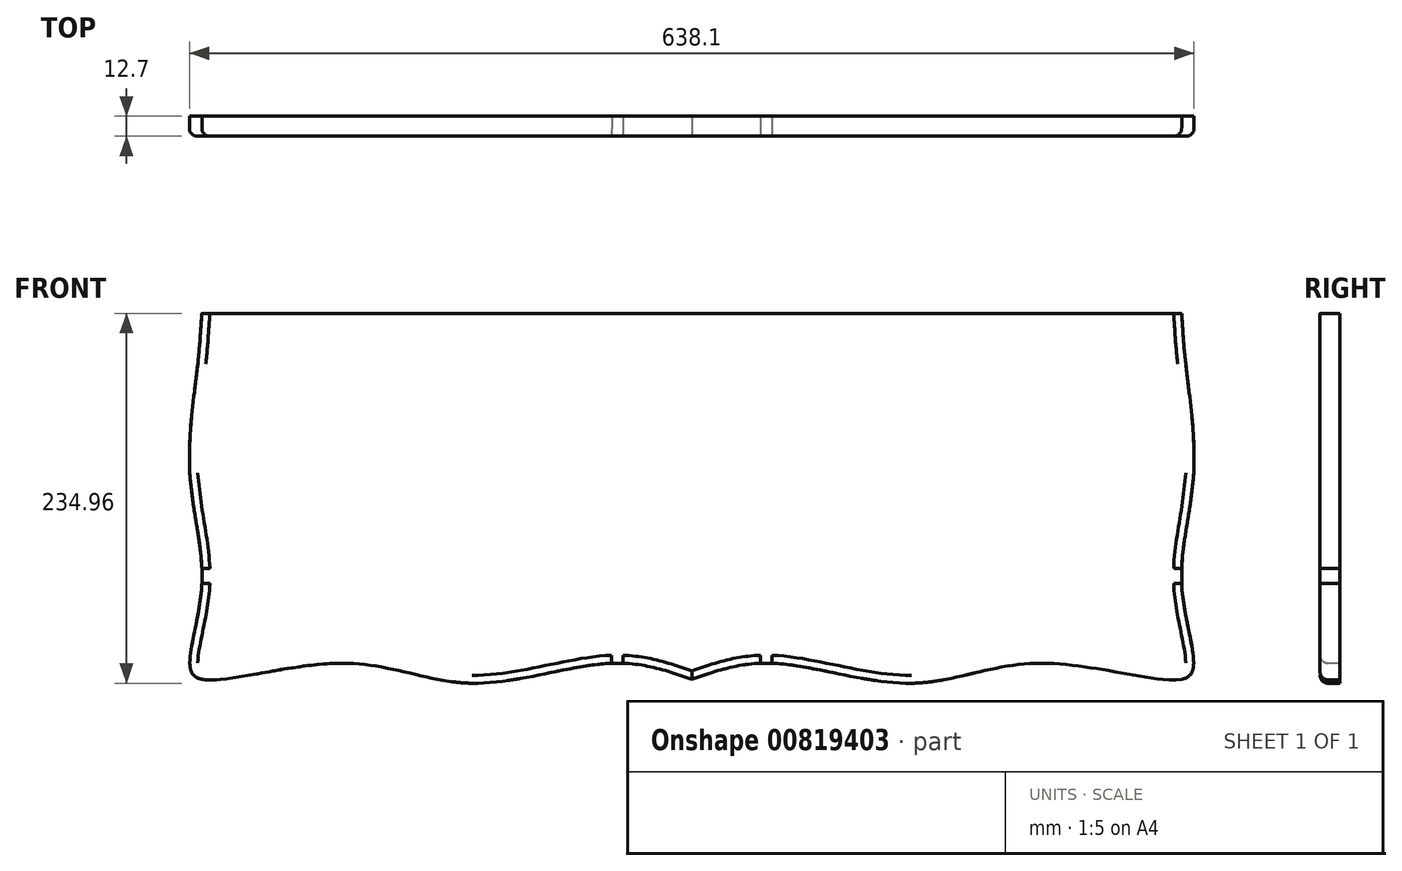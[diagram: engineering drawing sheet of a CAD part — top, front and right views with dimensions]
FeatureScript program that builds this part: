
annotation { "Feature Type Name" : "Feature", "Feature Type Description" : "" }
export const myFeature = defineFeature(function(context is Context, id is Id, definition is map)
    precondition{}
    {
        {
            var Q0;
            Q0=qCreatedBy(makeId("Front.planeOp"),FACE);
            var sketch = newSketch(context, id + "F0", { "sketchPlane" : qUnion([Q0])});
            skLineSegment(sketch, "E0.bottom", {"start": v(-290.57, 108.48) * mm, "end": v(331.73, 108.48) * mm});
            skLineSegment(sketch, "E0.top", {"start": v(-290.57, -113.77) * mm, "end": v(331.73, -113.77) * mm});
            skLineSegment(sketch, "E0.left", {"start": v(-290.57, 108.48) * mm, "end": v(-290.57, -113.77) * mm});
            skLineSegment(sketch, "E0.right", {"start": v(331.73, 108.48) * mm, "end": v(331.73, -113.77) * mm});
            skPoint(sketch, "E1", {"position": v(20.58, 108.48) * mm});
            skSolve(sketch);
        }
        {
            var Q0;
            Q0=makeQuery(id+"F0.imprint","IMPRINT",FACE,{"disambiguationData":[TD([[makeQuery(id+"F0.imprint","IMPRINT",EDGE,{"derivedFrom":sQuery(id+"F0.wireOp",EDGE,"E0.bottom")}),-1.0]])]});
            extrude(context, id + "F1", {"entities" : qUnion([Q0]), "depth" : 12.7 * mm, "offsetDistance" : 25.4 * mm});
        }
        {
            var Q0;
            Q0=makeQuery(id+"F1.opExtrude","CAP_FACE",FACE,{"disambiguationData":[OSD([sQuery(id+"F0.wireOp",EDGE,"E0.bottom"),sQuery(id+"F0.wireOp",EDGE,"E0.top"),sQuery(id+"F0.wireOp",EDGE,"E0.left"),sQuery(id+"F0.wireOp",EDGE,"E0.right")])],"isStart":false});
            var sketch = newSketch(context, id + "F2", { "sketchPlane" : qUnion([Q0])});
            skText(sketch, "E2", { "text": "Swimming", "fontName": "OpenSans-Bold.ttf"});
            skPoint(sketch, "E3", {"position": v(20.58, 108.48) * mm});
            const initialGuessF2  = {"E2": [-0.19905, 0.00392, 1, 0, 0.06017]};
            skSetInitialGuess(sketch, initialGuessF2);
            skSolve(sketch);
        }
        {
            var Q0;
            Q0=makeQuery(id+"F2.imprint","IMPRINT",FACE,{"disambiguationData":[TD([[makeQuery(id+"F2.imprint","IMPRINT",EDGE,{"derivedFrom":sQuery(id+"F2.wireOp",EDGE,"E2.sketch_text.stroke-0")}),1.0]])]});
            var sketch = newSketch(context, id + "F3", { "sketchPlane" : qUnion([Q0])});
            skText(sketch, "E4", { "text": " < silhouette >", "fontName": "OpenSans-Bold.ttf"});
            skPoint(sketch, "E5", {"position": v(20.58, -113.77) * mm});
            const initialGuessF3  = {"E4": [-0.15546, -0.06206, 1, 0, 0.03604]};
            skSetInitialGuess(sketch, initialGuessF3);
            skSolve(sketch);
        }
        {
            var Q0;
            {var subQ0=sQuery(id+"F0.wireOp",EDGE,"E0.right");var subQ1=sQuery(id+"F0.wireOp",EDGE,"E0.bottom");var subQ2=sQuery(id+"F0.wireOp",EDGE,"E0.left");var subQ3=sQuery(id+"F0.wireOp",EDGE,"E0.top");Q0=makeQuery(id+"FjgwLtvUwF4HY63_1.boolean.opBoolean","SPLIT",FACE,{"disambiguationData":[TD([makeQuery(id+"F1.opExtrude","SWEPT_FACE",FACE,{"disambiguationData":[OSD([subQ1])]})])],"derivedFrom":makeQuery(id+"F1.opExtrude","CAP_FACE",FACE,{"disambiguationData":[OSD([subQ1,subQ3,subQ2,subQ0])],"isStart":false})});}
            var sketch = newSketch(context, id + "F4", { "sketchPlane" : qUnion([Q0])});
            skPoint(sketch, "E6", {"position": v(-290.57, -62.97) * mm});
            skPoint(sketch, "E7", {"position": v(-290.57, 6.88) * mm});
            skPoint(sketch, "E8", {"position": v(-290.57, 76.73) * mm});
            skLineSegment(sketch, "E9", {"start": v(-290.57, 76.73) * mm, "end": v(-293.1, 76.73) * mm});
            skLineSegment(sketch, "E10", {"start": v(-290.57, 6.88) * mm, "end": v(-298.19, 6.88) * mm});
            skLineSegment(sketch, "E11", {"start": v(-290.57, -113.77) * mm, "end": v(-298.19, -113.77) * mm});
            skLineSegment(sketch, "E12", {"start": v(-290.57, -113.77) * mm, "end": v(-290.57, -123.93) * mm});
            skPoint(sketch, "E13", {"position": v(-201.67, -113.77) * mm});
            skPoint(sketch, "E14", {"position": v(20.58, -113.77) * mm});
            skPoint(sketch, "E15", {"position": v(-30.22, -113.77) * mm});
            skPoint(sketch, "E16", {"position": v(-119.12, -113.77) * mm});
            skPoint(sketch, "E17", {"position": v(71.38, -113.77) * mm});
            skPoint(sketch, "E18", {"position": v(160.28, -113.77) * mm});
            skPoint(sketch, "E19", {"position": v(242.83, -113.77) * mm});
            skPoint(sketch, "E20", {"position": v(331.73, -62.97) * mm});
            skPoint(sketch, "E21", {"position": v(331.73, 6.88) * mm});
            skPoint(sketch, "E22", {"position": v(331.73, 76.73) * mm});
            skLineSegment(sketch, "E23", {"start": v(331.73, 76.73) * mm, "end": v(334.27, 76.73) * mm});
            skLineSegment(sketch, "E24", {"start": v(331.73, 6.88) * mm, "end": v(339.35, 6.88) * mm});
            skLineSegment(sketch, "E25", {"start": v(331.73, -113.77) * mm, "end": v(339.35, -113.77) * mm});
            skLineSegment(sketch, "E26", {"start": v(331.73, -113.77) * mm, "end": v(331.73, -123.93) * mm});
            skLineSegment(sketch, "E27", {"start": v(-119.12, -113.77) * mm, "end": v(-119.12, -126.47) * mm});
            skLineSegment(sketch, "E28", {"start": v(20.58, -113.77) * mm, "end": v(20.58, -123.93) * mm});
            skLineSegment(sketch, "E29", {"start": v(160.28, -113.77) * mm, "end": v(160.28, -126.47) * mm});
            skFitSpline(sketch, "E30", {"points": [v(-290.57, 108.48) * mm, v(-293.1, 76.73) * mm, v(-298.19, 6.88) * mm, v(-290.57, -62.97) * mm, v(-298.19, -113.77) * mm, v(-290.57, -123.93) * mm, v(-201.67, -113.77) * mm, v(-119.12, -126.47) * mm, v(-30.22, -113.77) * mm, v(20.58, -123.93) * mm], "startDerivative": vector(-26.2, -341.82) * mm, "endDerivative": vector(438.15, -148.5) * mm});
            skFitSpline(sketch, "E31", {"points": [v(331.73, 108.48) * mm, v(334.27, 76.73) * mm, v(339.35, 6.88) * mm, v(331.73, -62.97) * mm, v(339.35, -113.77) * mm, v(331.73, -123.93) * mm, v(242.83, -113.77) * mm, v(160.28, -126.47) * mm, v(71.38, -113.77) * mm, v(20.58, -123.93) * mm], "startDerivative": vector(26.2, -341.82) * mm, "endDerivative": vector(-438.15, -148.5) * mm});
            skSolve(sketch);
        }
        {
            var Q0;
            {var subQ0=sQuery(id+"F4.wireOp",EDGE,"E28");Q0=makeQuery(id+"F4.imprint","IMPRINT",FACE,{"disambiguationData":[TD([[makeQuery(id+"F4.imprint","IMPRINT",EDGE,{"derivedFrom":subQ0}),-1.0]])]});}
            var Q1;
            {var subQ0=sQuery(id+"F4.wireOp",EDGE,"E28");Q1=makeQuery(id+"F4.imprint","IMPRINT",FACE,{"disambiguationData":[TD([[makeQuery(id+"F4.imprint","IMPRINT",EDGE,{"derivedFrom":subQ0}),1.0]])]});}
            var Q2;
            {var subQ0=sQuery(id+"F4.wireOp",EDGE,"E27");Q2=makeQuery(id+"F4.imprint","IMPRINT",FACE,{"disambiguationData":[TD([[makeQuery(id+"F4.imprint","IMPRINT",EDGE,{"derivedFrom":subQ0}),1.0]])]});}
            var Q3;
            {var subQ0=sQuery(id+"F4.wireOp",EDGE,"E27");Q3=makeQuery(id+"F4.imprint","IMPRINT",FACE,{"disambiguationData":[TD([[makeQuery(id+"F4.imprint","IMPRINT",EDGE,{"derivedFrom":subQ0}),-1.0]])]});}
            var Q4;
            {var subQ0=sQuery(id+"F4.wireOp",EDGE,"E12");Q4=makeQuery(id+"F4.imprint","IMPRINT",FACE,{"disambiguationData":[TD([[makeQuery(id+"F4.imprint","IMPRINT",EDGE,{"derivedFrom":subQ0}),1.0]])]});}
            var Q5;
            {var subQ0=sQuery(id+"F4.wireOp",EDGE,"E11");Q5=makeQuery(id+"F4.imprint","IMPRINT",FACE,{"disambiguationData":[TD([[makeQuery(id+"F4.imprint","IMPRINT",EDGE,{"derivedFrom":subQ0}),1.0]])]});}
            var Q6;
            {var subQ0=sQuery(id+"F4.wireOp",EDGE,"E11");Q6=makeQuery(id+"F4.imprint","IMPRINT",FACE,{"disambiguationData":[TD([[makeQuery(id+"F4.imprint","IMPRINT",EDGE,{"derivedFrom":subQ0}),-1.0]])]});}
            var Q7;
            {var subQ0=sQuery(id+"F4.wireOp",EDGE,"E10");Q7=makeQuery(id+"F4.imprint","IMPRINT",FACE,{"disambiguationData":[TD([[makeQuery(id+"F4.imprint","IMPRINT",EDGE,{"derivedFrom":subQ0}),1.0]])]});}
            var Q8;
            {var subQ0=sQuery(id+"F4.wireOp",EDGE,"E9");Q8=makeQuery(id+"F4.imprint","IMPRINT",FACE,{"disambiguationData":[TD([[makeQuery(id+"F4.imprint","IMPRINT",EDGE,{"derivedFrom":subQ0}),1.0]])]});}
            var Q9;
            {var subQ0=makeQuery(id+"F1.opExtrude","CAP_EDGE",EDGE,{"disambiguationData":[OSD([sQuery(id+"F0.wireOp",EDGE,"E0.bottom")])],"isStart":false});Q9=makeQuery(id+"F4.imprint","IMPRINT",FACE,{"disambiguationData":[TD([[makeQuery(id+"F4.imprint","IMPRINT",EDGE,{"derivedFrom":subQ0}),-1.0]])]});}
            var Q10;
            {var subQ0=sQuery(id+"F4.wireOp",EDGE,"E29");Q10=makeQuery(id+"F4.imprint","IMPRINT",FACE,{"disambiguationData":[TD([[makeQuery(id+"F4.imprint","IMPRINT",EDGE,{"derivedFrom":subQ0}),-1.0]])]});}
            var Q11;
            {var subQ0=sQuery(id+"F4.wireOp",EDGE,"E29");Q11=makeQuery(id+"F4.imprint","IMPRINT",FACE,{"disambiguationData":[TD([[makeQuery(id+"F4.imprint","IMPRINT",EDGE,{"derivedFrom":subQ0}),1.0]])]});}
            var Q12;
            {var subQ0=sQuery(id+"F4.wireOp",EDGE,"E26");Q12=makeQuery(id+"F4.imprint","IMPRINT",FACE,{"disambiguationData":[TD([[makeQuery(id+"F4.imprint","IMPRINT",EDGE,{"derivedFrom":subQ0}),-1.0]])]});}
            var Q13;
            {var subQ0=sQuery(id+"F4.wireOp",EDGE,"E25");Q13=makeQuery(id+"F4.imprint","IMPRINT",FACE,{"disambiguationData":[TD([[makeQuery(id+"F4.imprint","IMPRINT",EDGE,{"derivedFrom":subQ0}),-1.0]])]});}
            var Q14;
            {var subQ0=sQuery(id+"F4.wireOp",EDGE,"E25");Q14=makeQuery(id+"F4.imprint","IMPRINT",FACE,{"disambiguationData":[TD([[makeQuery(id+"F4.imprint","IMPRINT",EDGE,{"derivedFrom":subQ0}),1.0]])]});}
            var Q15;
            {var subQ0=sQuery(id+"F4.wireOp",EDGE,"E24");Q15=makeQuery(id+"F4.imprint","IMPRINT",FACE,{"disambiguationData":[TD([[makeQuery(id+"F4.imprint","IMPRINT",EDGE,{"derivedFrom":subQ0}),-1.0]])]});}
            var Q16;
            {var subQ0=sQuery(id+"F4.wireOp",EDGE,"E23");Q16=makeQuery(id+"F4.imprint","IMPRINT",FACE,{"disambiguationData":[TD([[makeQuery(id+"F4.imprint","IMPRINT",EDGE,{"derivedFrom":subQ0}),-1.0]])]});}
            var Q17;
            {var subQ0=sQuery(id+"F4.wireOp",EDGE,"E23");Q17=makeQuery(id+"F4.imprint","IMPRINT",FACE,{"disambiguationData":[TD([[makeQuery(id+"F4.imprint","IMPRINT",EDGE,{"derivedFrom":subQ0}),1.0]])]});}
            var Q18;
            {var subQ0=sQuery(id+"F4.wireOp",EDGE,"E9");Q18=makeQuery(id+"F4.imprint","IMPRINT",FACE,{"disambiguationData":[TD([[makeQuery(id+"F4.imprint","IMPRINT",EDGE,{"derivedFrom":subQ0}),-1.0]])]});}
            extrude(context, id + "F5", {"entities" : qUnion([Q0, Q1, Q2, Q3, Q4, Q5, Q6, Q7, Q8, Q9, Q10, Q11, Q12, Q13, Q14, Q15, Q16, Q17, Q18]), "operationType" : NewBodyOperationType.ADD, "depth" : -12.7 * mm, "offsetDistance" : 25.4 * mm});
        }
        {
            var Q0;
            {var subQ0=sQuery(id+"F4.wireOp",EDGE,"8007402e-1a4e-4a06-85a5-2af08e553504");var subQ1=sQuery(id+"F0.wireOp",EDGE,"E0.left");var subQ2=sQuery(id+"F0.wireOp",EDGE,"E0.top");var subQ3=sQuery(id+"F0.wireOp",EDGE,"E0.bottom");Q0=makeQuery(id+"F5.boolean.opBoolean","SPLIT",EDGE,{"disambiguationData":[TD([makeQuery(id+"F1.opExtrude","CAP_FACE",FACE,{"disambiguationData":[OSD([subQ3,subQ2,subQ1,sQuery(id+"F0.wireOp",EDGE,"E0.right")])],"isStart":false}),makeQuery(id+"F1.opExtrude","SWEPT_FACE",FACE,{"disambiguationData":[OSD([subQ2])]}),makeQuery(id+"F1.opExtrude","SWEPT_FACE",FACE,{"disambiguationData":[OSD([subQ1])]}),makeQuery(id+"F5.opExtrude","SWEPT_FACE",FACE,{"disambiguationData":[OSD([subQ0])]}),makeQuery(id+"F5.opExtrude","CAP_FACE",FACE,{"disambiguationData":[OSD([subQ3,sQuery(id+"F2.wireOp",EDGE,"E2.sketch_text.stroke-0"),sQuery(id+"F2.wireOp",EDGE,"E2.sketch_text.stroke-1"),sQuery(id+"F2.wireOp",EDGE,"E2.sketch_text.stroke-2"),sQuery(id+"F2.wireOp",EDGE,"E2.sketch_text.stroke-3"),sQuery(id+"F2.wireOp",EDGE,"E2.sketch_text.stroke-4"),sQuery(id+"F2.wireOp",EDGE,"E2.sketch_text.stroke-5"),sQuery(id+"F2.wireOp",EDGE,"E2.sketch_text.stroke-6"),sQuery(id+"F2.wireOp",EDGE,"E2.sketch_text.stroke-7"),sQuery(id+"F2.wireOp",EDGE,"E2.sketch_text.stroke-8"),sQuery(id+"F2.wireOp",EDGE,"E2.sketch_text.stroke-9"),sQuery(id+"F2.wireOp",EDGE,"E2.sketch_text.stroke-10"),sQuery(id+"F2.wireOp",EDGE,"E2.sketch_text.stroke-11"),sQuery(id+"F2.wireOp",EDGE,"E2.sketch_text.stroke-12"),sQuery(id+"F2.wireOp",EDGE,"E2.sketch_text.stroke-13"),sQuery(id+"F2.wireOp",EDGE,"E2.sketch_text.stroke-14"),sQuery(id+"F2.wireOp",EDGE,"E2.sketch_text.stroke-15"),sQuery(id+"F2.wireOp",EDGE,"E2.sketch_text.stroke-16"),sQuery(id+"F2.wireOp",EDGE,"E2.sketch_text.stroke-17"),sQuery(id+"F2.wireOp",EDGE,"E2.sketch_text.stroke-18"),sQuery(id+"F2.wireOp",EDGE,"E2.sketch_text.stroke-19"),sQuery(id+"F2.wireOp",EDGE,"E2.sketch_text.stroke-20"),sQuery(id+"F2.wireOp",EDGE,"E2.sketch_text.stroke-21"),sQuery(id+"F2.wireOp",EDGE,"E2.sketch_text.stroke-22"),sQuery(id+"F2.wireOp",EDGE,"E2.sketch_text.stroke-23"),sQuery(id+"F2.wireOp",EDGE,"E2.sketch_text.stroke-24"),sQuery(id+"F2.wireOp",EDGE,"E2.sketch_text.stroke-25"),sQuery(id+"F2.wireOp",EDGE,"E2.sketch_text.stroke-26"),sQuery(id+"F2.wireOp",EDGE,"E2.sketch_text.stroke-27"),sQuery(id+"F2.wireOp",EDGE,"E2.sketch_text.stroke-28"),sQuery(id+"F2.wireOp",EDGE,"E2.sketch_text.stroke-29"),sQuery(id+"F2.wireOp",EDGE,"E2.sketch_text.stroke-30"),sQuery(id+"F2.wireOp",EDGE,"E2.sketch_text.stroke-31"),sQuery(id+"F2.wireOp",EDGE,"E2.sketch_text.stroke-32"),sQuery(id+"F2.wireOp",EDGE,"E2.sketch_text.stroke-33"),sQuery(id+"F2.wireOp",EDGE,"E2.sketch_text.stroke-34"),sQuery(id+"F2.wireOp",EDGE,"E2.sketch_text.stroke-35"),sQuery(id+"F2.wireOp",EDGE,"E2.sketch_text.stroke-36"),sQuery(id+"F2.wireOp",EDGE,"E2.sketch_text.stroke-37"),sQuery(id+"F2.wireOp",EDGE,"E2.sketch_text.stroke-38"),sQuery(id+"F2.wireOp",EDGE,"E2.sketch_text.stroke-39"),sQuery(id+"F2.wireOp",EDGE,"E2.sketch_text.stroke-40"),sQuery(id+"F2.wireOp",EDGE,"E2.sketch_text.stroke-41"),sQuery(id+"F2.wireOp",EDGE,"E2.sketch_text.stroke-42"),sQuery(id+"F2.wireOp",EDGE,"E2.sketch_text.stroke-43"),sQuery(id+"F2.wireOp",EDGE,"E2.sketch_text.stroke-44"),sQuery(id+"F2.wireOp",EDGE,"E2.sketch_text.stroke-45"),sQuery(id+"F2.wireOp",EDGE,"E2.sketch_text.stroke-46"),sQuery(id+"F2.wireOp",EDGE,"E2.sketch_text.stroke-47"),sQuery(id+"F2.wireOp",EDGE,"E2.sketch_text.stroke-48"),sQuery(id+"F2.wireOp",EDGE,"E2.sketch_text.stroke-49"),sQuery(id+"F2.wireOp",EDGE,"E2.sketch_text.stroke-50"),sQuery(id+"F2.wireOp",EDGE,"E2.sketch_text.stroke-51"),sQuery(id+"F2.wireOp",EDGE,"E2.sketch_text.stroke-52"),sQuery(id+"F2.wireOp",EDGE,"E2.sketch_text.stroke-53"),sQuery(id+"F2.wireOp",EDGE,"E2.sketch_text.stroke-54"),sQuery(id+"F2.wireOp",EDGE,"E2.sketch_text.stroke-55"),sQuery(id+"F2.wireOp",EDGE,"E2.sketch_text.stroke-56"),sQuery(id+"F2.wireOp",EDGE,"E2.sketch_text.stroke-57"),sQuery(id+"F2.wireOp",EDGE,"E2.sketch_text.stroke-58"),sQuery(id+"F2.wireOp",EDGE,"E2.sketch_text.stroke-59"),sQuery(id+"F2.wireOp",EDGE,"E2.sketch_text.stroke-60"),sQuery(id+"F2.wireOp",EDGE,"E2.sketch_text.stroke-61"),sQuery(id+"F2.wireOp",EDGE,"E2.sketch_text.stroke-62"),sQuery(id+"F2.wireOp",EDGE,"E2.sketch_text.stroke-63"),sQuery(id+"F2.wireOp",EDGE,"E2.sketch_text.stroke-64"),sQuery(id+"F2.wireOp",EDGE,"E2.sketch_text.stroke-65"),sQuery(id+"F2.wireOp",EDGE,"E2.sketch_text.stroke-66"),sQuery(id+"F2.wireOp",EDGE,"E2.sketch_text.stroke-67"),sQuery(id+"F2.wireOp",EDGE,"E2.sketch_text.stroke-68"),sQuery(id+"F2.wireOp",EDGE,"E2.sketch_text.stroke-69"),sQuery(id+"F2.wireOp",EDGE,"E2.sketch_text.stroke-70"),sQuery(id+"F2.wireOp",EDGE,"E2.sketch_text.stroke-71"),sQuery(id+"F2.wireOp",EDGE,"E2.sketch_text.stroke-72"),sQuery(id+"F2.wireOp",EDGE,"E2.sketch_text.stroke-73"),sQuery(id+"F2.wireOp",EDGE,"E2.sketch_text.stroke-74"),sQuery(id+"F2.wireOp",EDGE,"E2.sketch_text.stroke-75"),sQuery(id+"F2.wireOp",EDGE,"E2.sketch_text.stroke-76"),sQuery(id+"F2.wireOp",EDGE,"E2.sketch_text.stroke-77"),sQuery(id+"F2.wireOp",EDGE,"E2.sketch_text.stroke-78"),sQuery(id+"F2.wireOp",EDGE,"E2.sketch_text.stroke-79"),sQuery(id+"F2.wireOp",EDGE,"E2.sketch_text.stroke-80"),sQuery(id+"F2.wireOp",EDGE,"E2.sketch_text.stroke-81"),sQuery(id+"F2.wireOp",EDGE,"E2.sketch_text.stroke-82"),sQuery(id+"F2.wireOp",EDGE,"E2.sketch_text.stroke-83"),sQuery(id+"F2.wireOp",EDGE,"E2.sketch_text.stroke-84"),sQuery(id+"F2.wireOp",EDGE,"E2.sketch_text.stroke-85"),sQuery(id+"F2.wireOp",EDGE,"E2.sketch_text.stroke-86"),sQuery(id+"F2.wireOp",EDGE,"E2.sketch_text.stroke-87"),sQuery(id+"F2.wireOp",EDGE,"E2.sketch_text.stroke-88"),sQuery(id+"F2.wireOp",EDGE,"E2.sketch_text.stroke-89"),sQuery(id+"F2.wireOp",EDGE,"E2.sketch_text.stroke-90"),sQuery(id+"F2.wireOp",EDGE,"E2.sketch_text.stroke-91"),sQuery(id+"F2.wireOp",EDGE,"E2.sketch_text.stroke-92"),sQuery(id+"F2.wireOp",EDGE,"E2.sketch_text.stroke-93"),sQuery(id+"F2.wireOp",EDGE,"E2.sketch_text.stroke-94"),sQuery(id+"F2.wireOp",EDGE,"E2.sketch_text.stroke-95"),sQuery(id+"F2.wireOp",EDGE,"E2.sketch_text.stroke-96"),sQuery(id+"F2.wireOp",EDGE,"E2.sketch_text.stroke-97"),sQuery(id+"F2.wireOp",EDGE,"E2.sketch_text.stroke-98"),sQuery(id+"F2.wireOp",EDGE,"E2.sketch_text.stroke-99"),sQuery(id+"F2.wireOp",EDGE,"E2.sketch_text.stroke-100"),sQuery(id+"F2.wireOp",EDGE,"E2.sketch_text.stroke-101"),sQuery(id+"F2.wireOp",EDGE,"E2.sketch_text.stroke-102"),sQuery(id+"F2.wireOp",EDGE,"E2.sketch_text.stroke-103"),sQuery(id+"F2.wireOp",EDGE,"E2.sketch_text.stroke-104"),sQuery(id+"F2.wireOp",EDGE,"E2.sketch_text.stroke-105"),sQuery(id+"F2.wireOp",EDGE,"E2.sketch_text.stroke-106"),sQuery(id+"F2.wireOp",EDGE,"E2.sketch_text.stroke-107"),sQuery(id+"F2.wireOp",EDGE,"E2.sketch_text.stroke-108"),sQuery(id+"F2.wireOp",EDGE,"E2.sketch_text.stroke-109"),sQuery(id+"F2.wireOp",EDGE,"E2.sketch_text.stroke-110"),sQuery(id+"F2.wireOp",EDGE,"E2.sketch_text.stroke-111"),sQuery(id+"F2.wireOp",EDGE,"E2.sketch_text.stroke-112"),sQuery(id+"F2.wireOp",EDGE,"E2.sketch_text.stroke-113"),sQuery(id+"F2.wireOp",EDGE,"E2.sketch_text.stroke-114"),sQuery(id+"F2.wireOp",EDGE,"E2.sketch_text.stroke-115"),sQuery(id+"F2.wireOp",EDGE,"E2.sketch_text.stroke-116"),sQuery(id+"F2.wireOp",EDGE,"E2.sketch_text.stroke-117"),sQuery(id+"F2.wireOp",EDGE,"E2.sketch_text.stroke-118"),sQuery(id+"F2.wireOp",EDGE,"E2.sketch_text.stroke-119"),sQuery(id+"F2.wireOp",EDGE,"E2.sketch_text.stroke-120"),sQuery(id+"F2.wireOp",EDGE,"E2.sketch_text.stroke-121"),sQuery(id+"F2.wireOp",EDGE,"E2.sketch_text.stroke-122"),sQuery(id+"F2.wireOp",EDGE,"E2.sketch_text.stroke-123"),sQuery(id+"F2.wireOp",EDGE,"E2.sketch_text.stroke-124"),sQuery(id+"F2.wireOp",EDGE,"E2.sketch_text.stroke-125"),sQuery(id+"F2.wireOp",EDGE,"E2.sketch_text.stroke-126"),sQuery(id+"F2.wireOp",EDGE,"E2.sketch_text.stroke-127"),sQuery(id+"F2.wireOp",EDGE,"E2.sketch_text.stroke-128"),sQuery(id+"F2.wireOp",EDGE,"E2.sketch_text.stroke-129"),sQuery(id+"F2.wireOp",EDGE,"E2.sketch_text.stroke-130"),sQuery(id+"F2.wireOp",EDGE,"E2.sketch_text.stroke-131"),sQuery(id+"F2.wireOp",EDGE,"E2.sketch_text.stroke-132"),sQuery(id+"F2.wireOp",EDGE,"E2.sketch_text.stroke-133"),sQuery(id+"F2.wireOp",EDGE,"E2.sketch_text.stroke-134"),sQuery(id+"F2.wireOp",EDGE,"E2.sketch_text.stroke-135"),sQuery(id+"F2.wireOp",EDGE,"E2.sketch_text.stroke-136"),sQuery(id+"F2.wireOp",EDGE,"E2.sketch_text.stroke-137"),sQuery(id+"F2.wireOp",EDGE,"E2.sketch_text.stroke-138"),sQuery(id+"F2.wireOp",EDGE,"E2.sketch_text.stroke-139"),sQuery(id+"F2.wireOp",EDGE,"E2.sketch_text.stroke-140"),sQuery(id+"F2.wireOp",EDGE,"E2.sketch_text.stroke-141"),sQuery(id+"F2.wireOp",EDGE,"E2.sketch_text.stroke-142"),sQuery(id+"F2.wireOp",EDGE,"E2.sketch_text.stroke-143"),sQuery(id+"F2.wireOp",EDGE,"E2.sketch_text.stroke-144"),sQuery(id+"F2.wireOp",EDGE,"E2.sketch_text.stroke-145"),sQuery(id+"F2.wireOp",EDGE,"E2.sketch_text.stroke-146"),sQuery(id+"F2.wireOp",EDGE,"E2.sketch_text.stroke-147"),sQuery(id+"F2.wireOp",EDGE,"E2.sketch_text.stroke-148"),sQuery(id+"F2.wireOp",EDGE,"E2.sketch_text.stroke-149"),sQuery(id+"F2.wireOp",EDGE,"E2.sketch_text.stroke-150"),sQuery(id+"F2.wireOp",EDGE,"E2.sketch_text.stroke-151"),sQuery(id+"F2.wireOp",EDGE,"E2.sketch_text.stroke-152"),sQuery(id+"F2.wireOp",EDGE,"E2.sketch_text.stroke-153"),sQuery(id+"F2.wireOp",EDGE,"E2.sketch_text.stroke-154"),sQuery(id+"F2.wireOp",EDGE,"E2.sketch_text.stroke-155"),sQuery(id+"F2.wireOp",EDGE,"E2.sketch_text.stroke-156"),sQuery(id+"F2.wireOp",EDGE,"E2.sketch_text.stroke-157"),sQuery(id+"F2.wireOp",EDGE,"E2.sketch_text.stroke-158"),sQuery(id+"F2.wireOp",EDGE,"E2.sketch_text.stroke-159"),sQuery(id+"F2.wireOp",EDGE,"E2.sketch_text.stroke-160"),sQuery(id+"F2.wireOp",EDGE,"E2.sketch_text.stroke-161"),sQuery(id+"F2.wireOp",EDGE,"E2.sketch_text.stroke-162"),sQuery(id+"F2.wireOp",EDGE,"E2.sketch_text.stroke-163"),sQuery(id+"F2.wireOp",EDGE,"E2.sketch_text.stroke-164"),sQuery(id+"F2.wireOp",EDGE,"E2.sketch_text.stroke-165"),sQuery(id+"F2.wireOp",EDGE,"E2.sketch_text.stroke-166"),sQuery(id+"F2.wireOp",EDGE,"E2.sketch_text.stroke-167"),sQuery(id+"F2.wireOp",EDGE,"E2.sketch_text.stroke-168"),sQuery(id+"F2.wireOp",EDGE,"E2.sketch_text.stroke-169"),sQuery(id+"F2.wireOp",EDGE,"E2.sketch_text.stroke-170"),sQuery(id+"F2.wireOp",EDGE,"E2.sketch_text.stroke-171"),sQuery(id+"F2.wireOp",EDGE,"E2.sketch_text.stroke-172"),sQuery(id+"F2.wireOp",EDGE,"E2.sketch_text.stroke-173"),sQuery(id+"F3.wireOp",EDGE,"E4.sketch_text.stroke-0"),sQuery(id+"F3.wireOp",EDGE,"E4.sketch_text.stroke-1"),sQuery(id+"F3.wireOp",EDGE,"E4.sketch_text.stroke-2"),sQuery(id+"F3.wireOp",EDGE,"E4.sketch_text.stroke-3"),sQuery(id+"F3.wireOp",EDGE,"E4.sketch_text.stroke-4"),sQuery(id+"F3.wireOp",EDGE,"E4.sketch_text.stroke-5"),sQuery(id+"F3.wireOp",EDGE,"E4.sketch_text.stroke-6"),sQuery(id+"F3.wireOp",EDGE,"E4.sketch_text.stroke-7"),sQuery(id+"F3.wireOp",EDGE,"E4.sketch_text.stroke-8"),sQuery(id+"F3.wireOp",EDGE,"E4.sketch_text.stroke-9"),sQuery(id+"F3.wireOp",EDGE,"E4.sketch_text.stroke-10"),sQuery(id+"F3.wireOp",EDGE,"E4.sketch_text.stroke-11"),sQuery(id+"F3.wireOp",EDGE,"E4.sketch_text.stroke-12"),sQuery(id+"F3.wireOp",EDGE,"E4.sketch_text.stroke-13"),sQuery(id+"F3.wireOp",EDGE,"E4.sketch_text.stroke-14"),sQuery(id+"F3.wireOp",EDGE,"E4.sketch_text.stroke-15"),sQuery(id+"F3.wireOp",EDGE,"E4.sketch_text.stroke-16"),sQuery(id+"F3.wireOp",EDGE,"E4.sketch_text.stroke-17"),sQuery(id+"F3.wireOp",EDGE,"E4.sketch_text.stroke-18"),sQuery(id+"F3.wireOp",EDGE,"E4.sketch_text.stroke-19"),sQuery(id+"F3.wireOp",EDGE,"E4.sketch_text.stroke-20"),sQuery(id+"F3.wireOp",EDGE,"E4.sketch_text.stroke-21"),sQuery(id+"F3.wireOp",EDGE,"E4.sketch_text.stroke-22"),sQuery(id+"F3.wireOp",EDGE,"E4.sketch_text.stroke-23"),sQuery(id+"F3.wireOp",EDGE,"E4.sketch_text.stroke-24"),sQuery(id+"F3.wireOp",EDGE,"E4.sketch_text.stroke-25"),sQuery(id+"F3.wireOp",EDGE,"E4.sketch_text.stroke-26"),sQuery(id+"F3.wireOp",EDGE,"E4.sketch_text.stroke-27"),sQuery(id+"F3.wireOp",EDGE,"E4.sketch_text.stroke-28"),sQuery(id+"F3.wireOp",EDGE,"E4.sketch_text.stroke-29"),sQuery(id+"F3.wireOp",EDGE,"E4.sketch_text.stroke-30"),sQuery(id+"F3.wireOp",EDGE,"E4.sketch_text.stroke-31"),sQuery(id+"F3.wireOp",EDGE,"E4.sketch_text.stroke-32"),sQuery(id+"F3.wireOp",EDGE,"E4.sketch_text.stroke-33"),sQuery(id+"F3.wireOp",EDGE,"E4.sketch_text.stroke-34"),sQuery(id+"F3.wireOp",EDGE,"E4.sketch_text.stroke-35"),sQuery(id+"F3.wireOp",EDGE,"E4.sketch_text.stroke-36"),sQuery(id+"F3.wireOp",EDGE,"E4.sketch_text.stroke-37"),sQuery(id+"F3.wireOp",EDGE,"E4.sketch_text.stroke-38"),sQuery(id+"F3.wireOp",EDGE,"E4.sketch_text.stroke-39"),sQuery(id+"F3.wireOp",EDGE,"E4.sketch_text.stroke-40"),sQuery(id+"F3.wireOp",EDGE,"E4.sketch_text.stroke-41"),sQuery(id+"F3.wireOp",EDGE,"E4.sketch_text.stroke-42"),sQuery(id+"F3.wireOp",EDGE,"E4.sketch_text.stroke-43"),sQuery(id+"F3.wireOp",EDGE,"E4.sketch_text.stroke-44"),sQuery(id+"F3.wireOp",EDGE,"E4.sketch_text.stroke-45"),sQuery(id+"F3.wireOp",EDGE,"E4.sketch_text.stroke-46"),sQuery(id+"F3.wireOp",EDGE,"E4.sketch_text.stroke-47"),sQuery(id+"F3.wireOp",EDGE,"E4.sketch_text.stroke-48"),sQuery(id+"F3.wireOp",EDGE,"E4.sketch_text.stroke-49"),sQuery(id+"F3.wireOp",EDGE,"E4.sketch_text.stroke-50"),sQuery(id+"F3.wireOp",EDGE,"E4.sketch_text.stroke-51"),sQuery(id+"F3.wireOp",EDGE,"E4.sketch_text.stroke-52"),sQuery(id+"F3.wireOp",EDGE,"E4.sketch_text.stroke-53"),sQuery(id+"F3.wireOp",EDGE,"E4.sketch_text.stroke-54"),sQuery(id+"F3.wireOp",EDGE,"E4.sketch_text.stroke-55"),sQuery(id+"F3.wireOp",EDGE,"E4.sketch_text.stroke-56"),sQuery(id+"F3.wireOp",EDGE,"E4.sketch_text.stroke-57"),sQuery(id+"F3.wireOp",EDGE,"E4.sketch_text.stroke-58"),sQuery(id+"F3.wireOp",EDGE,"E4.sketch_text.stroke-59"),sQuery(id+"F3.wireOp",EDGE,"E4.sketch_text.stroke-60"),sQuery(id+"F3.wireOp",EDGE,"E4.sketch_text.stroke-61"),sQuery(id+"F3.wireOp",EDGE,"E4.sketch_text.stroke-62"),sQuery(id+"F3.wireOp",EDGE,"E4.sketch_text.stroke-71"),sQuery(id+"F3.wireOp",EDGE,"E4.sketch_text.stroke-72"),sQuery(id+"F3.wireOp",EDGE,"E4.sketch_text.stroke-73"),sQuery(id+"F3.wireOp",EDGE,"E4.sketch_text.stroke-74"),sQuery(id+"F3.wireOp",EDGE,"E4.sketch_text.stroke-75"),sQuery(id+"F3.wireOp",EDGE,"E4.sketch_text.stroke-76"),sQuery(id+"F3.wireOp",EDGE,"E4.sketch_text.stroke-77"),sQuery(id+"F3.wireOp",EDGE,"E4.sketch_text.stroke-78"),sQuery(id+"F3.wireOp",EDGE,"E4.sketch_text.stroke-79"),sQuery(id+"F3.wireOp",EDGE,"E4.sketch_text.stroke-80"),sQuery(id+"F3.wireOp",EDGE,"E4.sketch_text.stroke-81"),sQuery(id+"F3.wireOp",EDGE,"E4.sketch_text.stroke-82"),sQuery(id+"F3.wireOp",EDGE,"E4.sketch_text.stroke-83"),sQuery(id+"F3.wireOp",EDGE,"E4.sketch_text.stroke-84"),sQuery(id+"F3.wireOp",EDGE,"E4.sketch_text.stroke-85"),sQuery(id+"F3.wireOp",EDGE,"E4.sketch_text.stroke-86"),sQuery(id+"F3.wireOp",EDGE,"E4.sketch_text.stroke-87"),sQuery(id+"F3.wireOp",EDGE,"E4.sketch_text.stroke-88"),sQuery(id+"F3.wireOp",EDGE,"E4.sketch_text.stroke-89"),sQuery(id+"F3.wireOp",EDGE,"E4.sketch_text.stroke-90"),sQuery(id+"F3.wireOp",EDGE,"E4.sketch_text.stroke-91"),sQuery(id+"F3.wireOp",EDGE,"E4.sketch_text.stroke-92"),sQuery(id+"F3.wireOp",EDGE,"E4.sketch_text.stroke-93"),sQuery(id+"F3.wireOp",EDGE,"E4.sketch_text.stroke-94"),sQuery(id+"F3.wireOp",EDGE,"E4.sketch_text.stroke-95"),sQuery(id+"F3.wireOp",EDGE,"E4.sketch_text.stroke-96"),sQuery(id+"F3.wireOp",EDGE,"E4.sketch_text.stroke-97"),sQuery(id+"F3.wireOp",EDGE,"E4.sketch_text.stroke-103"),sQuery(id+"F3.wireOp",EDGE,"E4.sketch_text.stroke-104"),sQuery(id+"F3.wireOp",EDGE,"E4.sketch_text.stroke-105"),sQuery(id+"F3.wireOp",EDGE,"E4.sketch_text.stroke-106"),sQuery(id+"F3.wireOp",EDGE,"E4.sketch_text.stroke-107"),sQuery(id+"F3.wireOp",EDGE,"E4.sketch_text.stroke-108"),sQuery(id+"F3.wireOp",EDGE,"E4.sketch_text.stroke-109"),sQuery(id+"F3.wireOp",EDGE,"E4.sketch_text.stroke-110"),sQuery(id+"F3.wireOp",EDGE,"E4.sketch_text.stroke-111"),sQuery(id+"F3.wireOp",EDGE,"E4.sketch_text.stroke-112"),sQuery(id+"F3.wireOp",EDGE,"E4.sketch_text.stroke-113"),sQuery(id+"F3.wireOp",EDGE,"E4.sketch_text.stroke-114"),sQuery(id+"F3.wireOp",EDGE,"E4.sketch_text.stroke-115"),sQuery(id+"F3.wireOp",EDGE,"E4.sketch_text.stroke-116"),sQuery(id+"F3.wireOp",EDGE,"E4.sketch_text.stroke-117"),sQuery(id+"F3.wireOp",EDGE,"E4.sketch_text.stroke-118"),sQuery(id+"F3.wireOp",EDGE,"E4.sketch_text.stroke-119"),sQuery(id+"F3.wireOp",EDGE,"E4.sketch_text.stroke-120"),sQuery(id+"F3.wireOp",EDGE,"E4.sketch_text.stroke-121"),sQuery(id+"F3.wireOp",EDGE,"E4.sketch_text.stroke-122"),sQuery(id+"F3.wireOp",EDGE,"E4.sketch_text.stroke-123"),sQuery(id+"F3.wireOp",EDGE,"E4.sketch_text.stroke-124"),sQuery(id+"F3.wireOp",EDGE,"E4.sketch_text.stroke-125"),sQuery(id+"F3.wireOp",EDGE,"E4.sketch_text.stroke-126"),sQuery(id+"F3.wireOp",EDGE,"E4.sketch_text.stroke-127"),sQuery(id+"F3.wireOp",EDGE,"E4.sketch_text.stroke-128"),sQuery(id+"F3.wireOp",EDGE,"E4.sketch_text.stroke-129"),sQuery(id+"F3.wireOp",EDGE,"E4.sketch_text.stroke-130"),sQuery(id+"F3.wireOp",EDGE,"E4.sketch_text.stroke-131"),sQuery(id+"F3.wireOp",EDGE,"E4.sketch_text.stroke-132"),sQuery(id+"F3.wireOp",EDGE,"E4.sketch_text.stroke-133"),sQuery(id+"F3.wireOp",EDGE,"E4.sketch_text.stroke-134"),sQuery(id+"F3.wireOp",EDGE,"E4.sketch_text.stroke-135"),sQuery(id+"F3.wireOp",EDGE,"E4.sketch_text.stroke-136"),sQuery(id+"F3.wireOp",EDGE,"E4.sketch_text.stroke-137"),sQuery(id+"F3.wireOp",EDGE,"E4.sketch_text.stroke-138"),sQuery(id+"F3.wireOp",EDGE,"E4.sketch_text.stroke-139"),sQuery(id+"F3.wireOp",EDGE,"E4.sketch_text.stroke-140"),sQuery(id+"F3.wireOp",EDGE,"E4.sketch_text.stroke-141"),sQuery(id+"F3.wireOp",EDGE,"E4.sketch_text.stroke-142"),sQuery(id+"F3.wireOp",EDGE,"E4.sketch_text.stroke-143"),sQuery(id+"F3.wireOp",EDGE,"E4.sketch_text.stroke-144"),sQuery(id+"F3.wireOp",EDGE,"E4.sketch_text.stroke-145"),sQuery(id+"F3.wireOp",EDGE,"E4.sketch_text.stroke-146"),sQuery(id+"F3.wireOp",EDGE,"E4.sketch_text.stroke-147"),sQuery(id+"F3.wireOp",EDGE,"E4.sketch_text.stroke-148"),sQuery(id+"F3.wireOp",EDGE,"E4.sketch_text.stroke-149"),sQuery(id+"F3.wireOp",EDGE,"E4.sketch_text.stroke-150"),sQuery(id+"F3.wireOp",EDGE,"E4.sketch_text.stroke-151"),sQuery(id+"F3.wireOp",EDGE,"E4.sketch_text.stroke-152"),sQuery(id+"F3.wireOp",EDGE,"E4.sketch_text.stroke-153"),sQuery(id+"F3.wireOp",EDGE,"E4.sketch_text.stroke-159"),sQuery(id+"F3.wireOp",EDGE,"E4.sketch_text.stroke-160"),sQuery(id+"F3.wireOp",EDGE,"E4.sketch_text.stroke-161"),sQuery(id+"F3.wireOp",EDGE,"E4.sketch_text.stroke-162"),sQuery(id+"F3.wireOp",EDGE,"E4.sketch_text.stroke-163"),sQuery(id+"F3.wireOp",EDGE,"E4.sketch_text.stroke-164"),sQuery(id+"F3.wireOp",EDGE,"E4.sketch_text.stroke-165"),sQuery(id+"F3.wireOp",EDGE,"E4.sketch_text.stroke-166"),sQuery(id+"F3.wireOp",EDGE,"E4.sketch_text.stroke-167"),sQuery(id+"F3.wireOp",EDGE,"E4.sketch_text.stroke-168"),sQuery(id+"F3.wireOp",EDGE,"E4.sketch_text.stroke-169"),sQuery(id+"F3.wireOp",EDGE,"E4.sketch_text.stroke-170"),sQuery(id+"F3.wireOp",EDGE,"E4.sketch_text.stroke-171"),sQuery(id+"F3.wireOp",EDGE,"E4.sketch_text.stroke-172"),sQuery(id+"F3.wireOp",EDGE,"E4.sketch_text.stroke-173"),sQuery(id+"F3.wireOp",EDGE,"E4.sketch_text.stroke-174"),sQuery(id+"F3.wireOp",EDGE,"E4.sketch_text.stroke-175"),sQuery(id+"F3.wireOp",EDGE,"E4.sketch_text.stroke-176"),sQuery(id+"F3.wireOp",EDGE,"E4.sketch_text.stroke-177"),sQuery(id+"F3.wireOp",EDGE,"E4.sketch_text.stroke-178"),sQuery(id+"F3.wireOp",EDGE,"E4.sketch_text.stroke-179"),sQuery(id+"F3.wireOp",EDGE,"E4.sketch_text.stroke-180"),subQ0,sQuery(id+"F4.wireOp",EDGE,"6ee83ff3-586e-4dbe-aaea-af71240543bd")])],"isStart":true})])],"derivedFrom":makeQuery(id+"F5.opExtrude","CAP_EDGE",EDGE,{"disambiguationData":[OSD([subQ0])],"isStart":true})});}
            var Q1;
            Q1=makeQuery(id+"F1.opExtrude","CAP_EDGE",EDGE,{"disambiguationData":[OSD([sQuery(id+"F0.wireOp",EDGE,"E0.left")])],"isStart":false});
            var Q2;
            {var subQ0=sQuery(id+"F0.wireOp",EDGE,"E0.top");var subQ1=sQuery(id+"F0.wireOp",EDGE,"E0.bottom");var subQ2=sQuery(id+"F4.wireOp",EDGE,"8007402e-1a4e-4a06-85a5-2af08e553504");Q2=makeQuery(id+"F5.boolean.opBoolean","SPLIT",EDGE,{"disambiguationData":[TD([makeQuery(id+"F1.opExtrude","CAP_FACE",FACE,{"disambiguationData":[OSD([subQ1,subQ0,sQuery(id+"F0.wireOp",EDGE,"E0.left"),sQuery(id+"F0.wireOp",EDGE,"E0.right")])],"isStart":false}),makeQuery(id+"F1.opExtrude","SWEPT_FACE",FACE,{"disambiguationData":[OSD([subQ0])]}),makeQuery(id+"F5.opExtrude","SWEPT_FACE",FACE,{"disambiguationData":[OSD([subQ2])]}),makeQuery(id+"F5.opExtrude","CAP_FACE",FACE,{"disambiguationData":[OSD([subQ1,sQuery(id+"F2.wireOp",EDGE,"E2.sketch_text.stroke-0"),sQuery(id+"F2.wireOp",EDGE,"E2.sketch_text.stroke-1"),sQuery(id+"F2.wireOp",EDGE,"E2.sketch_text.stroke-2"),sQuery(id+"F2.wireOp",EDGE,"E2.sketch_text.stroke-3"),sQuery(id+"F2.wireOp",EDGE,"E2.sketch_text.stroke-4"),sQuery(id+"F2.wireOp",EDGE,"E2.sketch_text.stroke-5"),sQuery(id+"F2.wireOp",EDGE,"E2.sketch_text.stroke-6"),sQuery(id+"F2.wireOp",EDGE,"E2.sketch_text.stroke-7"),sQuery(id+"F2.wireOp",EDGE,"E2.sketch_text.stroke-8"),sQuery(id+"F2.wireOp",EDGE,"E2.sketch_text.stroke-9"),sQuery(id+"F2.wireOp",EDGE,"E2.sketch_text.stroke-10"),sQuery(id+"F2.wireOp",EDGE,"E2.sketch_text.stroke-11"),sQuery(id+"F2.wireOp",EDGE,"E2.sketch_text.stroke-12"),sQuery(id+"F2.wireOp",EDGE,"E2.sketch_text.stroke-13"),sQuery(id+"F2.wireOp",EDGE,"E2.sketch_text.stroke-14"),sQuery(id+"F2.wireOp",EDGE,"E2.sketch_text.stroke-15"),sQuery(id+"F2.wireOp",EDGE,"E2.sketch_text.stroke-16"),sQuery(id+"F2.wireOp",EDGE,"E2.sketch_text.stroke-17"),sQuery(id+"F2.wireOp",EDGE,"E2.sketch_text.stroke-18"),sQuery(id+"F2.wireOp",EDGE,"E2.sketch_text.stroke-19"),sQuery(id+"F2.wireOp",EDGE,"E2.sketch_text.stroke-20"),sQuery(id+"F2.wireOp",EDGE,"E2.sketch_text.stroke-21"),sQuery(id+"F2.wireOp",EDGE,"E2.sketch_text.stroke-22"),sQuery(id+"F2.wireOp",EDGE,"E2.sketch_text.stroke-23"),sQuery(id+"F2.wireOp",EDGE,"E2.sketch_text.stroke-24"),sQuery(id+"F2.wireOp",EDGE,"E2.sketch_text.stroke-25"),sQuery(id+"F2.wireOp",EDGE,"E2.sketch_text.stroke-26"),sQuery(id+"F2.wireOp",EDGE,"E2.sketch_text.stroke-27"),sQuery(id+"F2.wireOp",EDGE,"E2.sketch_text.stroke-28"),sQuery(id+"F2.wireOp",EDGE,"E2.sketch_text.stroke-29"),sQuery(id+"F2.wireOp",EDGE,"E2.sketch_text.stroke-30"),sQuery(id+"F2.wireOp",EDGE,"E2.sketch_text.stroke-31"),sQuery(id+"F2.wireOp",EDGE,"E2.sketch_text.stroke-32"),sQuery(id+"F2.wireOp",EDGE,"E2.sketch_text.stroke-33"),sQuery(id+"F2.wireOp",EDGE,"E2.sketch_text.stroke-34"),sQuery(id+"F2.wireOp",EDGE,"E2.sketch_text.stroke-35"),sQuery(id+"F2.wireOp",EDGE,"E2.sketch_text.stroke-36"),sQuery(id+"F2.wireOp",EDGE,"E2.sketch_text.stroke-37"),sQuery(id+"F2.wireOp",EDGE,"E2.sketch_text.stroke-38"),sQuery(id+"F2.wireOp",EDGE,"E2.sketch_text.stroke-39"),sQuery(id+"F2.wireOp",EDGE,"E2.sketch_text.stroke-40"),sQuery(id+"F2.wireOp",EDGE,"E2.sketch_text.stroke-41"),sQuery(id+"F2.wireOp",EDGE,"E2.sketch_text.stroke-42"),sQuery(id+"F2.wireOp",EDGE,"E2.sketch_text.stroke-43"),sQuery(id+"F2.wireOp",EDGE,"E2.sketch_text.stroke-44"),sQuery(id+"F2.wireOp",EDGE,"E2.sketch_text.stroke-45"),sQuery(id+"F2.wireOp",EDGE,"E2.sketch_text.stroke-46"),sQuery(id+"F2.wireOp",EDGE,"E2.sketch_text.stroke-47"),sQuery(id+"F2.wireOp",EDGE,"E2.sketch_text.stroke-48"),sQuery(id+"F2.wireOp",EDGE,"E2.sketch_text.stroke-49"),sQuery(id+"F2.wireOp",EDGE,"E2.sketch_text.stroke-50"),sQuery(id+"F2.wireOp",EDGE,"E2.sketch_text.stroke-51"),sQuery(id+"F2.wireOp",EDGE,"E2.sketch_text.stroke-52"),sQuery(id+"F2.wireOp",EDGE,"E2.sketch_text.stroke-53"),sQuery(id+"F2.wireOp",EDGE,"E2.sketch_text.stroke-54"),sQuery(id+"F2.wireOp",EDGE,"E2.sketch_text.stroke-55"),sQuery(id+"F2.wireOp",EDGE,"E2.sketch_text.stroke-56"),sQuery(id+"F2.wireOp",EDGE,"E2.sketch_text.stroke-57"),sQuery(id+"F2.wireOp",EDGE,"E2.sketch_text.stroke-58"),sQuery(id+"F2.wireOp",EDGE,"E2.sketch_text.stroke-59"),sQuery(id+"F2.wireOp",EDGE,"E2.sketch_text.stroke-60"),sQuery(id+"F2.wireOp",EDGE,"E2.sketch_text.stroke-61"),sQuery(id+"F2.wireOp",EDGE,"E2.sketch_text.stroke-62"),sQuery(id+"F2.wireOp",EDGE,"E2.sketch_text.stroke-63"),sQuery(id+"F2.wireOp",EDGE,"E2.sketch_text.stroke-64"),sQuery(id+"F2.wireOp",EDGE,"E2.sketch_text.stroke-65"),sQuery(id+"F2.wireOp",EDGE,"E2.sketch_text.stroke-66"),sQuery(id+"F2.wireOp",EDGE,"E2.sketch_text.stroke-67"),sQuery(id+"F2.wireOp",EDGE,"E2.sketch_text.stroke-68"),sQuery(id+"F2.wireOp",EDGE,"E2.sketch_text.stroke-69"),sQuery(id+"F2.wireOp",EDGE,"E2.sketch_text.stroke-70"),sQuery(id+"F2.wireOp",EDGE,"E2.sketch_text.stroke-71"),sQuery(id+"F2.wireOp",EDGE,"E2.sketch_text.stroke-72"),sQuery(id+"F2.wireOp",EDGE,"E2.sketch_text.stroke-73"),sQuery(id+"F2.wireOp",EDGE,"E2.sketch_text.stroke-74"),sQuery(id+"F2.wireOp",EDGE,"E2.sketch_text.stroke-75"),sQuery(id+"F2.wireOp",EDGE,"E2.sketch_text.stroke-76"),sQuery(id+"F2.wireOp",EDGE,"E2.sketch_text.stroke-77"),sQuery(id+"F2.wireOp",EDGE,"E2.sketch_text.stroke-78"),sQuery(id+"F2.wireOp",EDGE,"E2.sketch_text.stroke-79"),sQuery(id+"F2.wireOp",EDGE,"E2.sketch_text.stroke-80"),sQuery(id+"F2.wireOp",EDGE,"E2.sketch_text.stroke-81"),sQuery(id+"F2.wireOp",EDGE,"E2.sketch_text.stroke-82"),sQuery(id+"F2.wireOp",EDGE,"E2.sketch_text.stroke-83"),sQuery(id+"F2.wireOp",EDGE,"E2.sketch_text.stroke-84"),sQuery(id+"F2.wireOp",EDGE,"E2.sketch_text.stroke-85"),sQuery(id+"F2.wireOp",EDGE,"E2.sketch_text.stroke-86"),sQuery(id+"F2.wireOp",EDGE,"E2.sketch_text.stroke-87"),sQuery(id+"F2.wireOp",EDGE,"E2.sketch_text.stroke-88"),sQuery(id+"F2.wireOp",EDGE,"E2.sketch_text.stroke-89"),sQuery(id+"F2.wireOp",EDGE,"E2.sketch_text.stroke-90"),sQuery(id+"F2.wireOp",EDGE,"E2.sketch_text.stroke-91"),sQuery(id+"F2.wireOp",EDGE,"E2.sketch_text.stroke-92"),sQuery(id+"F2.wireOp",EDGE,"E2.sketch_text.stroke-93"),sQuery(id+"F2.wireOp",EDGE,"E2.sketch_text.stroke-94"),sQuery(id+"F2.wireOp",EDGE,"E2.sketch_text.stroke-95"),sQuery(id+"F2.wireOp",EDGE,"E2.sketch_text.stroke-96"),sQuery(id+"F2.wireOp",EDGE,"E2.sketch_text.stroke-97"),sQuery(id+"F2.wireOp",EDGE,"E2.sketch_text.stroke-98"),sQuery(id+"F2.wireOp",EDGE,"E2.sketch_text.stroke-99"),sQuery(id+"F2.wireOp",EDGE,"E2.sketch_text.stroke-100"),sQuery(id+"F2.wireOp",EDGE,"E2.sketch_text.stroke-101"),sQuery(id+"F2.wireOp",EDGE,"E2.sketch_text.stroke-102"),sQuery(id+"F2.wireOp",EDGE,"E2.sketch_text.stroke-103"),sQuery(id+"F2.wireOp",EDGE,"E2.sketch_text.stroke-104"),sQuery(id+"F2.wireOp",EDGE,"E2.sketch_text.stroke-105"),sQuery(id+"F2.wireOp",EDGE,"E2.sketch_text.stroke-106"),sQuery(id+"F2.wireOp",EDGE,"E2.sketch_text.stroke-107"),sQuery(id+"F2.wireOp",EDGE,"E2.sketch_text.stroke-108"),sQuery(id+"F2.wireOp",EDGE,"E2.sketch_text.stroke-109"),sQuery(id+"F2.wireOp",EDGE,"E2.sketch_text.stroke-110"),sQuery(id+"F2.wireOp",EDGE,"E2.sketch_text.stroke-111"),sQuery(id+"F2.wireOp",EDGE,"E2.sketch_text.stroke-112"),sQuery(id+"F2.wireOp",EDGE,"E2.sketch_text.stroke-113"),sQuery(id+"F2.wireOp",EDGE,"E2.sketch_text.stroke-114"),sQuery(id+"F2.wireOp",EDGE,"E2.sketch_text.stroke-115"),sQuery(id+"F2.wireOp",EDGE,"E2.sketch_text.stroke-116"),sQuery(id+"F2.wireOp",EDGE,"E2.sketch_text.stroke-117"),sQuery(id+"F2.wireOp",EDGE,"E2.sketch_text.stroke-118"),sQuery(id+"F2.wireOp",EDGE,"E2.sketch_text.stroke-119"),sQuery(id+"F2.wireOp",EDGE,"E2.sketch_text.stroke-120"),sQuery(id+"F2.wireOp",EDGE,"E2.sketch_text.stroke-121"),sQuery(id+"F2.wireOp",EDGE,"E2.sketch_text.stroke-122"),sQuery(id+"F2.wireOp",EDGE,"E2.sketch_text.stroke-123"),sQuery(id+"F2.wireOp",EDGE,"E2.sketch_text.stroke-124"),sQuery(id+"F2.wireOp",EDGE,"E2.sketch_text.stroke-125"),sQuery(id+"F2.wireOp",EDGE,"E2.sketch_text.stroke-126"),sQuery(id+"F2.wireOp",EDGE,"E2.sketch_text.stroke-127"),sQuery(id+"F2.wireOp",EDGE,"E2.sketch_text.stroke-128"),sQuery(id+"F2.wireOp",EDGE,"E2.sketch_text.stroke-129"),sQuery(id+"F2.wireOp",EDGE,"E2.sketch_text.stroke-130"),sQuery(id+"F2.wireOp",EDGE,"E2.sketch_text.stroke-131"),sQuery(id+"F2.wireOp",EDGE,"E2.sketch_text.stroke-132"),sQuery(id+"F2.wireOp",EDGE,"E2.sketch_text.stroke-133"),sQuery(id+"F2.wireOp",EDGE,"E2.sketch_text.stroke-134"),sQuery(id+"F2.wireOp",EDGE,"E2.sketch_text.stroke-135"),sQuery(id+"F2.wireOp",EDGE,"E2.sketch_text.stroke-136"),sQuery(id+"F2.wireOp",EDGE,"E2.sketch_text.stroke-137"),sQuery(id+"F2.wireOp",EDGE,"E2.sketch_text.stroke-138"),sQuery(id+"F2.wireOp",EDGE,"E2.sketch_text.stroke-139"),sQuery(id+"F2.wireOp",EDGE,"E2.sketch_text.stroke-140"),sQuery(id+"F2.wireOp",EDGE,"E2.sketch_text.stroke-141"),sQuery(id+"F2.wireOp",EDGE,"E2.sketch_text.stroke-142"),sQuery(id+"F2.wireOp",EDGE,"E2.sketch_text.stroke-143"),sQuery(id+"F2.wireOp",EDGE,"E2.sketch_text.stroke-144"),sQuery(id+"F2.wireOp",EDGE,"E2.sketch_text.stroke-145"),sQuery(id+"F2.wireOp",EDGE,"E2.sketch_text.stroke-146"),sQuery(id+"F2.wireOp",EDGE,"E2.sketch_text.stroke-147"),sQuery(id+"F2.wireOp",EDGE,"E2.sketch_text.stroke-148"),sQuery(id+"F2.wireOp",EDGE,"E2.sketch_text.stroke-149"),sQuery(id+"F2.wireOp",EDGE,"E2.sketch_text.stroke-150"),sQuery(id+"F2.wireOp",EDGE,"E2.sketch_text.stroke-151"),sQuery(id+"F2.wireOp",EDGE,"E2.sketch_text.stroke-152"),sQuery(id+"F2.wireOp",EDGE,"E2.sketch_text.stroke-153"),sQuery(id+"F2.wireOp",EDGE,"E2.sketch_text.stroke-154"),sQuery(id+"F2.wireOp",EDGE,"E2.sketch_text.stroke-155"),sQuery(id+"F2.wireOp",EDGE,"E2.sketch_text.stroke-156"),sQuery(id+"F2.wireOp",EDGE,"E2.sketch_text.stroke-157"),sQuery(id+"F2.wireOp",EDGE,"E2.sketch_text.stroke-158"),sQuery(id+"F2.wireOp",EDGE,"E2.sketch_text.stroke-159"),sQuery(id+"F2.wireOp",EDGE,"E2.sketch_text.stroke-160"),sQuery(id+"F2.wireOp",EDGE,"E2.sketch_text.stroke-161"),sQuery(id+"F2.wireOp",EDGE,"E2.sketch_text.stroke-162"),sQuery(id+"F2.wireOp",EDGE,"E2.sketch_text.stroke-163"),sQuery(id+"F2.wireOp",EDGE,"E2.sketch_text.stroke-164"),sQuery(id+"F2.wireOp",EDGE,"E2.sketch_text.stroke-165"),sQuery(id+"F2.wireOp",EDGE,"E2.sketch_text.stroke-166"),sQuery(id+"F2.wireOp",EDGE,"E2.sketch_text.stroke-167"),sQuery(id+"F2.wireOp",EDGE,"E2.sketch_text.stroke-168"),sQuery(id+"F2.wireOp",EDGE,"E2.sketch_text.stroke-169"),sQuery(id+"F2.wireOp",EDGE,"E2.sketch_text.stroke-170"),sQuery(id+"F2.wireOp",EDGE,"E2.sketch_text.stroke-171"),sQuery(id+"F2.wireOp",EDGE,"E2.sketch_text.stroke-172"),sQuery(id+"F2.wireOp",EDGE,"E2.sketch_text.stroke-173"),sQuery(id+"F3.wireOp",EDGE,"E4.sketch_text.stroke-0"),sQuery(id+"F3.wireOp",EDGE,"E4.sketch_text.stroke-1"),sQuery(id+"F3.wireOp",EDGE,"E4.sketch_text.stroke-2"),sQuery(id+"F3.wireOp",EDGE,"E4.sketch_text.stroke-3"),sQuery(id+"F3.wireOp",EDGE,"E4.sketch_text.stroke-4"),sQuery(id+"F3.wireOp",EDGE,"E4.sketch_text.stroke-5"),sQuery(id+"F3.wireOp",EDGE,"E4.sketch_text.stroke-6"),sQuery(id+"F3.wireOp",EDGE,"E4.sketch_text.stroke-7"),sQuery(id+"F3.wireOp",EDGE,"E4.sketch_text.stroke-8"),sQuery(id+"F3.wireOp",EDGE,"E4.sketch_text.stroke-9"),sQuery(id+"F3.wireOp",EDGE,"E4.sketch_text.stroke-10"),sQuery(id+"F3.wireOp",EDGE,"E4.sketch_text.stroke-11"),sQuery(id+"F3.wireOp",EDGE,"E4.sketch_text.stroke-12"),sQuery(id+"F3.wireOp",EDGE,"E4.sketch_text.stroke-13"),sQuery(id+"F3.wireOp",EDGE,"E4.sketch_text.stroke-14"),sQuery(id+"F3.wireOp",EDGE,"E4.sketch_text.stroke-15"),sQuery(id+"F3.wireOp",EDGE,"E4.sketch_text.stroke-16"),sQuery(id+"F3.wireOp",EDGE,"E4.sketch_text.stroke-17"),sQuery(id+"F3.wireOp",EDGE,"E4.sketch_text.stroke-18"),sQuery(id+"F3.wireOp",EDGE,"E4.sketch_text.stroke-19"),sQuery(id+"F3.wireOp",EDGE,"E4.sketch_text.stroke-20"),sQuery(id+"F3.wireOp",EDGE,"E4.sketch_text.stroke-21"),sQuery(id+"F3.wireOp",EDGE,"E4.sketch_text.stroke-22"),sQuery(id+"F3.wireOp",EDGE,"E4.sketch_text.stroke-23"),sQuery(id+"F3.wireOp",EDGE,"E4.sketch_text.stroke-24"),sQuery(id+"F3.wireOp",EDGE,"E4.sketch_text.stroke-25"),sQuery(id+"F3.wireOp",EDGE,"E4.sketch_text.stroke-26"),sQuery(id+"F3.wireOp",EDGE,"E4.sketch_text.stroke-27"),sQuery(id+"F3.wireOp",EDGE,"E4.sketch_text.stroke-28"),sQuery(id+"F3.wireOp",EDGE,"E4.sketch_text.stroke-29"),sQuery(id+"F3.wireOp",EDGE,"E4.sketch_text.stroke-30"),sQuery(id+"F3.wireOp",EDGE,"E4.sketch_text.stroke-31"),sQuery(id+"F3.wireOp",EDGE,"E4.sketch_text.stroke-32"),sQuery(id+"F3.wireOp",EDGE,"E4.sketch_text.stroke-33"),sQuery(id+"F3.wireOp",EDGE,"E4.sketch_text.stroke-34"),sQuery(id+"F3.wireOp",EDGE,"E4.sketch_text.stroke-35"),sQuery(id+"F3.wireOp",EDGE,"E4.sketch_text.stroke-36"),sQuery(id+"F3.wireOp",EDGE,"E4.sketch_text.stroke-37"),sQuery(id+"F3.wireOp",EDGE,"E4.sketch_text.stroke-38"),sQuery(id+"F3.wireOp",EDGE,"E4.sketch_text.stroke-39"),sQuery(id+"F3.wireOp",EDGE,"E4.sketch_text.stroke-40"),sQuery(id+"F3.wireOp",EDGE,"E4.sketch_text.stroke-41"),sQuery(id+"F3.wireOp",EDGE,"E4.sketch_text.stroke-42"),sQuery(id+"F3.wireOp",EDGE,"E4.sketch_text.stroke-43"),sQuery(id+"F3.wireOp",EDGE,"E4.sketch_text.stroke-44"),sQuery(id+"F3.wireOp",EDGE,"E4.sketch_text.stroke-45"),sQuery(id+"F3.wireOp",EDGE,"E4.sketch_text.stroke-46"),sQuery(id+"F3.wireOp",EDGE,"E4.sketch_text.stroke-47"),sQuery(id+"F3.wireOp",EDGE,"E4.sketch_text.stroke-48"),sQuery(id+"F3.wireOp",EDGE,"E4.sketch_text.stroke-49"),sQuery(id+"F3.wireOp",EDGE,"E4.sketch_text.stroke-50"),sQuery(id+"F3.wireOp",EDGE,"E4.sketch_text.stroke-51"),sQuery(id+"F3.wireOp",EDGE,"E4.sketch_text.stroke-52"),sQuery(id+"F3.wireOp",EDGE,"E4.sketch_text.stroke-53"),sQuery(id+"F3.wireOp",EDGE,"E4.sketch_text.stroke-54"),sQuery(id+"F3.wireOp",EDGE,"E4.sketch_text.stroke-55"),sQuery(id+"F3.wireOp",EDGE,"E4.sketch_text.stroke-56"),sQuery(id+"F3.wireOp",EDGE,"E4.sketch_text.stroke-57"),sQuery(id+"F3.wireOp",EDGE,"E4.sketch_text.stroke-58"),sQuery(id+"F3.wireOp",EDGE,"E4.sketch_text.stroke-59"),sQuery(id+"F3.wireOp",EDGE,"E4.sketch_text.stroke-60"),sQuery(id+"F3.wireOp",EDGE,"E4.sketch_text.stroke-61"),sQuery(id+"F3.wireOp",EDGE,"E4.sketch_text.stroke-62"),sQuery(id+"F3.wireOp",EDGE,"E4.sketch_text.stroke-71"),sQuery(id+"F3.wireOp",EDGE,"E4.sketch_text.stroke-72"),sQuery(id+"F3.wireOp",EDGE,"E4.sketch_text.stroke-73"),sQuery(id+"F3.wireOp",EDGE,"E4.sketch_text.stroke-74"),sQuery(id+"F3.wireOp",EDGE,"E4.sketch_text.stroke-75"),sQuery(id+"F3.wireOp",EDGE,"E4.sketch_text.stroke-76"),sQuery(id+"F3.wireOp",EDGE,"E4.sketch_text.stroke-77"),sQuery(id+"F3.wireOp",EDGE,"E4.sketch_text.stroke-78"),sQuery(id+"F3.wireOp",EDGE,"E4.sketch_text.stroke-79"),sQuery(id+"F3.wireOp",EDGE,"E4.sketch_text.stroke-80"),sQuery(id+"F3.wireOp",EDGE,"E4.sketch_text.stroke-81"),sQuery(id+"F3.wireOp",EDGE,"E4.sketch_text.stroke-82"),sQuery(id+"F3.wireOp",EDGE,"E4.sketch_text.stroke-83"),sQuery(id+"F3.wireOp",EDGE,"E4.sketch_text.stroke-84"),sQuery(id+"F3.wireOp",EDGE,"E4.sketch_text.stroke-85"),sQuery(id+"F3.wireOp",EDGE,"E4.sketch_text.stroke-86"),sQuery(id+"F3.wireOp",EDGE,"E4.sketch_text.stroke-87"),sQuery(id+"F3.wireOp",EDGE,"E4.sketch_text.stroke-88"),sQuery(id+"F3.wireOp",EDGE,"E4.sketch_text.stroke-89"),sQuery(id+"F3.wireOp",EDGE,"E4.sketch_text.stroke-90"),sQuery(id+"F3.wireOp",EDGE,"E4.sketch_text.stroke-91"),sQuery(id+"F3.wireOp",EDGE,"E4.sketch_text.stroke-92"),sQuery(id+"F3.wireOp",EDGE,"E4.sketch_text.stroke-93"),sQuery(id+"F3.wireOp",EDGE,"E4.sketch_text.stroke-94"),sQuery(id+"F3.wireOp",EDGE,"E4.sketch_text.stroke-95"),sQuery(id+"F3.wireOp",EDGE,"E4.sketch_text.stroke-96"),sQuery(id+"F3.wireOp",EDGE,"E4.sketch_text.stroke-97"),sQuery(id+"F3.wireOp",EDGE,"E4.sketch_text.stroke-103"),sQuery(id+"F3.wireOp",EDGE,"E4.sketch_text.stroke-104"),sQuery(id+"F3.wireOp",EDGE,"E4.sketch_text.stroke-105"),sQuery(id+"F3.wireOp",EDGE,"E4.sketch_text.stroke-106"),sQuery(id+"F3.wireOp",EDGE,"E4.sketch_text.stroke-107"),sQuery(id+"F3.wireOp",EDGE,"E4.sketch_text.stroke-108"),sQuery(id+"F3.wireOp",EDGE,"E4.sketch_text.stroke-109"),sQuery(id+"F3.wireOp",EDGE,"E4.sketch_text.stroke-110"),sQuery(id+"F3.wireOp",EDGE,"E4.sketch_text.stroke-111"),sQuery(id+"F3.wireOp",EDGE,"E4.sketch_text.stroke-112"),sQuery(id+"F3.wireOp",EDGE,"E4.sketch_text.stroke-113"),sQuery(id+"F3.wireOp",EDGE,"E4.sketch_text.stroke-114"),sQuery(id+"F3.wireOp",EDGE,"E4.sketch_text.stroke-115"),sQuery(id+"F3.wireOp",EDGE,"E4.sketch_text.stroke-116"),sQuery(id+"F3.wireOp",EDGE,"E4.sketch_text.stroke-117"),sQuery(id+"F3.wireOp",EDGE,"E4.sketch_text.stroke-118"),sQuery(id+"F3.wireOp",EDGE,"E4.sketch_text.stroke-119"),sQuery(id+"F3.wireOp",EDGE,"E4.sketch_text.stroke-120"),sQuery(id+"F3.wireOp",EDGE,"E4.sketch_text.stroke-121"),sQuery(id+"F3.wireOp",EDGE,"E4.sketch_text.stroke-122"),sQuery(id+"F3.wireOp",EDGE,"E4.sketch_text.stroke-123"),sQuery(id+"F3.wireOp",EDGE,"E4.sketch_text.stroke-124"),sQuery(id+"F3.wireOp",EDGE,"E4.sketch_text.stroke-125"),sQuery(id+"F3.wireOp",EDGE,"E4.sketch_text.stroke-126"),sQuery(id+"F3.wireOp",EDGE,"E4.sketch_text.stroke-127"),sQuery(id+"F3.wireOp",EDGE,"E4.sketch_text.stroke-128"),sQuery(id+"F3.wireOp",EDGE,"E4.sketch_text.stroke-129"),sQuery(id+"F3.wireOp",EDGE,"E4.sketch_text.stroke-130"),sQuery(id+"F3.wireOp",EDGE,"E4.sketch_text.stroke-131"),sQuery(id+"F3.wireOp",EDGE,"E4.sketch_text.stroke-132"),sQuery(id+"F3.wireOp",EDGE,"E4.sketch_text.stroke-133"),sQuery(id+"F3.wireOp",EDGE,"E4.sketch_text.stroke-134"),sQuery(id+"F3.wireOp",EDGE,"E4.sketch_text.stroke-135"),sQuery(id+"F3.wireOp",EDGE,"E4.sketch_text.stroke-136"),sQuery(id+"F3.wireOp",EDGE,"E4.sketch_text.stroke-137"),sQuery(id+"F3.wireOp",EDGE,"E4.sketch_text.stroke-138"),sQuery(id+"F3.wireOp",EDGE,"E4.sketch_text.stroke-139"),sQuery(id+"F3.wireOp",EDGE,"E4.sketch_text.stroke-140"),sQuery(id+"F3.wireOp",EDGE,"E4.sketch_text.stroke-141"),sQuery(id+"F3.wireOp",EDGE,"E4.sketch_text.stroke-142"),sQuery(id+"F3.wireOp",EDGE,"E4.sketch_text.stroke-143"),sQuery(id+"F3.wireOp",EDGE,"E4.sketch_text.stroke-144"),sQuery(id+"F3.wireOp",EDGE,"E4.sketch_text.stroke-145"),sQuery(id+"F3.wireOp",EDGE,"E4.sketch_text.stroke-146"),sQuery(id+"F3.wireOp",EDGE,"E4.sketch_text.stroke-147"),sQuery(id+"F3.wireOp",EDGE,"E4.sketch_text.stroke-148"),sQuery(id+"F3.wireOp",EDGE,"E4.sketch_text.stroke-149"),sQuery(id+"F3.wireOp",EDGE,"E4.sketch_text.stroke-150"),sQuery(id+"F3.wireOp",EDGE,"E4.sketch_text.stroke-151"),sQuery(id+"F3.wireOp",EDGE,"E4.sketch_text.stroke-152"),sQuery(id+"F3.wireOp",EDGE,"E4.sketch_text.stroke-153"),sQuery(id+"F3.wireOp",EDGE,"E4.sketch_text.stroke-159"),sQuery(id+"F3.wireOp",EDGE,"E4.sketch_text.stroke-160"),sQuery(id+"F3.wireOp",EDGE,"E4.sketch_text.stroke-161"),sQuery(id+"F3.wireOp",EDGE,"E4.sketch_text.stroke-162"),sQuery(id+"F3.wireOp",EDGE,"E4.sketch_text.stroke-163"),sQuery(id+"F3.wireOp",EDGE,"E4.sketch_text.stroke-164"),sQuery(id+"F3.wireOp",EDGE,"E4.sketch_text.stroke-165"),sQuery(id+"F3.wireOp",EDGE,"E4.sketch_text.stroke-166"),sQuery(id+"F3.wireOp",EDGE,"E4.sketch_text.stroke-167"),sQuery(id+"F3.wireOp",EDGE,"E4.sketch_text.stroke-168"),sQuery(id+"F3.wireOp",EDGE,"E4.sketch_text.stroke-169"),sQuery(id+"F3.wireOp",EDGE,"E4.sketch_text.stroke-170"),sQuery(id+"F3.wireOp",EDGE,"E4.sketch_text.stroke-171"),sQuery(id+"F3.wireOp",EDGE,"E4.sketch_text.stroke-172"),sQuery(id+"F3.wireOp",EDGE,"E4.sketch_text.stroke-173"),sQuery(id+"F3.wireOp",EDGE,"E4.sketch_text.stroke-174"),sQuery(id+"F3.wireOp",EDGE,"E4.sketch_text.stroke-175"),sQuery(id+"F3.wireOp",EDGE,"E4.sketch_text.stroke-176"),sQuery(id+"F3.wireOp",EDGE,"E4.sketch_text.stroke-177"),sQuery(id+"F3.wireOp",EDGE,"E4.sketch_text.stroke-178"),sQuery(id+"F3.wireOp",EDGE,"E4.sketch_text.stroke-179"),sQuery(id+"F3.wireOp",EDGE,"E4.sketch_text.stroke-180"),subQ2,sQuery(id+"F4.wireOp",EDGE,"6ee83ff3-586e-4dbe-aaea-af71240543bd")])],"isStart":true})])],"derivedFrom":makeQuery(id+"F5.opExtrude","CAP_EDGE",EDGE,{"disambiguationData":[OSD([subQ2])],"isStart":true})});}
            var Q3;
            {var subQ0=sQuery(id+"F4.wireOp",EDGE,"8007402e-1a4e-4a06-85a5-2af08e553504");var subQ1=sQuery(id+"F0.wireOp",EDGE,"E0.top");var subQ2=sQuery(id+"F4.wireOp",EDGE,"6ee83ff3-586e-4dbe-aaea-af71240543bd");var subQ3=sQuery(id+"F0.wireOp",EDGE,"E0.bottom");Q3=makeQuery(id+"F5.boolean.opBoolean","SPLIT",EDGE,{"disambiguationData":[TD([makeQuery(id+"F1.opExtrude","CAP_FACE",FACE,{"disambiguationData":[OSD([subQ3,subQ1,sQuery(id+"F0.wireOp",EDGE,"E0.left"),sQuery(id+"F0.wireOp",EDGE,"E0.right")])],"isStart":false}),makeQuery(id+"F1.opExtrude","SWEPT_FACE",FACE,{"disambiguationData":[OSD([subQ1])]}),makeQuery(id+"F5.opExtrude","SWEPT_FACE",FACE,{"disambiguationData":[OSD([subQ0])]}),makeQuery(id+"F5.opExtrude","CAP_FACE",FACE,{"disambiguationData":[OSD([subQ3,sQuery(id+"F2.wireOp",EDGE,"E2.sketch_text.stroke-0"),sQuery(id+"F2.wireOp",EDGE,"E2.sketch_text.stroke-1"),sQuery(id+"F2.wireOp",EDGE,"E2.sketch_text.stroke-2"),sQuery(id+"F2.wireOp",EDGE,"E2.sketch_text.stroke-3"),sQuery(id+"F2.wireOp",EDGE,"E2.sketch_text.stroke-4"),sQuery(id+"F2.wireOp",EDGE,"E2.sketch_text.stroke-5"),sQuery(id+"F2.wireOp",EDGE,"E2.sketch_text.stroke-6"),sQuery(id+"F2.wireOp",EDGE,"E2.sketch_text.stroke-7"),sQuery(id+"F2.wireOp",EDGE,"E2.sketch_text.stroke-8"),sQuery(id+"F2.wireOp",EDGE,"E2.sketch_text.stroke-9"),sQuery(id+"F2.wireOp",EDGE,"E2.sketch_text.stroke-10"),sQuery(id+"F2.wireOp",EDGE,"E2.sketch_text.stroke-11"),sQuery(id+"F2.wireOp",EDGE,"E2.sketch_text.stroke-12"),sQuery(id+"F2.wireOp",EDGE,"E2.sketch_text.stroke-13"),sQuery(id+"F2.wireOp",EDGE,"E2.sketch_text.stroke-14"),sQuery(id+"F2.wireOp",EDGE,"E2.sketch_text.stroke-15"),sQuery(id+"F2.wireOp",EDGE,"E2.sketch_text.stroke-16"),sQuery(id+"F2.wireOp",EDGE,"E2.sketch_text.stroke-17"),sQuery(id+"F2.wireOp",EDGE,"E2.sketch_text.stroke-18"),sQuery(id+"F2.wireOp",EDGE,"E2.sketch_text.stroke-19"),sQuery(id+"F2.wireOp",EDGE,"E2.sketch_text.stroke-20"),sQuery(id+"F2.wireOp",EDGE,"E2.sketch_text.stroke-21"),sQuery(id+"F2.wireOp",EDGE,"E2.sketch_text.stroke-22"),sQuery(id+"F2.wireOp",EDGE,"E2.sketch_text.stroke-23"),sQuery(id+"F2.wireOp",EDGE,"E2.sketch_text.stroke-24"),sQuery(id+"F2.wireOp",EDGE,"E2.sketch_text.stroke-25"),sQuery(id+"F2.wireOp",EDGE,"E2.sketch_text.stroke-26"),sQuery(id+"F2.wireOp",EDGE,"E2.sketch_text.stroke-27"),sQuery(id+"F2.wireOp",EDGE,"E2.sketch_text.stroke-28"),sQuery(id+"F2.wireOp",EDGE,"E2.sketch_text.stroke-29"),sQuery(id+"F2.wireOp",EDGE,"E2.sketch_text.stroke-30"),sQuery(id+"F2.wireOp",EDGE,"E2.sketch_text.stroke-31"),sQuery(id+"F2.wireOp",EDGE,"E2.sketch_text.stroke-32"),sQuery(id+"F2.wireOp",EDGE,"E2.sketch_text.stroke-33"),sQuery(id+"F2.wireOp",EDGE,"E2.sketch_text.stroke-34"),sQuery(id+"F2.wireOp",EDGE,"E2.sketch_text.stroke-35"),sQuery(id+"F2.wireOp",EDGE,"E2.sketch_text.stroke-36"),sQuery(id+"F2.wireOp",EDGE,"E2.sketch_text.stroke-37"),sQuery(id+"F2.wireOp",EDGE,"E2.sketch_text.stroke-38"),sQuery(id+"F2.wireOp",EDGE,"E2.sketch_text.stroke-39"),sQuery(id+"F2.wireOp",EDGE,"E2.sketch_text.stroke-40"),sQuery(id+"F2.wireOp",EDGE,"E2.sketch_text.stroke-41"),sQuery(id+"F2.wireOp",EDGE,"E2.sketch_text.stroke-42"),sQuery(id+"F2.wireOp",EDGE,"E2.sketch_text.stroke-43"),sQuery(id+"F2.wireOp",EDGE,"E2.sketch_text.stroke-44"),sQuery(id+"F2.wireOp",EDGE,"E2.sketch_text.stroke-45"),sQuery(id+"F2.wireOp",EDGE,"E2.sketch_text.stroke-46"),sQuery(id+"F2.wireOp",EDGE,"E2.sketch_text.stroke-47"),sQuery(id+"F2.wireOp",EDGE,"E2.sketch_text.stroke-48"),sQuery(id+"F2.wireOp",EDGE,"E2.sketch_text.stroke-49"),sQuery(id+"F2.wireOp",EDGE,"E2.sketch_text.stroke-50"),sQuery(id+"F2.wireOp",EDGE,"E2.sketch_text.stroke-51"),sQuery(id+"F2.wireOp",EDGE,"E2.sketch_text.stroke-52"),sQuery(id+"F2.wireOp",EDGE,"E2.sketch_text.stroke-53"),sQuery(id+"F2.wireOp",EDGE,"E2.sketch_text.stroke-54"),sQuery(id+"F2.wireOp",EDGE,"E2.sketch_text.stroke-55"),sQuery(id+"F2.wireOp",EDGE,"E2.sketch_text.stroke-56"),sQuery(id+"F2.wireOp",EDGE,"E2.sketch_text.stroke-57"),sQuery(id+"F2.wireOp",EDGE,"E2.sketch_text.stroke-58"),sQuery(id+"F2.wireOp",EDGE,"E2.sketch_text.stroke-59"),sQuery(id+"F2.wireOp",EDGE,"E2.sketch_text.stroke-60"),sQuery(id+"F2.wireOp",EDGE,"E2.sketch_text.stroke-61"),sQuery(id+"F2.wireOp",EDGE,"E2.sketch_text.stroke-62"),sQuery(id+"F2.wireOp",EDGE,"E2.sketch_text.stroke-63"),sQuery(id+"F2.wireOp",EDGE,"E2.sketch_text.stroke-64"),sQuery(id+"F2.wireOp",EDGE,"E2.sketch_text.stroke-65"),sQuery(id+"F2.wireOp",EDGE,"E2.sketch_text.stroke-66"),sQuery(id+"F2.wireOp",EDGE,"E2.sketch_text.stroke-67"),sQuery(id+"F2.wireOp",EDGE,"E2.sketch_text.stroke-68"),sQuery(id+"F2.wireOp",EDGE,"E2.sketch_text.stroke-69"),sQuery(id+"F2.wireOp",EDGE,"E2.sketch_text.stroke-70"),sQuery(id+"F2.wireOp",EDGE,"E2.sketch_text.stroke-71"),sQuery(id+"F2.wireOp",EDGE,"E2.sketch_text.stroke-72"),sQuery(id+"F2.wireOp",EDGE,"E2.sketch_text.stroke-73"),sQuery(id+"F2.wireOp",EDGE,"E2.sketch_text.stroke-74"),sQuery(id+"F2.wireOp",EDGE,"E2.sketch_text.stroke-75"),sQuery(id+"F2.wireOp",EDGE,"E2.sketch_text.stroke-76"),sQuery(id+"F2.wireOp",EDGE,"E2.sketch_text.stroke-77"),sQuery(id+"F2.wireOp",EDGE,"E2.sketch_text.stroke-78"),sQuery(id+"F2.wireOp",EDGE,"E2.sketch_text.stroke-79"),sQuery(id+"F2.wireOp",EDGE,"E2.sketch_text.stroke-80"),sQuery(id+"F2.wireOp",EDGE,"E2.sketch_text.stroke-81"),sQuery(id+"F2.wireOp",EDGE,"E2.sketch_text.stroke-82"),sQuery(id+"F2.wireOp",EDGE,"E2.sketch_text.stroke-83"),sQuery(id+"F2.wireOp",EDGE,"E2.sketch_text.stroke-84"),sQuery(id+"F2.wireOp",EDGE,"E2.sketch_text.stroke-85"),sQuery(id+"F2.wireOp",EDGE,"E2.sketch_text.stroke-86"),sQuery(id+"F2.wireOp",EDGE,"E2.sketch_text.stroke-87"),sQuery(id+"F2.wireOp",EDGE,"E2.sketch_text.stroke-88"),sQuery(id+"F2.wireOp",EDGE,"E2.sketch_text.stroke-89"),sQuery(id+"F2.wireOp",EDGE,"E2.sketch_text.stroke-90"),sQuery(id+"F2.wireOp",EDGE,"E2.sketch_text.stroke-91"),sQuery(id+"F2.wireOp",EDGE,"E2.sketch_text.stroke-92"),sQuery(id+"F2.wireOp",EDGE,"E2.sketch_text.stroke-93"),sQuery(id+"F2.wireOp",EDGE,"E2.sketch_text.stroke-94"),sQuery(id+"F2.wireOp",EDGE,"E2.sketch_text.stroke-95"),sQuery(id+"F2.wireOp",EDGE,"E2.sketch_text.stroke-96"),sQuery(id+"F2.wireOp",EDGE,"E2.sketch_text.stroke-97"),sQuery(id+"F2.wireOp",EDGE,"E2.sketch_text.stroke-98"),sQuery(id+"F2.wireOp",EDGE,"E2.sketch_text.stroke-99"),sQuery(id+"F2.wireOp",EDGE,"E2.sketch_text.stroke-100"),sQuery(id+"F2.wireOp",EDGE,"E2.sketch_text.stroke-101"),sQuery(id+"F2.wireOp",EDGE,"E2.sketch_text.stroke-102"),sQuery(id+"F2.wireOp",EDGE,"E2.sketch_text.stroke-103"),sQuery(id+"F2.wireOp",EDGE,"E2.sketch_text.stroke-104"),sQuery(id+"F2.wireOp",EDGE,"E2.sketch_text.stroke-105"),sQuery(id+"F2.wireOp",EDGE,"E2.sketch_text.stroke-106"),sQuery(id+"F2.wireOp",EDGE,"E2.sketch_text.stroke-107"),sQuery(id+"F2.wireOp",EDGE,"E2.sketch_text.stroke-108"),sQuery(id+"F2.wireOp",EDGE,"E2.sketch_text.stroke-109"),sQuery(id+"F2.wireOp",EDGE,"E2.sketch_text.stroke-110"),sQuery(id+"F2.wireOp",EDGE,"E2.sketch_text.stroke-111"),sQuery(id+"F2.wireOp",EDGE,"E2.sketch_text.stroke-112"),sQuery(id+"F2.wireOp",EDGE,"E2.sketch_text.stroke-113"),sQuery(id+"F2.wireOp",EDGE,"E2.sketch_text.stroke-114"),sQuery(id+"F2.wireOp",EDGE,"E2.sketch_text.stroke-115"),sQuery(id+"F2.wireOp",EDGE,"E2.sketch_text.stroke-116"),sQuery(id+"F2.wireOp",EDGE,"E2.sketch_text.stroke-117"),sQuery(id+"F2.wireOp",EDGE,"E2.sketch_text.stroke-118"),sQuery(id+"F2.wireOp",EDGE,"E2.sketch_text.stroke-119"),sQuery(id+"F2.wireOp",EDGE,"E2.sketch_text.stroke-120"),sQuery(id+"F2.wireOp",EDGE,"E2.sketch_text.stroke-121"),sQuery(id+"F2.wireOp",EDGE,"E2.sketch_text.stroke-122"),sQuery(id+"F2.wireOp",EDGE,"E2.sketch_text.stroke-123"),sQuery(id+"F2.wireOp",EDGE,"E2.sketch_text.stroke-124"),sQuery(id+"F2.wireOp",EDGE,"E2.sketch_text.stroke-125"),sQuery(id+"F2.wireOp",EDGE,"E2.sketch_text.stroke-126"),sQuery(id+"F2.wireOp",EDGE,"E2.sketch_text.stroke-127"),sQuery(id+"F2.wireOp",EDGE,"E2.sketch_text.stroke-128"),sQuery(id+"F2.wireOp",EDGE,"E2.sketch_text.stroke-129"),sQuery(id+"F2.wireOp",EDGE,"E2.sketch_text.stroke-130"),sQuery(id+"F2.wireOp",EDGE,"E2.sketch_text.stroke-131"),sQuery(id+"F2.wireOp",EDGE,"E2.sketch_text.stroke-132"),sQuery(id+"F2.wireOp",EDGE,"E2.sketch_text.stroke-133"),sQuery(id+"F2.wireOp",EDGE,"E2.sketch_text.stroke-134"),sQuery(id+"F2.wireOp",EDGE,"E2.sketch_text.stroke-135"),sQuery(id+"F2.wireOp",EDGE,"E2.sketch_text.stroke-136"),sQuery(id+"F2.wireOp",EDGE,"E2.sketch_text.stroke-137"),sQuery(id+"F2.wireOp",EDGE,"E2.sketch_text.stroke-138"),sQuery(id+"F2.wireOp",EDGE,"E2.sketch_text.stroke-139"),sQuery(id+"F2.wireOp",EDGE,"E2.sketch_text.stroke-140"),sQuery(id+"F2.wireOp",EDGE,"E2.sketch_text.stroke-141"),sQuery(id+"F2.wireOp",EDGE,"E2.sketch_text.stroke-142"),sQuery(id+"F2.wireOp",EDGE,"E2.sketch_text.stroke-143"),sQuery(id+"F2.wireOp",EDGE,"E2.sketch_text.stroke-144"),sQuery(id+"F2.wireOp",EDGE,"E2.sketch_text.stroke-145"),sQuery(id+"F2.wireOp",EDGE,"E2.sketch_text.stroke-146"),sQuery(id+"F2.wireOp",EDGE,"E2.sketch_text.stroke-147"),sQuery(id+"F2.wireOp",EDGE,"E2.sketch_text.stroke-148"),sQuery(id+"F2.wireOp",EDGE,"E2.sketch_text.stroke-149"),sQuery(id+"F2.wireOp",EDGE,"E2.sketch_text.stroke-150"),sQuery(id+"F2.wireOp",EDGE,"E2.sketch_text.stroke-151"),sQuery(id+"F2.wireOp",EDGE,"E2.sketch_text.stroke-152"),sQuery(id+"F2.wireOp",EDGE,"E2.sketch_text.stroke-153"),sQuery(id+"F2.wireOp",EDGE,"E2.sketch_text.stroke-154"),sQuery(id+"F2.wireOp",EDGE,"E2.sketch_text.stroke-155"),sQuery(id+"F2.wireOp",EDGE,"E2.sketch_text.stroke-156"),sQuery(id+"F2.wireOp",EDGE,"E2.sketch_text.stroke-157"),sQuery(id+"F2.wireOp",EDGE,"E2.sketch_text.stroke-158"),sQuery(id+"F2.wireOp",EDGE,"E2.sketch_text.stroke-159"),sQuery(id+"F2.wireOp",EDGE,"E2.sketch_text.stroke-160"),sQuery(id+"F2.wireOp",EDGE,"E2.sketch_text.stroke-161"),sQuery(id+"F2.wireOp",EDGE,"E2.sketch_text.stroke-162"),sQuery(id+"F2.wireOp",EDGE,"E2.sketch_text.stroke-163"),sQuery(id+"F2.wireOp",EDGE,"E2.sketch_text.stroke-164"),sQuery(id+"F2.wireOp",EDGE,"E2.sketch_text.stroke-165"),sQuery(id+"F2.wireOp",EDGE,"E2.sketch_text.stroke-166"),sQuery(id+"F2.wireOp",EDGE,"E2.sketch_text.stroke-167"),sQuery(id+"F2.wireOp",EDGE,"E2.sketch_text.stroke-168"),sQuery(id+"F2.wireOp",EDGE,"E2.sketch_text.stroke-169"),sQuery(id+"F2.wireOp",EDGE,"E2.sketch_text.stroke-170"),sQuery(id+"F2.wireOp",EDGE,"E2.sketch_text.stroke-171"),sQuery(id+"F2.wireOp",EDGE,"E2.sketch_text.stroke-172"),sQuery(id+"F2.wireOp",EDGE,"E2.sketch_text.stroke-173"),sQuery(id+"F3.wireOp",EDGE,"E4.sketch_text.stroke-0"),sQuery(id+"F3.wireOp",EDGE,"E4.sketch_text.stroke-1"),sQuery(id+"F3.wireOp",EDGE,"E4.sketch_text.stroke-2"),sQuery(id+"F3.wireOp",EDGE,"E4.sketch_text.stroke-3"),sQuery(id+"F3.wireOp",EDGE,"E4.sketch_text.stroke-4"),sQuery(id+"F3.wireOp",EDGE,"E4.sketch_text.stroke-5"),sQuery(id+"F3.wireOp",EDGE,"E4.sketch_text.stroke-6"),sQuery(id+"F3.wireOp",EDGE,"E4.sketch_text.stroke-7"),sQuery(id+"F3.wireOp",EDGE,"E4.sketch_text.stroke-8"),sQuery(id+"F3.wireOp",EDGE,"E4.sketch_text.stroke-9"),sQuery(id+"F3.wireOp",EDGE,"E4.sketch_text.stroke-10"),sQuery(id+"F3.wireOp",EDGE,"E4.sketch_text.stroke-11"),sQuery(id+"F3.wireOp",EDGE,"E4.sketch_text.stroke-12"),sQuery(id+"F3.wireOp",EDGE,"E4.sketch_text.stroke-13"),sQuery(id+"F3.wireOp",EDGE,"E4.sketch_text.stroke-14"),sQuery(id+"F3.wireOp",EDGE,"E4.sketch_text.stroke-15"),sQuery(id+"F3.wireOp",EDGE,"E4.sketch_text.stroke-16"),sQuery(id+"F3.wireOp",EDGE,"E4.sketch_text.stroke-17"),sQuery(id+"F3.wireOp",EDGE,"E4.sketch_text.stroke-18"),sQuery(id+"F3.wireOp",EDGE,"E4.sketch_text.stroke-19"),sQuery(id+"F3.wireOp",EDGE,"E4.sketch_text.stroke-20"),sQuery(id+"F3.wireOp",EDGE,"E4.sketch_text.stroke-21"),sQuery(id+"F3.wireOp",EDGE,"E4.sketch_text.stroke-22"),sQuery(id+"F3.wireOp",EDGE,"E4.sketch_text.stroke-23"),sQuery(id+"F3.wireOp",EDGE,"E4.sketch_text.stroke-24"),sQuery(id+"F3.wireOp",EDGE,"E4.sketch_text.stroke-25"),sQuery(id+"F3.wireOp",EDGE,"E4.sketch_text.stroke-26"),sQuery(id+"F3.wireOp",EDGE,"E4.sketch_text.stroke-27"),sQuery(id+"F3.wireOp",EDGE,"E4.sketch_text.stroke-28"),sQuery(id+"F3.wireOp",EDGE,"E4.sketch_text.stroke-29"),sQuery(id+"F3.wireOp",EDGE,"E4.sketch_text.stroke-30"),sQuery(id+"F3.wireOp",EDGE,"E4.sketch_text.stroke-31"),sQuery(id+"F3.wireOp",EDGE,"E4.sketch_text.stroke-32"),sQuery(id+"F3.wireOp",EDGE,"E4.sketch_text.stroke-33"),sQuery(id+"F3.wireOp",EDGE,"E4.sketch_text.stroke-34"),sQuery(id+"F3.wireOp",EDGE,"E4.sketch_text.stroke-35"),sQuery(id+"F3.wireOp",EDGE,"E4.sketch_text.stroke-36"),sQuery(id+"F3.wireOp",EDGE,"E4.sketch_text.stroke-37"),sQuery(id+"F3.wireOp",EDGE,"E4.sketch_text.stroke-38"),sQuery(id+"F3.wireOp",EDGE,"E4.sketch_text.stroke-39"),sQuery(id+"F3.wireOp",EDGE,"E4.sketch_text.stroke-40"),sQuery(id+"F3.wireOp",EDGE,"E4.sketch_text.stroke-41"),sQuery(id+"F3.wireOp",EDGE,"E4.sketch_text.stroke-42"),sQuery(id+"F3.wireOp",EDGE,"E4.sketch_text.stroke-43"),sQuery(id+"F3.wireOp",EDGE,"E4.sketch_text.stroke-44"),sQuery(id+"F3.wireOp",EDGE,"E4.sketch_text.stroke-45"),sQuery(id+"F3.wireOp",EDGE,"E4.sketch_text.stroke-46"),sQuery(id+"F3.wireOp",EDGE,"E4.sketch_text.stroke-47"),sQuery(id+"F3.wireOp",EDGE,"E4.sketch_text.stroke-48"),sQuery(id+"F3.wireOp",EDGE,"E4.sketch_text.stroke-49"),sQuery(id+"F3.wireOp",EDGE,"E4.sketch_text.stroke-50"),sQuery(id+"F3.wireOp",EDGE,"E4.sketch_text.stroke-51"),sQuery(id+"F3.wireOp",EDGE,"E4.sketch_text.stroke-52"),sQuery(id+"F3.wireOp",EDGE,"E4.sketch_text.stroke-53"),sQuery(id+"F3.wireOp",EDGE,"E4.sketch_text.stroke-54"),sQuery(id+"F3.wireOp",EDGE,"E4.sketch_text.stroke-55"),sQuery(id+"F3.wireOp",EDGE,"E4.sketch_text.stroke-56"),sQuery(id+"F3.wireOp",EDGE,"E4.sketch_text.stroke-57"),sQuery(id+"F3.wireOp",EDGE,"E4.sketch_text.stroke-58"),sQuery(id+"F3.wireOp",EDGE,"E4.sketch_text.stroke-59"),sQuery(id+"F3.wireOp",EDGE,"E4.sketch_text.stroke-60"),sQuery(id+"F3.wireOp",EDGE,"E4.sketch_text.stroke-61"),sQuery(id+"F3.wireOp",EDGE,"E4.sketch_text.stroke-62"),sQuery(id+"F3.wireOp",EDGE,"E4.sketch_text.stroke-71"),sQuery(id+"F3.wireOp",EDGE,"E4.sketch_text.stroke-72"),sQuery(id+"F3.wireOp",EDGE,"E4.sketch_text.stroke-73"),sQuery(id+"F3.wireOp",EDGE,"E4.sketch_text.stroke-74"),sQuery(id+"F3.wireOp",EDGE,"E4.sketch_text.stroke-75"),sQuery(id+"F3.wireOp",EDGE,"E4.sketch_text.stroke-76"),sQuery(id+"F3.wireOp",EDGE,"E4.sketch_text.stroke-77"),sQuery(id+"F3.wireOp",EDGE,"E4.sketch_text.stroke-78"),sQuery(id+"F3.wireOp",EDGE,"E4.sketch_text.stroke-79"),sQuery(id+"F3.wireOp",EDGE,"E4.sketch_text.stroke-80"),sQuery(id+"F3.wireOp",EDGE,"E4.sketch_text.stroke-81"),sQuery(id+"F3.wireOp",EDGE,"E4.sketch_text.stroke-82"),sQuery(id+"F3.wireOp",EDGE,"E4.sketch_text.stroke-83"),sQuery(id+"F3.wireOp",EDGE,"E4.sketch_text.stroke-84"),sQuery(id+"F3.wireOp",EDGE,"E4.sketch_text.stroke-85"),sQuery(id+"F3.wireOp",EDGE,"E4.sketch_text.stroke-86"),sQuery(id+"F3.wireOp",EDGE,"E4.sketch_text.stroke-87"),sQuery(id+"F3.wireOp",EDGE,"E4.sketch_text.stroke-88"),sQuery(id+"F3.wireOp",EDGE,"E4.sketch_text.stroke-89"),sQuery(id+"F3.wireOp",EDGE,"E4.sketch_text.stroke-90"),sQuery(id+"F3.wireOp",EDGE,"E4.sketch_text.stroke-91"),sQuery(id+"F3.wireOp",EDGE,"E4.sketch_text.stroke-92"),sQuery(id+"F3.wireOp",EDGE,"E4.sketch_text.stroke-93"),sQuery(id+"F3.wireOp",EDGE,"E4.sketch_text.stroke-94"),sQuery(id+"F3.wireOp",EDGE,"E4.sketch_text.stroke-95"),sQuery(id+"F3.wireOp",EDGE,"E4.sketch_text.stroke-96"),sQuery(id+"F3.wireOp",EDGE,"E4.sketch_text.stroke-97"),sQuery(id+"F3.wireOp",EDGE,"E4.sketch_text.stroke-103"),sQuery(id+"F3.wireOp",EDGE,"E4.sketch_text.stroke-104"),sQuery(id+"F3.wireOp",EDGE,"E4.sketch_text.stroke-105"),sQuery(id+"F3.wireOp",EDGE,"E4.sketch_text.stroke-106"),sQuery(id+"F3.wireOp",EDGE,"E4.sketch_text.stroke-107"),sQuery(id+"F3.wireOp",EDGE,"E4.sketch_text.stroke-108"),sQuery(id+"F3.wireOp",EDGE,"E4.sketch_text.stroke-109"),sQuery(id+"F3.wireOp",EDGE,"E4.sketch_text.stroke-110"),sQuery(id+"F3.wireOp",EDGE,"E4.sketch_text.stroke-111"),sQuery(id+"F3.wireOp",EDGE,"E4.sketch_text.stroke-112"),sQuery(id+"F3.wireOp",EDGE,"E4.sketch_text.stroke-113"),sQuery(id+"F3.wireOp",EDGE,"E4.sketch_text.stroke-114"),sQuery(id+"F3.wireOp",EDGE,"E4.sketch_text.stroke-115"),sQuery(id+"F3.wireOp",EDGE,"E4.sketch_text.stroke-116"),sQuery(id+"F3.wireOp",EDGE,"E4.sketch_text.stroke-117"),sQuery(id+"F3.wireOp",EDGE,"E4.sketch_text.stroke-118"),sQuery(id+"F3.wireOp",EDGE,"E4.sketch_text.stroke-119"),sQuery(id+"F3.wireOp",EDGE,"E4.sketch_text.stroke-120"),sQuery(id+"F3.wireOp",EDGE,"E4.sketch_text.stroke-121"),sQuery(id+"F3.wireOp",EDGE,"E4.sketch_text.stroke-122"),sQuery(id+"F3.wireOp",EDGE,"E4.sketch_text.stroke-123"),sQuery(id+"F3.wireOp",EDGE,"E4.sketch_text.stroke-124"),sQuery(id+"F3.wireOp",EDGE,"E4.sketch_text.stroke-125"),sQuery(id+"F3.wireOp",EDGE,"E4.sketch_text.stroke-126"),sQuery(id+"F3.wireOp",EDGE,"E4.sketch_text.stroke-127"),sQuery(id+"F3.wireOp",EDGE,"E4.sketch_text.stroke-128"),sQuery(id+"F3.wireOp",EDGE,"E4.sketch_text.stroke-129"),sQuery(id+"F3.wireOp",EDGE,"E4.sketch_text.stroke-130"),sQuery(id+"F3.wireOp",EDGE,"E4.sketch_text.stroke-131"),sQuery(id+"F3.wireOp",EDGE,"E4.sketch_text.stroke-132"),sQuery(id+"F3.wireOp",EDGE,"E4.sketch_text.stroke-133"),sQuery(id+"F3.wireOp",EDGE,"E4.sketch_text.stroke-134"),sQuery(id+"F3.wireOp",EDGE,"E4.sketch_text.stroke-135"),sQuery(id+"F3.wireOp",EDGE,"E4.sketch_text.stroke-136"),sQuery(id+"F3.wireOp",EDGE,"E4.sketch_text.stroke-137"),sQuery(id+"F3.wireOp",EDGE,"E4.sketch_text.stroke-138"),sQuery(id+"F3.wireOp",EDGE,"E4.sketch_text.stroke-139"),sQuery(id+"F3.wireOp",EDGE,"E4.sketch_text.stroke-140"),sQuery(id+"F3.wireOp",EDGE,"E4.sketch_text.stroke-141"),sQuery(id+"F3.wireOp",EDGE,"E4.sketch_text.stroke-142"),sQuery(id+"F3.wireOp",EDGE,"E4.sketch_text.stroke-143"),sQuery(id+"F3.wireOp",EDGE,"E4.sketch_text.stroke-144"),sQuery(id+"F3.wireOp",EDGE,"E4.sketch_text.stroke-145"),sQuery(id+"F3.wireOp",EDGE,"E4.sketch_text.stroke-146"),sQuery(id+"F3.wireOp",EDGE,"E4.sketch_text.stroke-147"),sQuery(id+"F3.wireOp",EDGE,"E4.sketch_text.stroke-148"),sQuery(id+"F3.wireOp",EDGE,"E4.sketch_text.stroke-149"),sQuery(id+"F3.wireOp",EDGE,"E4.sketch_text.stroke-150"),sQuery(id+"F3.wireOp",EDGE,"E4.sketch_text.stroke-151"),sQuery(id+"F3.wireOp",EDGE,"E4.sketch_text.stroke-152"),sQuery(id+"F3.wireOp",EDGE,"E4.sketch_text.stroke-153"),sQuery(id+"F3.wireOp",EDGE,"E4.sketch_text.stroke-159"),sQuery(id+"F3.wireOp",EDGE,"E4.sketch_text.stroke-160"),sQuery(id+"F3.wireOp",EDGE,"E4.sketch_text.stroke-161"),sQuery(id+"F3.wireOp",EDGE,"E4.sketch_text.stroke-162"),sQuery(id+"F3.wireOp",EDGE,"E4.sketch_text.stroke-163"),sQuery(id+"F3.wireOp",EDGE,"E4.sketch_text.stroke-164"),sQuery(id+"F3.wireOp",EDGE,"E4.sketch_text.stroke-165"),sQuery(id+"F3.wireOp",EDGE,"E4.sketch_text.stroke-166"),sQuery(id+"F3.wireOp",EDGE,"E4.sketch_text.stroke-167"),sQuery(id+"F3.wireOp",EDGE,"E4.sketch_text.stroke-168"),sQuery(id+"F3.wireOp",EDGE,"E4.sketch_text.stroke-169"),sQuery(id+"F3.wireOp",EDGE,"E4.sketch_text.stroke-170"),sQuery(id+"F3.wireOp",EDGE,"E4.sketch_text.stroke-171"),sQuery(id+"F3.wireOp",EDGE,"E4.sketch_text.stroke-172"),sQuery(id+"F3.wireOp",EDGE,"E4.sketch_text.stroke-173"),sQuery(id+"F3.wireOp",EDGE,"E4.sketch_text.stroke-174"),sQuery(id+"F3.wireOp",EDGE,"E4.sketch_text.stroke-175"),sQuery(id+"F3.wireOp",EDGE,"E4.sketch_text.stroke-176"),sQuery(id+"F3.wireOp",EDGE,"E4.sketch_text.stroke-177"),sQuery(id+"F3.wireOp",EDGE,"E4.sketch_text.stroke-178"),sQuery(id+"F3.wireOp",EDGE,"E4.sketch_text.stroke-179"),sQuery(id+"F3.wireOp",EDGE,"E4.sketch_text.stroke-180"),subQ0,subQ2])],"isStart":true}),makeQuery(id+"F5.opExtrude","SWEPT_FACE",FACE,{"disambiguationData":[OSD([subQ2])]})])],"derivedFrom":makeQuery(id+"F5.opExtrude","CAP_EDGE",EDGE,{"disambiguationData":[OSD([subQ0])],"isStart":true})});}
            var Q4;
            {var subQ0=sQuery(id+"F0.wireOp",EDGE,"E0.top");var subQ1=sQuery(id+"F0.wireOp",EDGE,"E0.bottom");var subQ2=sQuery(id+"F4.wireOp",EDGE,"8007402e-1a4e-4a06-85a5-2af08e553504");Q4=makeQuery(id+"F5.boolean.opBoolean","SPLIT",EDGE,{"disambiguationData":[TD([makeQuery(id+"F1.opExtrude","CAP_FACE",FACE,{"disambiguationData":[OSD([subQ1,subQ0,sQuery(id+"F0.wireOp",EDGE,"E0.left"),sQuery(id+"F0.wireOp",EDGE,"E0.right")])],"isStart":false}),makeQuery(id+"F1.opExtrude","SWEPT_FACE",FACE,{"disambiguationData":[OSD([subQ0])]}),makeQuery(id+"F5.opExtrude","SWEPT_FACE",FACE,{"disambiguationData":[OSD([subQ2])]}),makeQuery(id+"F5.opExtrude","CAP_FACE",FACE,{"disambiguationData":[OSD([subQ1,sQuery(id+"F2.wireOp",EDGE,"E2.sketch_text.stroke-0"),sQuery(id+"F2.wireOp",EDGE,"E2.sketch_text.stroke-1"),sQuery(id+"F2.wireOp",EDGE,"E2.sketch_text.stroke-2"),sQuery(id+"F2.wireOp",EDGE,"E2.sketch_text.stroke-3"),sQuery(id+"F2.wireOp",EDGE,"E2.sketch_text.stroke-4"),sQuery(id+"F2.wireOp",EDGE,"E2.sketch_text.stroke-5"),sQuery(id+"F2.wireOp",EDGE,"E2.sketch_text.stroke-6"),sQuery(id+"F2.wireOp",EDGE,"E2.sketch_text.stroke-7"),sQuery(id+"F2.wireOp",EDGE,"E2.sketch_text.stroke-8"),sQuery(id+"F2.wireOp",EDGE,"E2.sketch_text.stroke-9"),sQuery(id+"F2.wireOp",EDGE,"E2.sketch_text.stroke-10"),sQuery(id+"F2.wireOp",EDGE,"E2.sketch_text.stroke-11"),sQuery(id+"F2.wireOp",EDGE,"E2.sketch_text.stroke-12"),sQuery(id+"F2.wireOp",EDGE,"E2.sketch_text.stroke-13"),sQuery(id+"F2.wireOp",EDGE,"E2.sketch_text.stroke-14"),sQuery(id+"F2.wireOp",EDGE,"E2.sketch_text.stroke-15"),sQuery(id+"F2.wireOp",EDGE,"E2.sketch_text.stroke-16"),sQuery(id+"F2.wireOp",EDGE,"E2.sketch_text.stroke-17"),sQuery(id+"F2.wireOp",EDGE,"E2.sketch_text.stroke-18"),sQuery(id+"F2.wireOp",EDGE,"E2.sketch_text.stroke-19"),sQuery(id+"F2.wireOp",EDGE,"E2.sketch_text.stroke-20"),sQuery(id+"F2.wireOp",EDGE,"E2.sketch_text.stroke-21"),sQuery(id+"F2.wireOp",EDGE,"E2.sketch_text.stroke-22"),sQuery(id+"F2.wireOp",EDGE,"E2.sketch_text.stroke-23"),sQuery(id+"F2.wireOp",EDGE,"E2.sketch_text.stroke-24"),sQuery(id+"F2.wireOp",EDGE,"E2.sketch_text.stroke-25"),sQuery(id+"F2.wireOp",EDGE,"E2.sketch_text.stroke-26"),sQuery(id+"F2.wireOp",EDGE,"E2.sketch_text.stroke-27"),sQuery(id+"F2.wireOp",EDGE,"E2.sketch_text.stroke-28"),sQuery(id+"F2.wireOp",EDGE,"E2.sketch_text.stroke-29"),sQuery(id+"F2.wireOp",EDGE,"E2.sketch_text.stroke-30"),sQuery(id+"F2.wireOp",EDGE,"E2.sketch_text.stroke-31"),sQuery(id+"F2.wireOp",EDGE,"E2.sketch_text.stroke-32"),sQuery(id+"F2.wireOp",EDGE,"E2.sketch_text.stroke-33"),sQuery(id+"F2.wireOp",EDGE,"E2.sketch_text.stroke-34"),sQuery(id+"F2.wireOp",EDGE,"E2.sketch_text.stroke-35"),sQuery(id+"F2.wireOp",EDGE,"E2.sketch_text.stroke-36"),sQuery(id+"F2.wireOp",EDGE,"E2.sketch_text.stroke-37"),sQuery(id+"F2.wireOp",EDGE,"E2.sketch_text.stroke-38"),sQuery(id+"F2.wireOp",EDGE,"E2.sketch_text.stroke-39"),sQuery(id+"F2.wireOp",EDGE,"E2.sketch_text.stroke-40"),sQuery(id+"F2.wireOp",EDGE,"E2.sketch_text.stroke-41"),sQuery(id+"F2.wireOp",EDGE,"E2.sketch_text.stroke-42"),sQuery(id+"F2.wireOp",EDGE,"E2.sketch_text.stroke-43"),sQuery(id+"F2.wireOp",EDGE,"E2.sketch_text.stroke-44"),sQuery(id+"F2.wireOp",EDGE,"E2.sketch_text.stroke-45"),sQuery(id+"F2.wireOp",EDGE,"E2.sketch_text.stroke-46"),sQuery(id+"F2.wireOp",EDGE,"E2.sketch_text.stroke-47"),sQuery(id+"F2.wireOp",EDGE,"E2.sketch_text.stroke-48"),sQuery(id+"F2.wireOp",EDGE,"E2.sketch_text.stroke-49"),sQuery(id+"F2.wireOp",EDGE,"E2.sketch_text.stroke-50"),sQuery(id+"F2.wireOp",EDGE,"E2.sketch_text.stroke-51"),sQuery(id+"F2.wireOp",EDGE,"E2.sketch_text.stroke-52"),sQuery(id+"F2.wireOp",EDGE,"E2.sketch_text.stroke-53"),sQuery(id+"F2.wireOp",EDGE,"E2.sketch_text.stroke-54"),sQuery(id+"F2.wireOp",EDGE,"E2.sketch_text.stroke-55"),sQuery(id+"F2.wireOp",EDGE,"E2.sketch_text.stroke-56"),sQuery(id+"F2.wireOp",EDGE,"E2.sketch_text.stroke-57"),sQuery(id+"F2.wireOp",EDGE,"E2.sketch_text.stroke-58"),sQuery(id+"F2.wireOp",EDGE,"E2.sketch_text.stroke-59"),sQuery(id+"F2.wireOp",EDGE,"E2.sketch_text.stroke-60"),sQuery(id+"F2.wireOp",EDGE,"E2.sketch_text.stroke-61"),sQuery(id+"F2.wireOp",EDGE,"E2.sketch_text.stroke-62"),sQuery(id+"F2.wireOp",EDGE,"E2.sketch_text.stroke-63"),sQuery(id+"F2.wireOp",EDGE,"E2.sketch_text.stroke-64"),sQuery(id+"F2.wireOp",EDGE,"E2.sketch_text.stroke-65"),sQuery(id+"F2.wireOp",EDGE,"E2.sketch_text.stroke-66"),sQuery(id+"F2.wireOp",EDGE,"E2.sketch_text.stroke-67"),sQuery(id+"F2.wireOp",EDGE,"E2.sketch_text.stroke-68"),sQuery(id+"F2.wireOp",EDGE,"E2.sketch_text.stroke-69"),sQuery(id+"F2.wireOp",EDGE,"E2.sketch_text.stroke-70"),sQuery(id+"F2.wireOp",EDGE,"E2.sketch_text.stroke-71"),sQuery(id+"F2.wireOp",EDGE,"E2.sketch_text.stroke-72"),sQuery(id+"F2.wireOp",EDGE,"E2.sketch_text.stroke-73"),sQuery(id+"F2.wireOp",EDGE,"E2.sketch_text.stroke-74"),sQuery(id+"F2.wireOp",EDGE,"E2.sketch_text.stroke-75"),sQuery(id+"F2.wireOp",EDGE,"E2.sketch_text.stroke-76"),sQuery(id+"F2.wireOp",EDGE,"E2.sketch_text.stroke-77"),sQuery(id+"F2.wireOp",EDGE,"E2.sketch_text.stroke-78"),sQuery(id+"F2.wireOp",EDGE,"E2.sketch_text.stroke-79"),sQuery(id+"F2.wireOp",EDGE,"E2.sketch_text.stroke-80"),sQuery(id+"F2.wireOp",EDGE,"E2.sketch_text.stroke-81"),sQuery(id+"F2.wireOp",EDGE,"E2.sketch_text.stroke-82"),sQuery(id+"F2.wireOp",EDGE,"E2.sketch_text.stroke-83"),sQuery(id+"F2.wireOp",EDGE,"E2.sketch_text.stroke-84"),sQuery(id+"F2.wireOp",EDGE,"E2.sketch_text.stroke-85"),sQuery(id+"F2.wireOp",EDGE,"E2.sketch_text.stroke-86"),sQuery(id+"F2.wireOp",EDGE,"E2.sketch_text.stroke-87"),sQuery(id+"F2.wireOp",EDGE,"E2.sketch_text.stroke-88"),sQuery(id+"F2.wireOp",EDGE,"E2.sketch_text.stroke-89"),sQuery(id+"F2.wireOp",EDGE,"E2.sketch_text.stroke-90"),sQuery(id+"F2.wireOp",EDGE,"E2.sketch_text.stroke-91"),sQuery(id+"F2.wireOp",EDGE,"E2.sketch_text.stroke-92"),sQuery(id+"F2.wireOp",EDGE,"E2.sketch_text.stroke-93"),sQuery(id+"F2.wireOp",EDGE,"E2.sketch_text.stroke-94"),sQuery(id+"F2.wireOp",EDGE,"E2.sketch_text.stroke-95"),sQuery(id+"F2.wireOp",EDGE,"E2.sketch_text.stroke-96"),sQuery(id+"F2.wireOp",EDGE,"E2.sketch_text.stroke-97"),sQuery(id+"F2.wireOp",EDGE,"E2.sketch_text.stroke-98"),sQuery(id+"F2.wireOp",EDGE,"E2.sketch_text.stroke-99"),sQuery(id+"F2.wireOp",EDGE,"E2.sketch_text.stroke-100"),sQuery(id+"F2.wireOp",EDGE,"E2.sketch_text.stroke-101"),sQuery(id+"F2.wireOp",EDGE,"E2.sketch_text.stroke-102"),sQuery(id+"F2.wireOp",EDGE,"E2.sketch_text.stroke-103"),sQuery(id+"F2.wireOp",EDGE,"E2.sketch_text.stroke-104"),sQuery(id+"F2.wireOp",EDGE,"E2.sketch_text.stroke-105"),sQuery(id+"F2.wireOp",EDGE,"E2.sketch_text.stroke-106"),sQuery(id+"F2.wireOp",EDGE,"E2.sketch_text.stroke-107"),sQuery(id+"F2.wireOp",EDGE,"E2.sketch_text.stroke-108"),sQuery(id+"F2.wireOp",EDGE,"E2.sketch_text.stroke-109"),sQuery(id+"F2.wireOp",EDGE,"E2.sketch_text.stroke-110"),sQuery(id+"F2.wireOp",EDGE,"E2.sketch_text.stroke-111"),sQuery(id+"F2.wireOp",EDGE,"E2.sketch_text.stroke-112"),sQuery(id+"F2.wireOp",EDGE,"E2.sketch_text.stroke-113"),sQuery(id+"F2.wireOp",EDGE,"E2.sketch_text.stroke-114"),sQuery(id+"F2.wireOp",EDGE,"E2.sketch_text.stroke-115"),sQuery(id+"F2.wireOp",EDGE,"E2.sketch_text.stroke-116"),sQuery(id+"F2.wireOp",EDGE,"E2.sketch_text.stroke-117"),sQuery(id+"F2.wireOp",EDGE,"E2.sketch_text.stroke-118"),sQuery(id+"F2.wireOp",EDGE,"E2.sketch_text.stroke-119"),sQuery(id+"F2.wireOp",EDGE,"E2.sketch_text.stroke-120"),sQuery(id+"F2.wireOp",EDGE,"E2.sketch_text.stroke-121"),sQuery(id+"F2.wireOp",EDGE,"E2.sketch_text.stroke-122"),sQuery(id+"F2.wireOp",EDGE,"E2.sketch_text.stroke-123"),sQuery(id+"F2.wireOp",EDGE,"E2.sketch_text.stroke-124"),sQuery(id+"F2.wireOp",EDGE,"E2.sketch_text.stroke-125"),sQuery(id+"F2.wireOp",EDGE,"E2.sketch_text.stroke-126"),sQuery(id+"F2.wireOp",EDGE,"E2.sketch_text.stroke-127"),sQuery(id+"F2.wireOp",EDGE,"E2.sketch_text.stroke-128"),sQuery(id+"F2.wireOp",EDGE,"E2.sketch_text.stroke-129"),sQuery(id+"F2.wireOp",EDGE,"E2.sketch_text.stroke-130"),sQuery(id+"F2.wireOp",EDGE,"E2.sketch_text.stroke-131"),sQuery(id+"F2.wireOp",EDGE,"E2.sketch_text.stroke-132"),sQuery(id+"F2.wireOp",EDGE,"E2.sketch_text.stroke-133"),sQuery(id+"F2.wireOp",EDGE,"E2.sketch_text.stroke-134"),sQuery(id+"F2.wireOp",EDGE,"E2.sketch_text.stroke-135"),sQuery(id+"F2.wireOp",EDGE,"E2.sketch_text.stroke-136"),sQuery(id+"F2.wireOp",EDGE,"E2.sketch_text.stroke-137"),sQuery(id+"F2.wireOp",EDGE,"E2.sketch_text.stroke-138"),sQuery(id+"F2.wireOp",EDGE,"E2.sketch_text.stroke-139"),sQuery(id+"F2.wireOp",EDGE,"E2.sketch_text.stroke-140"),sQuery(id+"F2.wireOp",EDGE,"E2.sketch_text.stroke-141"),sQuery(id+"F2.wireOp",EDGE,"E2.sketch_text.stroke-142"),sQuery(id+"F2.wireOp",EDGE,"E2.sketch_text.stroke-143"),sQuery(id+"F2.wireOp",EDGE,"E2.sketch_text.stroke-144"),sQuery(id+"F2.wireOp",EDGE,"E2.sketch_text.stroke-145"),sQuery(id+"F2.wireOp",EDGE,"E2.sketch_text.stroke-146"),sQuery(id+"F2.wireOp",EDGE,"E2.sketch_text.stroke-147"),sQuery(id+"F2.wireOp",EDGE,"E2.sketch_text.stroke-148"),sQuery(id+"F2.wireOp",EDGE,"E2.sketch_text.stroke-149"),sQuery(id+"F2.wireOp",EDGE,"E2.sketch_text.stroke-150"),sQuery(id+"F2.wireOp",EDGE,"E2.sketch_text.stroke-151"),sQuery(id+"F2.wireOp",EDGE,"E2.sketch_text.stroke-152"),sQuery(id+"F2.wireOp",EDGE,"E2.sketch_text.stroke-153"),sQuery(id+"F2.wireOp",EDGE,"E2.sketch_text.stroke-154"),sQuery(id+"F2.wireOp",EDGE,"E2.sketch_text.stroke-155"),sQuery(id+"F2.wireOp",EDGE,"E2.sketch_text.stroke-156"),sQuery(id+"F2.wireOp",EDGE,"E2.sketch_text.stroke-157"),sQuery(id+"F2.wireOp",EDGE,"E2.sketch_text.stroke-158"),sQuery(id+"F2.wireOp",EDGE,"E2.sketch_text.stroke-159"),sQuery(id+"F2.wireOp",EDGE,"E2.sketch_text.stroke-160"),sQuery(id+"F2.wireOp",EDGE,"E2.sketch_text.stroke-161"),sQuery(id+"F2.wireOp",EDGE,"E2.sketch_text.stroke-162"),sQuery(id+"F2.wireOp",EDGE,"E2.sketch_text.stroke-163"),sQuery(id+"F2.wireOp",EDGE,"E2.sketch_text.stroke-164"),sQuery(id+"F2.wireOp",EDGE,"E2.sketch_text.stroke-165"),sQuery(id+"F2.wireOp",EDGE,"E2.sketch_text.stroke-166"),sQuery(id+"F2.wireOp",EDGE,"E2.sketch_text.stroke-167"),sQuery(id+"F2.wireOp",EDGE,"E2.sketch_text.stroke-168"),sQuery(id+"F2.wireOp",EDGE,"E2.sketch_text.stroke-169"),sQuery(id+"F2.wireOp",EDGE,"E2.sketch_text.stroke-170"),sQuery(id+"F2.wireOp",EDGE,"E2.sketch_text.stroke-171"),sQuery(id+"F2.wireOp",EDGE,"E2.sketch_text.stroke-172"),sQuery(id+"F2.wireOp",EDGE,"E2.sketch_text.stroke-173"),sQuery(id+"F3.wireOp",EDGE,"E4.sketch_text.stroke-0"),sQuery(id+"F3.wireOp",EDGE,"E4.sketch_text.stroke-1"),sQuery(id+"F3.wireOp",EDGE,"E4.sketch_text.stroke-2"),sQuery(id+"F3.wireOp",EDGE,"E4.sketch_text.stroke-3"),sQuery(id+"F3.wireOp",EDGE,"E4.sketch_text.stroke-4"),sQuery(id+"F3.wireOp",EDGE,"E4.sketch_text.stroke-5"),sQuery(id+"F3.wireOp",EDGE,"E4.sketch_text.stroke-6"),sQuery(id+"F3.wireOp",EDGE,"E4.sketch_text.stroke-7"),sQuery(id+"F3.wireOp",EDGE,"E4.sketch_text.stroke-8"),sQuery(id+"F3.wireOp",EDGE,"E4.sketch_text.stroke-9"),sQuery(id+"F3.wireOp",EDGE,"E4.sketch_text.stroke-10"),sQuery(id+"F3.wireOp",EDGE,"E4.sketch_text.stroke-11"),sQuery(id+"F3.wireOp",EDGE,"E4.sketch_text.stroke-12"),sQuery(id+"F3.wireOp",EDGE,"E4.sketch_text.stroke-13"),sQuery(id+"F3.wireOp",EDGE,"E4.sketch_text.stroke-14"),sQuery(id+"F3.wireOp",EDGE,"E4.sketch_text.stroke-15"),sQuery(id+"F3.wireOp",EDGE,"E4.sketch_text.stroke-16"),sQuery(id+"F3.wireOp",EDGE,"E4.sketch_text.stroke-17"),sQuery(id+"F3.wireOp",EDGE,"E4.sketch_text.stroke-18"),sQuery(id+"F3.wireOp",EDGE,"E4.sketch_text.stroke-19"),sQuery(id+"F3.wireOp",EDGE,"E4.sketch_text.stroke-20"),sQuery(id+"F3.wireOp",EDGE,"E4.sketch_text.stroke-21"),sQuery(id+"F3.wireOp",EDGE,"E4.sketch_text.stroke-22"),sQuery(id+"F3.wireOp",EDGE,"E4.sketch_text.stroke-23"),sQuery(id+"F3.wireOp",EDGE,"E4.sketch_text.stroke-24"),sQuery(id+"F3.wireOp",EDGE,"E4.sketch_text.stroke-25"),sQuery(id+"F3.wireOp",EDGE,"E4.sketch_text.stroke-26"),sQuery(id+"F3.wireOp",EDGE,"E4.sketch_text.stroke-27"),sQuery(id+"F3.wireOp",EDGE,"E4.sketch_text.stroke-28"),sQuery(id+"F3.wireOp",EDGE,"E4.sketch_text.stroke-29"),sQuery(id+"F3.wireOp",EDGE,"E4.sketch_text.stroke-30"),sQuery(id+"F3.wireOp",EDGE,"E4.sketch_text.stroke-31"),sQuery(id+"F3.wireOp",EDGE,"E4.sketch_text.stroke-32"),sQuery(id+"F3.wireOp",EDGE,"E4.sketch_text.stroke-33"),sQuery(id+"F3.wireOp",EDGE,"E4.sketch_text.stroke-34"),sQuery(id+"F3.wireOp",EDGE,"E4.sketch_text.stroke-35"),sQuery(id+"F3.wireOp",EDGE,"E4.sketch_text.stroke-36"),sQuery(id+"F3.wireOp",EDGE,"E4.sketch_text.stroke-37"),sQuery(id+"F3.wireOp",EDGE,"E4.sketch_text.stroke-38"),sQuery(id+"F3.wireOp",EDGE,"E4.sketch_text.stroke-39"),sQuery(id+"F3.wireOp",EDGE,"E4.sketch_text.stroke-40"),sQuery(id+"F3.wireOp",EDGE,"E4.sketch_text.stroke-41"),sQuery(id+"F3.wireOp",EDGE,"E4.sketch_text.stroke-42"),sQuery(id+"F3.wireOp",EDGE,"E4.sketch_text.stroke-43"),sQuery(id+"F3.wireOp",EDGE,"E4.sketch_text.stroke-44"),sQuery(id+"F3.wireOp",EDGE,"E4.sketch_text.stroke-45"),sQuery(id+"F3.wireOp",EDGE,"E4.sketch_text.stroke-46"),sQuery(id+"F3.wireOp",EDGE,"E4.sketch_text.stroke-47"),sQuery(id+"F3.wireOp",EDGE,"E4.sketch_text.stroke-48"),sQuery(id+"F3.wireOp",EDGE,"E4.sketch_text.stroke-49"),sQuery(id+"F3.wireOp",EDGE,"E4.sketch_text.stroke-50"),sQuery(id+"F3.wireOp",EDGE,"E4.sketch_text.stroke-51"),sQuery(id+"F3.wireOp",EDGE,"E4.sketch_text.stroke-52"),sQuery(id+"F3.wireOp",EDGE,"E4.sketch_text.stroke-53"),sQuery(id+"F3.wireOp",EDGE,"E4.sketch_text.stroke-54"),sQuery(id+"F3.wireOp",EDGE,"E4.sketch_text.stroke-55"),sQuery(id+"F3.wireOp",EDGE,"E4.sketch_text.stroke-56"),sQuery(id+"F3.wireOp",EDGE,"E4.sketch_text.stroke-57"),sQuery(id+"F3.wireOp",EDGE,"E4.sketch_text.stroke-58"),sQuery(id+"F3.wireOp",EDGE,"E4.sketch_text.stroke-59"),sQuery(id+"F3.wireOp",EDGE,"E4.sketch_text.stroke-60"),sQuery(id+"F3.wireOp",EDGE,"E4.sketch_text.stroke-61"),sQuery(id+"F3.wireOp",EDGE,"E4.sketch_text.stroke-62"),sQuery(id+"F3.wireOp",EDGE,"E4.sketch_text.stroke-71"),sQuery(id+"F3.wireOp",EDGE,"E4.sketch_text.stroke-72"),sQuery(id+"F3.wireOp",EDGE,"E4.sketch_text.stroke-73"),sQuery(id+"F3.wireOp",EDGE,"E4.sketch_text.stroke-74"),sQuery(id+"F3.wireOp",EDGE,"E4.sketch_text.stroke-75"),sQuery(id+"F3.wireOp",EDGE,"E4.sketch_text.stroke-76"),sQuery(id+"F3.wireOp",EDGE,"E4.sketch_text.stroke-77"),sQuery(id+"F3.wireOp",EDGE,"E4.sketch_text.stroke-78"),sQuery(id+"F3.wireOp",EDGE,"E4.sketch_text.stroke-79"),sQuery(id+"F3.wireOp",EDGE,"E4.sketch_text.stroke-80"),sQuery(id+"F3.wireOp",EDGE,"E4.sketch_text.stroke-81"),sQuery(id+"F3.wireOp",EDGE,"E4.sketch_text.stroke-82"),sQuery(id+"F3.wireOp",EDGE,"E4.sketch_text.stroke-83"),sQuery(id+"F3.wireOp",EDGE,"E4.sketch_text.stroke-84"),sQuery(id+"F3.wireOp",EDGE,"E4.sketch_text.stroke-85"),sQuery(id+"F3.wireOp",EDGE,"E4.sketch_text.stroke-86"),sQuery(id+"F3.wireOp",EDGE,"E4.sketch_text.stroke-87"),sQuery(id+"F3.wireOp",EDGE,"E4.sketch_text.stroke-88"),sQuery(id+"F3.wireOp",EDGE,"E4.sketch_text.stroke-89"),sQuery(id+"F3.wireOp",EDGE,"E4.sketch_text.stroke-90"),sQuery(id+"F3.wireOp",EDGE,"E4.sketch_text.stroke-91"),sQuery(id+"F3.wireOp",EDGE,"E4.sketch_text.stroke-92"),sQuery(id+"F3.wireOp",EDGE,"E4.sketch_text.stroke-93"),sQuery(id+"F3.wireOp",EDGE,"E4.sketch_text.stroke-94"),sQuery(id+"F3.wireOp",EDGE,"E4.sketch_text.stroke-95"),sQuery(id+"F3.wireOp",EDGE,"E4.sketch_text.stroke-96"),sQuery(id+"F3.wireOp",EDGE,"E4.sketch_text.stroke-97"),sQuery(id+"F3.wireOp",EDGE,"E4.sketch_text.stroke-103"),sQuery(id+"F3.wireOp",EDGE,"E4.sketch_text.stroke-104"),sQuery(id+"F3.wireOp",EDGE,"E4.sketch_text.stroke-105"),sQuery(id+"F3.wireOp",EDGE,"E4.sketch_text.stroke-106"),sQuery(id+"F3.wireOp",EDGE,"E4.sketch_text.stroke-107"),sQuery(id+"F3.wireOp",EDGE,"E4.sketch_text.stroke-108"),sQuery(id+"F3.wireOp",EDGE,"E4.sketch_text.stroke-109"),sQuery(id+"F3.wireOp",EDGE,"E4.sketch_text.stroke-110"),sQuery(id+"F3.wireOp",EDGE,"E4.sketch_text.stroke-111"),sQuery(id+"F3.wireOp",EDGE,"E4.sketch_text.stroke-112"),sQuery(id+"F3.wireOp",EDGE,"E4.sketch_text.stroke-113"),sQuery(id+"F3.wireOp",EDGE,"E4.sketch_text.stroke-114"),sQuery(id+"F3.wireOp",EDGE,"E4.sketch_text.stroke-115"),sQuery(id+"F3.wireOp",EDGE,"E4.sketch_text.stroke-116"),sQuery(id+"F3.wireOp",EDGE,"E4.sketch_text.stroke-117"),sQuery(id+"F3.wireOp",EDGE,"E4.sketch_text.stroke-118"),sQuery(id+"F3.wireOp",EDGE,"E4.sketch_text.stroke-119"),sQuery(id+"F3.wireOp",EDGE,"E4.sketch_text.stroke-120"),sQuery(id+"F3.wireOp",EDGE,"E4.sketch_text.stroke-121"),sQuery(id+"F3.wireOp",EDGE,"E4.sketch_text.stroke-122"),sQuery(id+"F3.wireOp",EDGE,"E4.sketch_text.stroke-123"),sQuery(id+"F3.wireOp",EDGE,"E4.sketch_text.stroke-124"),sQuery(id+"F3.wireOp",EDGE,"E4.sketch_text.stroke-125"),sQuery(id+"F3.wireOp",EDGE,"E4.sketch_text.stroke-126"),sQuery(id+"F3.wireOp",EDGE,"E4.sketch_text.stroke-127"),sQuery(id+"F3.wireOp",EDGE,"E4.sketch_text.stroke-128"),sQuery(id+"F3.wireOp",EDGE,"E4.sketch_text.stroke-129"),sQuery(id+"F3.wireOp",EDGE,"E4.sketch_text.stroke-130"),sQuery(id+"F3.wireOp",EDGE,"E4.sketch_text.stroke-131"),sQuery(id+"F3.wireOp",EDGE,"E4.sketch_text.stroke-132"),sQuery(id+"F3.wireOp",EDGE,"E4.sketch_text.stroke-133"),sQuery(id+"F3.wireOp",EDGE,"E4.sketch_text.stroke-134"),sQuery(id+"F3.wireOp",EDGE,"E4.sketch_text.stroke-135"),sQuery(id+"F3.wireOp",EDGE,"E4.sketch_text.stroke-136"),sQuery(id+"F3.wireOp",EDGE,"E4.sketch_text.stroke-137"),sQuery(id+"F3.wireOp",EDGE,"E4.sketch_text.stroke-138"),sQuery(id+"F3.wireOp",EDGE,"E4.sketch_text.stroke-139"),sQuery(id+"F3.wireOp",EDGE,"E4.sketch_text.stroke-140"),sQuery(id+"F3.wireOp",EDGE,"E4.sketch_text.stroke-141"),sQuery(id+"F3.wireOp",EDGE,"E4.sketch_text.stroke-142"),sQuery(id+"F3.wireOp",EDGE,"E4.sketch_text.stroke-143"),sQuery(id+"F3.wireOp",EDGE,"E4.sketch_text.stroke-144"),sQuery(id+"F3.wireOp",EDGE,"E4.sketch_text.stroke-145"),sQuery(id+"F3.wireOp",EDGE,"E4.sketch_text.stroke-146"),sQuery(id+"F3.wireOp",EDGE,"E4.sketch_text.stroke-147"),sQuery(id+"F3.wireOp",EDGE,"E4.sketch_text.stroke-148"),sQuery(id+"F3.wireOp",EDGE,"E4.sketch_text.stroke-149"),sQuery(id+"F3.wireOp",EDGE,"E4.sketch_text.stroke-150"),sQuery(id+"F3.wireOp",EDGE,"E4.sketch_text.stroke-151"),sQuery(id+"F3.wireOp",EDGE,"E4.sketch_text.stroke-152"),sQuery(id+"F3.wireOp",EDGE,"E4.sketch_text.stroke-153"),sQuery(id+"F3.wireOp",EDGE,"E4.sketch_text.stroke-159"),sQuery(id+"F3.wireOp",EDGE,"E4.sketch_text.stroke-160"),sQuery(id+"F3.wireOp",EDGE,"E4.sketch_text.stroke-161"),sQuery(id+"F3.wireOp",EDGE,"E4.sketch_text.stroke-162"),sQuery(id+"F3.wireOp",EDGE,"E4.sketch_text.stroke-163"),sQuery(id+"F3.wireOp",EDGE,"E4.sketch_text.stroke-164"),sQuery(id+"F3.wireOp",EDGE,"E4.sketch_text.stroke-165"),sQuery(id+"F3.wireOp",EDGE,"E4.sketch_text.stroke-166"),sQuery(id+"F3.wireOp",EDGE,"E4.sketch_text.stroke-167"),sQuery(id+"F3.wireOp",EDGE,"E4.sketch_text.stroke-168"),sQuery(id+"F3.wireOp",EDGE,"E4.sketch_text.stroke-169"),sQuery(id+"F3.wireOp",EDGE,"E4.sketch_text.stroke-170"),sQuery(id+"F3.wireOp",EDGE,"E4.sketch_text.stroke-171"),sQuery(id+"F3.wireOp",EDGE,"E4.sketch_text.stroke-172"),sQuery(id+"F3.wireOp",EDGE,"E4.sketch_text.stroke-173"),sQuery(id+"F3.wireOp",EDGE,"E4.sketch_text.stroke-174"),sQuery(id+"F3.wireOp",EDGE,"E4.sketch_text.stroke-175"),sQuery(id+"F3.wireOp",EDGE,"E4.sketch_text.stroke-176"),sQuery(id+"F3.wireOp",EDGE,"E4.sketch_text.stroke-177"),sQuery(id+"F3.wireOp",EDGE,"E4.sketch_text.stroke-178"),sQuery(id+"F3.wireOp",EDGE,"E4.sketch_text.stroke-179"),sQuery(id+"F3.wireOp",EDGE,"E4.sketch_text.stroke-180"),subQ2,sQuery(id+"F4.wireOp",EDGE,"6ee83ff3-586e-4dbe-aaea-af71240543bd")])],"isStart":true})]),OD(1.0)],"derivedFrom":makeQuery(id+"F1.opExtrude","CAP_EDGE",EDGE,{"disambiguationData":[OSD([subQ0])],"isStart":false})});}
            var Q5;
            {var subQ0=sQuery(id+"F0.wireOp",EDGE,"E0.top");var subQ1=sQuery(id+"F0.wireOp",EDGE,"E0.bottom");var subQ2=sQuery(id+"F4.wireOp",EDGE,"8007402e-1a4e-4a06-85a5-2af08e553504");Q5=makeQuery(id+"F5.boolean.opBoolean","SPLIT",EDGE,{"disambiguationData":[TD([makeQuery(id+"F1.opExtrude","CAP_FACE",FACE,{"disambiguationData":[OSD([subQ1,subQ0,sQuery(id+"F0.wireOp",EDGE,"E0.left"),sQuery(id+"F0.wireOp",EDGE,"E0.right")])],"isStart":false}),makeQuery(id+"F1.opExtrude","SWEPT_FACE",FACE,{"disambiguationData":[OSD([subQ0])]}),makeQuery(id+"F5.opExtrude","SWEPT_FACE",FACE,{"disambiguationData":[OSD([subQ2])]}),makeQuery(id+"F5.opExtrude","CAP_FACE",FACE,{"disambiguationData":[OSD([subQ1,sQuery(id+"F2.wireOp",EDGE,"E2.sketch_text.stroke-0"),sQuery(id+"F2.wireOp",EDGE,"E2.sketch_text.stroke-1"),sQuery(id+"F2.wireOp",EDGE,"E2.sketch_text.stroke-2"),sQuery(id+"F2.wireOp",EDGE,"E2.sketch_text.stroke-3"),sQuery(id+"F2.wireOp",EDGE,"E2.sketch_text.stroke-4"),sQuery(id+"F2.wireOp",EDGE,"E2.sketch_text.stroke-5"),sQuery(id+"F2.wireOp",EDGE,"E2.sketch_text.stroke-6"),sQuery(id+"F2.wireOp",EDGE,"E2.sketch_text.stroke-7"),sQuery(id+"F2.wireOp",EDGE,"E2.sketch_text.stroke-8"),sQuery(id+"F2.wireOp",EDGE,"E2.sketch_text.stroke-9"),sQuery(id+"F2.wireOp",EDGE,"E2.sketch_text.stroke-10"),sQuery(id+"F2.wireOp",EDGE,"E2.sketch_text.stroke-11"),sQuery(id+"F2.wireOp",EDGE,"E2.sketch_text.stroke-12"),sQuery(id+"F2.wireOp",EDGE,"E2.sketch_text.stroke-13"),sQuery(id+"F2.wireOp",EDGE,"E2.sketch_text.stroke-14"),sQuery(id+"F2.wireOp",EDGE,"E2.sketch_text.stroke-15"),sQuery(id+"F2.wireOp",EDGE,"E2.sketch_text.stroke-16"),sQuery(id+"F2.wireOp",EDGE,"E2.sketch_text.stroke-17"),sQuery(id+"F2.wireOp",EDGE,"E2.sketch_text.stroke-18"),sQuery(id+"F2.wireOp",EDGE,"E2.sketch_text.stroke-19"),sQuery(id+"F2.wireOp",EDGE,"E2.sketch_text.stroke-20"),sQuery(id+"F2.wireOp",EDGE,"E2.sketch_text.stroke-21"),sQuery(id+"F2.wireOp",EDGE,"E2.sketch_text.stroke-22"),sQuery(id+"F2.wireOp",EDGE,"E2.sketch_text.stroke-23"),sQuery(id+"F2.wireOp",EDGE,"E2.sketch_text.stroke-24"),sQuery(id+"F2.wireOp",EDGE,"E2.sketch_text.stroke-25"),sQuery(id+"F2.wireOp",EDGE,"E2.sketch_text.stroke-26"),sQuery(id+"F2.wireOp",EDGE,"E2.sketch_text.stroke-27"),sQuery(id+"F2.wireOp",EDGE,"E2.sketch_text.stroke-28"),sQuery(id+"F2.wireOp",EDGE,"E2.sketch_text.stroke-29"),sQuery(id+"F2.wireOp",EDGE,"E2.sketch_text.stroke-30"),sQuery(id+"F2.wireOp",EDGE,"E2.sketch_text.stroke-31"),sQuery(id+"F2.wireOp",EDGE,"E2.sketch_text.stroke-32"),sQuery(id+"F2.wireOp",EDGE,"E2.sketch_text.stroke-33"),sQuery(id+"F2.wireOp",EDGE,"E2.sketch_text.stroke-34"),sQuery(id+"F2.wireOp",EDGE,"E2.sketch_text.stroke-35"),sQuery(id+"F2.wireOp",EDGE,"E2.sketch_text.stroke-36"),sQuery(id+"F2.wireOp",EDGE,"E2.sketch_text.stroke-37"),sQuery(id+"F2.wireOp",EDGE,"E2.sketch_text.stroke-38"),sQuery(id+"F2.wireOp",EDGE,"E2.sketch_text.stroke-39"),sQuery(id+"F2.wireOp",EDGE,"E2.sketch_text.stroke-40"),sQuery(id+"F2.wireOp",EDGE,"E2.sketch_text.stroke-41"),sQuery(id+"F2.wireOp",EDGE,"E2.sketch_text.stroke-42"),sQuery(id+"F2.wireOp",EDGE,"E2.sketch_text.stroke-43"),sQuery(id+"F2.wireOp",EDGE,"E2.sketch_text.stroke-44"),sQuery(id+"F2.wireOp",EDGE,"E2.sketch_text.stroke-45"),sQuery(id+"F2.wireOp",EDGE,"E2.sketch_text.stroke-46"),sQuery(id+"F2.wireOp",EDGE,"E2.sketch_text.stroke-47"),sQuery(id+"F2.wireOp",EDGE,"E2.sketch_text.stroke-48"),sQuery(id+"F2.wireOp",EDGE,"E2.sketch_text.stroke-49"),sQuery(id+"F2.wireOp",EDGE,"E2.sketch_text.stroke-50"),sQuery(id+"F2.wireOp",EDGE,"E2.sketch_text.stroke-51"),sQuery(id+"F2.wireOp",EDGE,"E2.sketch_text.stroke-52"),sQuery(id+"F2.wireOp",EDGE,"E2.sketch_text.stroke-53"),sQuery(id+"F2.wireOp",EDGE,"E2.sketch_text.stroke-54"),sQuery(id+"F2.wireOp",EDGE,"E2.sketch_text.stroke-55"),sQuery(id+"F2.wireOp",EDGE,"E2.sketch_text.stroke-56"),sQuery(id+"F2.wireOp",EDGE,"E2.sketch_text.stroke-57"),sQuery(id+"F2.wireOp",EDGE,"E2.sketch_text.stroke-58"),sQuery(id+"F2.wireOp",EDGE,"E2.sketch_text.stroke-59"),sQuery(id+"F2.wireOp",EDGE,"E2.sketch_text.stroke-60"),sQuery(id+"F2.wireOp",EDGE,"E2.sketch_text.stroke-61"),sQuery(id+"F2.wireOp",EDGE,"E2.sketch_text.stroke-62"),sQuery(id+"F2.wireOp",EDGE,"E2.sketch_text.stroke-63"),sQuery(id+"F2.wireOp",EDGE,"E2.sketch_text.stroke-64"),sQuery(id+"F2.wireOp",EDGE,"E2.sketch_text.stroke-65"),sQuery(id+"F2.wireOp",EDGE,"E2.sketch_text.stroke-66"),sQuery(id+"F2.wireOp",EDGE,"E2.sketch_text.stroke-67"),sQuery(id+"F2.wireOp",EDGE,"E2.sketch_text.stroke-68"),sQuery(id+"F2.wireOp",EDGE,"E2.sketch_text.stroke-69"),sQuery(id+"F2.wireOp",EDGE,"E2.sketch_text.stroke-70"),sQuery(id+"F2.wireOp",EDGE,"E2.sketch_text.stroke-71"),sQuery(id+"F2.wireOp",EDGE,"E2.sketch_text.stroke-72"),sQuery(id+"F2.wireOp",EDGE,"E2.sketch_text.stroke-73"),sQuery(id+"F2.wireOp",EDGE,"E2.sketch_text.stroke-74"),sQuery(id+"F2.wireOp",EDGE,"E2.sketch_text.stroke-75"),sQuery(id+"F2.wireOp",EDGE,"E2.sketch_text.stroke-76"),sQuery(id+"F2.wireOp",EDGE,"E2.sketch_text.stroke-77"),sQuery(id+"F2.wireOp",EDGE,"E2.sketch_text.stroke-78"),sQuery(id+"F2.wireOp",EDGE,"E2.sketch_text.stroke-79"),sQuery(id+"F2.wireOp",EDGE,"E2.sketch_text.stroke-80"),sQuery(id+"F2.wireOp",EDGE,"E2.sketch_text.stroke-81"),sQuery(id+"F2.wireOp",EDGE,"E2.sketch_text.stroke-82"),sQuery(id+"F2.wireOp",EDGE,"E2.sketch_text.stroke-83"),sQuery(id+"F2.wireOp",EDGE,"E2.sketch_text.stroke-84"),sQuery(id+"F2.wireOp",EDGE,"E2.sketch_text.stroke-85"),sQuery(id+"F2.wireOp",EDGE,"E2.sketch_text.stroke-86"),sQuery(id+"F2.wireOp",EDGE,"E2.sketch_text.stroke-87"),sQuery(id+"F2.wireOp",EDGE,"E2.sketch_text.stroke-88"),sQuery(id+"F2.wireOp",EDGE,"E2.sketch_text.stroke-89"),sQuery(id+"F2.wireOp",EDGE,"E2.sketch_text.stroke-90"),sQuery(id+"F2.wireOp",EDGE,"E2.sketch_text.stroke-91"),sQuery(id+"F2.wireOp",EDGE,"E2.sketch_text.stroke-92"),sQuery(id+"F2.wireOp",EDGE,"E2.sketch_text.stroke-93"),sQuery(id+"F2.wireOp",EDGE,"E2.sketch_text.stroke-94"),sQuery(id+"F2.wireOp",EDGE,"E2.sketch_text.stroke-95"),sQuery(id+"F2.wireOp",EDGE,"E2.sketch_text.stroke-96"),sQuery(id+"F2.wireOp",EDGE,"E2.sketch_text.stroke-97"),sQuery(id+"F2.wireOp",EDGE,"E2.sketch_text.stroke-98"),sQuery(id+"F2.wireOp",EDGE,"E2.sketch_text.stroke-99"),sQuery(id+"F2.wireOp",EDGE,"E2.sketch_text.stroke-100"),sQuery(id+"F2.wireOp",EDGE,"E2.sketch_text.stroke-101"),sQuery(id+"F2.wireOp",EDGE,"E2.sketch_text.stroke-102"),sQuery(id+"F2.wireOp",EDGE,"E2.sketch_text.stroke-103"),sQuery(id+"F2.wireOp",EDGE,"E2.sketch_text.stroke-104"),sQuery(id+"F2.wireOp",EDGE,"E2.sketch_text.stroke-105"),sQuery(id+"F2.wireOp",EDGE,"E2.sketch_text.stroke-106"),sQuery(id+"F2.wireOp",EDGE,"E2.sketch_text.stroke-107"),sQuery(id+"F2.wireOp",EDGE,"E2.sketch_text.stroke-108"),sQuery(id+"F2.wireOp",EDGE,"E2.sketch_text.stroke-109"),sQuery(id+"F2.wireOp",EDGE,"E2.sketch_text.stroke-110"),sQuery(id+"F2.wireOp",EDGE,"E2.sketch_text.stroke-111"),sQuery(id+"F2.wireOp",EDGE,"E2.sketch_text.stroke-112"),sQuery(id+"F2.wireOp",EDGE,"E2.sketch_text.stroke-113"),sQuery(id+"F2.wireOp",EDGE,"E2.sketch_text.stroke-114"),sQuery(id+"F2.wireOp",EDGE,"E2.sketch_text.stroke-115"),sQuery(id+"F2.wireOp",EDGE,"E2.sketch_text.stroke-116"),sQuery(id+"F2.wireOp",EDGE,"E2.sketch_text.stroke-117"),sQuery(id+"F2.wireOp",EDGE,"E2.sketch_text.stroke-118"),sQuery(id+"F2.wireOp",EDGE,"E2.sketch_text.stroke-119"),sQuery(id+"F2.wireOp",EDGE,"E2.sketch_text.stroke-120"),sQuery(id+"F2.wireOp",EDGE,"E2.sketch_text.stroke-121"),sQuery(id+"F2.wireOp",EDGE,"E2.sketch_text.stroke-122"),sQuery(id+"F2.wireOp",EDGE,"E2.sketch_text.stroke-123"),sQuery(id+"F2.wireOp",EDGE,"E2.sketch_text.stroke-124"),sQuery(id+"F2.wireOp",EDGE,"E2.sketch_text.stroke-125"),sQuery(id+"F2.wireOp",EDGE,"E2.sketch_text.stroke-126"),sQuery(id+"F2.wireOp",EDGE,"E2.sketch_text.stroke-127"),sQuery(id+"F2.wireOp",EDGE,"E2.sketch_text.stroke-128"),sQuery(id+"F2.wireOp",EDGE,"E2.sketch_text.stroke-129"),sQuery(id+"F2.wireOp",EDGE,"E2.sketch_text.stroke-130"),sQuery(id+"F2.wireOp",EDGE,"E2.sketch_text.stroke-131"),sQuery(id+"F2.wireOp",EDGE,"E2.sketch_text.stroke-132"),sQuery(id+"F2.wireOp",EDGE,"E2.sketch_text.stroke-133"),sQuery(id+"F2.wireOp",EDGE,"E2.sketch_text.stroke-134"),sQuery(id+"F2.wireOp",EDGE,"E2.sketch_text.stroke-135"),sQuery(id+"F2.wireOp",EDGE,"E2.sketch_text.stroke-136"),sQuery(id+"F2.wireOp",EDGE,"E2.sketch_text.stroke-137"),sQuery(id+"F2.wireOp",EDGE,"E2.sketch_text.stroke-138"),sQuery(id+"F2.wireOp",EDGE,"E2.sketch_text.stroke-139"),sQuery(id+"F2.wireOp",EDGE,"E2.sketch_text.stroke-140"),sQuery(id+"F2.wireOp",EDGE,"E2.sketch_text.stroke-141"),sQuery(id+"F2.wireOp",EDGE,"E2.sketch_text.stroke-142"),sQuery(id+"F2.wireOp",EDGE,"E2.sketch_text.stroke-143"),sQuery(id+"F2.wireOp",EDGE,"E2.sketch_text.stroke-144"),sQuery(id+"F2.wireOp",EDGE,"E2.sketch_text.stroke-145"),sQuery(id+"F2.wireOp",EDGE,"E2.sketch_text.stroke-146"),sQuery(id+"F2.wireOp",EDGE,"E2.sketch_text.stroke-147"),sQuery(id+"F2.wireOp",EDGE,"E2.sketch_text.stroke-148"),sQuery(id+"F2.wireOp",EDGE,"E2.sketch_text.stroke-149"),sQuery(id+"F2.wireOp",EDGE,"E2.sketch_text.stroke-150"),sQuery(id+"F2.wireOp",EDGE,"E2.sketch_text.stroke-151"),sQuery(id+"F2.wireOp",EDGE,"E2.sketch_text.stroke-152"),sQuery(id+"F2.wireOp",EDGE,"E2.sketch_text.stroke-153"),sQuery(id+"F2.wireOp",EDGE,"E2.sketch_text.stroke-154"),sQuery(id+"F2.wireOp",EDGE,"E2.sketch_text.stroke-155"),sQuery(id+"F2.wireOp",EDGE,"E2.sketch_text.stroke-156"),sQuery(id+"F2.wireOp",EDGE,"E2.sketch_text.stroke-157"),sQuery(id+"F2.wireOp",EDGE,"E2.sketch_text.stroke-158"),sQuery(id+"F2.wireOp",EDGE,"E2.sketch_text.stroke-159"),sQuery(id+"F2.wireOp",EDGE,"E2.sketch_text.stroke-160"),sQuery(id+"F2.wireOp",EDGE,"E2.sketch_text.stroke-161"),sQuery(id+"F2.wireOp",EDGE,"E2.sketch_text.stroke-162"),sQuery(id+"F2.wireOp",EDGE,"E2.sketch_text.stroke-163"),sQuery(id+"F2.wireOp",EDGE,"E2.sketch_text.stroke-164"),sQuery(id+"F2.wireOp",EDGE,"E2.sketch_text.stroke-165"),sQuery(id+"F2.wireOp",EDGE,"E2.sketch_text.stroke-166"),sQuery(id+"F2.wireOp",EDGE,"E2.sketch_text.stroke-167"),sQuery(id+"F2.wireOp",EDGE,"E2.sketch_text.stroke-168"),sQuery(id+"F2.wireOp",EDGE,"E2.sketch_text.stroke-169"),sQuery(id+"F2.wireOp",EDGE,"E2.sketch_text.stroke-170"),sQuery(id+"F2.wireOp",EDGE,"E2.sketch_text.stroke-171"),sQuery(id+"F2.wireOp",EDGE,"E2.sketch_text.stroke-172"),sQuery(id+"F2.wireOp",EDGE,"E2.sketch_text.stroke-173"),sQuery(id+"F3.wireOp",EDGE,"E4.sketch_text.stroke-0"),sQuery(id+"F3.wireOp",EDGE,"E4.sketch_text.stroke-1"),sQuery(id+"F3.wireOp",EDGE,"E4.sketch_text.stroke-2"),sQuery(id+"F3.wireOp",EDGE,"E4.sketch_text.stroke-3"),sQuery(id+"F3.wireOp",EDGE,"E4.sketch_text.stroke-4"),sQuery(id+"F3.wireOp",EDGE,"E4.sketch_text.stroke-5"),sQuery(id+"F3.wireOp",EDGE,"E4.sketch_text.stroke-6"),sQuery(id+"F3.wireOp",EDGE,"E4.sketch_text.stroke-7"),sQuery(id+"F3.wireOp",EDGE,"E4.sketch_text.stroke-8"),sQuery(id+"F3.wireOp",EDGE,"E4.sketch_text.stroke-9"),sQuery(id+"F3.wireOp",EDGE,"E4.sketch_text.stroke-10"),sQuery(id+"F3.wireOp",EDGE,"E4.sketch_text.stroke-11"),sQuery(id+"F3.wireOp",EDGE,"E4.sketch_text.stroke-12"),sQuery(id+"F3.wireOp",EDGE,"E4.sketch_text.stroke-13"),sQuery(id+"F3.wireOp",EDGE,"E4.sketch_text.stroke-14"),sQuery(id+"F3.wireOp",EDGE,"E4.sketch_text.stroke-15"),sQuery(id+"F3.wireOp",EDGE,"E4.sketch_text.stroke-16"),sQuery(id+"F3.wireOp",EDGE,"E4.sketch_text.stroke-17"),sQuery(id+"F3.wireOp",EDGE,"E4.sketch_text.stroke-18"),sQuery(id+"F3.wireOp",EDGE,"E4.sketch_text.stroke-19"),sQuery(id+"F3.wireOp",EDGE,"E4.sketch_text.stroke-20"),sQuery(id+"F3.wireOp",EDGE,"E4.sketch_text.stroke-21"),sQuery(id+"F3.wireOp",EDGE,"E4.sketch_text.stroke-22"),sQuery(id+"F3.wireOp",EDGE,"E4.sketch_text.stroke-23"),sQuery(id+"F3.wireOp",EDGE,"E4.sketch_text.stroke-24"),sQuery(id+"F3.wireOp",EDGE,"E4.sketch_text.stroke-25"),sQuery(id+"F3.wireOp",EDGE,"E4.sketch_text.stroke-26"),sQuery(id+"F3.wireOp",EDGE,"E4.sketch_text.stroke-27"),sQuery(id+"F3.wireOp",EDGE,"E4.sketch_text.stroke-28"),sQuery(id+"F3.wireOp",EDGE,"E4.sketch_text.stroke-29"),sQuery(id+"F3.wireOp",EDGE,"E4.sketch_text.stroke-30"),sQuery(id+"F3.wireOp",EDGE,"E4.sketch_text.stroke-31"),sQuery(id+"F3.wireOp",EDGE,"E4.sketch_text.stroke-32"),sQuery(id+"F3.wireOp",EDGE,"E4.sketch_text.stroke-33"),sQuery(id+"F3.wireOp",EDGE,"E4.sketch_text.stroke-34"),sQuery(id+"F3.wireOp",EDGE,"E4.sketch_text.stroke-35"),sQuery(id+"F3.wireOp",EDGE,"E4.sketch_text.stroke-36"),sQuery(id+"F3.wireOp",EDGE,"E4.sketch_text.stroke-37"),sQuery(id+"F3.wireOp",EDGE,"E4.sketch_text.stroke-38"),sQuery(id+"F3.wireOp",EDGE,"E4.sketch_text.stroke-39"),sQuery(id+"F3.wireOp",EDGE,"E4.sketch_text.stroke-40"),sQuery(id+"F3.wireOp",EDGE,"E4.sketch_text.stroke-41"),sQuery(id+"F3.wireOp",EDGE,"E4.sketch_text.stroke-42"),sQuery(id+"F3.wireOp",EDGE,"E4.sketch_text.stroke-43"),sQuery(id+"F3.wireOp",EDGE,"E4.sketch_text.stroke-44"),sQuery(id+"F3.wireOp",EDGE,"E4.sketch_text.stroke-45"),sQuery(id+"F3.wireOp",EDGE,"E4.sketch_text.stroke-46"),sQuery(id+"F3.wireOp",EDGE,"E4.sketch_text.stroke-47"),sQuery(id+"F3.wireOp",EDGE,"E4.sketch_text.stroke-48"),sQuery(id+"F3.wireOp",EDGE,"E4.sketch_text.stroke-49"),sQuery(id+"F3.wireOp",EDGE,"E4.sketch_text.stroke-50"),sQuery(id+"F3.wireOp",EDGE,"E4.sketch_text.stroke-51"),sQuery(id+"F3.wireOp",EDGE,"E4.sketch_text.stroke-52"),sQuery(id+"F3.wireOp",EDGE,"E4.sketch_text.stroke-53"),sQuery(id+"F3.wireOp",EDGE,"E4.sketch_text.stroke-54"),sQuery(id+"F3.wireOp",EDGE,"E4.sketch_text.stroke-55"),sQuery(id+"F3.wireOp",EDGE,"E4.sketch_text.stroke-56"),sQuery(id+"F3.wireOp",EDGE,"E4.sketch_text.stroke-57"),sQuery(id+"F3.wireOp",EDGE,"E4.sketch_text.stroke-58"),sQuery(id+"F3.wireOp",EDGE,"E4.sketch_text.stroke-59"),sQuery(id+"F3.wireOp",EDGE,"E4.sketch_text.stroke-60"),sQuery(id+"F3.wireOp",EDGE,"E4.sketch_text.stroke-61"),sQuery(id+"F3.wireOp",EDGE,"E4.sketch_text.stroke-62"),sQuery(id+"F3.wireOp",EDGE,"E4.sketch_text.stroke-71"),sQuery(id+"F3.wireOp",EDGE,"E4.sketch_text.stroke-72"),sQuery(id+"F3.wireOp",EDGE,"E4.sketch_text.stroke-73"),sQuery(id+"F3.wireOp",EDGE,"E4.sketch_text.stroke-74"),sQuery(id+"F3.wireOp",EDGE,"E4.sketch_text.stroke-75"),sQuery(id+"F3.wireOp",EDGE,"E4.sketch_text.stroke-76"),sQuery(id+"F3.wireOp",EDGE,"E4.sketch_text.stroke-77"),sQuery(id+"F3.wireOp",EDGE,"E4.sketch_text.stroke-78"),sQuery(id+"F3.wireOp",EDGE,"E4.sketch_text.stroke-79"),sQuery(id+"F3.wireOp",EDGE,"E4.sketch_text.stroke-80"),sQuery(id+"F3.wireOp",EDGE,"E4.sketch_text.stroke-81"),sQuery(id+"F3.wireOp",EDGE,"E4.sketch_text.stroke-82"),sQuery(id+"F3.wireOp",EDGE,"E4.sketch_text.stroke-83"),sQuery(id+"F3.wireOp",EDGE,"E4.sketch_text.stroke-84"),sQuery(id+"F3.wireOp",EDGE,"E4.sketch_text.stroke-85"),sQuery(id+"F3.wireOp",EDGE,"E4.sketch_text.stroke-86"),sQuery(id+"F3.wireOp",EDGE,"E4.sketch_text.stroke-87"),sQuery(id+"F3.wireOp",EDGE,"E4.sketch_text.stroke-88"),sQuery(id+"F3.wireOp",EDGE,"E4.sketch_text.stroke-89"),sQuery(id+"F3.wireOp",EDGE,"E4.sketch_text.stroke-90"),sQuery(id+"F3.wireOp",EDGE,"E4.sketch_text.stroke-91"),sQuery(id+"F3.wireOp",EDGE,"E4.sketch_text.stroke-92"),sQuery(id+"F3.wireOp",EDGE,"E4.sketch_text.stroke-93"),sQuery(id+"F3.wireOp",EDGE,"E4.sketch_text.stroke-94"),sQuery(id+"F3.wireOp",EDGE,"E4.sketch_text.stroke-95"),sQuery(id+"F3.wireOp",EDGE,"E4.sketch_text.stroke-96"),sQuery(id+"F3.wireOp",EDGE,"E4.sketch_text.stroke-97"),sQuery(id+"F3.wireOp",EDGE,"E4.sketch_text.stroke-103"),sQuery(id+"F3.wireOp",EDGE,"E4.sketch_text.stroke-104"),sQuery(id+"F3.wireOp",EDGE,"E4.sketch_text.stroke-105"),sQuery(id+"F3.wireOp",EDGE,"E4.sketch_text.stroke-106"),sQuery(id+"F3.wireOp",EDGE,"E4.sketch_text.stroke-107"),sQuery(id+"F3.wireOp",EDGE,"E4.sketch_text.stroke-108"),sQuery(id+"F3.wireOp",EDGE,"E4.sketch_text.stroke-109"),sQuery(id+"F3.wireOp",EDGE,"E4.sketch_text.stroke-110"),sQuery(id+"F3.wireOp",EDGE,"E4.sketch_text.stroke-111"),sQuery(id+"F3.wireOp",EDGE,"E4.sketch_text.stroke-112"),sQuery(id+"F3.wireOp",EDGE,"E4.sketch_text.stroke-113"),sQuery(id+"F3.wireOp",EDGE,"E4.sketch_text.stroke-114"),sQuery(id+"F3.wireOp",EDGE,"E4.sketch_text.stroke-115"),sQuery(id+"F3.wireOp",EDGE,"E4.sketch_text.stroke-116"),sQuery(id+"F3.wireOp",EDGE,"E4.sketch_text.stroke-117"),sQuery(id+"F3.wireOp",EDGE,"E4.sketch_text.stroke-118"),sQuery(id+"F3.wireOp",EDGE,"E4.sketch_text.stroke-119"),sQuery(id+"F3.wireOp",EDGE,"E4.sketch_text.stroke-120"),sQuery(id+"F3.wireOp",EDGE,"E4.sketch_text.stroke-121"),sQuery(id+"F3.wireOp",EDGE,"E4.sketch_text.stroke-122"),sQuery(id+"F3.wireOp",EDGE,"E4.sketch_text.stroke-123"),sQuery(id+"F3.wireOp",EDGE,"E4.sketch_text.stroke-124"),sQuery(id+"F3.wireOp",EDGE,"E4.sketch_text.stroke-125"),sQuery(id+"F3.wireOp",EDGE,"E4.sketch_text.stroke-126"),sQuery(id+"F3.wireOp",EDGE,"E4.sketch_text.stroke-127"),sQuery(id+"F3.wireOp",EDGE,"E4.sketch_text.stroke-128"),sQuery(id+"F3.wireOp",EDGE,"E4.sketch_text.stroke-129"),sQuery(id+"F3.wireOp",EDGE,"E4.sketch_text.stroke-130"),sQuery(id+"F3.wireOp",EDGE,"E4.sketch_text.stroke-131"),sQuery(id+"F3.wireOp",EDGE,"E4.sketch_text.stroke-132"),sQuery(id+"F3.wireOp",EDGE,"E4.sketch_text.stroke-133"),sQuery(id+"F3.wireOp",EDGE,"E4.sketch_text.stroke-134"),sQuery(id+"F3.wireOp",EDGE,"E4.sketch_text.stroke-135"),sQuery(id+"F3.wireOp",EDGE,"E4.sketch_text.stroke-136"),sQuery(id+"F3.wireOp",EDGE,"E4.sketch_text.stroke-137"),sQuery(id+"F3.wireOp",EDGE,"E4.sketch_text.stroke-138"),sQuery(id+"F3.wireOp",EDGE,"E4.sketch_text.stroke-139"),sQuery(id+"F3.wireOp",EDGE,"E4.sketch_text.stroke-140"),sQuery(id+"F3.wireOp",EDGE,"E4.sketch_text.stroke-141"),sQuery(id+"F3.wireOp",EDGE,"E4.sketch_text.stroke-142"),sQuery(id+"F3.wireOp",EDGE,"E4.sketch_text.stroke-143"),sQuery(id+"F3.wireOp",EDGE,"E4.sketch_text.stroke-144"),sQuery(id+"F3.wireOp",EDGE,"E4.sketch_text.stroke-145"),sQuery(id+"F3.wireOp",EDGE,"E4.sketch_text.stroke-146"),sQuery(id+"F3.wireOp",EDGE,"E4.sketch_text.stroke-147"),sQuery(id+"F3.wireOp",EDGE,"E4.sketch_text.stroke-148"),sQuery(id+"F3.wireOp",EDGE,"E4.sketch_text.stroke-149"),sQuery(id+"F3.wireOp",EDGE,"E4.sketch_text.stroke-150"),sQuery(id+"F3.wireOp",EDGE,"E4.sketch_text.stroke-151"),sQuery(id+"F3.wireOp",EDGE,"E4.sketch_text.stroke-152"),sQuery(id+"F3.wireOp",EDGE,"E4.sketch_text.stroke-153"),sQuery(id+"F3.wireOp",EDGE,"E4.sketch_text.stroke-159"),sQuery(id+"F3.wireOp",EDGE,"E4.sketch_text.stroke-160"),sQuery(id+"F3.wireOp",EDGE,"E4.sketch_text.stroke-161"),sQuery(id+"F3.wireOp",EDGE,"E4.sketch_text.stroke-162"),sQuery(id+"F3.wireOp",EDGE,"E4.sketch_text.stroke-163"),sQuery(id+"F3.wireOp",EDGE,"E4.sketch_text.stroke-164"),sQuery(id+"F3.wireOp",EDGE,"E4.sketch_text.stroke-165"),sQuery(id+"F3.wireOp",EDGE,"E4.sketch_text.stroke-166"),sQuery(id+"F3.wireOp",EDGE,"E4.sketch_text.stroke-167"),sQuery(id+"F3.wireOp",EDGE,"E4.sketch_text.stroke-168"),sQuery(id+"F3.wireOp",EDGE,"E4.sketch_text.stroke-169"),sQuery(id+"F3.wireOp",EDGE,"E4.sketch_text.stroke-170"),sQuery(id+"F3.wireOp",EDGE,"E4.sketch_text.stroke-171"),sQuery(id+"F3.wireOp",EDGE,"E4.sketch_text.stroke-172"),sQuery(id+"F3.wireOp",EDGE,"E4.sketch_text.stroke-173"),sQuery(id+"F3.wireOp",EDGE,"E4.sketch_text.stroke-174"),sQuery(id+"F3.wireOp",EDGE,"E4.sketch_text.stroke-175"),sQuery(id+"F3.wireOp",EDGE,"E4.sketch_text.stroke-176"),sQuery(id+"F3.wireOp",EDGE,"E4.sketch_text.stroke-177"),sQuery(id+"F3.wireOp",EDGE,"E4.sketch_text.stroke-178"),sQuery(id+"F3.wireOp",EDGE,"E4.sketch_text.stroke-179"),sQuery(id+"F3.wireOp",EDGE,"E4.sketch_text.stroke-180"),subQ2,sQuery(id+"F4.wireOp",EDGE,"6ee83ff3-586e-4dbe-aaea-af71240543bd")])],"isStart":true})]),OD(0.0)],"derivedFrom":makeQuery(id+"F1.opExtrude","CAP_EDGE",EDGE,{"disambiguationData":[OSD([subQ0])],"isStart":false})});}
            var Q6;
            {var subQ0=sQuery(id+"F4.wireOp",EDGE,"6ee83ff3-586e-4dbe-aaea-af71240543bd");var subQ1=sQuery(id+"F0.wireOp",EDGE,"E0.bottom");var subQ2=sQuery(id+"F0.wireOp",EDGE,"E0.right");Q6=makeQuery(id+"F5.boolean.opBoolean","SPLIT",EDGE,{"disambiguationData":[TD([makeQuery(id+"F1.opExtrude","SWEPT_FACE",FACE,{"disambiguationData":[OSD([subQ1])]}),makeQuery(id+"F1.opExtrude","CAP_FACE",FACE,{"disambiguationData":[OSD([subQ1,sQuery(id+"F0.wireOp",EDGE,"E0.top"),sQuery(id+"F0.wireOp",EDGE,"E0.left"),subQ2])],"isStart":false}),makeQuery(id+"F1.opExtrude","SWEPT_FACE",FACE,{"disambiguationData":[OSD([subQ2])]}),makeQuery(id+"F5.opExtrude","CAP_FACE",FACE,{"disambiguationData":[OSD([subQ1,sQuery(id+"F2.wireOp",EDGE,"E2.sketch_text.stroke-0"),sQuery(id+"F2.wireOp",EDGE,"E2.sketch_text.stroke-1"),sQuery(id+"F2.wireOp",EDGE,"E2.sketch_text.stroke-2"),sQuery(id+"F2.wireOp",EDGE,"E2.sketch_text.stroke-3"),sQuery(id+"F2.wireOp",EDGE,"E2.sketch_text.stroke-4"),sQuery(id+"F2.wireOp",EDGE,"E2.sketch_text.stroke-5"),sQuery(id+"F2.wireOp",EDGE,"E2.sketch_text.stroke-6"),sQuery(id+"F2.wireOp",EDGE,"E2.sketch_text.stroke-7"),sQuery(id+"F2.wireOp",EDGE,"E2.sketch_text.stroke-8"),sQuery(id+"F2.wireOp",EDGE,"E2.sketch_text.stroke-9"),sQuery(id+"F2.wireOp",EDGE,"E2.sketch_text.stroke-10"),sQuery(id+"F2.wireOp",EDGE,"E2.sketch_text.stroke-11"),sQuery(id+"F2.wireOp",EDGE,"E2.sketch_text.stroke-12"),sQuery(id+"F2.wireOp",EDGE,"E2.sketch_text.stroke-13"),sQuery(id+"F2.wireOp",EDGE,"E2.sketch_text.stroke-14"),sQuery(id+"F2.wireOp",EDGE,"E2.sketch_text.stroke-15"),sQuery(id+"F2.wireOp",EDGE,"E2.sketch_text.stroke-16"),sQuery(id+"F2.wireOp",EDGE,"E2.sketch_text.stroke-17"),sQuery(id+"F2.wireOp",EDGE,"E2.sketch_text.stroke-18"),sQuery(id+"F2.wireOp",EDGE,"E2.sketch_text.stroke-19"),sQuery(id+"F2.wireOp",EDGE,"E2.sketch_text.stroke-20"),sQuery(id+"F2.wireOp",EDGE,"E2.sketch_text.stroke-21"),sQuery(id+"F2.wireOp",EDGE,"E2.sketch_text.stroke-22"),sQuery(id+"F2.wireOp",EDGE,"E2.sketch_text.stroke-23"),sQuery(id+"F2.wireOp",EDGE,"E2.sketch_text.stroke-24"),sQuery(id+"F2.wireOp",EDGE,"E2.sketch_text.stroke-25"),sQuery(id+"F2.wireOp",EDGE,"E2.sketch_text.stroke-26"),sQuery(id+"F2.wireOp",EDGE,"E2.sketch_text.stroke-27"),sQuery(id+"F2.wireOp",EDGE,"E2.sketch_text.stroke-28"),sQuery(id+"F2.wireOp",EDGE,"E2.sketch_text.stroke-29"),sQuery(id+"F2.wireOp",EDGE,"E2.sketch_text.stroke-30"),sQuery(id+"F2.wireOp",EDGE,"E2.sketch_text.stroke-31"),sQuery(id+"F2.wireOp",EDGE,"E2.sketch_text.stroke-32"),sQuery(id+"F2.wireOp",EDGE,"E2.sketch_text.stroke-33"),sQuery(id+"F2.wireOp",EDGE,"E2.sketch_text.stroke-34"),sQuery(id+"F2.wireOp",EDGE,"E2.sketch_text.stroke-35"),sQuery(id+"F2.wireOp",EDGE,"E2.sketch_text.stroke-36"),sQuery(id+"F2.wireOp",EDGE,"E2.sketch_text.stroke-37"),sQuery(id+"F2.wireOp",EDGE,"E2.sketch_text.stroke-38"),sQuery(id+"F2.wireOp",EDGE,"E2.sketch_text.stroke-39"),sQuery(id+"F2.wireOp",EDGE,"E2.sketch_text.stroke-40"),sQuery(id+"F2.wireOp",EDGE,"E2.sketch_text.stroke-41"),sQuery(id+"F2.wireOp",EDGE,"E2.sketch_text.stroke-42"),sQuery(id+"F2.wireOp",EDGE,"E2.sketch_text.stroke-43"),sQuery(id+"F2.wireOp",EDGE,"E2.sketch_text.stroke-44"),sQuery(id+"F2.wireOp",EDGE,"E2.sketch_text.stroke-45"),sQuery(id+"F2.wireOp",EDGE,"E2.sketch_text.stroke-46"),sQuery(id+"F2.wireOp",EDGE,"E2.sketch_text.stroke-47"),sQuery(id+"F2.wireOp",EDGE,"E2.sketch_text.stroke-48"),sQuery(id+"F2.wireOp",EDGE,"E2.sketch_text.stroke-49"),sQuery(id+"F2.wireOp",EDGE,"E2.sketch_text.stroke-50"),sQuery(id+"F2.wireOp",EDGE,"E2.sketch_text.stroke-51"),sQuery(id+"F2.wireOp",EDGE,"E2.sketch_text.stroke-52"),sQuery(id+"F2.wireOp",EDGE,"E2.sketch_text.stroke-53"),sQuery(id+"F2.wireOp",EDGE,"E2.sketch_text.stroke-54"),sQuery(id+"F2.wireOp",EDGE,"E2.sketch_text.stroke-55"),sQuery(id+"F2.wireOp",EDGE,"E2.sketch_text.stroke-56"),sQuery(id+"F2.wireOp",EDGE,"E2.sketch_text.stroke-57"),sQuery(id+"F2.wireOp",EDGE,"E2.sketch_text.stroke-58"),sQuery(id+"F2.wireOp",EDGE,"E2.sketch_text.stroke-59"),sQuery(id+"F2.wireOp",EDGE,"E2.sketch_text.stroke-60"),sQuery(id+"F2.wireOp",EDGE,"E2.sketch_text.stroke-61"),sQuery(id+"F2.wireOp",EDGE,"E2.sketch_text.stroke-62"),sQuery(id+"F2.wireOp",EDGE,"E2.sketch_text.stroke-63"),sQuery(id+"F2.wireOp",EDGE,"E2.sketch_text.stroke-64"),sQuery(id+"F2.wireOp",EDGE,"E2.sketch_text.stroke-65"),sQuery(id+"F2.wireOp",EDGE,"E2.sketch_text.stroke-66"),sQuery(id+"F2.wireOp",EDGE,"E2.sketch_text.stroke-67"),sQuery(id+"F2.wireOp",EDGE,"E2.sketch_text.stroke-68"),sQuery(id+"F2.wireOp",EDGE,"E2.sketch_text.stroke-69"),sQuery(id+"F2.wireOp",EDGE,"E2.sketch_text.stroke-70"),sQuery(id+"F2.wireOp",EDGE,"E2.sketch_text.stroke-71"),sQuery(id+"F2.wireOp",EDGE,"E2.sketch_text.stroke-72"),sQuery(id+"F2.wireOp",EDGE,"E2.sketch_text.stroke-73"),sQuery(id+"F2.wireOp",EDGE,"E2.sketch_text.stroke-74"),sQuery(id+"F2.wireOp",EDGE,"E2.sketch_text.stroke-75"),sQuery(id+"F2.wireOp",EDGE,"E2.sketch_text.stroke-76"),sQuery(id+"F2.wireOp",EDGE,"E2.sketch_text.stroke-77"),sQuery(id+"F2.wireOp",EDGE,"E2.sketch_text.stroke-78"),sQuery(id+"F2.wireOp",EDGE,"E2.sketch_text.stroke-79"),sQuery(id+"F2.wireOp",EDGE,"E2.sketch_text.stroke-80"),sQuery(id+"F2.wireOp",EDGE,"E2.sketch_text.stroke-81"),sQuery(id+"F2.wireOp",EDGE,"E2.sketch_text.stroke-82"),sQuery(id+"F2.wireOp",EDGE,"E2.sketch_text.stroke-83"),sQuery(id+"F2.wireOp",EDGE,"E2.sketch_text.stroke-84"),sQuery(id+"F2.wireOp",EDGE,"E2.sketch_text.stroke-85"),sQuery(id+"F2.wireOp",EDGE,"E2.sketch_text.stroke-86"),sQuery(id+"F2.wireOp",EDGE,"E2.sketch_text.stroke-87"),sQuery(id+"F2.wireOp",EDGE,"E2.sketch_text.stroke-88"),sQuery(id+"F2.wireOp",EDGE,"E2.sketch_text.stroke-89"),sQuery(id+"F2.wireOp",EDGE,"E2.sketch_text.stroke-90"),sQuery(id+"F2.wireOp",EDGE,"E2.sketch_text.stroke-91"),sQuery(id+"F2.wireOp",EDGE,"E2.sketch_text.stroke-92"),sQuery(id+"F2.wireOp",EDGE,"E2.sketch_text.stroke-93"),sQuery(id+"F2.wireOp",EDGE,"E2.sketch_text.stroke-94"),sQuery(id+"F2.wireOp",EDGE,"E2.sketch_text.stroke-95"),sQuery(id+"F2.wireOp",EDGE,"E2.sketch_text.stroke-96"),sQuery(id+"F2.wireOp",EDGE,"E2.sketch_text.stroke-97"),sQuery(id+"F2.wireOp",EDGE,"E2.sketch_text.stroke-98"),sQuery(id+"F2.wireOp",EDGE,"E2.sketch_text.stroke-99"),sQuery(id+"F2.wireOp",EDGE,"E2.sketch_text.stroke-100"),sQuery(id+"F2.wireOp",EDGE,"E2.sketch_text.stroke-101"),sQuery(id+"F2.wireOp",EDGE,"E2.sketch_text.stroke-102"),sQuery(id+"F2.wireOp",EDGE,"E2.sketch_text.stroke-103"),sQuery(id+"F2.wireOp",EDGE,"E2.sketch_text.stroke-104"),sQuery(id+"F2.wireOp",EDGE,"E2.sketch_text.stroke-105"),sQuery(id+"F2.wireOp",EDGE,"E2.sketch_text.stroke-106"),sQuery(id+"F2.wireOp",EDGE,"E2.sketch_text.stroke-107"),sQuery(id+"F2.wireOp",EDGE,"E2.sketch_text.stroke-108"),sQuery(id+"F2.wireOp",EDGE,"E2.sketch_text.stroke-109"),sQuery(id+"F2.wireOp",EDGE,"E2.sketch_text.stroke-110"),sQuery(id+"F2.wireOp",EDGE,"E2.sketch_text.stroke-111"),sQuery(id+"F2.wireOp",EDGE,"E2.sketch_text.stroke-112"),sQuery(id+"F2.wireOp",EDGE,"E2.sketch_text.stroke-113"),sQuery(id+"F2.wireOp",EDGE,"E2.sketch_text.stroke-114"),sQuery(id+"F2.wireOp",EDGE,"E2.sketch_text.stroke-115"),sQuery(id+"F2.wireOp",EDGE,"E2.sketch_text.stroke-116"),sQuery(id+"F2.wireOp",EDGE,"E2.sketch_text.stroke-117"),sQuery(id+"F2.wireOp",EDGE,"E2.sketch_text.stroke-118"),sQuery(id+"F2.wireOp",EDGE,"E2.sketch_text.stroke-119"),sQuery(id+"F2.wireOp",EDGE,"E2.sketch_text.stroke-120"),sQuery(id+"F2.wireOp",EDGE,"E2.sketch_text.stroke-121"),sQuery(id+"F2.wireOp",EDGE,"E2.sketch_text.stroke-122"),sQuery(id+"F2.wireOp",EDGE,"E2.sketch_text.stroke-123"),sQuery(id+"F2.wireOp",EDGE,"E2.sketch_text.stroke-124"),sQuery(id+"F2.wireOp",EDGE,"E2.sketch_text.stroke-125"),sQuery(id+"F2.wireOp",EDGE,"E2.sketch_text.stroke-126"),sQuery(id+"F2.wireOp",EDGE,"E2.sketch_text.stroke-127"),sQuery(id+"F2.wireOp",EDGE,"E2.sketch_text.stroke-128"),sQuery(id+"F2.wireOp",EDGE,"E2.sketch_text.stroke-129"),sQuery(id+"F2.wireOp",EDGE,"E2.sketch_text.stroke-130"),sQuery(id+"F2.wireOp",EDGE,"E2.sketch_text.stroke-131"),sQuery(id+"F2.wireOp",EDGE,"E2.sketch_text.stroke-132"),sQuery(id+"F2.wireOp",EDGE,"E2.sketch_text.stroke-133"),sQuery(id+"F2.wireOp",EDGE,"E2.sketch_text.stroke-134"),sQuery(id+"F2.wireOp",EDGE,"E2.sketch_text.stroke-135"),sQuery(id+"F2.wireOp",EDGE,"E2.sketch_text.stroke-136"),sQuery(id+"F2.wireOp",EDGE,"E2.sketch_text.stroke-137"),sQuery(id+"F2.wireOp",EDGE,"E2.sketch_text.stroke-138"),sQuery(id+"F2.wireOp",EDGE,"E2.sketch_text.stroke-139"),sQuery(id+"F2.wireOp",EDGE,"E2.sketch_text.stroke-140"),sQuery(id+"F2.wireOp",EDGE,"E2.sketch_text.stroke-141"),sQuery(id+"F2.wireOp",EDGE,"E2.sketch_text.stroke-142"),sQuery(id+"F2.wireOp",EDGE,"E2.sketch_text.stroke-143"),sQuery(id+"F2.wireOp",EDGE,"E2.sketch_text.stroke-144"),sQuery(id+"F2.wireOp",EDGE,"E2.sketch_text.stroke-145"),sQuery(id+"F2.wireOp",EDGE,"E2.sketch_text.stroke-146"),sQuery(id+"F2.wireOp",EDGE,"E2.sketch_text.stroke-147"),sQuery(id+"F2.wireOp",EDGE,"E2.sketch_text.stroke-148"),sQuery(id+"F2.wireOp",EDGE,"E2.sketch_text.stroke-149"),sQuery(id+"F2.wireOp",EDGE,"E2.sketch_text.stroke-150"),sQuery(id+"F2.wireOp",EDGE,"E2.sketch_text.stroke-151"),sQuery(id+"F2.wireOp",EDGE,"E2.sketch_text.stroke-152"),sQuery(id+"F2.wireOp",EDGE,"E2.sketch_text.stroke-153"),sQuery(id+"F2.wireOp",EDGE,"E2.sketch_text.stroke-154"),sQuery(id+"F2.wireOp",EDGE,"E2.sketch_text.stroke-155"),sQuery(id+"F2.wireOp",EDGE,"E2.sketch_text.stroke-156"),sQuery(id+"F2.wireOp",EDGE,"E2.sketch_text.stroke-157"),sQuery(id+"F2.wireOp",EDGE,"E2.sketch_text.stroke-158"),sQuery(id+"F2.wireOp",EDGE,"E2.sketch_text.stroke-159"),sQuery(id+"F2.wireOp",EDGE,"E2.sketch_text.stroke-160"),sQuery(id+"F2.wireOp",EDGE,"E2.sketch_text.stroke-161"),sQuery(id+"F2.wireOp",EDGE,"E2.sketch_text.stroke-162"),sQuery(id+"F2.wireOp",EDGE,"E2.sketch_text.stroke-163"),sQuery(id+"F2.wireOp",EDGE,"E2.sketch_text.stroke-164"),sQuery(id+"F2.wireOp",EDGE,"E2.sketch_text.stroke-165"),sQuery(id+"F2.wireOp",EDGE,"E2.sketch_text.stroke-166"),sQuery(id+"F2.wireOp",EDGE,"E2.sketch_text.stroke-167"),sQuery(id+"F2.wireOp",EDGE,"E2.sketch_text.stroke-168"),sQuery(id+"F2.wireOp",EDGE,"E2.sketch_text.stroke-169"),sQuery(id+"F2.wireOp",EDGE,"E2.sketch_text.stroke-170"),sQuery(id+"F2.wireOp",EDGE,"E2.sketch_text.stroke-171"),sQuery(id+"F2.wireOp",EDGE,"E2.sketch_text.stroke-172"),sQuery(id+"F2.wireOp",EDGE,"E2.sketch_text.stroke-173"),sQuery(id+"F3.wireOp",EDGE,"E4.sketch_text.stroke-0"),sQuery(id+"F3.wireOp",EDGE,"E4.sketch_text.stroke-1"),sQuery(id+"F3.wireOp",EDGE,"E4.sketch_text.stroke-2"),sQuery(id+"F3.wireOp",EDGE,"E4.sketch_text.stroke-3"),sQuery(id+"F3.wireOp",EDGE,"E4.sketch_text.stroke-4"),sQuery(id+"F3.wireOp",EDGE,"E4.sketch_text.stroke-5"),sQuery(id+"F3.wireOp",EDGE,"E4.sketch_text.stroke-6"),sQuery(id+"F3.wireOp",EDGE,"E4.sketch_text.stroke-7"),sQuery(id+"F3.wireOp",EDGE,"E4.sketch_text.stroke-8"),sQuery(id+"F3.wireOp",EDGE,"E4.sketch_text.stroke-9"),sQuery(id+"F3.wireOp",EDGE,"E4.sketch_text.stroke-10"),sQuery(id+"F3.wireOp",EDGE,"E4.sketch_text.stroke-11"),sQuery(id+"F3.wireOp",EDGE,"E4.sketch_text.stroke-12"),sQuery(id+"F3.wireOp",EDGE,"E4.sketch_text.stroke-13"),sQuery(id+"F3.wireOp",EDGE,"E4.sketch_text.stroke-14"),sQuery(id+"F3.wireOp",EDGE,"E4.sketch_text.stroke-15"),sQuery(id+"F3.wireOp",EDGE,"E4.sketch_text.stroke-16"),sQuery(id+"F3.wireOp",EDGE,"E4.sketch_text.stroke-17"),sQuery(id+"F3.wireOp",EDGE,"E4.sketch_text.stroke-18"),sQuery(id+"F3.wireOp",EDGE,"E4.sketch_text.stroke-19"),sQuery(id+"F3.wireOp",EDGE,"E4.sketch_text.stroke-20"),sQuery(id+"F3.wireOp",EDGE,"E4.sketch_text.stroke-21"),sQuery(id+"F3.wireOp",EDGE,"E4.sketch_text.stroke-22"),sQuery(id+"F3.wireOp",EDGE,"E4.sketch_text.stroke-23"),sQuery(id+"F3.wireOp",EDGE,"E4.sketch_text.stroke-24"),sQuery(id+"F3.wireOp",EDGE,"E4.sketch_text.stroke-25"),sQuery(id+"F3.wireOp",EDGE,"E4.sketch_text.stroke-26"),sQuery(id+"F3.wireOp",EDGE,"E4.sketch_text.stroke-27"),sQuery(id+"F3.wireOp",EDGE,"E4.sketch_text.stroke-28"),sQuery(id+"F3.wireOp",EDGE,"E4.sketch_text.stroke-29"),sQuery(id+"F3.wireOp",EDGE,"E4.sketch_text.stroke-30"),sQuery(id+"F3.wireOp",EDGE,"E4.sketch_text.stroke-31"),sQuery(id+"F3.wireOp",EDGE,"E4.sketch_text.stroke-32"),sQuery(id+"F3.wireOp",EDGE,"E4.sketch_text.stroke-33"),sQuery(id+"F3.wireOp",EDGE,"E4.sketch_text.stroke-34"),sQuery(id+"F3.wireOp",EDGE,"E4.sketch_text.stroke-35"),sQuery(id+"F3.wireOp",EDGE,"E4.sketch_text.stroke-36"),sQuery(id+"F3.wireOp",EDGE,"E4.sketch_text.stroke-37"),sQuery(id+"F3.wireOp",EDGE,"E4.sketch_text.stroke-38"),sQuery(id+"F3.wireOp",EDGE,"E4.sketch_text.stroke-39"),sQuery(id+"F3.wireOp",EDGE,"E4.sketch_text.stroke-40"),sQuery(id+"F3.wireOp",EDGE,"E4.sketch_text.stroke-41"),sQuery(id+"F3.wireOp",EDGE,"E4.sketch_text.stroke-42"),sQuery(id+"F3.wireOp",EDGE,"E4.sketch_text.stroke-43"),sQuery(id+"F3.wireOp",EDGE,"E4.sketch_text.stroke-44"),sQuery(id+"F3.wireOp",EDGE,"E4.sketch_text.stroke-45"),sQuery(id+"F3.wireOp",EDGE,"E4.sketch_text.stroke-46"),sQuery(id+"F3.wireOp",EDGE,"E4.sketch_text.stroke-47"),sQuery(id+"F3.wireOp",EDGE,"E4.sketch_text.stroke-48"),sQuery(id+"F3.wireOp",EDGE,"E4.sketch_text.stroke-49"),sQuery(id+"F3.wireOp",EDGE,"E4.sketch_text.stroke-50"),sQuery(id+"F3.wireOp",EDGE,"E4.sketch_text.stroke-51"),sQuery(id+"F3.wireOp",EDGE,"E4.sketch_text.stroke-52"),sQuery(id+"F3.wireOp",EDGE,"E4.sketch_text.stroke-53"),sQuery(id+"F3.wireOp",EDGE,"E4.sketch_text.stroke-54"),sQuery(id+"F3.wireOp",EDGE,"E4.sketch_text.stroke-55"),sQuery(id+"F3.wireOp",EDGE,"E4.sketch_text.stroke-56"),sQuery(id+"F3.wireOp",EDGE,"E4.sketch_text.stroke-57"),sQuery(id+"F3.wireOp",EDGE,"E4.sketch_text.stroke-58"),sQuery(id+"F3.wireOp",EDGE,"E4.sketch_text.stroke-59"),sQuery(id+"F3.wireOp",EDGE,"E4.sketch_text.stroke-60"),sQuery(id+"F3.wireOp",EDGE,"E4.sketch_text.stroke-61"),sQuery(id+"F3.wireOp",EDGE,"E4.sketch_text.stroke-62"),sQuery(id+"F3.wireOp",EDGE,"E4.sketch_text.stroke-71"),sQuery(id+"F3.wireOp",EDGE,"E4.sketch_text.stroke-72"),sQuery(id+"F3.wireOp",EDGE,"E4.sketch_text.stroke-73"),sQuery(id+"F3.wireOp",EDGE,"E4.sketch_text.stroke-74"),sQuery(id+"F3.wireOp",EDGE,"E4.sketch_text.stroke-75"),sQuery(id+"F3.wireOp",EDGE,"E4.sketch_text.stroke-76"),sQuery(id+"F3.wireOp",EDGE,"E4.sketch_text.stroke-77"),sQuery(id+"F3.wireOp",EDGE,"E4.sketch_text.stroke-78"),sQuery(id+"F3.wireOp",EDGE,"E4.sketch_text.stroke-79"),sQuery(id+"F3.wireOp",EDGE,"E4.sketch_text.stroke-80"),sQuery(id+"F3.wireOp",EDGE,"E4.sketch_text.stroke-81"),sQuery(id+"F3.wireOp",EDGE,"E4.sketch_text.stroke-82"),sQuery(id+"F3.wireOp",EDGE,"E4.sketch_text.stroke-83"),sQuery(id+"F3.wireOp",EDGE,"E4.sketch_text.stroke-84"),sQuery(id+"F3.wireOp",EDGE,"E4.sketch_text.stroke-85"),sQuery(id+"F3.wireOp",EDGE,"E4.sketch_text.stroke-86"),sQuery(id+"F3.wireOp",EDGE,"E4.sketch_text.stroke-87"),sQuery(id+"F3.wireOp",EDGE,"E4.sketch_text.stroke-88"),sQuery(id+"F3.wireOp",EDGE,"E4.sketch_text.stroke-89"),sQuery(id+"F3.wireOp",EDGE,"E4.sketch_text.stroke-90"),sQuery(id+"F3.wireOp",EDGE,"E4.sketch_text.stroke-91"),sQuery(id+"F3.wireOp",EDGE,"E4.sketch_text.stroke-92"),sQuery(id+"F3.wireOp",EDGE,"E4.sketch_text.stroke-93"),sQuery(id+"F3.wireOp",EDGE,"E4.sketch_text.stroke-94"),sQuery(id+"F3.wireOp",EDGE,"E4.sketch_text.stroke-95"),sQuery(id+"F3.wireOp",EDGE,"E4.sketch_text.stroke-96"),sQuery(id+"F3.wireOp",EDGE,"E4.sketch_text.stroke-97"),sQuery(id+"F3.wireOp",EDGE,"E4.sketch_text.stroke-103"),sQuery(id+"F3.wireOp",EDGE,"E4.sketch_text.stroke-104"),sQuery(id+"F3.wireOp",EDGE,"E4.sketch_text.stroke-105"),sQuery(id+"F3.wireOp",EDGE,"E4.sketch_text.stroke-106"),sQuery(id+"F3.wireOp",EDGE,"E4.sketch_text.stroke-107"),sQuery(id+"F3.wireOp",EDGE,"E4.sketch_text.stroke-108"),sQuery(id+"F3.wireOp",EDGE,"E4.sketch_text.stroke-109"),sQuery(id+"F3.wireOp",EDGE,"E4.sketch_text.stroke-110"),sQuery(id+"F3.wireOp",EDGE,"E4.sketch_text.stroke-111"),sQuery(id+"F3.wireOp",EDGE,"E4.sketch_text.stroke-112"),sQuery(id+"F3.wireOp",EDGE,"E4.sketch_text.stroke-113"),sQuery(id+"F3.wireOp",EDGE,"E4.sketch_text.stroke-114"),sQuery(id+"F3.wireOp",EDGE,"E4.sketch_text.stroke-115"),sQuery(id+"F3.wireOp",EDGE,"E4.sketch_text.stroke-116"),sQuery(id+"F3.wireOp",EDGE,"E4.sketch_text.stroke-117"),sQuery(id+"F3.wireOp",EDGE,"E4.sketch_text.stroke-118"),sQuery(id+"F3.wireOp",EDGE,"E4.sketch_text.stroke-119"),sQuery(id+"F3.wireOp",EDGE,"E4.sketch_text.stroke-120"),sQuery(id+"F3.wireOp",EDGE,"E4.sketch_text.stroke-121"),sQuery(id+"F3.wireOp",EDGE,"E4.sketch_text.stroke-122"),sQuery(id+"F3.wireOp",EDGE,"E4.sketch_text.stroke-123"),sQuery(id+"F3.wireOp",EDGE,"E4.sketch_text.stroke-124"),sQuery(id+"F3.wireOp",EDGE,"E4.sketch_text.stroke-125"),sQuery(id+"F3.wireOp",EDGE,"E4.sketch_text.stroke-126"),sQuery(id+"F3.wireOp",EDGE,"E4.sketch_text.stroke-127"),sQuery(id+"F3.wireOp",EDGE,"E4.sketch_text.stroke-128"),sQuery(id+"F3.wireOp",EDGE,"E4.sketch_text.stroke-129"),sQuery(id+"F3.wireOp",EDGE,"E4.sketch_text.stroke-130"),sQuery(id+"F3.wireOp",EDGE,"E4.sketch_text.stroke-131"),sQuery(id+"F3.wireOp",EDGE,"E4.sketch_text.stroke-132"),sQuery(id+"F3.wireOp",EDGE,"E4.sketch_text.stroke-133"),sQuery(id+"F3.wireOp",EDGE,"E4.sketch_text.stroke-134"),sQuery(id+"F3.wireOp",EDGE,"E4.sketch_text.stroke-135"),sQuery(id+"F3.wireOp",EDGE,"E4.sketch_text.stroke-136"),sQuery(id+"F3.wireOp",EDGE,"E4.sketch_text.stroke-137"),sQuery(id+"F3.wireOp",EDGE,"E4.sketch_text.stroke-138"),sQuery(id+"F3.wireOp",EDGE,"E4.sketch_text.stroke-139"),sQuery(id+"F3.wireOp",EDGE,"E4.sketch_text.stroke-140"),sQuery(id+"F3.wireOp",EDGE,"E4.sketch_text.stroke-141"),sQuery(id+"F3.wireOp",EDGE,"E4.sketch_text.stroke-142"),sQuery(id+"F3.wireOp",EDGE,"E4.sketch_text.stroke-143"),sQuery(id+"F3.wireOp",EDGE,"E4.sketch_text.stroke-144"),sQuery(id+"F3.wireOp",EDGE,"E4.sketch_text.stroke-145"),sQuery(id+"F3.wireOp",EDGE,"E4.sketch_text.stroke-146"),sQuery(id+"F3.wireOp",EDGE,"E4.sketch_text.stroke-147"),sQuery(id+"F3.wireOp",EDGE,"E4.sketch_text.stroke-148"),sQuery(id+"F3.wireOp",EDGE,"E4.sketch_text.stroke-149"),sQuery(id+"F3.wireOp",EDGE,"E4.sketch_text.stroke-150"),sQuery(id+"F3.wireOp",EDGE,"E4.sketch_text.stroke-151"),sQuery(id+"F3.wireOp",EDGE,"E4.sketch_text.stroke-152"),sQuery(id+"F3.wireOp",EDGE,"E4.sketch_text.stroke-153"),sQuery(id+"F3.wireOp",EDGE,"E4.sketch_text.stroke-159"),sQuery(id+"F3.wireOp",EDGE,"E4.sketch_text.stroke-160"),sQuery(id+"F3.wireOp",EDGE,"E4.sketch_text.stroke-161"),sQuery(id+"F3.wireOp",EDGE,"E4.sketch_text.stroke-162"),sQuery(id+"F3.wireOp",EDGE,"E4.sketch_text.stroke-163"),sQuery(id+"F3.wireOp",EDGE,"E4.sketch_text.stroke-164"),sQuery(id+"F3.wireOp",EDGE,"E4.sketch_text.stroke-165"),sQuery(id+"F3.wireOp",EDGE,"E4.sketch_text.stroke-166"),sQuery(id+"F3.wireOp",EDGE,"E4.sketch_text.stroke-167"),sQuery(id+"F3.wireOp",EDGE,"E4.sketch_text.stroke-168"),sQuery(id+"F3.wireOp",EDGE,"E4.sketch_text.stroke-169"),sQuery(id+"F3.wireOp",EDGE,"E4.sketch_text.stroke-170"),sQuery(id+"F3.wireOp",EDGE,"E4.sketch_text.stroke-171"),sQuery(id+"F3.wireOp",EDGE,"E4.sketch_text.stroke-172"),sQuery(id+"F3.wireOp",EDGE,"E4.sketch_text.stroke-173"),sQuery(id+"F3.wireOp",EDGE,"E4.sketch_text.stroke-174"),sQuery(id+"F3.wireOp",EDGE,"E4.sketch_text.stroke-175"),sQuery(id+"F3.wireOp",EDGE,"E4.sketch_text.stroke-176"),sQuery(id+"F3.wireOp",EDGE,"E4.sketch_text.stroke-177"),sQuery(id+"F3.wireOp",EDGE,"E4.sketch_text.stroke-178"),sQuery(id+"F3.wireOp",EDGE,"E4.sketch_text.stroke-179"),sQuery(id+"F3.wireOp",EDGE,"E4.sketch_text.stroke-180"),sQuery(id+"F4.wireOp",EDGE,"8007402e-1a4e-4a06-85a5-2af08e553504"),subQ0])],"isStart":true}),makeQuery(id+"F5.opExtrude","SWEPT_FACE",FACE,{"disambiguationData":[OSD([subQ0])]})])],"derivedFrom":makeQuery(id+"F5.opExtrude","CAP_EDGE",EDGE,{"disambiguationData":[OSD([subQ0])],"isStart":true})});}
            var Q7;
            {var subQ0=sQuery(id+"F0.wireOp",EDGE,"E0.right");var subQ1=sQuery(id+"F0.wireOp",EDGE,"E0.top");var subQ2=sQuery(id+"F4.wireOp",EDGE,"6ee83ff3-586e-4dbe-aaea-af71240543bd");var subQ3=sQuery(id+"F0.wireOp",EDGE,"E0.bottom");Q7=makeQuery(id+"F5.boolean.opBoolean","SPLIT",EDGE,{"disambiguationData":[TD([makeQuery(id+"F1.opExtrude","CAP_FACE",FACE,{"disambiguationData":[OSD([subQ3,subQ1,sQuery(id+"F0.wireOp",EDGE,"E0.left"),subQ0])],"isStart":false}),makeQuery(id+"F1.opExtrude","SWEPT_FACE",FACE,{"disambiguationData":[OSD([subQ1])]}),makeQuery(id+"F1.opExtrude","SWEPT_FACE",FACE,{"disambiguationData":[OSD([subQ0])]}),makeQuery(id+"F5.opExtrude","CAP_FACE",FACE,{"disambiguationData":[OSD([subQ3,sQuery(id+"F2.wireOp",EDGE,"E2.sketch_text.stroke-0"),sQuery(id+"F2.wireOp",EDGE,"E2.sketch_text.stroke-1"),sQuery(id+"F2.wireOp",EDGE,"E2.sketch_text.stroke-2"),sQuery(id+"F2.wireOp",EDGE,"E2.sketch_text.stroke-3"),sQuery(id+"F2.wireOp",EDGE,"E2.sketch_text.stroke-4"),sQuery(id+"F2.wireOp",EDGE,"E2.sketch_text.stroke-5"),sQuery(id+"F2.wireOp",EDGE,"E2.sketch_text.stroke-6"),sQuery(id+"F2.wireOp",EDGE,"E2.sketch_text.stroke-7"),sQuery(id+"F2.wireOp",EDGE,"E2.sketch_text.stroke-8"),sQuery(id+"F2.wireOp",EDGE,"E2.sketch_text.stroke-9"),sQuery(id+"F2.wireOp",EDGE,"E2.sketch_text.stroke-10"),sQuery(id+"F2.wireOp",EDGE,"E2.sketch_text.stroke-11"),sQuery(id+"F2.wireOp",EDGE,"E2.sketch_text.stroke-12"),sQuery(id+"F2.wireOp",EDGE,"E2.sketch_text.stroke-13"),sQuery(id+"F2.wireOp",EDGE,"E2.sketch_text.stroke-14"),sQuery(id+"F2.wireOp",EDGE,"E2.sketch_text.stroke-15"),sQuery(id+"F2.wireOp",EDGE,"E2.sketch_text.stroke-16"),sQuery(id+"F2.wireOp",EDGE,"E2.sketch_text.stroke-17"),sQuery(id+"F2.wireOp",EDGE,"E2.sketch_text.stroke-18"),sQuery(id+"F2.wireOp",EDGE,"E2.sketch_text.stroke-19"),sQuery(id+"F2.wireOp",EDGE,"E2.sketch_text.stroke-20"),sQuery(id+"F2.wireOp",EDGE,"E2.sketch_text.stroke-21"),sQuery(id+"F2.wireOp",EDGE,"E2.sketch_text.stroke-22"),sQuery(id+"F2.wireOp",EDGE,"E2.sketch_text.stroke-23"),sQuery(id+"F2.wireOp",EDGE,"E2.sketch_text.stroke-24"),sQuery(id+"F2.wireOp",EDGE,"E2.sketch_text.stroke-25"),sQuery(id+"F2.wireOp",EDGE,"E2.sketch_text.stroke-26"),sQuery(id+"F2.wireOp",EDGE,"E2.sketch_text.stroke-27"),sQuery(id+"F2.wireOp",EDGE,"E2.sketch_text.stroke-28"),sQuery(id+"F2.wireOp",EDGE,"E2.sketch_text.stroke-29"),sQuery(id+"F2.wireOp",EDGE,"E2.sketch_text.stroke-30"),sQuery(id+"F2.wireOp",EDGE,"E2.sketch_text.stroke-31"),sQuery(id+"F2.wireOp",EDGE,"E2.sketch_text.stroke-32"),sQuery(id+"F2.wireOp",EDGE,"E2.sketch_text.stroke-33"),sQuery(id+"F2.wireOp",EDGE,"E2.sketch_text.stroke-34"),sQuery(id+"F2.wireOp",EDGE,"E2.sketch_text.stroke-35"),sQuery(id+"F2.wireOp",EDGE,"E2.sketch_text.stroke-36"),sQuery(id+"F2.wireOp",EDGE,"E2.sketch_text.stroke-37"),sQuery(id+"F2.wireOp",EDGE,"E2.sketch_text.stroke-38"),sQuery(id+"F2.wireOp",EDGE,"E2.sketch_text.stroke-39"),sQuery(id+"F2.wireOp",EDGE,"E2.sketch_text.stroke-40"),sQuery(id+"F2.wireOp",EDGE,"E2.sketch_text.stroke-41"),sQuery(id+"F2.wireOp",EDGE,"E2.sketch_text.stroke-42"),sQuery(id+"F2.wireOp",EDGE,"E2.sketch_text.stroke-43"),sQuery(id+"F2.wireOp",EDGE,"E2.sketch_text.stroke-44"),sQuery(id+"F2.wireOp",EDGE,"E2.sketch_text.stroke-45"),sQuery(id+"F2.wireOp",EDGE,"E2.sketch_text.stroke-46"),sQuery(id+"F2.wireOp",EDGE,"E2.sketch_text.stroke-47"),sQuery(id+"F2.wireOp",EDGE,"E2.sketch_text.stroke-48"),sQuery(id+"F2.wireOp",EDGE,"E2.sketch_text.stroke-49"),sQuery(id+"F2.wireOp",EDGE,"E2.sketch_text.stroke-50"),sQuery(id+"F2.wireOp",EDGE,"E2.sketch_text.stroke-51"),sQuery(id+"F2.wireOp",EDGE,"E2.sketch_text.stroke-52"),sQuery(id+"F2.wireOp",EDGE,"E2.sketch_text.stroke-53"),sQuery(id+"F2.wireOp",EDGE,"E2.sketch_text.stroke-54"),sQuery(id+"F2.wireOp",EDGE,"E2.sketch_text.stroke-55"),sQuery(id+"F2.wireOp",EDGE,"E2.sketch_text.stroke-56"),sQuery(id+"F2.wireOp",EDGE,"E2.sketch_text.stroke-57"),sQuery(id+"F2.wireOp",EDGE,"E2.sketch_text.stroke-58"),sQuery(id+"F2.wireOp",EDGE,"E2.sketch_text.stroke-59"),sQuery(id+"F2.wireOp",EDGE,"E2.sketch_text.stroke-60"),sQuery(id+"F2.wireOp",EDGE,"E2.sketch_text.stroke-61"),sQuery(id+"F2.wireOp",EDGE,"E2.sketch_text.stroke-62"),sQuery(id+"F2.wireOp",EDGE,"E2.sketch_text.stroke-63"),sQuery(id+"F2.wireOp",EDGE,"E2.sketch_text.stroke-64"),sQuery(id+"F2.wireOp",EDGE,"E2.sketch_text.stroke-65"),sQuery(id+"F2.wireOp",EDGE,"E2.sketch_text.stroke-66"),sQuery(id+"F2.wireOp",EDGE,"E2.sketch_text.stroke-67"),sQuery(id+"F2.wireOp",EDGE,"E2.sketch_text.stroke-68"),sQuery(id+"F2.wireOp",EDGE,"E2.sketch_text.stroke-69"),sQuery(id+"F2.wireOp",EDGE,"E2.sketch_text.stroke-70"),sQuery(id+"F2.wireOp",EDGE,"E2.sketch_text.stroke-71"),sQuery(id+"F2.wireOp",EDGE,"E2.sketch_text.stroke-72"),sQuery(id+"F2.wireOp",EDGE,"E2.sketch_text.stroke-73"),sQuery(id+"F2.wireOp",EDGE,"E2.sketch_text.stroke-74"),sQuery(id+"F2.wireOp",EDGE,"E2.sketch_text.stroke-75"),sQuery(id+"F2.wireOp",EDGE,"E2.sketch_text.stroke-76"),sQuery(id+"F2.wireOp",EDGE,"E2.sketch_text.stroke-77"),sQuery(id+"F2.wireOp",EDGE,"E2.sketch_text.stroke-78"),sQuery(id+"F2.wireOp",EDGE,"E2.sketch_text.stroke-79"),sQuery(id+"F2.wireOp",EDGE,"E2.sketch_text.stroke-80"),sQuery(id+"F2.wireOp",EDGE,"E2.sketch_text.stroke-81"),sQuery(id+"F2.wireOp",EDGE,"E2.sketch_text.stroke-82"),sQuery(id+"F2.wireOp",EDGE,"E2.sketch_text.stroke-83"),sQuery(id+"F2.wireOp",EDGE,"E2.sketch_text.stroke-84"),sQuery(id+"F2.wireOp",EDGE,"E2.sketch_text.stroke-85"),sQuery(id+"F2.wireOp",EDGE,"E2.sketch_text.stroke-86"),sQuery(id+"F2.wireOp",EDGE,"E2.sketch_text.stroke-87"),sQuery(id+"F2.wireOp",EDGE,"E2.sketch_text.stroke-88"),sQuery(id+"F2.wireOp",EDGE,"E2.sketch_text.stroke-89"),sQuery(id+"F2.wireOp",EDGE,"E2.sketch_text.stroke-90"),sQuery(id+"F2.wireOp",EDGE,"E2.sketch_text.stroke-91"),sQuery(id+"F2.wireOp",EDGE,"E2.sketch_text.stroke-92"),sQuery(id+"F2.wireOp",EDGE,"E2.sketch_text.stroke-93"),sQuery(id+"F2.wireOp",EDGE,"E2.sketch_text.stroke-94"),sQuery(id+"F2.wireOp",EDGE,"E2.sketch_text.stroke-95"),sQuery(id+"F2.wireOp",EDGE,"E2.sketch_text.stroke-96"),sQuery(id+"F2.wireOp",EDGE,"E2.sketch_text.stroke-97"),sQuery(id+"F2.wireOp",EDGE,"E2.sketch_text.stroke-98"),sQuery(id+"F2.wireOp",EDGE,"E2.sketch_text.stroke-99"),sQuery(id+"F2.wireOp",EDGE,"E2.sketch_text.stroke-100"),sQuery(id+"F2.wireOp",EDGE,"E2.sketch_text.stroke-101"),sQuery(id+"F2.wireOp",EDGE,"E2.sketch_text.stroke-102"),sQuery(id+"F2.wireOp",EDGE,"E2.sketch_text.stroke-103"),sQuery(id+"F2.wireOp",EDGE,"E2.sketch_text.stroke-104"),sQuery(id+"F2.wireOp",EDGE,"E2.sketch_text.stroke-105"),sQuery(id+"F2.wireOp",EDGE,"E2.sketch_text.stroke-106"),sQuery(id+"F2.wireOp",EDGE,"E2.sketch_text.stroke-107"),sQuery(id+"F2.wireOp",EDGE,"E2.sketch_text.stroke-108"),sQuery(id+"F2.wireOp",EDGE,"E2.sketch_text.stroke-109"),sQuery(id+"F2.wireOp",EDGE,"E2.sketch_text.stroke-110"),sQuery(id+"F2.wireOp",EDGE,"E2.sketch_text.stroke-111"),sQuery(id+"F2.wireOp",EDGE,"E2.sketch_text.stroke-112"),sQuery(id+"F2.wireOp",EDGE,"E2.sketch_text.stroke-113"),sQuery(id+"F2.wireOp",EDGE,"E2.sketch_text.stroke-114"),sQuery(id+"F2.wireOp",EDGE,"E2.sketch_text.stroke-115"),sQuery(id+"F2.wireOp",EDGE,"E2.sketch_text.stroke-116"),sQuery(id+"F2.wireOp",EDGE,"E2.sketch_text.stroke-117"),sQuery(id+"F2.wireOp",EDGE,"E2.sketch_text.stroke-118"),sQuery(id+"F2.wireOp",EDGE,"E2.sketch_text.stroke-119"),sQuery(id+"F2.wireOp",EDGE,"E2.sketch_text.stroke-120"),sQuery(id+"F2.wireOp",EDGE,"E2.sketch_text.stroke-121"),sQuery(id+"F2.wireOp",EDGE,"E2.sketch_text.stroke-122"),sQuery(id+"F2.wireOp",EDGE,"E2.sketch_text.stroke-123"),sQuery(id+"F2.wireOp",EDGE,"E2.sketch_text.stroke-124"),sQuery(id+"F2.wireOp",EDGE,"E2.sketch_text.stroke-125"),sQuery(id+"F2.wireOp",EDGE,"E2.sketch_text.stroke-126"),sQuery(id+"F2.wireOp",EDGE,"E2.sketch_text.stroke-127"),sQuery(id+"F2.wireOp",EDGE,"E2.sketch_text.stroke-128"),sQuery(id+"F2.wireOp",EDGE,"E2.sketch_text.stroke-129"),sQuery(id+"F2.wireOp",EDGE,"E2.sketch_text.stroke-130"),sQuery(id+"F2.wireOp",EDGE,"E2.sketch_text.stroke-131"),sQuery(id+"F2.wireOp",EDGE,"E2.sketch_text.stroke-132"),sQuery(id+"F2.wireOp",EDGE,"E2.sketch_text.stroke-133"),sQuery(id+"F2.wireOp",EDGE,"E2.sketch_text.stroke-134"),sQuery(id+"F2.wireOp",EDGE,"E2.sketch_text.stroke-135"),sQuery(id+"F2.wireOp",EDGE,"E2.sketch_text.stroke-136"),sQuery(id+"F2.wireOp",EDGE,"E2.sketch_text.stroke-137"),sQuery(id+"F2.wireOp",EDGE,"E2.sketch_text.stroke-138"),sQuery(id+"F2.wireOp",EDGE,"E2.sketch_text.stroke-139"),sQuery(id+"F2.wireOp",EDGE,"E2.sketch_text.stroke-140"),sQuery(id+"F2.wireOp",EDGE,"E2.sketch_text.stroke-141"),sQuery(id+"F2.wireOp",EDGE,"E2.sketch_text.stroke-142"),sQuery(id+"F2.wireOp",EDGE,"E2.sketch_text.stroke-143"),sQuery(id+"F2.wireOp",EDGE,"E2.sketch_text.stroke-144"),sQuery(id+"F2.wireOp",EDGE,"E2.sketch_text.stroke-145"),sQuery(id+"F2.wireOp",EDGE,"E2.sketch_text.stroke-146"),sQuery(id+"F2.wireOp",EDGE,"E2.sketch_text.stroke-147"),sQuery(id+"F2.wireOp",EDGE,"E2.sketch_text.stroke-148"),sQuery(id+"F2.wireOp",EDGE,"E2.sketch_text.stroke-149"),sQuery(id+"F2.wireOp",EDGE,"E2.sketch_text.stroke-150"),sQuery(id+"F2.wireOp",EDGE,"E2.sketch_text.stroke-151"),sQuery(id+"F2.wireOp",EDGE,"E2.sketch_text.stroke-152"),sQuery(id+"F2.wireOp",EDGE,"E2.sketch_text.stroke-153"),sQuery(id+"F2.wireOp",EDGE,"E2.sketch_text.stroke-154"),sQuery(id+"F2.wireOp",EDGE,"E2.sketch_text.stroke-155"),sQuery(id+"F2.wireOp",EDGE,"E2.sketch_text.stroke-156"),sQuery(id+"F2.wireOp",EDGE,"E2.sketch_text.stroke-157"),sQuery(id+"F2.wireOp",EDGE,"E2.sketch_text.stroke-158"),sQuery(id+"F2.wireOp",EDGE,"E2.sketch_text.stroke-159"),sQuery(id+"F2.wireOp",EDGE,"E2.sketch_text.stroke-160"),sQuery(id+"F2.wireOp",EDGE,"E2.sketch_text.stroke-161"),sQuery(id+"F2.wireOp",EDGE,"E2.sketch_text.stroke-162"),sQuery(id+"F2.wireOp",EDGE,"E2.sketch_text.stroke-163"),sQuery(id+"F2.wireOp",EDGE,"E2.sketch_text.stroke-164"),sQuery(id+"F2.wireOp",EDGE,"E2.sketch_text.stroke-165"),sQuery(id+"F2.wireOp",EDGE,"E2.sketch_text.stroke-166"),sQuery(id+"F2.wireOp",EDGE,"E2.sketch_text.stroke-167"),sQuery(id+"F2.wireOp",EDGE,"E2.sketch_text.stroke-168"),sQuery(id+"F2.wireOp",EDGE,"E2.sketch_text.stroke-169"),sQuery(id+"F2.wireOp",EDGE,"E2.sketch_text.stroke-170"),sQuery(id+"F2.wireOp",EDGE,"E2.sketch_text.stroke-171"),sQuery(id+"F2.wireOp",EDGE,"E2.sketch_text.stroke-172"),sQuery(id+"F2.wireOp",EDGE,"E2.sketch_text.stroke-173"),sQuery(id+"F3.wireOp",EDGE,"E4.sketch_text.stroke-0"),sQuery(id+"F3.wireOp",EDGE,"E4.sketch_text.stroke-1"),sQuery(id+"F3.wireOp",EDGE,"E4.sketch_text.stroke-2"),sQuery(id+"F3.wireOp",EDGE,"E4.sketch_text.stroke-3"),sQuery(id+"F3.wireOp",EDGE,"E4.sketch_text.stroke-4"),sQuery(id+"F3.wireOp",EDGE,"E4.sketch_text.stroke-5"),sQuery(id+"F3.wireOp",EDGE,"E4.sketch_text.stroke-6"),sQuery(id+"F3.wireOp",EDGE,"E4.sketch_text.stroke-7"),sQuery(id+"F3.wireOp",EDGE,"E4.sketch_text.stroke-8"),sQuery(id+"F3.wireOp",EDGE,"E4.sketch_text.stroke-9"),sQuery(id+"F3.wireOp",EDGE,"E4.sketch_text.stroke-10"),sQuery(id+"F3.wireOp",EDGE,"E4.sketch_text.stroke-11"),sQuery(id+"F3.wireOp",EDGE,"E4.sketch_text.stroke-12"),sQuery(id+"F3.wireOp",EDGE,"E4.sketch_text.stroke-13"),sQuery(id+"F3.wireOp",EDGE,"E4.sketch_text.stroke-14"),sQuery(id+"F3.wireOp",EDGE,"E4.sketch_text.stroke-15"),sQuery(id+"F3.wireOp",EDGE,"E4.sketch_text.stroke-16"),sQuery(id+"F3.wireOp",EDGE,"E4.sketch_text.stroke-17"),sQuery(id+"F3.wireOp",EDGE,"E4.sketch_text.stroke-18"),sQuery(id+"F3.wireOp",EDGE,"E4.sketch_text.stroke-19"),sQuery(id+"F3.wireOp",EDGE,"E4.sketch_text.stroke-20"),sQuery(id+"F3.wireOp",EDGE,"E4.sketch_text.stroke-21"),sQuery(id+"F3.wireOp",EDGE,"E4.sketch_text.stroke-22"),sQuery(id+"F3.wireOp",EDGE,"E4.sketch_text.stroke-23"),sQuery(id+"F3.wireOp",EDGE,"E4.sketch_text.stroke-24"),sQuery(id+"F3.wireOp",EDGE,"E4.sketch_text.stroke-25"),sQuery(id+"F3.wireOp",EDGE,"E4.sketch_text.stroke-26"),sQuery(id+"F3.wireOp",EDGE,"E4.sketch_text.stroke-27"),sQuery(id+"F3.wireOp",EDGE,"E4.sketch_text.stroke-28"),sQuery(id+"F3.wireOp",EDGE,"E4.sketch_text.stroke-29"),sQuery(id+"F3.wireOp",EDGE,"E4.sketch_text.stroke-30"),sQuery(id+"F3.wireOp",EDGE,"E4.sketch_text.stroke-31"),sQuery(id+"F3.wireOp",EDGE,"E4.sketch_text.stroke-32"),sQuery(id+"F3.wireOp",EDGE,"E4.sketch_text.stroke-33"),sQuery(id+"F3.wireOp",EDGE,"E4.sketch_text.stroke-34"),sQuery(id+"F3.wireOp",EDGE,"E4.sketch_text.stroke-35"),sQuery(id+"F3.wireOp",EDGE,"E4.sketch_text.stroke-36"),sQuery(id+"F3.wireOp",EDGE,"E4.sketch_text.stroke-37"),sQuery(id+"F3.wireOp",EDGE,"E4.sketch_text.stroke-38"),sQuery(id+"F3.wireOp",EDGE,"E4.sketch_text.stroke-39"),sQuery(id+"F3.wireOp",EDGE,"E4.sketch_text.stroke-40"),sQuery(id+"F3.wireOp",EDGE,"E4.sketch_text.stroke-41"),sQuery(id+"F3.wireOp",EDGE,"E4.sketch_text.stroke-42"),sQuery(id+"F3.wireOp",EDGE,"E4.sketch_text.stroke-43"),sQuery(id+"F3.wireOp",EDGE,"E4.sketch_text.stroke-44"),sQuery(id+"F3.wireOp",EDGE,"E4.sketch_text.stroke-45"),sQuery(id+"F3.wireOp",EDGE,"E4.sketch_text.stroke-46"),sQuery(id+"F3.wireOp",EDGE,"E4.sketch_text.stroke-47"),sQuery(id+"F3.wireOp",EDGE,"E4.sketch_text.stroke-48"),sQuery(id+"F3.wireOp",EDGE,"E4.sketch_text.stroke-49"),sQuery(id+"F3.wireOp",EDGE,"E4.sketch_text.stroke-50"),sQuery(id+"F3.wireOp",EDGE,"E4.sketch_text.stroke-51"),sQuery(id+"F3.wireOp",EDGE,"E4.sketch_text.stroke-52"),sQuery(id+"F3.wireOp",EDGE,"E4.sketch_text.stroke-53"),sQuery(id+"F3.wireOp",EDGE,"E4.sketch_text.stroke-54"),sQuery(id+"F3.wireOp",EDGE,"E4.sketch_text.stroke-55"),sQuery(id+"F3.wireOp",EDGE,"E4.sketch_text.stroke-56"),sQuery(id+"F3.wireOp",EDGE,"E4.sketch_text.stroke-57"),sQuery(id+"F3.wireOp",EDGE,"E4.sketch_text.stroke-58"),sQuery(id+"F3.wireOp",EDGE,"E4.sketch_text.stroke-59"),sQuery(id+"F3.wireOp",EDGE,"E4.sketch_text.stroke-60"),sQuery(id+"F3.wireOp",EDGE,"E4.sketch_text.stroke-61"),sQuery(id+"F3.wireOp",EDGE,"E4.sketch_text.stroke-62"),sQuery(id+"F3.wireOp",EDGE,"E4.sketch_text.stroke-71"),sQuery(id+"F3.wireOp",EDGE,"E4.sketch_text.stroke-72"),sQuery(id+"F3.wireOp",EDGE,"E4.sketch_text.stroke-73"),sQuery(id+"F3.wireOp",EDGE,"E4.sketch_text.stroke-74"),sQuery(id+"F3.wireOp",EDGE,"E4.sketch_text.stroke-75"),sQuery(id+"F3.wireOp",EDGE,"E4.sketch_text.stroke-76"),sQuery(id+"F3.wireOp",EDGE,"E4.sketch_text.stroke-77"),sQuery(id+"F3.wireOp",EDGE,"E4.sketch_text.stroke-78"),sQuery(id+"F3.wireOp",EDGE,"E4.sketch_text.stroke-79"),sQuery(id+"F3.wireOp",EDGE,"E4.sketch_text.stroke-80"),sQuery(id+"F3.wireOp",EDGE,"E4.sketch_text.stroke-81"),sQuery(id+"F3.wireOp",EDGE,"E4.sketch_text.stroke-82"),sQuery(id+"F3.wireOp",EDGE,"E4.sketch_text.stroke-83"),sQuery(id+"F3.wireOp",EDGE,"E4.sketch_text.stroke-84"),sQuery(id+"F3.wireOp",EDGE,"E4.sketch_text.stroke-85"),sQuery(id+"F3.wireOp",EDGE,"E4.sketch_text.stroke-86"),sQuery(id+"F3.wireOp",EDGE,"E4.sketch_text.stroke-87"),sQuery(id+"F3.wireOp",EDGE,"E4.sketch_text.stroke-88"),sQuery(id+"F3.wireOp",EDGE,"E4.sketch_text.stroke-89"),sQuery(id+"F3.wireOp",EDGE,"E4.sketch_text.stroke-90"),sQuery(id+"F3.wireOp",EDGE,"E4.sketch_text.stroke-91"),sQuery(id+"F3.wireOp",EDGE,"E4.sketch_text.stroke-92"),sQuery(id+"F3.wireOp",EDGE,"E4.sketch_text.stroke-93"),sQuery(id+"F3.wireOp",EDGE,"E4.sketch_text.stroke-94"),sQuery(id+"F3.wireOp",EDGE,"E4.sketch_text.stroke-95"),sQuery(id+"F3.wireOp",EDGE,"E4.sketch_text.stroke-96"),sQuery(id+"F3.wireOp",EDGE,"E4.sketch_text.stroke-97"),sQuery(id+"F3.wireOp",EDGE,"E4.sketch_text.stroke-103"),sQuery(id+"F3.wireOp",EDGE,"E4.sketch_text.stroke-104"),sQuery(id+"F3.wireOp",EDGE,"E4.sketch_text.stroke-105"),sQuery(id+"F3.wireOp",EDGE,"E4.sketch_text.stroke-106"),sQuery(id+"F3.wireOp",EDGE,"E4.sketch_text.stroke-107"),sQuery(id+"F3.wireOp",EDGE,"E4.sketch_text.stroke-108"),sQuery(id+"F3.wireOp",EDGE,"E4.sketch_text.stroke-109"),sQuery(id+"F3.wireOp",EDGE,"E4.sketch_text.stroke-110"),sQuery(id+"F3.wireOp",EDGE,"E4.sketch_text.stroke-111"),sQuery(id+"F3.wireOp",EDGE,"E4.sketch_text.stroke-112"),sQuery(id+"F3.wireOp",EDGE,"E4.sketch_text.stroke-113"),sQuery(id+"F3.wireOp",EDGE,"E4.sketch_text.stroke-114"),sQuery(id+"F3.wireOp",EDGE,"E4.sketch_text.stroke-115"),sQuery(id+"F3.wireOp",EDGE,"E4.sketch_text.stroke-116"),sQuery(id+"F3.wireOp",EDGE,"E4.sketch_text.stroke-117"),sQuery(id+"F3.wireOp",EDGE,"E4.sketch_text.stroke-118"),sQuery(id+"F3.wireOp",EDGE,"E4.sketch_text.stroke-119"),sQuery(id+"F3.wireOp",EDGE,"E4.sketch_text.stroke-120"),sQuery(id+"F3.wireOp",EDGE,"E4.sketch_text.stroke-121"),sQuery(id+"F3.wireOp",EDGE,"E4.sketch_text.stroke-122"),sQuery(id+"F3.wireOp",EDGE,"E4.sketch_text.stroke-123"),sQuery(id+"F3.wireOp",EDGE,"E4.sketch_text.stroke-124"),sQuery(id+"F3.wireOp",EDGE,"E4.sketch_text.stroke-125"),sQuery(id+"F3.wireOp",EDGE,"E4.sketch_text.stroke-126"),sQuery(id+"F3.wireOp",EDGE,"E4.sketch_text.stroke-127"),sQuery(id+"F3.wireOp",EDGE,"E4.sketch_text.stroke-128"),sQuery(id+"F3.wireOp",EDGE,"E4.sketch_text.stroke-129"),sQuery(id+"F3.wireOp",EDGE,"E4.sketch_text.stroke-130"),sQuery(id+"F3.wireOp",EDGE,"E4.sketch_text.stroke-131"),sQuery(id+"F3.wireOp",EDGE,"E4.sketch_text.stroke-132"),sQuery(id+"F3.wireOp",EDGE,"E4.sketch_text.stroke-133"),sQuery(id+"F3.wireOp",EDGE,"E4.sketch_text.stroke-134"),sQuery(id+"F3.wireOp",EDGE,"E4.sketch_text.stroke-135"),sQuery(id+"F3.wireOp",EDGE,"E4.sketch_text.stroke-136"),sQuery(id+"F3.wireOp",EDGE,"E4.sketch_text.stroke-137"),sQuery(id+"F3.wireOp",EDGE,"E4.sketch_text.stroke-138"),sQuery(id+"F3.wireOp",EDGE,"E4.sketch_text.stroke-139"),sQuery(id+"F3.wireOp",EDGE,"E4.sketch_text.stroke-140"),sQuery(id+"F3.wireOp",EDGE,"E4.sketch_text.stroke-141"),sQuery(id+"F3.wireOp",EDGE,"E4.sketch_text.stroke-142"),sQuery(id+"F3.wireOp",EDGE,"E4.sketch_text.stroke-143"),sQuery(id+"F3.wireOp",EDGE,"E4.sketch_text.stroke-144"),sQuery(id+"F3.wireOp",EDGE,"E4.sketch_text.stroke-145"),sQuery(id+"F3.wireOp",EDGE,"E4.sketch_text.stroke-146"),sQuery(id+"F3.wireOp",EDGE,"E4.sketch_text.stroke-147"),sQuery(id+"F3.wireOp",EDGE,"E4.sketch_text.stroke-148"),sQuery(id+"F3.wireOp",EDGE,"E4.sketch_text.stroke-149"),sQuery(id+"F3.wireOp",EDGE,"E4.sketch_text.stroke-150"),sQuery(id+"F3.wireOp",EDGE,"E4.sketch_text.stroke-151"),sQuery(id+"F3.wireOp",EDGE,"E4.sketch_text.stroke-152"),sQuery(id+"F3.wireOp",EDGE,"E4.sketch_text.stroke-153"),sQuery(id+"F3.wireOp",EDGE,"E4.sketch_text.stroke-159"),sQuery(id+"F3.wireOp",EDGE,"E4.sketch_text.stroke-160"),sQuery(id+"F3.wireOp",EDGE,"E4.sketch_text.stroke-161"),sQuery(id+"F3.wireOp",EDGE,"E4.sketch_text.stroke-162"),sQuery(id+"F3.wireOp",EDGE,"E4.sketch_text.stroke-163"),sQuery(id+"F3.wireOp",EDGE,"E4.sketch_text.stroke-164"),sQuery(id+"F3.wireOp",EDGE,"E4.sketch_text.stroke-165"),sQuery(id+"F3.wireOp",EDGE,"E4.sketch_text.stroke-166"),sQuery(id+"F3.wireOp",EDGE,"E4.sketch_text.stroke-167"),sQuery(id+"F3.wireOp",EDGE,"E4.sketch_text.stroke-168"),sQuery(id+"F3.wireOp",EDGE,"E4.sketch_text.stroke-169"),sQuery(id+"F3.wireOp",EDGE,"E4.sketch_text.stroke-170"),sQuery(id+"F3.wireOp",EDGE,"E4.sketch_text.stroke-171"),sQuery(id+"F3.wireOp",EDGE,"E4.sketch_text.stroke-172"),sQuery(id+"F3.wireOp",EDGE,"E4.sketch_text.stroke-173"),sQuery(id+"F3.wireOp",EDGE,"E4.sketch_text.stroke-174"),sQuery(id+"F3.wireOp",EDGE,"E4.sketch_text.stroke-175"),sQuery(id+"F3.wireOp",EDGE,"E4.sketch_text.stroke-176"),sQuery(id+"F3.wireOp",EDGE,"E4.sketch_text.stroke-177"),sQuery(id+"F3.wireOp",EDGE,"E4.sketch_text.stroke-178"),sQuery(id+"F3.wireOp",EDGE,"E4.sketch_text.stroke-179"),sQuery(id+"F3.wireOp",EDGE,"E4.sketch_text.stroke-180"),sQuery(id+"F4.wireOp",EDGE,"8007402e-1a4e-4a06-85a5-2af08e553504"),subQ2])],"isStart":true}),makeQuery(id+"F5.opExtrude","SWEPT_FACE",FACE,{"disambiguationData":[OSD([subQ2])]})])],"derivedFrom":makeQuery(id+"F5.opExtrude","CAP_EDGE",EDGE,{"disambiguationData":[OSD([subQ2])],"isStart":true})});}
            var Q8;
            Q8=makeQuery(id+"F1.opExtrude","CAP_EDGE",EDGE,{"disambiguationData":[OSD([sQuery(id+"F0.wireOp",EDGE,"E0.right")])],"isStart":false});
            var Q9;
            {var subQ0=sQuery(id+"F0.wireOp",EDGE,"E0.top");var subQ1=sQuery(id+"F0.wireOp",EDGE,"E0.bottom");var subQ2=sQuery(id+"F4.wireOp",EDGE,"6ee83ff3-586e-4dbe-aaea-af71240543bd");Q9=makeQuery(id+"F5.boolean.opBoolean","SPLIT",EDGE,{"disambiguationData":[TD([makeQuery(id+"F1.opExtrude","CAP_FACE",FACE,{"disambiguationData":[OSD([subQ1,subQ0,sQuery(id+"F0.wireOp",EDGE,"E0.left"),sQuery(id+"F0.wireOp",EDGE,"E0.right")])],"isStart":false}),makeQuery(id+"F1.opExtrude","SWEPT_FACE",FACE,{"disambiguationData":[OSD([subQ0])]}),makeQuery(id+"F5.opExtrude","CAP_FACE",FACE,{"disambiguationData":[OSD([subQ1,sQuery(id+"F2.wireOp",EDGE,"E2.sketch_text.stroke-0"),sQuery(id+"F2.wireOp",EDGE,"E2.sketch_text.stroke-1"),sQuery(id+"F2.wireOp",EDGE,"E2.sketch_text.stroke-2"),sQuery(id+"F2.wireOp",EDGE,"E2.sketch_text.stroke-3"),sQuery(id+"F2.wireOp",EDGE,"E2.sketch_text.stroke-4"),sQuery(id+"F2.wireOp",EDGE,"E2.sketch_text.stroke-5"),sQuery(id+"F2.wireOp",EDGE,"E2.sketch_text.stroke-6"),sQuery(id+"F2.wireOp",EDGE,"E2.sketch_text.stroke-7"),sQuery(id+"F2.wireOp",EDGE,"E2.sketch_text.stroke-8"),sQuery(id+"F2.wireOp",EDGE,"E2.sketch_text.stroke-9"),sQuery(id+"F2.wireOp",EDGE,"E2.sketch_text.stroke-10"),sQuery(id+"F2.wireOp",EDGE,"E2.sketch_text.stroke-11"),sQuery(id+"F2.wireOp",EDGE,"E2.sketch_text.stroke-12"),sQuery(id+"F2.wireOp",EDGE,"E2.sketch_text.stroke-13"),sQuery(id+"F2.wireOp",EDGE,"E2.sketch_text.stroke-14"),sQuery(id+"F2.wireOp",EDGE,"E2.sketch_text.stroke-15"),sQuery(id+"F2.wireOp",EDGE,"E2.sketch_text.stroke-16"),sQuery(id+"F2.wireOp",EDGE,"E2.sketch_text.stroke-17"),sQuery(id+"F2.wireOp",EDGE,"E2.sketch_text.stroke-18"),sQuery(id+"F2.wireOp",EDGE,"E2.sketch_text.stroke-19"),sQuery(id+"F2.wireOp",EDGE,"E2.sketch_text.stroke-20"),sQuery(id+"F2.wireOp",EDGE,"E2.sketch_text.stroke-21"),sQuery(id+"F2.wireOp",EDGE,"E2.sketch_text.stroke-22"),sQuery(id+"F2.wireOp",EDGE,"E2.sketch_text.stroke-23"),sQuery(id+"F2.wireOp",EDGE,"E2.sketch_text.stroke-24"),sQuery(id+"F2.wireOp",EDGE,"E2.sketch_text.stroke-25"),sQuery(id+"F2.wireOp",EDGE,"E2.sketch_text.stroke-26"),sQuery(id+"F2.wireOp",EDGE,"E2.sketch_text.stroke-27"),sQuery(id+"F2.wireOp",EDGE,"E2.sketch_text.stroke-28"),sQuery(id+"F2.wireOp",EDGE,"E2.sketch_text.stroke-29"),sQuery(id+"F2.wireOp",EDGE,"E2.sketch_text.stroke-30"),sQuery(id+"F2.wireOp",EDGE,"E2.sketch_text.stroke-31"),sQuery(id+"F2.wireOp",EDGE,"E2.sketch_text.stroke-32"),sQuery(id+"F2.wireOp",EDGE,"E2.sketch_text.stroke-33"),sQuery(id+"F2.wireOp",EDGE,"E2.sketch_text.stroke-34"),sQuery(id+"F2.wireOp",EDGE,"E2.sketch_text.stroke-35"),sQuery(id+"F2.wireOp",EDGE,"E2.sketch_text.stroke-36"),sQuery(id+"F2.wireOp",EDGE,"E2.sketch_text.stroke-37"),sQuery(id+"F2.wireOp",EDGE,"E2.sketch_text.stroke-38"),sQuery(id+"F2.wireOp",EDGE,"E2.sketch_text.stroke-39"),sQuery(id+"F2.wireOp",EDGE,"E2.sketch_text.stroke-40"),sQuery(id+"F2.wireOp",EDGE,"E2.sketch_text.stroke-41"),sQuery(id+"F2.wireOp",EDGE,"E2.sketch_text.stroke-42"),sQuery(id+"F2.wireOp",EDGE,"E2.sketch_text.stroke-43"),sQuery(id+"F2.wireOp",EDGE,"E2.sketch_text.stroke-44"),sQuery(id+"F2.wireOp",EDGE,"E2.sketch_text.stroke-45"),sQuery(id+"F2.wireOp",EDGE,"E2.sketch_text.stroke-46"),sQuery(id+"F2.wireOp",EDGE,"E2.sketch_text.stroke-47"),sQuery(id+"F2.wireOp",EDGE,"E2.sketch_text.stroke-48"),sQuery(id+"F2.wireOp",EDGE,"E2.sketch_text.stroke-49"),sQuery(id+"F2.wireOp",EDGE,"E2.sketch_text.stroke-50"),sQuery(id+"F2.wireOp",EDGE,"E2.sketch_text.stroke-51"),sQuery(id+"F2.wireOp",EDGE,"E2.sketch_text.stroke-52"),sQuery(id+"F2.wireOp",EDGE,"E2.sketch_text.stroke-53"),sQuery(id+"F2.wireOp",EDGE,"E2.sketch_text.stroke-54"),sQuery(id+"F2.wireOp",EDGE,"E2.sketch_text.stroke-55"),sQuery(id+"F2.wireOp",EDGE,"E2.sketch_text.stroke-56"),sQuery(id+"F2.wireOp",EDGE,"E2.sketch_text.stroke-57"),sQuery(id+"F2.wireOp",EDGE,"E2.sketch_text.stroke-58"),sQuery(id+"F2.wireOp",EDGE,"E2.sketch_text.stroke-59"),sQuery(id+"F2.wireOp",EDGE,"E2.sketch_text.stroke-60"),sQuery(id+"F2.wireOp",EDGE,"E2.sketch_text.stroke-61"),sQuery(id+"F2.wireOp",EDGE,"E2.sketch_text.stroke-62"),sQuery(id+"F2.wireOp",EDGE,"E2.sketch_text.stroke-63"),sQuery(id+"F2.wireOp",EDGE,"E2.sketch_text.stroke-64"),sQuery(id+"F2.wireOp",EDGE,"E2.sketch_text.stroke-65"),sQuery(id+"F2.wireOp",EDGE,"E2.sketch_text.stroke-66"),sQuery(id+"F2.wireOp",EDGE,"E2.sketch_text.stroke-67"),sQuery(id+"F2.wireOp",EDGE,"E2.sketch_text.stroke-68"),sQuery(id+"F2.wireOp",EDGE,"E2.sketch_text.stroke-69"),sQuery(id+"F2.wireOp",EDGE,"E2.sketch_text.stroke-70"),sQuery(id+"F2.wireOp",EDGE,"E2.sketch_text.stroke-71"),sQuery(id+"F2.wireOp",EDGE,"E2.sketch_text.stroke-72"),sQuery(id+"F2.wireOp",EDGE,"E2.sketch_text.stroke-73"),sQuery(id+"F2.wireOp",EDGE,"E2.sketch_text.stroke-74"),sQuery(id+"F2.wireOp",EDGE,"E2.sketch_text.stroke-75"),sQuery(id+"F2.wireOp",EDGE,"E2.sketch_text.stroke-76"),sQuery(id+"F2.wireOp",EDGE,"E2.sketch_text.stroke-77"),sQuery(id+"F2.wireOp",EDGE,"E2.sketch_text.stroke-78"),sQuery(id+"F2.wireOp",EDGE,"E2.sketch_text.stroke-79"),sQuery(id+"F2.wireOp",EDGE,"E2.sketch_text.stroke-80"),sQuery(id+"F2.wireOp",EDGE,"E2.sketch_text.stroke-81"),sQuery(id+"F2.wireOp",EDGE,"E2.sketch_text.stroke-82"),sQuery(id+"F2.wireOp",EDGE,"E2.sketch_text.stroke-83"),sQuery(id+"F2.wireOp",EDGE,"E2.sketch_text.stroke-84"),sQuery(id+"F2.wireOp",EDGE,"E2.sketch_text.stroke-85"),sQuery(id+"F2.wireOp",EDGE,"E2.sketch_text.stroke-86"),sQuery(id+"F2.wireOp",EDGE,"E2.sketch_text.stroke-87"),sQuery(id+"F2.wireOp",EDGE,"E2.sketch_text.stroke-88"),sQuery(id+"F2.wireOp",EDGE,"E2.sketch_text.stroke-89"),sQuery(id+"F2.wireOp",EDGE,"E2.sketch_text.stroke-90"),sQuery(id+"F2.wireOp",EDGE,"E2.sketch_text.stroke-91"),sQuery(id+"F2.wireOp",EDGE,"E2.sketch_text.stroke-92"),sQuery(id+"F2.wireOp",EDGE,"E2.sketch_text.stroke-93"),sQuery(id+"F2.wireOp",EDGE,"E2.sketch_text.stroke-94"),sQuery(id+"F2.wireOp",EDGE,"E2.sketch_text.stroke-95"),sQuery(id+"F2.wireOp",EDGE,"E2.sketch_text.stroke-96"),sQuery(id+"F2.wireOp",EDGE,"E2.sketch_text.stroke-97"),sQuery(id+"F2.wireOp",EDGE,"E2.sketch_text.stroke-98"),sQuery(id+"F2.wireOp",EDGE,"E2.sketch_text.stroke-99"),sQuery(id+"F2.wireOp",EDGE,"E2.sketch_text.stroke-100"),sQuery(id+"F2.wireOp",EDGE,"E2.sketch_text.stroke-101"),sQuery(id+"F2.wireOp",EDGE,"E2.sketch_text.stroke-102"),sQuery(id+"F2.wireOp",EDGE,"E2.sketch_text.stroke-103"),sQuery(id+"F2.wireOp",EDGE,"E2.sketch_text.stroke-104"),sQuery(id+"F2.wireOp",EDGE,"E2.sketch_text.stroke-105"),sQuery(id+"F2.wireOp",EDGE,"E2.sketch_text.stroke-106"),sQuery(id+"F2.wireOp",EDGE,"E2.sketch_text.stroke-107"),sQuery(id+"F2.wireOp",EDGE,"E2.sketch_text.stroke-108"),sQuery(id+"F2.wireOp",EDGE,"E2.sketch_text.stroke-109"),sQuery(id+"F2.wireOp",EDGE,"E2.sketch_text.stroke-110"),sQuery(id+"F2.wireOp",EDGE,"E2.sketch_text.stroke-111"),sQuery(id+"F2.wireOp",EDGE,"E2.sketch_text.stroke-112"),sQuery(id+"F2.wireOp",EDGE,"E2.sketch_text.stroke-113"),sQuery(id+"F2.wireOp",EDGE,"E2.sketch_text.stroke-114"),sQuery(id+"F2.wireOp",EDGE,"E2.sketch_text.stroke-115"),sQuery(id+"F2.wireOp",EDGE,"E2.sketch_text.stroke-116"),sQuery(id+"F2.wireOp",EDGE,"E2.sketch_text.stroke-117"),sQuery(id+"F2.wireOp",EDGE,"E2.sketch_text.stroke-118"),sQuery(id+"F2.wireOp",EDGE,"E2.sketch_text.stroke-119"),sQuery(id+"F2.wireOp",EDGE,"E2.sketch_text.stroke-120"),sQuery(id+"F2.wireOp",EDGE,"E2.sketch_text.stroke-121"),sQuery(id+"F2.wireOp",EDGE,"E2.sketch_text.stroke-122"),sQuery(id+"F2.wireOp",EDGE,"E2.sketch_text.stroke-123"),sQuery(id+"F2.wireOp",EDGE,"E2.sketch_text.stroke-124"),sQuery(id+"F2.wireOp",EDGE,"E2.sketch_text.stroke-125"),sQuery(id+"F2.wireOp",EDGE,"E2.sketch_text.stroke-126"),sQuery(id+"F2.wireOp",EDGE,"E2.sketch_text.stroke-127"),sQuery(id+"F2.wireOp",EDGE,"E2.sketch_text.stroke-128"),sQuery(id+"F2.wireOp",EDGE,"E2.sketch_text.stroke-129"),sQuery(id+"F2.wireOp",EDGE,"E2.sketch_text.stroke-130"),sQuery(id+"F2.wireOp",EDGE,"E2.sketch_text.stroke-131"),sQuery(id+"F2.wireOp",EDGE,"E2.sketch_text.stroke-132"),sQuery(id+"F2.wireOp",EDGE,"E2.sketch_text.stroke-133"),sQuery(id+"F2.wireOp",EDGE,"E2.sketch_text.stroke-134"),sQuery(id+"F2.wireOp",EDGE,"E2.sketch_text.stroke-135"),sQuery(id+"F2.wireOp",EDGE,"E2.sketch_text.stroke-136"),sQuery(id+"F2.wireOp",EDGE,"E2.sketch_text.stroke-137"),sQuery(id+"F2.wireOp",EDGE,"E2.sketch_text.stroke-138"),sQuery(id+"F2.wireOp",EDGE,"E2.sketch_text.stroke-139"),sQuery(id+"F2.wireOp",EDGE,"E2.sketch_text.stroke-140"),sQuery(id+"F2.wireOp",EDGE,"E2.sketch_text.stroke-141"),sQuery(id+"F2.wireOp",EDGE,"E2.sketch_text.stroke-142"),sQuery(id+"F2.wireOp",EDGE,"E2.sketch_text.stroke-143"),sQuery(id+"F2.wireOp",EDGE,"E2.sketch_text.stroke-144"),sQuery(id+"F2.wireOp",EDGE,"E2.sketch_text.stroke-145"),sQuery(id+"F2.wireOp",EDGE,"E2.sketch_text.stroke-146"),sQuery(id+"F2.wireOp",EDGE,"E2.sketch_text.stroke-147"),sQuery(id+"F2.wireOp",EDGE,"E2.sketch_text.stroke-148"),sQuery(id+"F2.wireOp",EDGE,"E2.sketch_text.stroke-149"),sQuery(id+"F2.wireOp",EDGE,"E2.sketch_text.stroke-150"),sQuery(id+"F2.wireOp",EDGE,"E2.sketch_text.stroke-151"),sQuery(id+"F2.wireOp",EDGE,"E2.sketch_text.stroke-152"),sQuery(id+"F2.wireOp",EDGE,"E2.sketch_text.stroke-153"),sQuery(id+"F2.wireOp",EDGE,"E2.sketch_text.stroke-154"),sQuery(id+"F2.wireOp",EDGE,"E2.sketch_text.stroke-155"),sQuery(id+"F2.wireOp",EDGE,"E2.sketch_text.stroke-156"),sQuery(id+"F2.wireOp",EDGE,"E2.sketch_text.stroke-157"),sQuery(id+"F2.wireOp",EDGE,"E2.sketch_text.stroke-158"),sQuery(id+"F2.wireOp",EDGE,"E2.sketch_text.stroke-159"),sQuery(id+"F2.wireOp",EDGE,"E2.sketch_text.stroke-160"),sQuery(id+"F2.wireOp",EDGE,"E2.sketch_text.stroke-161"),sQuery(id+"F2.wireOp",EDGE,"E2.sketch_text.stroke-162"),sQuery(id+"F2.wireOp",EDGE,"E2.sketch_text.stroke-163"),sQuery(id+"F2.wireOp",EDGE,"E2.sketch_text.stroke-164"),sQuery(id+"F2.wireOp",EDGE,"E2.sketch_text.stroke-165"),sQuery(id+"F2.wireOp",EDGE,"E2.sketch_text.stroke-166"),sQuery(id+"F2.wireOp",EDGE,"E2.sketch_text.stroke-167"),sQuery(id+"F2.wireOp",EDGE,"E2.sketch_text.stroke-168"),sQuery(id+"F2.wireOp",EDGE,"E2.sketch_text.stroke-169"),sQuery(id+"F2.wireOp",EDGE,"E2.sketch_text.stroke-170"),sQuery(id+"F2.wireOp",EDGE,"E2.sketch_text.stroke-171"),sQuery(id+"F2.wireOp",EDGE,"E2.sketch_text.stroke-172"),sQuery(id+"F2.wireOp",EDGE,"E2.sketch_text.stroke-173"),sQuery(id+"F3.wireOp",EDGE,"E4.sketch_text.stroke-0"),sQuery(id+"F3.wireOp",EDGE,"E4.sketch_text.stroke-1"),sQuery(id+"F3.wireOp",EDGE,"E4.sketch_text.stroke-2"),sQuery(id+"F3.wireOp",EDGE,"E4.sketch_text.stroke-3"),sQuery(id+"F3.wireOp",EDGE,"E4.sketch_text.stroke-4"),sQuery(id+"F3.wireOp",EDGE,"E4.sketch_text.stroke-5"),sQuery(id+"F3.wireOp",EDGE,"E4.sketch_text.stroke-6"),sQuery(id+"F3.wireOp",EDGE,"E4.sketch_text.stroke-7"),sQuery(id+"F3.wireOp",EDGE,"E4.sketch_text.stroke-8"),sQuery(id+"F3.wireOp",EDGE,"E4.sketch_text.stroke-9"),sQuery(id+"F3.wireOp",EDGE,"E4.sketch_text.stroke-10"),sQuery(id+"F3.wireOp",EDGE,"E4.sketch_text.stroke-11"),sQuery(id+"F3.wireOp",EDGE,"E4.sketch_text.stroke-12"),sQuery(id+"F3.wireOp",EDGE,"E4.sketch_text.stroke-13"),sQuery(id+"F3.wireOp",EDGE,"E4.sketch_text.stroke-14"),sQuery(id+"F3.wireOp",EDGE,"E4.sketch_text.stroke-15"),sQuery(id+"F3.wireOp",EDGE,"E4.sketch_text.stroke-16"),sQuery(id+"F3.wireOp",EDGE,"E4.sketch_text.stroke-17"),sQuery(id+"F3.wireOp",EDGE,"E4.sketch_text.stroke-18"),sQuery(id+"F3.wireOp",EDGE,"E4.sketch_text.stroke-19"),sQuery(id+"F3.wireOp",EDGE,"E4.sketch_text.stroke-20"),sQuery(id+"F3.wireOp",EDGE,"E4.sketch_text.stroke-21"),sQuery(id+"F3.wireOp",EDGE,"E4.sketch_text.stroke-22"),sQuery(id+"F3.wireOp",EDGE,"E4.sketch_text.stroke-23"),sQuery(id+"F3.wireOp",EDGE,"E4.sketch_text.stroke-24"),sQuery(id+"F3.wireOp",EDGE,"E4.sketch_text.stroke-25"),sQuery(id+"F3.wireOp",EDGE,"E4.sketch_text.stroke-26"),sQuery(id+"F3.wireOp",EDGE,"E4.sketch_text.stroke-27"),sQuery(id+"F3.wireOp",EDGE,"E4.sketch_text.stroke-28"),sQuery(id+"F3.wireOp",EDGE,"E4.sketch_text.stroke-29"),sQuery(id+"F3.wireOp",EDGE,"E4.sketch_text.stroke-30"),sQuery(id+"F3.wireOp",EDGE,"E4.sketch_text.stroke-31"),sQuery(id+"F3.wireOp",EDGE,"E4.sketch_text.stroke-32"),sQuery(id+"F3.wireOp",EDGE,"E4.sketch_text.stroke-33"),sQuery(id+"F3.wireOp",EDGE,"E4.sketch_text.stroke-34"),sQuery(id+"F3.wireOp",EDGE,"E4.sketch_text.stroke-35"),sQuery(id+"F3.wireOp",EDGE,"E4.sketch_text.stroke-36"),sQuery(id+"F3.wireOp",EDGE,"E4.sketch_text.stroke-37"),sQuery(id+"F3.wireOp",EDGE,"E4.sketch_text.stroke-38"),sQuery(id+"F3.wireOp",EDGE,"E4.sketch_text.stroke-39"),sQuery(id+"F3.wireOp",EDGE,"E4.sketch_text.stroke-40"),sQuery(id+"F3.wireOp",EDGE,"E4.sketch_text.stroke-41"),sQuery(id+"F3.wireOp",EDGE,"E4.sketch_text.stroke-42"),sQuery(id+"F3.wireOp",EDGE,"E4.sketch_text.stroke-43"),sQuery(id+"F3.wireOp",EDGE,"E4.sketch_text.stroke-44"),sQuery(id+"F3.wireOp",EDGE,"E4.sketch_text.stroke-45"),sQuery(id+"F3.wireOp",EDGE,"E4.sketch_text.stroke-46"),sQuery(id+"F3.wireOp",EDGE,"E4.sketch_text.stroke-47"),sQuery(id+"F3.wireOp",EDGE,"E4.sketch_text.stroke-48"),sQuery(id+"F3.wireOp",EDGE,"E4.sketch_text.stroke-49"),sQuery(id+"F3.wireOp",EDGE,"E4.sketch_text.stroke-50"),sQuery(id+"F3.wireOp",EDGE,"E4.sketch_text.stroke-51"),sQuery(id+"F3.wireOp",EDGE,"E4.sketch_text.stroke-52"),sQuery(id+"F3.wireOp",EDGE,"E4.sketch_text.stroke-53"),sQuery(id+"F3.wireOp",EDGE,"E4.sketch_text.stroke-54"),sQuery(id+"F3.wireOp",EDGE,"E4.sketch_text.stroke-55"),sQuery(id+"F3.wireOp",EDGE,"E4.sketch_text.stroke-56"),sQuery(id+"F3.wireOp",EDGE,"E4.sketch_text.stroke-57"),sQuery(id+"F3.wireOp",EDGE,"E4.sketch_text.stroke-58"),sQuery(id+"F3.wireOp",EDGE,"E4.sketch_text.stroke-59"),sQuery(id+"F3.wireOp",EDGE,"E4.sketch_text.stroke-60"),sQuery(id+"F3.wireOp",EDGE,"E4.sketch_text.stroke-61"),sQuery(id+"F3.wireOp",EDGE,"E4.sketch_text.stroke-62"),sQuery(id+"F3.wireOp",EDGE,"E4.sketch_text.stroke-71"),sQuery(id+"F3.wireOp",EDGE,"E4.sketch_text.stroke-72"),sQuery(id+"F3.wireOp",EDGE,"E4.sketch_text.stroke-73"),sQuery(id+"F3.wireOp",EDGE,"E4.sketch_text.stroke-74"),sQuery(id+"F3.wireOp",EDGE,"E4.sketch_text.stroke-75"),sQuery(id+"F3.wireOp",EDGE,"E4.sketch_text.stroke-76"),sQuery(id+"F3.wireOp",EDGE,"E4.sketch_text.stroke-77"),sQuery(id+"F3.wireOp",EDGE,"E4.sketch_text.stroke-78"),sQuery(id+"F3.wireOp",EDGE,"E4.sketch_text.stroke-79"),sQuery(id+"F3.wireOp",EDGE,"E4.sketch_text.stroke-80"),sQuery(id+"F3.wireOp",EDGE,"E4.sketch_text.stroke-81"),sQuery(id+"F3.wireOp",EDGE,"E4.sketch_text.stroke-82"),sQuery(id+"F3.wireOp",EDGE,"E4.sketch_text.stroke-83"),sQuery(id+"F3.wireOp",EDGE,"E4.sketch_text.stroke-84"),sQuery(id+"F3.wireOp",EDGE,"E4.sketch_text.stroke-85"),sQuery(id+"F3.wireOp",EDGE,"E4.sketch_text.stroke-86"),sQuery(id+"F3.wireOp",EDGE,"E4.sketch_text.stroke-87"),sQuery(id+"F3.wireOp",EDGE,"E4.sketch_text.stroke-88"),sQuery(id+"F3.wireOp",EDGE,"E4.sketch_text.stroke-89"),sQuery(id+"F3.wireOp",EDGE,"E4.sketch_text.stroke-90"),sQuery(id+"F3.wireOp",EDGE,"E4.sketch_text.stroke-91"),sQuery(id+"F3.wireOp",EDGE,"E4.sketch_text.stroke-92"),sQuery(id+"F3.wireOp",EDGE,"E4.sketch_text.stroke-93"),sQuery(id+"F3.wireOp",EDGE,"E4.sketch_text.stroke-94"),sQuery(id+"F3.wireOp",EDGE,"E4.sketch_text.stroke-95"),sQuery(id+"F3.wireOp",EDGE,"E4.sketch_text.stroke-96"),sQuery(id+"F3.wireOp",EDGE,"E4.sketch_text.stroke-97"),sQuery(id+"F3.wireOp",EDGE,"E4.sketch_text.stroke-103"),sQuery(id+"F3.wireOp",EDGE,"E4.sketch_text.stroke-104"),sQuery(id+"F3.wireOp",EDGE,"E4.sketch_text.stroke-105"),sQuery(id+"F3.wireOp",EDGE,"E4.sketch_text.stroke-106"),sQuery(id+"F3.wireOp",EDGE,"E4.sketch_text.stroke-107"),sQuery(id+"F3.wireOp",EDGE,"E4.sketch_text.stroke-108"),sQuery(id+"F3.wireOp",EDGE,"E4.sketch_text.stroke-109"),sQuery(id+"F3.wireOp",EDGE,"E4.sketch_text.stroke-110"),sQuery(id+"F3.wireOp",EDGE,"E4.sketch_text.stroke-111"),sQuery(id+"F3.wireOp",EDGE,"E4.sketch_text.stroke-112"),sQuery(id+"F3.wireOp",EDGE,"E4.sketch_text.stroke-113"),sQuery(id+"F3.wireOp",EDGE,"E4.sketch_text.stroke-114"),sQuery(id+"F3.wireOp",EDGE,"E4.sketch_text.stroke-115"),sQuery(id+"F3.wireOp",EDGE,"E4.sketch_text.stroke-116"),sQuery(id+"F3.wireOp",EDGE,"E4.sketch_text.stroke-117"),sQuery(id+"F3.wireOp",EDGE,"E4.sketch_text.stroke-118"),sQuery(id+"F3.wireOp",EDGE,"E4.sketch_text.stroke-119"),sQuery(id+"F3.wireOp",EDGE,"E4.sketch_text.stroke-120"),sQuery(id+"F3.wireOp",EDGE,"E4.sketch_text.stroke-121"),sQuery(id+"F3.wireOp",EDGE,"E4.sketch_text.stroke-122"),sQuery(id+"F3.wireOp",EDGE,"E4.sketch_text.stroke-123"),sQuery(id+"F3.wireOp",EDGE,"E4.sketch_text.stroke-124"),sQuery(id+"F3.wireOp",EDGE,"E4.sketch_text.stroke-125"),sQuery(id+"F3.wireOp",EDGE,"E4.sketch_text.stroke-126"),sQuery(id+"F3.wireOp",EDGE,"E4.sketch_text.stroke-127"),sQuery(id+"F3.wireOp",EDGE,"E4.sketch_text.stroke-128"),sQuery(id+"F3.wireOp",EDGE,"E4.sketch_text.stroke-129"),sQuery(id+"F3.wireOp",EDGE,"E4.sketch_text.stroke-130"),sQuery(id+"F3.wireOp",EDGE,"E4.sketch_text.stroke-131"),sQuery(id+"F3.wireOp",EDGE,"E4.sketch_text.stroke-132"),sQuery(id+"F3.wireOp",EDGE,"E4.sketch_text.stroke-133"),sQuery(id+"F3.wireOp",EDGE,"E4.sketch_text.stroke-134"),sQuery(id+"F3.wireOp",EDGE,"E4.sketch_text.stroke-135"),sQuery(id+"F3.wireOp",EDGE,"E4.sketch_text.stroke-136"),sQuery(id+"F3.wireOp",EDGE,"E4.sketch_text.stroke-137"),sQuery(id+"F3.wireOp",EDGE,"E4.sketch_text.stroke-138"),sQuery(id+"F3.wireOp",EDGE,"E4.sketch_text.stroke-139"),sQuery(id+"F3.wireOp",EDGE,"E4.sketch_text.stroke-140"),sQuery(id+"F3.wireOp",EDGE,"E4.sketch_text.stroke-141"),sQuery(id+"F3.wireOp",EDGE,"E4.sketch_text.stroke-142"),sQuery(id+"F3.wireOp",EDGE,"E4.sketch_text.stroke-143"),sQuery(id+"F3.wireOp",EDGE,"E4.sketch_text.stroke-144"),sQuery(id+"F3.wireOp",EDGE,"E4.sketch_text.stroke-145"),sQuery(id+"F3.wireOp",EDGE,"E4.sketch_text.stroke-146"),sQuery(id+"F3.wireOp",EDGE,"E4.sketch_text.stroke-147"),sQuery(id+"F3.wireOp",EDGE,"E4.sketch_text.stroke-148"),sQuery(id+"F3.wireOp",EDGE,"E4.sketch_text.stroke-149"),sQuery(id+"F3.wireOp",EDGE,"E4.sketch_text.stroke-150"),sQuery(id+"F3.wireOp",EDGE,"E4.sketch_text.stroke-151"),sQuery(id+"F3.wireOp",EDGE,"E4.sketch_text.stroke-152"),sQuery(id+"F3.wireOp",EDGE,"E4.sketch_text.stroke-153"),sQuery(id+"F3.wireOp",EDGE,"E4.sketch_text.stroke-159"),sQuery(id+"F3.wireOp",EDGE,"E4.sketch_text.stroke-160"),sQuery(id+"F3.wireOp",EDGE,"E4.sketch_text.stroke-161"),sQuery(id+"F3.wireOp",EDGE,"E4.sketch_text.stroke-162"),sQuery(id+"F3.wireOp",EDGE,"E4.sketch_text.stroke-163"),sQuery(id+"F3.wireOp",EDGE,"E4.sketch_text.stroke-164"),sQuery(id+"F3.wireOp",EDGE,"E4.sketch_text.stroke-165"),sQuery(id+"F3.wireOp",EDGE,"E4.sketch_text.stroke-166"),sQuery(id+"F3.wireOp",EDGE,"E4.sketch_text.stroke-167"),sQuery(id+"F3.wireOp",EDGE,"E4.sketch_text.stroke-168"),sQuery(id+"F3.wireOp",EDGE,"E4.sketch_text.stroke-169"),sQuery(id+"F3.wireOp",EDGE,"E4.sketch_text.stroke-170"),sQuery(id+"F3.wireOp",EDGE,"E4.sketch_text.stroke-171"),sQuery(id+"F3.wireOp",EDGE,"E4.sketch_text.stroke-172"),sQuery(id+"F3.wireOp",EDGE,"E4.sketch_text.stroke-173"),sQuery(id+"F3.wireOp",EDGE,"E4.sketch_text.stroke-174"),sQuery(id+"F3.wireOp",EDGE,"E4.sketch_text.stroke-175"),sQuery(id+"F3.wireOp",EDGE,"E4.sketch_text.stroke-176"),sQuery(id+"F3.wireOp",EDGE,"E4.sketch_text.stroke-177"),sQuery(id+"F3.wireOp",EDGE,"E4.sketch_text.stroke-178"),sQuery(id+"F3.wireOp",EDGE,"E4.sketch_text.stroke-179"),sQuery(id+"F3.wireOp",EDGE,"E4.sketch_text.stroke-180"),sQuery(id+"F4.wireOp",EDGE,"8007402e-1a4e-4a06-85a5-2af08e553504"),subQ2])],"isStart":true}),makeQuery(id+"F5.opExtrude","SWEPT_FACE",FACE,{"disambiguationData":[OSD([subQ2])]})])],"derivedFrom":makeQuery(id+"F5.opExtrude","CAP_EDGE",EDGE,{"disambiguationData":[OSD([subQ2])],"isStart":true})});}
            var Q10;
            {var subQ0=sQuery(id+"F4.wireOp",EDGE,"8007402e-1a4e-4a06-85a5-2af08e553504");var subQ1=sQuery(id+"F0.wireOp",EDGE,"E0.top");var subQ2=sQuery(id+"F4.wireOp",EDGE,"6ee83ff3-586e-4dbe-aaea-af71240543bd");var subQ3=sQuery(id+"F0.wireOp",EDGE,"E0.bottom");Q10=makeQuery(id+"F5.boolean.opBoolean","SPLIT",EDGE,{"disambiguationData":[TD([makeQuery(id+"F1.opExtrude","CAP_FACE",FACE,{"disambiguationData":[OSD([subQ3,subQ1,sQuery(id+"F0.wireOp",EDGE,"E0.left"),sQuery(id+"F0.wireOp",EDGE,"E0.right")])],"isStart":false}),makeQuery(id+"F1.opExtrude","SWEPT_FACE",FACE,{"disambiguationData":[OSD([subQ1])]}),makeQuery(id+"F5.opExtrude","SWEPT_FACE",FACE,{"disambiguationData":[OSD([subQ0])]}),makeQuery(id+"F5.opExtrude","CAP_FACE",FACE,{"disambiguationData":[OSD([subQ3,sQuery(id+"F2.wireOp",EDGE,"E2.sketch_text.stroke-0"),sQuery(id+"F2.wireOp",EDGE,"E2.sketch_text.stroke-1"),sQuery(id+"F2.wireOp",EDGE,"E2.sketch_text.stroke-2"),sQuery(id+"F2.wireOp",EDGE,"E2.sketch_text.stroke-3"),sQuery(id+"F2.wireOp",EDGE,"E2.sketch_text.stroke-4"),sQuery(id+"F2.wireOp",EDGE,"E2.sketch_text.stroke-5"),sQuery(id+"F2.wireOp",EDGE,"E2.sketch_text.stroke-6"),sQuery(id+"F2.wireOp",EDGE,"E2.sketch_text.stroke-7"),sQuery(id+"F2.wireOp",EDGE,"E2.sketch_text.stroke-8"),sQuery(id+"F2.wireOp",EDGE,"E2.sketch_text.stroke-9"),sQuery(id+"F2.wireOp",EDGE,"E2.sketch_text.stroke-10"),sQuery(id+"F2.wireOp",EDGE,"E2.sketch_text.stroke-11"),sQuery(id+"F2.wireOp",EDGE,"E2.sketch_text.stroke-12"),sQuery(id+"F2.wireOp",EDGE,"E2.sketch_text.stroke-13"),sQuery(id+"F2.wireOp",EDGE,"E2.sketch_text.stroke-14"),sQuery(id+"F2.wireOp",EDGE,"E2.sketch_text.stroke-15"),sQuery(id+"F2.wireOp",EDGE,"E2.sketch_text.stroke-16"),sQuery(id+"F2.wireOp",EDGE,"E2.sketch_text.stroke-17"),sQuery(id+"F2.wireOp",EDGE,"E2.sketch_text.stroke-18"),sQuery(id+"F2.wireOp",EDGE,"E2.sketch_text.stroke-19"),sQuery(id+"F2.wireOp",EDGE,"E2.sketch_text.stroke-20"),sQuery(id+"F2.wireOp",EDGE,"E2.sketch_text.stroke-21"),sQuery(id+"F2.wireOp",EDGE,"E2.sketch_text.stroke-22"),sQuery(id+"F2.wireOp",EDGE,"E2.sketch_text.stroke-23"),sQuery(id+"F2.wireOp",EDGE,"E2.sketch_text.stroke-24"),sQuery(id+"F2.wireOp",EDGE,"E2.sketch_text.stroke-25"),sQuery(id+"F2.wireOp",EDGE,"E2.sketch_text.stroke-26"),sQuery(id+"F2.wireOp",EDGE,"E2.sketch_text.stroke-27"),sQuery(id+"F2.wireOp",EDGE,"E2.sketch_text.stroke-28"),sQuery(id+"F2.wireOp",EDGE,"E2.sketch_text.stroke-29"),sQuery(id+"F2.wireOp",EDGE,"E2.sketch_text.stroke-30"),sQuery(id+"F2.wireOp",EDGE,"E2.sketch_text.stroke-31"),sQuery(id+"F2.wireOp",EDGE,"E2.sketch_text.stroke-32"),sQuery(id+"F2.wireOp",EDGE,"E2.sketch_text.stroke-33"),sQuery(id+"F2.wireOp",EDGE,"E2.sketch_text.stroke-34"),sQuery(id+"F2.wireOp",EDGE,"E2.sketch_text.stroke-35"),sQuery(id+"F2.wireOp",EDGE,"E2.sketch_text.stroke-36"),sQuery(id+"F2.wireOp",EDGE,"E2.sketch_text.stroke-37"),sQuery(id+"F2.wireOp",EDGE,"E2.sketch_text.stroke-38"),sQuery(id+"F2.wireOp",EDGE,"E2.sketch_text.stroke-39"),sQuery(id+"F2.wireOp",EDGE,"E2.sketch_text.stroke-40"),sQuery(id+"F2.wireOp",EDGE,"E2.sketch_text.stroke-41"),sQuery(id+"F2.wireOp",EDGE,"E2.sketch_text.stroke-42"),sQuery(id+"F2.wireOp",EDGE,"E2.sketch_text.stroke-43"),sQuery(id+"F2.wireOp",EDGE,"E2.sketch_text.stroke-44"),sQuery(id+"F2.wireOp",EDGE,"E2.sketch_text.stroke-45"),sQuery(id+"F2.wireOp",EDGE,"E2.sketch_text.stroke-46"),sQuery(id+"F2.wireOp",EDGE,"E2.sketch_text.stroke-47"),sQuery(id+"F2.wireOp",EDGE,"E2.sketch_text.stroke-48"),sQuery(id+"F2.wireOp",EDGE,"E2.sketch_text.stroke-49"),sQuery(id+"F2.wireOp",EDGE,"E2.sketch_text.stroke-50"),sQuery(id+"F2.wireOp",EDGE,"E2.sketch_text.stroke-51"),sQuery(id+"F2.wireOp",EDGE,"E2.sketch_text.stroke-52"),sQuery(id+"F2.wireOp",EDGE,"E2.sketch_text.stroke-53"),sQuery(id+"F2.wireOp",EDGE,"E2.sketch_text.stroke-54"),sQuery(id+"F2.wireOp",EDGE,"E2.sketch_text.stroke-55"),sQuery(id+"F2.wireOp",EDGE,"E2.sketch_text.stroke-56"),sQuery(id+"F2.wireOp",EDGE,"E2.sketch_text.stroke-57"),sQuery(id+"F2.wireOp",EDGE,"E2.sketch_text.stroke-58"),sQuery(id+"F2.wireOp",EDGE,"E2.sketch_text.stroke-59"),sQuery(id+"F2.wireOp",EDGE,"E2.sketch_text.stroke-60"),sQuery(id+"F2.wireOp",EDGE,"E2.sketch_text.stroke-61"),sQuery(id+"F2.wireOp",EDGE,"E2.sketch_text.stroke-62"),sQuery(id+"F2.wireOp",EDGE,"E2.sketch_text.stroke-63"),sQuery(id+"F2.wireOp",EDGE,"E2.sketch_text.stroke-64"),sQuery(id+"F2.wireOp",EDGE,"E2.sketch_text.stroke-65"),sQuery(id+"F2.wireOp",EDGE,"E2.sketch_text.stroke-66"),sQuery(id+"F2.wireOp",EDGE,"E2.sketch_text.stroke-67"),sQuery(id+"F2.wireOp",EDGE,"E2.sketch_text.stroke-68"),sQuery(id+"F2.wireOp",EDGE,"E2.sketch_text.stroke-69"),sQuery(id+"F2.wireOp",EDGE,"E2.sketch_text.stroke-70"),sQuery(id+"F2.wireOp",EDGE,"E2.sketch_text.stroke-71"),sQuery(id+"F2.wireOp",EDGE,"E2.sketch_text.stroke-72"),sQuery(id+"F2.wireOp",EDGE,"E2.sketch_text.stroke-73"),sQuery(id+"F2.wireOp",EDGE,"E2.sketch_text.stroke-74"),sQuery(id+"F2.wireOp",EDGE,"E2.sketch_text.stroke-75"),sQuery(id+"F2.wireOp",EDGE,"E2.sketch_text.stroke-76"),sQuery(id+"F2.wireOp",EDGE,"E2.sketch_text.stroke-77"),sQuery(id+"F2.wireOp",EDGE,"E2.sketch_text.stroke-78"),sQuery(id+"F2.wireOp",EDGE,"E2.sketch_text.stroke-79"),sQuery(id+"F2.wireOp",EDGE,"E2.sketch_text.stroke-80"),sQuery(id+"F2.wireOp",EDGE,"E2.sketch_text.stroke-81"),sQuery(id+"F2.wireOp",EDGE,"E2.sketch_text.stroke-82"),sQuery(id+"F2.wireOp",EDGE,"E2.sketch_text.stroke-83"),sQuery(id+"F2.wireOp",EDGE,"E2.sketch_text.stroke-84"),sQuery(id+"F2.wireOp",EDGE,"E2.sketch_text.stroke-85"),sQuery(id+"F2.wireOp",EDGE,"E2.sketch_text.stroke-86"),sQuery(id+"F2.wireOp",EDGE,"E2.sketch_text.stroke-87"),sQuery(id+"F2.wireOp",EDGE,"E2.sketch_text.stroke-88"),sQuery(id+"F2.wireOp",EDGE,"E2.sketch_text.stroke-89"),sQuery(id+"F2.wireOp",EDGE,"E2.sketch_text.stroke-90"),sQuery(id+"F2.wireOp",EDGE,"E2.sketch_text.stroke-91"),sQuery(id+"F2.wireOp",EDGE,"E2.sketch_text.stroke-92"),sQuery(id+"F2.wireOp",EDGE,"E2.sketch_text.stroke-93"),sQuery(id+"F2.wireOp",EDGE,"E2.sketch_text.stroke-94"),sQuery(id+"F2.wireOp",EDGE,"E2.sketch_text.stroke-95"),sQuery(id+"F2.wireOp",EDGE,"E2.sketch_text.stroke-96"),sQuery(id+"F2.wireOp",EDGE,"E2.sketch_text.stroke-97"),sQuery(id+"F2.wireOp",EDGE,"E2.sketch_text.stroke-98"),sQuery(id+"F2.wireOp",EDGE,"E2.sketch_text.stroke-99"),sQuery(id+"F2.wireOp",EDGE,"E2.sketch_text.stroke-100"),sQuery(id+"F2.wireOp",EDGE,"E2.sketch_text.stroke-101"),sQuery(id+"F2.wireOp",EDGE,"E2.sketch_text.stroke-102"),sQuery(id+"F2.wireOp",EDGE,"E2.sketch_text.stroke-103"),sQuery(id+"F2.wireOp",EDGE,"E2.sketch_text.stroke-104"),sQuery(id+"F2.wireOp",EDGE,"E2.sketch_text.stroke-105"),sQuery(id+"F2.wireOp",EDGE,"E2.sketch_text.stroke-106"),sQuery(id+"F2.wireOp",EDGE,"E2.sketch_text.stroke-107"),sQuery(id+"F2.wireOp",EDGE,"E2.sketch_text.stroke-108"),sQuery(id+"F2.wireOp",EDGE,"E2.sketch_text.stroke-109"),sQuery(id+"F2.wireOp",EDGE,"E2.sketch_text.stroke-110"),sQuery(id+"F2.wireOp",EDGE,"E2.sketch_text.stroke-111"),sQuery(id+"F2.wireOp",EDGE,"E2.sketch_text.stroke-112"),sQuery(id+"F2.wireOp",EDGE,"E2.sketch_text.stroke-113"),sQuery(id+"F2.wireOp",EDGE,"E2.sketch_text.stroke-114"),sQuery(id+"F2.wireOp",EDGE,"E2.sketch_text.stroke-115"),sQuery(id+"F2.wireOp",EDGE,"E2.sketch_text.stroke-116"),sQuery(id+"F2.wireOp",EDGE,"E2.sketch_text.stroke-117"),sQuery(id+"F2.wireOp",EDGE,"E2.sketch_text.stroke-118"),sQuery(id+"F2.wireOp",EDGE,"E2.sketch_text.stroke-119"),sQuery(id+"F2.wireOp",EDGE,"E2.sketch_text.stroke-120"),sQuery(id+"F2.wireOp",EDGE,"E2.sketch_text.stroke-121"),sQuery(id+"F2.wireOp",EDGE,"E2.sketch_text.stroke-122"),sQuery(id+"F2.wireOp",EDGE,"E2.sketch_text.stroke-123"),sQuery(id+"F2.wireOp",EDGE,"E2.sketch_text.stroke-124"),sQuery(id+"F2.wireOp",EDGE,"E2.sketch_text.stroke-125"),sQuery(id+"F2.wireOp",EDGE,"E2.sketch_text.stroke-126"),sQuery(id+"F2.wireOp",EDGE,"E2.sketch_text.stroke-127"),sQuery(id+"F2.wireOp",EDGE,"E2.sketch_text.stroke-128"),sQuery(id+"F2.wireOp",EDGE,"E2.sketch_text.stroke-129"),sQuery(id+"F2.wireOp",EDGE,"E2.sketch_text.stroke-130"),sQuery(id+"F2.wireOp",EDGE,"E2.sketch_text.stroke-131"),sQuery(id+"F2.wireOp",EDGE,"E2.sketch_text.stroke-132"),sQuery(id+"F2.wireOp",EDGE,"E2.sketch_text.stroke-133"),sQuery(id+"F2.wireOp",EDGE,"E2.sketch_text.stroke-134"),sQuery(id+"F2.wireOp",EDGE,"E2.sketch_text.stroke-135"),sQuery(id+"F2.wireOp",EDGE,"E2.sketch_text.stroke-136"),sQuery(id+"F2.wireOp",EDGE,"E2.sketch_text.stroke-137"),sQuery(id+"F2.wireOp",EDGE,"E2.sketch_text.stroke-138"),sQuery(id+"F2.wireOp",EDGE,"E2.sketch_text.stroke-139"),sQuery(id+"F2.wireOp",EDGE,"E2.sketch_text.stroke-140"),sQuery(id+"F2.wireOp",EDGE,"E2.sketch_text.stroke-141"),sQuery(id+"F2.wireOp",EDGE,"E2.sketch_text.stroke-142"),sQuery(id+"F2.wireOp",EDGE,"E2.sketch_text.stroke-143"),sQuery(id+"F2.wireOp",EDGE,"E2.sketch_text.stroke-144"),sQuery(id+"F2.wireOp",EDGE,"E2.sketch_text.stroke-145"),sQuery(id+"F2.wireOp",EDGE,"E2.sketch_text.stroke-146"),sQuery(id+"F2.wireOp",EDGE,"E2.sketch_text.stroke-147"),sQuery(id+"F2.wireOp",EDGE,"E2.sketch_text.stroke-148"),sQuery(id+"F2.wireOp",EDGE,"E2.sketch_text.stroke-149"),sQuery(id+"F2.wireOp",EDGE,"E2.sketch_text.stroke-150"),sQuery(id+"F2.wireOp",EDGE,"E2.sketch_text.stroke-151"),sQuery(id+"F2.wireOp",EDGE,"E2.sketch_text.stroke-152"),sQuery(id+"F2.wireOp",EDGE,"E2.sketch_text.stroke-153"),sQuery(id+"F2.wireOp",EDGE,"E2.sketch_text.stroke-154"),sQuery(id+"F2.wireOp",EDGE,"E2.sketch_text.stroke-155"),sQuery(id+"F2.wireOp",EDGE,"E2.sketch_text.stroke-156"),sQuery(id+"F2.wireOp",EDGE,"E2.sketch_text.stroke-157"),sQuery(id+"F2.wireOp",EDGE,"E2.sketch_text.stroke-158"),sQuery(id+"F2.wireOp",EDGE,"E2.sketch_text.stroke-159"),sQuery(id+"F2.wireOp",EDGE,"E2.sketch_text.stroke-160"),sQuery(id+"F2.wireOp",EDGE,"E2.sketch_text.stroke-161"),sQuery(id+"F2.wireOp",EDGE,"E2.sketch_text.stroke-162"),sQuery(id+"F2.wireOp",EDGE,"E2.sketch_text.stroke-163"),sQuery(id+"F2.wireOp",EDGE,"E2.sketch_text.stroke-164"),sQuery(id+"F2.wireOp",EDGE,"E2.sketch_text.stroke-165"),sQuery(id+"F2.wireOp",EDGE,"E2.sketch_text.stroke-166"),sQuery(id+"F2.wireOp",EDGE,"E2.sketch_text.stroke-167"),sQuery(id+"F2.wireOp",EDGE,"E2.sketch_text.stroke-168"),sQuery(id+"F2.wireOp",EDGE,"E2.sketch_text.stroke-169"),sQuery(id+"F2.wireOp",EDGE,"E2.sketch_text.stroke-170"),sQuery(id+"F2.wireOp",EDGE,"E2.sketch_text.stroke-171"),sQuery(id+"F2.wireOp",EDGE,"E2.sketch_text.stroke-172"),sQuery(id+"F2.wireOp",EDGE,"E2.sketch_text.stroke-173"),sQuery(id+"F3.wireOp",EDGE,"E4.sketch_text.stroke-0"),sQuery(id+"F3.wireOp",EDGE,"E4.sketch_text.stroke-1"),sQuery(id+"F3.wireOp",EDGE,"E4.sketch_text.stroke-2"),sQuery(id+"F3.wireOp",EDGE,"E4.sketch_text.stroke-3"),sQuery(id+"F3.wireOp",EDGE,"E4.sketch_text.stroke-4"),sQuery(id+"F3.wireOp",EDGE,"E4.sketch_text.stroke-5"),sQuery(id+"F3.wireOp",EDGE,"E4.sketch_text.stroke-6"),sQuery(id+"F3.wireOp",EDGE,"E4.sketch_text.stroke-7"),sQuery(id+"F3.wireOp",EDGE,"E4.sketch_text.stroke-8"),sQuery(id+"F3.wireOp",EDGE,"E4.sketch_text.stroke-9"),sQuery(id+"F3.wireOp",EDGE,"E4.sketch_text.stroke-10"),sQuery(id+"F3.wireOp",EDGE,"E4.sketch_text.stroke-11"),sQuery(id+"F3.wireOp",EDGE,"E4.sketch_text.stroke-12"),sQuery(id+"F3.wireOp",EDGE,"E4.sketch_text.stroke-13"),sQuery(id+"F3.wireOp",EDGE,"E4.sketch_text.stroke-14"),sQuery(id+"F3.wireOp",EDGE,"E4.sketch_text.stroke-15"),sQuery(id+"F3.wireOp",EDGE,"E4.sketch_text.stroke-16"),sQuery(id+"F3.wireOp",EDGE,"E4.sketch_text.stroke-17"),sQuery(id+"F3.wireOp",EDGE,"E4.sketch_text.stroke-18"),sQuery(id+"F3.wireOp",EDGE,"E4.sketch_text.stroke-19"),sQuery(id+"F3.wireOp",EDGE,"E4.sketch_text.stroke-20"),sQuery(id+"F3.wireOp",EDGE,"E4.sketch_text.stroke-21"),sQuery(id+"F3.wireOp",EDGE,"E4.sketch_text.stroke-22"),sQuery(id+"F3.wireOp",EDGE,"E4.sketch_text.stroke-23"),sQuery(id+"F3.wireOp",EDGE,"E4.sketch_text.stroke-24"),sQuery(id+"F3.wireOp",EDGE,"E4.sketch_text.stroke-25"),sQuery(id+"F3.wireOp",EDGE,"E4.sketch_text.stroke-26"),sQuery(id+"F3.wireOp",EDGE,"E4.sketch_text.stroke-27"),sQuery(id+"F3.wireOp",EDGE,"E4.sketch_text.stroke-28"),sQuery(id+"F3.wireOp",EDGE,"E4.sketch_text.stroke-29"),sQuery(id+"F3.wireOp",EDGE,"E4.sketch_text.stroke-30"),sQuery(id+"F3.wireOp",EDGE,"E4.sketch_text.stroke-31"),sQuery(id+"F3.wireOp",EDGE,"E4.sketch_text.stroke-32"),sQuery(id+"F3.wireOp",EDGE,"E4.sketch_text.stroke-33"),sQuery(id+"F3.wireOp",EDGE,"E4.sketch_text.stroke-34"),sQuery(id+"F3.wireOp",EDGE,"E4.sketch_text.stroke-35"),sQuery(id+"F3.wireOp",EDGE,"E4.sketch_text.stroke-36"),sQuery(id+"F3.wireOp",EDGE,"E4.sketch_text.stroke-37"),sQuery(id+"F3.wireOp",EDGE,"E4.sketch_text.stroke-38"),sQuery(id+"F3.wireOp",EDGE,"E4.sketch_text.stroke-39"),sQuery(id+"F3.wireOp",EDGE,"E4.sketch_text.stroke-40"),sQuery(id+"F3.wireOp",EDGE,"E4.sketch_text.stroke-41"),sQuery(id+"F3.wireOp",EDGE,"E4.sketch_text.stroke-42"),sQuery(id+"F3.wireOp",EDGE,"E4.sketch_text.stroke-43"),sQuery(id+"F3.wireOp",EDGE,"E4.sketch_text.stroke-44"),sQuery(id+"F3.wireOp",EDGE,"E4.sketch_text.stroke-45"),sQuery(id+"F3.wireOp",EDGE,"E4.sketch_text.stroke-46"),sQuery(id+"F3.wireOp",EDGE,"E4.sketch_text.stroke-47"),sQuery(id+"F3.wireOp",EDGE,"E4.sketch_text.stroke-48"),sQuery(id+"F3.wireOp",EDGE,"E4.sketch_text.stroke-49"),sQuery(id+"F3.wireOp",EDGE,"E4.sketch_text.stroke-50"),sQuery(id+"F3.wireOp",EDGE,"E4.sketch_text.stroke-51"),sQuery(id+"F3.wireOp",EDGE,"E4.sketch_text.stroke-52"),sQuery(id+"F3.wireOp",EDGE,"E4.sketch_text.stroke-53"),sQuery(id+"F3.wireOp",EDGE,"E4.sketch_text.stroke-54"),sQuery(id+"F3.wireOp",EDGE,"E4.sketch_text.stroke-55"),sQuery(id+"F3.wireOp",EDGE,"E4.sketch_text.stroke-56"),sQuery(id+"F3.wireOp",EDGE,"E4.sketch_text.stroke-57"),sQuery(id+"F3.wireOp",EDGE,"E4.sketch_text.stroke-58"),sQuery(id+"F3.wireOp",EDGE,"E4.sketch_text.stroke-59"),sQuery(id+"F3.wireOp",EDGE,"E4.sketch_text.stroke-60"),sQuery(id+"F3.wireOp",EDGE,"E4.sketch_text.stroke-61"),sQuery(id+"F3.wireOp",EDGE,"E4.sketch_text.stroke-62"),sQuery(id+"F3.wireOp",EDGE,"E4.sketch_text.stroke-71"),sQuery(id+"F3.wireOp",EDGE,"E4.sketch_text.stroke-72"),sQuery(id+"F3.wireOp",EDGE,"E4.sketch_text.stroke-73"),sQuery(id+"F3.wireOp",EDGE,"E4.sketch_text.stroke-74"),sQuery(id+"F3.wireOp",EDGE,"E4.sketch_text.stroke-75"),sQuery(id+"F3.wireOp",EDGE,"E4.sketch_text.stroke-76"),sQuery(id+"F3.wireOp",EDGE,"E4.sketch_text.stroke-77"),sQuery(id+"F3.wireOp",EDGE,"E4.sketch_text.stroke-78"),sQuery(id+"F3.wireOp",EDGE,"E4.sketch_text.stroke-79"),sQuery(id+"F3.wireOp",EDGE,"E4.sketch_text.stroke-80"),sQuery(id+"F3.wireOp",EDGE,"E4.sketch_text.stroke-81"),sQuery(id+"F3.wireOp",EDGE,"E4.sketch_text.stroke-82"),sQuery(id+"F3.wireOp",EDGE,"E4.sketch_text.stroke-83"),sQuery(id+"F3.wireOp",EDGE,"E4.sketch_text.stroke-84"),sQuery(id+"F3.wireOp",EDGE,"E4.sketch_text.stroke-85"),sQuery(id+"F3.wireOp",EDGE,"E4.sketch_text.stroke-86"),sQuery(id+"F3.wireOp",EDGE,"E4.sketch_text.stroke-87"),sQuery(id+"F3.wireOp",EDGE,"E4.sketch_text.stroke-88"),sQuery(id+"F3.wireOp",EDGE,"E4.sketch_text.stroke-89"),sQuery(id+"F3.wireOp",EDGE,"E4.sketch_text.stroke-90"),sQuery(id+"F3.wireOp",EDGE,"E4.sketch_text.stroke-91"),sQuery(id+"F3.wireOp",EDGE,"E4.sketch_text.stroke-92"),sQuery(id+"F3.wireOp",EDGE,"E4.sketch_text.stroke-93"),sQuery(id+"F3.wireOp",EDGE,"E4.sketch_text.stroke-94"),sQuery(id+"F3.wireOp",EDGE,"E4.sketch_text.stroke-95"),sQuery(id+"F3.wireOp",EDGE,"E4.sketch_text.stroke-96"),sQuery(id+"F3.wireOp",EDGE,"E4.sketch_text.stroke-97"),sQuery(id+"F3.wireOp",EDGE,"E4.sketch_text.stroke-103"),sQuery(id+"F3.wireOp",EDGE,"E4.sketch_text.stroke-104"),sQuery(id+"F3.wireOp",EDGE,"E4.sketch_text.stroke-105"),sQuery(id+"F3.wireOp",EDGE,"E4.sketch_text.stroke-106"),sQuery(id+"F3.wireOp",EDGE,"E4.sketch_text.stroke-107"),sQuery(id+"F3.wireOp",EDGE,"E4.sketch_text.stroke-108"),sQuery(id+"F3.wireOp",EDGE,"E4.sketch_text.stroke-109"),sQuery(id+"F3.wireOp",EDGE,"E4.sketch_text.stroke-110"),sQuery(id+"F3.wireOp",EDGE,"E4.sketch_text.stroke-111"),sQuery(id+"F3.wireOp",EDGE,"E4.sketch_text.stroke-112"),sQuery(id+"F3.wireOp",EDGE,"E4.sketch_text.stroke-113"),sQuery(id+"F3.wireOp",EDGE,"E4.sketch_text.stroke-114"),sQuery(id+"F3.wireOp",EDGE,"E4.sketch_text.stroke-115"),sQuery(id+"F3.wireOp",EDGE,"E4.sketch_text.stroke-116"),sQuery(id+"F3.wireOp",EDGE,"E4.sketch_text.stroke-117"),sQuery(id+"F3.wireOp",EDGE,"E4.sketch_text.stroke-118"),sQuery(id+"F3.wireOp",EDGE,"E4.sketch_text.stroke-119"),sQuery(id+"F3.wireOp",EDGE,"E4.sketch_text.stroke-120"),sQuery(id+"F3.wireOp",EDGE,"E4.sketch_text.stroke-121"),sQuery(id+"F3.wireOp",EDGE,"E4.sketch_text.stroke-122"),sQuery(id+"F3.wireOp",EDGE,"E4.sketch_text.stroke-123"),sQuery(id+"F3.wireOp",EDGE,"E4.sketch_text.stroke-124"),sQuery(id+"F3.wireOp",EDGE,"E4.sketch_text.stroke-125"),sQuery(id+"F3.wireOp",EDGE,"E4.sketch_text.stroke-126"),sQuery(id+"F3.wireOp",EDGE,"E4.sketch_text.stroke-127"),sQuery(id+"F3.wireOp",EDGE,"E4.sketch_text.stroke-128"),sQuery(id+"F3.wireOp",EDGE,"E4.sketch_text.stroke-129"),sQuery(id+"F3.wireOp",EDGE,"E4.sketch_text.stroke-130"),sQuery(id+"F3.wireOp",EDGE,"E4.sketch_text.stroke-131"),sQuery(id+"F3.wireOp",EDGE,"E4.sketch_text.stroke-132"),sQuery(id+"F3.wireOp",EDGE,"E4.sketch_text.stroke-133"),sQuery(id+"F3.wireOp",EDGE,"E4.sketch_text.stroke-134"),sQuery(id+"F3.wireOp",EDGE,"E4.sketch_text.stroke-135"),sQuery(id+"F3.wireOp",EDGE,"E4.sketch_text.stroke-136"),sQuery(id+"F3.wireOp",EDGE,"E4.sketch_text.stroke-137"),sQuery(id+"F3.wireOp",EDGE,"E4.sketch_text.stroke-138"),sQuery(id+"F3.wireOp",EDGE,"E4.sketch_text.stroke-139"),sQuery(id+"F3.wireOp",EDGE,"E4.sketch_text.stroke-140"),sQuery(id+"F3.wireOp",EDGE,"E4.sketch_text.stroke-141"),sQuery(id+"F3.wireOp",EDGE,"E4.sketch_text.stroke-142"),sQuery(id+"F3.wireOp",EDGE,"E4.sketch_text.stroke-143"),sQuery(id+"F3.wireOp",EDGE,"E4.sketch_text.stroke-144"),sQuery(id+"F3.wireOp",EDGE,"E4.sketch_text.stroke-145"),sQuery(id+"F3.wireOp",EDGE,"E4.sketch_text.stroke-146"),sQuery(id+"F3.wireOp",EDGE,"E4.sketch_text.stroke-147"),sQuery(id+"F3.wireOp",EDGE,"E4.sketch_text.stroke-148"),sQuery(id+"F3.wireOp",EDGE,"E4.sketch_text.stroke-149"),sQuery(id+"F3.wireOp",EDGE,"E4.sketch_text.stroke-150"),sQuery(id+"F3.wireOp",EDGE,"E4.sketch_text.stroke-151"),sQuery(id+"F3.wireOp",EDGE,"E4.sketch_text.stroke-152"),sQuery(id+"F3.wireOp",EDGE,"E4.sketch_text.stroke-153"),sQuery(id+"F3.wireOp",EDGE,"E4.sketch_text.stroke-159"),sQuery(id+"F3.wireOp",EDGE,"E4.sketch_text.stroke-160"),sQuery(id+"F3.wireOp",EDGE,"E4.sketch_text.stroke-161"),sQuery(id+"F3.wireOp",EDGE,"E4.sketch_text.stroke-162"),sQuery(id+"F3.wireOp",EDGE,"E4.sketch_text.stroke-163"),sQuery(id+"F3.wireOp",EDGE,"E4.sketch_text.stroke-164"),sQuery(id+"F3.wireOp",EDGE,"E4.sketch_text.stroke-165"),sQuery(id+"F3.wireOp",EDGE,"E4.sketch_text.stroke-166"),sQuery(id+"F3.wireOp",EDGE,"E4.sketch_text.stroke-167"),sQuery(id+"F3.wireOp",EDGE,"E4.sketch_text.stroke-168"),sQuery(id+"F3.wireOp",EDGE,"E4.sketch_text.stroke-169"),sQuery(id+"F3.wireOp",EDGE,"E4.sketch_text.stroke-170"),sQuery(id+"F3.wireOp",EDGE,"E4.sketch_text.stroke-171"),sQuery(id+"F3.wireOp",EDGE,"E4.sketch_text.stroke-172"),sQuery(id+"F3.wireOp",EDGE,"E4.sketch_text.stroke-173"),sQuery(id+"F3.wireOp",EDGE,"E4.sketch_text.stroke-174"),sQuery(id+"F3.wireOp",EDGE,"E4.sketch_text.stroke-175"),sQuery(id+"F3.wireOp",EDGE,"E4.sketch_text.stroke-176"),sQuery(id+"F3.wireOp",EDGE,"E4.sketch_text.stroke-177"),sQuery(id+"F3.wireOp",EDGE,"E4.sketch_text.stroke-178"),sQuery(id+"F3.wireOp",EDGE,"E4.sketch_text.stroke-179"),sQuery(id+"F3.wireOp",EDGE,"E4.sketch_text.stroke-180"),subQ0,subQ2])],"isStart":true}),makeQuery(id+"F5.opExtrude","SWEPT_FACE",FACE,{"disambiguationData":[OSD([subQ2])]})])],"derivedFrom":makeQuery(id+"F5.opExtrude","CAP_EDGE",EDGE,{"disambiguationData":[OSD([subQ2])],"isStart":true})});}
            var Q11;
            {var subQ0=sQuery(id+"F0.wireOp",EDGE,"E0.top");var subQ1=sQuery(id+"F0.wireOp",EDGE,"E0.bottom");var subQ2=sQuery(id+"F4.wireOp",EDGE,"6ee83ff3-586e-4dbe-aaea-af71240543bd");Q11=makeQuery(id+"F5.boolean.opBoolean","SPLIT",EDGE,{"disambiguationData":[TD([makeQuery(id+"F1.opExtrude","CAP_FACE",FACE,{"disambiguationData":[OSD([subQ1,subQ0,sQuery(id+"F0.wireOp",EDGE,"E0.left"),sQuery(id+"F0.wireOp",EDGE,"E0.right")])],"isStart":false}),makeQuery(id+"F1.opExtrude","SWEPT_FACE",FACE,{"disambiguationData":[OSD([subQ0])]}),makeQuery(id+"F5.opExtrude","CAP_FACE",FACE,{"disambiguationData":[OSD([subQ1,sQuery(id+"F2.wireOp",EDGE,"E2.sketch_text.stroke-0"),sQuery(id+"F2.wireOp",EDGE,"E2.sketch_text.stroke-1"),sQuery(id+"F2.wireOp",EDGE,"E2.sketch_text.stroke-2"),sQuery(id+"F2.wireOp",EDGE,"E2.sketch_text.stroke-3"),sQuery(id+"F2.wireOp",EDGE,"E2.sketch_text.stroke-4"),sQuery(id+"F2.wireOp",EDGE,"E2.sketch_text.stroke-5"),sQuery(id+"F2.wireOp",EDGE,"E2.sketch_text.stroke-6"),sQuery(id+"F2.wireOp",EDGE,"E2.sketch_text.stroke-7"),sQuery(id+"F2.wireOp",EDGE,"E2.sketch_text.stroke-8"),sQuery(id+"F2.wireOp",EDGE,"E2.sketch_text.stroke-9"),sQuery(id+"F2.wireOp",EDGE,"E2.sketch_text.stroke-10"),sQuery(id+"F2.wireOp",EDGE,"E2.sketch_text.stroke-11"),sQuery(id+"F2.wireOp",EDGE,"E2.sketch_text.stroke-12"),sQuery(id+"F2.wireOp",EDGE,"E2.sketch_text.stroke-13"),sQuery(id+"F2.wireOp",EDGE,"E2.sketch_text.stroke-14"),sQuery(id+"F2.wireOp",EDGE,"E2.sketch_text.stroke-15"),sQuery(id+"F2.wireOp",EDGE,"E2.sketch_text.stroke-16"),sQuery(id+"F2.wireOp",EDGE,"E2.sketch_text.stroke-17"),sQuery(id+"F2.wireOp",EDGE,"E2.sketch_text.stroke-18"),sQuery(id+"F2.wireOp",EDGE,"E2.sketch_text.stroke-19"),sQuery(id+"F2.wireOp",EDGE,"E2.sketch_text.stroke-20"),sQuery(id+"F2.wireOp",EDGE,"E2.sketch_text.stroke-21"),sQuery(id+"F2.wireOp",EDGE,"E2.sketch_text.stroke-22"),sQuery(id+"F2.wireOp",EDGE,"E2.sketch_text.stroke-23"),sQuery(id+"F2.wireOp",EDGE,"E2.sketch_text.stroke-24"),sQuery(id+"F2.wireOp",EDGE,"E2.sketch_text.stroke-25"),sQuery(id+"F2.wireOp",EDGE,"E2.sketch_text.stroke-26"),sQuery(id+"F2.wireOp",EDGE,"E2.sketch_text.stroke-27"),sQuery(id+"F2.wireOp",EDGE,"E2.sketch_text.stroke-28"),sQuery(id+"F2.wireOp",EDGE,"E2.sketch_text.stroke-29"),sQuery(id+"F2.wireOp",EDGE,"E2.sketch_text.stroke-30"),sQuery(id+"F2.wireOp",EDGE,"E2.sketch_text.stroke-31"),sQuery(id+"F2.wireOp",EDGE,"E2.sketch_text.stroke-32"),sQuery(id+"F2.wireOp",EDGE,"E2.sketch_text.stroke-33"),sQuery(id+"F2.wireOp",EDGE,"E2.sketch_text.stroke-34"),sQuery(id+"F2.wireOp",EDGE,"E2.sketch_text.stroke-35"),sQuery(id+"F2.wireOp",EDGE,"E2.sketch_text.stroke-36"),sQuery(id+"F2.wireOp",EDGE,"E2.sketch_text.stroke-37"),sQuery(id+"F2.wireOp",EDGE,"E2.sketch_text.stroke-38"),sQuery(id+"F2.wireOp",EDGE,"E2.sketch_text.stroke-39"),sQuery(id+"F2.wireOp",EDGE,"E2.sketch_text.stroke-40"),sQuery(id+"F2.wireOp",EDGE,"E2.sketch_text.stroke-41"),sQuery(id+"F2.wireOp",EDGE,"E2.sketch_text.stroke-42"),sQuery(id+"F2.wireOp",EDGE,"E2.sketch_text.stroke-43"),sQuery(id+"F2.wireOp",EDGE,"E2.sketch_text.stroke-44"),sQuery(id+"F2.wireOp",EDGE,"E2.sketch_text.stroke-45"),sQuery(id+"F2.wireOp",EDGE,"E2.sketch_text.stroke-46"),sQuery(id+"F2.wireOp",EDGE,"E2.sketch_text.stroke-47"),sQuery(id+"F2.wireOp",EDGE,"E2.sketch_text.stroke-48"),sQuery(id+"F2.wireOp",EDGE,"E2.sketch_text.stroke-49"),sQuery(id+"F2.wireOp",EDGE,"E2.sketch_text.stroke-50"),sQuery(id+"F2.wireOp",EDGE,"E2.sketch_text.stroke-51"),sQuery(id+"F2.wireOp",EDGE,"E2.sketch_text.stroke-52"),sQuery(id+"F2.wireOp",EDGE,"E2.sketch_text.stroke-53"),sQuery(id+"F2.wireOp",EDGE,"E2.sketch_text.stroke-54"),sQuery(id+"F2.wireOp",EDGE,"E2.sketch_text.stroke-55"),sQuery(id+"F2.wireOp",EDGE,"E2.sketch_text.stroke-56"),sQuery(id+"F2.wireOp",EDGE,"E2.sketch_text.stroke-57"),sQuery(id+"F2.wireOp",EDGE,"E2.sketch_text.stroke-58"),sQuery(id+"F2.wireOp",EDGE,"E2.sketch_text.stroke-59"),sQuery(id+"F2.wireOp",EDGE,"E2.sketch_text.stroke-60"),sQuery(id+"F2.wireOp",EDGE,"E2.sketch_text.stroke-61"),sQuery(id+"F2.wireOp",EDGE,"E2.sketch_text.stroke-62"),sQuery(id+"F2.wireOp",EDGE,"E2.sketch_text.stroke-63"),sQuery(id+"F2.wireOp",EDGE,"E2.sketch_text.stroke-64"),sQuery(id+"F2.wireOp",EDGE,"E2.sketch_text.stroke-65"),sQuery(id+"F2.wireOp",EDGE,"E2.sketch_text.stroke-66"),sQuery(id+"F2.wireOp",EDGE,"E2.sketch_text.stroke-67"),sQuery(id+"F2.wireOp",EDGE,"E2.sketch_text.stroke-68"),sQuery(id+"F2.wireOp",EDGE,"E2.sketch_text.stroke-69"),sQuery(id+"F2.wireOp",EDGE,"E2.sketch_text.stroke-70"),sQuery(id+"F2.wireOp",EDGE,"E2.sketch_text.stroke-71"),sQuery(id+"F2.wireOp",EDGE,"E2.sketch_text.stroke-72"),sQuery(id+"F2.wireOp",EDGE,"E2.sketch_text.stroke-73"),sQuery(id+"F2.wireOp",EDGE,"E2.sketch_text.stroke-74"),sQuery(id+"F2.wireOp",EDGE,"E2.sketch_text.stroke-75"),sQuery(id+"F2.wireOp",EDGE,"E2.sketch_text.stroke-76"),sQuery(id+"F2.wireOp",EDGE,"E2.sketch_text.stroke-77"),sQuery(id+"F2.wireOp",EDGE,"E2.sketch_text.stroke-78"),sQuery(id+"F2.wireOp",EDGE,"E2.sketch_text.stroke-79"),sQuery(id+"F2.wireOp",EDGE,"E2.sketch_text.stroke-80"),sQuery(id+"F2.wireOp",EDGE,"E2.sketch_text.stroke-81"),sQuery(id+"F2.wireOp",EDGE,"E2.sketch_text.stroke-82"),sQuery(id+"F2.wireOp",EDGE,"E2.sketch_text.stroke-83"),sQuery(id+"F2.wireOp",EDGE,"E2.sketch_text.stroke-84"),sQuery(id+"F2.wireOp",EDGE,"E2.sketch_text.stroke-85"),sQuery(id+"F2.wireOp",EDGE,"E2.sketch_text.stroke-86"),sQuery(id+"F2.wireOp",EDGE,"E2.sketch_text.stroke-87"),sQuery(id+"F2.wireOp",EDGE,"E2.sketch_text.stroke-88"),sQuery(id+"F2.wireOp",EDGE,"E2.sketch_text.stroke-89"),sQuery(id+"F2.wireOp",EDGE,"E2.sketch_text.stroke-90"),sQuery(id+"F2.wireOp",EDGE,"E2.sketch_text.stroke-91"),sQuery(id+"F2.wireOp",EDGE,"E2.sketch_text.stroke-92"),sQuery(id+"F2.wireOp",EDGE,"E2.sketch_text.stroke-93"),sQuery(id+"F2.wireOp",EDGE,"E2.sketch_text.stroke-94"),sQuery(id+"F2.wireOp",EDGE,"E2.sketch_text.stroke-95"),sQuery(id+"F2.wireOp",EDGE,"E2.sketch_text.stroke-96"),sQuery(id+"F2.wireOp",EDGE,"E2.sketch_text.stroke-97"),sQuery(id+"F2.wireOp",EDGE,"E2.sketch_text.stroke-98"),sQuery(id+"F2.wireOp",EDGE,"E2.sketch_text.stroke-99"),sQuery(id+"F2.wireOp",EDGE,"E2.sketch_text.stroke-100"),sQuery(id+"F2.wireOp",EDGE,"E2.sketch_text.stroke-101"),sQuery(id+"F2.wireOp",EDGE,"E2.sketch_text.stroke-102"),sQuery(id+"F2.wireOp",EDGE,"E2.sketch_text.stroke-103"),sQuery(id+"F2.wireOp",EDGE,"E2.sketch_text.stroke-104"),sQuery(id+"F2.wireOp",EDGE,"E2.sketch_text.stroke-105"),sQuery(id+"F2.wireOp",EDGE,"E2.sketch_text.stroke-106"),sQuery(id+"F2.wireOp",EDGE,"E2.sketch_text.stroke-107"),sQuery(id+"F2.wireOp",EDGE,"E2.sketch_text.stroke-108"),sQuery(id+"F2.wireOp",EDGE,"E2.sketch_text.stroke-109"),sQuery(id+"F2.wireOp",EDGE,"E2.sketch_text.stroke-110"),sQuery(id+"F2.wireOp",EDGE,"E2.sketch_text.stroke-111"),sQuery(id+"F2.wireOp",EDGE,"E2.sketch_text.stroke-112"),sQuery(id+"F2.wireOp",EDGE,"E2.sketch_text.stroke-113"),sQuery(id+"F2.wireOp",EDGE,"E2.sketch_text.stroke-114"),sQuery(id+"F2.wireOp",EDGE,"E2.sketch_text.stroke-115"),sQuery(id+"F2.wireOp",EDGE,"E2.sketch_text.stroke-116"),sQuery(id+"F2.wireOp",EDGE,"E2.sketch_text.stroke-117"),sQuery(id+"F2.wireOp",EDGE,"E2.sketch_text.stroke-118"),sQuery(id+"F2.wireOp",EDGE,"E2.sketch_text.stroke-119"),sQuery(id+"F2.wireOp",EDGE,"E2.sketch_text.stroke-120"),sQuery(id+"F2.wireOp",EDGE,"E2.sketch_text.stroke-121"),sQuery(id+"F2.wireOp",EDGE,"E2.sketch_text.stroke-122"),sQuery(id+"F2.wireOp",EDGE,"E2.sketch_text.stroke-123"),sQuery(id+"F2.wireOp",EDGE,"E2.sketch_text.stroke-124"),sQuery(id+"F2.wireOp",EDGE,"E2.sketch_text.stroke-125"),sQuery(id+"F2.wireOp",EDGE,"E2.sketch_text.stroke-126"),sQuery(id+"F2.wireOp",EDGE,"E2.sketch_text.stroke-127"),sQuery(id+"F2.wireOp",EDGE,"E2.sketch_text.stroke-128"),sQuery(id+"F2.wireOp",EDGE,"E2.sketch_text.stroke-129"),sQuery(id+"F2.wireOp",EDGE,"E2.sketch_text.stroke-130"),sQuery(id+"F2.wireOp",EDGE,"E2.sketch_text.stroke-131"),sQuery(id+"F2.wireOp",EDGE,"E2.sketch_text.stroke-132"),sQuery(id+"F2.wireOp",EDGE,"E2.sketch_text.stroke-133"),sQuery(id+"F2.wireOp",EDGE,"E2.sketch_text.stroke-134"),sQuery(id+"F2.wireOp",EDGE,"E2.sketch_text.stroke-135"),sQuery(id+"F2.wireOp",EDGE,"E2.sketch_text.stroke-136"),sQuery(id+"F2.wireOp",EDGE,"E2.sketch_text.stroke-137"),sQuery(id+"F2.wireOp",EDGE,"E2.sketch_text.stroke-138"),sQuery(id+"F2.wireOp",EDGE,"E2.sketch_text.stroke-139"),sQuery(id+"F2.wireOp",EDGE,"E2.sketch_text.stroke-140"),sQuery(id+"F2.wireOp",EDGE,"E2.sketch_text.stroke-141"),sQuery(id+"F2.wireOp",EDGE,"E2.sketch_text.stroke-142"),sQuery(id+"F2.wireOp",EDGE,"E2.sketch_text.stroke-143"),sQuery(id+"F2.wireOp",EDGE,"E2.sketch_text.stroke-144"),sQuery(id+"F2.wireOp",EDGE,"E2.sketch_text.stroke-145"),sQuery(id+"F2.wireOp",EDGE,"E2.sketch_text.stroke-146"),sQuery(id+"F2.wireOp",EDGE,"E2.sketch_text.stroke-147"),sQuery(id+"F2.wireOp",EDGE,"E2.sketch_text.stroke-148"),sQuery(id+"F2.wireOp",EDGE,"E2.sketch_text.stroke-149"),sQuery(id+"F2.wireOp",EDGE,"E2.sketch_text.stroke-150"),sQuery(id+"F2.wireOp",EDGE,"E2.sketch_text.stroke-151"),sQuery(id+"F2.wireOp",EDGE,"E2.sketch_text.stroke-152"),sQuery(id+"F2.wireOp",EDGE,"E2.sketch_text.stroke-153"),sQuery(id+"F2.wireOp",EDGE,"E2.sketch_text.stroke-154"),sQuery(id+"F2.wireOp",EDGE,"E2.sketch_text.stroke-155"),sQuery(id+"F2.wireOp",EDGE,"E2.sketch_text.stroke-156"),sQuery(id+"F2.wireOp",EDGE,"E2.sketch_text.stroke-157"),sQuery(id+"F2.wireOp",EDGE,"E2.sketch_text.stroke-158"),sQuery(id+"F2.wireOp",EDGE,"E2.sketch_text.stroke-159"),sQuery(id+"F2.wireOp",EDGE,"E2.sketch_text.stroke-160"),sQuery(id+"F2.wireOp",EDGE,"E2.sketch_text.stroke-161"),sQuery(id+"F2.wireOp",EDGE,"E2.sketch_text.stroke-162"),sQuery(id+"F2.wireOp",EDGE,"E2.sketch_text.stroke-163"),sQuery(id+"F2.wireOp",EDGE,"E2.sketch_text.stroke-164"),sQuery(id+"F2.wireOp",EDGE,"E2.sketch_text.stroke-165"),sQuery(id+"F2.wireOp",EDGE,"E2.sketch_text.stroke-166"),sQuery(id+"F2.wireOp",EDGE,"E2.sketch_text.stroke-167"),sQuery(id+"F2.wireOp",EDGE,"E2.sketch_text.stroke-168"),sQuery(id+"F2.wireOp",EDGE,"E2.sketch_text.stroke-169"),sQuery(id+"F2.wireOp",EDGE,"E2.sketch_text.stroke-170"),sQuery(id+"F2.wireOp",EDGE,"E2.sketch_text.stroke-171"),sQuery(id+"F2.wireOp",EDGE,"E2.sketch_text.stroke-172"),sQuery(id+"F2.wireOp",EDGE,"E2.sketch_text.stroke-173"),sQuery(id+"F3.wireOp",EDGE,"E4.sketch_text.stroke-0"),sQuery(id+"F3.wireOp",EDGE,"E4.sketch_text.stroke-1"),sQuery(id+"F3.wireOp",EDGE,"E4.sketch_text.stroke-2"),sQuery(id+"F3.wireOp",EDGE,"E4.sketch_text.stroke-3"),sQuery(id+"F3.wireOp",EDGE,"E4.sketch_text.stroke-4"),sQuery(id+"F3.wireOp",EDGE,"E4.sketch_text.stroke-5"),sQuery(id+"F3.wireOp",EDGE,"E4.sketch_text.stroke-6"),sQuery(id+"F3.wireOp",EDGE,"E4.sketch_text.stroke-7"),sQuery(id+"F3.wireOp",EDGE,"E4.sketch_text.stroke-8"),sQuery(id+"F3.wireOp",EDGE,"E4.sketch_text.stroke-9"),sQuery(id+"F3.wireOp",EDGE,"E4.sketch_text.stroke-10"),sQuery(id+"F3.wireOp",EDGE,"E4.sketch_text.stroke-11"),sQuery(id+"F3.wireOp",EDGE,"E4.sketch_text.stroke-12"),sQuery(id+"F3.wireOp",EDGE,"E4.sketch_text.stroke-13"),sQuery(id+"F3.wireOp",EDGE,"E4.sketch_text.stroke-14"),sQuery(id+"F3.wireOp",EDGE,"E4.sketch_text.stroke-15"),sQuery(id+"F3.wireOp",EDGE,"E4.sketch_text.stroke-16"),sQuery(id+"F3.wireOp",EDGE,"E4.sketch_text.stroke-17"),sQuery(id+"F3.wireOp",EDGE,"E4.sketch_text.stroke-18"),sQuery(id+"F3.wireOp",EDGE,"E4.sketch_text.stroke-19"),sQuery(id+"F3.wireOp",EDGE,"E4.sketch_text.stroke-20"),sQuery(id+"F3.wireOp",EDGE,"E4.sketch_text.stroke-21"),sQuery(id+"F3.wireOp",EDGE,"E4.sketch_text.stroke-22"),sQuery(id+"F3.wireOp",EDGE,"E4.sketch_text.stroke-23"),sQuery(id+"F3.wireOp",EDGE,"E4.sketch_text.stroke-24"),sQuery(id+"F3.wireOp",EDGE,"E4.sketch_text.stroke-25"),sQuery(id+"F3.wireOp",EDGE,"E4.sketch_text.stroke-26"),sQuery(id+"F3.wireOp",EDGE,"E4.sketch_text.stroke-27"),sQuery(id+"F3.wireOp",EDGE,"E4.sketch_text.stroke-28"),sQuery(id+"F3.wireOp",EDGE,"E4.sketch_text.stroke-29"),sQuery(id+"F3.wireOp",EDGE,"E4.sketch_text.stroke-30"),sQuery(id+"F3.wireOp",EDGE,"E4.sketch_text.stroke-31"),sQuery(id+"F3.wireOp",EDGE,"E4.sketch_text.stroke-32"),sQuery(id+"F3.wireOp",EDGE,"E4.sketch_text.stroke-33"),sQuery(id+"F3.wireOp",EDGE,"E4.sketch_text.stroke-34"),sQuery(id+"F3.wireOp",EDGE,"E4.sketch_text.stroke-35"),sQuery(id+"F3.wireOp",EDGE,"E4.sketch_text.stroke-36"),sQuery(id+"F3.wireOp",EDGE,"E4.sketch_text.stroke-37"),sQuery(id+"F3.wireOp",EDGE,"E4.sketch_text.stroke-38"),sQuery(id+"F3.wireOp",EDGE,"E4.sketch_text.stroke-39"),sQuery(id+"F3.wireOp",EDGE,"E4.sketch_text.stroke-40"),sQuery(id+"F3.wireOp",EDGE,"E4.sketch_text.stroke-41"),sQuery(id+"F3.wireOp",EDGE,"E4.sketch_text.stroke-42"),sQuery(id+"F3.wireOp",EDGE,"E4.sketch_text.stroke-43"),sQuery(id+"F3.wireOp",EDGE,"E4.sketch_text.stroke-44"),sQuery(id+"F3.wireOp",EDGE,"E4.sketch_text.stroke-45"),sQuery(id+"F3.wireOp",EDGE,"E4.sketch_text.stroke-46"),sQuery(id+"F3.wireOp",EDGE,"E4.sketch_text.stroke-47"),sQuery(id+"F3.wireOp",EDGE,"E4.sketch_text.stroke-48"),sQuery(id+"F3.wireOp",EDGE,"E4.sketch_text.stroke-49"),sQuery(id+"F3.wireOp",EDGE,"E4.sketch_text.stroke-50"),sQuery(id+"F3.wireOp",EDGE,"E4.sketch_text.stroke-51"),sQuery(id+"F3.wireOp",EDGE,"E4.sketch_text.stroke-52"),sQuery(id+"F3.wireOp",EDGE,"E4.sketch_text.stroke-53"),sQuery(id+"F3.wireOp",EDGE,"E4.sketch_text.stroke-54"),sQuery(id+"F3.wireOp",EDGE,"E4.sketch_text.stroke-55"),sQuery(id+"F3.wireOp",EDGE,"E4.sketch_text.stroke-56"),sQuery(id+"F3.wireOp",EDGE,"E4.sketch_text.stroke-57"),sQuery(id+"F3.wireOp",EDGE,"E4.sketch_text.stroke-58"),sQuery(id+"F3.wireOp",EDGE,"E4.sketch_text.stroke-59"),sQuery(id+"F3.wireOp",EDGE,"E4.sketch_text.stroke-60"),sQuery(id+"F3.wireOp",EDGE,"E4.sketch_text.stroke-61"),sQuery(id+"F3.wireOp",EDGE,"E4.sketch_text.stroke-62"),sQuery(id+"F3.wireOp",EDGE,"E4.sketch_text.stroke-71"),sQuery(id+"F3.wireOp",EDGE,"E4.sketch_text.stroke-72"),sQuery(id+"F3.wireOp",EDGE,"E4.sketch_text.stroke-73"),sQuery(id+"F3.wireOp",EDGE,"E4.sketch_text.stroke-74"),sQuery(id+"F3.wireOp",EDGE,"E4.sketch_text.stroke-75"),sQuery(id+"F3.wireOp",EDGE,"E4.sketch_text.stroke-76"),sQuery(id+"F3.wireOp",EDGE,"E4.sketch_text.stroke-77"),sQuery(id+"F3.wireOp",EDGE,"E4.sketch_text.stroke-78"),sQuery(id+"F3.wireOp",EDGE,"E4.sketch_text.stroke-79"),sQuery(id+"F3.wireOp",EDGE,"E4.sketch_text.stroke-80"),sQuery(id+"F3.wireOp",EDGE,"E4.sketch_text.stroke-81"),sQuery(id+"F3.wireOp",EDGE,"E4.sketch_text.stroke-82"),sQuery(id+"F3.wireOp",EDGE,"E4.sketch_text.stroke-83"),sQuery(id+"F3.wireOp",EDGE,"E4.sketch_text.stroke-84"),sQuery(id+"F3.wireOp",EDGE,"E4.sketch_text.stroke-85"),sQuery(id+"F3.wireOp",EDGE,"E4.sketch_text.stroke-86"),sQuery(id+"F3.wireOp",EDGE,"E4.sketch_text.stroke-87"),sQuery(id+"F3.wireOp",EDGE,"E4.sketch_text.stroke-88"),sQuery(id+"F3.wireOp",EDGE,"E4.sketch_text.stroke-89"),sQuery(id+"F3.wireOp",EDGE,"E4.sketch_text.stroke-90"),sQuery(id+"F3.wireOp",EDGE,"E4.sketch_text.stroke-91"),sQuery(id+"F3.wireOp",EDGE,"E4.sketch_text.stroke-92"),sQuery(id+"F3.wireOp",EDGE,"E4.sketch_text.stroke-93"),sQuery(id+"F3.wireOp",EDGE,"E4.sketch_text.stroke-94"),sQuery(id+"F3.wireOp",EDGE,"E4.sketch_text.stroke-95"),sQuery(id+"F3.wireOp",EDGE,"E4.sketch_text.stroke-96"),sQuery(id+"F3.wireOp",EDGE,"E4.sketch_text.stroke-97"),sQuery(id+"F3.wireOp",EDGE,"E4.sketch_text.stroke-103"),sQuery(id+"F3.wireOp",EDGE,"E4.sketch_text.stroke-104"),sQuery(id+"F3.wireOp",EDGE,"E4.sketch_text.stroke-105"),sQuery(id+"F3.wireOp",EDGE,"E4.sketch_text.stroke-106"),sQuery(id+"F3.wireOp",EDGE,"E4.sketch_text.stroke-107"),sQuery(id+"F3.wireOp",EDGE,"E4.sketch_text.stroke-108"),sQuery(id+"F3.wireOp",EDGE,"E4.sketch_text.stroke-109"),sQuery(id+"F3.wireOp",EDGE,"E4.sketch_text.stroke-110"),sQuery(id+"F3.wireOp",EDGE,"E4.sketch_text.stroke-111"),sQuery(id+"F3.wireOp",EDGE,"E4.sketch_text.stroke-112"),sQuery(id+"F3.wireOp",EDGE,"E4.sketch_text.stroke-113"),sQuery(id+"F3.wireOp",EDGE,"E4.sketch_text.stroke-114"),sQuery(id+"F3.wireOp",EDGE,"E4.sketch_text.stroke-115"),sQuery(id+"F3.wireOp",EDGE,"E4.sketch_text.stroke-116"),sQuery(id+"F3.wireOp",EDGE,"E4.sketch_text.stroke-117"),sQuery(id+"F3.wireOp",EDGE,"E4.sketch_text.stroke-118"),sQuery(id+"F3.wireOp",EDGE,"E4.sketch_text.stroke-119"),sQuery(id+"F3.wireOp",EDGE,"E4.sketch_text.stroke-120"),sQuery(id+"F3.wireOp",EDGE,"E4.sketch_text.stroke-121"),sQuery(id+"F3.wireOp",EDGE,"E4.sketch_text.stroke-122"),sQuery(id+"F3.wireOp",EDGE,"E4.sketch_text.stroke-123"),sQuery(id+"F3.wireOp",EDGE,"E4.sketch_text.stroke-124"),sQuery(id+"F3.wireOp",EDGE,"E4.sketch_text.stroke-125"),sQuery(id+"F3.wireOp",EDGE,"E4.sketch_text.stroke-126"),sQuery(id+"F3.wireOp",EDGE,"E4.sketch_text.stroke-127"),sQuery(id+"F3.wireOp",EDGE,"E4.sketch_text.stroke-128"),sQuery(id+"F3.wireOp",EDGE,"E4.sketch_text.stroke-129"),sQuery(id+"F3.wireOp",EDGE,"E4.sketch_text.stroke-130"),sQuery(id+"F3.wireOp",EDGE,"E4.sketch_text.stroke-131"),sQuery(id+"F3.wireOp",EDGE,"E4.sketch_text.stroke-132"),sQuery(id+"F3.wireOp",EDGE,"E4.sketch_text.stroke-133"),sQuery(id+"F3.wireOp",EDGE,"E4.sketch_text.stroke-134"),sQuery(id+"F3.wireOp",EDGE,"E4.sketch_text.stroke-135"),sQuery(id+"F3.wireOp",EDGE,"E4.sketch_text.stroke-136"),sQuery(id+"F3.wireOp",EDGE,"E4.sketch_text.stroke-137"),sQuery(id+"F3.wireOp",EDGE,"E4.sketch_text.stroke-138"),sQuery(id+"F3.wireOp",EDGE,"E4.sketch_text.stroke-139"),sQuery(id+"F3.wireOp",EDGE,"E4.sketch_text.stroke-140"),sQuery(id+"F3.wireOp",EDGE,"E4.sketch_text.stroke-141"),sQuery(id+"F3.wireOp",EDGE,"E4.sketch_text.stroke-142"),sQuery(id+"F3.wireOp",EDGE,"E4.sketch_text.stroke-143"),sQuery(id+"F3.wireOp",EDGE,"E4.sketch_text.stroke-144"),sQuery(id+"F3.wireOp",EDGE,"E4.sketch_text.stroke-145"),sQuery(id+"F3.wireOp",EDGE,"E4.sketch_text.stroke-146"),sQuery(id+"F3.wireOp",EDGE,"E4.sketch_text.stroke-147"),sQuery(id+"F3.wireOp",EDGE,"E4.sketch_text.stroke-148"),sQuery(id+"F3.wireOp",EDGE,"E4.sketch_text.stroke-149"),sQuery(id+"F3.wireOp",EDGE,"E4.sketch_text.stroke-150"),sQuery(id+"F3.wireOp",EDGE,"E4.sketch_text.stroke-151"),sQuery(id+"F3.wireOp",EDGE,"E4.sketch_text.stroke-152"),sQuery(id+"F3.wireOp",EDGE,"E4.sketch_text.stroke-153"),sQuery(id+"F3.wireOp",EDGE,"E4.sketch_text.stroke-159"),sQuery(id+"F3.wireOp",EDGE,"E4.sketch_text.stroke-160"),sQuery(id+"F3.wireOp",EDGE,"E4.sketch_text.stroke-161"),sQuery(id+"F3.wireOp",EDGE,"E4.sketch_text.stroke-162"),sQuery(id+"F3.wireOp",EDGE,"E4.sketch_text.stroke-163"),sQuery(id+"F3.wireOp",EDGE,"E4.sketch_text.stroke-164"),sQuery(id+"F3.wireOp",EDGE,"E4.sketch_text.stroke-165"),sQuery(id+"F3.wireOp",EDGE,"E4.sketch_text.stroke-166"),sQuery(id+"F3.wireOp",EDGE,"E4.sketch_text.stroke-167"),sQuery(id+"F3.wireOp",EDGE,"E4.sketch_text.stroke-168"),sQuery(id+"F3.wireOp",EDGE,"E4.sketch_text.stroke-169"),sQuery(id+"F3.wireOp",EDGE,"E4.sketch_text.stroke-170"),sQuery(id+"F3.wireOp",EDGE,"E4.sketch_text.stroke-171"),sQuery(id+"F3.wireOp",EDGE,"E4.sketch_text.stroke-172"),sQuery(id+"F3.wireOp",EDGE,"E4.sketch_text.stroke-173"),sQuery(id+"F3.wireOp",EDGE,"E4.sketch_text.stroke-174"),sQuery(id+"F3.wireOp",EDGE,"E4.sketch_text.stroke-175"),sQuery(id+"F3.wireOp",EDGE,"E4.sketch_text.stroke-176"),sQuery(id+"F3.wireOp",EDGE,"E4.sketch_text.stroke-177"),sQuery(id+"F3.wireOp",EDGE,"E4.sketch_text.stroke-178"),sQuery(id+"F3.wireOp",EDGE,"E4.sketch_text.stroke-179"),sQuery(id+"F3.wireOp",EDGE,"E4.sketch_text.stroke-180"),sQuery(id+"F4.wireOp",EDGE,"8007402e-1a4e-4a06-85a5-2af08e553504"),subQ2])],"isStart":true}),makeQuery(id+"F5.opExtrude","SWEPT_FACE",FACE,{"disambiguationData":[OSD([subQ2])]})]),OD(0.0)],"derivedFrom":makeQuery(id+"F1.opExtrude","CAP_EDGE",EDGE,{"disambiguationData":[OSD([subQ0])],"isStart":false})});}
            var Q12;
            {var subQ0=sQuery(id+"F0.wireOp",EDGE,"E0.top");var subQ1=sQuery(id+"F0.wireOp",EDGE,"E0.bottom");var subQ2=sQuery(id+"F4.wireOp",EDGE,"6ee83ff3-586e-4dbe-aaea-af71240543bd");Q12=makeQuery(id+"F5.boolean.opBoolean","SPLIT",EDGE,{"disambiguationData":[TD([makeQuery(id+"F1.opExtrude","CAP_FACE",FACE,{"disambiguationData":[OSD([subQ1,subQ0,sQuery(id+"F0.wireOp",EDGE,"E0.left"),sQuery(id+"F0.wireOp",EDGE,"E0.right")])],"isStart":false}),makeQuery(id+"F1.opExtrude","SWEPT_FACE",FACE,{"disambiguationData":[OSD([subQ0])]}),makeQuery(id+"F5.opExtrude","CAP_FACE",FACE,{"disambiguationData":[OSD([subQ1,sQuery(id+"F2.wireOp",EDGE,"E2.sketch_text.stroke-0"),sQuery(id+"F2.wireOp",EDGE,"E2.sketch_text.stroke-1"),sQuery(id+"F2.wireOp",EDGE,"E2.sketch_text.stroke-2"),sQuery(id+"F2.wireOp",EDGE,"E2.sketch_text.stroke-3"),sQuery(id+"F2.wireOp",EDGE,"E2.sketch_text.stroke-4"),sQuery(id+"F2.wireOp",EDGE,"E2.sketch_text.stroke-5"),sQuery(id+"F2.wireOp",EDGE,"E2.sketch_text.stroke-6"),sQuery(id+"F2.wireOp",EDGE,"E2.sketch_text.stroke-7"),sQuery(id+"F2.wireOp",EDGE,"E2.sketch_text.stroke-8"),sQuery(id+"F2.wireOp",EDGE,"E2.sketch_text.stroke-9"),sQuery(id+"F2.wireOp",EDGE,"E2.sketch_text.stroke-10"),sQuery(id+"F2.wireOp",EDGE,"E2.sketch_text.stroke-11"),sQuery(id+"F2.wireOp",EDGE,"E2.sketch_text.stroke-12"),sQuery(id+"F2.wireOp",EDGE,"E2.sketch_text.stroke-13"),sQuery(id+"F2.wireOp",EDGE,"E2.sketch_text.stroke-14"),sQuery(id+"F2.wireOp",EDGE,"E2.sketch_text.stroke-15"),sQuery(id+"F2.wireOp",EDGE,"E2.sketch_text.stroke-16"),sQuery(id+"F2.wireOp",EDGE,"E2.sketch_text.stroke-17"),sQuery(id+"F2.wireOp",EDGE,"E2.sketch_text.stroke-18"),sQuery(id+"F2.wireOp",EDGE,"E2.sketch_text.stroke-19"),sQuery(id+"F2.wireOp",EDGE,"E2.sketch_text.stroke-20"),sQuery(id+"F2.wireOp",EDGE,"E2.sketch_text.stroke-21"),sQuery(id+"F2.wireOp",EDGE,"E2.sketch_text.stroke-22"),sQuery(id+"F2.wireOp",EDGE,"E2.sketch_text.stroke-23"),sQuery(id+"F2.wireOp",EDGE,"E2.sketch_text.stroke-24"),sQuery(id+"F2.wireOp",EDGE,"E2.sketch_text.stroke-25"),sQuery(id+"F2.wireOp",EDGE,"E2.sketch_text.stroke-26"),sQuery(id+"F2.wireOp",EDGE,"E2.sketch_text.stroke-27"),sQuery(id+"F2.wireOp",EDGE,"E2.sketch_text.stroke-28"),sQuery(id+"F2.wireOp",EDGE,"E2.sketch_text.stroke-29"),sQuery(id+"F2.wireOp",EDGE,"E2.sketch_text.stroke-30"),sQuery(id+"F2.wireOp",EDGE,"E2.sketch_text.stroke-31"),sQuery(id+"F2.wireOp",EDGE,"E2.sketch_text.stroke-32"),sQuery(id+"F2.wireOp",EDGE,"E2.sketch_text.stroke-33"),sQuery(id+"F2.wireOp",EDGE,"E2.sketch_text.stroke-34"),sQuery(id+"F2.wireOp",EDGE,"E2.sketch_text.stroke-35"),sQuery(id+"F2.wireOp",EDGE,"E2.sketch_text.stroke-36"),sQuery(id+"F2.wireOp",EDGE,"E2.sketch_text.stroke-37"),sQuery(id+"F2.wireOp",EDGE,"E2.sketch_text.stroke-38"),sQuery(id+"F2.wireOp",EDGE,"E2.sketch_text.stroke-39"),sQuery(id+"F2.wireOp",EDGE,"E2.sketch_text.stroke-40"),sQuery(id+"F2.wireOp",EDGE,"E2.sketch_text.stroke-41"),sQuery(id+"F2.wireOp",EDGE,"E2.sketch_text.stroke-42"),sQuery(id+"F2.wireOp",EDGE,"E2.sketch_text.stroke-43"),sQuery(id+"F2.wireOp",EDGE,"E2.sketch_text.stroke-44"),sQuery(id+"F2.wireOp",EDGE,"E2.sketch_text.stroke-45"),sQuery(id+"F2.wireOp",EDGE,"E2.sketch_text.stroke-46"),sQuery(id+"F2.wireOp",EDGE,"E2.sketch_text.stroke-47"),sQuery(id+"F2.wireOp",EDGE,"E2.sketch_text.stroke-48"),sQuery(id+"F2.wireOp",EDGE,"E2.sketch_text.stroke-49"),sQuery(id+"F2.wireOp",EDGE,"E2.sketch_text.stroke-50"),sQuery(id+"F2.wireOp",EDGE,"E2.sketch_text.stroke-51"),sQuery(id+"F2.wireOp",EDGE,"E2.sketch_text.stroke-52"),sQuery(id+"F2.wireOp",EDGE,"E2.sketch_text.stroke-53"),sQuery(id+"F2.wireOp",EDGE,"E2.sketch_text.stroke-54"),sQuery(id+"F2.wireOp",EDGE,"E2.sketch_text.stroke-55"),sQuery(id+"F2.wireOp",EDGE,"E2.sketch_text.stroke-56"),sQuery(id+"F2.wireOp",EDGE,"E2.sketch_text.stroke-57"),sQuery(id+"F2.wireOp",EDGE,"E2.sketch_text.stroke-58"),sQuery(id+"F2.wireOp",EDGE,"E2.sketch_text.stroke-59"),sQuery(id+"F2.wireOp",EDGE,"E2.sketch_text.stroke-60"),sQuery(id+"F2.wireOp",EDGE,"E2.sketch_text.stroke-61"),sQuery(id+"F2.wireOp",EDGE,"E2.sketch_text.stroke-62"),sQuery(id+"F2.wireOp",EDGE,"E2.sketch_text.stroke-63"),sQuery(id+"F2.wireOp",EDGE,"E2.sketch_text.stroke-64"),sQuery(id+"F2.wireOp",EDGE,"E2.sketch_text.stroke-65"),sQuery(id+"F2.wireOp",EDGE,"E2.sketch_text.stroke-66"),sQuery(id+"F2.wireOp",EDGE,"E2.sketch_text.stroke-67"),sQuery(id+"F2.wireOp",EDGE,"E2.sketch_text.stroke-68"),sQuery(id+"F2.wireOp",EDGE,"E2.sketch_text.stroke-69"),sQuery(id+"F2.wireOp",EDGE,"E2.sketch_text.stroke-70"),sQuery(id+"F2.wireOp",EDGE,"E2.sketch_text.stroke-71"),sQuery(id+"F2.wireOp",EDGE,"E2.sketch_text.stroke-72"),sQuery(id+"F2.wireOp",EDGE,"E2.sketch_text.stroke-73"),sQuery(id+"F2.wireOp",EDGE,"E2.sketch_text.stroke-74"),sQuery(id+"F2.wireOp",EDGE,"E2.sketch_text.stroke-75"),sQuery(id+"F2.wireOp",EDGE,"E2.sketch_text.stroke-76"),sQuery(id+"F2.wireOp",EDGE,"E2.sketch_text.stroke-77"),sQuery(id+"F2.wireOp",EDGE,"E2.sketch_text.stroke-78"),sQuery(id+"F2.wireOp",EDGE,"E2.sketch_text.stroke-79"),sQuery(id+"F2.wireOp",EDGE,"E2.sketch_text.stroke-80"),sQuery(id+"F2.wireOp",EDGE,"E2.sketch_text.stroke-81"),sQuery(id+"F2.wireOp",EDGE,"E2.sketch_text.stroke-82"),sQuery(id+"F2.wireOp",EDGE,"E2.sketch_text.stroke-83"),sQuery(id+"F2.wireOp",EDGE,"E2.sketch_text.stroke-84"),sQuery(id+"F2.wireOp",EDGE,"E2.sketch_text.stroke-85"),sQuery(id+"F2.wireOp",EDGE,"E2.sketch_text.stroke-86"),sQuery(id+"F2.wireOp",EDGE,"E2.sketch_text.stroke-87"),sQuery(id+"F2.wireOp",EDGE,"E2.sketch_text.stroke-88"),sQuery(id+"F2.wireOp",EDGE,"E2.sketch_text.stroke-89"),sQuery(id+"F2.wireOp",EDGE,"E2.sketch_text.stroke-90"),sQuery(id+"F2.wireOp",EDGE,"E2.sketch_text.stroke-91"),sQuery(id+"F2.wireOp",EDGE,"E2.sketch_text.stroke-92"),sQuery(id+"F2.wireOp",EDGE,"E2.sketch_text.stroke-93"),sQuery(id+"F2.wireOp",EDGE,"E2.sketch_text.stroke-94"),sQuery(id+"F2.wireOp",EDGE,"E2.sketch_text.stroke-95"),sQuery(id+"F2.wireOp",EDGE,"E2.sketch_text.stroke-96"),sQuery(id+"F2.wireOp",EDGE,"E2.sketch_text.stroke-97"),sQuery(id+"F2.wireOp",EDGE,"E2.sketch_text.stroke-98"),sQuery(id+"F2.wireOp",EDGE,"E2.sketch_text.stroke-99"),sQuery(id+"F2.wireOp",EDGE,"E2.sketch_text.stroke-100"),sQuery(id+"F2.wireOp",EDGE,"E2.sketch_text.stroke-101"),sQuery(id+"F2.wireOp",EDGE,"E2.sketch_text.stroke-102"),sQuery(id+"F2.wireOp",EDGE,"E2.sketch_text.stroke-103"),sQuery(id+"F2.wireOp",EDGE,"E2.sketch_text.stroke-104"),sQuery(id+"F2.wireOp",EDGE,"E2.sketch_text.stroke-105"),sQuery(id+"F2.wireOp",EDGE,"E2.sketch_text.stroke-106"),sQuery(id+"F2.wireOp",EDGE,"E2.sketch_text.stroke-107"),sQuery(id+"F2.wireOp",EDGE,"E2.sketch_text.stroke-108"),sQuery(id+"F2.wireOp",EDGE,"E2.sketch_text.stroke-109"),sQuery(id+"F2.wireOp",EDGE,"E2.sketch_text.stroke-110"),sQuery(id+"F2.wireOp",EDGE,"E2.sketch_text.stroke-111"),sQuery(id+"F2.wireOp",EDGE,"E2.sketch_text.stroke-112"),sQuery(id+"F2.wireOp",EDGE,"E2.sketch_text.stroke-113"),sQuery(id+"F2.wireOp",EDGE,"E2.sketch_text.stroke-114"),sQuery(id+"F2.wireOp",EDGE,"E2.sketch_text.stroke-115"),sQuery(id+"F2.wireOp",EDGE,"E2.sketch_text.stroke-116"),sQuery(id+"F2.wireOp",EDGE,"E2.sketch_text.stroke-117"),sQuery(id+"F2.wireOp",EDGE,"E2.sketch_text.stroke-118"),sQuery(id+"F2.wireOp",EDGE,"E2.sketch_text.stroke-119"),sQuery(id+"F2.wireOp",EDGE,"E2.sketch_text.stroke-120"),sQuery(id+"F2.wireOp",EDGE,"E2.sketch_text.stroke-121"),sQuery(id+"F2.wireOp",EDGE,"E2.sketch_text.stroke-122"),sQuery(id+"F2.wireOp",EDGE,"E2.sketch_text.stroke-123"),sQuery(id+"F2.wireOp",EDGE,"E2.sketch_text.stroke-124"),sQuery(id+"F2.wireOp",EDGE,"E2.sketch_text.stroke-125"),sQuery(id+"F2.wireOp",EDGE,"E2.sketch_text.stroke-126"),sQuery(id+"F2.wireOp",EDGE,"E2.sketch_text.stroke-127"),sQuery(id+"F2.wireOp",EDGE,"E2.sketch_text.stroke-128"),sQuery(id+"F2.wireOp",EDGE,"E2.sketch_text.stroke-129"),sQuery(id+"F2.wireOp",EDGE,"E2.sketch_text.stroke-130"),sQuery(id+"F2.wireOp",EDGE,"E2.sketch_text.stroke-131"),sQuery(id+"F2.wireOp",EDGE,"E2.sketch_text.stroke-132"),sQuery(id+"F2.wireOp",EDGE,"E2.sketch_text.stroke-133"),sQuery(id+"F2.wireOp",EDGE,"E2.sketch_text.stroke-134"),sQuery(id+"F2.wireOp",EDGE,"E2.sketch_text.stroke-135"),sQuery(id+"F2.wireOp",EDGE,"E2.sketch_text.stroke-136"),sQuery(id+"F2.wireOp",EDGE,"E2.sketch_text.stroke-137"),sQuery(id+"F2.wireOp",EDGE,"E2.sketch_text.stroke-138"),sQuery(id+"F2.wireOp",EDGE,"E2.sketch_text.stroke-139"),sQuery(id+"F2.wireOp",EDGE,"E2.sketch_text.stroke-140"),sQuery(id+"F2.wireOp",EDGE,"E2.sketch_text.stroke-141"),sQuery(id+"F2.wireOp",EDGE,"E2.sketch_text.stroke-142"),sQuery(id+"F2.wireOp",EDGE,"E2.sketch_text.stroke-143"),sQuery(id+"F2.wireOp",EDGE,"E2.sketch_text.stroke-144"),sQuery(id+"F2.wireOp",EDGE,"E2.sketch_text.stroke-145"),sQuery(id+"F2.wireOp",EDGE,"E2.sketch_text.stroke-146"),sQuery(id+"F2.wireOp",EDGE,"E2.sketch_text.stroke-147"),sQuery(id+"F2.wireOp",EDGE,"E2.sketch_text.stroke-148"),sQuery(id+"F2.wireOp",EDGE,"E2.sketch_text.stroke-149"),sQuery(id+"F2.wireOp",EDGE,"E2.sketch_text.stroke-150"),sQuery(id+"F2.wireOp",EDGE,"E2.sketch_text.stroke-151"),sQuery(id+"F2.wireOp",EDGE,"E2.sketch_text.stroke-152"),sQuery(id+"F2.wireOp",EDGE,"E2.sketch_text.stroke-153"),sQuery(id+"F2.wireOp",EDGE,"E2.sketch_text.stroke-154"),sQuery(id+"F2.wireOp",EDGE,"E2.sketch_text.stroke-155"),sQuery(id+"F2.wireOp",EDGE,"E2.sketch_text.stroke-156"),sQuery(id+"F2.wireOp",EDGE,"E2.sketch_text.stroke-157"),sQuery(id+"F2.wireOp",EDGE,"E2.sketch_text.stroke-158"),sQuery(id+"F2.wireOp",EDGE,"E2.sketch_text.stroke-159"),sQuery(id+"F2.wireOp",EDGE,"E2.sketch_text.stroke-160"),sQuery(id+"F2.wireOp",EDGE,"E2.sketch_text.stroke-161"),sQuery(id+"F2.wireOp",EDGE,"E2.sketch_text.stroke-162"),sQuery(id+"F2.wireOp",EDGE,"E2.sketch_text.stroke-163"),sQuery(id+"F2.wireOp",EDGE,"E2.sketch_text.stroke-164"),sQuery(id+"F2.wireOp",EDGE,"E2.sketch_text.stroke-165"),sQuery(id+"F2.wireOp",EDGE,"E2.sketch_text.stroke-166"),sQuery(id+"F2.wireOp",EDGE,"E2.sketch_text.stroke-167"),sQuery(id+"F2.wireOp",EDGE,"E2.sketch_text.stroke-168"),sQuery(id+"F2.wireOp",EDGE,"E2.sketch_text.stroke-169"),sQuery(id+"F2.wireOp",EDGE,"E2.sketch_text.stroke-170"),sQuery(id+"F2.wireOp",EDGE,"E2.sketch_text.stroke-171"),sQuery(id+"F2.wireOp",EDGE,"E2.sketch_text.stroke-172"),sQuery(id+"F2.wireOp",EDGE,"E2.sketch_text.stroke-173"),sQuery(id+"F3.wireOp",EDGE,"E4.sketch_text.stroke-0"),sQuery(id+"F3.wireOp",EDGE,"E4.sketch_text.stroke-1"),sQuery(id+"F3.wireOp",EDGE,"E4.sketch_text.stroke-2"),sQuery(id+"F3.wireOp",EDGE,"E4.sketch_text.stroke-3"),sQuery(id+"F3.wireOp",EDGE,"E4.sketch_text.stroke-4"),sQuery(id+"F3.wireOp",EDGE,"E4.sketch_text.stroke-5"),sQuery(id+"F3.wireOp",EDGE,"E4.sketch_text.stroke-6"),sQuery(id+"F3.wireOp",EDGE,"E4.sketch_text.stroke-7"),sQuery(id+"F3.wireOp",EDGE,"E4.sketch_text.stroke-8"),sQuery(id+"F3.wireOp",EDGE,"E4.sketch_text.stroke-9"),sQuery(id+"F3.wireOp",EDGE,"E4.sketch_text.stroke-10"),sQuery(id+"F3.wireOp",EDGE,"E4.sketch_text.stroke-11"),sQuery(id+"F3.wireOp",EDGE,"E4.sketch_text.stroke-12"),sQuery(id+"F3.wireOp",EDGE,"E4.sketch_text.stroke-13"),sQuery(id+"F3.wireOp",EDGE,"E4.sketch_text.stroke-14"),sQuery(id+"F3.wireOp",EDGE,"E4.sketch_text.stroke-15"),sQuery(id+"F3.wireOp",EDGE,"E4.sketch_text.stroke-16"),sQuery(id+"F3.wireOp",EDGE,"E4.sketch_text.stroke-17"),sQuery(id+"F3.wireOp",EDGE,"E4.sketch_text.stroke-18"),sQuery(id+"F3.wireOp",EDGE,"E4.sketch_text.stroke-19"),sQuery(id+"F3.wireOp",EDGE,"E4.sketch_text.stroke-20"),sQuery(id+"F3.wireOp",EDGE,"E4.sketch_text.stroke-21"),sQuery(id+"F3.wireOp",EDGE,"E4.sketch_text.stroke-22"),sQuery(id+"F3.wireOp",EDGE,"E4.sketch_text.stroke-23"),sQuery(id+"F3.wireOp",EDGE,"E4.sketch_text.stroke-24"),sQuery(id+"F3.wireOp",EDGE,"E4.sketch_text.stroke-25"),sQuery(id+"F3.wireOp",EDGE,"E4.sketch_text.stroke-26"),sQuery(id+"F3.wireOp",EDGE,"E4.sketch_text.stroke-27"),sQuery(id+"F3.wireOp",EDGE,"E4.sketch_text.stroke-28"),sQuery(id+"F3.wireOp",EDGE,"E4.sketch_text.stroke-29"),sQuery(id+"F3.wireOp",EDGE,"E4.sketch_text.stroke-30"),sQuery(id+"F3.wireOp",EDGE,"E4.sketch_text.stroke-31"),sQuery(id+"F3.wireOp",EDGE,"E4.sketch_text.stroke-32"),sQuery(id+"F3.wireOp",EDGE,"E4.sketch_text.stroke-33"),sQuery(id+"F3.wireOp",EDGE,"E4.sketch_text.stroke-34"),sQuery(id+"F3.wireOp",EDGE,"E4.sketch_text.stroke-35"),sQuery(id+"F3.wireOp",EDGE,"E4.sketch_text.stroke-36"),sQuery(id+"F3.wireOp",EDGE,"E4.sketch_text.stroke-37"),sQuery(id+"F3.wireOp",EDGE,"E4.sketch_text.stroke-38"),sQuery(id+"F3.wireOp",EDGE,"E4.sketch_text.stroke-39"),sQuery(id+"F3.wireOp",EDGE,"E4.sketch_text.stroke-40"),sQuery(id+"F3.wireOp",EDGE,"E4.sketch_text.stroke-41"),sQuery(id+"F3.wireOp",EDGE,"E4.sketch_text.stroke-42"),sQuery(id+"F3.wireOp",EDGE,"E4.sketch_text.stroke-43"),sQuery(id+"F3.wireOp",EDGE,"E4.sketch_text.stroke-44"),sQuery(id+"F3.wireOp",EDGE,"E4.sketch_text.stroke-45"),sQuery(id+"F3.wireOp",EDGE,"E4.sketch_text.stroke-46"),sQuery(id+"F3.wireOp",EDGE,"E4.sketch_text.stroke-47"),sQuery(id+"F3.wireOp",EDGE,"E4.sketch_text.stroke-48"),sQuery(id+"F3.wireOp",EDGE,"E4.sketch_text.stroke-49"),sQuery(id+"F3.wireOp",EDGE,"E4.sketch_text.stroke-50"),sQuery(id+"F3.wireOp",EDGE,"E4.sketch_text.stroke-51"),sQuery(id+"F3.wireOp",EDGE,"E4.sketch_text.stroke-52"),sQuery(id+"F3.wireOp",EDGE,"E4.sketch_text.stroke-53"),sQuery(id+"F3.wireOp",EDGE,"E4.sketch_text.stroke-54"),sQuery(id+"F3.wireOp",EDGE,"E4.sketch_text.stroke-55"),sQuery(id+"F3.wireOp",EDGE,"E4.sketch_text.stroke-56"),sQuery(id+"F3.wireOp",EDGE,"E4.sketch_text.stroke-57"),sQuery(id+"F3.wireOp",EDGE,"E4.sketch_text.stroke-58"),sQuery(id+"F3.wireOp",EDGE,"E4.sketch_text.stroke-59"),sQuery(id+"F3.wireOp",EDGE,"E4.sketch_text.stroke-60"),sQuery(id+"F3.wireOp",EDGE,"E4.sketch_text.stroke-61"),sQuery(id+"F3.wireOp",EDGE,"E4.sketch_text.stroke-62"),sQuery(id+"F3.wireOp",EDGE,"E4.sketch_text.stroke-71"),sQuery(id+"F3.wireOp",EDGE,"E4.sketch_text.stroke-72"),sQuery(id+"F3.wireOp",EDGE,"E4.sketch_text.stroke-73"),sQuery(id+"F3.wireOp",EDGE,"E4.sketch_text.stroke-74"),sQuery(id+"F3.wireOp",EDGE,"E4.sketch_text.stroke-75"),sQuery(id+"F3.wireOp",EDGE,"E4.sketch_text.stroke-76"),sQuery(id+"F3.wireOp",EDGE,"E4.sketch_text.stroke-77"),sQuery(id+"F3.wireOp",EDGE,"E4.sketch_text.stroke-78"),sQuery(id+"F3.wireOp",EDGE,"E4.sketch_text.stroke-79"),sQuery(id+"F3.wireOp",EDGE,"E4.sketch_text.stroke-80"),sQuery(id+"F3.wireOp",EDGE,"E4.sketch_text.stroke-81"),sQuery(id+"F3.wireOp",EDGE,"E4.sketch_text.stroke-82"),sQuery(id+"F3.wireOp",EDGE,"E4.sketch_text.stroke-83"),sQuery(id+"F3.wireOp",EDGE,"E4.sketch_text.stroke-84"),sQuery(id+"F3.wireOp",EDGE,"E4.sketch_text.stroke-85"),sQuery(id+"F3.wireOp",EDGE,"E4.sketch_text.stroke-86"),sQuery(id+"F3.wireOp",EDGE,"E4.sketch_text.stroke-87"),sQuery(id+"F3.wireOp",EDGE,"E4.sketch_text.stroke-88"),sQuery(id+"F3.wireOp",EDGE,"E4.sketch_text.stroke-89"),sQuery(id+"F3.wireOp",EDGE,"E4.sketch_text.stroke-90"),sQuery(id+"F3.wireOp",EDGE,"E4.sketch_text.stroke-91"),sQuery(id+"F3.wireOp",EDGE,"E4.sketch_text.stroke-92"),sQuery(id+"F3.wireOp",EDGE,"E4.sketch_text.stroke-93"),sQuery(id+"F3.wireOp",EDGE,"E4.sketch_text.stroke-94"),sQuery(id+"F3.wireOp",EDGE,"E4.sketch_text.stroke-95"),sQuery(id+"F3.wireOp",EDGE,"E4.sketch_text.stroke-96"),sQuery(id+"F3.wireOp",EDGE,"E4.sketch_text.stroke-97"),sQuery(id+"F3.wireOp",EDGE,"E4.sketch_text.stroke-103"),sQuery(id+"F3.wireOp",EDGE,"E4.sketch_text.stroke-104"),sQuery(id+"F3.wireOp",EDGE,"E4.sketch_text.stroke-105"),sQuery(id+"F3.wireOp",EDGE,"E4.sketch_text.stroke-106"),sQuery(id+"F3.wireOp",EDGE,"E4.sketch_text.stroke-107"),sQuery(id+"F3.wireOp",EDGE,"E4.sketch_text.stroke-108"),sQuery(id+"F3.wireOp",EDGE,"E4.sketch_text.stroke-109"),sQuery(id+"F3.wireOp",EDGE,"E4.sketch_text.stroke-110"),sQuery(id+"F3.wireOp",EDGE,"E4.sketch_text.stroke-111"),sQuery(id+"F3.wireOp",EDGE,"E4.sketch_text.stroke-112"),sQuery(id+"F3.wireOp",EDGE,"E4.sketch_text.stroke-113"),sQuery(id+"F3.wireOp",EDGE,"E4.sketch_text.stroke-114"),sQuery(id+"F3.wireOp",EDGE,"E4.sketch_text.stroke-115"),sQuery(id+"F3.wireOp",EDGE,"E4.sketch_text.stroke-116"),sQuery(id+"F3.wireOp",EDGE,"E4.sketch_text.stroke-117"),sQuery(id+"F3.wireOp",EDGE,"E4.sketch_text.stroke-118"),sQuery(id+"F3.wireOp",EDGE,"E4.sketch_text.stroke-119"),sQuery(id+"F3.wireOp",EDGE,"E4.sketch_text.stroke-120"),sQuery(id+"F3.wireOp",EDGE,"E4.sketch_text.stroke-121"),sQuery(id+"F3.wireOp",EDGE,"E4.sketch_text.stroke-122"),sQuery(id+"F3.wireOp",EDGE,"E4.sketch_text.stroke-123"),sQuery(id+"F3.wireOp",EDGE,"E4.sketch_text.stroke-124"),sQuery(id+"F3.wireOp",EDGE,"E4.sketch_text.stroke-125"),sQuery(id+"F3.wireOp",EDGE,"E4.sketch_text.stroke-126"),sQuery(id+"F3.wireOp",EDGE,"E4.sketch_text.stroke-127"),sQuery(id+"F3.wireOp",EDGE,"E4.sketch_text.stroke-128"),sQuery(id+"F3.wireOp",EDGE,"E4.sketch_text.stroke-129"),sQuery(id+"F3.wireOp",EDGE,"E4.sketch_text.stroke-130"),sQuery(id+"F3.wireOp",EDGE,"E4.sketch_text.stroke-131"),sQuery(id+"F3.wireOp",EDGE,"E4.sketch_text.stroke-132"),sQuery(id+"F3.wireOp",EDGE,"E4.sketch_text.stroke-133"),sQuery(id+"F3.wireOp",EDGE,"E4.sketch_text.stroke-134"),sQuery(id+"F3.wireOp",EDGE,"E4.sketch_text.stroke-135"),sQuery(id+"F3.wireOp",EDGE,"E4.sketch_text.stroke-136"),sQuery(id+"F3.wireOp",EDGE,"E4.sketch_text.stroke-137"),sQuery(id+"F3.wireOp",EDGE,"E4.sketch_text.stroke-138"),sQuery(id+"F3.wireOp",EDGE,"E4.sketch_text.stroke-139"),sQuery(id+"F3.wireOp",EDGE,"E4.sketch_text.stroke-140"),sQuery(id+"F3.wireOp",EDGE,"E4.sketch_text.stroke-141"),sQuery(id+"F3.wireOp",EDGE,"E4.sketch_text.stroke-142"),sQuery(id+"F3.wireOp",EDGE,"E4.sketch_text.stroke-143"),sQuery(id+"F3.wireOp",EDGE,"E4.sketch_text.stroke-144"),sQuery(id+"F3.wireOp",EDGE,"E4.sketch_text.stroke-145"),sQuery(id+"F3.wireOp",EDGE,"E4.sketch_text.stroke-146"),sQuery(id+"F3.wireOp",EDGE,"E4.sketch_text.stroke-147"),sQuery(id+"F3.wireOp",EDGE,"E4.sketch_text.stroke-148"),sQuery(id+"F3.wireOp",EDGE,"E4.sketch_text.stroke-149"),sQuery(id+"F3.wireOp",EDGE,"E4.sketch_text.stroke-150"),sQuery(id+"F3.wireOp",EDGE,"E4.sketch_text.stroke-151"),sQuery(id+"F3.wireOp",EDGE,"E4.sketch_text.stroke-152"),sQuery(id+"F3.wireOp",EDGE,"E4.sketch_text.stroke-153"),sQuery(id+"F3.wireOp",EDGE,"E4.sketch_text.stroke-159"),sQuery(id+"F3.wireOp",EDGE,"E4.sketch_text.stroke-160"),sQuery(id+"F3.wireOp",EDGE,"E4.sketch_text.stroke-161"),sQuery(id+"F3.wireOp",EDGE,"E4.sketch_text.stroke-162"),sQuery(id+"F3.wireOp",EDGE,"E4.sketch_text.stroke-163"),sQuery(id+"F3.wireOp",EDGE,"E4.sketch_text.stroke-164"),sQuery(id+"F3.wireOp",EDGE,"E4.sketch_text.stroke-165"),sQuery(id+"F3.wireOp",EDGE,"E4.sketch_text.stroke-166"),sQuery(id+"F3.wireOp",EDGE,"E4.sketch_text.stroke-167"),sQuery(id+"F3.wireOp",EDGE,"E4.sketch_text.stroke-168"),sQuery(id+"F3.wireOp",EDGE,"E4.sketch_text.stroke-169"),sQuery(id+"F3.wireOp",EDGE,"E4.sketch_text.stroke-170"),sQuery(id+"F3.wireOp",EDGE,"E4.sketch_text.stroke-171"),sQuery(id+"F3.wireOp",EDGE,"E4.sketch_text.stroke-172"),sQuery(id+"F3.wireOp",EDGE,"E4.sketch_text.stroke-173"),sQuery(id+"F3.wireOp",EDGE,"E4.sketch_text.stroke-174"),sQuery(id+"F3.wireOp",EDGE,"E4.sketch_text.stroke-175"),sQuery(id+"F3.wireOp",EDGE,"E4.sketch_text.stroke-176"),sQuery(id+"F3.wireOp",EDGE,"E4.sketch_text.stroke-177"),sQuery(id+"F3.wireOp",EDGE,"E4.sketch_text.stroke-178"),sQuery(id+"F3.wireOp",EDGE,"E4.sketch_text.stroke-179"),sQuery(id+"F3.wireOp",EDGE,"E4.sketch_text.stroke-180"),sQuery(id+"F4.wireOp",EDGE,"8007402e-1a4e-4a06-85a5-2af08e553504"),subQ2])],"isStart":true}),makeQuery(id+"F5.opExtrude","SWEPT_FACE",FACE,{"disambiguationData":[OSD([subQ2])]})]),OD(1.0)],"derivedFrom":makeQuery(id+"F1.opExtrude","CAP_EDGE",EDGE,{"disambiguationData":[OSD([subQ0])],"isStart":false})});}
            var Q13;
            {var subQ0=sQuery(id+"F0.wireOp",EDGE,"E0.top");var subQ1=sQuery(id+"F0.wireOp",EDGE,"E0.bottom");var subQ2=sQuery(id+"F4.wireOp",EDGE,"727ac2c1-f511-4829-95a7-a443ef16a4cd");Q13=makeQuery(id+"F5.boolean.opBoolean","SPLIT",EDGE,{"disambiguationData":[TD([makeQuery(id+"F1.opExtrude","CAP_FACE",FACE,{"disambiguationData":[OSD([subQ1,subQ0,sQuery(id+"F0.wireOp",EDGE,"E0.left"),sQuery(id+"F0.wireOp",EDGE,"E0.right")])],"isStart":false}),makeQuery(id+"F1.opExtrude","SWEPT_FACE",FACE,{"disambiguationData":[OSD([subQ0])]}),makeQuery(id+"F5.opExtrude","CAP_FACE",FACE,{"disambiguationData":[OSD([subQ1,sQuery(id+"F2.wireOp",EDGE,"E2.sketch_text.stroke-0"),sQuery(id+"F2.wireOp",EDGE,"E2.sketch_text.stroke-1"),sQuery(id+"F2.wireOp",EDGE,"E2.sketch_text.stroke-2"),sQuery(id+"F2.wireOp",EDGE,"E2.sketch_text.stroke-3"),sQuery(id+"F2.wireOp",EDGE,"E2.sketch_text.stroke-4"),sQuery(id+"F2.wireOp",EDGE,"E2.sketch_text.stroke-5"),sQuery(id+"F2.wireOp",EDGE,"E2.sketch_text.stroke-6"),sQuery(id+"F2.wireOp",EDGE,"E2.sketch_text.stroke-7"),sQuery(id+"F2.wireOp",EDGE,"E2.sketch_text.stroke-8"),sQuery(id+"F2.wireOp",EDGE,"E2.sketch_text.stroke-9"),sQuery(id+"F2.wireOp",EDGE,"E2.sketch_text.stroke-10"),sQuery(id+"F2.wireOp",EDGE,"E2.sketch_text.stroke-11"),sQuery(id+"F2.wireOp",EDGE,"E2.sketch_text.stroke-12"),sQuery(id+"F2.wireOp",EDGE,"E2.sketch_text.stroke-13"),sQuery(id+"F2.wireOp",EDGE,"E2.sketch_text.stroke-14"),sQuery(id+"F2.wireOp",EDGE,"E2.sketch_text.stroke-15"),sQuery(id+"F2.wireOp",EDGE,"E2.sketch_text.stroke-16"),sQuery(id+"F2.wireOp",EDGE,"E2.sketch_text.stroke-17"),sQuery(id+"F2.wireOp",EDGE,"E2.sketch_text.stroke-18"),sQuery(id+"F2.wireOp",EDGE,"E2.sketch_text.stroke-19"),sQuery(id+"F2.wireOp",EDGE,"E2.sketch_text.stroke-20"),sQuery(id+"F2.wireOp",EDGE,"E2.sketch_text.stroke-21"),sQuery(id+"F2.wireOp",EDGE,"E2.sketch_text.stroke-22"),sQuery(id+"F2.wireOp",EDGE,"E2.sketch_text.stroke-23"),sQuery(id+"F2.wireOp",EDGE,"E2.sketch_text.stroke-24"),sQuery(id+"F2.wireOp",EDGE,"E2.sketch_text.stroke-25"),sQuery(id+"F2.wireOp",EDGE,"E2.sketch_text.stroke-26"),sQuery(id+"F2.wireOp",EDGE,"E2.sketch_text.stroke-27"),sQuery(id+"F2.wireOp",EDGE,"E2.sketch_text.stroke-28"),sQuery(id+"F2.wireOp",EDGE,"E2.sketch_text.stroke-29"),sQuery(id+"F2.wireOp",EDGE,"E2.sketch_text.stroke-30"),sQuery(id+"F2.wireOp",EDGE,"E2.sketch_text.stroke-31"),sQuery(id+"F2.wireOp",EDGE,"E2.sketch_text.stroke-32"),sQuery(id+"F2.wireOp",EDGE,"E2.sketch_text.stroke-33"),sQuery(id+"F2.wireOp",EDGE,"E2.sketch_text.stroke-34"),sQuery(id+"F2.wireOp",EDGE,"E2.sketch_text.stroke-35"),sQuery(id+"F2.wireOp",EDGE,"E2.sketch_text.stroke-36"),sQuery(id+"F2.wireOp",EDGE,"E2.sketch_text.stroke-37"),sQuery(id+"F2.wireOp",EDGE,"E2.sketch_text.stroke-38"),sQuery(id+"F2.wireOp",EDGE,"E2.sketch_text.stroke-39"),sQuery(id+"F2.wireOp",EDGE,"E2.sketch_text.stroke-40"),sQuery(id+"F2.wireOp",EDGE,"E2.sketch_text.stroke-41"),sQuery(id+"F2.wireOp",EDGE,"E2.sketch_text.stroke-42"),sQuery(id+"F2.wireOp",EDGE,"E2.sketch_text.stroke-43"),sQuery(id+"F2.wireOp",EDGE,"E2.sketch_text.stroke-44"),sQuery(id+"F2.wireOp",EDGE,"E2.sketch_text.stroke-45"),sQuery(id+"F2.wireOp",EDGE,"E2.sketch_text.stroke-46"),sQuery(id+"F2.wireOp",EDGE,"E2.sketch_text.stroke-47"),sQuery(id+"F2.wireOp",EDGE,"E2.sketch_text.stroke-48"),sQuery(id+"F2.wireOp",EDGE,"E2.sketch_text.stroke-49"),sQuery(id+"F2.wireOp",EDGE,"E2.sketch_text.stroke-50"),sQuery(id+"F2.wireOp",EDGE,"E2.sketch_text.stroke-51"),sQuery(id+"F2.wireOp",EDGE,"E2.sketch_text.stroke-52"),sQuery(id+"F2.wireOp",EDGE,"E2.sketch_text.stroke-53"),sQuery(id+"F2.wireOp",EDGE,"E2.sketch_text.stroke-54"),sQuery(id+"F2.wireOp",EDGE,"E2.sketch_text.stroke-55"),sQuery(id+"F2.wireOp",EDGE,"E2.sketch_text.stroke-56"),sQuery(id+"F2.wireOp",EDGE,"E2.sketch_text.stroke-57"),sQuery(id+"F2.wireOp",EDGE,"E2.sketch_text.stroke-58"),sQuery(id+"F2.wireOp",EDGE,"E2.sketch_text.stroke-59"),sQuery(id+"F2.wireOp",EDGE,"E2.sketch_text.stroke-60"),sQuery(id+"F2.wireOp",EDGE,"E2.sketch_text.stroke-61"),sQuery(id+"F2.wireOp",EDGE,"E2.sketch_text.stroke-62"),sQuery(id+"F2.wireOp",EDGE,"E2.sketch_text.stroke-63"),sQuery(id+"F2.wireOp",EDGE,"E2.sketch_text.stroke-64"),sQuery(id+"F2.wireOp",EDGE,"E2.sketch_text.stroke-65"),sQuery(id+"F2.wireOp",EDGE,"E2.sketch_text.stroke-66"),sQuery(id+"F2.wireOp",EDGE,"E2.sketch_text.stroke-67"),sQuery(id+"F2.wireOp",EDGE,"E2.sketch_text.stroke-68"),sQuery(id+"F2.wireOp",EDGE,"E2.sketch_text.stroke-69"),sQuery(id+"F2.wireOp",EDGE,"E2.sketch_text.stroke-70"),sQuery(id+"F2.wireOp",EDGE,"E2.sketch_text.stroke-71"),sQuery(id+"F2.wireOp",EDGE,"E2.sketch_text.stroke-72"),sQuery(id+"F2.wireOp",EDGE,"E2.sketch_text.stroke-73"),sQuery(id+"F2.wireOp",EDGE,"E2.sketch_text.stroke-74"),sQuery(id+"F2.wireOp",EDGE,"E2.sketch_text.stroke-75"),sQuery(id+"F2.wireOp",EDGE,"E2.sketch_text.stroke-76"),sQuery(id+"F2.wireOp",EDGE,"E2.sketch_text.stroke-77"),sQuery(id+"F2.wireOp",EDGE,"E2.sketch_text.stroke-78"),sQuery(id+"F2.wireOp",EDGE,"E2.sketch_text.stroke-79"),sQuery(id+"F2.wireOp",EDGE,"E2.sketch_text.stroke-80"),sQuery(id+"F2.wireOp",EDGE,"E2.sketch_text.stroke-81"),sQuery(id+"F2.wireOp",EDGE,"E2.sketch_text.stroke-82"),sQuery(id+"F2.wireOp",EDGE,"E2.sketch_text.stroke-83"),sQuery(id+"F2.wireOp",EDGE,"E2.sketch_text.stroke-84"),sQuery(id+"F2.wireOp",EDGE,"E2.sketch_text.stroke-85"),sQuery(id+"F2.wireOp",EDGE,"E2.sketch_text.stroke-86"),sQuery(id+"F2.wireOp",EDGE,"E2.sketch_text.stroke-87"),sQuery(id+"F2.wireOp",EDGE,"E2.sketch_text.stroke-88"),sQuery(id+"F2.wireOp",EDGE,"E2.sketch_text.stroke-89"),sQuery(id+"F2.wireOp",EDGE,"E2.sketch_text.stroke-90"),sQuery(id+"F2.wireOp",EDGE,"E2.sketch_text.stroke-91"),sQuery(id+"F2.wireOp",EDGE,"E2.sketch_text.stroke-92"),sQuery(id+"F2.wireOp",EDGE,"E2.sketch_text.stroke-93"),sQuery(id+"F2.wireOp",EDGE,"E2.sketch_text.stroke-94"),sQuery(id+"F2.wireOp",EDGE,"E2.sketch_text.stroke-95"),sQuery(id+"F2.wireOp",EDGE,"E2.sketch_text.stroke-96"),sQuery(id+"F2.wireOp",EDGE,"E2.sketch_text.stroke-97"),sQuery(id+"F2.wireOp",EDGE,"E2.sketch_text.stroke-98"),sQuery(id+"F2.wireOp",EDGE,"E2.sketch_text.stroke-99"),sQuery(id+"F2.wireOp",EDGE,"E2.sketch_text.stroke-100"),sQuery(id+"F2.wireOp",EDGE,"E2.sketch_text.stroke-101"),sQuery(id+"F2.wireOp",EDGE,"E2.sketch_text.stroke-102"),sQuery(id+"F2.wireOp",EDGE,"E2.sketch_text.stroke-103"),sQuery(id+"F2.wireOp",EDGE,"E2.sketch_text.stroke-104"),sQuery(id+"F2.wireOp",EDGE,"E2.sketch_text.stroke-105"),sQuery(id+"F2.wireOp",EDGE,"E2.sketch_text.stroke-106"),sQuery(id+"F2.wireOp",EDGE,"E2.sketch_text.stroke-107"),sQuery(id+"F2.wireOp",EDGE,"E2.sketch_text.stroke-108"),sQuery(id+"F2.wireOp",EDGE,"E2.sketch_text.stroke-109"),sQuery(id+"F2.wireOp",EDGE,"E2.sketch_text.stroke-110"),sQuery(id+"F2.wireOp",EDGE,"E2.sketch_text.stroke-111"),sQuery(id+"F2.wireOp",EDGE,"E2.sketch_text.stroke-112"),sQuery(id+"F2.wireOp",EDGE,"E2.sketch_text.stroke-113"),sQuery(id+"F2.wireOp",EDGE,"E2.sketch_text.stroke-114"),sQuery(id+"F2.wireOp",EDGE,"E2.sketch_text.stroke-115"),sQuery(id+"F2.wireOp",EDGE,"E2.sketch_text.stroke-116"),sQuery(id+"F2.wireOp",EDGE,"E2.sketch_text.stroke-117"),sQuery(id+"F2.wireOp",EDGE,"E2.sketch_text.stroke-118"),sQuery(id+"F2.wireOp",EDGE,"E2.sketch_text.stroke-119"),sQuery(id+"F2.wireOp",EDGE,"E2.sketch_text.stroke-120"),sQuery(id+"F2.wireOp",EDGE,"E2.sketch_text.stroke-121"),sQuery(id+"F2.wireOp",EDGE,"E2.sketch_text.stroke-122"),sQuery(id+"F2.wireOp",EDGE,"E2.sketch_text.stroke-123"),sQuery(id+"F2.wireOp",EDGE,"E2.sketch_text.stroke-124"),sQuery(id+"F2.wireOp",EDGE,"E2.sketch_text.stroke-125"),sQuery(id+"F2.wireOp",EDGE,"E2.sketch_text.stroke-126"),sQuery(id+"F2.wireOp",EDGE,"E2.sketch_text.stroke-127"),sQuery(id+"F2.wireOp",EDGE,"E2.sketch_text.stroke-128"),sQuery(id+"F2.wireOp",EDGE,"E2.sketch_text.stroke-129"),sQuery(id+"F2.wireOp",EDGE,"E2.sketch_text.stroke-130"),sQuery(id+"F2.wireOp",EDGE,"E2.sketch_text.stroke-131"),sQuery(id+"F2.wireOp",EDGE,"E2.sketch_text.stroke-132"),sQuery(id+"F2.wireOp",EDGE,"E2.sketch_text.stroke-133"),sQuery(id+"F2.wireOp",EDGE,"E2.sketch_text.stroke-134"),sQuery(id+"F2.wireOp",EDGE,"E2.sketch_text.stroke-135"),sQuery(id+"F2.wireOp",EDGE,"E2.sketch_text.stroke-136"),sQuery(id+"F2.wireOp",EDGE,"E2.sketch_text.stroke-137"),sQuery(id+"F2.wireOp",EDGE,"E2.sketch_text.stroke-138"),sQuery(id+"F2.wireOp",EDGE,"E2.sketch_text.stroke-139"),sQuery(id+"F2.wireOp",EDGE,"E2.sketch_text.stroke-140"),sQuery(id+"F2.wireOp",EDGE,"E2.sketch_text.stroke-141"),sQuery(id+"F2.wireOp",EDGE,"E2.sketch_text.stroke-142"),sQuery(id+"F2.wireOp",EDGE,"E2.sketch_text.stroke-143"),sQuery(id+"F2.wireOp",EDGE,"E2.sketch_text.stroke-144"),sQuery(id+"F2.wireOp",EDGE,"E2.sketch_text.stroke-145"),sQuery(id+"F2.wireOp",EDGE,"E2.sketch_text.stroke-146"),sQuery(id+"F2.wireOp",EDGE,"E2.sketch_text.stroke-147"),sQuery(id+"F2.wireOp",EDGE,"E2.sketch_text.stroke-148"),sQuery(id+"F2.wireOp",EDGE,"E2.sketch_text.stroke-149"),sQuery(id+"F2.wireOp",EDGE,"E2.sketch_text.stroke-150"),sQuery(id+"F2.wireOp",EDGE,"E2.sketch_text.stroke-151"),sQuery(id+"F2.wireOp",EDGE,"E2.sketch_text.stroke-152"),sQuery(id+"F2.wireOp",EDGE,"E2.sketch_text.stroke-153"),sQuery(id+"F2.wireOp",EDGE,"E2.sketch_text.stroke-154"),sQuery(id+"F2.wireOp",EDGE,"E2.sketch_text.stroke-155"),sQuery(id+"F2.wireOp",EDGE,"E2.sketch_text.stroke-156"),sQuery(id+"F2.wireOp",EDGE,"E2.sketch_text.stroke-157"),sQuery(id+"F2.wireOp",EDGE,"E2.sketch_text.stroke-158"),sQuery(id+"F2.wireOp",EDGE,"E2.sketch_text.stroke-159"),sQuery(id+"F2.wireOp",EDGE,"E2.sketch_text.stroke-160"),sQuery(id+"F2.wireOp",EDGE,"E2.sketch_text.stroke-161"),sQuery(id+"F2.wireOp",EDGE,"E2.sketch_text.stroke-162"),sQuery(id+"F2.wireOp",EDGE,"E2.sketch_text.stroke-163"),sQuery(id+"F2.wireOp",EDGE,"E2.sketch_text.stroke-164"),sQuery(id+"F2.wireOp",EDGE,"E2.sketch_text.stroke-165"),sQuery(id+"F2.wireOp",EDGE,"E2.sketch_text.stroke-166"),sQuery(id+"F2.wireOp",EDGE,"E2.sketch_text.stroke-167"),sQuery(id+"F2.wireOp",EDGE,"E2.sketch_text.stroke-168"),sQuery(id+"F2.wireOp",EDGE,"E2.sketch_text.stroke-169"),sQuery(id+"F2.wireOp",EDGE,"E2.sketch_text.stroke-170"),sQuery(id+"F2.wireOp",EDGE,"E2.sketch_text.stroke-171"),sQuery(id+"F2.wireOp",EDGE,"E2.sketch_text.stroke-172"),sQuery(id+"F2.wireOp",EDGE,"E2.sketch_text.stroke-173"),sQuery(id+"F3.wireOp",EDGE,"E4.sketch_text.stroke-0"),sQuery(id+"F3.wireOp",EDGE,"E4.sketch_text.stroke-1"),sQuery(id+"F3.wireOp",EDGE,"E4.sketch_text.stroke-2"),sQuery(id+"F3.wireOp",EDGE,"E4.sketch_text.stroke-3"),sQuery(id+"F3.wireOp",EDGE,"E4.sketch_text.stroke-4"),sQuery(id+"F3.wireOp",EDGE,"E4.sketch_text.stroke-5"),sQuery(id+"F3.wireOp",EDGE,"E4.sketch_text.stroke-6"),sQuery(id+"F3.wireOp",EDGE,"E4.sketch_text.stroke-7"),sQuery(id+"F3.wireOp",EDGE,"E4.sketch_text.stroke-8"),sQuery(id+"F3.wireOp",EDGE,"E4.sketch_text.stroke-9"),sQuery(id+"F3.wireOp",EDGE,"E4.sketch_text.stroke-10"),sQuery(id+"F3.wireOp",EDGE,"E4.sketch_text.stroke-11"),sQuery(id+"F3.wireOp",EDGE,"E4.sketch_text.stroke-12"),sQuery(id+"F3.wireOp",EDGE,"E4.sketch_text.stroke-13"),sQuery(id+"F3.wireOp",EDGE,"E4.sketch_text.stroke-14"),sQuery(id+"F3.wireOp",EDGE,"E4.sketch_text.stroke-15"),sQuery(id+"F3.wireOp",EDGE,"E4.sketch_text.stroke-16"),sQuery(id+"F3.wireOp",EDGE,"E4.sketch_text.stroke-17"),sQuery(id+"F3.wireOp",EDGE,"E4.sketch_text.stroke-18"),sQuery(id+"F3.wireOp",EDGE,"E4.sketch_text.stroke-19"),sQuery(id+"F3.wireOp",EDGE,"E4.sketch_text.stroke-20"),sQuery(id+"F3.wireOp",EDGE,"E4.sketch_text.stroke-21"),sQuery(id+"F3.wireOp",EDGE,"E4.sketch_text.stroke-22"),sQuery(id+"F3.wireOp",EDGE,"E4.sketch_text.stroke-23"),sQuery(id+"F3.wireOp",EDGE,"E4.sketch_text.stroke-24"),sQuery(id+"F3.wireOp",EDGE,"E4.sketch_text.stroke-25"),sQuery(id+"F3.wireOp",EDGE,"E4.sketch_text.stroke-26"),sQuery(id+"F3.wireOp",EDGE,"E4.sketch_text.stroke-27"),sQuery(id+"F3.wireOp",EDGE,"E4.sketch_text.stroke-28"),sQuery(id+"F3.wireOp",EDGE,"E4.sketch_text.stroke-29"),sQuery(id+"F3.wireOp",EDGE,"E4.sketch_text.stroke-30"),sQuery(id+"F3.wireOp",EDGE,"E4.sketch_text.stroke-31"),sQuery(id+"F3.wireOp",EDGE,"E4.sketch_text.stroke-32"),sQuery(id+"F3.wireOp",EDGE,"E4.sketch_text.stroke-33"),sQuery(id+"F3.wireOp",EDGE,"E4.sketch_text.stroke-34"),sQuery(id+"F3.wireOp",EDGE,"E4.sketch_text.stroke-35"),sQuery(id+"F3.wireOp",EDGE,"E4.sketch_text.stroke-36"),sQuery(id+"F3.wireOp",EDGE,"E4.sketch_text.stroke-37"),sQuery(id+"F3.wireOp",EDGE,"E4.sketch_text.stroke-38"),sQuery(id+"F3.wireOp",EDGE,"E4.sketch_text.stroke-39"),sQuery(id+"F3.wireOp",EDGE,"E4.sketch_text.stroke-40"),sQuery(id+"F3.wireOp",EDGE,"E4.sketch_text.stroke-41"),sQuery(id+"F3.wireOp",EDGE,"E4.sketch_text.stroke-42"),sQuery(id+"F3.wireOp",EDGE,"E4.sketch_text.stroke-43"),sQuery(id+"F3.wireOp",EDGE,"E4.sketch_text.stroke-44"),sQuery(id+"F3.wireOp",EDGE,"E4.sketch_text.stroke-45"),sQuery(id+"F3.wireOp",EDGE,"E4.sketch_text.stroke-46"),sQuery(id+"F3.wireOp",EDGE,"E4.sketch_text.stroke-47"),sQuery(id+"F3.wireOp",EDGE,"E4.sketch_text.stroke-48"),sQuery(id+"F3.wireOp",EDGE,"E4.sketch_text.stroke-49"),sQuery(id+"F3.wireOp",EDGE,"E4.sketch_text.stroke-50"),sQuery(id+"F3.wireOp",EDGE,"E4.sketch_text.stroke-51"),sQuery(id+"F3.wireOp",EDGE,"E4.sketch_text.stroke-52"),sQuery(id+"F3.wireOp",EDGE,"E4.sketch_text.stroke-53"),sQuery(id+"F3.wireOp",EDGE,"E4.sketch_text.stroke-54"),sQuery(id+"F3.wireOp",EDGE,"E4.sketch_text.stroke-55"),sQuery(id+"F3.wireOp",EDGE,"E4.sketch_text.stroke-56"),sQuery(id+"F3.wireOp",EDGE,"E4.sketch_text.stroke-57"),sQuery(id+"F3.wireOp",EDGE,"E4.sketch_text.stroke-58"),sQuery(id+"F3.wireOp",EDGE,"E4.sketch_text.stroke-59"),sQuery(id+"F3.wireOp",EDGE,"E4.sketch_text.stroke-60"),sQuery(id+"F3.wireOp",EDGE,"E4.sketch_text.stroke-61"),sQuery(id+"F3.wireOp",EDGE,"E4.sketch_text.stroke-62"),sQuery(id+"F3.wireOp",EDGE,"E4.sketch_text.stroke-71"),sQuery(id+"F3.wireOp",EDGE,"E4.sketch_text.stroke-72"),sQuery(id+"F3.wireOp",EDGE,"E4.sketch_text.stroke-73"),sQuery(id+"F3.wireOp",EDGE,"E4.sketch_text.stroke-74"),sQuery(id+"F3.wireOp",EDGE,"E4.sketch_text.stroke-75"),sQuery(id+"F3.wireOp",EDGE,"E4.sketch_text.stroke-76"),sQuery(id+"F3.wireOp",EDGE,"E4.sketch_text.stroke-77"),sQuery(id+"F3.wireOp",EDGE,"E4.sketch_text.stroke-78"),sQuery(id+"F3.wireOp",EDGE,"E4.sketch_text.stroke-79"),sQuery(id+"F3.wireOp",EDGE,"E4.sketch_text.stroke-80"),sQuery(id+"F3.wireOp",EDGE,"E4.sketch_text.stroke-81"),sQuery(id+"F3.wireOp",EDGE,"E4.sketch_text.stroke-82"),sQuery(id+"F3.wireOp",EDGE,"E4.sketch_text.stroke-83"),sQuery(id+"F3.wireOp",EDGE,"E4.sketch_text.stroke-84"),sQuery(id+"F3.wireOp",EDGE,"E4.sketch_text.stroke-85"),sQuery(id+"F3.wireOp",EDGE,"E4.sketch_text.stroke-86"),sQuery(id+"F3.wireOp",EDGE,"E4.sketch_text.stroke-87"),sQuery(id+"F3.wireOp",EDGE,"E4.sketch_text.stroke-88"),sQuery(id+"F3.wireOp",EDGE,"E4.sketch_text.stroke-89"),sQuery(id+"F3.wireOp",EDGE,"E4.sketch_text.stroke-90"),sQuery(id+"F3.wireOp",EDGE,"E4.sketch_text.stroke-91"),sQuery(id+"F3.wireOp",EDGE,"E4.sketch_text.stroke-92"),sQuery(id+"F3.wireOp",EDGE,"E4.sketch_text.stroke-93"),sQuery(id+"F3.wireOp",EDGE,"E4.sketch_text.stroke-94"),sQuery(id+"F3.wireOp",EDGE,"E4.sketch_text.stroke-95"),sQuery(id+"F3.wireOp",EDGE,"E4.sketch_text.stroke-96"),sQuery(id+"F3.wireOp",EDGE,"E4.sketch_text.stroke-97"),sQuery(id+"F3.wireOp",EDGE,"E4.sketch_text.stroke-103"),sQuery(id+"F3.wireOp",EDGE,"E4.sketch_text.stroke-104"),sQuery(id+"F3.wireOp",EDGE,"E4.sketch_text.stroke-105"),sQuery(id+"F3.wireOp",EDGE,"E4.sketch_text.stroke-106"),sQuery(id+"F3.wireOp",EDGE,"E4.sketch_text.stroke-107"),sQuery(id+"F3.wireOp",EDGE,"E4.sketch_text.stroke-108"),sQuery(id+"F3.wireOp",EDGE,"E4.sketch_text.stroke-109"),sQuery(id+"F3.wireOp",EDGE,"E4.sketch_text.stroke-110"),sQuery(id+"F3.wireOp",EDGE,"E4.sketch_text.stroke-111"),sQuery(id+"F3.wireOp",EDGE,"E4.sketch_text.stroke-112"),sQuery(id+"F3.wireOp",EDGE,"E4.sketch_text.stroke-113"),sQuery(id+"F3.wireOp",EDGE,"E4.sketch_text.stroke-114"),sQuery(id+"F3.wireOp",EDGE,"E4.sketch_text.stroke-115"),sQuery(id+"F3.wireOp",EDGE,"E4.sketch_text.stroke-116"),sQuery(id+"F3.wireOp",EDGE,"E4.sketch_text.stroke-117"),sQuery(id+"F3.wireOp",EDGE,"E4.sketch_text.stroke-118"),sQuery(id+"F3.wireOp",EDGE,"E4.sketch_text.stroke-119"),sQuery(id+"F3.wireOp",EDGE,"E4.sketch_text.stroke-120"),sQuery(id+"F3.wireOp",EDGE,"E4.sketch_text.stroke-121"),sQuery(id+"F3.wireOp",EDGE,"E4.sketch_text.stroke-122"),sQuery(id+"F3.wireOp",EDGE,"E4.sketch_text.stroke-123"),sQuery(id+"F3.wireOp",EDGE,"E4.sketch_text.stroke-124"),sQuery(id+"F3.wireOp",EDGE,"E4.sketch_text.stroke-125"),sQuery(id+"F3.wireOp",EDGE,"E4.sketch_text.stroke-126"),sQuery(id+"F3.wireOp",EDGE,"E4.sketch_text.stroke-127"),sQuery(id+"F3.wireOp",EDGE,"E4.sketch_text.stroke-128"),sQuery(id+"F3.wireOp",EDGE,"E4.sketch_text.stroke-129"),sQuery(id+"F3.wireOp",EDGE,"E4.sketch_text.stroke-130"),sQuery(id+"F3.wireOp",EDGE,"E4.sketch_text.stroke-131"),sQuery(id+"F3.wireOp",EDGE,"E4.sketch_text.stroke-132"),sQuery(id+"F3.wireOp",EDGE,"E4.sketch_text.stroke-133"),sQuery(id+"F3.wireOp",EDGE,"E4.sketch_text.stroke-134"),sQuery(id+"F3.wireOp",EDGE,"E4.sketch_text.stroke-135"),sQuery(id+"F3.wireOp",EDGE,"E4.sketch_text.stroke-136"),sQuery(id+"F3.wireOp",EDGE,"E4.sketch_text.stroke-137"),sQuery(id+"F3.wireOp",EDGE,"E4.sketch_text.stroke-138"),sQuery(id+"F3.wireOp",EDGE,"E4.sketch_text.stroke-139"),sQuery(id+"F3.wireOp",EDGE,"E4.sketch_text.stroke-140"),sQuery(id+"F3.wireOp",EDGE,"E4.sketch_text.stroke-141"),sQuery(id+"F3.wireOp",EDGE,"E4.sketch_text.stroke-142"),sQuery(id+"F3.wireOp",EDGE,"E4.sketch_text.stroke-143"),sQuery(id+"F3.wireOp",EDGE,"E4.sketch_text.stroke-144"),sQuery(id+"F3.wireOp",EDGE,"E4.sketch_text.stroke-145"),sQuery(id+"F3.wireOp",EDGE,"E4.sketch_text.stroke-146"),sQuery(id+"F3.wireOp",EDGE,"E4.sketch_text.stroke-147"),sQuery(id+"F3.wireOp",EDGE,"E4.sketch_text.stroke-148"),sQuery(id+"F3.wireOp",EDGE,"E4.sketch_text.stroke-149"),sQuery(id+"F3.wireOp",EDGE,"E4.sketch_text.stroke-150"),sQuery(id+"F3.wireOp",EDGE,"E4.sketch_text.stroke-151"),sQuery(id+"F3.wireOp",EDGE,"E4.sketch_text.stroke-152"),sQuery(id+"F3.wireOp",EDGE,"E4.sketch_text.stroke-153"),sQuery(id+"F3.wireOp",EDGE,"E4.sketch_text.stroke-159"),sQuery(id+"F3.wireOp",EDGE,"E4.sketch_text.stroke-160"),sQuery(id+"F3.wireOp",EDGE,"E4.sketch_text.stroke-161"),sQuery(id+"F3.wireOp",EDGE,"E4.sketch_text.stroke-162"),sQuery(id+"F3.wireOp",EDGE,"E4.sketch_text.stroke-163"),sQuery(id+"F3.wireOp",EDGE,"E4.sketch_text.stroke-164"),sQuery(id+"F3.wireOp",EDGE,"E4.sketch_text.stroke-165"),sQuery(id+"F3.wireOp",EDGE,"E4.sketch_text.stroke-166"),sQuery(id+"F3.wireOp",EDGE,"E4.sketch_text.stroke-167"),sQuery(id+"F3.wireOp",EDGE,"E4.sketch_text.stroke-168"),sQuery(id+"F3.wireOp",EDGE,"E4.sketch_text.stroke-169"),sQuery(id+"F3.wireOp",EDGE,"E4.sketch_text.stroke-170"),sQuery(id+"F3.wireOp",EDGE,"E4.sketch_text.stroke-171"),sQuery(id+"F3.wireOp",EDGE,"E4.sketch_text.stroke-172"),sQuery(id+"F3.wireOp",EDGE,"E4.sketch_text.stroke-173"),sQuery(id+"F3.wireOp",EDGE,"E4.sketch_text.stroke-174"),sQuery(id+"F3.wireOp",EDGE,"E4.sketch_text.stroke-175"),sQuery(id+"F3.wireOp",EDGE,"E4.sketch_text.stroke-176"),sQuery(id+"F3.wireOp",EDGE,"E4.sketch_text.stroke-177"),sQuery(id+"F3.wireOp",EDGE,"E4.sketch_text.stroke-178"),sQuery(id+"F3.wireOp",EDGE,"E4.sketch_text.stroke-179"),sQuery(id+"F3.wireOp",EDGE,"E4.sketch_text.stroke-180"),sQuery(id+"F4.wireOp",EDGE,"8007402e-1a4e-4a06-85a5-2af08e553504"),subQ2])],"isStart":true}),makeQuery(id+"F5.opExtrude","SWEPT_FACE",FACE,{"disambiguationData":[OSD([subQ2])]})])],"derivedFrom":makeQuery(id+"F5.opExtrude","CAP_EDGE",EDGE,{"disambiguationData":[OSD([subQ2])],"isStart":true})});}
            var Q14;
            {var subQ0=sQuery(id+"F0.wireOp",EDGE,"E0.top");var subQ1=sQuery(id+"F0.wireOp",EDGE,"E0.bottom");var subQ2=sQuery(id+"F4.wireOp",EDGE,"727ac2c1-f511-4829-95a7-a443ef16a4cd");Q14=makeQuery(id+"F5.boolean.opBoolean","SPLIT",EDGE,{"disambiguationData":[TD([makeQuery(id+"F1.opExtrude","CAP_FACE",FACE,{"disambiguationData":[OSD([subQ1,subQ0,sQuery(id+"F0.wireOp",EDGE,"E0.left"),sQuery(id+"F0.wireOp",EDGE,"E0.right")])],"isStart":false}),makeQuery(id+"F1.opExtrude","SWEPT_FACE",FACE,{"disambiguationData":[OSD([subQ0])]}),makeQuery(id+"F5.opExtrude","CAP_FACE",FACE,{"disambiguationData":[OSD([subQ1,sQuery(id+"F2.wireOp",EDGE,"E2.sketch_text.stroke-0"),sQuery(id+"F2.wireOp",EDGE,"E2.sketch_text.stroke-1"),sQuery(id+"F2.wireOp",EDGE,"E2.sketch_text.stroke-2"),sQuery(id+"F2.wireOp",EDGE,"E2.sketch_text.stroke-3"),sQuery(id+"F2.wireOp",EDGE,"E2.sketch_text.stroke-4"),sQuery(id+"F2.wireOp",EDGE,"E2.sketch_text.stroke-5"),sQuery(id+"F2.wireOp",EDGE,"E2.sketch_text.stroke-6"),sQuery(id+"F2.wireOp",EDGE,"E2.sketch_text.stroke-7"),sQuery(id+"F2.wireOp",EDGE,"E2.sketch_text.stroke-8"),sQuery(id+"F2.wireOp",EDGE,"E2.sketch_text.stroke-9"),sQuery(id+"F2.wireOp",EDGE,"E2.sketch_text.stroke-10"),sQuery(id+"F2.wireOp",EDGE,"E2.sketch_text.stroke-11"),sQuery(id+"F2.wireOp",EDGE,"E2.sketch_text.stroke-12"),sQuery(id+"F2.wireOp",EDGE,"E2.sketch_text.stroke-13"),sQuery(id+"F2.wireOp",EDGE,"E2.sketch_text.stroke-14"),sQuery(id+"F2.wireOp",EDGE,"E2.sketch_text.stroke-15"),sQuery(id+"F2.wireOp",EDGE,"E2.sketch_text.stroke-16"),sQuery(id+"F2.wireOp",EDGE,"E2.sketch_text.stroke-17"),sQuery(id+"F2.wireOp",EDGE,"E2.sketch_text.stroke-18"),sQuery(id+"F2.wireOp",EDGE,"E2.sketch_text.stroke-19"),sQuery(id+"F2.wireOp",EDGE,"E2.sketch_text.stroke-20"),sQuery(id+"F2.wireOp",EDGE,"E2.sketch_text.stroke-21"),sQuery(id+"F2.wireOp",EDGE,"E2.sketch_text.stroke-22"),sQuery(id+"F2.wireOp",EDGE,"E2.sketch_text.stroke-23"),sQuery(id+"F2.wireOp",EDGE,"E2.sketch_text.stroke-24"),sQuery(id+"F2.wireOp",EDGE,"E2.sketch_text.stroke-25"),sQuery(id+"F2.wireOp",EDGE,"E2.sketch_text.stroke-26"),sQuery(id+"F2.wireOp",EDGE,"E2.sketch_text.stroke-27"),sQuery(id+"F2.wireOp",EDGE,"E2.sketch_text.stroke-28"),sQuery(id+"F2.wireOp",EDGE,"E2.sketch_text.stroke-29"),sQuery(id+"F2.wireOp",EDGE,"E2.sketch_text.stroke-30"),sQuery(id+"F2.wireOp",EDGE,"E2.sketch_text.stroke-31"),sQuery(id+"F2.wireOp",EDGE,"E2.sketch_text.stroke-32"),sQuery(id+"F2.wireOp",EDGE,"E2.sketch_text.stroke-33"),sQuery(id+"F2.wireOp",EDGE,"E2.sketch_text.stroke-34"),sQuery(id+"F2.wireOp",EDGE,"E2.sketch_text.stroke-35"),sQuery(id+"F2.wireOp",EDGE,"E2.sketch_text.stroke-36"),sQuery(id+"F2.wireOp",EDGE,"E2.sketch_text.stroke-37"),sQuery(id+"F2.wireOp",EDGE,"E2.sketch_text.stroke-38"),sQuery(id+"F2.wireOp",EDGE,"E2.sketch_text.stroke-39"),sQuery(id+"F2.wireOp",EDGE,"E2.sketch_text.stroke-40"),sQuery(id+"F2.wireOp",EDGE,"E2.sketch_text.stroke-41"),sQuery(id+"F2.wireOp",EDGE,"E2.sketch_text.stroke-42"),sQuery(id+"F2.wireOp",EDGE,"E2.sketch_text.stroke-43"),sQuery(id+"F2.wireOp",EDGE,"E2.sketch_text.stroke-44"),sQuery(id+"F2.wireOp",EDGE,"E2.sketch_text.stroke-45"),sQuery(id+"F2.wireOp",EDGE,"E2.sketch_text.stroke-46"),sQuery(id+"F2.wireOp",EDGE,"E2.sketch_text.stroke-47"),sQuery(id+"F2.wireOp",EDGE,"E2.sketch_text.stroke-48"),sQuery(id+"F2.wireOp",EDGE,"E2.sketch_text.stroke-49"),sQuery(id+"F2.wireOp",EDGE,"E2.sketch_text.stroke-50"),sQuery(id+"F2.wireOp",EDGE,"E2.sketch_text.stroke-51"),sQuery(id+"F2.wireOp",EDGE,"E2.sketch_text.stroke-52"),sQuery(id+"F2.wireOp",EDGE,"E2.sketch_text.stroke-53"),sQuery(id+"F2.wireOp",EDGE,"E2.sketch_text.stroke-54"),sQuery(id+"F2.wireOp",EDGE,"E2.sketch_text.stroke-55"),sQuery(id+"F2.wireOp",EDGE,"E2.sketch_text.stroke-56"),sQuery(id+"F2.wireOp",EDGE,"E2.sketch_text.stroke-57"),sQuery(id+"F2.wireOp",EDGE,"E2.sketch_text.stroke-58"),sQuery(id+"F2.wireOp",EDGE,"E2.sketch_text.stroke-59"),sQuery(id+"F2.wireOp",EDGE,"E2.sketch_text.stroke-60"),sQuery(id+"F2.wireOp",EDGE,"E2.sketch_text.stroke-61"),sQuery(id+"F2.wireOp",EDGE,"E2.sketch_text.stroke-62"),sQuery(id+"F2.wireOp",EDGE,"E2.sketch_text.stroke-63"),sQuery(id+"F2.wireOp",EDGE,"E2.sketch_text.stroke-64"),sQuery(id+"F2.wireOp",EDGE,"E2.sketch_text.stroke-65"),sQuery(id+"F2.wireOp",EDGE,"E2.sketch_text.stroke-66"),sQuery(id+"F2.wireOp",EDGE,"E2.sketch_text.stroke-67"),sQuery(id+"F2.wireOp",EDGE,"E2.sketch_text.stroke-68"),sQuery(id+"F2.wireOp",EDGE,"E2.sketch_text.stroke-69"),sQuery(id+"F2.wireOp",EDGE,"E2.sketch_text.stroke-70"),sQuery(id+"F2.wireOp",EDGE,"E2.sketch_text.stroke-71"),sQuery(id+"F2.wireOp",EDGE,"E2.sketch_text.stroke-72"),sQuery(id+"F2.wireOp",EDGE,"E2.sketch_text.stroke-73"),sQuery(id+"F2.wireOp",EDGE,"E2.sketch_text.stroke-74"),sQuery(id+"F2.wireOp",EDGE,"E2.sketch_text.stroke-75"),sQuery(id+"F2.wireOp",EDGE,"E2.sketch_text.stroke-76"),sQuery(id+"F2.wireOp",EDGE,"E2.sketch_text.stroke-77"),sQuery(id+"F2.wireOp",EDGE,"E2.sketch_text.stroke-78"),sQuery(id+"F2.wireOp",EDGE,"E2.sketch_text.stroke-79"),sQuery(id+"F2.wireOp",EDGE,"E2.sketch_text.stroke-80"),sQuery(id+"F2.wireOp",EDGE,"E2.sketch_text.stroke-81"),sQuery(id+"F2.wireOp",EDGE,"E2.sketch_text.stroke-82"),sQuery(id+"F2.wireOp",EDGE,"E2.sketch_text.stroke-83"),sQuery(id+"F2.wireOp",EDGE,"E2.sketch_text.stroke-84"),sQuery(id+"F2.wireOp",EDGE,"E2.sketch_text.stroke-85"),sQuery(id+"F2.wireOp",EDGE,"E2.sketch_text.stroke-86"),sQuery(id+"F2.wireOp",EDGE,"E2.sketch_text.stroke-87"),sQuery(id+"F2.wireOp",EDGE,"E2.sketch_text.stroke-88"),sQuery(id+"F2.wireOp",EDGE,"E2.sketch_text.stroke-89"),sQuery(id+"F2.wireOp",EDGE,"E2.sketch_text.stroke-90"),sQuery(id+"F2.wireOp",EDGE,"E2.sketch_text.stroke-91"),sQuery(id+"F2.wireOp",EDGE,"E2.sketch_text.stroke-92"),sQuery(id+"F2.wireOp",EDGE,"E2.sketch_text.stroke-93"),sQuery(id+"F2.wireOp",EDGE,"E2.sketch_text.stroke-94"),sQuery(id+"F2.wireOp",EDGE,"E2.sketch_text.stroke-95"),sQuery(id+"F2.wireOp",EDGE,"E2.sketch_text.stroke-96"),sQuery(id+"F2.wireOp",EDGE,"E2.sketch_text.stroke-97"),sQuery(id+"F2.wireOp",EDGE,"E2.sketch_text.stroke-98"),sQuery(id+"F2.wireOp",EDGE,"E2.sketch_text.stroke-99"),sQuery(id+"F2.wireOp",EDGE,"E2.sketch_text.stroke-100"),sQuery(id+"F2.wireOp",EDGE,"E2.sketch_text.stroke-101"),sQuery(id+"F2.wireOp",EDGE,"E2.sketch_text.stroke-102"),sQuery(id+"F2.wireOp",EDGE,"E2.sketch_text.stroke-103"),sQuery(id+"F2.wireOp",EDGE,"E2.sketch_text.stroke-104"),sQuery(id+"F2.wireOp",EDGE,"E2.sketch_text.stroke-105"),sQuery(id+"F2.wireOp",EDGE,"E2.sketch_text.stroke-106"),sQuery(id+"F2.wireOp",EDGE,"E2.sketch_text.stroke-107"),sQuery(id+"F2.wireOp",EDGE,"E2.sketch_text.stroke-108"),sQuery(id+"F2.wireOp",EDGE,"E2.sketch_text.stroke-109"),sQuery(id+"F2.wireOp",EDGE,"E2.sketch_text.stroke-110"),sQuery(id+"F2.wireOp",EDGE,"E2.sketch_text.stroke-111"),sQuery(id+"F2.wireOp",EDGE,"E2.sketch_text.stroke-112"),sQuery(id+"F2.wireOp",EDGE,"E2.sketch_text.stroke-113"),sQuery(id+"F2.wireOp",EDGE,"E2.sketch_text.stroke-114"),sQuery(id+"F2.wireOp",EDGE,"E2.sketch_text.stroke-115"),sQuery(id+"F2.wireOp",EDGE,"E2.sketch_text.stroke-116"),sQuery(id+"F2.wireOp",EDGE,"E2.sketch_text.stroke-117"),sQuery(id+"F2.wireOp",EDGE,"E2.sketch_text.stroke-118"),sQuery(id+"F2.wireOp",EDGE,"E2.sketch_text.stroke-119"),sQuery(id+"F2.wireOp",EDGE,"E2.sketch_text.stroke-120"),sQuery(id+"F2.wireOp",EDGE,"E2.sketch_text.stroke-121"),sQuery(id+"F2.wireOp",EDGE,"E2.sketch_text.stroke-122"),sQuery(id+"F2.wireOp",EDGE,"E2.sketch_text.stroke-123"),sQuery(id+"F2.wireOp",EDGE,"E2.sketch_text.stroke-124"),sQuery(id+"F2.wireOp",EDGE,"E2.sketch_text.stroke-125"),sQuery(id+"F2.wireOp",EDGE,"E2.sketch_text.stroke-126"),sQuery(id+"F2.wireOp",EDGE,"E2.sketch_text.stroke-127"),sQuery(id+"F2.wireOp",EDGE,"E2.sketch_text.stroke-128"),sQuery(id+"F2.wireOp",EDGE,"E2.sketch_text.stroke-129"),sQuery(id+"F2.wireOp",EDGE,"E2.sketch_text.stroke-130"),sQuery(id+"F2.wireOp",EDGE,"E2.sketch_text.stroke-131"),sQuery(id+"F2.wireOp",EDGE,"E2.sketch_text.stroke-132"),sQuery(id+"F2.wireOp",EDGE,"E2.sketch_text.stroke-133"),sQuery(id+"F2.wireOp",EDGE,"E2.sketch_text.stroke-134"),sQuery(id+"F2.wireOp",EDGE,"E2.sketch_text.stroke-135"),sQuery(id+"F2.wireOp",EDGE,"E2.sketch_text.stroke-136"),sQuery(id+"F2.wireOp",EDGE,"E2.sketch_text.stroke-137"),sQuery(id+"F2.wireOp",EDGE,"E2.sketch_text.stroke-138"),sQuery(id+"F2.wireOp",EDGE,"E2.sketch_text.stroke-139"),sQuery(id+"F2.wireOp",EDGE,"E2.sketch_text.stroke-140"),sQuery(id+"F2.wireOp",EDGE,"E2.sketch_text.stroke-141"),sQuery(id+"F2.wireOp",EDGE,"E2.sketch_text.stroke-142"),sQuery(id+"F2.wireOp",EDGE,"E2.sketch_text.stroke-143"),sQuery(id+"F2.wireOp",EDGE,"E2.sketch_text.stroke-144"),sQuery(id+"F2.wireOp",EDGE,"E2.sketch_text.stroke-145"),sQuery(id+"F2.wireOp",EDGE,"E2.sketch_text.stroke-146"),sQuery(id+"F2.wireOp",EDGE,"E2.sketch_text.stroke-147"),sQuery(id+"F2.wireOp",EDGE,"E2.sketch_text.stroke-148"),sQuery(id+"F2.wireOp",EDGE,"E2.sketch_text.stroke-149"),sQuery(id+"F2.wireOp",EDGE,"E2.sketch_text.stroke-150"),sQuery(id+"F2.wireOp",EDGE,"E2.sketch_text.stroke-151"),sQuery(id+"F2.wireOp",EDGE,"E2.sketch_text.stroke-152"),sQuery(id+"F2.wireOp",EDGE,"E2.sketch_text.stroke-153"),sQuery(id+"F2.wireOp",EDGE,"E2.sketch_text.stroke-154"),sQuery(id+"F2.wireOp",EDGE,"E2.sketch_text.stroke-155"),sQuery(id+"F2.wireOp",EDGE,"E2.sketch_text.stroke-156"),sQuery(id+"F2.wireOp",EDGE,"E2.sketch_text.stroke-157"),sQuery(id+"F2.wireOp",EDGE,"E2.sketch_text.stroke-158"),sQuery(id+"F2.wireOp",EDGE,"E2.sketch_text.stroke-159"),sQuery(id+"F2.wireOp",EDGE,"E2.sketch_text.stroke-160"),sQuery(id+"F2.wireOp",EDGE,"E2.sketch_text.stroke-161"),sQuery(id+"F2.wireOp",EDGE,"E2.sketch_text.stroke-162"),sQuery(id+"F2.wireOp",EDGE,"E2.sketch_text.stroke-163"),sQuery(id+"F2.wireOp",EDGE,"E2.sketch_text.stroke-164"),sQuery(id+"F2.wireOp",EDGE,"E2.sketch_text.stroke-165"),sQuery(id+"F2.wireOp",EDGE,"E2.sketch_text.stroke-166"),sQuery(id+"F2.wireOp",EDGE,"E2.sketch_text.stroke-167"),sQuery(id+"F2.wireOp",EDGE,"E2.sketch_text.stroke-168"),sQuery(id+"F2.wireOp",EDGE,"E2.sketch_text.stroke-169"),sQuery(id+"F2.wireOp",EDGE,"E2.sketch_text.stroke-170"),sQuery(id+"F2.wireOp",EDGE,"E2.sketch_text.stroke-171"),sQuery(id+"F2.wireOp",EDGE,"E2.sketch_text.stroke-172"),sQuery(id+"F2.wireOp",EDGE,"E2.sketch_text.stroke-173"),sQuery(id+"F3.wireOp",EDGE,"E4.sketch_text.stroke-0"),sQuery(id+"F3.wireOp",EDGE,"E4.sketch_text.stroke-1"),sQuery(id+"F3.wireOp",EDGE,"E4.sketch_text.stroke-2"),sQuery(id+"F3.wireOp",EDGE,"E4.sketch_text.stroke-3"),sQuery(id+"F3.wireOp",EDGE,"E4.sketch_text.stroke-4"),sQuery(id+"F3.wireOp",EDGE,"E4.sketch_text.stroke-5"),sQuery(id+"F3.wireOp",EDGE,"E4.sketch_text.stroke-6"),sQuery(id+"F3.wireOp",EDGE,"E4.sketch_text.stroke-7"),sQuery(id+"F3.wireOp",EDGE,"E4.sketch_text.stroke-8"),sQuery(id+"F3.wireOp",EDGE,"E4.sketch_text.stroke-9"),sQuery(id+"F3.wireOp",EDGE,"E4.sketch_text.stroke-10"),sQuery(id+"F3.wireOp",EDGE,"E4.sketch_text.stroke-11"),sQuery(id+"F3.wireOp",EDGE,"E4.sketch_text.stroke-12"),sQuery(id+"F3.wireOp",EDGE,"E4.sketch_text.stroke-13"),sQuery(id+"F3.wireOp",EDGE,"E4.sketch_text.stroke-14"),sQuery(id+"F3.wireOp",EDGE,"E4.sketch_text.stroke-15"),sQuery(id+"F3.wireOp",EDGE,"E4.sketch_text.stroke-16"),sQuery(id+"F3.wireOp",EDGE,"E4.sketch_text.stroke-17"),sQuery(id+"F3.wireOp",EDGE,"E4.sketch_text.stroke-18"),sQuery(id+"F3.wireOp",EDGE,"E4.sketch_text.stroke-19"),sQuery(id+"F3.wireOp",EDGE,"E4.sketch_text.stroke-20"),sQuery(id+"F3.wireOp",EDGE,"E4.sketch_text.stroke-21"),sQuery(id+"F3.wireOp",EDGE,"E4.sketch_text.stroke-22"),sQuery(id+"F3.wireOp",EDGE,"E4.sketch_text.stroke-23"),sQuery(id+"F3.wireOp",EDGE,"E4.sketch_text.stroke-24"),sQuery(id+"F3.wireOp",EDGE,"E4.sketch_text.stroke-25"),sQuery(id+"F3.wireOp",EDGE,"E4.sketch_text.stroke-26"),sQuery(id+"F3.wireOp",EDGE,"E4.sketch_text.stroke-27"),sQuery(id+"F3.wireOp",EDGE,"E4.sketch_text.stroke-28"),sQuery(id+"F3.wireOp",EDGE,"E4.sketch_text.stroke-29"),sQuery(id+"F3.wireOp",EDGE,"E4.sketch_text.stroke-30"),sQuery(id+"F3.wireOp",EDGE,"E4.sketch_text.stroke-31"),sQuery(id+"F3.wireOp",EDGE,"E4.sketch_text.stroke-32"),sQuery(id+"F3.wireOp",EDGE,"E4.sketch_text.stroke-33"),sQuery(id+"F3.wireOp",EDGE,"E4.sketch_text.stroke-34"),sQuery(id+"F3.wireOp",EDGE,"E4.sketch_text.stroke-35"),sQuery(id+"F3.wireOp",EDGE,"E4.sketch_text.stroke-36"),sQuery(id+"F3.wireOp",EDGE,"E4.sketch_text.stroke-37"),sQuery(id+"F3.wireOp",EDGE,"E4.sketch_text.stroke-38"),sQuery(id+"F3.wireOp",EDGE,"E4.sketch_text.stroke-39"),sQuery(id+"F3.wireOp",EDGE,"E4.sketch_text.stroke-40"),sQuery(id+"F3.wireOp",EDGE,"E4.sketch_text.stroke-41"),sQuery(id+"F3.wireOp",EDGE,"E4.sketch_text.stroke-42"),sQuery(id+"F3.wireOp",EDGE,"E4.sketch_text.stroke-43"),sQuery(id+"F3.wireOp",EDGE,"E4.sketch_text.stroke-44"),sQuery(id+"F3.wireOp",EDGE,"E4.sketch_text.stroke-45"),sQuery(id+"F3.wireOp",EDGE,"E4.sketch_text.stroke-46"),sQuery(id+"F3.wireOp",EDGE,"E4.sketch_text.stroke-47"),sQuery(id+"F3.wireOp",EDGE,"E4.sketch_text.stroke-48"),sQuery(id+"F3.wireOp",EDGE,"E4.sketch_text.stroke-49"),sQuery(id+"F3.wireOp",EDGE,"E4.sketch_text.stroke-50"),sQuery(id+"F3.wireOp",EDGE,"E4.sketch_text.stroke-51"),sQuery(id+"F3.wireOp",EDGE,"E4.sketch_text.stroke-52"),sQuery(id+"F3.wireOp",EDGE,"E4.sketch_text.stroke-53"),sQuery(id+"F3.wireOp",EDGE,"E4.sketch_text.stroke-54"),sQuery(id+"F3.wireOp",EDGE,"E4.sketch_text.stroke-55"),sQuery(id+"F3.wireOp",EDGE,"E4.sketch_text.stroke-56"),sQuery(id+"F3.wireOp",EDGE,"E4.sketch_text.stroke-57"),sQuery(id+"F3.wireOp",EDGE,"E4.sketch_text.stroke-58"),sQuery(id+"F3.wireOp",EDGE,"E4.sketch_text.stroke-59"),sQuery(id+"F3.wireOp",EDGE,"E4.sketch_text.stroke-60"),sQuery(id+"F3.wireOp",EDGE,"E4.sketch_text.stroke-61"),sQuery(id+"F3.wireOp",EDGE,"E4.sketch_text.stroke-62"),sQuery(id+"F3.wireOp",EDGE,"E4.sketch_text.stroke-71"),sQuery(id+"F3.wireOp",EDGE,"E4.sketch_text.stroke-72"),sQuery(id+"F3.wireOp",EDGE,"E4.sketch_text.stroke-73"),sQuery(id+"F3.wireOp",EDGE,"E4.sketch_text.stroke-74"),sQuery(id+"F3.wireOp",EDGE,"E4.sketch_text.stroke-75"),sQuery(id+"F3.wireOp",EDGE,"E4.sketch_text.stroke-76"),sQuery(id+"F3.wireOp",EDGE,"E4.sketch_text.stroke-77"),sQuery(id+"F3.wireOp",EDGE,"E4.sketch_text.stroke-78"),sQuery(id+"F3.wireOp",EDGE,"E4.sketch_text.stroke-79"),sQuery(id+"F3.wireOp",EDGE,"E4.sketch_text.stroke-80"),sQuery(id+"F3.wireOp",EDGE,"E4.sketch_text.stroke-81"),sQuery(id+"F3.wireOp",EDGE,"E4.sketch_text.stroke-82"),sQuery(id+"F3.wireOp",EDGE,"E4.sketch_text.stroke-83"),sQuery(id+"F3.wireOp",EDGE,"E4.sketch_text.stroke-84"),sQuery(id+"F3.wireOp",EDGE,"E4.sketch_text.stroke-85"),sQuery(id+"F3.wireOp",EDGE,"E4.sketch_text.stroke-86"),sQuery(id+"F3.wireOp",EDGE,"E4.sketch_text.stroke-87"),sQuery(id+"F3.wireOp",EDGE,"E4.sketch_text.stroke-88"),sQuery(id+"F3.wireOp",EDGE,"E4.sketch_text.stroke-89"),sQuery(id+"F3.wireOp",EDGE,"E4.sketch_text.stroke-90"),sQuery(id+"F3.wireOp",EDGE,"E4.sketch_text.stroke-91"),sQuery(id+"F3.wireOp",EDGE,"E4.sketch_text.stroke-92"),sQuery(id+"F3.wireOp",EDGE,"E4.sketch_text.stroke-93"),sQuery(id+"F3.wireOp",EDGE,"E4.sketch_text.stroke-94"),sQuery(id+"F3.wireOp",EDGE,"E4.sketch_text.stroke-95"),sQuery(id+"F3.wireOp",EDGE,"E4.sketch_text.stroke-96"),sQuery(id+"F3.wireOp",EDGE,"E4.sketch_text.stroke-97"),sQuery(id+"F3.wireOp",EDGE,"E4.sketch_text.stroke-103"),sQuery(id+"F3.wireOp",EDGE,"E4.sketch_text.stroke-104"),sQuery(id+"F3.wireOp",EDGE,"E4.sketch_text.stroke-105"),sQuery(id+"F3.wireOp",EDGE,"E4.sketch_text.stroke-106"),sQuery(id+"F3.wireOp",EDGE,"E4.sketch_text.stroke-107"),sQuery(id+"F3.wireOp",EDGE,"E4.sketch_text.stroke-108"),sQuery(id+"F3.wireOp",EDGE,"E4.sketch_text.stroke-109"),sQuery(id+"F3.wireOp",EDGE,"E4.sketch_text.stroke-110"),sQuery(id+"F3.wireOp",EDGE,"E4.sketch_text.stroke-111"),sQuery(id+"F3.wireOp",EDGE,"E4.sketch_text.stroke-112"),sQuery(id+"F3.wireOp",EDGE,"E4.sketch_text.stroke-113"),sQuery(id+"F3.wireOp",EDGE,"E4.sketch_text.stroke-114"),sQuery(id+"F3.wireOp",EDGE,"E4.sketch_text.stroke-115"),sQuery(id+"F3.wireOp",EDGE,"E4.sketch_text.stroke-116"),sQuery(id+"F3.wireOp",EDGE,"E4.sketch_text.stroke-117"),sQuery(id+"F3.wireOp",EDGE,"E4.sketch_text.stroke-118"),sQuery(id+"F3.wireOp",EDGE,"E4.sketch_text.stroke-119"),sQuery(id+"F3.wireOp",EDGE,"E4.sketch_text.stroke-120"),sQuery(id+"F3.wireOp",EDGE,"E4.sketch_text.stroke-121"),sQuery(id+"F3.wireOp",EDGE,"E4.sketch_text.stroke-122"),sQuery(id+"F3.wireOp",EDGE,"E4.sketch_text.stroke-123"),sQuery(id+"F3.wireOp",EDGE,"E4.sketch_text.stroke-124"),sQuery(id+"F3.wireOp",EDGE,"E4.sketch_text.stroke-125"),sQuery(id+"F3.wireOp",EDGE,"E4.sketch_text.stroke-126"),sQuery(id+"F3.wireOp",EDGE,"E4.sketch_text.stroke-127"),sQuery(id+"F3.wireOp",EDGE,"E4.sketch_text.stroke-128"),sQuery(id+"F3.wireOp",EDGE,"E4.sketch_text.stroke-129"),sQuery(id+"F3.wireOp",EDGE,"E4.sketch_text.stroke-130"),sQuery(id+"F3.wireOp",EDGE,"E4.sketch_text.stroke-131"),sQuery(id+"F3.wireOp",EDGE,"E4.sketch_text.stroke-132"),sQuery(id+"F3.wireOp",EDGE,"E4.sketch_text.stroke-133"),sQuery(id+"F3.wireOp",EDGE,"E4.sketch_text.stroke-134"),sQuery(id+"F3.wireOp",EDGE,"E4.sketch_text.stroke-135"),sQuery(id+"F3.wireOp",EDGE,"E4.sketch_text.stroke-136"),sQuery(id+"F3.wireOp",EDGE,"E4.sketch_text.stroke-137"),sQuery(id+"F3.wireOp",EDGE,"E4.sketch_text.stroke-138"),sQuery(id+"F3.wireOp",EDGE,"E4.sketch_text.stroke-139"),sQuery(id+"F3.wireOp",EDGE,"E4.sketch_text.stroke-140"),sQuery(id+"F3.wireOp",EDGE,"E4.sketch_text.stroke-141"),sQuery(id+"F3.wireOp",EDGE,"E4.sketch_text.stroke-142"),sQuery(id+"F3.wireOp",EDGE,"E4.sketch_text.stroke-143"),sQuery(id+"F3.wireOp",EDGE,"E4.sketch_text.stroke-144"),sQuery(id+"F3.wireOp",EDGE,"E4.sketch_text.stroke-145"),sQuery(id+"F3.wireOp",EDGE,"E4.sketch_text.stroke-146"),sQuery(id+"F3.wireOp",EDGE,"E4.sketch_text.stroke-147"),sQuery(id+"F3.wireOp",EDGE,"E4.sketch_text.stroke-148"),sQuery(id+"F3.wireOp",EDGE,"E4.sketch_text.stroke-149"),sQuery(id+"F3.wireOp",EDGE,"E4.sketch_text.stroke-150"),sQuery(id+"F3.wireOp",EDGE,"E4.sketch_text.stroke-151"),sQuery(id+"F3.wireOp",EDGE,"E4.sketch_text.stroke-152"),sQuery(id+"F3.wireOp",EDGE,"E4.sketch_text.stroke-153"),sQuery(id+"F3.wireOp",EDGE,"E4.sketch_text.stroke-159"),sQuery(id+"F3.wireOp",EDGE,"E4.sketch_text.stroke-160"),sQuery(id+"F3.wireOp",EDGE,"E4.sketch_text.stroke-161"),sQuery(id+"F3.wireOp",EDGE,"E4.sketch_text.stroke-162"),sQuery(id+"F3.wireOp",EDGE,"E4.sketch_text.stroke-163"),sQuery(id+"F3.wireOp",EDGE,"E4.sketch_text.stroke-164"),sQuery(id+"F3.wireOp",EDGE,"E4.sketch_text.stroke-165"),sQuery(id+"F3.wireOp",EDGE,"E4.sketch_text.stroke-166"),sQuery(id+"F3.wireOp",EDGE,"E4.sketch_text.stroke-167"),sQuery(id+"F3.wireOp",EDGE,"E4.sketch_text.stroke-168"),sQuery(id+"F3.wireOp",EDGE,"E4.sketch_text.stroke-169"),sQuery(id+"F3.wireOp",EDGE,"E4.sketch_text.stroke-170"),sQuery(id+"F3.wireOp",EDGE,"E4.sketch_text.stroke-171"),sQuery(id+"F3.wireOp",EDGE,"E4.sketch_text.stroke-172"),sQuery(id+"F3.wireOp",EDGE,"E4.sketch_text.stroke-173"),sQuery(id+"F3.wireOp",EDGE,"E4.sketch_text.stroke-174"),sQuery(id+"F3.wireOp",EDGE,"E4.sketch_text.stroke-175"),sQuery(id+"F3.wireOp",EDGE,"E4.sketch_text.stroke-176"),sQuery(id+"F3.wireOp",EDGE,"E4.sketch_text.stroke-177"),sQuery(id+"F3.wireOp",EDGE,"E4.sketch_text.stroke-178"),sQuery(id+"F3.wireOp",EDGE,"E4.sketch_text.stroke-179"),sQuery(id+"F3.wireOp",EDGE,"E4.sketch_text.stroke-180"),sQuery(id+"F4.wireOp",EDGE,"8007402e-1a4e-4a06-85a5-2af08e553504"),subQ2])],"isStart":true}),makeQuery(id+"F5.opExtrude","SWEPT_FACE",FACE,{"disambiguationData":[OSD([subQ2])]})]),OD(1.0)],"derivedFrom":makeQuery(id+"F1.opExtrude","CAP_EDGE",EDGE,{"disambiguationData":[OSD([subQ0])],"isStart":false})});}
            var Q15;
            {var subQ0=sQuery(id+"F4.wireOp",EDGE,"8007402e-1a4e-4a06-85a5-2af08e553504");var subQ1=sQuery(id+"F0.wireOp",EDGE,"E0.top");var subQ2=sQuery(id+"F4.wireOp",EDGE,"727ac2c1-f511-4829-95a7-a443ef16a4cd");var subQ3=sQuery(id+"F0.wireOp",EDGE,"E0.bottom");Q15=makeQuery(id+"F5.boolean.opBoolean","SPLIT",EDGE,{"disambiguationData":[TD([makeQuery(id+"F1.opExtrude","CAP_FACE",FACE,{"disambiguationData":[OSD([subQ3,subQ1,sQuery(id+"F0.wireOp",EDGE,"E0.left"),sQuery(id+"F0.wireOp",EDGE,"E0.right")])],"isStart":false}),makeQuery(id+"F1.opExtrude","SWEPT_FACE",FACE,{"disambiguationData":[OSD([subQ1])]}),makeQuery(id+"F5.opExtrude","SWEPT_FACE",FACE,{"disambiguationData":[OSD([subQ0])]}),makeQuery(id+"F5.opExtrude","CAP_FACE",FACE,{"disambiguationData":[OSD([subQ3,sQuery(id+"F2.wireOp",EDGE,"E2.sketch_text.stroke-0"),sQuery(id+"F2.wireOp",EDGE,"E2.sketch_text.stroke-1"),sQuery(id+"F2.wireOp",EDGE,"E2.sketch_text.stroke-2"),sQuery(id+"F2.wireOp",EDGE,"E2.sketch_text.stroke-3"),sQuery(id+"F2.wireOp",EDGE,"E2.sketch_text.stroke-4"),sQuery(id+"F2.wireOp",EDGE,"E2.sketch_text.stroke-5"),sQuery(id+"F2.wireOp",EDGE,"E2.sketch_text.stroke-6"),sQuery(id+"F2.wireOp",EDGE,"E2.sketch_text.stroke-7"),sQuery(id+"F2.wireOp",EDGE,"E2.sketch_text.stroke-8"),sQuery(id+"F2.wireOp",EDGE,"E2.sketch_text.stroke-9"),sQuery(id+"F2.wireOp",EDGE,"E2.sketch_text.stroke-10"),sQuery(id+"F2.wireOp",EDGE,"E2.sketch_text.stroke-11"),sQuery(id+"F2.wireOp",EDGE,"E2.sketch_text.stroke-12"),sQuery(id+"F2.wireOp",EDGE,"E2.sketch_text.stroke-13"),sQuery(id+"F2.wireOp",EDGE,"E2.sketch_text.stroke-14"),sQuery(id+"F2.wireOp",EDGE,"E2.sketch_text.stroke-15"),sQuery(id+"F2.wireOp",EDGE,"E2.sketch_text.stroke-16"),sQuery(id+"F2.wireOp",EDGE,"E2.sketch_text.stroke-17"),sQuery(id+"F2.wireOp",EDGE,"E2.sketch_text.stroke-18"),sQuery(id+"F2.wireOp",EDGE,"E2.sketch_text.stroke-19"),sQuery(id+"F2.wireOp",EDGE,"E2.sketch_text.stroke-20"),sQuery(id+"F2.wireOp",EDGE,"E2.sketch_text.stroke-21"),sQuery(id+"F2.wireOp",EDGE,"E2.sketch_text.stroke-22"),sQuery(id+"F2.wireOp",EDGE,"E2.sketch_text.stroke-23"),sQuery(id+"F2.wireOp",EDGE,"E2.sketch_text.stroke-24"),sQuery(id+"F2.wireOp",EDGE,"E2.sketch_text.stroke-25"),sQuery(id+"F2.wireOp",EDGE,"E2.sketch_text.stroke-26"),sQuery(id+"F2.wireOp",EDGE,"E2.sketch_text.stroke-27"),sQuery(id+"F2.wireOp",EDGE,"E2.sketch_text.stroke-28"),sQuery(id+"F2.wireOp",EDGE,"E2.sketch_text.stroke-29"),sQuery(id+"F2.wireOp",EDGE,"E2.sketch_text.stroke-30"),sQuery(id+"F2.wireOp",EDGE,"E2.sketch_text.stroke-31"),sQuery(id+"F2.wireOp",EDGE,"E2.sketch_text.stroke-32"),sQuery(id+"F2.wireOp",EDGE,"E2.sketch_text.stroke-33"),sQuery(id+"F2.wireOp",EDGE,"E2.sketch_text.stroke-34"),sQuery(id+"F2.wireOp",EDGE,"E2.sketch_text.stroke-35"),sQuery(id+"F2.wireOp",EDGE,"E2.sketch_text.stroke-36"),sQuery(id+"F2.wireOp",EDGE,"E2.sketch_text.stroke-37"),sQuery(id+"F2.wireOp",EDGE,"E2.sketch_text.stroke-38"),sQuery(id+"F2.wireOp",EDGE,"E2.sketch_text.stroke-39"),sQuery(id+"F2.wireOp",EDGE,"E2.sketch_text.stroke-40"),sQuery(id+"F2.wireOp",EDGE,"E2.sketch_text.stroke-41"),sQuery(id+"F2.wireOp",EDGE,"E2.sketch_text.stroke-42"),sQuery(id+"F2.wireOp",EDGE,"E2.sketch_text.stroke-43"),sQuery(id+"F2.wireOp",EDGE,"E2.sketch_text.stroke-44"),sQuery(id+"F2.wireOp",EDGE,"E2.sketch_text.stroke-45"),sQuery(id+"F2.wireOp",EDGE,"E2.sketch_text.stroke-46"),sQuery(id+"F2.wireOp",EDGE,"E2.sketch_text.stroke-47"),sQuery(id+"F2.wireOp",EDGE,"E2.sketch_text.stroke-48"),sQuery(id+"F2.wireOp",EDGE,"E2.sketch_text.stroke-49"),sQuery(id+"F2.wireOp",EDGE,"E2.sketch_text.stroke-50"),sQuery(id+"F2.wireOp",EDGE,"E2.sketch_text.stroke-51"),sQuery(id+"F2.wireOp",EDGE,"E2.sketch_text.stroke-52"),sQuery(id+"F2.wireOp",EDGE,"E2.sketch_text.stroke-53"),sQuery(id+"F2.wireOp",EDGE,"E2.sketch_text.stroke-54"),sQuery(id+"F2.wireOp",EDGE,"E2.sketch_text.stroke-55"),sQuery(id+"F2.wireOp",EDGE,"E2.sketch_text.stroke-56"),sQuery(id+"F2.wireOp",EDGE,"E2.sketch_text.stroke-57"),sQuery(id+"F2.wireOp",EDGE,"E2.sketch_text.stroke-58"),sQuery(id+"F2.wireOp",EDGE,"E2.sketch_text.stroke-59"),sQuery(id+"F2.wireOp",EDGE,"E2.sketch_text.stroke-60"),sQuery(id+"F2.wireOp",EDGE,"E2.sketch_text.stroke-61"),sQuery(id+"F2.wireOp",EDGE,"E2.sketch_text.stroke-62"),sQuery(id+"F2.wireOp",EDGE,"E2.sketch_text.stroke-63"),sQuery(id+"F2.wireOp",EDGE,"E2.sketch_text.stroke-64"),sQuery(id+"F2.wireOp",EDGE,"E2.sketch_text.stroke-65"),sQuery(id+"F2.wireOp",EDGE,"E2.sketch_text.stroke-66"),sQuery(id+"F2.wireOp",EDGE,"E2.sketch_text.stroke-67"),sQuery(id+"F2.wireOp",EDGE,"E2.sketch_text.stroke-68"),sQuery(id+"F2.wireOp",EDGE,"E2.sketch_text.stroke-69"),sQuery(id+"F2.wireOp",EDGE,"E2.sketch_text.stroke-70"),sQuery(id+"F2.wireOp",EDGE,"E2.sketch_text.stroke-71"),sQuery(id+"F2.wireOp",EDGE,"E2.sketch_text.stroke-72"),sQuery(id+"F2.wireOp",EDGE,"E2.sketch_text.stroke-73"),sQuery(id+"F2.wireOp",EDGE,"E2.sketch_text.stroke-74"),sQuery(id+"F2.wireOp",EDGE,"E2.sketch_text.stroke-75"),sQuery(id+"F2.wireOp",EDGE,"E2.sketch_text.stroke-76"),sQuery(id+"F2.wireOp",EDGE,"E2.sketch_text.stroke-77"),sQuery(id+"F2.wireOp",EDGE,"E2.sketch_text.stroke-78"),sQuery(id+"F2.wireOp",EDGE,"E2.sketch_text.stroke-79"),sQuery(id+"F2.wireOp",EDGE,"E2.sketch_text.stroke-80"),sQuery(id+"F2.wireOp",EDGE,"E2.sketch_text.stroke-81"),sQuery(id+"F2.wireOp",EDGE,"E2.sketch_text.stroke-82"),sQuery(id+"F2.wireOp",EDGE,"E2.sketch_text.stroke-83"),sQuery(id+"F2.wireOp",EDGE,"E2.sketch_text.stroke-84"),sQuery(id+"F2.wireOp",EDGE,"E2.sketch_text.stroke-85"),sQuery(id+"F2.wireOp",EDGE,"E2.sketch_text.stroke-86"),sQuery(id+"F2.wireOp",EDGE,"E2.sketch_text.stroke-87"),sQuery(id+"F2.wireOp",EDGE,"E2.sketch_text.stroke-88"),sQuery(id+"F2.wireOp",EDGE,"E2.sketch_text.stroke-89"),sQuery(id+"F2.wireOp",EDGE,"E2.sketch_text.stroke-90"),sQuery(id+"F2.wireOp",EDGE,"E2.sketch_text.stroke-91"),sQuery(id+"F2.wireOp",EDGE,"E2.sketch_text.stroke-92"),sQuery(id+"F2.wireOp",EDGE,"E2.sketch_text.stroke-93"),sQuery(id+"F2.wireOp",EDGE,"E2.sketch_text.stroke-94"),sQuery(id+"F2.wireOp",EDGE,"E2.sketch_text.stroke-95"),sQuery(id+"F2.wireOp",EDGE,"E2.sketch_text.stroke-96"),sQuery(id+"F2.wireOp",EDGE,"E2.sketch_text.stroke-97"),sQuery(id+"F2.wireOp",EDGE,"E2.sketch_text.stroke-98"),sQuery(id+"F2.wireOp",EDGE,"E2.sketch_text.stroke-99"),sQuery(id+"F2.wireOp",EDGE,"E2.sketch_text.stroke-100"),sQuery(id+"F2.wireOp",EDGE,"E2.sketch_text.stroke-101"),sQuery(id+"F2.wireOp",EDGE,"E2.sketch_text.stroke-102"),sQuery(id+"F2.wireOp",EDGE,"E2.sketch_text.stroke-103"),sQuery(id+"F2.wireOp",EDGE,"E2.sketch_text.stroke-104"),sQuery(id+"F2.wireOp",EDGE,"E2.sketch_text.stroke-105"),sQuery(id+"F2.wireOp",EDGE,"E2.sketch_text.stroke-106"),sQuery(id+"F2.wireOp",EDGE,"E2.sketch_text.stroke-107"),sQuery(id+"F2.wireOp",EDGE,"E2.sketch_text.stroke-108"),sQuery(id+"F2.wireOp",EDGE,"E2.sketch_text.stroke-109"),sQuery(id+"F2.wireOp",EDGE,"E2.sketch_text.stroke-110"),sQuery(id+"F2.wireOp",EDGE,"E2.sketch_text.stroke-111"),sQuery(id+"F2.wireOp",EDGE,"E2.sketch_text.stroke-112"),sQuery(id+"F2.wireOp",EDGE,"E2.sketch_text.stroke-113"),sQuery(id+"F2.wireOp",EDGE,"E2.sketch_text.stroke-114"),sQuery(id+"F2.wireOp",EDGE,"E2.sketch_text.stroke-115"),sQuery(id+"F2.wireOp",EDGE,"E2.sketch_text.stroke-116"),sQuery(id+"F2.wireOp",EDGE,"E2.sketch_text.stroke-117"),sQuery(id+"F2.wireOp",EDGE,"E2.sketch_text.stroke-118"),sQuery(id+"F2.wireOp",EDGE,"E2.sketch_text.stroke-119"),sQuery(id+"F2.wireOp",EDGE,"E2.sketch_text.stroke-120"),sQuery(id+"F2.wireOp",EDGE,"E2.sketch_text.stroke-121"),sQuery(id+"F2.wireOp",EDGE,"E2.sketch_text.stroke-122"),sQuery(id+"F2.wireOp",EDGE,"E2.sketch_text.stroke-123"),sQuery(id+"F2.wireOp",EDGE,"E2.sketch_text.stroke-124"),sQuery(id+"F2.wireOp",EDGE,"E2.sketch_text.stroke-125"),sQuery(id+"F2.wireOp",EDGE,"E2.sketch_text.stroke-126"),sQuery(id+"F2.wireOp",EDGE,"E2.sketch_text.stroke-127"),sQuery(id+"F2.wireOp",EDGE,"E2.sketch_text.stroke-128"),sQuery(id+"F2.wireOp",EDGE,"E2.sketch_text.stroke-129"),sQuery(id+"F2.wireOp",EDGE,"E2.sketch_text.stroke-130"),sQuery(id+"F2.wireOp",EDGE,"E2.sketch_text.stroke-131"),sQuery(id+"F2.wireOp",EDGE,"E2.sketch_text.stroke-132"),sQuery(id+"F2.wireOp",EDGE,"E2.sketch_text.stroke-133"),sQuery(id+"F2.wireOp",EDGE,"E2.sketch_text.stroke-134"),sQuery(id+"F2.wireOp",EDGE,"E2.sketch_text.stroke-135"),sQuery(id+"F2.wireOp",EDGE,"E2.sketch_text.stroke-136"),sQuery(id+"F2.wireOp",EDGE,"E2.sketch_text.stroke-137"),sQuery(id+"F2.wireOp",EDGE,"E2.sketch_text.stroke-138"),sQuery(id+"F2.wireOp",EDGE,"E2.sketch_text.stroke-139"),sQuery(id+"F2.wireOp",EDGE,"E2.sketch_text.stroke-140"),sQuery(id+"F2.wireOp",EDGE,"E2.sketch_text.stroke-141"),sQuery(id+"F2.wireOp",EDGE,"E2.sketch_text.stroke-142"),sQuery(id+"F2.wireOp",EDGE,"E2.sketch_text.stroke-143"),sQuery(id+"F2.wireOp",EDGE,"E2.sketch_text.stroke-144"),sQuery(id+"F2.wireOp",EDGE,"E2.sketch_text.stroke-145"),sQuery(id+"F2.wireOp",EDGE,"E2.sketch_text.stroke-146"),sQuery(id+"F2.wireOp",EDGE,"E2.sketch_text.stroke-147"),sQuery(id+"F2.wireOp",EDGE,"E2.sketch_text.stroke-148"),sQuery(id+"F2.wireOp",EDGE,"E2.sketch_text.stroke-149"),sQuery(id+"F2.wireOp",EDGE,"E2.sketch_text.stroke-150"),sQuery(id+"F2.wireOp",EDGE,"E2.sketch_text.stroke-151"),sQuery(id+"F2.wireOp",EDGE,"E2.sketch_text.stroke-152"),sQuery(id+"F2.wireOp",EDGE,"E2.sketch_text.stroke-153"),sQuery(id+"F2.wireOp",EDGE,"E2.sketch_text.stroke-154"),sQuery(id+"F2.wireOp",EDGE,"E2.sketch_text.stroke-155"),sQuery(id+"F2.wireOp",EDGE,"E2.sketch_text.stroke-156"),sQuery(id+"F2.wireOp",EDGE,"E2.sketch_text.stroke-157"),sQuery(id+"F2.wireOp",EDGE,"E2.sketch_text.stroke-158"),sQuery(id+"F2.wireOp",EDGE,"E2.sketch_text.stroke-159"),sQuery(id+"F2.wireOp",EDGE,"E2.sketch_text.stroke-160"),sQuery(id+"F2.wireOp",EDGE,"E2.sketch_text.stroke-161"),sQuery(id+"F2.wireOp",EDGE,"E2.sketch_text.stroke-162"),sQuery(id+"F2.wireOp",EDGE,"E2.sketch_text.stroke-163"),sQuery(id+"F2.wireOp",EDGE,"E2.sketch_text.stroke-164"),sQuery(id+"F2.wireOp",EDGE,"E2.sketch_text.stroke-165"),sQuery(id+"F2.wireOp",EDGE,"E2.sketch_text.stroke-166"),sQuery(id+"F2.wireOp",EDGE,"E2.sketch_text.stroke-167"),sQuery(id+"F2.wireOp",EDGE,"E2.sketch_text.stroke-168"),sQuery(id+"F2.wireOp",EDGE,"E2.sketch_text.stroke-169"),sQuery(id+"F2.wireOp",EDGE,"E2.sketch_text.stroke-170"),sQuery(id+"F2.wireOp",EDGE,"E2.sketch_text.stroke-171"),sQuery(id+"F2.wireOp",EDGE,"E2.sketch_text.stroke-172"),sQuery(id+"F2.wireOp",EDGE,"E2.sketch_text.stroke-173"),sQuery(id+"F3.wireOp",EDGE,"E4.sketch_text.stroke-0"),sQuery(id+"F3.wireOp",EDGE,"E4.sketch_text.stroke-1"),sQuery(id+"F3.wireOp",EDGE,"E4.sketch_text.stroke-2"),sQuery(id+"F3.wireOp",EDGE,"E4.sketch_text.stroke-3"),sQuery(id+"F3.wireOp",EDGE,"E4.sketch_text.stroke-4"),sQuery(id+"F3.wireOp",EDGE,"E4.sketch_text.stroke-5"),sQuery(id+"F3.wireOp",EDGE,"E4.sketch_text.stroke-6"),sQuery(id+"F3.wireOp",EDGE,"E4.sketch_text.stroke-7"),sQuery(id+"F3.wireOp",EDGE,"E4.sketch_text.stroke-8"),sQuery(id+"F3.wireOp",EDGE,"E4.sketch_text.stroke-9"),sQuery(id+"F3.wireOp",EDGE,"E4.sketch_text.stroke-10"),sQuery(id+"F3.wireOp",EDGE,"E4.sketch_text.stroke-11"),sQuery(id+"F3.wireOp",EDGE,"E4.sketch_text.stroke-12"),sQuery(id+"F3.wireOp",EDGE,"E4.sketch_text.stroke-13"),sQuery(id+"F3.wireOp",EDGE,"E4.sketch_text.stroke-14"),sQuery(id+"F3.wireOp",EDGE,"E4.sketch_text.stroke-15"),sQuery(id+"F3.wireOp",EDGE,"E4.sketch_text.stroke-16"),sQuery(id+"F3.wireOp",EDGE,"E4.sketch_text.stroke-17"),sQuery(id+"F3.wireOp",EDGE,"E4.sketch_text.stroke-18"),sQuery(id+"F3.wireOp",EDGE,"E4.sketch_text.stroke-19"),sQuery(id+"F3.wireOp",EDGE,"E4.sketch_text.stroke-20"),sQuery(id+"F3.wireOp",EDGE,"E4.sketch_text.stroke-21"),sQuery(id+"F3.wireOp",EDGE,"E4.sketch_text.stroke-22"),sQuery(id+"F3.wireOp",EDGE,"E4.sketch_text.stroke-23"),sQuery(id+"F3.wireOp",EDGE,"E4.sketch_text.stroke-24"),sQuery(id+"F3.wireOp",EDGE,"E4.sketch_text.stroke-25"),sQuery(id+"F3.wireOp",EDGE,"E4.sketch_text.stroke-26"),sQuery(id+"F3.wireOp",EDGE,"E4.sketch_text.stroke-27"),sQuery(id+"F3.wireOp",EDGE,"E4.sketch_text.stroke-28"),sQuery(id+"F3.wireOp",EDGE,"E4.sketch_text.stroke-29"),sQuery(id+"F3.wireOp",EDGE,"E4.sketch_text.stroke-30"),sQuery(id+"F3.wireOp",EDGE,"E4.sketch_text.stroke-31"),sQuery(id+"F3.wireOp",EDGE,"E4.sketch_text.stroke-32"),sQuery(id+"F3.wireOp",EDGE,"E4.sketch_text.stroke-33"),sQuery(id+"F3.wireOp",EDGE,"E4.sketch_text.stroke-34"),sQuery(id+"F3.wireOp",EDGE,"E4.sketch_text.stroke-35"),sQuery(id+"F3.wireOp",EDGE,"E4.sketch_text.stroke-36"),sQuery(id+"F3.wireOp",EDGE,"E4.sketch_text.stroke-37"),sQuery(id+"F3.wireOp",EDGE,"E4.sketch_text.stroke-38"),sQuery(id+"F3.wireOp",EDGE,"E4.sketch_text.stroke-39"),sQuery(id+"F3.wireOp",EDGE,"E4.sketch_text.stroke-40"),sQuery(id+"F3.wireOp",EDGE,"E4.sketch_text.stroke-41"),sQuery(id+"F3.wireOp",EDGE,"E4.sketch_text.stroke-42"),sQuery(id+"F3.wireOp",EDGE,"E4.sketch_text.stroke-43"),sQuery(id+"F3.wireOp",EDGE,"E4.sketch_text.stroke-44"),sQuery(id+"F3.wireOp",EDGE,"E4.sketch_text.stroke-45"),sQuery(id+"F3.wireOp",EDGE,"E4.sketch_text.stroke-46"),sQuery(id+"F3.wireOp",EDGE,"E4.sketch_text.stroke-47"),sQuery(id+"F3.wireOp",EDGE,"E4.sketch_text.stroke-48"),sQuery(id+"F3.wireOp",EDGE,"E4.sketch_text.stroke-49"),sQuery(id+"F3.wireOp",EDGE,"E4.sketch_text.stroke-50"),sQuery(id+"F3.wireOp",EDGE,"E4.sketch_text.stroke-51"),sQuery(id+"F3.wireOp",EDGE,"E4.sketch_text.stroke-52"),sQuery(id+"F3.wireOp",EDGE,"E4.sketch_text.stroke-53"),sQuery(id+"F3.wireOp",EDGE,"E4.sketch_text.stroke-54"),sQuery(id+"F3.wireOp",EDGE,"E4.sketch_text.stroke-55"),sQuery(id+"F3.wireOp",EDGE,"E4.sketch_text.stroke-56"),sQuery(id+"F3.wireOp",EDGE,"E4.sketch_text.stroke-57"),sQuery(id+"F3.wireOp",EDGE,"E4.sketch_text.stroke-58"),sQuery(id+"F3.wireOp",EDGE,"E4.sketch_text.stroke-59"),sQuery(id+"F3.wireOp",EDGE,"E4.sketch_text.stroke-60"),sQuery(id+"F3.wireOp",EDGE,"E4.sketch_text.stroke-61"),sQuery(id+"F3.wireOp",EDGE,"E4.sketch_text.stroke-62"),sQuery(id+"F3.wireOp",EDGE,"E4.sketch_text.stroke-71"),sQuery(id+"F3.wireOp",EDGE,"E4.sketch_text.stroke-72"),sQuery(id+"F3.wireOp",EDGE,"E4.sketch_text.stroke-73"),sQuery(id+"F3.wireOp",EDGE,"E4.sketch_text.stroke-74"),sQuery(id+"F3.wireOp",EDGE,"E4.sketch_text.stroke-75"),sQuery(id+"F3.wireOp",EDGE,"E4.sketch_text.stroke-76"),sQuery(id+"F3.wireOp",EDGE,"E4.sketch_text.stroke-77"),sQuery(id+"F3.wireOp",EDGE,"E4.sketch_text.stroke-78"),sQuery(id+"F3.wireOp",EDGE,"E4.sketch_text.stroke-79"),sQuery(id+"F3.wireOp",EDGE,"E4.sketch_text.stroke-80"),sQuery(id+"F3.wireOp",EDGE,"E4.sketch_text.stroke-81"),sQuery(id+"F3.wireOp",EDGE,"E4.sketch_text.stroke-82"),sQuery(id+"F3.wireOp",EDGE,"E4.sketch_text.stroke-83"),sQuery(id+"F3.wireOp",EDGE,"E4.sketch_text.stroke-84"),sQuery(id+"F3.wireOp",EDGE,"E4.sketch_text.stroke-85"),sQuery(id+"F3.wireOp",EDGE,"E4.sketch_text.stroke-86"),sQuery(id+"F3.wireOp",EDGE,"E4.sketch_text.stroke-87"),sQuery(id+"F3.wireOp",EDGE,"E4.sketch_text.stroke-88"),sQuery(id+"F3.wireOp",EDGE,"E4.sketch_text.stroke-89"),sQuery(id+"F3.wireOp",EDGE,"E4.sketch_text.stroke-90"),sQuery(id+"F3.wireOp",EDGE,"E4.sketch_text.stroke-91"),sQuery(id+"F3.wireOp",EDGE,"E4.sketch_text.stroke-92"),sQuery(id+"F3.wireOp",EDGE,"E4.sketch_text.stroke-93"),sQuery(id+"F3.wireOp",EDGE,"E4.sketch_text.stroke-94"),sQuery(id+"F3.wireOp",EDGE,"E4.sketch_text.stroke-95"),sQuery(id+"F3.wireOp",EDGE,"E4.sketch_text.stroke-96"),sQuery(id+"F3.wireOp",EDGE,"E4.sketch_text.stroke-97"),sQuery(id+"F3.wireOp",EDGE,"E4.sketch_text.stroke-103"),sQuery(id+"F3.wireOp",EDGE,"E4.sketch_text.stroke-104"),sQuery(id+"F3.wireOp",EDGE,"E4.sketch_text.stroke-105"),sQuery(id+"F3.wireOp",EDGE,"E4.sketch_text.stroke-106"),sQuery(id+"F3.wireOp",EDGE,"E4.sketch_text.stroke-107"),sQuery(id+"F3.wireOp",EDGE,"E4.sketch_text.stroke-108"),sQuery(id+"F3.wireOp",EDGE,"E4.sketch_text.stroke-109"),sQuery(id+"F3.wireOp",EDGE,"E4.sketch_text.stroke-110"),sQuery(id+"F3.wireOp",EDGE,"E4.sketch_text.stroke-111"),sQuery(id+"F3.wireOp",EDGE,"E4.sketch_text.stroke-112"),sQuery(id+"F3.wireOp",EDGE,"E4.sketch_text.stroke-113"),sQuery(id+"F3.wireOp",EDGE,"E4.sketch_text.stroke-114"),sQuery(id+"F3.wireOp",EDGE,"E4.sketch_text.stroke-115"),sQuery(id+"F3.wireOp",EDGE,"E4.sketch_text.stroke-116"),sQuery(id+"F3.wireOp",EDGE,"E4.sketch_text.stroke-117"),sQuery(id+"F3.wireOp",EDGE,"E4.sketch_text.stroke-118"),sQuery(id+"F3.wireOp",EDGE,"E4.sketch_text.stroke-119"),sQuery(id+"F3.wireOp",EDGE,"E4.sketch_text.stroke-120"),sQuery(id+"F3.wireOp",EDGE,"E4.sketch_text.stroke-121"),sQuery(id+"F3.wireOp",EDGE,"E4.sketch_text.stroke-122"),sQuery(id+"F3.wireOp",EDGE,"E4.sketch_text.stroke-123"),sQuery(id+"F3.wireOp",EDGE,"E4.sketch_text.stroke-124"),sQuery(id+"F3.wireOp",EDGE,"E4.sketch_text.stroke-125"),sQuery(id+"F3.wireOp",EDGE,"E4.sketch_text.stroke-126"),sQuery(id+"F3.wireOp",EDGE,"E4.sketch_text.stroke-127"),sQuery(id+"F3.wireOp",EDGE,"E4.sketch_text.stroke-128"),sQuery(id+"F3.wireOp",EDGE,"E4.sketch_text.stroke-129"),sQuery(id+"F3.wireOp",EDGE,"E4.sketch_text.stroke-130"),sQuery(id+"F3.wireOp",EDGE,"E4.sketch_text.stroke-131"),sQuery(id+"F3.wireOp",EDGE,"E4.sketch_text.stroke-132"),sQuery(id+"F3.wireOp",EDGE,"E4.sketch_text.stroke-133"),sQuery(id+"F3.wireOp",EDGE,"E4.sketch_text.stroke-134"),sQuery(id+"F3.wireOp",EDGE,"E4.sketch_text.stroke-135"),sQuery(id+"F3.wireOp",EDGE,"E4.sketch_text.stroke-136"),sQuery(id+"F3.wireOp",EDGE,"E4.sketch_text.stroke-137"),sQuery(id+"F3.wireOp",EDGE,"E4.sketch_text.stroke-138"),sQuery(id+"F3.wireOp",EDGE,"E4.sketch_text.stroke-139"),sQuery(id+"F3.wireOp",EDGE,"E4.sketch_text.stroke-140"),sQuery(id+"F3.wireOp",EDGE,"E4.sketch_text.stroke-141"),sQuery(id+"F3.wireOp",EDGE,"E4.sketch_text.stroke-142"),sQuery(id+"F3.wireOp",EDGE,"E4.sketch_text.stroke-143"),sQuery(id+"F3.wireOp",EDGE,"E4.sketch_text.stroke-144"),sQuery(id+"F3.wireOp",EDGE,"E4.sketch_text.stroke-145"),sQuery(id+"F3.wireOp",EDGE,"E4.sketch_text.stroke-146"),sQuery(id+"F3.wireOp",EDGE,"E4.sketch_text.stroke-147"),sQuery(id+"F3.wireOp",EDGE,"E4.sketch_text.stroke-148"),sQuery(id+"F3.wireOp",EDGE,"E4.sketch_text.stroke-149"),sQuery(id+"F3.wireOp",EDGE,"E4.sketch_text.stroke-150"),sQuery(id+"F3.wireOp",EDGE,"E4.sketch_text.stroke-151"),sQuery(id+"F3.wireOp",EDGE,"E4.sketch_text.stroke-152"),sQuery(id+"F3.wireOp",EDGE,"E4.sketch_text.stroke-153"),sQuery(id+"F3.wireOp",EDGE,"E4.sketch_text.stroke-159"),sQuery(id+"F3.wireOp",EDGE,"E4.sketch_text.stroke-160"),sQuery(id+"F3.wireOp",EDGE,"E4.sketch_text.stroke-161"),sQuery(id+"F3.wireOp",EDGE,"E4.sketch_text.stroke-162"),sQuery(id+"F3.wireOp",EDGE,"E4.sketch_text.stroke-163"),sQuery(id+"F3.wireOp",EDGE,"E4.sketch_text.stroke-164"),sQuery(id+"F3.wireOp",EDGE,"E4.sketch_text.stroke-165"),sQuery(id+"F3.wireOp",EDGE,"E4.sketch_text.stroke-166"),sQuery(id+"F3.wireOp",EDGE,"E4.sketch_text.stroke-167"),sQuery(id+"F3.wireOp",EDGE,"E4.sketch_text.stroke-168"),sQuery(id+"F3.wireOp",EDGE,"E4.sketch_text.stroke-169"),sQuery(id+"F3.wireOp",EDGE,"E4.sketch_text.stroke-170"),sQuery(id+"F3.wireOp",EDGE,"E4.sketch_text.stroke-171"),sQuery(id+"F3.wireOp",EDGE,"E4.sketch_text.stroke-172"),sQuery(id+"F3.wireOp",EDGE,"E4.sketch_text.stroke-173"),sQuery(id+"F3.wireOp",EDGE,"E4.sketch_text.stroke-174"),sQuery(id+"F3.wireOp",EDGE,"E4.sketch_text.stroke-175"),sQuery(id+"F3.wireOp",EDGE,"E4.sketch_text.stroke-176"),sQuery(id+"F3.wireOp",EDGE,"E4.sketch_text.stroke-177"),sQuery(id+"F3.wireOp",EDGE,"E4.sketch_text.stroke-178"),sQuery(id+"F3.wireOp",EDGE,"E4.sketch_text.stroke-179"),sQuery(id+"F3.wireOp",EDGE,"E4.sketch_text.stroke-180"),subQ0,subQ2])],"isStart":true}),makeQuery(id+"F5.opExtrude","SWEPT_FACE",FACE,{"disambiguationData":[OSD([subQ2])]})])],"derivedFrom":makeQuery(id+"F5.opExtrude","CAP_EDGE",EDGE,{"disambiguationData":[OSD([subQ2])],"isStart":true})});}
            var Q16;
            {var subQ0=sQuery(id+"F0.wireOp",EDGE,"E0.top");var subQ1=sQuery(id+"F0.wireOp",EDGE,"E0.bottom");var subQ2=sQuery(id+"F4.wireOp",EDGE,"727ac2c1-f511-4829-95a7-a443ef16a4cd");Q16=makeQuery(id+"F5.boolean.opBoolean","SPLIT",EDGE,{"disambiguationData":[TD([makeQuery(id+"F1.opExtrude","CAP_FACE",FACE,{"disambiguationData":[OSD([subQ1,subQ0,sQuery(id+"F0.wireOp",EDGE,"E0.left"),sQuery(id+"F0.wireOp",EDGE,"E0.right")])],"isStart":false}),makeQuery(id+"F1.opExtrude","SWEPT_FACE",FACE,{"disambiguationData":[OSD([subQ0])]}),makeQuery(id+"F5.opExtrude","CAP_FACE",FACE,{"disambiguationData":[OSD([subQ1,sQuery(id+"F2.wireOp",EDGE,"E2.sketch_text.stroke-0"),sQuery(id+"F2.wireOp",EDGE,"E2.sketch_text.stroke-1"),sQuery(id+"F2.wireOp",EDGE,"E2.sketch_text.stroke-2"),sQuery(id+"F2.wireOp",EDGE,"E2.sketch_text.stroke-3"),sQuery(id+"F2.wireOp",EDGE,"E2.sketch_text.stroke-4"),sQuery(id+"F2.wireOp",EDGE,"E2.sketch_text.stroke-5"),sQuery(id+"F2.wireOp",EDGE,"E2.sketch_text.stroke-6"),sQuery(id+"F2.wireOp",EDGE,"E2.sketch_text.stroke-7"),sQuery(id+"F2.wireOp",EDGE,"E2.sketch_text.stroke-8"),sQuery(id+"F2.wireOp",EDGE,"E2.sketch_text.stroke-9"),sQuery(id+"F2.wireOp",EDGE,"E2.sketch_text.stroke-10"),sQuery(id+"F2.wireOp",EDGE,"E2.sketch_text.stroke-11"),sQuery(id+"F2.wireOp",EDGE,"E2.sketch_text.stroke-12"),sQuery(id+"F2.wireOp",EDGE,"E2.sketch_text.stroke-13"),sQuery(id+"F2.wireOp",EDGE,"E2.sketch_text.stroke-14"),sQuery(id+"F2.wireOp",EDGE,"E2.sketch_text.stroke-15"),sQuery(id+"F2.wireOp",EDGE,"E2.sketch_text.stroke-16"),sQuery(id+"F2.wireOp",EDGE,"E2.sketch_text.stroke-17"),sQuery(id+"F2.wireOp",EDGE,"E2.sketch_text.stroke-18"),sQuery(id+"F2.wireOp",EDGE,"E2.sketch_text.stroke-19"),sQuery(id+"F2.wireOp",EDGE,"E2.sketch_text.stroke-20"),sQuery(id+"F2.wireOp",EDGE,"E2.sketch_text.stroke-21"),sQuery(id+"F2.wireOp",EDGE,"E2.sketch_text.stroke-22"),sQuery(id+"F2.wireOp",EDGE,"E2.sketch_text.stroke-23"),sQuery(id+"F2.wireOp",EDGE,"E2.sketch_text.stroke-24"),sQuery(id+"F2.wireOp",EDGE,"E2.sketch_text.stroke-25"),sQuery(id+"F2.wireOp",EDGE,"E2.sketch_text.stroke-26"),sQuery(id+"F2.wireOp",EDGE,"E2.sketch_text.stroke-27"),sQuery(id+"F2.wireOp",EDGE,"E2.sketch_text.stroke-28"),sQuery(id+"F2.wireOp",EDGE,"E2.sketch_text.stroke-29"),sQuery(id+"F2.wireOp",EDGE,"E2.sketch_text.stroke-30"),sQuery(id+"F2.wireOp",EDGE,"E2.sketch_text.stroke-31"),sQuery(id+"F2.wireOp",EDGE,"E2.sketch_text.stroke-32"),sQuery(id+"F2.wireOp",EDGE,"E2.sketch_text.stroke-33"),sQuery(id+"F2.wireOp",EDGE,"E2.sketch_text.stroke-34"),sQuery(id+"F2.wireOp",EDGE,"E2.sketch_text.stroke-35"),sQuery(id+"F2.wireOp",EDGE,"E2.sketch_text.stroke-36"),sQuery(id+"F2.wireOp",EDGE,"E2.sketch_text.stroke-37"),sQuery(id+"F2.wireOp",EDGE,"E2.sketch_text.stroke-38"),sQuery(id+"F2.wireOp",EDGE,"E2.sketch_text.stroke-39"),sQuery(id+"F2.wireOp",EDGE,"E2.sketch_text.stroke-40"),sQuery(id+"F2.wireOp",EDGE,"E2.sketch_text.stroke-41"),sQuery(id+"F2.wireOp",EDGE,"E2.sketch_text.stroke-42"),sQuery(id+"F2.wireOp",EDGE,"E2.sketch_text.stroke-43"),sQuery(id+"F2.wireOp",EDGE,"E2.sketch_text.stroke-44"),sQuery(id+"F2.wireOp",EDGE,"E2.sketch_text.stroke-45"),sQuery(id+"F2.wireOp",EDGE,"E2.sketch_text.stroke-46"),sQuery(id+"F2.wireOp",EDGE,"E2.sketch_text.stroke-47"),sQuery(id+"F2.wireOp",EDGE,"E2.sketch_text.stroke-48"),sQuery(id+"F2.wireOp",EDGE,"E2.sketch_text.stroke-49"),sQuery(id+"F2.wireOp",EDGE,"E2.sketch_text.stroke-50"),sQuery(id+"F2.wireOp",EDGE,"E2.sketch_text.stroke-51"),sQuery(id+"F2.wireOp",EDGE,"E2.sketch_text.stroke-52"),sQuery(id+"F2.wireOp",EDGE,"E2.sketch_text.stroke-53"),sQuery(id+"F2.wireOp",EDGE,"E2.sketch_text.stroke-54"),sQuery(id+"F2.wireOp",EDGE,"E2.sketch_text.stroke-55"),sQuery(id+"F2.wireOp",EDGE,"E2.sketch_text.stroke-56"),sQuery(id+"F2.wireOp",EDGE,"E2.sketch_text.stroke-57"),sQuery(id+"F2.wireOp",EDGE,"E2.sketch_text.stroke-58"),sQuery(id+"F2.wireOp",EDGE,"E2.sketch_text.stroke-59"),sQuery(id+"F2.wireOp",EDGE,"E2.sketch_text.stroke-60"),sQuery(id+"F2.wireOp",EDGE,"E2.sketch_text.stroke-61"),sQuery(id+"F2.wireOp",EDGE,"E2.sketch_text.stroke-62"),sQuery(id+"F2.wireOp",EDGE,"E2.sketch_text.stroke-63"),sQuery(id+"F2.wireOp",EDGE,"E2.sketch_text.stroke-64"),sQuery(id+"F2.wireOp",EDGE,"E2.sketch_text.stroke-65"),sQuery(id+"F2.wireOp",EDGE,"E2.sketch_text.stroke-66"),sQuery(id+"F2.wireOp",EDGE,"E2.sketch_text.stroke-67"),sQuery(id+"F2.wireOp",EDGE,"E2.sketch_text.stroke-68"),sQuery(id+"F2.wireOp",EDGE,"E2.sketch_text.stroke-69"),sQuery(id+"F2.wireOp",EDGE,"E2.sketch_text.stroke-70"),sQuery(id+"F2.wireOp",EDGE,"E2.sketch_text.stroke-71"),sQuery(id+"F2.wireOp",EDGE,"E2.sketch_text.stroke-72"),sQuery(id+"F2.wireOp",EDGE,"E2.sketch_text.stroke-73"),sQuery(id+"F2.wireOp",EDGE,"E2.sketch_text.stroke-74"),sQuery(id+"F2.wireOp",EDGE,"E2.sketch_text.stroke-75"),sQuery(id+"F2.wireOp",EDGE,"E2.sketch_text.stroke-76"),sQuery(id+"F2.wireOp",EDGE,"E2.sketch_text.stroke-77"),sQuery(id+"F2.wireOp",EDGE,"E2.sketch_text.stroke-78"),sQuery(id+"F2.wireOp",EDGE,"E2.sketch_text.stroke-79"),sQuery(id+"F2.wireOp",EDGE,"E2.sketch_text.stroke-80"),sQuery(id+"F2.wireOp",EDGE,"E2.sketch_text.stroke-81"),sQuery(id+"F2.wireOp",EDGE,"E2.sketch_text.stroke-82"),sQuery(id+"F2.wireOp",EDGE,"E2.sketch_text.stroke-83"),sQuery(id+"F2.wireOp",EDGE,"E2.sketch_text.stroke-84"),sQuery(id+"F2.wireOp",EDGE,"E2.sketch_text.stroke-85"),sQuery(id+"F2.wireOp",EDGE,"E2.sketch_text.stroke-86"),sQuery(id+"F2.wireOp",EDGE,"E2.sketch_text.stroke-87"),sQuery(id+"F2.wireOp",EDGE,"E2.sketch_text.stroke-88"),sQuery(id+"F2.wireOp",EDGE,"E2.sketch_text.stroke-89"),sQuery(id+"F2.wireOp",EDGE,"E2.sketch_text.stroke-90"),sQuery(id+"F2.wireOp",EDGE,"E2.sketch_text.stroke-91"),sQuery(id+"F2.wireOp",EDGE,"E2.sketch_text.stroke-92"),sQuery(id+"F2.wireOp",EDGE,"E2.sketch_text.stroke-93"),sQuery(id+"F2.wireOp",EDGE,"E2.sketch_text.stroke-94"),sQuery(id+"F2.wireOp",EDGE,"E2.sketch_text.stroke-95"),sQuery(id+"F2.wireOp",EDGE,"E2.sketch_text.stroke-96"),sQuery(id+"F2.wireOp",EDGE,"E2.sketch_text.stroke-97"),sQuery(id+"F2.wireOp",EDGE,"E2.sketch_text.stroke-98"),sQuery(id+"F2.wireOp",EDGE,"E2.sketch_text.stroke-99"),sQuery(id+"F2.wireOp",EDGE,"E2.sketch_text.stroke-100"),sQuery(id+"F2.wireOp",EDGE,"E2.sketch_text.stroke-101"),sQuery(id+"F2.wireOp",EDGE,"E2.sketch_text.stroke-102"),sQuery(id+"F2.wireOp",EDGE,"E2.sketch_text.stroke-103"),sQuery(id+"F2.wireOp",EDGE,"E2.sketch_text.stroke-104"),sQuery(id+"F2.wireOp",EDGE,"E2.sketch_text.stroke-105"),sQuery(id+"F2.wireOp",EDGE,"E2.sketch_text.stroke-106"),sQuery(id+"F2.wireOp",EDGE,"E2.sketch_text.stroke-107"),sQuery(id+"F2.wireOp",EDGE,"E2.sketch_text.stroke-108"),sQuery(id+"F2.wireOp",EDGE,"E2.sketch_text.stroke-109"),sQuery(id+"F2.wireOp",EDGE,"E2.sketch_text.stroke-110"),sQuery(id+"F2.wireOp",EDGE,"E2.sketch_text.stroke-111"),sQuery(id+"F2.wireOp",EDGE,"E2.sketch_text.stroke-112"),sQuery(id+"F2.wireOp",EDGE,"E2.sketch_text.stroke-113"),sQuery(id+"F2.wireOp",EDGE,"E2.sketch_text.stroke-114"),sQuery(id+"F2.wireOp",EDGE,"E2.sketch_text.stroke-115"),sQuery(id+"F2.wireOp",EDGE,"E2.sketch_text.stroke-116"),sQuery(id+"F2.wireOp",EDGE,"E2.sketch_text.stroke-117"),sQuery(id+"F2.wireOp",EDGE,"E2.sketch_text.stroke-118"),sQuery(id+"F2.wireOp",EDGE,"E2.sketch_text.stroke-119"),sQuery(id+"F2.wireOp",EDGE,"E2.sketch_text.stroke-120"),sQuery(id+"F2.wireOp",EDGE,"E2.sketch_text.stroke-121"),sQuery(id+"F2.wireOp",EDGE,"E2.sketch_text.stroke-122"),sQuery(id+"F2.wireOp",EDGE,"E2.sketch_text.stroke-123"),sQuery(id+"F2.wireOp",EDGE,"E2.sketch_text.stroke-124"),sQuery(id+"F2.wireOp",EDGE,"E2.sketch_text.stroke-125"),sQuery(id+"F2.wireOp",EDGE,"E2.sketch_text.stroke-126"),sQuery(id+"F2.wireOp",EDGE,"E2.sketch_text.stroke-127"),sQuery(id+"F2.wireOp",EDGE,"E2.sketch_text.stroke-128"),sQuery(id+"F2.wireOp",EDGE,"E2.sketch_text.stroke-129"),sQuery(id+"F2.wireOp",EDGE,"E2.sketch_text.stroke-130"),sQuery(id+"F2.wireOp",EDGE,"E2.sketch_text.stroke-131"),sQuery(id+"F2.wireOp",EDGE,"E2.sketch_text.stroke-132"),sQuery(id+"F2.wireOp",EDGE,"E2.sketch_text.stroke-133"),sQuery(id+"F2.wireOp",EDGE,"E2.sketch_text.stroke-134"),sQuery(id+"F2.wireOp",EDGE,"E2.sketch_text.stroke-135"),sQuery(id+"F2.wireOp",EDGE,"E2.sketch_text.stroke-136"),sQuery(id+"F2.wireOp",EDGE,"E2.sketch_text.stroke-137"),sQuery(id+"F2.wireOp",EDGE,"E2.sketch_text.stroke-138"),sQuery(id+"F2.wireOp",EDGE,"E2.sketch_text.stroke-139"),sQuery(id+"F2.wireOp",EDGE,"E2.sketch_text.stroke-140"),sQuery(id+"F2.wireOp",EDGE,"E2.sketch_text.stroke-141"),sQuery(id+"F2.wireOp",EDGE,"E2.sketch_text.stroke-142"),sQuery(id+"F2.wireOp",EDGE,"E2.sketch_text.stroke-143"),sQuery(id+"F2.wireOp",EDGE,"E2.sketch_text.stroke-144"),sQuery(id+"F2.wireOp",EDGE,"E2.sketch_text.stroke-145"),sQuery(id+"F2.wireOp",EDGE,"E2.sketch_text.stroke-146"),sQuery(id+"F2.wireOp",EDGE,"E2.sketch_text.stroke-147"),sQuery(id+"F2.wireOp",EDGE,"E2.sketch_text.stroke-148"),sQuery(id+"F2.wireOp",EDGE,"E2.sketch_text.stroke-149"),sQuery(id+"F2.wireOp",EDGE,"E2.sketch_text.stroke-150"),sQuery(id+"F2.wireOp",EDGE,"E2.sketch_text.stroke-151"),sQuery(id+"F2.wireOp",EDGE,"E2.sketch_text.stroke-152"),sQuery(id+"F2.wireOp",EDGE,"E2.sketch_text.stroke-153"),sQuery(id+"F2.wireOp",EDGE,"E2.sketch_text.stroke-154"),sQuery(id+"F2.wireOp",EDGE,"E2.sketch_text.stroke-155"),sQuery(id+"F2.wireOp",EDGE,"E2.sketch_text.stroke-156"),sQuery(id+"F2.wireOp",EDGE,"E2.sketch_text.stroke-157"),sQuery(id+"F2.wireOp",EDGE,"E2.sketch_text.stroke-158"),sQuery(id+"F2.wireOp",EDGE,"E2.sketch_text.stroke-159"),sQuery(id+"F2.wireOp",EDGE,"E2.sketch_text.stroke-160"),sQuery(id+"F2.wireOp",EDGE,"E2.sketch_text.stroke-161"),sQuery(id+"F2.wireOp",EDGE,"E2.sketch_text.stroke-162"),sQuery(id+"F2.wireOp",EDGE,"E2.sketch_text.stroke-163"),sQuery(id+"F2.wireOp",EDGE,"E2.sketch_text.stroke-164"),sQuery(id+"F2.wireOp",EDGE,"E2.sketch_text.stroke-165"),sQuery(id+"F2.wireOp",EDGE,"E2.sketch_text.stroke-166"),sQuery(id+"F2.wireOp",EDGE,"E2.sketch_text.stroke-167"),sQuery(id+"F2.wireOp",EDGE,"E2.sketch_text.stroke-168"),sQuery(id+"F2.wireOp",EDGE,"E2.sketch_text.stroke-169"),sQuery(id+"F2.wireOp",EDGE,"E2.sketch_text.stroke-170"),sQuery(id+"F2.wireOp",EDGE,"E2.sketch_text.stroke-171"),sQuery(id+"F2.wireOp",EDGE,"E2.sketch_text.stroke-172"),sQuery(id+"F2.wireOp",EDGE,"E2.sketch_text.stroke-173"),sQuery(id+"F3.wireOp",EDGE,"E4.sketch_text.stroke-0"),sQuery(id+"F3.wireOp",EDGE,"E4.sketch_text.stroke-1"),sQuery(id+"F3.wireOp",EDGE,"E4.sketch_text.stroke-2"),sQuery(id+"F3.wireOp",EDGE,"E4.sketch_text.stroke-3"),sQuery(id+"F3.wireOp",EDGE,"E4.sketch_text.stroke-4"),sQuery(id+"F3.wireOp",EDGE,"E4.sketch_text.stroke-5"),sQuery(id+"F3.wireOp",EDGE,"E4.sketch_text.stroke-6"),sQuery(id+"F3.wireOp",EDGE,"E4.sketch_text.stroke-7"),sQuery(id+"F3.wireOp",EDGE,"E4.sketch_text.stroke-8"),sQuery(id+"F3.wireOp",EDGE,"E4.sketch_text.stroke-9"),sQuery(id+"F3.wireOp",EDGE,"E4.sketch_text.stroke-10"),sQuery(id+"F3.wireOp",EDGE,"E4.sketch_text.stroke-11"),sQuery(id+"F3.wireOp",EDGE,"E4.sketch_text.stroke-12"),sQuery(id+"F3.wireOp",EDGE,"E4.sketch_text.stroke-13"),sQuery(id+"F3.wireOp",EDGE,"E4.sketch_text.stroke-14"),sQuery(id+"F3.wireOp",EDGE,"E4.sketch_text.stroke-15"),sQuery(id+"F3.wireOp",EDGE,"E4.sketch_text.stroke-16"),sQuery(id+"F3.wireOp",EDGE,"E4.sketch_text.stroke-17"),sQuery(id+"F3.wireOp",EDGE,"E4.sketch_text.stroke-18"),sQuery(id+"F3.wireOp",EDGE,"E4.sketch_text.stroke-19"),sQuery(id+"F3.wireOp",EDGE,"E4.sketch_text.stroke-20"),sQuery(id+"F3.wireOp",EDGE,"E4.sketch_text.stroke-21"),sQuery(id+"F3.wireOp",EDGE,"E4.sketch_text.stroke-22"),sQuery(id+"F3.wireOp",EDGE,"E4.sketch_text.stroke-23"),sQuery(id+"F3.wireOp",EDGE,"E4.sketch_text.stroke-24"),sQuery(id+"F3.wireOp",EDGE,"E4.sketch_text.stroke-25"),sQuery(id+"F3.wireOp",EDGE,"E4.sketch_text.stroke-26"),sQuery(id+"F3.wireOp",EDGE,"E4.sketch_text.stroke-27"),sQuery(id+"F3.wireOp",EDGE,"E4.sketch_text.stroke-28"),sQuery(id+"F3.wireOp",EDGE,"E4.sketch_text.stroke-29"),sQuery(id+"F3.wireOp",EDGE,"E4.sketch_text.stroke-30"),sQuery(id+"F3.wireOp",EDGE,"E4.sketch_text.stroke-31"),sQuery(id+"F3.wireOp",EDGE,"E4.sketch_text.stroke-32"),sQuery(id+"F3.wireOp",EDGE,"E4.sketch_text.stroke-33"),sQuery(id+"F3.wireOp",EDGE,"E4.sketch_text.stroke-34"),sQuery(id+"F3.wireOp",EDGE,"E4.sketch_text.stroke-35"),sQuery(id+"F3.wireOp",EDGE,"E4.sketch_text.stroke-36"),sQuery(id+"F3.wireOp",EDGE,"E4.sketch_text.stroke-37"),sQuery(id+"F3.wireOp",EDGE,"E4.sketch_text.stroke-38"),sQuery(id+"F3.wireOp",EDGE,"E4.sketch_text.stroke-39"),sQuery(id+"F3.wireOp",EDGE,"E4.sketch_text.stroke-40"),sQuery(id+"F3.wireOp",EDGE,"E4.sketch_text.stroke-41"),sQuery(id+"F3.wireOp",EDGE,"E4.sketch_text.stroke-42"),sQuery(id+"F3.wireOp",EDGE,"E4.sketch_text.stroke-43"),sQuery(id+"F3.wireOp",EDGE,"E4.sketch_text.stroke-44"),sQuery(id+"F3.wireOp",EDGE,"E4.sketch_text.stroke-45"),sQuery(id+"F3.wireOp",EDGE,"E4.sketch_text.stroke-46"),sQuery(id+"F3.wireOp",EDGE,"E4.sketch_text.stroke-47"),sQuery(id+"F3.wireOp",EDGE,"E4.sketch_text.stroke-48"),sQuery(id+"F3.wireOp",EDGE,"E4.sketch_text.stroke-49"),sQuery(id+"F3.wireOp",EDGE,"E4.sketch_text.stroke-50"),sQuery(id+"F3.wireOp",EDGE,"E4.sketch_text.stroke-51"),sQuery(id+"F3.wireOp",EDGE,"E4.sketch_text.stroke-52"),sQuery(id+"F3.wireOp",EDGE,"E4.sketch_text.stroke-53"),sQuery(id+"F3.wireOp",EDGE,"E4.sketch_text.stroke-54"),sQuery(id+"F3.wireOp",EDGE,"E4.sketch_text.stroke-55"),sQuery(id+"F3.wireOp",EDGE,"E4.sketch_text.stroke-56"),sQuery(id+"F3.wireOp",EDGE,"E4.sketch_text.stroke-57"),sQuery(id+"F3.wireOp",EDGE,"E4.sketch_text.stroke-58"),sQuery(id+"F3.wireOp",EDGE,"E4.sketch_text.stroke-59"),sQuery(id+"F3.wireOp",EDGE,"E4.sketch_text.stroke-60"),sQuery(id+"F3.wireOp",EDGE,"E4.sketch_text.stroke-61"),sQuery(id+"F3.wireOp",EDGE,"E4.sketch_text.stroke-62"),sQuery(id+"F3.wireOp",EDGE,"E4.sketch_text.stroke-71"),sQuery(id+"F3.wireOp",EDGE,"E4.sketch_text.stroke-72"),sQuery(id+"F3.wireOp",EDGE,"E4.sketch_text.stroke-73"),sQuery(id+"F3.wireOp",EDGE,"E4.sketch_text.stroke-74"),sQuery(id+"F3.wireOp",EDGE,"E4.sketch_text.stroke-75"),sQuery(id+"F3.wireOp",EDGE,"E4.sketch_text.stroke-76"),sQuery(id+"F3.wireOp",EDGE,"E4.sketch_text.stroke-77"),sQuery(id+"F3.wireOp",EDGE,"E4.sketch_text.stroke-78"),sQuery(id+"F3.wireOp",EDGE,"E4.sketch_text.stroke-79"),sQuery(id+"F3.wireOp",EDGE,"E4.sketch_text.stroke-80"),sQuery(id+"F3.wireOp",EDGE,"E4.sketch_text.stroke-81"),sQuery(id+"F3.wireOp",EDGE,"E4.sketch_text.stroke-82"),sQuery(id+"F3.wireOp",EDGE,"E4.sketch_text.stroke-83"),sQuery(id+"F3.wireOp",EDGE,"E4.sketch_text.stroke-84"),sQuery(id+"F3.wireOp",EDGE,"E4.sketch_text.stroke-85"),sQuery(id+"F3.wireOp",EDGE,"E4.sketch_text.stroke-86"),sQuery(id+"F3.wireOp",EDGE,"E4.sketch_text.stroke-87"),sQuery(id+"F3.wireOp",EDGE,"E4.sketch_text.stroke-88"),sQuery(id+"F3.wireOp",EDGE,"E4.sketch_text.stroke-89"),sQuery(id+"F3.wireOp",EDGE,"E4.sketch_text.stroke-90"),sQuery(id+"F3.wireOp",EDGE,"E4.sketch_text.stroke-91"),sQuery(id+"F3.wireOp",EDGE,"E4.sketch_text.stroke-92"),sQuery(id+"F3.wireOp",EDGE,"E4.sketch_text.stroke-93"),sQuery(id+"F3.wireOp",EDGE,"E4.sketch_text.stroke-94"),sQuery(id+"F3.wireOp",EDGE,"E4.sketch_text.stroke-95"),sQuery(id+"F3.wireOp",EDGE,"E4.sketch_text.stroke-96"),sQuery(id+"F3.wireOp",EDGE,"E4.sketch_text.stroke-97"),sQuery(id+"F3.wireOp",EDGE,"E4.sketch_text.stroke-103"),sQuery(id+"F3.wireOp",EDGE,"E4.sketch_text.stroke-104"),sQuery(id+"F3.wireOp",EDGE,"E4.sketch_text.stroke-105"),sQuery(id+"F3.wireOp",EDGE,"E4.sketch_text.stroke-106"),sQuery(id+"F3.wireOp",EDGE,"E4.sketch_text.stroke-107"),sQuery(id+"F3.wireOp",EDGE,"E4.sketch_text.stroke-108"),sQuery(id+"F3.wireOp",EDGE,"E4.sketch_text.stroke-109"),sQuery(id+"F3.wireOp",EDGE,"E4.sketch_text.stroke-110"),sQuery(id+"F3.wireOp",EDGE,"E4.sketch_text.stroke-111"),sQuery(id+"F3.wireOp",EDGE,"E4.sketch_text.stroke-112"),sQuery(id+"F3.wireOp",EDGE,"E4.sketch_text.stroke-113"),sQuery(id+"F3.wireOp",EDGE,"E4.sketch_text.stroke-114"),sQuery(id+"F3.wireOp",EDGE,"E4.sketch_text.stroke-115"),sQuery(id+"F3.wireOp",EDGE,"E4.sketch_text.stroke-116"),sQuery(id+"F3.wireOp",EDGE,"E4.sketch_text.stroke-117"),sQuery(id+"F3.wireOp",EDGE,"E4.sketch_text.stroke-118"),sQuery(id+"F3.wireOp",EDGE,"E4.sketch_text.stroke-119"),sQuery(id+"F3.wireOp",EDGE,"E4.sketch_text.stroke-120"),sQuery(id+"F3.wireOp",EDGE,"E4.sketch_text.stroke-121"),sQuery(id+"F3.wireOp",EDGE,"E4.sketch_text.stroke-122"),sQuery(id+"F3.wireOp",EDGE,"E4.sketch_text.stroke-123"),sQuery(id+"F3.wireOp",EDGE,"E4.sketch_text.stroke-124"),sQuery(id+"F3.wireOp",EDGE,"E4.sketch_text.stroke-125"),sQuery(id+"F3.wireOp",EDGE,"E4.sketch_text.stroke-126"),sQuery(id+"F3.wireOp",EDGE,"E4.sketch_text.stroke-127"),sQuery(id+"F3.wireOp",EDGE,"E4.sketch_text.stroke-128"),sQuery(id+"F3.wireOp",EDGE,"E4.sketch_text.stroke-129"),sQuery(id+"F3.wireOp",EDGE,"E4.sketch_text.stroke-130"),sQuery(id+"F3.wireOp",EDGE,"E4.sketch_text.stroke-131"),sQuery(id+"F3.wireOp",EDGE,"E4.sketch_text.stroke-132"),sQuery(id+"F3.wireOp",EDGE,"E4.sketch_text.stroke-133"),sQuery(id+"F3.wireOp",EDGE,"E4.sketch_text.stroke-134"),sQuery(id+"F3.wireOp",EDGE,"E4.sketch_text.stroke-135"),sQuery(id+"F3.wireOp",EDGE,"E4.sketch_text.stroke-136"),sQuery(id+"F3.wireOp",EDGE,"E4.sketch_text.stroke-137"),sQuery(id+"F3.wireOp",EDGE,"E4.sketch_text.stroke-138"),sQuery(id+"F3.wireOp",EDGE,"E4.sketch_text.stroke-139"),sQuery(id+"F3.wireOp",EDGE,"E4.sketch_text.stroke-140"),sQuery(id+"F3.wireOp",EDGE,"E4.sketch_text.stroke-141"),sQuery(id+"F3.wireOp",EDGE,"E4.sketch_text.stroke-142"),sQuery(id+"F3.wireOp",EDGE,"E4.sketch_text.stroke-143"),sQuery(id+"F3.wireOp",EDGE,"E4.sketch_text.stroke-144"),sQuery(id+"F3.wireOp",EDGE,"E4.sketch_text.stroke-145"),sQuery(id+"F3.wireOp",EDGE,"E4.sketch_text.stroke-146"),sQuery(id+"F3.wireOp",EDGE,"E4.sketch_text.stroke-147"),sQuery(id+"F3.wireOp",EDGE,"E4.sketch_text.stroke-148"),sQuery(id+"F3.wireOp",EDGE,"E4.sketch_text.stroke-149"),sQuery(id+"F3.wireOp",EDGE,"E4.sketch_text.stroke-150"),sQuery(id+"F3.wireOp",EDGE,"E4.sketch_text.stroke-151"),sQuery(id+"F3.wireOp",EDGE,"E4.sketch_text.stroke-152"),sQuery(id+"F3.wireOp",EDGE,"E4.sketch_text.stroke-153"),sQuery(id+"F3.wireOp",EDGE,"E4.sketch_text.stroke-159"),sQuery(id+"F3.wireOp",EDGE,"E4.sketch_text.stroke-160"),sQuery(id+"F3.wireOp",EDGE,"E4.sketch_text.stroke-161"),sQuery(id+"F3.wireOp",EDGE,"E4.sketch_text.stroke-162"),sQuery(id+"F3.wireOp",EDGE,"E4.sketch_text.stroke-163"),sQuery(id+"F3.wireOp",EDGE,"E4.sketch_text.stroke-164"),sQuery(id+"F3.wireOp",EDGE,"E4.sketch_text.stroke-165"),sQuery(id+"F3.wireOp",EDGE,"E4.sketch_text.stroke-166"),sQuery(id+"F3.wireOp",EDGE,"E4.sketch_text.stroke-167"),sQuery(id+"F3.wireOp",EDGE,"E4.sketch_text.stroke-168"),sQuery(id+"F3.wireOp",EDGE,"E4.sketch_text.stroke-169"),sQuery(id+"F3.wireOp",EDGE,"E4.sketch_text.stroke-170"),sQuery(id+"F3.wireOp",EDGE,"E4.sketch_text.stroke-171"),sQuery(id+"F3.wireOp",EDGE,"E4.sketch_text.stroke-172"),sQuery(id+"F3.wireOp",EDGE,"E4.sketch_text.stroke-173"),sQuery(id+"F3.wireOp",EDGE,"E4.sketch_text.stroke-174"),sQuery(id+"F3.wireOp",EDGE,"E4.sketch_text.stroke-175"),sQuery(id+"F3.wireOp",EDGE,"E4.sketch_text.stroke-176"),sQuery(id+"F3.wireOp",EDGE,"E4.sketch_text.stroke-177"),sQuery(id+"F3.wireOp",EDGE,"E4.sketch_text.stroke-178"),sQuery(id+"F3.wireOp",EDGE,"E4.sketch_text.stroke-179"),sQuery(id+"F3.wireOp",EDGE,"E4.sketch_text.stroke-180"),sQuery(id+"F4.wireOp",EDGE,"8007402e-1a4e-4a06-85a5-2af08e553504"),subQ2])],"isStart":true}),makeQuery(id+"F5.opExtrude","SWEPT_FACE",FACE,{"disambiguationData":[OSD([subQ2])]})]),OD(0.0)],"derivedFrom":makeQuery(id+"F1.opExtrude","CAP_EDGE",EDGE,{"disambiguationData":[OSD([subQ0])],"isStart":false})});}
            var Q17;
            {var subQ0=sQuery(id+"F0.wireOp",EDGE,"E0.top");var subQ1=sQuery(id+"F0.wireOp",EDGE,"E0.bottom");var subQ2=sQuery(id+"F4.wireOp",EDGE,"1a034e28-a7c2-419d-97de-c33d70a47301");Q17=makeQuery(id+"F5.boolean.opBoolean","SPLIT",EDGE,{"disambiguationData":[TD([makeQuery(id+"F1.opExtrude","CAP_FACE",FACE,{"disambiguationData":[OSD([subQ1,subQ0,sQuery(id+"F0.wireOp",EDGE,"E0.left"),sQuery(id+"F0.wireOp",EDGE,"E0.right")])],"isStart":false}),makeQuery(id+"F1.opExtrude","SWEPT_FACE",FACE,{"disambiguationData":[OSD([subQ0])]}),makeQuery(id+"F5.opExtrude","CAP_FACE",FACE,{"disambiguationData":[OSD([subQ1,sQuery(id+"F2.wireOp",EDGE,"E2.sketch_text.stroke-0"),sQuery(id+"F2.wireOp",EDGE,"E2.sketch_text.stroke-1"),sQuery(id+"F2.wireOp",EDGE,"E2.sketch_text.stroke-2"),sQuery(id+"F2.wireOp",EDGE,"E2.sketch_text.stroke-3"),sQuery(id+"F2.wireOp",EDGE,"E2.sketch_text.stroke-4"),sQuery(id+"F2.wireOp",EDGE,"E2.sketch_text.stroke-5"),sQuery(id+"F2.wireOp",EDGE,"E2.sketch_text.stroke-6"),sQuery(id+"F2.wireOp",EDGE,"E2.sketch_text.stroke-7"),sQuery(id+"F2.wireOp",EDGE,"E2.sketch_text.stroke-8"),sQuery(id+"F2.wireOp",EDGE,"E2.sketch_text.stroke-9"),sQuery(id+"F2.wireOp",EDGE,"E2.sketch_text.stroke-10"),sQuery(id+"F2.wireOp",EDGE,"E2.sketch_text.stroke-11"),sQuery(id+"F2.wireOp",EDGE,"E2.sketch_text.stroke-12"),sQuery(id+"F2.wireOp",EDGE,"E2.sketch_text.stroke-13"),sQuery(id+"F2.wireOp",EDGE,"E2.sketch_text.stroke-14"),sQuery(id+"F2.wireOp",EDGE,"E2.sketch_text.stroke-15"),sQuery(id+"F2.wireOp",EDGE,"E2.sketch_text.stroke-16"),sQuery(id+"F2.wireOp",EDGE,"E2.sketch_text.stroke-17"),sQuery(id+"F2.wireOp",EDGE,"E2.sketch_text.stroke-18"),sQuery(id+"F2.wireOp",EDGE,"E2.sketch_text.stroke-19"),sQuery(id+"F2.wireOp",EDGE,"E2.sketch_text.stroke-20"),sQuery(id+"F2.wireOp",EDGE,"E2.sketch_text.stroke-21"),sQuery(id+"F2.wireOp",EDGE,"E2.sketch_text.stroke-22"),sQuery(id+"F2.wireOp",EDGE,"E2.sketch_text.stroke-23"),sQuery(id+"F2.wireOp",EDGE,"E2.sketch_text.stroke-24"),sQuery(id+"F2.wireOp",EDGE,"E2.sketch_text.stroke-25"),sQuery(id+"F2.wireOp",EDGE,"E2.sketch_text.stroke-26"),sQuery(id+"F2.wireOp",EDGE,"E2.sketch_text.stroke-27"),sQuery(id+"F2.wireOp",EDGE,"E2.sketch_text.stroke-28"),sQuery(id+"F2.wireOp",EDGE,"E2.sketch_text.stroke-29"),sQuery(id+"F2.wireOp",EDGE,"E2.sketch_text.stroke-30"),sQuery(id+"F2.wireOp",EDGE,"E2.sketch_text.stroke-31"),sQuery(id+"F2.wireOp",EDGE,"E2.sketch_text.stroke-32"),sQuery(id+"F2.wireOp",EDGE,"E2.sketch_text.stroke-33"),sQuery(id+"F2.wireOp",EDGE,"E2.sketch_text.stroke-34"),sQuery(id+"F2.wireOp",EDGE,"E2.sketch_text.stroke-35"),sQuery(id+"F2.wireOp",EDGE,"E2.sketch_text.stroke-36"),sQuery(id+"F2.wireOp",EDGE,"E2.sketch_text.stroke-37"),sQuery(id+"F2.wireOp",EDGE,"E2.sketch_text.stroke-38"),sQuery(id+"F2.wireOp",EDGE,"E2.sketch_text.stroke-39"),sQuery(id+"F2.wireOp",EDGE,"E2.sketch_text.stroke-40"),sQuery(id+"F2.wireOp",EDGE,"E2.sketch_text.stroke-41"),sQuery(id+"F2.wireOp",EDGE,"E2.sketch_text.stroke-42"),sQuery(id+"F2.wireOp",EDGE,"E2.sketch_text.stroke-43"),sQuery(id+"F2.wireOp",EDGE,"E2.sketch_text.stroke-44"),sQuery(id+"F2.wireOp",EDGE,"E2.sketch_text.stroke-45"),sQuery(id+"F2.wireOp",EDGE,"E2.sketch_text.stroke-46"),sQuery(id+"F2.wireOp",EDGE,"E2.sketch_text.stroke-47"),sQuery(id+"F2.wireOp",EDGE,"E2.sketch_text.stroke-48"),sQuery(id+"F2.wireOp",EDGE,"E2.sketch_text.stroke-49"),sQuery(id+"F2.wireOp",EDGE,"E2.sketch_text.stroke-50"),sQuery(id+"F2.wireOp",EDGE,"E2.sketch_text.stroke-51"),sQuery(id+"F2.wireOp",EDGE,"E2.sketch_text.stroke-52"),sQuery(id+"F2.wireOp",EDGE,"E2.sketch_text.stroke-53"),sQuery(id+"F2.wireOp",EDGE,"E2.sketch_text.stroke-54"),sQuery(id+"F2.wireOp",EDGE,"E2.sketch_text.stroke-55"),sQuery(id+"F2.wireOp",EDGE,"E2.sketch_text.stroke-56"),sQuery(id+"F2.wireOp",EDGE,"E2.sketch_text.stroke-57"),sQuery(id+"F2.wireOp",EDGE,"E2.sketch_text.stroke-58"),sQuery(id+"F2.wireOp",EDGE,"E2.sketch_text.stroke-59"),sQuery(id+"F2.wireOp",EDGE,"E2.sketch_text.stroke-60"),sQuery(id+"F2.wireOp",EDGE,"E2.sketch_text.stroke-61"),sQuery(id+"F2.wireOp",EDGE,"E2.sketch_text.stroke-62"),sQuery(id+"F2.wireOp",EDGE,"E2.sketch_text.stroke-63"),sQuery(id+"F2.wireOp",EDGE,"E2.sketch_text.stroke-64"),sQuery(id+"F2.wireOp",EDGE,"E2.sketch_text.stroke-65"),sQuery(id+"F2.wireOp",EDGE,"E2.sketch_text.stroke-66"),sQuery(id+"F2.wireOp",EDGE,"E2.sketch_text.stroke-67"),sQuery(id+"F2.wireOp",EDGE,"E2.sketch_text.stroke-68"),sQuery(id+"F2.wireOp",EDGE,"E2.sketch_text.stroke-69"),sQuery(id+"F2.wireOp",EDGE,"E2.sketch_text.stroke-70"),sQuery(id+"F2.wireOp",EDGE,"E2.sketch_text.stroke-71"),sQuery(id+"F2.wireOp",EDGE,"E2.sketch_text.stroke-72"),sQuery(id+"F2.wireOp",EDGE,"E2.sketch_text.stroke-73"),sQuery(id+"F2.wireOp",EDGE,"E2.sketch_text.stroke-74"),sQuery(id+"F2.wireOp",EDGE,"E2.sketch_text.stroke-75"),sQuery(id+"F2.wireOp",EDGE,"E2.sketch_text.stroke-76"),sQuery(id+"F2.wireOp",EDGE,"E2.sketch_text.stroke-77"),sQuery(id+"F2.wireOp",EDGE,"E2.sketch_text.stroke-78"),sQuery(id+"F2.wireOp",EDGE,"E2.sketch_text.stroke-79"),sQuery(id+"F2.wireOp",EDGE,"E2.sketch_text.stroke-80"),sQuery(id+"F2.wireOp",EDGE,"E2.sketch_text.stroke-81"),sQuery(id+"F2.wireOp",EDGE,"E2.sketch_text.stroke-82"),sQuery(id+"F2.wireOp",EDGE,"E2.sketch_text.stroke-83"),sQuery(id+"F2.wireOp",EDGE,"E2.sketch_text.stroke-84"),sQuery(id+"F2.wireOp",EDGE,"E2.sketch_text.stroke-85"),sQuery(id+"F2.wireOp",EDGE,"E2.sketch_text.stroke-86"),sQuery(id+"F2.wireOp",EDGE,"E2.sketch_text.stroke-87"),sQuery(id+"F2.wireOp",EDGE,"E2.sketch_text.stroke-88"),sQuery(id+"F2.wireOp",EDGE,"E2.sketch_text.stroke-89"),sQuery(id+"F2.wireOp",EDGE,"E2.sketch_text.stroke-90"),sQuery(id+"F2.wireOp",EDGE,"E2.sketch_text.stroke-91"),sQuery(id+"F2.wireOp",EDGE,"E2.sketch_text.stroke-92"),sQuery(id+"F2.wireOp",EDGE,"E2.sketch_text.stroke-93"),sQuery(id+"F2.wireOp",EDGE,"E2.sketch_text.stroke-94"),sQuery(id+"F2.wireOp",EDGE,"E2.sketch_text.stroke-95"),sQuery(id+"F2.wireOp",EDGE,"E2.sketch_text.stroke-96"),sQuery(id+"F2.wireOp",EDGE,"E2.sketch_text.stroke-97"),sQuery(id+"F2.wireOp",EDGE,"E2.sketch_text.stroke-98"),sQuery(id+"F2.wireOp",EDGE,"E2.sketch_text.stroke-99"),sQuery(id+"F2.wireOp",EDGE,"E2.sketch_text.stroke-100"),sQuery(id+"F2.wireOp",EDGE,"E2.sketch_text.stroke-101"),sQuery(id+"F2.wireOp",EDGE,"E2.sketch_text.stroke-102"),sQuery(id+"F2.wireOp",EDGE,"E2.sketch_text.stroke-103"),sQuery(id+"F2.wireOp",EDGE,"E2.sketch_text.stroke-104"),sQuery(id+"F2.wireOp",EDGE,"E2.sketch_text.stroke-105"),sQuery(id+"F2.wireOp",EDGE,"E2.sketch_text.stroke-106"),sQuery(id+"F2.wireOp",EDGE,"E2.sketch_text.stroke-107"),sQuery(id+"F2.wireOp",EDGE,"E2.sketch_text.stroke-108"),sQuery(id+"F2.wireOp",EDGE,"E2.sketch_text.stroke-109"),sQuery(id+"F2.wireOp",EDGE,"E2.sketch_text.stroke-110"),sQuery(id+"F2.wireOp",EDGE,"E2.sketch_text.stroke-111"),sQuery(id+"F2.wireOp",EDGE,"E2.sketch_text.stroke-112"),sQuery(id+"F2.wireOp",EDGE,"E2.sketch_text.stroke-113"),sQuery(id+"F2.wireOp",EDGE,"E2.sketch_text.stroke-114"),sQuery(id+"F2.wireOp",EDGE,"E2.sketch_text.stroke-115"),sQuery(id+"F2.wireOp",EDGE,"E2.sketch_text.stroke-116"),sQuery(id+"F2.wireOp",EDGE,"E2.sketch_text.stroke-117"),sQuery(id+"F2.wireOp",EDGE,"E2.sketch_text.stroke-118"),sQuery(id+"F2.wireOp",EDGE,"E2.sketch_text.stroke-119"),sQuery(id+"F2.wireOp",EDGE,"E2.sketch_text.stroke-120"),sQuery(id+"F2.wireOp",EDGE,"E2.sketch_text.stroke-121"),sQuery(id+"F2.wireOp",EDGE,"E2.sketch_text.stroke-122"),sQuery(id+"F2.wireOp",EDGE,"E2.sketch_text.stroke-123"),sQuery(id+"F2.wireOp",EDGE,"E2.sketch_text.stroke-124"),sQuery(id+"F2.wireOp",EDGE,"E2.sketch_text.stroke-125"),sQuery(id+"F2.wireOp",EDGE,"E2.sketch_text.stroke-126"),sQuery(id+"F2.wireOp",EDGE,"E2.sketch_text.stroke-127"),sQuery(id+"F2.wireOp",EDGE,"E2.sketch_text.stroke-128"),sQuery(id+"F2.wireOp",EDGE,"E2.sketch_text.stroke-129"),sQuery(id+"F2.wireOp",EDGE,"E2.sketch_text.stroke-130"),sQuery(id+"F2.wireOp",EDGE,"E2.sketch_text.stroke-131"),sQuery(id+"F2.wireOp",EDGE,"E2.sketch_text.stroke-132"),sQuery(id+"F2.wireOp",EDGE,"E2.sketch_text.stroke-133"),sQuery(id+"F2.wireOp",EDGE,"E2.sketch_text.stroke-134"),sQuery(id+"F2.wireOp",EDGE,"E2.sketch_text.stroke-135"),sQuery(id+"F2.wireOp",EDGE,"E2.sketch_text.stroke-136"),sQuery(id+"F2.wireOp",EDGE,"E2.sketch_text.stroke-137"),sQuery(id+"F2.wireOp",EDGE,"E2.sketch_text.stroke-138"),sQuery(id+"F2.wireOp",EDGE,"E2.sketch_text.stroke-139"),sQuery(id+"F2.wireOp",EDGE,"E2.sketch_text.stroke-140"),sQuery(id+"F2.wireOp",EDGE,"E2.sketch_text.stroke-141"),sQuery(id+"F2.wireOp",EDGE,"E2.sketch_text.stroke-142"),sQuery(id+"F2.wireOp",EDGE,"E2.sketch_text.stroke-143"),sQuery(id+"F2.wireOp",EDGE,"E2.sketch_text.stroke-144"),sQuery(id+"F2.wireOp",EDGE,"E2.sketch_text.stroke-145"),sQuery(id+"F2.wireOp",EDGE,"E2.sketch_text.stroke-146"),sQuery(id+"F2.wireOp",EDGE,"E2.sketch_text.stroke-147"),sQuery(id+"F2.wireOp",EDGE,"E2.sketch_text.stroke-148"),sQuery(id+"F2.wireOp",EDGE,"E2.sketch_text.stroke-149"),sQuery(id+"F2.wireOp",EDGE,"E2.sketch_text.stroke-150"),sQuery(id+"F2.wireOp",EDGE,"E2.sketch_text.stroke-151"),sQuery(id+"F2.wireOp",EDGE,"E2.sketch_text.stroke-152"),sQuery(id+"F2.wireOp",EDGE,"E2.sketch_text.stroke-153"),sQuery(id+"F2.wireOp",EDGE,"E2.sketch_text.stroke-154"),sQuery(id+"F2.wireOp",EDGE,"E2.sketch_text.stroke-155"),sQuery(id+"F2.wireOp",EDGE,"E2.sketch_text.stroke-156"),sQuery(id+"F2.wireOp",EDGE,"E2.sketch_text.stroke-157"),sQuery(id+"F2.wireOp",EDGE,"E2.sketch_text.stroke-158"),sQuery(id+"F2.wireOp",EDGE,"E2.sketch_text.stroke-159"),sQuery(id+"F2.wireOp",EDGE,"E2.sketch_text.stroke-160"),sQuery(id+"F2.wireOp",EDGE,"E2.sketch_text.stroke-161"),sQuery(id+"F2.wireOp",EDGE,"E2.sketch_text.stroke-162"),sQuery(id+"F2.wireOp",EDGE,"E2.sketch_text.stroke-163"),sQuery(id+"F2.wireOp",EDGE,"E2.sketch_text.stroke-164"),sQuery(id+"F2.wireOp",EDGE,"E2.sketch_text.stroke-165"),sQuery(id+"F2.wireOp",EDGE,"E2.sketch_text.stroke-166"),sQuery(id+"F2.wireOp",EDGE,"E2.sketch_text.stroke-167"),sQuery(id+"F2.wireOp",EDGE,"E2.sketch_text.stroke-168"),sQuery(id+"F2.wireOp",EDGE,"E2.sketch_text.stroke-169"),sQuery(id+"F2.wireOp",EDGE,"E2.sketch_text.stroke-170"),sQuery(id+"F2.wireOp",EDGE,"E2.sketch_text.stroke-171"),sQuery(id+"F2.wireOp",EDGE,"E2.sketch_text.stroke-172"),sQuery(id+"F2.wireOp",EDGE,"E2.sketch_text.stroke-173"),sQuery(id+"F3.wireOp",EDGE,"E4.sketch_text.stroke-0"),sQuery(id+"F3.wireOp",EDGE,"E4.sketch_text.stroke-1"),sQuery(id+"F3.wireOp",EDGE,"E4.sketch_text.stroke-2"),sQuery(id+"F3.wireOp",EDGE,"E4.sketch_text.stroke-3"),sQuery(id+"F3.wireOp",EDGE,"E4.sketch_text.stroke-4"),sQuery(id+"F3.wireOp",EDGE,"E4.sketch_text.stroke-5"),sQuery(id+"F3.wireOp",EDGE,"E4.sketch_text.stroke-6"),sQuery(id+"F3.wireOp",EDGE,"E4.sketch_text.stroke-7"),sQuery(id+"F3.wireOp",EDGE,"E4.sketch_text.stroke-8"),sQuery(id+"F3.wireOp",EDGE,"E4.sketch_text.stroke-9"),sQuery(id+"F3.wireOp",EDGE,"E4.sketch_text.stroke-10"),sQuery(id+"F3.wireOp",EDGE,"E4.sketch_text.stroke-11"),sQuery(id+"F3.wireOp",EDGE,"E4.sketch_text.stroke-12"),sQuery(id+"F3.wireOp",EDGE,"E4.sketch_text.stroke-13"),sQuery(id+"F3.wireOp",EDGE,"E4.sketch_text.stroke-14"),sQuery(id+"F3.wireOp",EDGE,"E4.sketch_text.stroke-15"),sQuery(id+"F3.wireOp",EDGE,"E4.sketch_text.stroke-16"),sQuery(id+"F3.wireOp",EDGE,"E4.sketch_text.stroke-17"),sQuery(id+"F3.wireOp",EDGE,"E4.sketch_text.stroke-18"),sQuery(id+"F3.wireOp",EDGE,"E4.sketch_text.stroke-19"),sQuery(id+"F3.wireOp",EDGE,"E4.sketch_text.stroke-20"),sQuery(id+"F3.wireOp",EDGE,"E4.sketch_text.stroke-21"),sQuery(id+"F3.wireOp",EDGE,"E4.sketch_text.stroke-22"),sQuery(id+"F3.wireOp",EDGE,"E4.sketch_text.stroke-23"),sQuery(id+"F3.wireOp",EDGE,"E4.sketch_text.stroke-24"),sQuery(id+"F3.wireOp",EDGE,"E4.sketch_text.stroke-25"),sQuery(id+"F3.wireOp",EDGE,"E4.sketch_text.stroke-26"),sQuery(id+"F3.wireOp",EDGE,"E4.sketch_text.stroke-27"),sQuery(id+"F3.wireOp",EDGE,"E4.sketch_text.stroke-28"),sQuery(id+"F3.wireOp",EDGE,"E4.sketch_text.stroke-29"),sQuery(id+"F3.wireOp",EDGE,"E4.sketch_text.stroke-30"),sQuery(id+"F3.wireOp",EDGE,"E4.sketch_text.stroke-31"),sQuery(id+"F3.wireOp",EDGE,"E4.sketch_text.stroke-32"),sQuery(id+"F3.wireOp",EDGE,"E4.sketch_text.stroke-33"),sQuery(id+"F3.wireOp",EDGE,"E4.sketch_text.stroke-34"),sQuery(id+"F3.wireOp",EDGE,"E4.sketch_text.stroke-35"),sQuery(id+"F3.wireOp",EDGE,"E4.sketch_text.stroke-36"),sQuery(id+"F3.wireOp",EDGE,"E4.sketch_text.stroke-37"),sQuery(id+"F3.wireOp",EDGE,"E4.sketch_text.stroke-38"),sQuery(id+"F3.wireOp",EDGE,"E4.sketch_text.stroke-39"),sQuery(id+"F3.wireOp",EDGE,"E4.sketch_text.stroke-40"),sQuery(id+"F3.wireOp",EDGE,"E4.sketch_text.stroke-41"),sQuery(id+"F3.wireOp",EDGE,"E4.sketch_text.stroke-42"),sQuery(id+"F3.wireOp",EDGE,"E4.sketch_text.stroke-43"),sQuery(id+"F3.wireOp",EDGE,"E4.sketch_text.stroke-44"),sQuery(id+"F3.wireOp",EDGE,"E4.sketch_text.stroke-45"),sQuery(id+"F3.wireOp",EDGE,"E4.sketch_text.stroke-46"),sQuery(id+"F3.wireOp",EDGE,"E4.sketch_text.stroke-47"),sQuery(id+"F3.wireOp",EDGE,"E4.sketch_text.stroke-48"),sQuery(id+"F3.wireOp",EDGE,"E4.sketch_text.stroke-49"),sQuery(id+"F3.wireOp",EDGE,"E4.sketch_text.stroke-50"),sQuery(id+"F3.wireOp",EDGE,"E4.sketch_text.stroke-51"),sQuery(id+"F3.wireOp",EDGE,"E4.sketch_text.stroke-52"),sQuery(id+"F3.wireOp",EDGE,"E4.sketch_text.stroke-53"),sQuery(id+"F3.wireOp",EDGE,"E4.sketch_text.stroke-54"),sQuery(id+"F3.wireOp",EDGE,"E4.sketch_text.stroke-55"),sQuery(id+"F3.wireOp",EDGE,"E4.sketch_text.stroke-56"),sQuery(id+"F3.wireOp",EDGE,"E4.sketch_text.stroke-57"),sQuery(id+"F3.wireOp",EDGE,"E4.sketch_text.stroke-58"),sQuery(id+"F3.wireOp",EDGE,"E4.sketch_text.stroke-59"),sQuery(id+"F3.wireOp",EDGE,"E4.sketch_text.stroke-60"),sQuery(id+"F3.wireOp",EDGE,"E4.sketch_text.stroke-61"),sQuery(id+"F3.wireOp",EDGE,"E4.sketch_text.stroke-62"),sQuery(id+"F3.wireOp",EDGE,"E4.sketch_text.stroke-71"),sQuery(id+"F3.wireOp",EDGE,"E4.sketch_text.stroke-72"),sQuery(id+"F3.wireOp",EDGE,"E4.sketch_text.stroke-73"),sQuery(id+"F3.wireOp",EDGE,"E4.sketch_text.stroke-74"),sQuery(id+"F3.wireOp",EDGE,"E4.sketch_text.stroke-75"),sQuery(id+"F3.wireOp",EDGE,"E4.sketch_text.stroke-76"),sQuery(id+"F3.wireOp",EDGE,"E4.sketch_text.stroke-77"),sQuery(id+"F3.wireOp",EDGE,"E4.sketch_text.stroke-78"),sQuery(id+"F3.wireOp",EDGE,"E4.sketch_text.stroke-79"),sQuery(id+"F3.wireOp",EDGE,"E4.sketch_text.stroke-80"),sQuery(id+"F3.wireOp",EDGE,"E4.sketch_text.stroke-81"),sQuery(id+"F3.wireOp",EDGE,"E4.sketch_text.stroke-82"),sQuery(id+"F3.wireOp",EDGE,"E4.sketch_text.stroke-83"),sQuery(id+"F3.wireOp",EDGE,"E4.sketch_text.stroke-84"),sQuery(id+"F3.wireOp",EDGE,"E4.sketch_text.stroke-85"),sQuery(id+"F3.wireOp",EDGE,"E4.sketch_text.stroke-86"),sQuery(id+"F3.wireOp",EDGE,"E4.sketch_text.stroke-87"),sQuery(id+"F3.wireOp",EDGE,"E4.sketch_text.stroke-88"),sQuery(id+"F3.wireOp",EDGE,"E4.sketch_text.stroke-89"),sQuery(id+"F3.wireOp",EDGE,"E4.sketch_text.stroke-90"),sQuery(id+"F3.wireOp",EDGE,"E4.sketch_text.stroke-91"),sQuery(id+"F3.wireOp",EDGE,"E4.sketch_text.stroke-92"),sQuery(id+"F3.wireOp",EDGE,"E4.sketch_text.stroke-93"),sQuery(id+"F3.wireOp",EDGE,"E4.sketch_text.stroke-94"),sQuery(id+"F3.wireOp",EDGE,"E4.sketch_text.stroke-95"),sQuery(id+"F3.wireOp",EDGE,"E4.sketch_text.stroke-96"),sQuery(id+"F3.wireOp",EDGE,"E4.sketch_text.stroke-97"),sQuery(id+"F3.wireOp",EDGE,"E4.sketch_text.stroke-103"),sQuery(id+"F3.wireOp",EDGE,"E4.sketch_text.stroke-104"),sQuery(id+"F3.wireOp",EDGE,"E4.sketch_text.stroke-105"),sQuery(id+"F3.wireOp",EDGE,"E4.sketch_text.stroke-106"),sQuery(id+"F3.wireOp",EDGE,"E4.sketch_text.stroke-107"),sQuery(id+"F3.wireOp",EDGE,"E4.sketch_text.stroke-108"),sQuery(id+"F3.wireOp",EDGE,"E4.sketch_text.stroke-109"),sQuery(id+"F3.wireOp",EDGE,"E4.sketch_text.stroke-110"),sQuery(id+"F3.wireOp",EDGE,"E4.sketch_text.stroke-111"),sQuery(id+"F3.wireOp",EDGE,"E4.sketch_text.stroke-112"),sQuery(id+"F3.wireOp",EDGE,"E4.sketch_text.stroke-113"),sQuery(id+"F3.wireOp",EDGE,"E4.sketch_text.stroke-114"),sQuery(id+"F3.wireOp",EDGE,"E4.sketch_text.stroke-115"),sQuery(id+"F3.wireOp",EDGE,"E4.sketch_text.stroke-116"),sQuery(id+"F3.wireOp",EDGE,"E4.sketch_text.stroke-117"),sQuery(id+"F3.wireOp",EDGE,"E4.sketch_text.stroke-118"),sQuery(id+"F3.wireOp",EDGE,"E4.sketch_text.stroke-119"),sQuery(id+"F3.wireOp",EDGE,"E4.sketch_text.stroke-120"),sQuery(id+"F3.wireOp",EDGE,"E4.sketch_text.stroke-121"),sQuery(id+"F3.wireOp",EDGE,"E4.sketch_text.stroke-122"),sQuery(id+"F3.wireOp",EDGE,"E4.sketch_text.stroke-123"),sQuery(id+"F3.wireOp",EDGE,"E4.sketch_text.stroke-124"),sQuery(id+"F3.wireOp",EDGE,"E4.sketch_text.stroke-125"),sQuery(id+"F3.wireOp",EDGE,"E4.sketch_text.stroke-126"),sQuery(id+"F3.wireOp",EDGE,"E4.sketch_text.stroke-127"),sQuery(id+"F3.wireOp",EDGE,"E4.sketch_text.stroke-128"),sQuery(id+"F3.wireOp",EDGE,"E4.sketch_text.stroke-129"),sQuery(id+"F3.wireOp",EDGE,"E4.sketch_text.stroke-130"),sQuery(id+"F3.wireOp",EDGE,"E4.sketch_text.stroke-131"),sQuery(id+"F3.wireOp",EDGE,"E4.sketch_text.stroke-132"),sQuery(id+"F3.wireOp",EDGE,"E4.sketch_text.stroke-133"),sQuery(id+"F3.wireOp",EDGE,"E4.sketch_text.stroke-134"),sQuery(id+"F3.wireOp",EDGE,"E4.sketch_text.stroke-135"),sQuery(id+"F3.wireOp",EDGE,"E4.sketch_text.stroke-136"),sQuery(id+"F3.wireOp",EDGE,"E4.sketch_text.stroke-137"),sQuery(id+"F3.wireOp",EDGE,"E4.sketch_text.stroke-138"),sQuery(id+"F3.wireOp",EDGE,"E4.sketch_text.stroke-139"),sQuery(id+"F3.wireOp",EDGE,"E4.sketch_text.stroke-140"),sQuery(id+"F3.wireOp",EDGE,"E4.sketch_text.stroke-141"),sQuery(id+"F3.wireOp",EDGE,"E4.sketch_text.stroke-142"),sQuery(id+"F3.wireOp",EDGE,"E4.sketch_text.stroke-143"),sQuery(id+"F3.wireOp",EDGE,"E4.sketch_text.stroke-144"),sQuery(id+"F3.wireOp",EDGE,"E4.sketch_text.stroke-145"),sQuery(id+"F3.wireOp",EDGE,"E4.sketch_text.stroke-146"),sQuery(id+"F3.wireOp",EDGE,"E4.sketch_text.stroke-147"),sQuery(id+"F3.wireOp",EDGE,"E4.sketch_text.stroke-148"),sQuery(id+"F3.wireOp",EDGE,"E4.sketch_text.stroke-149"),sQuery(id+"F3.wireOp",EDGE,"E4.sketch_text.stroke-150"),sQuery(id+"F3.wireOp",EDGE,"E4.sketch_text.stroke-151"),sQuery(id+"F3.wireOp",EDGE,"E4.sketch_text.stroke-152"),sQuery(id+"F3.wireOp",EDGE,"E4.sketch_text.stroke-153"),sQuery(id+"F3.wireOp",EDGE,"E4.sketch_text.stroke-159"),sQuery(id+"F3.wireOp",EDGE,"E4.sketch_text.stroke-160"),sQuery(id+"F3.wireOp",EDGE,"E4.sketch_text.stroke-161"),sQuery(id+"F3.wireOp",EDGE,"E4.sketch_text.stroke-162"),sQuery(id+"F3.wireOp",EDGE,"E4.sketch_text.stroke-163"),sQuery(id+"F3.wireOp",EDGE,"E4.sketch_text.stroke-164"),sQuery(id+"F3.wireOp",EDGE,"E4.sketch_text.stroke-165"),sQuery(id+"F3.wireOp",EDGE,"E4.sketch_text.stroke-166"),sQuery(id+"F3.wireOp",EDGE,"E4.sketch_text.stroke-167"),sQuery(id+"F3.wireOp",EDGE,"E4.sketch_text.stroke-168"),sQuery(id+"F3.wireOp",EDGE,"E4.sketch_text.stroke-169"),sQuery(id+"F3.wireOp",EDGE,"E4.sketch_text.stroke-170"),sQuery(id+"F3.wireOp",EDGE,"E4.sketch_text.stroke-171"),sQuery(id+"F3.wireOp",EDGE,"E4.sketch_text.stroke-172"),sQuery(id+"F3.wireOp",EDGE,"E4.sketch_text.stroke-173"),sQuery(id+"F3.wireOp",EDGE,"E4.sketch_text.stroke-174"),sQuery(id+"F3.wireOp",EDGE,"E4.sketch_text.stroke-175"),sQuery(id+"F3.wireOp",EDGE,"E4.sketch_text.stroke-176"),sQuery(id+"F3.wireOp",EDGE,"E4.sketch_text.stroke-177"),sQuery(id+"F3.wireOp",EDGE,"E4.sketch_text.stroke-178"),sQuery(id+"F3.wireOp",EDGE,"E4.sketch_text.stroke-179"),sQuery(id+"F3.wireOp",EDGE,"E4.sketch_text.stroke-180"),sQuery(id+"F4.wireOp",EDGE,"727ac2c1-f511-4829-95a7-a443ef16a4cd"),subQ2])],"isStart":true}),makeQuery(id+"F5.opExtrude","SWEPT_FACE",FACE,{"disambiguationData":[OSD([subQ2])]})])],"derivedFrom":makeQuery(id+"F5.opExtrude","CAP_EDGE",EDGE,{"disambiguationData":[OSD([subQ2])],"isStart":true})});}
            var Q18;
            {var subQ0=sQuery(id+"F0.wireOp",EDGE,"E0.top");var subQ1=sQuery(id+"F0.wireOp",EDGE,"E0.bottom");var subQ2=sQuery(id+"F4.wireOp",EDGE,"1a034e28-a7c2-419d-97de-c33d70a47301");Q18=makeQuery(id+"F5.boolean.opBoolean","SPLIT",EDGE,{"disambiguationData":[TD([makeQuery(id+"F1.opExtrude","CAP_FACE",FACE,{"disambiguationData":[OSD([subQ1,subQ0,sQuery(id+"F0.wireOp",EDGE,"E0.left"),sQuery(id+"F0.wireOp",EDGE,"E0.right")])],"isStart":false}),makeQuery(id+"F1.opExtrude","SWEPT_FACE",FACE,{"disambiguationData":[OSD([subQ0])]}),makeQuery(id+"F5.opExtrude","CAP_FACE",FACE,{"disambiguationData":[OSD([subQ1,sQuery(id+"F2.wireOp",EDGE,"E2.sketch_text.stroke-0"),sQuery(id+"F2.wireOp",EDGE,"E2.sketch_text.stroke-1"),sQuery(id+"F2.wireOp",EDGE,"E2.sketch_text.stroke-2"),sQuery(id+"F2.wireOp",EDGE,"E2.sketch_text.stroke-3"),sQuery(id+"F2.wireOp",EDGE,"E2.sketch_text.stroke-4"),sQuery(id+"F2.wireOp",EDGE,"E2.sketch_text.stroke-5"),sQuery(id+"F2.wireOp",EDGE,"E2.sketch_text.stroke-6"),sQuery(id+"F2.wireOp",EDGE,"E2.sketch_text.stroke-7"),sQuery(id+"F2.wireOp",EDGE,"E2.sketch_text.stroke-8"),sQuery(id+"F2.wireOp",EDGE,"E2.sketch_text.stroke-9"),sQuery(id+"F2.wireOp",EDGE,"E2.sketch_text.stroke-10"),sQuery(id+"F2.wireOp",EDGE,"E2.sketch_text.stroke-11"),sQuery(id+"F2.wireOp",EDGE,"E2.sketch_text.stroke-12"),sQuery(id+"F2.wireOp",EDGE,"E2.sketch_text.stroke-13"),sQuery(id+"F2.wireOp",EDGE,"E2.sketch_text.stroke-14"),sQuery(id+"F2.wireOp",EDGE,"E2.sketch_text.stroke-15"),sQuery(id+"F2.wireOp",EDGE,"E2.sketch_text.stroke-16"),sQuery(id+"F2.wireOp",EDGE,"E2.sketch_text.stroke-17"),sQuery(id+"F2.wireOp",EDGE,"E2.sketch_text.stroke-18"),sQuery(id+"F2.wireOp",EDGE,"E2.sketch_text.stroke-19"),sQuery(id+"F2.wireOp",EDGE,"E2.sketch_text.stroke-20"),sQuery(id+"F2.wireOp",EDGE,"E2.sketch_text.stroke-21"),sQuery(id+"F2.wireOp",EDGE,"E2.sketch_text.stroke-22"),sQuery(id+"F2.wireOp",EDGE,"E2.sketch_text.stroke-23"),sQuery(id+"F2.wireOp",EDGE,"E2.sketch_text.stroke-24"),sQuery(id+"F2.wireOp",EDGE,"E2.sketch_text.stroke-25"),sQuery(id+"F2.wireOp",EDGE,"E2.sketch_text.stroke-26"),sQuery(id+"F2.wireOp",EDGE,"E2.sketch_text.stroke-27"),sQuery(id+"F2.wireOp",EDGE,"E2.sketch_text.stroke-28"),sQuery(id+"F2.wireOp",EDGE,"E2.sketch_text.stroke-29"),sQuery(id+"F2.wireOp",EDGE,"E2.sketch_text.stroke-30"),sQuery(id+"F2.wireOp",EDGE,"E2.sketch_text.stroke-31"),sQuery(id+"F2.wireOp",EDGE,"E2.sketch_text.stroke-32"),sQuery(id+"F2.wireOp",EDGE,"E2.sketch_text.stroke-33"),sQuery(id+"F2.wireOp",EDGE,"E2.sketch_text.stroke-34"),sQuery(id+"F2.wireOp",EDGE,"E2.sketch_text.stroke-35"),sQuery(id+"F2.wireOp",EDGE,"E2.sketch_text.stroke-36"),sQuery(id+"F2.wireOp",EDGE,"E2.sketch_text.stroke-37"),sQuery(id+"F2.wireOp",EDGE,"E2.sketch_text.stroke-38"),sQuery(id+"F2.wireOp",EDGE,"E2.sketch_text.stroke-39"),sQuery(id+"F2.wireOp",EDGE,"E2.sketch_text.stroke-40"),sQuery(id+"F2.wireOp",EDGE,"E2.sketch_text.stroke-41"),sQuery(id+"F2.wireOp",EDGE,"E2.sketch_text.stroke-42"),sQuery(id+"F2.wireOp",EDGE,"E2.sketch_text.stroke-43"),sQuery(id+"F2.wireOp",EDGE,"E2.sketch_text.stroke-44"),sQuery(id+"F2.wireOp",EDGE,"E2.sketch_text.stroke-45"),sQuery(id+"F2.wireOp",EDGE,"E2.sketch_text.stroke-46"),sQuery(id+"F2.wireOp",EDGE,"E2.sketch_text.stroke-47"),sQuery(id+"F2.wireOp",EDGE,"E2.sketch_text.stroke-48"),sQuery(id+"F2.wireOp",EDGE,"E2.sketch_text.stroke-49"),sQuery(id+"F2.wireOp",EDGE,"E2.sketch_text.stroke-50"),sQuery(id+"F2.wireOp",EDGE,"E2.sketch_text.stroke-51"),sQuery(id+"F2.wireOp",EDGE,"E2.sketch_text.stroke-52"),sQuery(id+"F2.wireOp",EDGE,"E2.sketch_text.stroke-53"),sQuery(id+"F2.wireOp",EDGE,"E2.sketch_text.stroke-54"),sQuery(id+"F2.wireOp",EDGE,"E2.sketch_text.stroke-55"),sQuery(id+"F2.wireOp",EDGE,"E2.sketch_text.stroke-56"),sQuery(id+"F2.wireOp",EDGE,"E2.sketch_text.stroke-57"),sQuery(id+"F2.wireOp",EDGE,"E2.sketch_text.stroke-58"),sQuery(id+"F2.wireOp",EDGE,"E2.sketch_text.stroke-59"),sQuery(id+"F2.wireOp",EDGE,"E2.sketch_text.stroke-60"),sQuery(id+"F2.wireOp",EDGE,"E2.sketch_text.stroke-61"),sQuery(id+"F2.wireOp",EDGE,"E2.sketch_text.stroke-62"),sQuery(id+"F2.wireOp",EDGE,"E2.sketch_text.stroke-63"),sQuery(id+"F2.wireOp",EDGE,"E2.sketch_text.stroke-64"),sQuery(id+"F2.wireOp",EDGE,"E2.sketch_text.stroke-65"),sQuery(id+"F2.wireOp",EDGE,"E2.sketch_text.stroke-66"),sQuery(id+"F2.wireOp",EDGE,"E2.sketch_text.stroke-67"),sQuery(id+"F2.wireOp",EDGE,"E2.sketch_text.stroke-68"),sQuery(id+"F2.wireOp",EDGE,"E2.sketch_text.stroke-69"),sQuery(id+"F2.wireOp",EDGE,"E2.sketch_text.stroke-70"),sQuery(id+"F2.wireOp",EDGE,"E2.sketch_text.stroke-71"),sQuery(id+"F2.wireOp",EDGE,"E2.sketch_text.stroke-72"),sQuery(id+"F2.wireOp",EDGE,"E2.sketch_text.stroke-73"),sQuery(id+"F2.wireOp",EDGE,"E2.sketch_text.stroke-74"),sQuery(id+"F2.wireOp",EDGE,"E2.sketch_text.stroke-75"),sQuery(id+"F2.wireOp",EDGE,"E2.sketch_text.stroke-76"),sQuery(id+"F2.wireOp",EDGE,"E2.sketch_text.stroke-77"),sQuery(id+"F2.wireOp",EDGE,"E2.sketch_text.stroke-78"),sQuery(id+"F2.wireOp",EDGE,"E2.sketch_text.stroke-79"),sQuery(id+"F2.wireOp",EDGE,"E2.sketch_text.stroke-80"),sQuery(id+"F2.wireOp",EDGE,"E2.sketch_text.stroke-81"),sQuery(id+"F2.wireOp",EDGE,"E2.sketch_text.stroke-82"),sQuery(id+"F2.wireOp",EDGE,"E2.sketch_text.stroke-83"),sQuery(id+"F2.wireOp",EDGE,"E2.sketch_text.stroke-84"),sQuery(id+"F2.wireOp",EDGE,"E2.sketch_text.stroke-85"),sQuery(id+"F2.wireOp",EDGE,"E2.sketch_text.stroke-86"),sQuery(id+"F2.wireOp",EDGE,"E2.sketch_text.stroke-87"),sQuery(id+"F2.wireOp",EDGE,"E2.sketch_text.stroke-88"),sQuery(id+"F2.wireOp",EDGE,"E2.sketch_text.stroke-89"),sQuery(id+"F2.wireOp",EDGE,"E2.sketch_text.stroke-90"),sQuery(id+"F2.wireOp",EDGE,"E2.sketch_text.stroke-91"),sQuery(id+"F2.wireOp",EDGE,"E2.sketch_text.stroke-92"),sQuery(id+"F2.wireOp",EDGE,"E2.sketch_text.stroke-93"),sQuery(id+"F2.wireOp",EDGE,"E2.sketch_text.stroke-94"),sQuery(id+"F2.wireOp",EDGE,"E2.sketch_text.stroke-95"),sQuery(id+"F2.wireOp",EDGE,"E2.sketch_text.stroke-96"),sQuery(id+"F2.wireOp",EDGE,"E2.sketch_text.stroke-97"),sQuery(id+"F2.wireOp",EDGE,"E2.sketch_text.stroke-98"),sQuery(id+"F2.wireOp",EDGE,"E2.sketch_text.stroke-99"),sQuery(id+"F2.wireOp",EDGE,"E2.sketch_text.stroke-100"),sQuery(id+"F2.wireOp",EDGE,"E2.sketch_text.stroke-101"),sQuery(id+"F2.wireOp",EDGE,"E2.sketch_text.stroke-102"),sQuery(id+"F2.wireOp",EDGE,"E2.sketch_text.stroke-103"),sQuery(id+"F2.wireOp",EDGE,"E2.sketch_text.stroke-104"),sQuery(id+"F2.wireOp",EDGE,"E2.sketch_text.stroke-105"),sQuery(id+"F2.wireOp",EDGE,"E2.sketch_text.stroke-106"),sQuery(id+"F2.wireOp",EDGE,"E2.sketch_text.stroke-107"),sQuery(id+"F2.wireOp",EDGE,"E2.sketch_text.stroke-108"),sQuery(id+"F2.wireOp",EDGE,"E2.sketch_text.stroke-109"),sQuery(id+"F2.wireOp",EDGE,"E2.sketch_text.stroke-110"),sQuery(id+"F2.wireOp",EDGE,"E2.sketch_text.stroke-111"),sQuery(id+"F2.wireOp",EDGE,"E2.sketch_text.stroke-112"),sQuery(id+"F2.wireOp",EDGE,"E2.sketch_text.stroke-113"),sQuery(id+"F2.wireOp",EDGE,"E2.sketch_text.stroke-114"),sQuery(id+"F2.wireOp",EDGE,"E2.sketch_text.stroke-115"),sQuery(id+"F2.wireOp",EDGE,"E2.sketch_text.stroke-116"),sQuery(id+"F2.wireOp",EDGE,"E2.sketch_text.stroke-117"),sQuery(id+"F2.wireOp",EDGE,"E2.sketch_text.stroke-118"),sQuery(id+"F2.wireOp",EDGE,"E2.sketch_text.stroke-119"),sQuery(id+"F2.wireOp",EDGE,"E2.sketch_text.stroke-120"),sQuery(id+"F2.wireOp",EDGE,"E2.sketch_text.stroke-121"),sQuery(id+"F2.wireOp",EDGE,"E2.sketch_text.stroke-122"),sQuery(id+"F2.wireOp",EDGE,"E2.sketch_text.stroke-123"),sQuery(id+"F2.wireOp",EDGE,"E2.sketch_text.stroke-124"),sQuery(id+"F2.wireOp",EDGE,"E2.sketch_text.stroke-125"),sQuery(id+"F2.wireOp",EDGE,"E2.sketch_text.stroke-126"),sQuery(id+"F2.wireOp",EDGE,"E2.sketch_text.stroke-127"),sQuery(id+"F2.wireOp",EDGE,"E2.sketch_text.stroke-128"),sQuery(id+"F2.wireOp",EDGE,"E2.sketch_text.stroke-129"),sQuery(id+"F2.wireOp",EDGE,"E2.sketch_text.stroke-130"),sQuery(id+"F2.wireOp",EDGE,"E2.sketch_text.stroke-131"),sQuery(id+"F2.wireOp",EDGE,"E2.sketch_text.stroke-132"),sQuery(id+"F2.wireOp",EDGE,"E2.sketch_text.stroke-133"),sQuery(id+"F2.wireOp",EDGE,"E2.sketch_text.stroke-134"),sQuery(id+"F2.wireOp",EDGE,"E2.sketch_text.stroke-135"),sQuery(id+"F2.wireOp",EDGE,"E2.sketch_text.stroke-136"),sQuery(id+"F2.wireOp",EDGE,"E2.sketch_text.stroke-137"),sQuery(id+"F2.wireOp",EDGE,"E2.sketch_text.stroke-138"),sQuery(id+"F2.wireOp",EDGE,"E2.sketch_text.stroke-139"),sQuery(id+"F2.wireOp",EDGE,"E2.sketch_text.stroke-140"),sQuery(id+"F2.wireOp",EDGE,"E2.sketch_text.stroke-141"),sQuery(id+"F2.wireOp",EDGE,"E2.sketch_text.stroke-142"),sQuery(id+"F2.wireOp",EDGE,"E2.sketch_text.stroke-143"),sQuery(id+"F2.wireOp",EDGE,"E2.sketch_text.stroke-144"),sQuery(id+"F2.wireOp",EDGE,"E2.sketch_text.stroke-145"),sQuery(id+"F2.wireOp",EDGE,"E2.sketch_text.stroke-146"),sQuery(id+"F2.wireOp",EDGE,"E2.sketch_text.stroke-147"),sQuery(id+"F2.wireOp",EDGE,"E2.sketch_text.stroke-148"),sQuery(id+"F2.wireOp",EDGE,"E2.sketch_text.stroke-149"),sQuery(id+"F2.wireOp",EDGE,"E2.sketch_text.stroke-150"),sQuery(id+"F2.wireOp",EDGE,"E2.sketch_text.stroke-151"),sQuery(id+"F2.wireOp",EDGE,"E2.sketch_text.stroke-152"),sQuery(id+"F2.wireOp",EDGE,"E2.sketch_text.stroke-153"),sQuery(id+"F2.wireOp",EDGE,"E2.sketch_text.stroke-154"),sQuery(id+"F2.wireOp",EDGE,"E2.sketch_text.stroke-155"),sQuery(id+"F2.wireOp",EDGE,"E2.sketch_text.stroke-156"),sQuery(id+"F2.wireOp",EDGE,"E2.sketch_text.stroke-157"),sQuery(id+"F2.wireOp",EDGE,"E2.sketch_text.stroke-158"),sQuery(id+"F2.wireOp",EDGE,"E2.sketch_text.stroke-159"),sQuery(id+"F2.wireOp",EDGE,"E2.sketch_text.stroke-160"),sQuery(id+"F2.wireOp",EDGE,"E2.sketch_text.stroke-161"),sQuery(id+"F2.wireOp",EDGE,"E2.sketch_text.stroke-162"),sQuery(id+"F2.wireOp",EDGE,"E2.sketch_text.stroke-163"),sQuery(id+"F2.wireOp",EDGE,"E2.sketch_text.stroke-164"),sQuery(id+"F2.wireOp",EDGE,"E2.sketch_text.stroke-165"),sQuery(id+"F2.wireOp",EDGE,"E2.sketch_text.stroke-166"),sQuery(id+"F2.wireOp",EDGE,"E2.sketch_text.stroke-167"),sQuery(id+"F2.wireOp",EDGE,"E2.sketch_text.stroke-168"),sQuery(id+"F2.wireOp",EDGE,"E2.sketch_text.stroke-169"),sQuery(id+"F2.wireOp",EDGE,"E2.sketch_text.stroke-170"),sQuery(id+"F2.wireOp",EDGE,"E2.sketch_text.stroke-171"),sQuery(id+"F2.wireOp",EDGE,"E2.sketch_text.stroke-172"),sQuery(id+"F2.wireOp",EDGE,"E2.sketch_text.stroke-173"),sQuery(id+"F3.wireOp",EDGE,"E4.sketch_text.stroke-0"),sQuery(id+"F3.wireOp",EDGE,"E4.sketch_text.stroke-1"),sQuery(id+"F3.wireOp",EDGE,"E4.sketch_text.stroke-2"),sQuery(id+"F3.wireOp",EDGE,"E4.sketch_text.stroke-3"),sQuery(id+"F3.wireOp",EDGE,"E4.sketch_text.stroke-4"),sQuery(id+"F3.wireOp",EDGE,"E4.sketch_text.stroke-5"),sQuery(id+"F3.wireOp",EDGE,"E4.sketch_text.stroke-6"),sQuery(id+"F3.wireOp",EDGE,"E4.sketch_text.stroke-7"),sQuery(id+"F3.wireOp",EDGE,"E4.sketch_text.stroke-8"),sQuery(id+"F3.wireOp",EDGE,"E4.sketch_text.stroke-9"),sQuery(id+"F3.wireOp",EDGE,"E4.sketch_text.stroke-10"),sQuery(id+"F3.wireOp",EDGE,"E4.sketch_text.stroke-11"),sQuery(id+"F3.wireOp",EDGE,"E4.sketch_text.stroke-12"),sQuery(id+"F3.wireOp",EDGE,"E4.sketch_text.stroke-13"),sQuery(id+"F3.wireOp",EDGE,"E4.sketch_text.stroke-14"),sQuery(id+"F3.wireOp",EDGE,"E4.sketch_text.stroke-15"),sQuery(id+"F3.wireOp",EDGE,"E4.sketch_text.stroke-16"),sQuery(id+"F3.wireOp",EDGE,"E4.sketch_text.stroke-17"),sQuery(id+"F3.wireOp",EDGE,"E4.sketch_text.stroke-18"),sQuery(id+"F3.wireOp",EDGE,"E4.sketch_text.stroke-19"),sQuery(id+"F3.wireOp",EDGE,"E4.sketch_text.stroke-20"),sQuery(id+"F3.wireOp",EDGE,"E4.sketch_text.stroke-21"),sQuery(id+"F3.wireOp",EDGE,"E4.sketch_text.stroke-22"),sQuery(id+"F3.wireOp",EDGE,"E4.sketch_text.stroke-23"),sQuery(id+"F3.wireOp",EDGE,"E4.sketch_text.stroke-24"),sQuery(id+"F3.wireOp",EDGE,"E4.sketch_text.stroke-25"),sQuery(id+"F3.wireOp",EDGE,"E4.sketch_text.stroke-26"),sQuery(id+"F3.wireOp",EDGE,"E4.sketch_text.stroke-27"),sQuery(id+"F3.wireOp",EDGE,"E4.sketch_text.stroke-28"),sQuery(id+"F3.wireOp",EDGE,"E4.sketch_text.stroke-29"),sQuery(id+"F3.wireOp",EDGE,"E4.sketch_text.stroke-30"),sQuery(id+"F3.wireOp",EDGE,"E4.sketch_text.stroke-31"),sQuery(id+"F3.wireOp",EDGE,"E4.sketch_text.stroke-32"),sQuery(id+"F3.wireOp",EDGE,"E4.sketch_text.stroke-33"),sQuery(id+"F3.wireOp",EDGE,"E4.sketch_text.stroke-34"),sQuery(id+"F3.wireOp",EDGE,"E4.sketch_text.stroke-35"),sQuery(id+"F3.wireOp",EDGE,"E4.sketch_text.stroke-36"),sQuery(id+"F3.wireOp",EDGE,"E4.sketch_text.stroke-37"),sQuery(id+"F3.wireOp",EDGE,"E4.sketch_text.stroke-38"),sQuery(id+"F3.wireOp",EDGE,"E4.sketch_text.stroke-39"),sQuery(id+"F3.wireOp",EDGE,"E4.sketch_text.stroke-40"),sQuery(id+"F3.wireOp",EDGE,"E4.sketch_text.stroke-41"),sQuery(id+"F3.wireOp",EDGE,"E4.sketch_text.stroke-42"),sQuery(id+"F3.wireOp",EDGE,"E4.sketch_text.stroke-43"),sQuery(id+"F3.wireOp",EDGE,"E4.sketch_text.stroke-44"),sQuery(id+"F3.wireOp",EDGE,"E4.sketch_text.stroke-45"),sQuery(id+"F3.wireOp",EDGE,"E4.sketch_text.stroke-46"),sQuery(id+"F3.wireOp",EDGE,"E4.sketch_text.stroke-47"),sQuery(id+"F3.wireOp",EDGE,"E4.sketch_text.stroke-48"),sQuery(id+"F3.wireOp",EDGE,"E4.sketch_text.stroke-49"),sQuery(id+"F3.wireOp",EDGE,"E4.sketch_text.stroke-50"),sQuery(id+"F3.wireOp",EDGE,"E4.sketch_text.stroke-51"),sQuery(id+"F3.wireOp",EDGE,"E4.sketch_text.stroke-52"),sQuery(id+"F3.wireOp",EDGE,"E4.sketch_text.stroke-53"),sQuery(id+"F3.wireOp",EDGE,"E4.sketch_text.stroke-54"),sQuery(id+"F3.wireOp",EDGE,"E4.sketch_text.stroke-55"),sQuery(id+"F3.wireOp",EDGE,"E4.sketch_text.stroke-56"),sQuery(id+"F3.wireOp",EDGE,"E4.sketch_text.stroke-57"),sQuery(id+"F3.wireOp",EDGE,"E4.sketch_text.stroke-58"),sQuery(id+"F3.wireOp",EDGE,"E4.sketch_text.stroke-59"),sQuery(id+"F3.wireOp",EDGE,"E4.sketch_text.stroke-60"),sQuery(id+"F3.wireOp",EDGE,"E4.sketch_text.stroke-61"),sQuery(id+"F3.wireOp",EDGE,"E4.sketch_text.stroke-62"),sQuery(id+"F3.wireOp",EDGE,"E4.sketch_text.stroke-71"),sQuery(id+"F3.wireOp",EDGE,"E4.sketch_text.stroke-72"),sQuery(id+"F3.wireOp",EDGE,"E4.sketch_text.stroke-73"),sQuery(id+"F3.wireOp",EDGE,"E4.sketch_text.stroke-74"),sQuery(id+"F3.wireOp",EDGE,"E4.sketch_text.stroke-75"),sQuery(id+"F3.wireOp",EDGE,"E4.sketch_text.stroke-76"),sQuery(id+"F3.wireOp",EDGE,"E4.sketch_text.stroke-77"),sQuery(id+"F3.wireOp",EDGE,"E4.sketch_text.stroke-78"),sQuery(id+"F3.wireOp",EDGE,"E4.sketch_text.stroke-79"),sQuery(id+"F3.wireOp",EDGE,"E4.sketch_text.stroke-80"),sQuery(id+"F3.wireOp",EDGE,"E4.sketch_text.stroke-81"),sQuery(id+"F3.wireOp",EDGE,"E4.sketch_text.stroke-82"),sQuery(id+"F3.wireOp",EDGE,"E4.sketch_text.stroke-83"),sQuery(id+"F3.wireOp",EDGE,"E4.sketch_text.stroke-84"),sQuery(id+"F3.wireOp",EDGE,"E4.sketch_text.stroke-85"),sQuery(id+"F3.wireOp",EDGE,"E4.sketch_text.stroke-86"),sQuery(id+"F3.wireOp",EDGE,"E4.sketch_text.stroke-87"),sQuery(id+"F3.wireOp",EDGE,"E4.sketch_text.stroke-88"),sQuery(id+"F3.wireOp",EDGE,"E4.sketch_text.stroke-89"),sQuery(id+"F3.wireOp",EDGE,"E4.sketch_text.stroke-90"),sQuery(id+"F3.wireOp",EDGE,"E4.sketch_text.stroke-91"),sQuery(id+"F3.wireOp",EDGE,"E4.sketch_text.stroke-92"),sQuery(id+"F3.wireOp",EDGE,"E4.sketch_text.stroke-93"),sQuery(id+"F3.wireOp",EDGE,"E4.sketch_text.stroke-94"),sQuery(id+"F3.wireOp",EDGE,"E4.sketch_text.stroke-95"),sQuery(id+"F3.wireOp",EDGE,"E4.sketch_text.stroke-96"),sQuery(id+"F3.wireOp",EDGE,"E4.sketch_text.stroke-97"),sQuery(id+"F3.wireOp",EDGE,"E4.sketch_text.stroke-103"),sQuery(id+"F3.wireOp",EDGE,"E4.sketch_text.stroke-104"),sQuery(id+"F3.wireOp",EDGE,"E4.sketch_text.stroke-105"),sQuery(id+"F3.wireOp",EDGE,"E4.sketch_text.stroke-106"),sQuery(id+"F3.wireOp",EDGE,"E4.sketch_text.stroke-107"),sQuery(id+"F3.wireOp",EDGE,"E4.sketch_text.stroke-108"),sQuery(id+"F3.wireOp",EDGE,"E4.sketch_text.stroke-109"),sQuery(id+"F3.wireOp",EDGE,"E4.sketch_text.stroke-110"),sQuery(id+"F3.wireOp",EDGE,"E4.sketch_text.stroke-111"),sQuery(id+"F3.wireOp",EDGE,"E4.sketch_text.stroke-112"),sQuery(id+"F3.wireOp",EDGE,"E4.sketch_text.stroke-113"),sQuery(id+"F3.wireOp",EDGE,"E4.sketch_text.stroke-114"),sQuery(id+"F3.wireOp",EDGE,"E4.sketch_text.stroke-115"),sQuery(id+"F3.wireOp",EDGE,"E4.sketch_text.stroke-116"),sQuery(id+"F3.wireOp",EDGE,"E4.sketch_text.stroke-117"),sQuery(id+"F3.wireOp",EDGE,"E4.sketch_text.stroke-118"),sQuery(id+"F3.wireOp",EDGE,"E4.sketch_text.stroke-119"),sQuery(id+"F3.wireOp",EDGE,"E4.sketch_text.stroke-120"),sQuery(id+"F3.wireOp",EDGE,"E4.sketch_text.stroke-121"),sQuery(id+"F3.wireOp",EDGE,"E4.sketch_text.stroke-122"),sQuery(id+"F3.wireOp",EDGE,"E4.sketch_text.stroke-123"),sQuery(id+"F3.wireOp",EDGE,"E4.sketch_text.stroke-124"),sQuery(id+"F3.wireOp",EDGE,"E4.sketch_text.stroke-125"),sQuery(id+"F3.wireOp",EDGE,"E4.sketch_text.stroke-126"),sQuery(id+"F3.wireOp",EDGE,"E4.sketch_text.stroke-127"),sQuery(id+"F3.wireOp",EDGE,"E4.sketch_text.stroke-128"),sQuery(id+"F3.wireOp",EDGE,"E4.sketch_text.stroke-129"),sQuery(id+"F3.wireOp",EDGE,"E4.sketch_text.stroke-130"),sQuery(id+"F3.wireOp",EDGE,"E4.sketch_text.stroke-131"),sQuery(id+"F3.wireOp",EDGE,"E4.sketch_text.stroke-132"),sQuery(id+"F3.wireOp",EDGE,"E4.sketch_text.stroke-133"),sQuery(id+"F3.wireOp",EDGE,"E4.sketch_text.stroke-134"),sQuery(id+"F3.wireOp",EDGE,"E4.sketch_text.stroke-135"),sQuery(id+"F3.wireOp",EDGE,"E4.sketch_text.stroke-136"),sQuery(id+"F3.wireOp",EDGE,"E4.sketch_text.stroke-137"),sQuery(id+"F3.wireOp",EDGE,"E4.sketch_text.stroke-138"),sQuery(id+"F3.wireOp",EDGE,"E4.sketch_text.stroke-139"),sQuery(id+"F3.wireOp",EDGE,"E4.sketch_text.stroke-140"),sQuery(id+"F3.wireOp",EDGE,"E4.sketch_text.stroke-141"),sQuery(id+"F3.wireOp",EDGE,"E4.sketch_text.stroke-142"),sQuery(id+"F3.wireOp",EDGE,"E4.sketch_text.stroke-143"),sQuery(id+"F3.wireOp",EDGE,"E4.sketch_text.stroke-144"),sQuery(id+"F3.wireOp",EDGE,"E4.sketch_text.stroke-145"),sQuery(id+"F3.wireOp",EDGE,"E4.sketch_text.stroke-146"),sQuery(id+"F3.wireOp",EDGE,"E4.sketch_text.stroke-147"),sQuery(id+"F3.wireOp",EDGE,"E4.sketch_text.stroke-148"),sQuery(id+"F3.wireOp",EDGE,"E4.sketch_text.stroke-149"),sQuery(id+"F3.wireOp",EDGE,"E4.sketch_text.stroke-150"),sQuery(id+"F3.wireOp",EDGE,"E4.sketch_text.stroke-151"),sQuery(id+"F3.wireOp",EDGE,"E4.sketch_text.stroke-152"),sQuery(id+"F3.wireOp",EDGE,"E4.sketch_text.stroke-153"),sQuery(id+"F3.wireOp",EDGE,"E4.sketch_text.stroke-159"),sQuery(id+"F3.wireOp",EDGE,"E4.sketch_text.stroke-160"),sQuery(id+"F3.wireOp",EDGE,"E4.sketch_text.stroke-161"),sQuery(id+"F3.wireOp",EDGE,"E4.sketch_text.stroke-162"),sQuery(id+"F3.wireOp",EDGE,"E4.sketch_text.stroke-163"),sQuery(id+"F3.wireOp",EDGE,"E4.sketch_text.stroke-164"),sQuery(id+"F3.wireOp",EDGE,"E4.sketch_text.stroke-165"),sQuery(id+"F3.wireOp",EDGE,"E4.sketch_text.stroke-166"),sQuery(id+"F3.wireOp",EDGE,"E4.sketch_text.stroke-167"),sQuery(id+"F3.wireOp",EDGE,"E4.sketch_text.stroke-168"),sQuery(id+"F3.wireOp",EDGE,"E4.sketch_text.stroke-169"),sQuery(id+"F3.wireOp",EDGE,"E4.sketch_text.stroke-170"),sQuery(id+"F3.wireOp",EDGE,"E4.sketch_text.stroke-171"),sQuery(id+"F3.wireOp",EDGE,"E4.sketch_text.stroke-172"),sQuery(id+"F3.wireOp",EDGE,"E4.sketch_text.stroke-173"),sQuery(id+"F3.wireOp",EDGE,"E4.sketch_text.stroke-174"),sQuery(id+"F3.wireOp",EDGE,"E4.sketch_text.stroke-175"),sQuery(id+"F3.wireOp",EDGE,"E4.sketch_text.stroke-176"),sQuery(id+"F3.wireOp",EDGE,"E4.sketch_text.stroke-177"),sQuery(id+"F3.wireOp",EDGE,"E4.sketch_text.stroke-178"),sQuery(id+"F3.wireOp",EDGE,"E4.sketch_text.stroke-179"),sQuery(id+"F3.wireOp",EDGE,"E4.sketch_text.stroke-180"),sQuery(id+"F4.wireOp",EDGE,"727ac2c1-f511-4829-95a7-a443ef16a4cd"),subQ2])],"isStart":true}),makeQuery(id+"F5.opExtrude","SWEPT_FACE",FACE,{"disambiguationData":[OSD([subQ2])]})]),OD(0.0)],"derivedFrom":makeQuery(id+"F1.opExtrude","CAP_EDGE",EDGE,{"disambiguationData":[OSD([subQ0])],"isStart":false})});}
            var Q19;
            {var subQ0=sQuery(id+"F0.wireOp",EDGE,"E0.top");var subQ1=sQuery(id+"F0.wireOp",EDGE,"E0.bottom");var subQ2=sQuery(id+"F4.wireOp",EDGE,"1a034e28-a7c2-419d-97de-c33d70a47301");Q19=makeQuery(id+"F5.boolean.opBoolean","SPLIT",EDGE,{"disambiguationData":[TD([makeQuery(id+"F1.opExtrude","CAP_FACE",FACE,{"disambiguationData":[OSD([subQ1,subQ0,sQuery(id+"F0.wireOp",EDGE,"E0.left"),sQuery(id+"F0.wireOp",EDGE,"E0.right")])],"isStart":false}),makeQuery(id+"F1.opExtrude","SWEPT_FACE",FACE,{"disambiguationData":[OSD([subQ0])]}),makeQuery(id+"F5.opExtrude","CAP_FACE",FACE,{"disambiguationData":[OSD([subQ1,sQuery(id+"F2.wireOp",EDGE,"E2.sketch_text.stroke-0"),sQuery(id+"F2.wireOp",EDGE,"E2.sketch_text.stroke-1"),sQuery(id+"F2.wireOp",EDGE,"E2.sketch_text.stroke-2"),sQuery(id+"F2.wireOp",EDGE,"E2.sketch_text.stroke-3"),sQuery(id+"F2.wireOp",EDGE,"E2.sketch_text.stroke-4"),sQuery(id+"F2.wireOp",EDGE,"E2.sketch_text.stroke-5"),sQuery(id+"F2.wireOp",EDGE,"E2.sketch_text.stroke-6"),sQuery(id+"F2.wireOp",EDGE,"E2.sketch_text.stroke-7"),sQuery(id+"F2.wireOp",EDGE,"E2.sketch_text.stroke-8"),sQuery(id+"F2.wireOp",EDGE,"E2.sketch_text.stroke-9"),sQuery(id+"F2.wireOp",EDGE,"E2.sketch_text.stroke-10"),sQuery(id+"F2.wireOp",EDGE,"E2.sketch_text.stroke-11"),sQuery(id+"F2.wireOp",EDGE,"E2.sketch_text.stroke-12"),sQuery(id+"F2.wireOp",EDGE,"E2.sketch_text.stroke-13"),sQuery(id+"F2.wireOp",EDGE,"E2.sketch_text.stroke-14"),sQuery(id+"F2.wireOp",EDGE,"E2.sketch_text.stroke-15"),sQuery(id+"F2.wireOp",EDGE,"E2.sketch_text.stroke-16"),sQuery(id+"F2.wireOp",EDGE,"E2.sketch_text.stroke-17"),sQuery(id+"F2.wireOp",EDGE,"E2.sketch_text.stroke-18"),sQuery(id+"F2.wireOp",EDGE,"E2.sketch_text.stroke-19"),sQuery(id+"F2.wireOp",EDGE,"E2.sketch_text.stroke-20"),sQuery(id+"F2.wireOp",EDGE,"E2.sketch_text.stroke-21"),sQuery(id+"F2.wireOp",EDGE,"E2.sketch_text.stroke-22"),sQuery(id+"F2.wireOp",EDGE,"E2.sketch_text.stroke-23"),sQuery(id+"F2.wireOp",EDGE,"E2.sketch_text.stroke-24"),sQuery(id+"F2.wireOp",EDGE,"E2.sketch_text.stroke-25"),sQuery(id+"F2.wireOp",EDGE,"E2.sketch_text.stroke-26"),sQuery(id+"F2.wireOp",EDGE,"E2.sketch_text.stroke-27"),sQuery(id+"F2.wireOp",EDGE,"E2.sketch_text.stroke-28"),sQuery(id+"F2.wireOp",EDGE,"E2.sketch_text.stroke-29"),sQuery(id+"F2.wireOp",EDGE,"E2.sketch_text.stroke-30"),sQuery(id+"F2.wireOp",EDGE,"E2.sketch_text.stroke-31"),sQuery(id+"F2.wireOp",EDGE,"E2.sketch_text.stroke-32"),sQuery(id+"F2.wireOp",EDGE,"E2.sketch_text.stroke-33"),sQuery(id+"F2.wireOp",EDGE,"E2.sketch_text.stroke-34"),sQuery(id+"F2.wireOp",EDGE,"E2.sketch_text.stroke-35"),sQuery(id+"F2.wireOp",EDGE,"E2.sketch_text.stroke-36"),sQuery(id+"F2.wireOp",EDGE,"E2.sketch_text.stroke-37"),sQuery(id+"F2.wireOp",EDGE,"E2.sketch_text.stroke-38"),sQuery(id+"F2.wireOp",EDGE,"E2.sketch_text.stroke-39"),sQuery(id+"F2.wireOp",EDGE,"E2.sketch_text.stroke-40"),sQuery(id+"F2.wireOp",EDGE,"E2.sketch_text.stroke-41"),sQuery(id+"F2.wireOp",EDGE,"E2.sketch_text.stroke-42"),sQuery(id+"F2.wireOp",EDGE,"E2.sketch_text.stroke-43"),sQuery(id+"F2.wireOp",EDGE,"E2.sketch_text.stroke-44"),sQuery(id+"F2.wireOp",EDGE,"E2.sketch_text.stroke-45"),sQuery(id+"F2.wireOp",EDGE,"E2.sketch_text.stroke-46"),sQuery(id+"F2.wireOp",EDGE,"E2.sketch_text.stroke-47"),sQuery(id+"F2.wireOp",EDGE,"E2.sketch_text.stroke-48"),sQuery(id+"F2.wireOp",EDGE,"E2.sketch_text.stroke-49"),sQuery(id+"F2.wireOp",EDGE,"E2.sketch_text.stroke-50"),sQuery(id+"F2.wireOp",EDGE,"E2.sketch_text.stroke-51"),sQuery(id+"F2.wireOp",EDGE,"E2.sketch_text.stroke-52"),sQuery(id+"F2.wireOp",EDGE,"E2.sketch_text.stroke-53"),sQuery(id+"F2.wireOp",EDGE,"E2.sketch_text.stroke-54"),sQuery(id+"F2.wireOp",EDGE,"E2.sketch_text.stroke-55"),sQuery(id+"F2.wireOp",EDGE,"E2.sketch_text.stroke-56"),sQuery(id+"F2.wireOp",EDGE,"E2.sketch_text.stroke-57"),sQuery(id+"F2.wireOp",EDGE,"E2.sketch_text.stroke-58"),sQuery(id+"F2.wireOp",EDGE,"E2.sketch_text.stroke-59"),sQuery(id+"F2.wireOp",EDGE,"E2.sketch_text.stroke-60"),sQuery(id+"F2.wireOp",EDGE,"E2.sketch_text.stroke-61"),sQuery(id+"F2.wireOp",EDGE,"E2.sketch_text.stroke-62"),sQuery(id+"F2.wireOp",EDGE,"E2.sketch_text.stroke-63"),sQuery(id+"F2.wireOp",EDGE,"E2.sketch_text.stroke-64"),sQuery(id+"F2.wireOp",EDGE,"E2.sketch_text.stroke-65"),sQuery(id+"F2.wireOp",EDGE,"E2.sketch_text.stroke-66"),sQuery(id+"F2.wireOp",EDGE,"E2.sketch_text.stroke-67"),sQuery(id+"F2.wireOp",EDGE,"E2.sketch_text.stroke-68"),sQuery(id+"F2.wireOp",EDGE,"E2.sketch_text.stroke-69"),sQuery(id+"F2.wireOp",EDGE,"E2.sketch_text.stroke-70"),sQuery(id+"F2.wireOp",EDGE,"E2.sketch_text.stroke-71"),sQuery(id+"F2.wireOp",EDGE,"E2.sketch_text.stroke-72"),sQuery(id+"F2.wireOp",EDGE,"E2.sketch_text.stroke-73"),sQuery(id+"F2.wireOp",EDGE,"E2.sketch_text.stroke-74"),sQuery(id+"F2.wireOp",EDGE,"E2.sketch_text.stroke-75"),sQuery(id+"F2.wireOp",EDGE,"E2.sketch_text.stroke-76"),sQuery(id+"F2.wireOp",EDGE,"E2.sketch_text.stroke-77"),sQuery(id+"F2.wireOp",EDGE,"E2.sketch_text.stroke-78"),sQuery(id+"F2.wireOp",EDGE,"E2.sketch_text.stroke-79"),sQuery(id+"F2.wireOp",EDGE,"E2.sketch_text.stroke-80"),sQuery(id+"F2.wireOp",EDGE,"E2.sketch_text.stroke-81"),sQuery(id+"F2.wireOp",EDGE,"E2.sketch_text.stroke-82"),sQuery(id+"F2.wireOp",EDGE,"E2.sketch_text.stroke-83"),sQuery(id+"F2.wireOp",EDGE,"E2.sketch_text.stroke-84"),sQuery(id+"F2.wireOp",EDGE,"E2.sketch_text.stroke-85"),sQuery(id+"F2.wireOp",EDGE,"E2.sketch_text.stroke-86"),sQuery(id+"F2.wireOp",EDGE,"E2.sketch_text.stroke-87"),sQuery(id+"F2.wireOp",EDGE,"E2.sketch_text.stroke-88"),sQuery(id+"F2.wireOp",EDGE,"E2.sketch_text.stroke-89"),sQuery(id+"F2.wireOp",EDGE,"E2.sketch_text.stroke-90"),sQuery(id+"F2.wireOp",EDGE,"E2.sketch_text.stroke-91"),sQuery(id+"F2.wireOp",EDGE,"E2.sketch_text.stroke-92"),sQuery(id+"F2.wireOp",EDGE,"E2.sketch_text.stroke-93"),sQuery(id+"F2.wireOp",EDGE,"E2.sketch_text.stroke-94"),sQuery(id+"F2.wireOp",EDGE,"E2.sketch_text.stroke-95"),sQuery(id+"F2.wireOp",EDGE,"E2.sketch_text.stroke-96"),sQuery(id+"F2.wireOp",EDGE,"E2.sketch_text.stroke-97"),sQuery(id+"F2.wireOp",EDGE,"E2.sketch_text.stroke-98"),sQuery(id+"F2.wireOp",EDGE,"E2.sketch_text.stroke-99"),sQuery(id+"F2.wireOp",EDGE,"E2.sketch_text.stroke-100"),sQuery(id+"F2.wireOp",EDGE,"E2.sketch_text.stroke-101"),sQuery(id+"F2.wireOp",EDGE,"E2.sketch_text.stroke-102"),sQuery(id+"F2.wireOp",EDGE,"E2.sketch_text.stroke-103"),sQuery(id+"F2.wireOp",EDGE,"E2.sketch_text.stroke-104"),sQuery(id+"F2.wireOp",EDGE,"E2.sketch_text.stroke-105"),sQuery(id+"F2.wireOp",EDGE,"E2.sketch_text.stroke-106"),sQuery(id+"F2.wireOp",EDGE,"E2.sketch_text.stroke-107"),sQuery(id+"F2.wireOp",EDGE,"E2.sketch_text.stroke-108"),sQuery(id+"F2.wireOp",EDGE,"E2.sketch_text.stroke-109"),sQuery(id+"F2.wireOp",EDGE,"E2.sketch_text.stroke-110"),sQuery(id+"F2.wireOp",EDGE,"E2.sketch_text.stroke-111"),sQuery(id+"F2.wireOp",EDGE,"E2.sketch_text.stroke-112"),sQuery(id+"F2.wireOp",EDGE,"E2.sketch_text.stroke-113"),sQuery(id+"F2.wireOp",EDGE,"E2.sketch_text.stroke-114"),sQuery(id+"F2.wireOp",EDGE,"E2.sketch_text.stroke-115"),sQuery(id+"F2.wireOp",EDGE,"E2.sketch_text.stroke-116"),sQuery(id+"F2.wireOp",EDGE,"E2.sketch_text.stroke-117"),sQuery(id+"F2.wireOp",EDGE,"E2.sketch_text.stroke-118"),sQuery(id+"F2.wireOp",EDGE,"E2.sketch_text.stroke-119"),sQuery(id+"F2.wireOp",EDGE,"E2.sketch_text.stroke-120"),sQuery(id+"F2.wireOp",EDGE,"E2.sketch_text.stroke-121"),sQuery(id+"F2.wireOp",EDGE,"E2.sketch_text.stroke-122"),sQuery(id+"F2.wireOp",EDGE,"E2.sketch_text.stroke-123"),sQuery(id+"F2.wireOp",EDGE,"E2.sketch_text.stroke-124"),sQuery(id+"F2.wireOp",EDGE,"E2.sketch_text.stroke-125"),sQuery(id+"F2.wireOp",EDGE,"E2.sketch_text.stroke-126"),sQuery(id+"F2.wireOp",EDGE,"E2.sketch_text.stroke-127"),sQuery(id+"F2.wireOp",EDGE,"E2.sketch_text.stroke-128"),sQuery(id+"F2.wireOp",EDGE,"E2.sketch_text.stroke-129"),sQuery(id+"F2.wireOp",EDGE,"E2.sketch_text.stroke-130"),sQuery(id+"F2.wireOp",EDGE,"E2.sketch_text.stroke-131"),sQuery(id+"F2.wireOp",EDGE,"E2.sketch_text.stroke-132"),sQuery(id+"F2.wireOp",EDGE,"E2.sketch_text.stroke-133"),sQuery(id+"F2.wireOp",EDGE,"E2.sketch_text.stroke-134"),sQuery(id+"F2.wireOp",EDGE,"E2.sketch_text.stroke-135"),sQuery(id+"F2.wireOp",EDGE,"E2.sketch_text.stroke-136"),sQuery(id+"F2.wireOp",EDGE,"E2.sketch_text.stroke-137"),sQuery(id+"F2.wireOp",EDGE,"E2.sketch_text.stroke-138"),sQuery(id+"F2.wireOp",EDGE,"E2.sketch_text.stroke-139"),sQuery(id+"F2.wireOp",EDGE,"E2.sketch_text.stroke-140"),sQuery(id+"F2.wireOp",EDGE,"E2.sketch_text.stroke-141"),sQuery(id+"F2.wireOp",EDGE,"E2.sketch_text.stroke-142"),sQuery(id+"F2.wireOp",EDGE,"E2.sketch_text.stroke-143"),sQuery(id+"F2.wireOp",EDGE,"E2.sketch_text.stroke-144"),sQuery(id+"F2.wireOp",EDGE,"E2.sketch_text.stroke-145"),sQuery(id+"F2.wireOp",EDGE,"E2.sketch_text.stroke-146"),sQuery(id+"F2.wireOp",EDGE,"E2.sketch_text.stroke-147"),sQuery(id+"F2.wireOp",EDGE,"E2.sketch_text.stroke-148"),sQuery(id+"F2.wireOp",EDGE,"E2.sketch_text.stroke-149"),sQuery(id+"F2.wireOp",EDGE,"E2.sketch_text.stroke-150"),sQuery(id+"F2.wireOp",EDGE,"E2.sketch_text.stroke-151"),sQuery(id+"F2.wireOp",EDGE,"E2.sketch_text.stroke-152"),sQuery(id+"F2.wireOp",EDGE,"E2.sketch_text.stroke-153"),sQuery(id+"F2.wireOp",EDGE,"E2.sketch_text.stroke-154"),sQuery(id+"F2.wireOp",EDGE,"E2.sketch_text.stroke-155"),sQuery(id+"F2.wireOp",EDGE,"E2.sketch_text.stroke-156"),sQuery(id+"F2.wireOp",EDGE,"E2.sketch_text.stroke-157"),sQuery(id+"F2.wireOp",EDGE,"E2.sketch_text.stroke-158"),sQuery(id+"F2.wireOp",EDGE,"E2.sketch_text.stroke-159"),sQuery(id+"F2.wireOp",EDGE,"E2.sketch_text.stroke-160"),sQuery(id+"F2.wireOp",EDGE,"E2.sketch_text.stroke-161"),sQuery(id+"F2.wireOp",EDGE,"E2.sketch_text.stroke-162"),sQuery(id+"F2.wireOp",EDGE,"E2.sketch_text.stroke-163"),sQuery(id+"F2.wireOp",EDGE,"E2.sketch_text.stroke-164"),sQuery(id+"F2.wireOp",EDGE,"E2.sketch_text.stroke-165"),sQuery(id+"F2.wireOp",EDGE,"E2.sketch_text.stroke-166"),sQuery(id+"F2.wireOp",EDGE,"E2.sketch_text.stroke-167"),sQuery(id+"F2.wireOp",EDGE,"E2.sketch_text.stroke-168"),sQuery(id+"F2.wireOp",EDGE,"E2.sketch_text.stroke-169"),sQuery(id+"F2.wireOp",EDGE,"E2.sketch_text.stroke-170"),sQuery(id+"F2.wireOp",EDGE,"E2.sketch_text.stroke-171"),sQuery(id+"F2.wireOp",EDGE,"E2.sketch_text.stroke-172"),sQuery(id+"F2.wireOp",EDGE,"E2.sketch_text.stroke-173"),sQuery(id+"F3.wireOp",EDGE,"E4.sketch_text.stroke-0"),sQuery(id+"F3.wireOp",EDGE,"E4.sketch_text.stroke-1"),sQuery(id+"F3.wireOp",EDGE,"E4.sketch_text.stroke-2"),sQuery(id+"F3.wireOp",EDGE,"E4.sketch_text.stroke-3"),sQuery(id+"F3.wireOp",EDGE,"E4.sketch_text.stroke-4"),sQuery(id+"F3.wireOp",EDGE,"E4.sketch_text.stroke-5"),sQuery(id+"F3.wireOp",EDGE,"E4.sketch_text.stroke-6"),sQuery(id+"F3.wireOp",EDGE,"E4.sketch_text.stroke-7"),sQuery(id+"F3.wireOp",EDGE,"E4.sketch_text.stroke-8"),sQuery(id+"F3.wireOp",EDGE,"E4.sketch_text.stroke-9"),sQuery(id+"F3.wireOp",EDGE,"E4.sketch_text.stroke-10"),sQuery(id+"F3.wireOp",EDGE,"E4.sketch_text.stroke-11"),sQuery(id+"F3.wireOp",EDGE,"E4.sketch_text.stroke-12"),sQuery(id+"F3.wireOp",EDGE,"E4.sketch_text.stroke-13"),sQuery(id+"F3.wireOp",EDGE,"E4.sketch_text.stroke-14"),sQuery(id+"F3.wireOp",EDGE,"E4.sketch_text.stroke-15"),sQuery(id+"F3.wireOp",EDGE,"E4.sketch_text.stroke-16"),sQuery(id+"F3.wireOp",EDGE,"E4.sketch_text.stroke-17"),sQuery(id+"F3.wireOp",EDGE,"E4.sketch_text.stroke-18"),sQuery(id+"F3.wireOp",EDGE,"E4.sketch_text.stroke-19"),sQuery(id+"F3.wireOp",EDGE,"E4.sketch_text.stroke-20"),sQuery(id+"F3.wireOp",EDGE,"E4.sketch_text.stroke-21"),sQuery(id+"F3.wireOp",EDGE,"E4.sketch_text.stroke-22"),sQuery(id+"F3.wireOp",EDGE,"E4.sketch_text.stroke-23"),sQuery(id+"F3.wireOp",EDGE,"E4.sketch_text.stroke-24"),sQuery(id+"F3.wireOp",EDGE,"E4.sketch_text.stroke-25"),sQuery(id+"F3.wireOp",EDGE,"E4.sketch_text.stroke-26"),sQuery(id+"F3.wireOp",EDGE,"E4.sketch_text.stroke-27"),sQuery(id+"F3.wireOp",EDGE,"E4.sketch_text.stroke-28"),sQuery(id+"F3.wireOp",EDGE,"E4.sketch_text.stroke-29"),sQuery(id+"F3.wireOp",EDGE,"E4.sketch_text.stroke-30"),sQuery(id+"F3.wireOp",EDGE,"E4.sketch_text.stroke-31"),sQuery(id+"F3.wireOp",EDGE,"E4.sketch_text.stroke-32"),sQuery(id+"F3.wireOp",EDGE,"E4.sketch_text.stroke-33"),sQuery(id+"F3.wireOp",EDGE,"E4.sketch_text.stroke-34"),sQuery(id+"F3.wireOp",EDGE,"E4.sketch_text.stroke-35"),sQuery(id+"F3.wireOp",EDGE,"E4.sketch_text.stroke-36"),sQuery(id+"F3.wireOp",EDGE,"E4.sketch_text.stroke-37"),sQuery(id+"F3.wireOp",EDGE,"E4.sketch_text.stroke-38"),sQuery(id+"F3.wireOp",EDGE,"E4.sketch_text.stroke-39"),sQuery(id+"F3.wireOp",EDGE,"E4.sketch_text.stroke-40"),sQuery(id+"F3.wireOp",EDGE,"E4.sketch_text.stroke-41"),sQuery(id+"F3.wireOp",EDGE,"E4.sketch_text.stroke-42"),sQuery(id+"F3.wireOp",EDGE,"E4.sketch_text.stroke-43"),sQuery(id+"F3.wireOp",EDGE,"E4.sketch_text.stroke-44"),sQuery(id+"F3.wireOp",EDGE,"E4.sketch_text.stroke-45"),sQuery(id+"F3.wireOp",EDGE,"E4.sketch_text.stroke-46"),sQuery(id+"F3.wireOp",EDGE,"E4.sketch_text.stroke-47"),sQuery(id+"F3.wireOp",EDGE,"E4.sketch_text.stroke-48"),sQuery(id+"F3.wireOp",EDGE,"E4.sketch_text.stroke-49"),sQuery(id+"F3.wireOp",EDGE,"E4.sketch_text.stroke-50"),sQuery(id+"F3.wireOp",EDGE,"E4.sketch_text.stroke-51"),sQuery(id+"F3.wireOp",EDGE,"E4.sketch_text.stroke-52"),sQuery(id+"F3.wireOp",EDGE,"E4.sketch_text.stroke-53"),sQuery(id+"F3.wireOp",EDGE,"E4.sketch_text.stroke-54"),sQuery(id+"F3.wireOp",EDGE,"E4.sketch_text.stroke-55"),sQuery(id+"F3.wireOp",EDGE,"E4.sketch_text.stroke-56"),sQuery(id+"F3.wireOp",EDGE,"E4.sketch_text.stroke-57"),sQuery(id+"F3.wireOp",EDGE,"E4.sketch_text.stroke-58"),sQuery(id+"F3.wireOp",EDGE,"E4.sketch_text.stroke-59"),sQuery(id+"F3.wireOp",EDGE,"E4.sketch_text.stroke-60"),sQuery(id+"F3.wireOp",EDGE,"E4.sketch_text.stroke-61"),sQuery(id+"F3.wireOp",EDGE,"E4.sketch_text.stroke-62"),sQuery(id+"F3.wireOp",EDGE,"E4.sketch_text.stroke-71"),sQuery(id+"F3.wireOp",EDGE,"E4.sketch_text.stroke-72"),sQuery(id+"F3.wireOp",EDGE,"E4.sketch_text.stroke-73"),sQuery(id+"F3.wireOp",EDGE,"E4.sketch_text.stroke-74"),sQuery(id+"F3.wireOp",EDGE,"E4.sketch_text.stroke-75"),sQuery(id+"F3.wireOp",EDGE,"E4.sketch_text.stroke-76"),sQuery(id+"F3.wireOp",EDGE,"E4.sketch_text.stroke-77"),sQuery(id+"F3.wireOp",EDGE,"E4.sketch_text.stroke-78"),sQuery(id+"F3.wireOp",EDGE,"E4.sketch_text.stroke-79"),sQuery(id+"F3.wireOp",EDGE,"E4.sketch_text.stroke-80"),sQuery(id+"F3.wireOp",EDGE,"E4.sketch_text.stroke-81"),sQuery(id+"F3.wireOp",EDGE,"E4.sketch_text.stroke-82"),sQuery(id+"F3.wireOp",EDGE,"E4.sketch_text.stroke-83"),sQuery(id+"F3.wireOp",EDGE,"E4.sketch_text.stroke-84"),sQuery(id+"F3.wireOp",EDGE,"E4.sketch_text.stroke-85"),sQuery(id+"F3.wireOp",EDGE,"E4.sketch_text.stroke-86"),sQuery(id+"F3.wireOp",EDGE,"E4.sketch_text.stroke-87"),sQuery(id+"F3.wireOp",EDGE,"E4.sketch_text.stroke-88"),sQuery(id+"F3.wireOp",EDGE,"E4.sketch_text.stroke-89"),sQuery(id+"F3.wireOp",EDGE,"E4.sketch_text.stroke-90"),sQuery(id+"F3.wireOp",EDGE,"E4.sketch_text.stroke-91"),sQuery(id+"F3.wireOp",EDGE,"E4.sketch_text.stroke-92"),sQuery(id+"F3.wireOp",EDGE,"E4.sketch_text.stroke-93"),sQuery(id+"F3.wireOp",EDGE,"E4.sketch_text.stroke-94"),sQuery(id+"F3.wireOp",EDGE,"E4.sketch_text.stroke-95"),sQuery(id+"F3.wireOp",EDGE,"E4.sketch_text.stroke-96"),sQuery(id+"F3.wireOp",EDGE,"E4.sketch_text.stroke-97"),sQuery(id+"F3.wireOp",EDGE,"E4.sketch_text.stroke-103"),sQuery(id+"F3.wireOp",EDGE,"E4.sketch_text.stroke-104"),sQuery(id+"F3.wireOp",EDGE,"E4.sketch_text.stroke-105"),sQuery(id+"F3.wireOp",EDGE,"E4.sketch_text.stroke-106"),sQuery(id+"F3.wireOp",EDGE,"E4.sketch_text.stroke-107"),sQuery(id+"F3.wireOp",EDGE,"E4.sketch_text.stroke-108"),sQuery(id+"F3.wireOp",EDGE,"E4.sketch_text.stroke-109"),sQuery(id+"F3.wireOp",EDGE,"E4.sketch_text.stroke-110"),sQuery(id+"F3.wireOp",EDGE,"E4.sketch_text.stroke-111"),sQuery(id+"F3.wireOp",EDGE,"E4.sketch_text.stroke-112"),sQuery(id+"F3.wireOp",EDGE,"E4.sketch_text.stroke-113"),sQuery(id+"F3.wireOp",EDGE,"E4.sketch_text.stroke-114"),sQuery(id+"F3.wireOp",EDGE,"E4.sketch_text.stroke-115"),sQuery(id+"F3.wireOp",EDGE,"E4.sketch_text.stroke-116"),sQuery(id+"F3.wireOp",EDGE,"E4.sketch_text.stroke-117"),sQuery(id+"F3.wireOp",EDGE,"E4.sketch_text.stroke-118"),sQuery(id+"F3.wireOp",EDGE,"E4.sketch_text.stroke-119"),sQuery(id+"F3.wireOp",EDGE,"E4.sketch_text.stroke-120"),sQuery(id+"F3.wireOp",EDGE,"E4.sketch_text.stroke-121"),sQuery(id+"F3.wireOp",EDGE,"E4.sketch_text.stroke-122"),sQuery(id+"F3.wireOp",EDGE,"E4.sketch_text.stroke-123"),sQuery(id+"F3.wireOp",EDGE,"E4.sketch_text.stroke-124"),sQuery(id+"F3.wireOp",EDGE,"E4.sketch_text.stroke-125"),sQuery(id+"F3.wireOp",EDGE,"E4.sketch_text.stroke-126"),sQuery(id+"F3.wireOp",EDGE,"E4.sketch_text.stroke-127"),sQuery(id+"F3.wireOp",EDGE,"E4.sketch_text.stroke-128"),sQuery(id+"F3.wireOp",EDGE,"E4.sketch_text.stroke-129"),sQuery(id+"F3.wireOp",EDGE,"E4.sketch_text.stroke-130"),sQuery(id+"F3.wireOp",EDGE,"E4.sketch_text.stroke-131"),sQuery(id+"F3.wireOp",EDGE,"E4.sketch_text.stroke-132"),sQuery(id+"F3.wireOp",EDGE,"E4.sketch_text.stroke-133"),sQuery(id+"F3.wireOp",EDGE,"E4.sketch_text.stroke-134"),sQuery(id+"F3.wireOp",EDGE,"E4.sketch_text.stroke-135"),sQuery(id+"F3.wireOp",EDGE,"E4.sketch_text.stroke-136"),sQuery(id+"F3.wireOp",EDGE,"E4.sketch_text.stroke-137"),sQuery(id+"F3.wireOp",EDGE,"E4.sketch_text.stroke-138"),sQuery(id+"F3.wireOp",EDGE,"E4.sketch_text.stroke-139"),sQuery(id+"F3.wireOp",EDGE,"E4.sketch_text.stroke-140"),sQuery(id+"F3.wireOp",EDGE,"E4.sketch_text.stroke-141"),sQuery(id+"F3.wireOp",EDGE,"E4.sketch_text.stroke-142"),sQuery(id+"F3.wireOp",EDGE,"E4.sketch_text.stroke-143"),sQuery(id+"F3.wireOp",EDGE,"E4.sketch_text.stroke-144"),sQuery(id+"F3.wireOp",EDGE,"E4.sketch_text.stroke-145"),sQuery(id+"F3.wireOp",EDGE,"E4.sketch_text.stroke-146"),sQuery(id+"F3.wireOp",EDGE,"E4.sketch_text.stroke-147"),sQuery(id+"F3.wireOp",EDGE,"E4.sketch_text.stroke-148"),sQuery(id+"F3.wireOp",EDGE,"E4.sketch_text.stroke-149"),sQuery(id+"F3.wireOp",EDGE,"E4.sketch_text.stroke-150"),sQuery(id+"F3.wireOp",EDGE,"E4.sketch_text.stroke-151"),sQuery(id+"F3.wireOp",EDGE,"E4.sketch_text.stroke-152"),sQuery(id+"F3.wireOp",EDGE,"E4.sketch_text.stroke-153"),sQuery(id+"F3.wireOp",EDGE,"E4.sketch_text.stroke-159"),sQuery(id+"F3.wireOp",EDGE,"E4.sketch_text.stroke-160"),sQuery(id+"F3.wireOp",EDGE,"E4.sketch_text.stroke-161"),sQuery(id+"F3.wireOp",EDGE,"E4.sketch_text.stroke-162"),sQuery(id+"F3.wireOp",EDGE,"E4.sketch_text.stroke-163"),sQuery(id+"F3.wireOp",EDGE,"E4.sketch_text.stroke-164"),sQuery(id+"F3.wireOp",EDGE,"E4.sketch_text.stroke-165"),sQuery(id+"F3.wireOp",EDGE,"E4.sketch_text.stroke-166"),sQuery(id+"F3.wireOp",EDGE,"E4.sketch_text.stroke-167"),sQuery(id+"F3.wireOp",EDGE,"E4.sketch_text.stroke-168"),sQuery(id+"F3.wireOp",EDGE,"E4.sketch_text.stroke-169"),sQuery(id+"F3.wireOp",EDGE,"E4.sketch_text.stroke-170"),sQuery(id+"F3.wireOp",EDGE,"E4.sketch_text.stroke-171"),sQuery(id+"F3.wireOp",EDGE,"E4.sketch_text.stroke-172"),sQuery(id+"F3.wireOp",EDGE,"E4.sketch_text.stroke-173"),sQuery(id+"F3.wireOp",EDGE,"E4.sketch_text.stroke-174"),sQuery(id+"F3.wireOp",EDGE,"E4.sketch_text.stroke-175"),sQuery(id+"F3.wireOp",EDGE,"E4.sketch_text.stroke-176"),sQuery(id+"F3.wireOp",EDGE,"E4.sketch_text.stroke-177"),sQuery(id+"F3.wireOp",EDGE,"E4.sketch_text.stroke-178"),sQuery(id+"F3.wireOp",EDGE,"E4.sketch_text.stroke-179"),sQuery(id+"F3.wireOp",EDGE,"E4.sketch_text.stroke-180"),sQuery(id+"F4.wireOp",EDGE,"727ac2c1-f511-4829-95a7-a443ef16a4cd"),subQ2])],"isStart":true}),makeQuery(id+"F5.opExtrude","SWEPT_FACE",FACE,{"disambiguationData":[OSD([subQ2])]})]),OD(1.0)],"derivedFrom":makeQuery(id+"F1.opExtrude","CAP_EDGE",EDGE,{"disambiguationData":[OSD([subQ0])],"isStart":false})});}
            var Q20;
            {var subQ0=sQuery(id+"F0.wireOp",EDGE,"E0.top");var subQ1=sQuery(id+"F0.wireOp",EDGE,"E0.bottom");var subQ2=sQuery(id+"F4.wireOp",EDGE,"E30");Q20=makeQuery(id+"F5.boolean.opBoolean","SPLIT",EDGE,{"disambiguationData":[TD([makeQuery(id+"F1.opExtrude","CAP_FACE",FACE,{"disambiguationData":[OSD([subQ1,subQ0,sQuery(id+"F0.wireOp",EDGE,"E0.left"),sQuery(id+"F0.wireOp",EDGE,"E0.right")])],"isStart":false}),makeQuery(id+"F1.opExtrude","SWEPT_FACE",FACE,{"disambiguationData":[OSD([subQ0])]}),makeQuery(id+"F5.opExtrude","SWEPT_FACE",FACE,{"disambiguationData":[OSD([subQ2])]}),makeQuery(id+"F5.opExtrude","CAP_FACE",FACE,{"disambiguationData":[OSD([subQ1,sQuery(id+"F2.wireOp",EDGE,"E2.sketch_text.stroke-0"),sQuery(id+"F2.wireOp",EDGE,"E2.sketch_text.stroke-1"),sQuery(id+"F2.wireOp",EDGE,"E2.sketch_text.stroke-2"),sQuery(id+"F2.wireOp",EDGE,"E2.sketch_text.stroke-3"),sQuery(id+"F2.wireOp",EDGE,"E2.sketch_text.stroke-4"),sQuery(id+"F2.wireOp",EDGE,"E2.sketch_text.stroke-5"),sQuery(id+"F2.wireOp",EDGE,"E2.sketch_text.stroke-6"),sQuery(id+"F2.wireOp",EDGE,"E2.sketch_text.stroke-7"),sQuery(id+"F2.wireOp",EDGE,"E2.sketch_text.stroke-8"),sQuery(id+"F2.wireOp",EDGE,"E2.sketch_text.stroke-9"),sQuery(id+"F2.wireOp",EDGE,"E2.sketch_text.stroke-10"),sQuery(id+"F2.wireOp",EDGE,"E2.sketch_text.stroke-11"),sQuery(id+"F2.wireOp",EDGE,"E2.sketch_text.stroke-12"),sQuery(id+"F2.wireOp",EDGE,"E2.sketch_text.stroke-13"),sQuery(id+"F2.wireOp",EDGE,"E2.sketch_text.stroke-14"),sQuery(id+"F2.wireOp",EDGE,"E2.sketch_text.stroke-15"),sQuery(id+"F2.wireOp",EDGE,"E2.sketch_text.stroke-16"),sQuery(id+"F2.wireOp",EDGE,"E2.sketch_text.stroke-17"),sQuery(id+"F2.wireOp",EDGE,"E2.sketch_text.stroke-18"),sQuery(id+"F2.wireOp",EDGE,"E2.sketch_text.stroke-19"),sQuery(id+"F2.wireOp",EDGE,"E2.sketch_text.stroke-20"),sQuery(id+"F2.wireOp",EDGE,"E2.sketch_text.stroke-21"),sQuery(id+"F2.wireOp",EDGE,"E2.sketch_text.stroke-22"),sQuery(id+"F2.wireOp",EDGE,"E2.sketch_text.stroke-23"),sQuery(id+"F2.wireOp",EDGE,"E2.sketch_text.stroke-24"),sQuery(id+"F2.wireOp",EDGE,"E2.sketch_text.stroke-25"),sQuery(id+"F2.wireOp",EDGE,"E2.sketch_text.stroke-26"),sQuery(id+"F2.wireOp",EDGE,"E2.sketch_text.stroke-27"),sQuery(id+"F2.wireOp",EDGE,"E2.sketch_text.stroke-28"),sQuery(id+"F2.wireOp",EDGE,"E2.sketch_text.stroke-29"),sQuery(id+"F2.wireOp",EDGE,"E2.sketch_text.stroke-30"),sQuery(id+"F2.wireOp",EDGE,"E2.sketch_text.stroke-31"),sQuery(id+"F2.wireOp",EDGE,"E2.sketch_text.stroke-32"),sQuery(id+"F2.wireOp",EDGE,"E2.sketch_text.stroke-33"),sQuery(id+"F2.wireOp",EDGE,"E2.sketch_text.stroke-34"),sQuery(id+"F2.wireOp",EDGE,"E2.sketch_text.stroke-35"),sQuery(id+"F2.wireOp",EDGE,"E2.sketch_text.stroke-36"),sQuery(id+"F2.wireOp",EDGE,"E2.sketch_text.stroke-37"),sQuery(id+"F2.wireOp",EDGE,"E2.sketch_text.stroke-38"),sQuery(id+"F2.wireOp",EDGE,"E2.sketch_text.stroke-39"),sQuery(id+"F2.wireOp",EDGE,"E2.sketch_text.stroke-40"),sQuery(id+"F2.wireOp",EDGE,"E2.sketch_text.stroke-41"),sQuery(id+"F2.wireOp",EDGE,"E2.sketch_text.stroke-42"),sQuery(id+"F2.wireOp",EDGE,"E2.sketch_text.stroke-43"),sQuery(id+"F2.wireOp",EDGE,"E2.sketch_text.stroke-44"),sQuery(id+"F2.wireOp",EDGE,"E2.sketch_text.stroke-45"),sQuery(id+"F2.wireOp",EDGE,"E2.sketch_text.stroke-46"),sQuery(id+"F2.wireOp",EDGE,"E2.sketch_text.stroke-47"),sQuery(id+"F2.wireOp",EDGE,"E2.sketch_text.stroke-48"),sQuery(id+"F2.wireOp",EDGE,"E2.sketch_text.stroke-49"),sQuery(id+"F2.wireOp",EDGE,"E2.sketch_text.stroke-50"),sQuery(id+"F2.wireOp",EDGE,"E2.sketch_text.stroke-51"),sQuery(id+"F2.wireOp",EDGE,"E2.sketch_text.stroke-52"),sQuery(id+"F2.wireOp",EDGE,"E2.sketch_text.stroke-53"),sQuery(id+"F2.wireOp",EDGE,"E2.sketch_text.stroke-54"),sQuery(id+"F2.wireOp",EDGE,"E2.sketch_text.stroke-55"),sQuery(id+"F2.wireOp",EDGE,"E2.sketch_text.stroke-56"),sQuery(id+"F2.wireOp",EDGE,"E2.sketch_text.stroke-57"),sQuery(id+"F2.wireOp",EDGE,"E2.sketch_text.stroke-58"),sQuery(id+"F2.wireOp",EDGE,"E2.sketch_text.stroke-59"),sQuery(id+"F2.wireOp",EDGE,"E2.sketch_text.stroke-60"),sQuery(id+"F2.wireOp",EDGE,"E2.sketch_text.stroke-61"),sQuery(id+"F2.wireOp",EDGE,"E2.sketch_text.stroke-62"),sQuery(id+"F2.wireOp",EDGE,"E2.sketch_text.stroke-63"),sQuery(id+"F2.wireOp",EDGE,"E2.sketch_text.stroke-64"),sQuery(id+"F2.wireOp",EDGE,"E2.sketch_text.stroke-65"),sQuery(id+"F2.wireOp",EDGE,"E2.sketch_text.stroke-66"),sQuery(id+"F2.wireOp",EDGE,"E2.sketch_text.stroke-67"),sQuery(id+"F2.wireOp",EDGE,"E2.sketch_text.stroke-68"),sQuery(id+"F2.wireOp",EDGE,"E2.sketch_text.stroke-69"),sQuery(id+"F2.wireOp",EDGE,"E2.sketch_text.stroke-70"),sQuery(id+"F2.wireOp",EDGE,"E2.sketch_text.stroke-71"),sQuery(id+"F2.wireOp",EDGE,"E2.sketch_text.stroke-72"),sQuery(id+"F2.wireOp",EDGE,"E2.sketch_text.stroke-73"),sQuery(id+"F2.wireOp",EDGE,"E2.sketch_text.stroke-74"),sQuery(id+"F2.wireOp",EDGE,"E2.sketch_text.stroke-75"),sQuery(id+"F2.wireOp",EDGE,"E2.sketch_text.stroke-76"),sQuery(id+"F2.wireOp",EDGE,"E2.sketch_text.stroke-77"),sQuery(id+"F2.wireOp",EDGE,"E2.sketch_text.stroke-78"),sQuery(id+"F2.wireOp",EDGE,"E2.sketch_text.stroke-79"),sQuery(id+"F2.wireOp",EDGE,"E2.sketch_text.stroke-80"),sQuery(id+"F2.wireOp",EDGE,"E2.sketch_text.stroke-81"),sQuery(id+"F2.wireOp",EDGE,"E2.sketch_text.stroke-82"),sQuery(id+"F2.wireOp",EDGE,"E2.sketch_text.stroke-83"),sQuery(id+"F2.wireOp",EDGE,"E2.sketch_text.stroke-84"),sQuery(id+"F2.wireOp",EDGE,"E2.sketch_text.stroke-85"),sQuery(id+"F2.wireOp",EDGE,"E2.sketch_text.stroke-86"),sQuery(id+"F2.wireOp",EDGE,"E2.sketch_text.stroke-87"),sQuery(id+"F2.wireOp",EDGE,"E2.sketch_text.stroke-88"),sQuery(id+"F2.wireOp",EDGE,"E2.sketch_text.stroke-89"),sQuery(id+"F2.wireOp",EDGE,"E2.sketch_text.stroke-90"),sQuery(id+"F2.wireOp",EDGE,"E2.sketch_text.stroke-91"),sQuery(id+"F2.wireOp",EDGE,"E2.sketch_text.stroke-92"),sQuery(id+"F2.wireOp",EDGE,"E2.sketch_text.stroke-93"),sQuery(id+"F2.wireOp",EDGE,"E2.sketch_text.stroke-94"),sQuery(id+"F2.wireOp",EDGE,"E2.sketch_text.stroke-95"),sQuery(id+"F2.wireOp",EDGE,"E2.sketch_text.stroke-96"),sQuery(id+"F2.wireOp",EDGE,"E2.sketch_text.stroke-97"),sQuery(id+"F2.wireOp",EDGE,"E2.sketch_text.stroke-98"),sQuery(id+"F2.wireOp",EDGE,"E2.sketch_text.stroke-99"),sQuery(id+"F2.wireOp",EDGE,"E2.sketch_text.stroke-100"),sQuery(id+"F2.wireOp",EDGE,"E2.sketch_text.stroke-101"),sQuery(id+"F2.wireOp",EDGE,"E2.sketch_text.stroke-102"),sQuery(id+"F2.wireOp",EDGE,"E2.sketch_text.stroke-103"),sQuery(id+"F2.wireOp",EDGE,"E2.sketch_text.stroke-104"),sQuery(id+"F2.wireOp",EDGE,"E2.sketch_text.stroke-105"),sQuery(id+"F2.wireOp",EDGE,"E2.sketch_text.stroke-106"),sQuery(id+"F2.wireOp",EDGE,"E2.sketch_text.stroke-107"),sQuery(id+"F2.wireOp",EDGE,"E2.sketch_text.stroke-108"),sQuery(id+"F2.wireOp",EDGE,"E2.sketch_text.stroke-109"),sQuery(id+"F2.wireOp",EDGE,"E2.sketch_text.stroke-110"),sQuery(id+"F2.wireOp",EDGE,"E2.sketch_text.stroke-111"),sQuery(id+"F2.wireOp",EDGE,"E2.sketch_text.stroke-112"),sQuery(id+"F2.wireOp",EDGE,"E2.sketch_text.stroke-113"),sQuery(id+"F2.wireOp",EDGE,"E2.sketch_text.stroke-114"),sQuery(id+"F2.wireOp",EDGE,"E2.sketch_text.stroke-115"),sQuery(id+"F2.wireOp",EDGE,"E2.sketch_text.stroke-116"),sQuery(id+"F2.wireOp",EDGE,"E2.sketch_text.stroke-117"),sQuery(id+"F2.wireOp",EDGE,"E2.sketch_text.stroke-118"),sQuery(id+"F2.wireOp",EDGE,"E2.sketch_text.stroke-119"),sQuery(id+"F2.wireOp",EDGE,"E2.sketch_text.stroke-120"),sQuery(id+"F2.wireOp",EDGE,"E2.sketch_text.stroke-121"),sQuery(id+"F2.wireOp",EDGE,"E2.sketch_text.stroke-122"),sQuery(id+"F2.wireOp",EDGE,"E2.sketch_text.stroke-123"),sQuery(id+"F2.wireOp",EDGE,"E2.sketch_text.stroke-124"),sQuery(id+"F2.wireOp",EDGE,"E2.sketch_text.stroke-125"),sQuery(id+"F2.wireOp",EDGE,"E2.sketch_text.stroke-126"),sQuery(id+"F2.wireOp",EDGE,"E2.sketch_text.stroke-127"),sQuery(id+"F2.wireOp",EDGE,"E2.sketch_text.stroke-128"),sQuery(id+"F2.wireOp",EDGE,"E2.sketch_text.stroke-129"),sQuery(id+"F2.wireOp",EDGE,"E2.sketch_text.stroke-130"),sQuery(id+"F2.wireOp",EDGE,"E2.sketch_text.stroke-131"),sQuery(id+"F2.wireOp",EDGE,"E2.sketch_text.stroke-132"),sQuery(id+"F2.wireOp",EDGE,"E2.sketch_text.stroke-133"),sQuery(id+"F2.wireOp",EDGE,"E2.sketch_text.stroke-134"),sQuery(id+"F2.wireOp",EDGE,"E2.sketch_text.stroke-135"),sQuery(id+"F2.wireOp",EDGE,"E2.sketch_text.stroke-136"),sQuery(id+"F2.wireOp",EDGE,"E2.sketch_text.stroke-137"),sQuery(id+"F2.wireOp",EDGE,"E2.sketch_text.stroke-138"),sQuery(id+"F2.wireOp",EDGE,"E2.sketch_text.stroke-139"),sQuery(id+"F2.wireOp",EDGE,"E2.sketch_text.stroke-140"),sQuery(id+"F2.wireOp",EDGE,"E2.sketch_text.stroke-141"),sQuery(id+"F2.wireOp",EDGE,"E2.sketch_text.stroke-142"),sQuery(id+"F2.wireOp",EDGE,"E2.sketch_text.stroke-143"),sQuery(id+"F2.wireOp",EDGE,"E2.sketch_text.stroke-144"),sQuery(id+"F2.wireOp",EDGE,"E2.sketch_text.stroke-145"),sQuery(id+"F2.wireOp",EDGE,"E2.sketch_text.stroke-146"),sQuery(id+"F2.wireOp",EDGE,"E2.sketch_text.stroke-147"),sQuery(id+"F2.wireOp",EDGE,"E2.sketch_text.stroke-148"),sQuery(id+"F2.wireOp",EDGE,"E2.sketch_text.stroke-149"),sQuery(id+"F2.wireOp",EDGE,"E2.sketch_text.stroke-150"),sQuery(id+"F2.wireOp",EDGE,"E2.sketch_text.stroke-151"),sQuery(id+"F2.wireOp",EDGE,"E2.sketch_text.stroke-152"),sQuery(id+"F2.wireOp",EDGE,"E2.sketch_text.stroke-153"),sQuery(id+"F2.wireOp",EDGE,"E2.sketch_text.stroke-154"),sQuery(id+"F2.wireOp",EDGE,"E2.sketch_text.stroke-155"),sQuery(id+"F2.wireOp",EDGE,"E2.sketch_text.stroke-156"),sQuery(id+"F2.wireOp",EDGE,"E2.sketch_text.stroke-157"),sQuery(id+"F2.wireOp",EDGE,"E2.sketch_text.stroke-158"),sQuery(id+"F2.wireOp",EDGE,"E2.sketch_text.stroke-159"),sQuery(id+"F2.wireOp",EDGE,"E2.sketch_text.stroke-160"),sQuery(id+"F2.wireOp",EDGE,"E2.sketch_text.stroke-161"),sQuery(id+"F2.wireOp",EDGE,"E2.sketch_text.stroke-162"),sQuery(id+"F2.wireOp",EDGE,"E2.sketch_text.stroke-163"),sQuery(id+"F2.wireOp",EDGE,"E2.sketch_text.stroke-164"),sQuery(id+"F2.wireOp",EDGE,"E2.sketch_text.stroke-165"),sQuery(id+"F2.wireOp",EDGE,"E2.sketch_text.stroke-166"),sQuery(id+"F2.wireOp",EDGE,"E2.sketch_text.stroke-167"),sQuery(id+"F2.wireOp",EDGE,"E2.sketch_text.stroke-168"),sQuery(id+"F2.wireOp",EDGE,"E2.sketch_text.stroke-169"),sQuery(id+"F2.wireOp",EDGE,"E2.sketch_text.stroke-170"),sQuery(id+"F2.wireOp",EDGE,"E2.sketch_text.stroke-171"),sQuery(id+"F2.wireOp",EDGE,"E2.sketch_text.stroke-172"),sQuery(id+"F2.wireOp",EDGE,"E2.sketch_text.stroke-173"),sQuery(id+"F3.wireOp",EDGE,"E4.sketch_text.stroke-0"),sQuery(id+"F3.wireOp",EDGE,"E4.sketch_text.stroke-1"),sQuery(id+"F3.wireOp",EDGE,"E4.sketch_text.stroke-2"),sQuery(id+"F3.wireOp",EDGE,"E4.sketch_text.stroke-3"),sQuery(id+"F3.wireOp",EDGE,"E4.sketch_text.stroke-4"),sQuery(id+"F3.wireOp",EDGE,"E4.sketch_text.stroke-5"),sQuery(id+"F3.wireOp",EDGE,"E4.sketch_text.stroke-6"),sQuery(id+"F3.wireOp",EDGE,"E4.sketch_text.stroke-7"),sQuery(id+"F3.wireOp",EDGE,"E4.sketch_text.stroke-8"),sQuery(id+"F3.wireOp",EDGE,"E4.sketch_text.stroke-9"),sQuery(id+"F3.wireOp",EDGE,"E4.sketch_text.stroke-10"),sQuery(id+"F3.wireOp",EDGE,"E4.sketch_text.stroke-11"),sQuery(id+"F3.wireOp",EDGE,"E4.sketch_text.stroke-12"),sQuery(id+"F3.wireOp",EDGE,"E4.sketch_text.stroke-13"),sQuery(id+"F3.wireOp",EDGE,"E4.sketch_text.stroke-14"),sQuery(id+"F3.wireOp",EDGE,"E4.sketch_text.stroke-15"),sQuery(id+"F3.wireOp",EDGE,"E4.sketch_text.stroke-16"),sQuery(id+"F3.wireOp",EDGE,"E4.sketch_text.stroke-17"),sQuery(id+"F3.wireOp",EDGE,"E4.sketch_text.stroke-18"),sQuery(id+"F3.wireOp",EDGE,"E4.sketch_text.stroke-19"),sQuery(id+"F3.wireOp",EDGE,"E4.sketch_text.stroke-20"),sQuery(id+"F3.wireOp",EDGE,"E4.sketch_text.stroke-21"),sQuery(id+"F3.wireOp",EDGE,"E4.sketch_text.stroke-22"),sQuery(id+"F3.wireOp",EDGE,"E4.sketch_text.stroke-23"),sQuery(id+"F3.wireOp",EDGE,"E4.sketch_text.stroke-24"),sQuery(id+"F3.wireOp",EDGE,"E4.sketch_text.stroke-25"),sQuery(id+"F3.wireOp",EDGE,"E4.sketch_text.stroke-26"),sQuery(id+"F3.wireOp",EDGE,"E4.sketch_text.stroke-27"),sQuery(id+"F3.wireOp",EDGE,"E4.sketch_text.stroke-28"),sQuery(id+"F3.wireOp",EDGE,"E4.sketch_text.stroke-29"),sQuery(id+"F3.wireOp",EDGE,"E4.sketch_text.stroke-30"),sQuery(id+"F3.wireOp",EDGE,"E4.sketch_text.stroke-31"),sQuery(id+"F3.wireOp",EDGE,"E4.sketch_text.stroke-32"),sQuery(id+"F3.wireOp",EDGE,"E4.sketch_text.stroke-33"),sQuery(id+"F3.wireOp",EDGE,"E4.sketch_text.stroke-34"),sQuery(id+"F3.wireOp",EDGE,"E4.sketch_text.stroke-35"),sQuery(id+"F3.wireOp",EDGE,"E4.sketch_text.stroke-36"),sQuery(id+"F3.wireOp",EDGE,"E4.sketch_text.stroke-37"),sQuery(id+"F3.wireOp",EDGE,"E4.sketch_text.stroke-38"),sQuery(id+"F3.wireOp",EDGE,"E4.sketch_text.stroke-39"),sQuery(id+"F3.wireOp",EDGE,"E4.sketch_text.stroke-40"),sQuery(id+"F3.wireOp",EDGE,"E4.sketch_text.stroke-41"),sQuery(id+"F3.wireOp",EDGE,"E4.sketch_text.stroke-42"),sQuery(id+"F3.wireOp",EDGE,"E4.sketch_text.stroke-43"),sQuery(id+"F3.wireOp",EDGE,"E4.sketch_text.stroke-44"),sQuery(id+"F3.wireOp",EDGE,"E4.sketch_text.stroke-45"),sQuery(id+"F3.wireOp",EDGE,"E4.sketch_text.stroke-46"),sQuery(id+"F3.wireOp",EDGE,"E4.sketch_text.stroke-47"),sQuery(id+"F3.wireOp",EDGE,"E4.sketch_text.stroke-48"),sQuery(id+"F3.wireOp",EDGE,"E4.sketch_text.stroke-49"),sQuery(id+"F3.wireOp",EDGE,"E4.sketch_text.stroke-50"),sQuery(id+"F3.wireOp",EDGE,"E4.sketch_text.stroke-51"),sQuery(id+"F3.wireOp",EDGE,"E4.sketch_text.stroke-52"),sQuery(id+"F3.wireOp",EDGE,"E4.sketch_text.stroke-53"),sQuery(id+"F3.wireOp",EDGE,"E4.sketch_text.stroke-54"),sQuery(id+"F3.wireOp",EDGE,"E4.sketch_text.stroke-55"),sQuery(id+"F3.wireOp",EDGE,"E4.sketch_text.stroke-56"),sQuery(id+"F3.wireOp",EDGE,"E4.sketch_text.stroke-57"),sQuery(id+"F3.wireOp",EDGE,"E4.sketch_text.stroke-58"),sQuery(id+"F3.wireOp",EDGE,"E4.sketch_text.stroke-59"),sQuery(id+"F3.wireOp",EDGE,"E4.sketch_text.stroke-60"),sQuery(id+"F3.wireOp",EDGE,"E4.sketch_text.stroke-61"),sQuery(id+"F3.wireOp",EDGE,"E4.sketch_text.stroke-62"),sQuery(id+"F3.wireOp",EDGE,"E4.sketch_text.stroke-71"),sQuery(id+"F3.wireOp",EDGE,"E4.sketch_text.stroke-72"),sQuery(id+"F3.wireOp",EDGE,"E4.sketch_text.stroke-73"),sQuery(id+"F3.wireOp",EDGE,"E4.sketch_text.stroke-74"),sQuery(id+"F3.wireOp",EDGE,"E4.sketch_text.stroke-75"),sQuery(id+"F3.wireOp",EDGE,"E4.sketch_text.stroke-76"),sQuery(id+"F3.wireOp",EDGE,"E4.sketch_text.stroke-77"),sQuery(id+"F3.wireOp",EDGE,"E4.sketch_text.stroke-78"),sQuery(id+"F3.wireOp",EDGE,"E4.sketch_text.stroke-79"),sQuery(id+"F3.wireOp",EDGE,"E4.sketch_text.stroke-80"),sQuery(id+"F3.wireOp",EDGE,"E4.sketch_text.stroke-81"),sQuery(id+"F3.wireOp",EDGE,"E4.sketch_text.stroke-82"),sQuery(id+"F3.wireOp",EDGE,"E4.sketch_text.stroke-83"),sQuery(id+"F3.wireOp",EDGE,"E4.sketch_text.stroke-84"),sQuery(id+"F3.wireOp",EDGE,"E4.sketch_text.stroke-85"),sQuery(id+"F3.wireOp",EDGE,"E4.sketch_text.stroke-86"),sQuery(id+"F3.wireOp",EDGE,"E4.sketch_text.stroke-87"),sQuery(id+"F3.wireOp",EDGE,"E4.sketch_text.stroke-88"),sQuery(id+"F3.wireOp",EDGE,"E4.sketch_text.stroke-89"),sQuery(id+"F3.wireOp",EDGE,"E4.sketch_text.stroke-90"),sQuery(id+"F3.wireOp",EDGE,"E4.sketch_text.stroke-91"),sQuery(id+"F3.wireOp",EDGE,"E4.sketch_text.stroke-92"),sQuery(id+"F3.wireOp",EDGE,"E4.sketch_text.stroke-93"),sQuery(id+"F3.wireOp",EDGE,"E4.sketch_text.stroke-94"),sQuery(id+"F3.wireOp",EDGE,"E4.sketch_text.stroke-95"),sQuery(id+"F3.wireOp",EDGE,"E4.sketch_text.stroke-96"),sQuery(id+"F3.wireOp",EDGE,"E4.sketch_text.stroke-97"),sQuery(id+"F3.wireOp",EDGE,"E4.sketch_text.stroke-103"),sQuery(id+"F3.wireOp",EDGE,"E4.sketch_text.stroke-104"),sQuery(id+"F3.wireOp",EDGE,"E4.sketch_text.stroke-105"),sQuery(id+"F3.wireOp",EDGE,"E4.sketch_text.stroke-106"),sQuery(id+"F3.wireOp",EDGE,"E4.sketch_text.stroke-107"),sQuery(id+"F3.wireOp",EDGE,"E4.sketch_text.stroke-108"),sQuery(id+"F3.wireOp",EDGE,"E4.sketch_text.stroke-109"),sQuery(id+"F3.wireOp",EDGE,"E4.sketch_text.stroke-110"),sQuery(id+"F3.wireOp",EDGE,"E4.sketch_text.stroke-111"),sQuery(id+"F3.wireOp",EDGE,"E4.sketch_text.stroke-112"),sQuery(id+"F3.wireOp",EDGE,"E4.sketch_text.stroke-113"),sQuery(id+"F3.wireOp",EDGE,"E4.sketch_text.stroke-114"),sQuery(id+"F3.wireOp",EDGE,"E4.sketch_text.stroke-115"),sQuery(id+"F3.wireOp",EDGE,"E4.sketch_text.stroke-116"),sQuery(id+"F3.wireOp",EDGE,"E4.sketch_text.stroke-117"),sQuery(id+"F3.wireOp",EDGE,"E4.sketch_text.stroke-118"),sQuery(id+"F3.wireOp",EDGE,"E4.sketch_text.stroke-119"),sQuery(id+"F3.wireOp",EDGE,"E4.sketch_text.stroke-120"),sQuery(id+"F3.wireOp",EDGE,"E4.sketch_text.stroke-121"),sQuery(id+"F3.wireOp",EDGE,"E4.sketch_text.stroke-122"),sQuery(id+"F3.wireOp",EDGE,"E4.sketch_text.stroke-123"),sQuery(id+"F3.wireOp",EDGE,"E4.sketch_text.stroke-124"),sQuery(id+"F3.wireOp",EDGE,"E4.sketch_text.stroke-125"),sQuery(id+"F3.wireOp",EDGE,"E4.sketch_text.stroke-126"),sQuery(id+"F3.wireOp",EDGE,"E4.sketch_text.stroke-127"),sQuery(id+"F3.wireOp",EDGE,"E4.sketch_text.stroke-128"),sQuery(id+"F3.wireOp",EDGE,"E4.sketch_text.stroke-129"),sQuery(id+"F3.wireOp",EDGE,"E4.sketch_text.stroke-130"),sQuery(id+"F3.wireOp",EDGE,"E4.sketch_text.stroke-131"),sQuery(id+"F3.wireOp",EDGE,"E4.sketch_text.stroke-132"),sQuery(id+"F3.wireOp",EDGE,"E4.sketch_text.stroke-133"),sQuery(id+"F3.wireOp",EDGE,"E4.sketch_text.stroke-134"),sQuery(id+"F3.wireOp",EDGE,"E4.sketch_text.stroke-135"),sQuery(id+"F3.wireOp",EDGE,"E4.sketch_text.stroke-136"),sQuery(id+"F3.wireOp",EDGE,"E4.sketch_text.stroke-137"),sQuery(id+"F3.wireOp",EDGE,"E4.sketch_text.stroke-138"),sQuery(id+"F3.wireOp",EDGE,"E4.sketch_text.stroke-139"),sQuery(id+"F3.wireOp",EDGE,"E4.sketch_text.stroke-140"),sQuery(id+"F3.wireOp",EDGE,"E4.sketch_text.stroke-141"),sQuery(id+"F3.wireOp",EDGE,"E4.sketch_text.stroke-142"),sQuery(id+"F3.wireOp",EDGE,"E4.sketch_text.stroke-143"),sQuery(id+"F3.wireOp",EDGE,"E4.sketch_text.stroke-144"),sQuery(id+"F3.wireOp",EDGE,"E4.sketch_text.stroke-145"),sQuery(id+"F3.wireOp",EDGE,"E4.sketch_text.stroke-146"),sQuery(id+"F3.wireOp",EDGE,"E4.sketch_text.stroke-147"),sQuery(id+"F3.wireOp",EDGE,"E4.sketch_text.stroke-148"),sQuery(id+"F3.wireOp",EDGE,"E4.sketch_text.stroke-149"),sQuery(id+"F3.wireOp",EDGE,"E4.sketch_text.stroke-150"),sQuery(id+"F3.wireOp",EDGE,"E4.sketch_text.stroke-151"),sQuery(id+"F3.wireOp",EDGE,"E4.sketch_text.stroke-152"),sQuery(id+"F3.wireOp",EDGE,"E4.sketch_text.stroke-153"),sQuery(id+"F3.wireOp",EDGE,"E4.sketch_text.stroke-159"),sQuery(id+"F3.wireOp",EDGE,"E4.sketch_text.stroke-160"),sQuery(id+"F3.wireOp",EDGE,"E4.sketch_text.stroke-161"),sQuery(id+"F3.wireOp",EDGE,"E4.sketch_text.stroke-162"),sQuery(id+"F3.wireOp",EDGE,"E4.sketch_text.stroke-163"),sQuery(id+"F3.wireOp",EDGE,"E4.sketch_text.stroke-164"),sQuery(id+"F3.wireOp",EDGE,"E4.sketch_text.stroke-165"),sQuery(id+"F3.wireOp",EDGE,"E4.sketch_text.stroke-166"),sQuery(id+"F3.wireOp",EDGE,"E4.sketch_text.stroke-167"),sQuery(id+"F3.wireOp",EDGE,"E4.sketch_text.stroke-168"),sQuery(id+"F3.wireOp",EDGE,"E4.sketch_text.stroke-169"),sQuery(id+"F3.wireOp",EDGE,"E4.sketch_text.stroke-170"),sQuery(id+"F3.wireOp",EDGE,"E4.sketch_text.stroke-171"),sQuery(id+"F3.wireOp",EDGE,"E4.sketch_text.stroke-172"),sQuery(id+"F3.wireOp",EDGE,"E4.sketch_text.stroke-173"),sQuery(id+"F3.wireOp",EDGE,"E4.sketch_text.stroke-174"),sQuery(id+"F3.wireOp",EDGE,"E4.sketch_text.stroke-175"),sQuery(id+"F3.wireOp",EDGE,"E4.sketch_text.stroke-176"),sQuery(id+"F3.wireOp",EDGE,"E4.sketch_text.stroke-177"),sQuery(id+"F3.wireOp",EDGE,"E4.sketch_text.stroke-178"),sQuery(id+"F3.wireOp",EDGE,"E4.sketch_text.stroke-179"),sQuery(id+"F3.wireOp",EDGE,"E4.sketch_text.stroke-180"),subQ2,sQuery(id+"F4.wireOp",EDGE,"E31")])],"isStart":true})])],"derivedFrom":makeQuery(id+"F5.opExtrude","CAP_EDGE",EDGE,{"disambiguationData":[OSD([subQ2])],"isStart":true})});}
            var Q21;
            {var subQ0=sQuery(id+"F4.wireOp",EDGE,"E30");var subQ1=sQuery(id+"F0.wireOp",EDGE,"E0.top");var subQ2=sQuery(id+"F4.wireOp",EDGE,"E31");var subQ3=sQuery(id+"F0.wireOp",EDGE,"E0.bottom");Q21=makeQuery(id+"F5.boolean.opBoolean","SPLIT",EDGE,{"disambiguationData":[TD([makeQuery(id+"F1.opExtrude","CAP_FACE",FACE,{"disambiguationData":[OSD([subQ3,subQ1,sQuery(id+"F0.wireOp",EDGE,"E0.left"),sQuery(id+"F0.wireOp",EDGE,"E0.right")])],"isStart":false}),makeQuery(id+"F1.opExtrude","SWEPT_FACE",FACE,{"disambiguationData":[OSD([subQ1])]}),makeQuery(id+"F5.opExtrude","SWEPT_FACE",FACE,{"disambiguationData":[OSD([subQ0])]}),makeQuery(id+"F5.opExtrude","CAP_FACE",FACE,{"disambiguationData":[OSD([subQ3,sQuery(id+"F2.wireOp",EDGE,"E2.sketch_text.stroke-0"),sQuery(id+"F2.wireOp",EDGE,"E2.sketch_text.stroke-1"),sQuery(id+"F2.wireOp",EDGE,"E2.sketch_text.stroke-2"),sQuery(id+"F2.wireOp",EDGE,"E2.sketch_text.stroke-3"),sQuery(id+"F2.wireOp",EDGE,"E2.sketch_text.stroke-4"),sQuery(id+"F2.wireOp",EDGE,"E2.sketch_text.stroke-5"),sQuery(id+"F2.wireOp",EDGE,"E2.sketch_text.stroke-6"),sQuery(id+"F2.wireOp",EDGE,"E2.sketch_text.stroke-7"),sQuery(id+"F2.wireOp",EDGE,"E2.sketch_text.stroke-8"),sQuery(id+"F2.wireOp",EDGE,"E2.sketch_text.stroke-9"),sQuery(id+"F2.wireOp",EDGE,"E2.sketch_text.stroke-10"),sQuery(id+"F2.wireOp",EDGE,"E2.sketch_text.stroke-11"),sQuery(id+"F2.wireOp",EDGE,"E2.sketch_text.stroke-12"),sQuery(id+"F2.wireOp",EDGE,"E2.sketch_text.stroke-13"),sQuery(id+"F2.wireOp",EDGE,"E2.sketch_text.stroke-14"),sQuery(id+"F2.wireOp",EDGE,"E2.sketch_text.stroke-15"),sQuery(id+"F2.wireOp",EDGE,"E2.sketch_text.stroke-16"),sQuery(id+"F2.wireOp",EDGE,"E2.sketch_text.stroke-17"),sQuery(id+"F2.wireOp",EDGE,"E2.sketch_text.stroke-18"),sQuery(id+"F2.wireOp",EDGE,"E2.sketch_text.stroke-19"),sQuery(id+"F2.wireOp",EDGE,"E2.sketch_text.stroke-20"),sQuery(id+"F2.wireOp",EDGE,"E2.sketch_text.stroke-21"),sQuery(id+"F2.wireOp",EDGE,"E2.sketch_text.stroke-22"),sQuery(id+"F2.wireOp",EDGE,"E2.sketch_text.stroke-23"),sQuery(id+"F2.wireOp",EDGE,"E2.sketch_text.stroke-24"),sQuery(id+"F2.wireOp",EDGE,"E2.sketch_text.stroke-25"),sQuery(id+"F2.wireOp",EDGE,"E2.sketch_text.stroke-26"),sQuery(id+"F2.wireOp",EDGE,"E2.sketch_text.stroke-27"),sQuery(id+"F2.wireOp",EDGE,"E2.sketch_text.stroke-28"),sQuery(id+"F2.wireOp",EDGE,"E2.sketch_text.stroke-29"),sQuery(id+"F2.wireOp",EDGE,"E2.sketch_text.stroke-30"),sQuery(id+"F2.wireOp",EDGE,"E2.sketch_text.stroke-31"),sQuery(id+"F2.wireOp",EDGE,"E2.sketch_text.stroke-32"),sQuery(id+"F2.wireOp",EDGE,"E2.sketch_text.stroke-33"),sQuery(id+"F2.wireOp",EDGE,"E2.sketch_text.stroke-34"),sQuery(id+"F2.wireOp",EDGE,"E2.sketch_text.stroke-35"),sQuery(id+"F2.wireOp",EDGE,"E2.sketch_text.stroke-36"),sQuery(id+"F2.wireOp",EDGE,"E2.sketch_text.stroke-37"),sQuery(id+"F2.wireOp",EDGE,"E2.sketch_text.stroke-38"),sQuery(id+"F2.wireOp",EDGE,"E2.sketch_text.stroke-39"),sQuery(id+"F2.wireOp",EDGE,"E2.sketch_text.stroke-40"),sQuery(id+"F2.wireOp",EDGE,"E2.sketch_text.stroke-41"),sQuery(id+"F2.wireOp",EDGE,"E2.sketch_text.stroke-42"),sQuery(id+"F2.wireOp",EDGE,"E2.sketch_text.stroke-43"),sQuery(id+"F2.wireOp",EDGE,"E2.sketch_text.stroke-44"),sQuery(id+"F2.wireOp",EDGE,"E2.sketch_text.stroke-45"),sQuery(id+"F2.wireOp",EDGE,"E2.sketch_text.stroke-46"),sQuery(id+"F2.wireOp",EDGE,"E2.sketch_text.stroke-47"),sQuery(id+"F2.wireOp",EDGE,"E2.sketch_text.stroke-48"),sQuery(id+"F2.wireOp",EDGE,"E2.sketch_text.stroke-49"),sQuery(id+"F2.wireOp",EDGE,"E2.sketch_text.stroke-50"),sQuery(id+"F2.wireOp",EDGE,"E2.sketch_text.stroke-51"),sQuery(id+"F2.wireOp",EDGE,"E2.sketch_text.stroke-52"),sQuery(id+"F2.wireOp",EDGE,"E2.sketch_text.stroke-53"),sQuery(id+"F2.wireOp",EDGE,"E2.sketch_text.stroke-54"),sQuery(id+"F2.wireOp",EDGE,"E2.sketch_text.stroke-55"),sQuery(id+"F2.wireOp",EDGE,"E2.sketch_text.stroke-56"),sQuery(id+"F2.wireOp",EDGE,"E2.sketch_text.stroke-57"),sQuery(id+"F2.wireOp",EDGE,"E2.sketch_text.stroke-58"),sQuery(id+"F2.wireOp",EDGE,"E2.sketch_text.stroke-59"),sQuery(id+"F2.wireOp",EDGE,"E2.sketch_text.stroke-60"),sQuery(id+"F2.wireOp",EDGE,"E2.sketch_text.stroke-61"),sQuery(id+"F2.wireOp",EDGE,"E2.sketch_text.stroke-62"),sQuery(id+"F2.wireOp",EDGE,"E2.sketch_text.stroke-63"),sQuery(id+"F2.wireOp",EDGE,"E2.sketch_text.stroke-64"),sQuery(id+"F2.wireOp",EDGE,"E2.sketch_text.stroke-65"),sQuery(id+"F2.wireOp",EDGE,"E2.sketch_text.stroke-66"),sQuery(id+"F2.wireOp",EDGE,"E2.sketch_text.stroke-67"),sQuery(id+"F2.wireOp",EDGE,"E2.sketch_text.stroke-68"),sQuery(id+"F2.wireOp",EDGE,"E2.sketch_text.stroke-69"),sQuery(id+"F2.wireOp",EDGE,"E2.sketch_text.stroke-70"),sQuery(id+"F2.wireOp",EDGE,"E2.sketch_text.stroke-71"),sQuery(id+"F2.wireOp",EDGE,"E2.sketch_text.stroke-72"),sQuery(id+"F2.wireOp",EDGE,"E2.sketch_text.stroke-73"),sQuery(id+"F2.wireOp",EDGE,"E2.sketch_text.stroke-74"),sQuery(id+"F2.wireOp",EDGE,"E2.sketch_text.stroke-75"),sQuery(id+"F2.wireOp",EDGE,"E2.sketch_text.stroke-76"),sQuery(id+"F2.wireOp",EDGE,"E2.sketch_text.stroke-77"),sQuery(id+"F2.wireOp",EDGE,"E2.sketch_text.stroke-78"),sQuery(id+"F2.wireOp",EDGE,"E2.sketch_text.stroke-79"),sQuery(id+"F2.wireOp",EDGE,"E2.sketch_text.stroke-80"),sQuery(id+"F2.wireOp",EDGE,"E2.sketch_text.stroke-81"),sQuery(id+"F2.wireOp",EDGE,"E2.sketch_text.stroke-82"),sQuery(id+"F2.wireOp",EDGE,"E2.sketch_text.stroke-83"),sQuery(id+"F2.wireOp",EDGE,"E2.sketch_text.stroke-84"),sQuery(id+"F2.wireOp",EDGE,"E2.sketch_text.stroke-85"),sQuery(id+"F2.wireOp",EDGE,"E2.sketch_text.stroke-86"),sQuery(id+"F2.wireOp",EDGE,"E2.sketch_text.stroke-87"),sQuery(id+"F2.wireOp",EDGE,"E2.sketch_text.stroke-88"),sQuery(id+"F2.wireOp",EDGE,"E2.sketch_text.stroke-89"),sQuery(id+"F2.wireOp",EDGE,"E2.sketch_text.stroke-90"),sQuery(id+"F2.wireOp",EDGE,"E2.sketch_text.stroke-91"),sQuery(id+"F2.wireOp",EDGE,"E2.sketch_text.stroke-92"),sQuery(id+"F2.wireOp",EDGE,"E2.sketch_text.stroke-93"),sQuery(id+"F2.wireOp",EDGE,"E2.sketch_text.stroke-94"),sQuery(id+"F2.wireOp",EDGE,"E2.sketch_text.stroke-95"),sQuery(id+"F2.wireOp",EDGE,"E2.sketch_text.stroke-96"),sQuery(id+"F2.wireOp",EDGE,"E2.sketch_text.stroke-97"),sQuery(id+"F2.wireOp",EDGE,"E2.sketch_text.stroke-98"),sQuery(id+"F2.wireOp",EDGE,"E2.sketch_text.stroke-99"),sQuery(id+"F2.wireOp",EDGE,"E2.sketch_text.stroke-100"),sQuery(id+"F2.wireOp",EDGE,"E2.sketch_text.stroke-101"),sQuery(id+"F2.wireOp",EDGE,"E2.sketch_text.stroke-102"),sQuery(id+"F2.wireOp",EDGE,"E2.sketch_text.stroke-103"),sQuery(id+"F2.wireOp",EDGE,"E2.sketch_text.stroke-104"),sQuery(id+"F2.wireOp",EDGE,"E2.sketch_text.stroke-105"),sQuery(id+"F2.wireOp",EDGE,"E2.sketch_text.stroke-106"),sQuery(id+"F2.wireOp",EDGE,"E2.sketch_text.stroke-107"),sQuery(id+"F2.wireOp",EDGE,"E2.sketch_text.stroke-108"),sQuery(id+"F2.wireOp",EDGE,"E2.sketch_text.stroke-109"),sQuery(id+"F2.wireOp",EDGE,"E2.sketch_text.stroke-110"),sQuery(id+"F2.wireOp",EDGE,"E2.sketch_text.stroke-111"),sQuery(id+"F2.wireOp",EDGE,"E2.sketch_text.stroke-112"),sQuery(id+"F2.wireOp",EDGE,"E2.sketch_text.stroke-113"),sQuery(id+"F2.wireOp",EDGE,"E2.sketch_text.stroke-114"),sQuery(id+"F2.wireOp",EDGE,"E2.sketch_text.stroke-115"),sQuery(id+"F2.wireOp",EDGE,"E2.sketch_text.stroke-116"),sQuery(id+"F2.wireOp",EDGE,"E2.sketch_text.stroke-117"),sQuery(id+"F2.wireOp",EDGE,"E2.sketch_text.stroke-118"),sQuery(id+"F2.wireOp",EDGE,"E2.sketch_text.stroke-119"),sQuery(id+"F2.wireOp",EDGE,"E2.sketch_text.stroke-120"),sQuery(id+"F2.wireOp",EDGE,"E2.sketch_text.stroke-121"),sQuery(id+"F2.wireOp",EDGE,"E2.sketch_text.stroke-122"),sQuery(id+"F2.wireOp",EDGE,"E2.sketch_text.stroke-123"),sQuery(id+"F2.wireOp",EDGE,"E2.sketch_text.stroke-124"),sQuery(id+"F2.wireOp",EDGE,"E2.sketch_text.stroke-125"),sQuery(id+"F2.wireOp",EDGE,"E2.sketch_text.stroke-126"),sQuery(id+"F2.wireOp",EDGE,"E2.sketch_text.stroke-127"),sQuery(id+"F2.wireOp",EDGE,"E2.sketch_text.stroke-128"),sQuery(id+"F2.wireOp",EDGE,"E2.sketch_text.stroke-129"),sQuery(id+"F2.wireOp",EDGE,"E2.sketch_text.stroke-130"),sQuery(id+"F2.wireOp",EDGE,"E2.sketch_text.stroke-131"),sQuery(id+"F2.wireOp",EDGE,"E2.sketch_text.stroke-132"),sQuery(id+"F2.wireOp",EDGE,"E2.sketch_text.stroke-133"),sQuery(id+"F2.wireOp",EDGE,"E2.sketch_text.stroke-134"),sQuery(id+"F2.wireOp",EDGE,"E2.sketch_text.stroke-135"),sQuery(id+"F2.wireOp",EDGE,"E2.sketch_text.stroke-136"),sQuery(id+"F2.wireOp",EDGE,"E2.sketch_text.stroke-137"),sQuery(id+"F2.wireOp",EDGE,"E2.sketch_text.stroke-138"),sQuery(id+"F2.wireOp",EDGE,"E2.sketch_text.stroke-139"),sQuery(id+"F2.wireOp",EDGE,"E2.sketch_text.stroke-140"),sQuery(id+"F2.wireOp",EDGE,"E2.sketch_text.stroke-141"),sQuery(id+"F2.wireOp",EDGE,"E2.sketch_text.stroke-142"),sQuery(id+"F2.wireOp",EDGE,"E2.sketch_text.stroke-143"),sQuery(id+"F2.wireOp",EDGE,"E2.sketch_text.stroke-144"),sQuery(id+"F2.wireOp",EDGE,"E2.sketch_text.stroke-145"),sQuery(id+"F2.wireOp",EDGE,"E2.sketch_text.stroke-146"),sQuery(id+"F2.wireOp",EDGE,"E2.sketch_text.stroke-147"),sQuery(id+"F2.wireOp",EDGE,"E2.sketch_text.stroke-148"),sQuery(id+"F2.wireOp",EDGE,"E2.sketch_text.stroke-149"),sQuery(id+"F2.wireOp",EDGE,"E2.sketch_text.stroke-150"),sQuery(id+"F2.wireOp",EDGE,"E2.sketch_text.stroke-151"),sQuery(id+"F2.wireOp",EDGE,"E2.sketch_text.stroke-152"),sQuery(id+"F2.wireOp",EDGE,"E2.sketch_text.stroke-153"),sQuery(id+"F2.wireOp",EDGE,"E2.sketch_text.stroke-154"),sQuery(id+"F2.wireOp",EDGE,"E2.sketch_text.stroke-155"),sQuery(id+"F2.wireOp",EDGE,"E2.sketch_text.stroke-156"),sQuery(id+"F2.wireOp",EDGE,"E2.sketch_text.stroke-157"),sQuery(id+"F2.wireOp",EDGE,"E2.sketch_text.stroke-158"),sQuery(id+"F2.wireOp",EDGE,"E2.sketch_text.stroke-159"),sQuery(id+"F2.wireOp",EDGE,"E2.sketch_text.stroke-160"),sQuery(id+"F2.wireOp",EDGE,"E2.sketch_text.stroke-161"),sQuery(id+"F2.wireOp",EDGE,"E2.sketch_text.stroke-162"),sQuery(id+"F2.wireOp",EDGE,"E2.sketch_text.stroke-163"),sQuery(id+"F2.wireOp",EDGE,"E2.sketch_text.stroke-164"),sQuery(id+"F2.wireOp",EDGE,"E2.sketch_text.stroke-165"),sQuery(id+"F2.wireOp",EDGE,"E2.sketch_text.stroke-166"),sQuery(id+"F2.wireOp",EDGE,"E2.sketch_text.stroke-167"),sQuery(id+"F2.wireOp",EDGE,"E2.sketch_text.stroke-168"),sQuery(id+"F2.wireOp",EDGE,"E2.sketch_text.stroke-169"),sQuery(id+"F2.wireOp",EDGE,"E2.sketch_text.stroke-170"),sQuery(id+"F2.wireOp",EDGE,"E2.sketch_text.stroke-171"),sQuery(id+"F2.wireOp",EDGE,"E2.sketch_text.stroke-172"),sQuery(id+"F2.wireOp",EDGE,"E2.sketch_text.stroke-173"),sQuery(id+"F3.wireOp",EDGE,"E4.sketch_text.stroke-0"),sQuery(id+"F3.wireOp",EDGE,"E4.sketch_text.stroke-1"),sQuery(id+"F3.wireOp",EDGE,"E4.sketch_text.stroke-2"),sQuery(id+"F3.wireOp",EDGE,"E4.sketch_text.stroke-3"),sQuery(id+"F3.wireOp",EDGE,"E4.sketch_text.stroke-4"),sQuery(id+"F3.wireOp",EDGE,"E4.sketch_text.stroke-5"),sQuery(id+"F3.wireOp",EDGE,"E4.sketch_text.stroke-6"),sQuery(id+"F3.wireOp",EDGE,"E4.sketch_text.stroke-7"),sQuery(id+"F3.wireOp",EDGE,"E4.sketch_text.stroke-8"),sQuery(id+"F3.wireOp",EDGE,"E4.sketch_text.stroke-9"),sQuery(id+"F3.wireOp",EDGE,"E4.sketch_text.stroke-10"),sQuery(id+"F3.wireOp",EDGE,"E4.sketch_text.stroke-11"),sQuery(id+"F3.wireOp",EDGE,"E4.sketch_text.stroke-12"),sQuery(id+"F3.wireOp",EDGE,"E4.sketch_text.stroke-13"),sQuery(id+"F3.wireOp",EDGE,"E4.sketch_text.stroke-14"),sQuery(id+"F3.wireOp",EDGE,"E4.sketch_text.stroke-15"),sQuery(id+"F3.wireOp",EDGE,"E4.sketch_text.stroke-16"),sQuery(id+"F3.wireOp",EDGE,"E4.sketch_text.stroke-17"),sQuery(id+"F3.wireOp",EDGE,"E4.sketch_text.stroke-18"),sQuery(id+"F3.wireOp",EDGE,"E4.sketch_text.stroke-19"),sQuery(id+"F3.wireOp",EDGE,"E4.sketch_text.stroke-20"),sQuery(id+"F3.wireOp",EDGE,"E4.sketch_text.stroke-21"),sQuery(id+"F3.wireOp",EDGE,"E4.sketch_text.stroke-22"),sQuery(id+"F3.wireOp",EDGE,"E4.sketch_text.stroke-23"),sQuery(id+"F3.wireOp",EDGE,"E4.sketch_text.stroke-24"),sQuery(id+"F3.wireOp",EDGE,"E4.sketch_text.stroke-25"),sQuery(id+"F3.wireOp",EDGE,"E4.sketch_text.stroke-26"),sQuery(id+"F3.wireOp",EDGE,"E4.sketch_text.stroke-27"),sQuery(id+"F3.wireOp",EDGE,"E4.sketch_text.stroke-28"),sQuery(id+"F3.wireOp",EDGE,"E4.sketch_text.stroke-29"),sQuery(id+"F3.wireOp",EDGE,"E4.sketch_text.stroke-30"),sQuery(id+"F3.wireOp",EDGE,"E4.sketch_text.stroke-31"),sQuery(id+"F3.wireOp",EDGE,"E4.sketch_text.stroke-32"),sQuery(id+"F3.wireOp",EDGE,"E4.sketch_text.stroke-33"),sQuery(id+"F3.wireOp",EDGE,"E4.sketch_text.stroke-34"),sQuery(id+"F3.wireOp",EDGE,"E4.sketch_text.stroke-35"),sQuery(id+"F3.wireOp",EDGE,"E4.sketch_text.stroke-36"),sQuery(id+"F3.wireOp",EDGE,"E4.sketch_text.stroke-37"),sQuery(id+"F3.wireOp",EDGE,"E4.sketch_text.stroke-38"),sQuery(id+"F3.wireOp",EDGE,"E4.sketch_text.stroke-39"),sQuery(id+"F3.wireOp",EDGE,"E4.sketch_text.stroke-40"),sQuery(id+"F3.wireOp",EDGE,"E4.sketch_text.stroke-41"),sQuery(id+"F3.wireOp",EDGE,"E4.sketch_text.stroke-42"),sQuery(id+"F3.wireOp",EDGE,"E4.sketch_text.stroke-43"),sQuery(id+"F3.wireOp",EDGE,"E4.sketch_text.stroke-44"),sQuery(id+"F3.wireOp",EDGE,"E4.sketch_text.stroke-45"),sQuery(id+"F3.wireOp",EDGE,"E4.sketch_text.stroke-46"),sQuery(id+"F3.wireOp",EDGE,"E4.sketch_text.stroke-47"),sQuery(id+"F3.wireOp",EDGE,"E4.sketch_text.stroke-48"),sQuery(id+"F3.wireOp",EDGE,"E4.sketch_text.stroke-49"),sQuery(id+"F3.wireOp",EDGE,"E4.sketch_text.stroke-50"),sQuery(id+"F3.wireOp",EDGE,"E4.sketch_text.stroke-51"),sQuery(id+"F3.wireOp",EDGE,"E4.sketch_text.stroke-52"),sQuery(id+"F3.wireOp",EDGE,"E4.sketch_text.stroke-53"),sQuery(id+"F3.wireOp",EDGE,"E4.sketch_text.stroke-54"),sQuery(id+"F3.wireOp",EDGE,"E4.sketch_text.stroke-55"),sQuery(id+"F3.wireOp",EDGE,"E4.sketch_text.stroke-56"),sQuery(id+"F3.wireOp",EDGE,"E4.sketch_text.stroke-57"),sQuery(id+"F3.wireOp",EDGE,"E4.sketch_text.stroke-58"),sQuery(id+"F3.wireOp",EDGE,"E4.sketch_text.stroke-59"),sQuery(id+"F3.wireOp",EDGE,"E4.sketch_text.stroke-60"),sQuery(id+"F3.wireOp",EDGE,"E4.sketch_text.stroke-61"),sQuery(id+"F3.wireOp",EDGE,"E4.sketch_text.stroke-62"),sQuery(id+"F3.wireOp",EDGE,"E4.sketch_text.stroke-71"),sQuery(id+"F3.wireOp",EDGE,"E4.sketch_text.stroke-72"),sQuery(id+"F3.wireOp",EDGE,"E4.sketch_text.stroke-73"),sQuery(id+"F3.wireOp",EDGE,"E4.sketch_text.stroke-74"),sQuery(id+"F3.wireOp",EDGE,"E4.sketch_text.stroke-75"),sQuery(id+"F3.wireOp",EDGE,"E4.sketch_text.stroke-76"),sQuery(id+"F3.wireOp",EDGE,"E4.sketch_text.stroke-77"),sQuery(id+"F3.wireOp",EDGE,"E4.sketch_text.stroke-78"),sQuery(id+"F3.wireOp",EDGE,"E4.sketch_text.stroke-79"),sQuery(id+"F3.wireOp",EDGE,"E4.sketch_text.stroke-80"),sQuery(id+"F3.wireOp",EDGE,"E4.sketch_text.stroke-81"),sQuery(id+"F3.wireOp",EDGE,"E4.sketch_text.stroke-82"),sQuery(id+"F3.wireOp",EDGE,"E4.sketch_text.stroke-83"),sQuery(id+"F3.wireOp",EDGE,"E4.sketch_text.stroke-84"),sQuery(id+"F3.wireOp",EDGE,"E4.sketch_text.stroke-85"),sQuery(id+"F3.wireOp",EDGE,"E4.sketch_text.stroke-86"),sQuery(id+"F3.wireOp",EDGE,"E4.sketch_text.stroke-87"),sQuery(id+"F3.wireOp",EDGE,"E4.sketch_text.stroke-88"),sQuery(id+"F3.wireOp",EDGE,"E4.sketch_text.stroke-89"),sQuery(id+"F3.wireOp",EDGE,"E4.sketch_text.stroke-90"),sQuery(id+"F3.wireOp",EDGE,"E4.sketch_text.stroke-91"),sQuery(id+"F3.wireOp",EDGE,"E4.sketch_text.stroke-92"),sQuery(id+"F3.wireOp",EDGE,"E4.sketch_text.stroke-93"),sQuery(id+"F3.wireOp",EDGE,"E4.sketch_text.stroke-94"),sQuery(id+"F3.wireOp",EDGE,"E4.sketch_text.stroke-95"),sQuery(id+"F3.wireOp",EDGE,"E4.sketch_text.stroke-96"),sQuery(id+"F3.wireOp",EDGE,"E4.sketch_text.stroke-97"),sQuery(id+"F3.wireOp",EDGE,"E4.sketch_text.stroke-103"),sQuery(id+"F3.wireOp",EDGE,"E4.sketch_text.stroke-104"),sQuery(id+"F3.wireOp",EDGE,"E4.sketch_text.stroke-105"),sQuery(id+"F3.wireOp",EDGE,"E4.sketch_text.stroke-106"),sQuery(id+"F3.wireOp",EDGE,"E4.sketch_text.stroke-107"),sQuery(id+"F3.wireOp",EDGE,"E4.sketch_text.stroke-108"),sQuery(id+"F3.wireOp",EDGE,"E4.sketch_text.stroke-109"),sQuery(id+"F3.wireOp",EDGE,"E4.sketch_text.stroke-110"),sQuery(id+"F3.wireOp",EDGE,"E4.sketch_text.stroke-111"),sQuery(id+"F3.wireOp",EDGE,"E4.sketch_text.stroke-112"),sQuery(id+"F3.wireOp",EDGE,"E4.sketch_text.stroke-113"),sQuery(id+"F3.wireOp",EDGE,"E4.sketch_text.stroke-114"),sQuery(id+"F3.wireOp",EDGE,"E4.sketch_text.stroke-115"),sQuery(id+"F3.wireOp",EDGE,"E4.sketch_text.stroke-116"),sQuery(id+"F3.wireOp",EDGE,"E4.sketch_text.stroke-117"),sQuery(id+"F3.wireOp",EDGE,"E4.sketch_text.stroke-118"),sQuery(id+"F3.wireOp",EDGE,"E4.sketch_text.stroke-119"),sQuery(id+"F3.wireOp",EDGE,"E4.sketch_text.stroke-120"),sQuery(id+"F3.wireOp",EDGE,"E4.sketch_text.stroke-121"),sQuery(id+"F3.wireOp",EDGE,"E4.sketch_text.stroke-122"),sQuery(id+"F3.wireOp",EDGE,"E4.sketch_text.stroke-123"),sQuery(id+"F3.wireOp",EDGE,"E4.sketch_text.stroke-124"),sQuery(id+"F3.wireOp",EDGE,"E4.sketch_text.stroke-125"),sQuery(id+"F3.wireOp",EDGE,"E4.sketch_text.stroke-126"),sQuery(id+"F3.wireOp",EDGE,"E4.sketch_text.stroke-127"),sQuery(id+"F3.wireOp",EDGE,"E4.sketch_text.stroke-128"),sQuery(id+"F3.wireOp",EDGE,"E4.sketch_text.stroke-129"),sQuery(id+"F3.wireOp",EDGE,"E4.sketch_text.stroke-130"),sQuery(id+"F3.wireOp",EDGE,"E4.sketch_text.stroke-131"),sQuery(id+"F3.wireOp",EDGE,"E4.sketch_text.stroke-132"),sQuery(id+"F3.wireOp",EDGE,"E4.sketch_text.stroke-133"),sQuery(id+"F3.wireOp",EDGE,"E4.sketch_text.stroke-134"),sQuery(id+"F3.wireOp",EDGE,"E4.sketch_text.stroke-135"),sQuery(id+"F3.wireOp",EDGE,"E4.sketch_text.stroke-136"),sQuery(id+"F3.wireOp",EDGE,"E4.sketch_text.stroke-137"),sQuery(id+"F3.wireOp",EDGE,"E4.sketch_text.stroke-138"),sQuery(id+"F3.wireOp",EDGE,"E4.sketch_text.stroke-139"),sQuery(id+"F3.wireOp",EDGE,"E4.sketch_text.stroke-140"),sQuery(id+"F3.wireOp",EDGE,"E4.sketch_text.stroke-141"),sQuery(id+"F3.wireOp",EDGE,"E4.sketch_text.stroke-142"),sQuery(id+"F3.wireOp",EDGE,"E4.sketch_text.stroke-143"),sQuery(id+"F3.wireOp",EDGE,"E4.sketch_text.stroke-144"),sQuery(id+"F3.wireOp",EDGE,"E4.sketch_text.stroke-145"),sQuery(id+"F3.wireOp",EDGE,"E4.sketch_text.stroke-146"),sQuery(id+"F3.wireOp",EDGE,"E4.sketch_text.stroke-147"),sQuery(id+"F3.wireOp",EDGE,"E4.sketch_text.stroke-148"),sQuery(id+"F3.wireOp",EDGE,"E4.sketch_text.stroke-149"),sQuery(id+"F3.wireOp",EDGE,"E4.sketch_text.stroke-150"),sQuery(id+"F3.wireOp",EDGE,"E4.sketch_text.stroke-151"),sQuery(id+"F3.wireOp",EDGE,"E4.sketch_text.stroke-152"),sQuery(id+"F3.wireOp",EDGE,"E4.sketch_text.stroke-153"),sQuery(id+"F3.wireOp",EDGE,"E4.sketch_text.stroke-159"),sQuery(id+"F3.wireOp",EDGE,"E4.sketch_text.stroke-160"),sQuery(id+"F3.wireOp",EDGE,"E4.sketch_text.stroke-161"),sQuery(id+"F3.wireOp",EDGE,"E4.sketch_text.stroke-162"),sQuery(id+"F3.wireOp",EDGE,"E4.sketch_text.stroke-163"),sQuery(id+"F3.wireOp",EDGE,"E4.sketch_text.stroke-164"),sQuery(id+"F3.wireOp",EDGE,"E4.sketch_text.stroke-165"),sQuery(id+"F3.wireOp",EDGE,"E4.sketch_text.stroke-166"),sQuery(id+"F3.wireOp",EDGE,"E4.sketch_text.stroke-167"),sQuery(id+"F3.wireOp",EDGE,"E4.sketch_text.stroke-168"),sQuery(id+"F3.wireOp",EDGE,"E4.sketch_text.stroke-169"),sQuery(id+"F3.wireOp",EDGE,"E4.sketch_text.stroke-170"),sQuery(id+"F3.wireOp",EDGE,"E4.sketch_text.stroke-171"),sQuery(id+"F3.wireOp",EDGE,"E4.sketch_text.stroke-172"),sQuery(id+"F3.wireOp",EDGE,"E4.sketch_text.stroke-173"),sQuery(id+"F3.wireOp",EDGE,"E4.sketch_text.stroke-174"),sQuery(id+"F3.wireOp",EDGE,"E4.sketch_text.stroke-175"),sQuery(id+"F3.wireOp",EDGE,"E4.sketch_text.stroke-176"),sQuery(id+"F3.wireOp",EDGE,"E4.sketch_text.stroke-177"),sQuery(id+"F3.wireOp",EDGE,"E4.sketch_text.stroke-178"),sQuery(id+"F3.wireOp",EDGE,"E4.sketch_text.stroke-179"),sQuery(id+"F3.wireOp",EDGE,"E4.sketch_text.stroke-180"),subQ0,subQ2])],"isStart":true}),makeQuery(id+"F5.opExtrude","SWEPT_FACE",FACE,{"disambiguationData":[OSD([subQ2])]})])],"derivedFrom":makeQuery(id+"F5.opExtrude","CAP_EDGE",EDGE,{"disambiguationData":[OSD([subQ0])],"isStart":true})});}
            var Q22;
            {var subQ0=sQuery(id+"F4.wireOp",EDGE,"E30");var subQ1=sQuery(id+"F0.wireOp",EDGE,"E0.top");var subQ2=sQuery(id+"F4.wireOp",EDGE,"E31");var subQ3=sQuery(id+"F0.wireOp",EDGE,"E0.bottom");Q22=makeQuery(id+"F5.boolean.opBoolean","SPLIT",EDGE,{"disambiguationData":[TD([makeQuery(id+"F1.opExtrude","CAP_FACE",FACE,{"disambiguationData":[OSD([subQ3,subQ1,sQuery(id+"F0.wireOp",EDGE,"E0.left"),sQuery(id+"F0.wireOp",EDGE,"E0.right")])],"isStart":false}),makeQuery(id+"F1.opExtrude","SWEPT_FACE",FACE,{"disambiguationData":[OSD([subQ1])]}),makeQuery(id+"F5.opExtrude","SWEPT_FACE",FACE,{"disambiguationData":[OSD([subQ0])]}),makeQuery(id+"F5.opExtrude","CAP_FACE",FACE,{"disambiguationData":[OSD([subQ3,sQuery(id+"F2.wireOp",EDGE,"E2.sketch_text.stroke-0"),sQuery(id+"F2.wireOp",EDGE,"E2.sketch_text.stroke-1"),sQuery(id+"F2.wireOp",EDGE,"E2.sketch_text.stroke-2"),sQuery(id+"F2.wireOp",EDGE,"E2.sketch_text.stroke-3"),sQuery(id+"F2.wireOp",EDGE,"E2.sketch_text.stroke-4"),sQuery(id+"F2.wireOp",EDGE,"E2.sketch_text.stroke-5"),sQuery(id+"F2.wireOp",EDGE,"E2.sketch_text.stroke-6"),sQuery(id+"F2.wireOp",EDGE,"E2.sketch_text.stroke-7"),sQuery(id+"F2.wireOp",EDGE,"E2.sketch_text.stroke-8"),sQuery(id+"F2.wireOp",EDGE,"E2.sketch_text.stroke-9"),sQuery(id+"F2.wireOp",EDGE,"E2.sketch_text.stroke-10"),sQuery(id+"F2.wireOp",EDGE,"E2.sketch_text.stroke-11"),sQuery(id+"F2.wireOp",EDGE,"E2.sketch_text.stroke-12"),sQuery(id+"F2.wireOp",EDGE,"E2.sketch_text.stroke-13"),sQuery(id+"F2.wireOp",EDGE,"E2.sketch_text.stroke-14"),sQuery(id+"F2.wireOp",EDGE,"E2.sketch_text.stroke-15"),sQuery(id+"F2.wireOp",EDGE,"E2.sketch_text.stroke-16"),sQuery(id+"F2.wireOp",EDGE,"E2.sketch_text.stroke-17"),sQuery(id+"F2.wireOp",EDGE,"E2.sketch_text.stroke-18"),sQuery(id+"F2.wireOp",EDGE,"E2.sketch_text.stroke-19"),sQuery(id+"F2.wireOp",EDGE,"E2.sketch_text.stroke-20"),sQuery(id+"F2.wireOp",EDGE,"E2.sketch_text.stroke-21"),sQuery(id+"F2.wireOp",EDGE,"E2.sketch_text.stroke-22"),sQuery(id+"F2.wireOp",EDGE,"E2.sketch_text.stroke-23"),sQuery(id+"F2.wireOp",EDGE,"E2.sketch_text.stroke-24"),sQuery(id+"F2.wireOp",EDGE,"E2.sketch_text.stroke-25"),sQuery(id+"F2.wireOp",EDGE,"E2.sketch_text.stroke-26"),sQuery(id+"F2.wireOp",EDGE,"E2.sketch_text.stroke-27"),sQuery(id+"F2.wireOp",EDGE,"E2.sketch_text.stroke-28"),sQuery(id+"F2.wireOp",EDGE,"E2.sketch_text.stroke-29"),sQuery(id+"F2.wireOp",EDGE,"E2.sketch_text.stroke-30"),sQuery(id+"F2.wireOp",EDGE,"E2.sketch_text.stroke-31"),sQuery(id+"F2.wireOp",EDGE,"E2.sketch_text.stroke-32"),sQuery(id+"F2.wireOp",EDGE,"E2.sketch_text.stroke-33"),sQuery(id+"F2.wireOp",EDGE,"E2.sketch_text.stroke-34"),sQuery(id+"F2.wireOp",EDGE,"E2.sketch_text.stroke-35"),sQuery(id+"F2.wireOp",EDGE,"E2.sketch_text.stroke-36"),sQuery(id+"F2.wireOp",EDGE,"E2.sketch_text.stroke-37"),sQuery(id+"F2.wireOp",EDGE,"E2.sketch_text.stroke-38"),sQuery(id+"F2.wireOp",EDGE,"E2.sketch_text.stroke-39"),sQuery(id+"F2.wireOp",EDGE,"E2.sketch_text.stroke-40"),sQuery(id+"F2.wireOp",EDGE,"E2.sketch_text.stroke-41"),sQuery(id+"F2.wireOp",EDGE,"E2.sketch_text.stroke-42"),sQuery(id+"F2.wireOp",EDGE,"E2.sketch_text.stroke-43"),sQuery(id+"F2.wireOp",EDGE,"E2.sketch_text.stroke-44"),sQuery(id+"F2.wireOp",EDGE,"E2.sketch_text.stroke-45"),sQuery(id+"F2.wireOp",EDGE,"E2.sketch_text.stroke-46"),sQuery(id+"F2.wireOp",EDGE,"E2.sketch_text.stroke-47"),sQuery(id+"F2.wireOp",EDGE,"E2.sketch_text.stroke-48"),sQuery(id+"F2.wireOp",EDGE,"E2.sketch_text.stroke-49"),sQuery(id+"F2.wireOp",EDGE,"E2.sketch_text.stroke-50"),sQuery(id+"F2.wireOp",EDGE,"E2.sketch_text.stroke-51"),sQuery(id+"F2.wireOp",EDGE,"E2.sketch_text.stroke-52"),sQuery(id+"F2.wireOp",EDGE,"E2.sketch_text.stroke-53"),sQuery(id+"F2.wireOp",EDGE,"E2.sketch_text.stroke-54"),sQuery(id+"F2.wireOp",EDGE,"E2.sketch_text.stroke-55"),sQuery(id+"F2.wireOp",EDGE,"E2.sketch_text.stroke-56"),sQuery(id+"F2.wireOp",EDGE,"E2.sketch_text.stroke-57"),sQuery(id+"F2.wireOp",EDGE,"E2.sketch_text.stroke-58"),sQuery(id+"F2.wireOp",EDGE,"E2.sketch_text.stroke-59"),sQuery(id+"F2.wireOp",EDGE,"E2.sketch_text.stroke-60"),sQuery(id+"F2.wireOp",EDGE,"E2.sketch_text.stroke-61"),sQuery(id+"F2.wireOp",EDGE,"E2.sketch_text.stroke-62"),sQuery(id+"F2.wireOp",EDGE,"E2.sketch_text.stroke-63"),sQuery(id+"F2.wireOp",EDGE,"E2.sketch_text.stroke-64"),sQuery(id+"F2.wireOp",EDGE,"E2.sketch_text.stroke-65"),sQuery(id+"F2.wireOp",EDGE,"E2.sketch_text.stroke-66"),sQuery(id+"F2.wireOp",EDGE,"E2.sketch_text.stroke-67"),sQuery(id+"F2.wireOp",EDGE,"E2.sketch_text.stroke-68"),sQuery(id+"F2.wireOp",EDGE,"E2.sketch_text.stroke-69"),sQuery(id+"F2.wireOp",EDGE,"E2.sketch_text.stroke-70"),sQuery(id+"F2.wireOp",EDGE,"E2.sketch_text.stroke-71"),sQuery(id+"F2.wireOp",EDGE,"E2.sketch_text.stroke-72"),sQuery(id+"F2.wireOp",EDGE,"E2.sketch_text.stroke-73"),sQuery(id+"F2.wireOp",EDGE,"E2.sketch_text.stroke-74"),sQuery(id+"F2.wireOp",EDGE,"E2.sketch_text.stroke-75"),sQuery(id+"F2.wireOp",EDGE,"E2.sketch_text.stroke-76"),sQuery(id+"F2.wireOp",EDGE,"E2.sketch_text.stroke-77"),sQuery(id+"F2.wireOp",EDGE,"E2.sketch_text.stroke-78"),sQuery(id+"F2.wireOp",EDGE,"E2.sketch_text.stroke-79"),sQuery(id+"F2.wireOp",EDGE,"E2.sketch_text.stroke-80"),sQuery(id+"F2.wireOp",EDGE,"E2.sketch_text.stroke-81"),sQuery(id+"F2.wireOp",EDGE,"E2.sketch_text.stroke-82"),sQuery(id+"F2.wireOp",EDGE,"E2.sketch_text.stroke-83"),sQuery(id+"F2.wireOp",EDGE,"E2.sketch_text.stroke-84"),sQuery(id+"F2.wireOp",EDGE,"E2.sketch_text.stroke-85"),sQuery(id+"F2.wireOp",EDGE,"E2.sketch_text.stroke-86"),sQuery(id+"F2.wireOp",EDGE,"E2.sketch_text.stroke-87"),sQuery(id+"F2.wireOp",EDGE,"E2.sketch_text.stroke-88"),sQuery(id+"F2.wireOp",EDGE,"E2.sketch_text.stroke-89"),sQuery(id+"F2.wireOp",EDGE,"E2.sketch_text.stroke-90"),sQuery(id+"F2.wireOp",EDGE,"E2.sketch_text.stroke-91"),sQuery(id+"F2.wireOp",EDGE,"E2.sketch_text.stroke-92"),sQuery(id+"F2.wireOp",EDGE,"E2.sketch_text.stroke-93"),sQuery(id+"F2.wireOp",EDGE,"E2.sketch_text.stroke-94"),sQuery(id+"F2.wireOp",EDGE,"E2.sketch_text.stroke-95"),sQuery(id+"F2.wireOp",EDGE,"E2.sketch_text.stroke-96"),sQuery(id+"F2.wireOp",EDGE,"E2.sketch_text.stroke-97"),sQuery(id+"F2.wireOp",EDGE,"E2.sketch_text.stroke-98"),sQuery(id+"F2.wireOp",EDGE,"E2.sketch_text.stroke-99"),sQuery(id+"F2.wireOp",EDGE,"E2.sketch_text.stroke-100"),sQuery(id+"F2.wireOp",EDGE,"E2.sketch_text.stroke-101"),sQuery(id+"F2.wireOp",EDGE,"E2.sketch_text.stroke-102"),sQuery(id+"F2.wireOp",EDGE,"E2.sketch_text.stroke-103"),sQuery(id+"F2.wireOp",EDGE,"E2.sketch_text.stroke-104"),sQuery(id+"F2.wireOp",EDGE,"E2.sketch_text.stroke-105"),sQuery(id+"F2.wireOp",EDGE,"E2.sketch_text.stroke-106"),sQuery(id+"F2.wireOp",EDGE,"E2.sketch_text.stroke-107"),sQuery(id+"F2.wireOp",EDGE,"E2.sketch_text.stroke-108"),sQuery(id+"F2.wireOp",EDGE,"E2.sketch_text.stroke-109"),sQuery(id+"F2.wireOp",EDGE,"E2.sketch_text.stroke-110"),sQuery(id+"F2.wireOp",EDGE,"E2.sketch_text.stroke-111"),sQuery(id+"F2.wireOp",EDGE,"E2.sketch_text.stroke-112"),sQuery(id+"F2.wireOp",EDGE,"E2.sketch_text.stroke-113"),sQuery(id+"F2.wireOp",EDGE,"E2.sketch_text.stroke-114"),sQuery(id+"F2.wireOp",EDGE,"E2.sketch_text.stroke-115"),sQuery(id+"F2.wireOp",EDGE,"E2.sketch_text.stroke-116"),sQuery(id+"F2.wireOp",EDGE,"E2.sketch_text.stroke-117"),sQuery(id+"F2.wireOp",EDGE,"E2.sketch_text.stroke-118"),sQuery(id+"F2.wireOp",EDGE,"E2.sketch_text.stroke-119"),sQuery(id+"F2.wireOp",EDGE,"E2.sketch_text.stroke-120"),sQuery(id+"F2.wireOp",EDGE,"E2.sketch_text.stroke-121"),sQuery(id+"F2.wireOp",EDGE,"E2.sketch_text.stroke-122"),sQuery(id+"F2.wireOp",EDGE,"E2.sketch_text.stroke-123"),sQuery(id+"F2.wireOp",EDGE,"E2.sketch_text.stroke-124"),sQuery(id+"F2.wireOp",EDGE,"E2.sketch_text.stroke-125"),sQuery(id+"F2.wireOp",EDGE,"E2.sketch_text.stroke-126"),sQuery(id+"F2.wireOp",EDGE,"E2.sketch_text.stroke-127"),sQuery(id+"F2.wireOp",EDGE,"E2.sketch_text.stroke-128"),sQuery(id+"F2.wireOp",EDGE,"E2.sketch_text.stroke-129"),sQuery(id+"F2.wireOp",EDGE,"E2.sketch_text.stroke-130"),sQuery(id+"F2.wireOp",EDGE,"E2.sketch_text.stroke-131"),sQuery(id+"F2.wireOp",EDGE,"E2.sketch_text.stroke-132"),sQuery(id+"F2.wireOp",EDGE,"E2.sketch_text.stroke-133"),sQuery(id+"F2.wireOp",EDGE,"E2.sketch_text.stroke-134"),sQuery(id+"F2.wireOp",EDGE,"E2.sketch_text.stroke-135"),sQuery(id+"F2.wireOp",EDGE,"E2.sketch_text.stroke-136"),sQuery(id+"F2.wireOp",EDGE,"E2.sketch_text.stroke-137"),sQuery(id+"F2.wireOp",EDGE,"E2.sketch_text.stroke-138"),sQuery(id+"F2.wireOp",EDGE,"E2.sketch_text.stroke-139"),sQuery(id+"F2.wireOp",EDGE,"E2.sketch_text.stroke-140"),sQuery(id+"F2.wireOp",EDGE,"E2.sketch_text.stroke-141"),sQuery(id+"F2.wireOp",EDGE,"E2.sketch_text.stroke-142"),sQuery(id+"F2.wireOp",EDGE,"E2.sketch_text.stroke-143"),sQuery(id+"F2.wireOp",EDGE,"E2.sketch_text.stroke-144"),sQuery(id+"F2.wireOp",EDGE,"E2.sketch_text.stroke-145"),sQuery(id+"F2.wireOp",EDGE,"E2.sketch_text.stroke-146"),sQuery(id+"F2.wireOp",EDGE,"E2.sketch_text.stroke-147"),sQuery(id+"F2.wireOp",EDGE,"E2.sketch_text.stroke-148"),sQuery(id+"F2.wireOp",EDGE,"E2.sketch_text.stroke-149"),sQuery(id+"F2.wireOp",EDGE,"E2.sketch_text.stroke-150"),sQuery(id+"F2.wireOp",EDGE,"E2.sketch_text.stroke-151"),sQuery(id+"F2.wireOp",EDGE,"E2.sketch_text.stroke-152"),sQuery(id+"F2.wireOp",EDGE,"E2.sketch_text.stroke-153"),sQuery(id+"F2.wireOp",EDGE,"E2.sketch_text.stroke-154"),sQuery(id+"F2.wireOp",EDGE,"E2.sketch_text.stroke-155"),sQuery(id+"F2.wireOp",EDGE,"E2.sketch_text.stroke-156"),sQuery(id+"F2.wireOp",EDGE,"E2.sketch_text.stroke-157"),sQuery(id+"F2.wireOp",EDGE,"E2.sketch_text.stroke-158"),sQuery(id+"F2.wireOp",EDGE,"E2.sketch_text.stroke-159"),sQuery(id+"F2.wireOp",EDGE,"E2.sketch_text.stroke-160"),sQuery(id+"F2.wireOp",EDGE,"E2.sketch_text.stroke-161"),sQuery(id+"F2.wireOp",EDGE,"E2.sketch_text.stroke-162"),sQuery(id+"F2.wireOp",EDGE,"E2.sketch_text.stroke-163"),sQuery(id+"F2.wireOp",EDGE,"E2.sketch_text.stroke-164"),sQuery(id+"F2.wireOp",EDGE,"E2.sketch_text.stroke-165"),sQuery(id+"F2.wireOp",EDGE,"E2.sketch_text.stroke-166"),sQuery(id+"F2.wireOp",EDGE,"E2.sketch_text.stroke-167"),sQuery(id+"F2.wireOp",EDGE,"E2.sketch_text.stroke-168"),sQuery(id+"F2.wireOp",EDGE,"E2.sketch_text.stroke-169"),sQuery(id+"F2.wireOp",EDGE,"E2.sketch_text.stroke-170"),sQuery(id+"F2.wireOp",EDGE,"E2.sketch_text.stroke-171"),sQuery(id+"F2.wireOp",EDGE,"E2.sketch_text.stroke-172"),sQuery(id+"F2.wireOp",EDGE,"E2.sketch_text.stroke-173"),sQuery(id+"F3.wireOp",EDGE,"E4.sketch_text.stroke-0"),sQuery(id+"F3.wireOp",EDGE,"E4.sketch_text.stroke-1"),sQuery(id+"F3.wireOp",EDGE,"E4.sketch_text.stroke-2"),sQuery(id+"F3.wireOp",EDGE,"E4.sketch_text.stroke-3"),sQuery(id+"F3.wireOp",EDGE,"E4.sketch_text.stroke-4"),sQuery(id+"F3.wireOp",EDGE,"E4.sketch_text.stroke-5"),sQuery(id+"F3.wireOp",EDGE,"E4.sketch_text.stroke-6"),sQuery(id+"F3.wireOp",EDGE,"E4.sketch_text.stroke-7"),sQuery(id+"F3.wireOp",EDGE,"E4.sketch_text.stroke-8"),sQuery(id+"F3.wireOp",EDGE,"E4.sketch_text.stroke-9"),sQuery(id+"F3.wireOp",EDGE,"E4.sketch_text.stroke-10"),sQuery(id+"F3.wireOp",EDGE,"E4.sketch_text.stroke-11"),sQuery(id+"F3.wireOp",EDGE,"E4.sketch_text.stroke-12"),sQuery(id+"F3.wireOp",EDGE,"E4.sketch_text.stroke-13"),sQuery(id+"F3.wireOp",EDGE,"E4.sketch_text.stroke-14"),sQuery(id+"F3.wireOp",EDGE,"E4.sketch_text.stroke-15"),sQuery(id+"F3.wireOp",EDGE,"E4.sketch_text.stroke-16"),sQuery(id+"F3.wireOp",EDGE,"E4.sketch_text.stroke-17"),sQuery(id+"F3.wireOp",EDGE,"E4.sketch_text.stroke-18"),sQuery(id+"F3.wireOp",EDGE,"E4.sketch_text.stroke-19"),sQuery(id+"F3.wireOp",EDGE,"E4.sketch_text.stroke-20"),sQuery(id+"F3.wireOp",EDGE,"E4.sketch_text.stroke-21"),sQuery(id+"F3.wireOp",EDGE,"E4.sketch_text.stroke-22"),sQuery(id+"F3.wireOp",EDGE,"E4.sketch_text.stroke-23"),sQuery(id+"F3.wireOp",EDGE,"E4.sketch_text.stroke-24"),sQuery(id+"F3.wireOp",EDGE,"E4.sketch_text.stroke-25"),sQuery(id+"F3.wireOp",EDGE,"E4.sketch_text.stroke-26"),sQuery(id+"F3.wireOp",EDGE,"E4.sketch_text.stroke-27"),sQuery(id+"F3.wireOp",EDGE,"E4.sketch_text.stroke-28"),sQuery(id+"F3.wireOp",EDGE,"E4.sketch_text.stroke-29"),sQuery(id+"F3.wireOp",EDGE,"E4.sketch_text.stroke-30"),sQuery(id+"F3.wireOp",EDGE,"E4.sketch_text.stroke-31"),sQuery(id+"F3.wireOp",EDGE,"E4.sketch_text.stroke-32"),sQuery(id+"F3.wireOp",EDGE,"E4.sketch_text.stroke-33"),sQuery(id+"F3.wireOp",EDGE,"E4.sketch_text.stroke-34"),sQuery(id+"F3.wireOp",EDGE,"E4.sketch_text.stroke-35"),sQuery(id+"F3.wireOp",EDGE,"E4.sketch_text.stroke-36"),sQuery(id+"F3.wireOp",EDGE,"E4.sketch_text.stroke-37"),sQuery(id+"F3.wireOp",EDGE,"E4.sketch_text.stroke-38"),sQuery(id+"F3.wireOp",EDGE,"E4.sketch_text.stroke-39"),sQuery(id+"F3.wireOp",EDGE,"E4.sketch_text.stroke-40"),sQuery(id+"F3.wireOp",EDGE,"E4.sketch_text.stroke-41"),sQuery(id+"F3.wireOp",EDGE,"E4.sketch_text.stroke-42"),sQuery(id+"F3.wireOp",EDGE,"E4.sketch_text.stroke-43"),sQuery(id+"F3.wireOp",EDGE,"E4.sketch_text.stroke-44"),sQuery(id+"F3.wireOp",EDGE,"E4.sketch_text.stroke-45"),sQuery(id+"F3.wireOp",EDGE,"E4.sketch_text.stroke-46"),sQuery(id+"F3.wireOp",EDGE,"E4.sketch_text.stroke-47"),sQuery(id+"F3.wireOp",EDGE,"E4.sketch_text.stroke-48"),sQuery(id+"F3.wireOp",EDGE,"E4.sketch_text.stroke-49"),sQuery(id+"F3.wireOp",EDGE,"E4.sketch_text.stroke-50"),sQuery(id+"F3.wireOp",EDGE,"E4.sketch_text.stroke-51"),sQuery(id+"F3.wireOp",EDGE,"E4.sketch_text.stroke-52"),sQuery(id+"F3.wireOp",EDGE,"E4.sketch_text.stroke-53"),sQuery(id+"F3.wireOp",EDGE,"E4.sketch_text.stroke-54"),sQuery(id+"F3.wireOp",EDGE,"E4.sketch_text.stroke-55"),sQuery(id+"F3.wireOp",EDGE,"E4.sketch_text.stroke-56"),sQuery(id+"F3.wireOp",EDGE,"E4.sketch_text.stroke-57"),sQuery(id+"F3.wireOp",EDGE,"E4.sketch_text.stroke-58"),sQuery(id+"F3.wireOp",EDGE,"E4.sketch_text.stroke-59"),sQuery(id+"F3.wireOp",EDGE,"E4.sketch_text.stroke-60"),sQuery(id+"F3.wireOp",EDGE,"E4.sketch_text.stroke-61"),sQuery(id+"F3.wireOp",EDGE,"E4.sketch_text.stroke-62"),sQuery(id+"F3.wireOp",EDGE,"E4.sketch_text.stroke-71"),sQuery(id+"F3.wireOp",EDGE,"E4.sketch_text.stroke-72"),sQuery(id+"F3.wireOp",EDGE,"E4.sketch_text.stroke-73"),sQuery(id+"F3.wireOp",EDGE,"E4.sketch_text.stroke-74"),sQuery(id+"F3.wireOp",EDGE,"E4.sketch_text.stroke-75"),sQuery(id+"F3.wireOp",EDGE,"E4.sketch_text.stroke-76"),sQuery(id+"F3.wireOp",EDGE,"E4.sketch_text.stroke-77"),sQuery(id+"F3.wireOp",EDGE,"E4.sketch_text.stroke-78"),sQuery(id+"F3.wireOp",EDGE,"E4.sketch_text.stroke-79"),sQuery(id+"F3.wireOp",EDGE,"E4.sketch_text.stroke-80"),sQuery(id+"F3.wireOp",EDGE,"E4.sketch_text.stroke-81"),sQuery(id+"F3.wireOp",EDGE,"E4.sketch_text.stroke-82"),sQuery(id+"F3.wireOp",EDGE,"E4.sketch_text.stroke-83"),sQuery(id+"F3.wireOp",EDGE,"E4.sketch_text.stroke-84"),sQuery(id+"F3.wireOp",EDGE,"E4.sketch_text.stroke-85"),sQuery(id+"F3.wireOp",EDGE,"E4.sketch_text.stroke-86"),sQuery(id+"F3.wireOp",EDGE,"E4.sketch_text.stroke-87"),sQuery(id+"F3.wireOp",EDGE,"E4.sketch_text.stroke-88"),sQuery(id+"F3.wireOp",EDGE,"E4.sketch_text.stroke-89"),sQuery(id+"F3.wireOp",EDGE,"E4.sketch_text.stroke-90"),sQuery(id+"F3.wireOp",EDGE,"E4.sketch_text.stroke-91"),sQuery(id+"F3.wireOp",EDGE,"E4.sketch_text.stroke-92"),sQuery(id+"F3.wireOp",EDGE,"E4.sketch_text.stroke-93"),sQuery(id+"F3.wireOp",EDGE,"E4.sketch_text.stroke-94"),sQuery(id+"F3.wireOp",EDGE,"E4.sketch_text.stroke-95"),sQuery(id+"F3.wireOp",EDGE,"E4.sketch_text.stroke-96"),sQuery(id+"F3.wireOp",EDGE,"E4.sketch_text.stroke-97"),sQuery(id+"F3.wireOp",EDGE,"E4.sketch_text.stroke-103"),sQuery(id+"F3.wireOp",EDGE,"E4.sketch_text.stroke-104"),sQuery(id+"F3.wireOp",EDGE,"E4.sketch_text.stroke-105"),sQuery(id+"F3.wireOp",EDGE,"E4.sketch_text.stroke-106"),sQuery(id+"F3.wireOp",EDGE,"E4.sketch_text.stroke-107"),sQuery(id+"F3.wireOp",EDGE,"E4.sketch_text.stroke-108"),sQuery(id+"F3.wireOp",EDGE,"E4.sketch_text.stroke-109"),sQuery(id+"F3.wireOp",EDGE,"E4.sketch_text.stroke-110"),sQuery(id+"F3.wireOp",EDGE,"E4.sketch_text.stroke-111"),sQuery(id+"F3.wireOp",EDGE,"E4.sketch_text.stroke-112"),sQuery(id+"F3.wireOp",EDGE,"E4.sketch_text.stroke-113"),sQuery(id+"F3.wireOp",EDGE,"E4.sketch_text.stroke-114"),sQuery(id+"F3.wireOp",EDGE,"E4.sketch_text.stroke-115"),sQuery(id+"F3.wireOp",EDGE,"E4.sketch_text.stroke-116"),sQuery(id+"F3.wireOp",EDGE,"E4.sketch_text.stroke-117"),sQuery(id+"F3.wireOp",EDGE,"E4.sketch_text.stroke-118"),sQuery(id+"F3.wireOp",EDGE,"E4.sketch_text.stroke-119"),sQuery(id+"F3.wireOp",EDGE,"E4.sketch_text.stroke-120"),sQuery(id+"F3.wireOp",EDGE,"E4.sketch_text.stroke-121"),sQuery(id+"F3.wireOp",EDGE,"E4.sketch_text.stroke-122"),sQuery(id+"F3.wireOp",EDGE,"E4.sketch_text.stroke-123"),sQuery(id+"F3.wireOp",EDGE,"E4.sketch_text.stroke-124"),sQuery(id+"F3.wireOp",EDGE,"E4.sketch_text.stroke-125"),sQuery(id+"F3.wireOp",EDGE,"E4.sketch_text.stroke-126"),sQuery(id+"F3.wireOp",EDGE,"E4.sketch_text.stroke-127"),sQuery(id+"F3.wireOp",EDGE,"E4.sketch_text.stroke-128"),sQuery(id+"F3.wireOp",EDGE,"E4.sketch_text.stroke-129"),sQuery(id+"F3.wireOp",EDGE,"E4.sketch_text.stroke-130"),sQuery(id+"F3.wireOp",EDGE,"E4.sketch_text.stroke-131"),sQuery(id+"F3.wireOp",EDGE,"E4.sketch_text.stroke-132"),sQuery(id+"F3.wireOp",EDGE,"E4.sketch_text.stroke-133"),sQuery(id+"F3.wireOp",EDGE,"E4.sketch_text.stroke-134"),sQuery(id+"F3.wireOp",EDGE,"E4.sketch_text.stroke-135"),sQuery(id+"F3.wireOp",EDGE,"E4.sketch_text.stroke-136"),sQuery(id+"F3.wireOp",EDGE,"E4.sketch_text.stroke-137"),sQuery(id+"F3.wireOp",EDGE,"E4.sketch_text.stroke-138"),sQuery(id+"F3.wireOp",EDGE,"E4.sketch_text.stroke-139"),sQuery(id+"F3.wireOp",EDGE,"E4.sketch_text.stroke-140"),sQuery(id+"F3.wireOp",EDGE,"E4.sketch_text.stroke-141"),sQuery(id+"F3.wireOp",EDGE,"E4.sketch_text.stroke-142"),sQuery(id+"F3.wireOp",EDGE,"E4.sketch_text.stroke-143"),sQuery(id+"F3.wireOp",EDGE,"E4.sketch_text.stroke-144"),sQuery(id+"F3.wireOp",EDGE,"E4.sketch_text.stroke-145"),sQuery(id+"F3.wireOp",EDGE,"E4.sketch_text.stroke-146"),sQuery(id+"F3.wireOp",EDGE,"E4.sketch_text.stroke-147"),sQuery(id+"F3.wireOp",EDGE,"E4.sketch_text.stroke-148"),sQuery(id+"F3.wireOp",EDGE,"E4.sketch_text.stroke-149"),sQuery(id+"F3.wireOp",EDGE,"E4.sketch_text.stroke-150"),sQuery(id+"F3.wireOp",EDGE,"E4.sketch_text.stroke-151"),sQuery(id+"F3.wireOp",EDGE,"E4.sketch_text.stroke-152"),sQuery(id+"F3.wireOp",EDGE,"E4.sketch_text.stroke-153"),sQuery(id+"F3.wireOp",EDGE,"E4.sketch_text.stroke-159"),sQuery(id+"F3.wireOp",EDGE,"E4.sketch_text.stroke-160"),sQuery(id+"F3.wireOp",EDGE,"E4.sketch_text.stroke-161"),sQuery(id+"F3.wireOp",EDGE,"E4.sketch_text.stroke-162"),sQuery(id+"F3.wireOp",EDGE,"E4.sketch_text.stroke-163"),sQuery(id+"F3.wireOp",EDGE,"E4.sketch_text.stroke-164"),sQuery(id+"F3.wireOp",EDGE,"E4.sketch_text.stroke-165"),sQuery(id+"F3.wireOp",EDGE,"E4.sketch_text.stroke-166"),sQuery(id+"F3.wireOp",EDGE,"E4.sketch_text.stroke-167"),sQuery(id+"F3.wireOp",EDGE,"E4.sketch_text.stroke-168"),sQuery(id+"F3.wireOp",EDGE,"E4.sketch_text.stroke-169"),sQuery(id+"F3.wireOp",EDGE,"E4.sketch_text.stroke-170"),sQuery(id+"F3.wireOp",EDGE,"E4.sketch_text.stroke-171"),sQuery(id+"F3.wireOp",EDGE,"E4.sketch_text.stroke-172"),sQuery(id+"F3.wireOp",EDGE,"E4.sketch_text.stroke-173"),sQuery(id+"F3.wireOp",EDGE,"E4.sketch_text.stroke-174"),sQuery(id+"F3.wireOp",EDGE,"E4.sketch_text.stroke-175"),sQuery(id+"F3.wireOp",EDGE,"E4.sketch_text.stroke-176"),sQuery(id+"F3.wireOp",EDGE,"E4.sketch_text.stroke-177"),sQuery(id+"F3.wireOp",EDGE,"E4.sketch_text.stroke-178"),sQuery(id+"F3.wireOp",EDGE,"E4.sketch_text.stroke-179"),sQuery(id+"F3.wireOp",EDGE,"E4.sketch_text.stroke-180"),subQ0,subQ2])],"isStart":true}),makeQuery(id+"F5.opExtrude","SWEPT_FACE",FACE,{"disambiguationData":[OSD([subQ2])]})])],"derivedFrom":makeQuery(id+"F5.opExtrude","CAP_EDGE",EDGE,{"disambiguationData":[OSD([subQ2])],"isStart":true})});}
            var Q23;
            {var subQ0=sQuery(id+"F0.wireOp",EDGE,"E0.top");var subQ1=sQuery(id+"F0.wireOp",EDGE,"E0.bottom");var subQ2=sQuery(id+"F4.wireOp",EDGE,"E31");Q23=makeQuery(id+"F5.boolean.opBoolean","SPLIT",EDGE,{"disambiguationData":[TD([makeQuery(id+"F1.opExtrude","CAP_FACE",FACE,{"disambiguationData":[OSD([subQ1,subQ0,sQuery(id+"F0.wireOp",EDGE,"E0.left"),sQuery(id+"F0.wireOp",EDGE,"E0.right")])],"isStart":false}),makeQuery(id+"F1.opExtrude","SWEPT_FACE",FACE,{"disambiguationData":[OSD([subQ0])]}),makeQuery(id+"F5.opExtrude","CAP_FACE",FACE,{"disambiguationData":[OSD([subQ1,sQuery(id+"F2.wireOp",EDGE,"E2.sketch_text.stroke-0"),sQuery(id+"F2.wireOp",EDGE,"E2.sketch_text.stroke-1"),sQuery(id+"F2.wireOp",EDGE,"E2.sketch_text.stroke-2"),sQuery(id+"F2.wireOp",EDGE,"E2.sketch_text.stroke-3"),sQuery(id+"F2.wireOp",EDGE,"E2.sketch_text.stroke-4"),sQuery(id+"F2.wireOp",EDGE,"E2.sketch_text.stroke-5"),sQuery(id+"F2.wireOp",EDGE,"E2.sketch_text.stroke-6"),sQuery(id+"F2.wireOp",EDGE,"E2.sketch_text.stroke-7"),sQuery(id+"F2.wireOp",EDGE,"E2.sketch_text.stroke-8"),sQuery(id+"F2.wireOp",EDGE,"E2.sketch_text.stroke-9"),sQuery(id+"F2.wireOp",EDGE,"E2.sketch_text.stroke-10"),sQuery(id+"F2.wireOp",EDGE,"E2.sketch_text.stroke-11"),sQuery(id+"F2.wireOp",EDGE,"E2.sketch_text.stroke-12"),sQuery(id+"F2.wireOp",EDGE,"E2.sketch_text.stroke-13"),sQuery(id+"F2.wireOp",EDGE,"E2.sketch_text.stroke-14"),sQuery(id+"F2.wireOp",EDGE,"E2.sketch_text.stroke-15"),sQuery(id+"F2.wireOp",EDGE,"E2.sketch_text.stroke-16"),sQuery(id+"F2.wireOp",EDGE,"E2.sketch_text.stroke-17"),sQuery(id+"F2.wireOp",EDGE,"E2.sketch_text.stroke-18"),sQuery(id+"F2.wireOp",EDGE,"E2.sketch_text.stroke-19"),sQuery(id+"F2.wireOp",EDGE,"E2.sketch_text.stroke-20"),sQuery(id+"F2.wireOp",EDGE,"E2.sketch_text.stroke-21"),sQuery(id+"F2.wireOp",EDGE,"E2.sketch_text.stroke-22"),sQuery(id+"F2.wireOp",EDGE,"E2.sketch_text.stroke-23"),sQuery(id+"F2.wireOp",EDGE,"E2.sketch_text.stroke-24"),sQuery(id+"F2.wireOp",EDGE,"E2.sketch_text.stroke-25"),sQuery(id+"F2.wireOp",EDGE,"E2.sketch_text.stroke-26"),sQuery(id+"F2.wireOp",EDGE,"E2.sketch_text.stroke-27"),sQuery(id+"F2.wireOp",EDGE,"E2.sketch_text.stroke-28"),sQuery(id+"F2.wireOp",EDGE,"E2.sketch_text.stroke-29"),sQuery(id+"F2.wireOp",EDGE,"E2.sketch_text.stroke-30"),sQuery(id+"F2.wireOp",EDGE,"E2.sketch_text.stroke-31"),sQuery(id+"F2.wireOp",EDGE,"E2.sketch_text.stroke-32"),sQuery(id+"F2.wireOp",EDGE,"E2.sketch_text.stroke-33"),sQuery(id+"F2.wireOp",EDGE,"E2.sketch_text.stroke-34"),sQuery(id+"F2.wireOp",EDGE,"E2.sketch_text.stroke-35"),sQuery(id+"F2.wireOp",EDGE,"E2.sketch_text.stroke-36"),sQuery(id+"F2.wireOp",EDGE,"E2.sketch_text.stroke-37"),sQuery(id+"F2.wireOp",EDGE,"E2.sketch_text.stroke-38"),sQuery(id+"F2.wireOp",EDGE,"E2.sketch_text.stroke-39"),sQuery(id+"F2.wireOp",EDGE,"E2.sketch_text.stroke-40"),sQuery(id+"F2.wireOp",EDGE,"E2.sketch_text.stroke-41"),sQuery(id+"F2.wireOp",EDGE,"E2.sketch_text.stroke-42"),sQuery(id+"F2.wireOp",EDGE,"E2.sketch_text.stroke-43"),sQuery(id+"F2.wireOp",EDGE,"E2.sketch_text.stroke-44"),sQuery(id+"F2.wireOp",EDGE,"E2.sketch_text.stroke-45"),sQuery(id+"F2.wireOp",EDGE,"E2.sketch_text.stroke-46"),sQuery(id+"F2.wireOp",EDGE,"E2.sketch_text.stroke-47"),sQuery(id+"F2.wireOp",EDGE,"E2.sketch_text.stroke-48"),sQuery(id+"F2.wireOp",EDGE,"E2.sketch_text.stroke-49"),sQuery(id+"F2.wireOp",EDGE,"E2.sketch_text.stroke-50"),sQuery(id+"F2.wireOp",EDGE,"E2.sketch_text.stroke-51"),sQuery(id+"F2.wireOp",EDGE,"E2.sketch_text.stroke-52"),sQuery(id+"F2.wireOp",EDGE,"E2.sketch_text.stroke-53"),sQuery(id+"F2.wireOp",EDGE,"E2.sketch_text.stroke-54"),sQuery(id+"F2.wireOp",EDGE,"E2.sketch_text.stroke-55"),sQuery(id+"F2.wireOp",EDGE,"E2.sketch_text.stroke-56"),sQuery(id+"F2.wireOp",EDGE,"E2.sketch_text.stroke-57"),sQuery(id+"F2.wireOp",EDGE,"E2.sketch_text.stroke-58"),sQuery(id+"F2.wireOp",EDGE,"E2.sketch_text.stroke-59"),sQuery(id+"F2.wireOp",EDGE,"E2.sketch_text.stroke-60"),sQuery(id+"F2.wireOp",EDGE,"E2.sketch_text.stroke-61"),sQuery(id+"F2.wireOp",EDGE,"E2.sketch_text.stroke-62"),sQuery(id+"F2.wireOp",EDGE,"E2.sketch_text.stroke-63"),sQuery(id+"F2.wireOp",EDGE,"E2.sketch_text.stroke-64"),sQuery(id+"F2.wireOp",EDGE,"E2.sketch_text.stroke-65"),sQuery(id+"F2.wireOp",EDGE,"E2.sketch_text.stroke-66"),sQuery(id+"F2.wireOp",EDGE,"E2.sketch_text.stroke-67"),sQuery(id+"F2.wireOp",EDGE,"E2.sketch_text.stroke-68"),sQuery(id+"F2.wireOp",EDGE,"E2.sketch_text.stroke-69"),sQuery(id+"F2.wireOp",EDGE,"E2.sketch_text.stroke-70"),sQuery(id+"F2.wireOp",EDGE,"E2.sketch_text.stroke-71"),sQuery(id+"F2.wireOp",EDGE,"E2.sketch_text.stroke-72"),sQuery(id+"F2.wireOp",EDGE,"E2.sketch_text.stroke-73"),sQuery(id+"F2.wireOp",EDGE,"E2.sketch_text.stroke-74"),sQuery(id+"F2.wireOp",EDGE,"E2.sketch_text.stroke-75"),sQuery(id+"F2.wireOp",EDGE,"E2.sketch_text.stroke-76"),sQuery(id+"F2.wireOp",EDGE,"E2.sketch_text.stroke-77"),sQuery(id+"F2.wireOp",EDGE,"E2.sketch_text.stroke-78"),sQuery(id+"F2.wireOp",EDGE,"E2.sketch_text.stroke-79"),sQuery(id+"F2.wireOp",EDGE,"E2.sketch_text.stroke-80"),sQuery(id+"F2.wireOp",EDGE,"E2.sketch_text.stroke-81"),sQuery(id+"F2.wireOp",EDGE,"E2.sketch_text.stroke-82"),sQuery(id+"F2.wireOp",EDGE,"E2.sketch_text.stroke-83"),sQuery(id+"F2.wireOp",EDGE,"E2.sketch_text.stroke-84"),sQuery(id+"F2.wireOp",EDGE,"E2.sketch_text.stroke-85"),sQuery(id+"F2.wireOp",EDGE,"E2.sketch_text.stroke-86"),sQuery(id+"F2.wireOp",EDGE,"E2.sketch_text.stroke-87"),sQuery(id+"F2.wireOp",EDGE,"E2.sketch_text.stroke-88"),sQuery(id+"F2.wireOp",EDGE,"E2.sketch_text.stroke-89"),sQuery(id+"F2.wireOp",EDGE,"E2.sketch_text.stroke-90"),sQuery(id+"F2.wireOp",EDGE,"E2.sketch_text.stroke-91"),sQuery(id+"F2.wireOp",EDGE,"E2.sketch_text.stroke-92"),sQuery(id+"F2.wireOp",EDGE,"E2.sketch_text.stroke-93"),sQuery(id+"F2.wireOp",EDGE,"E2.sketch_text.stroke-94"),sQuery(id+"F2.wireOp",EDGE,"E2.sketch_text.stroke-95"),sQuery(id+"F2.wireOp",EDGE,"E2.sketch_text.stroke-96"),sQuery(id+"F2.wireOp",EDGE,"E2.sketch_text.stroke-97"),sQuery(id+"F2.wireOp",EDGE,"E2.sketch_text.stroke-98"),sQuery(id+"F2.wireOp",EDGE,"E2.sketch_text.stroke-99"),sQuery(id+"F2.wireOp",EDGE,"E2.sketch_text.stroke-100"),sQuery(id+"F2.wireOp",EDGE,"E2.sketch_text.stroke-101"),sQuery(id+"F2.wireOp",EDGE,"E2.sketch_text.stroke-102"),sQuery(id+"F2.wireOp",EDGE,"E2.sketch_text.stroke-103"),sQuery(id+"F2.wireOp",EDGE,"E2.sketch_text.stroke-104"),sQuery(id+"F2.wireOp",EDGE,"E2.sketch_text.stroke-105"),sQuery(id+"F2.wireOp",EDGE,"E2.sketch_text.stroke-106"),sQuery(id+"F2.wireOp",EDGE,"E2.sketch_text.stroke-107"),sQuery(id+"F2.wireOp",EDGE,"E2.sketch_text.stroke-108"),sQuery(id+"F2.wireOp",EDGE,"E2.sketch_text.stroke-109"),sQuery(id+"F2.wireOp",EDGE,"E2.sketch_text.stroke-110"),sQuery(id+"F2.wireOp",EDGE,"E2.sketch_text.stroke-111"),sQuery(id+"F2.wireOp",EDGE,"E2.sketch_text.stroke-112"),sQuery(id+"F2.wireOp",EDGE,"E2.sketch_text.stroke-113"),sQuery(id+"F2.wireOp",EDGE,"E2.sketch_text.stroke-114"),sQuery(id+"F2.wireOp",EDGE,"E2.sketch_text.stroke-115"),sQuery(id+"F2.wireOp",EDGE,"E2.sketch_text.stroke-116"),sQuery(id+"F2.wireOp",EDGE,"E2.sketch_text.stroke-117"),sQuery(id+"F2.wireOp",EDGE,"E2.sketch_text.stroke-118"),sQuery(id+"F2.wireOp",EDGE,"E2.sketch_text.stroke-119"),sQuery(id+"F2.wireOp",EDGE,"E2.sketch_text.stroke-120"),sQuery(id+"F2.wireOp",EDGE,"E2.sketch_text.stroke-121"),sQuery(id+"F2.wireOp",EDGE,"E2.sketch_text.stroke-122"),sQuery(id+"F2.wireOp",EDGE,"E2.sketch_text.stroke-123"),sQuery(id+"F2.wireOp",EDGE,"E2.sketch_text.stroke-124"),sQuery(id+"F2.wireOp",EDGE,"E2.sketch_text.stroke-125"),sQuery(id+"F2.wireOp",EDGE,"E2.sketch_text.stroke-126"),sQuery(id+"F2.wireOp",EDGE,"E2.sketch_text.stroke-127"),sQuery(id+"F2.wireOp",EDGE,"E2.sketch_text.stroke-128"),sQuery(id+"F2.wireOp",EDGE,"E2.sketch_text.stroke-129"),sQuery(id+"F2.wireOp",EDGE,"E2.sketch_text.stroke-130"),sQuery(id+"F2.wireOp",EDGE,"E2.sketch_text.stroke-131"),sQuery(id+"F2.wireOp",EDGE,"E2.sketch_text.stroke-132"),sQuery(id+"F2.wireOp",EDGE,"E2.sketch_text.stroke-133"),sQuery(id+"F2.wireOp",EDGE,"E2.sketch_text.stroke-134"),sQuery(id+"F2.wireOp",EDGE,"E2.sketch_text.stroke-135"),sQuery(id+"F2.wireOp",EDGE,"E2.sketch_text.stroke-136"),sQuery(id+"F2.wireOp",EDGE,"E2.sketch_text.stroke-137"),sQuery(id+"F2.wireOp",EDGE,"E2.sketch_text.stroke-138"),sQuery(id+"F2.wireOp",EDGE,"E2.sketch_text.stroke-139"),sQuery(id+"F2.wireOp",EDGE,"E2.sketch_text.stroke-140"),sQuery(id+"F2.wireOp",EDGE,"E2.sketch_text.stroke-141"),sQuery(id+"F2.wireOp",EDGE,"E2.sketch_text.stroke-142"),sQuery(id+"F2.wireOp",EDGE,"E2.sketch_text.stroke-143"),sQuery(id+"F2.wireOp",EDGE,"E2.sketch_text.stroke-144"),sQuery(id+"F2.wireOp",EDGE,"E2.sketch_text.stroke-145"),sQuery(id+"F2.wireOp",EDGE,"E2.sketch_text.stroke-146"),sQuery(id+"F2.wireOp",EDGE,"E2.sketch_text.stroke-147"),sQuery(id+"F2.wireOp",EDGE,"E2.sketch_text.stroke-148"),sQuery(id+"F2.wireOp",EDGE,"E2.sketch_text.stroke-149"),sQuery(id+"F2.wireOp",EDGE,"E2.sketch_text.stroke-150"),sQuery(id+"F2.wireOp",EDGE,"E2.sketch_text.stroke-151"),sQuery(id+"F2.wireOp",EDGE,"E2.sketch_text.stroke-152"),sQuery(id+"F2.wireOp",EDGE,"E2.sketch_text.stroke-153"),sQuery(id+"F2.wireOp",EDGE,"E2.sketch_text.stroke-154"),sQuery(id+"F2.wireOp",EDGE,"E2.sketch_text.stroke-155"),sQuery(id+"F2.wireOp",EDGE,"E2.sketch_text.stroke-156"),sQuery(id+"F2.wireOp",EDGE,"E2.sketch_text.stroke-157"),sQuery(id+"F2.wireOp",EDGE,"E2.sketch_text.stroke-158"),sQuery(id+"F2.wireOp",EDGE,"E2.sketch_text.stroke-159"),sQuery(id+"F2.wireOp",EDGE,"E2.sketch_text.stroke-160"),sQuery(id+"F2.wireOp",EDGE,"E2.sketch_text.stroke-161"),sQuery(id+"F2.wireOp",EDGE,"E2.sketch_text.stroke-162"),sQuery(id+"F2.wireOp",EDGE,"E2.sketch_text.stroke-163"),sQuery(id+"F2.wireOp",EDGE,"E2.sketch_text.stroke-164"),sQuery(id+"F2.wireOp",EDGE,"E2.sketch_text.stroke-165"),sQuery(id+"F2.wireOp",EDGE,"E2.sketch_text.stroke-166"),sQuery(id+"F2.wireOp",EDGE,"E2.sketch_text.stroke-167"),sQuery(id+"F2.wireOp",EDGE,"E2.sketch_text.stroke-168"),sQuery(id+"F2.wireOp",EDGE,"E2.sketch_text.stroke-169"),sQuery(id+"F2.wireOp",EDGE,"E2.sketch_text.stroke-170"),sQuery(id+"F2.wireOp",EDGE,"E2.sketch_text.stroke-171"),sQuery(id+"F2.wireOp",EDGE,"E2.sketch_text.stroke-172"),sQuery(id+"F2.wireOp",EDGE,"E2.sketch_text.stroke-173"),sQuery(id+"F3.wireOp",EDGE,"E4.sketch_text.stroke-0"),sQuery(id+"F3.wireOp",EDGE,"E4.sketch_text.stroke-1"),sQuery(id+"F3.wireOp",EDGE,"E4.sketch_text.stroke-2"),sQuery(id+"F3.wireOp",EDGE,"E4.sketch_text.stroke-3"),sQuery(id+"F3.wireOp",EDGE,"E4.sketch_text.stroke-4"),sQuery(id+"F3.wireOp",EDGE,"E4.sketch_text.stroke-5"),sQuery(id+"F3.wireOp",EDGE,"E4.sketch_text.stroke-6"),sQuery(id+"F3.wireOp",EDGE,"E4.sketch_text.stroke-7"),sQuery(id+"F3.wireOp",EDGE,"E4.sketch_text.stroke-8"),sQuery(id+"F3.wireOp",EDGE,"E4.sketch_text.stroke-9"),sQuery(id+"F3.wireOp",EDGE,"E4.sketch_text.stroke-10"),sQuery(id+"F3.wireOp",EDGE,"E4.sketch_text.stroke-11"),sQuery(id+"F3.wireOp",EDGE,"E4.sketch_text.stroke-12"),sQuery(id+"F3.wireOp",EDGE,"E4.sketch_text.stroke-13"),sQuery(id+"F3.wireOp",EDGE,"E4.sketch_text.stroke-14"),sQuery(id+"F3.wireOp",EDGE,"E4.sketch_text.stroke-15"),sQuery(id+"F3.wireOp",EDGE,"E4.sketch_text.stroke-16"),sQuery(id+"F3.wireOp",EDGE,"E4.sketch_text.stroke-17"),sQuery(id+"F3.wireOp",EDGE,"E4.sketch_text.stroke-18"),sQuery(id+"F3.wireOp",EDGE,"E4.sketch_text.stroke-19"),sQuery(id+"F3.wireOp",EDGE,"E4.sketch_text.stroke-20"),sQuery(id+"F3.wireOp",EDGE,"E4.sketch_text.stroke-21"),sQuery(id+"F3.wireOp",EDGE,"E4.sketch_text.stroke-22"),sQuery(id+"F3.wireOp",EDGE,"E4.sketch_text.stroke-23"),sQuery(id+"F3.wireOp",EDGE,"E4.sketch_text.stroke-24"),sQuery(id+"F3.wireOp",EDGE,"E4.sketch_text.stroke-25"),sQuery(id+"F3.wireOp",EDGE,"E4.sketch_text.stroke-26"),sQuery(id+"F3.wireOp",EDGE,"E4.sketch_text.stroke-27"),sQuery(id+"F3.wireOp",EDGE,"E4.sketch_text.stroke-28"),sQuery(id+"F3.wireOp",EDGE,"E4.sketch_text.stroke-29"),sQuery(id+"F3.wireOp",EDGE,"E4.sketch_text.stroke-30"),sQuery(id+"F3.wireOp",EDGE,"E4.sketch_text.stroke-31"),sQuery(id+"F3.wireOp",EDGE,"E4.sketch_text.stroke-32"),sQuery(id+"F3.wireOp",EDGE,"E4.sketch_text.stroke-33"),sQuery(id+"F3.wireOp",EDGE,"E4.sketch_text.stroke-34"),sQuery(id+"F3.wireOp",EDGE,"E4.sketch_text.stroke-35"),sQuery(id+"F3.wireOp",EDGE,"E4.sketch_text.stroke-36"),sQuery(id+"F3.wireOp",EDGE,"E4.sketch_text.stroke-37"),sQuery(id+"F3.wireOp",EDGE,"E4.sketch_text.stroke-38"),sQuery(id+"F3.wireOp",EDGE,"E4.sketch_text.stroke-39"),sQuery(id+"F3.wireOp",EDGE,"E4.sketch_text.stroke-40"),sQuery(id+"F3.wireOp",EDGE,"E4.sketch_text.stroke-41"),sQuery(id+"F3.wireOp",EDGE,"E4.sketch_text.stroke-42"),sQuery(id+"F3.wireOp",EDGE,"E4.sketch_text.stroke-43"),sQuery(id+"F3.wireOp",EDGE,"E4.sketch_text.stroke-44"),sQuery(id+"F3.wireOp",EDGE,"E4.sketch_text.stroke-45"),sQuery(id+"F3.wireOp",EDGE,"E4.sketch_text.stroke-46"),sQuery(id+"F3.wireOp",EDGE,"E4.sketch_text.stroke-47"),sQuery(id+"F3.wireOp",EDGE,"E4.sketch_text.stroke-48"),sQuery(id+"F3.wireOp",EDGE,"E4.sketch_text.stroke-49"),sQuery(id+"F3.wireOp",EDGE,"E4.sketch_text.stroke-50"),sQuery(id+"F3.wireOp",EDGE,"E4.sketch_text.stroke-51"),sQuery(id+"F3.wireOp",EDGE,"E4.sketch_text.stroke-52"),sQuery(id+"F3.wireOp",EDGE,"E4.sketch_text.stroke-53"),sQuery(id+"F3.wireOp",EDGE,"E4.sketch_text.stroke-54"),sQuery(id+"F3.wireOp",EDGE,"E4.sketch_text.stroke-55"),sQuery(id+"F3.wireOp",EDGE,"E4.sketch_text.stroke-56"),sQuery(id+"F3.wireOp",EDGE,"E4.sketch_text.stroke-57"),sQuery(id+"F3.wireOp",EDGE,"E4.sketch_text.stroke-58"),sQuery(id+"F3.wireOp",EDGE,"E4.sketch_text.stroke-59"),sQuery(id+"F3.wireOp",EDGE,"E4.sketch_text.stroke-60"),sQuery(id+"F3.wireOp",EDGE,"E4.sketch_text.stroke-61"),sQuery(id+"F3.wireOp",EDGE,"E4.sketch_text.stroke-62"),sQuery(id+"F3.wireOp",EDGE,"E4.sketch_text.stroke-71"),sQuery(id+"F3.wireOp",EDGE,"E4.sketch_text.stroke-72"),sQuery(id+"F3.wireOp",EDGE,"E4.sketch_text.stroke-73"),sQuery(id+"F3.wireOp",EDGE,"E4.sketch_text.stroke-74"),sQuery(id+"F3.wireOp",EDGE,"E4.sketch_text.stroke-75"),sQuery(id+"F3.wireOp",EDGE,"E4.sketch_text.stroke-76"),sQuery(id+"F3.wireOp",EDGE,"E4.sketch_text.stroke-77"),sQuery(id+"F3.wireOp",EDGE,"E4.sketch_text.stroke-78"),sQuery(id+"F3.wireOp",EDGE,"E4.sketch_text.stroke-79"),sQuery(id+"F3.wireOp",EDGE,"E4.sketch_text.stroke-80"),sQuery(id+"F3.wireOp",EDGE,"E4.sketch_text.stroke-81"),sQuery(id+"F3.wireOp",EDGE,"E4.sketch_text.stroke-82"),sQuery(id+"F3.wireOp",EDGE,"E4.sketch_text.stroke-83"),sQuery(id+"F3.wireOp",EDGE,"E4.sketch_text.stroke-84"),sQuery(id+"F3.wireOp",EDGE,"E4.sketch_text.stroke-85"),sQuery(id+"F3.wireOp",EDGE,"E4.sketch_text.stroke-86"),sQuery(id+"F3.wireOp",EDGE,"E4.sketch_text.stroke-87"),sQuery(id+"F3.wireOp",EDGE,"E4.sketch_text.stroke-88"),sQuery(id+"F3.wireOp",EDGE,"E4.sketch_text.stroke-89"),sQuery(id+"F3.wireOp",EDGE,"E4.sketch_text.stroke-90"),sQuery(id+"F3.wireOp",EDGE,"E4.sketch_text.stroke-91"),sQuery(id+"F3.wireOp",EDGE,"E4.sketch_text.stroke-92"),sQuery(id+"F3.wireOp",EDGE,"E4.sketch_text.stroke-93"),sQuery(id+"F3.wireOp",EDGE,"E4.sketch_text.stroke-94"),sQuery(id+"F3.wireOp",EDGE,"E4.sketch_text.stroke-95"),sQuery(id+"F3.wireOp",EDGE,"E4.sketch_text.stroke-96"),sQuery(id+"F3.wireOp",EDGE,"E4.sketch_text.stroke-97"),sQuery(id+"F3.wireOp",EDGE,"E4.sketch_text.stroke-103"),sQuery(id+"F3.wireOp",EDGE,"E4.sketch_text.stroke-104"),sQuery(id+"F3.wireOp",EDGE,"E4.sketch_text.stroke-105"),sQuery(id+"F3.wireOp",EDGE,"E4.sketch_text.stroke-106"),sQuery(id+"F3.wireOp",EDGE,"E4.sketch_text.stroke-107"),sQuery(id+"F3.wireOp",EDGE,"E4.sketch_text.stroke-108"),sQuery(id+"F3.wireOp",EDGE,"E4.sketch_text.stroke-109"),sQuery(id+"F3.wireOp",EDGE,"E4.sketch_text.stroke-110"),sQuery(id+"F3.wireOp",EDGE,"E4.sketch_text.stroke-111"),sQuery(id+"F3.wireOp",EDGE,"E4.sketch_text.stroke-112"),sQuery(id+"F3.wireOp",EDGE,"E4.sketch_text.stroke-113"),sQuery(id+"F3.wireOp",EDGE,"E4.sketch_text.stroke-114"),sQuery(id+"F3.wireOp",EDGE,"E4.sketch_text.stroke-115"),sQuery(id+"F3.wireOp",EDGE,"E4.sketch_text.stroke-116"),sQuery(id+"F3.wireOp",EDGE,"E4.sketch_text.stroke-117"),sQuery(id+"F3.wireOp",EDGE,"E4.sketch_text.stroke-118"),sQuery(id+"F3.wireOp",EDGE,"E4.sketch_text.stroke-119"),sQuery(id+"F3.wireOp",EDGE,"E4.sketch_text.stroke-120"),sQuery(id+"F3.wireOp",EDGE,"E4.sketch_text.stroke-121"),sQuery(id+"F3.wireOp",EDGE,"E4.sketch_text.stroke-122"),sQuery(id+"F3.wireOp",EDGE,"E4.sketch_text.stroke-123"),sQuery(id+"F3.wireOp",EDGE,"E4.sketch_text.stroke-124"),sQuery(id+"F3.wireOp",EDGE,"E4.sketch_text.stroke-125"),sQuery(id+"F3.wireOp",EDGE,"E4.sketch_text.stroke-126"),sQuery(id+"F3.wireOp",EDGE,"E4.sketch_text.stroke-127"),sQuery(id+"F3.wireOp",EDGE,"E4.sketch_text.stroke-128"),sQuery(id+"F3.wireOp",EDGE,"E4.sketch_text.stroke-129"),sQuery(id+"F3.wireOp",EDGE,"E4.sketch_text.stroke-130"),sQuery(id+"F3.wireOp",EDGE,"E4.sketch_text.stroke-131"),sQuery(id+"F3.wireOp",EDGE,"E4.sketch_text.stroke-132"),sQuery(id+"F3.wireOp",EDGE,"E4.sketch_text.stroke-133"),sQuery(id+"F3.wireOp",EDGE,"E4.sketch_text.stroke-134"),sQuery(id+"F3.wireOp",EDGE,"E4.sketch_text.stroke-135"),sQuery(id+"F3.wireOp",EDGE,"E4.sketch_text.stroke-136"),sQuery(id+"F3.wireOp",EDGE,"E4.sketch_text.stroke-137"),sQuery(id+"F3.wireOp",EDGE,"E4.sketch_text.stroke-138"),sQuery(id+"F3.wireOp",EDGE,"E4.sketch_text.stroke-139"),sQuery(id+"F3.wireOp",EDGE,"E4.sketch_text.stroke-140"),sQuery(id+"F3.wireOp",EDGE,"E4.sketch_text.stroke-141"),sQuery(id+"F3.wireOp",EDGE,"E4.sketch_text.stroke-142"),sQuery(id+"F3.wireOp",EDGE,"E4.sketch_text.stroke-143"),sQuery(id+"F3.wireOp",EDGE,"E4.sketch_text.stroke-144"),sQuery(id+"F3.wireOp",EDGE,"E4.sketch_text.stroke-145"),sQuery(id+"F3.wireOp",EDGE,"E4.sketch_text.stroke-146"),sQuery(id+"F3.wireOp",EDGE,"E4.sketch_text.stroke-147"),sQuery(id+"F3.wireOp",EDGE,"E4.sketch_text.stroke-148"),sQuery(id+"F3.wireOp",EDGE,"E4.sketch_text.stroke-149"),sQuery(id+"F3.wireOp",EDGE,"E4.sketch_text.stroke-150"),sQuery(id+"F3.wireOp",EDGE,"E4.sketch_text.stroke-151"),sQuery(id+"F3.wireOp",EDGE,"E4.sketch_text.stroke-152"),sQuery(id+"F3.wireOp",EDGE,"E4.sketch_text.stroke-153"),sQuery(id+"F3.wireOp",EDGE,"E4.sketch_text.stroke-159"),sQuery(id+"F3.wireOp",EDGE,"E4.sketch_text.stroke-160"),sQuery(id+"F3.wireOp",EDGE,"E4.sketch_text.stroke-161"),sQuery(id+"F3.wireOp",EDGE,"E4.sketch_text.stroke-162"),sQuery(id+"F3.wireOp",EDGE,"E4.sketch_text.stroke-163"),sQuery(id+"F3.wireOp",EDGE,"E4.sketch_text.stroke-164"),sQuery(id+"F3.wireOp",EDGE,"E4.sketch_text.stroke-165"),sQuery(id+"F3.wireOp",EDGE,"E4.sketch_text.stroke-166"),sQuery(id+"F3.wireOp",EDGE,"E4.sketch_text.stroke-167"),sQuery(id+"F3.wireOp",EDGE,"E4.sketch_text.stroke-168"),sQuery(id+"F3.wireOp",EDGE,"E4.sketch_text.stroke-169"),sQuery(id+"F3.wireOp",EDGE,"E4.sketch_text.stroke-170"),sQuery(id+"F3.wireOp",EDGE,"E4.sketch_text.stroke-171"),sQuery(id+"F3.wireOp",EDGE,"E4.sketch_text.stroke-172"),sQuery(id+"F3.wireOp",EDGE,"E4.sketch_text.stroke-173"),sQuery(id+"F3.wireOp",EDGE,"E4.sketch_text.stroke-174"),sQuery(id+"F3.wireOp",EDGE,"E4.sketch_text.stroke-175"),sQuery(id+"F3.wireOp",EDGE,"E4.sketch_text.stroke-176"),sQuery(id+"F3.wireOp",EDGE,"E4.sketch_text.stroke-177"),sQuery(id+"F3.wireOp",EDGE,"E4.sketch_text.stroke-178"),sQuery(id+"F3.wireOp",EDGE,"E4.sketch_text.stroke-179"),sQuery(id+"F3.wireOp",EDGE,"E4.sketch_text.stroke-180"),sQuery(id+"F4.wireOp",EDGE,"E30"),subQ2])],"isStart":true}),makeQuery(id+"F5.opExtrude","SWEPT_FACE",FACE,{"disambiguationData":[OSD([subQ2])]})])],"derivedFrom":makeQuery(id+"F5.opExtrude","CAP_EDGE",EDGE,{"disambiguationData":[OSD([subQ2])],"isStart":true})});}
            var Q24;
            {var subQ0=sQuery(id+"F0.wireOp",EDGE,"E0.top");var subQ1=sQuery(id+"F0.wireOp",EDGE,"E0.bottom");var subQ2=sQuery(id+"F4.wireOp",EDGE,"E30");Q24=makeQuery(id+"F5.boolean.opBoolean","SPLIT",EDGE,{"disambiguationData":[TD([makeQuery(id+"F1.opExtrude","CAP_FACE",FACE,{"disambiguationData":[OSD([subQ1,subQ0,sQuery(id+"F0.wireOp",EDGE,"E0.left"),sQuery(id+"F0.wireOp",EDGE,"E0.right")])],"isStart":false}),makeQuery(id+"F1.opExtrude","SWEPT_FACE",FACE,{"disambiguationData":[OSD([subQ0])]}),makeQuery(id+"F5.opExtrude","SWEPT_FACE",FACE,{"disambiguationData":[OSD([subQ2])]}),makeQuery(id+"F5.opExtrude","CAP_FACE",FACE,{"disambiguationData":[OSD([subQ1,sQuery(id+"F2.wireOp",EDGE,"E2.sketch_text.stroke-0"),sQuery(id+"F2.wireOp",EDGE,"E2.sketch_text.stroke-1"),sQuery(id+"F2.wireOp",EDGE,"E2.sketch_text.stroke-2"),sQuery(id+"F2.wireOp",EDGE,"E2.sketch_text.stroke-3"),sQuery(id+"F2.wireOp",EDGE,"E2.sketch_text.stroke-4"),sQuery(id+"F2.wireOp",EDGE,"E2.sketch_text.stroke-5"),sQuery(id+"F2.wireOp",EDGE,"E2.sketch_text.stroke-6"),sQuery(id+"F2.wireOp",EDGE,"E2.sketch_text.stroke-7"),sQuery(id+"F2.wireOp",EDGE,"E2.sketch_text.stroke-8"),sQuery(id+"F2.wireOp",EDGE,"E2.sketch_text.stroke-9"),sQuery(id+"F2.wireOp",EDGE,"E2.sketch_text.stroke-10"),sQuery(id+"F2.wireOp",EDGE,"E2.sketch_text.stroke-11"),sQuery(id+"F2.wireOp",EDGE,"E2.sketch_text.stroke-12"),sQuery(id+"F2.wireOp",EDGE,"E2.sketch_text.stroke-13"),sQuery(id+"F2.wireOp",EDGE,"E2.sketch_text.stroke-14"),sQuery(id+"F2.wireOp",EDGE,"E2.sketch_text.stroke-15"),sQuery(id+"F2.wireOp",EDGE,"E2.sketch_text.stroke-16"),sQuery(id+"F2.wireOp",EDGE,"E2.sketch_text.stroke-17"),sQuery(id+"F2.wireOp",EDGE,"E2.sketch_text.stroke-18"),sQuery(id+"F2.wireOp",EDGE,"E2.sketch_text.stroke-19"),sQuery(id+"F2.wireOp",EDGE,"E2.sketch_text.stroke-20"),sQuery(id+"F2.wireOp",EDGE,"E2.sketch_text.stroke-21"),sQuery(id+"F2.wireOp",EDGE,"E2.sketch_text.stroke-22"),sQuery(id+"F2.wireOp",EDGE,"E2.sketch_text.stroke-23"),sQuery(id+"F2.wireOp",EDGE,"E2.sketch_text.stroke-24"),sQuery(id+"F2.wireOp",EDGE,"E2.sketch_text.stroke-25"),sQuery(id+"F2.wireOp",EDGE,"E2.sketch_text.stroke-26"),sQuery(id+"F2.wireOp",EDGE,"E2.sketch_text.stroke-27"),sQuery(id+"F2.wireOp",EDGE,"E2.sketch_text.stroke-28"),sQuery(id+"F2.wireOp",EDGE,"E2.sketch_text.stroke-29"),sQuery(id+"F2.wireOp",EDGE,"E2.sketch_text.stroke-30"),sQuery(id+"F2.wireOp",EDGE,"E2.sketch_text.stroke-31"),sQuery(id+"F2.wireOp",EDGE,"E2.sketch_text.stroke-32"),sQuery(id+"F2.wireOp",EDGE,"E2.sketch_text.stroke-33"),sQuery(id+"F2.wireOp",EDGE,"E2.sketch_text.stroke-34"),sQuery(id+"F2.wireOp",EDGE,"E2.sketch_text.stroke-35"),sQuery(id+"F2.wireOp",EDGE,"E2.sketch_text.stroke-36"),sQuery(id+"F2.wireOp",EDGE,"E2.sketch_text.stroke-37"),sQuery(id+"F2.wireOp",EDGE,"E2.sketch_text.stroke-38"),sQuery(id+"F2.wireOp",EDGE,"E2.sketch_text.stroke-39"),sQuery(id+"F2.wireOp",EDGE,"E2.sketch_text.stroke-40"),sQuery(id+"F2.wireOp",EDGE,"E2.sketch_text.stroke-41"),sQuery(id+"F2.wireOp",EDGE,"E2.sketch_text.stroke-42"),sQuery(id+"F2.wireOp",EDGE,"E2.sketch_text.stroke-43"),sQuery(id+"F2.wireOp",EDGE,"E2.sketch_text.stroke-44"),sQuery(id+"F2.wireOp",EDGE,"E2.sketch_text.stroke-45"),sQuery(id+"F2.wireOp",EDGE,"E2.sketch_text.stroke-46"),sQuery(id+"F2.wireOp",EDGE,"E2.sketch_text.stroke-47"),sQuery(id+"F2.wireOp",EDGE,"E2.sketch_text.stroke-48"),sQuery(id+"F2.wireOp",EDGE,"E2.sketch_text.stroke-49"),sQuery(id+"F2.wireOp",EDGE,"E2.sketch_text.stroke-50"),sQuery(id+"F2.wireOp",EDGE,"E2.sketch_text.stroke-51"),sQuery(id+"F2.wireOp",EDGE,"E2.sketch_text.stroke-52"),sQuery(id+"F2.wireOp",EDGE,"E2.sketch_text.stroke-53"),sQuery(id+"F2.wireOp",EDGE,"E2.sketch_text.stroke-54"),sQuery(id+"F2.wireOp",EDGE,"E2.sketch_text.stroke-55"),sQuery(id+"F2.wireOp",EDGE,"E2.sketch_text.stroke-56"),sQuery(id+"F2.wireOp",EDGE,"E2.sketch_text.stroke-57"),sQuery(id+"F2.wireOp",EDGE,"E2.sketch_text.stroke-58"),sQuery(id+"F2.wireOp",EDGE,"E2.sketch_text.stroke-59"),sQuery(id+"F2.wireOp",EDGE,"E2.sketch_text.stroke-60"),sQuery(id+"F2.wireOp",EDGE,"E2.sketch_text.stroke-61"),sQuery(id+"F2.wireOp",EDGE,"E2.sketch_text.stroke-62"),sQuery(id+"F2.wireOp",EDGE,"E2.sketch_text.stroke-63"),sQuery(id+"F2.wireOp",EDGE,"E2.sketch_text.stroke-64"),sQuery(id+"F2.wireOp",EDGE,"E2.sketch_text.stroke-65"),sQuery(id+"F2.wireOp",EDGE,"E2.sketch_text.stroke-66"),sQuery(id+"F2.wireOp",EDGE,"E2.sketch_text.stroke-67"),sQuery(id+"F2.wireOp",EDGE,"E2.sketch_text.stroke-68"),sQuery(id+"F2.wireOp",EDGE,"E2.sketch_text.stroke-69"),sQuery(id+"F2.wireOp",EDGE,"E2.sketch_text.stroke-70"),sQuery(id+"F2.wireOp",EDGE,"E2.sketch_text.stroke-71"),sQuery(id+"F2.wireOp",EDGE,"E2.sketch_text.stroke-72"),sQuery(id+"F2.wireOp",EDGE,"E2.sketch_text.stroke-73"),sQuery(id+"F2.wireOp",EDGE,"E2.sketch_text.stroke-74"),sQuery(id+"F2.wireOp",EDGE,"E2.sketch_text.stroke-75"),sQuery(id+"F2.wireOp",EDGE,"E2.sketch_text.stroke-76"),sQuery(id+"F2.wireOp",EDGE,"E2.sketch_text.stroke-77"),sQuery(id+"F2.wireOp",EDGE,"E2.sketch_text.stroke-78"),sQuery(id+"F2.wireOp",EDGE,"E2.sketch_text.stroke-79"),sQuery(id+"F2.wireOp",EDGE,"E2.sketch_text.stroke-80"),sQuery(id+"F2.wireOp",EDGE,"E2.sketch_text.stroke-81"),sQuery(id+"F2.wireOp",EDGE,"E2.sketch_text.stroke-82"),sQuery(id+"F2.wireOp",EDGE,"E2.sketch_text.stroke-83"),sQuery(id+"F2.wireOp",EDGE,"E2.sketch_text.stroke-84"),sQuery(id+"F2.wireOp",EDGE,"E2.sketch_text.stroke-85"),sQuery(id+"F2.wireOp",EDGE,"E2.sketch_text.stroke-86"),sQuery(id+"F2.wireOp",EDGE,"E2.sketch_text.stroke-87"),sQuery(id+"F2.wireOp",EDGE,"E2.sketch_text.stroke-88"),sQuery(id+"F2.wireOp",EDGE,"E2.sketch_text.stroke-89"),sQuery(id+"F2.wireOp",EDGE,"E2.sketch_text.stroke-90"),sQuery(id+"F2.wireOp",EDGE,"E2.sketch_text.stroke-91"),sQuery(id+"F2.wireOp",EDGE,"E2.sketch_text.stroke-92"),sQuery(id+"F2.wireOp",EDGE,"E2.sketch_text.stroke-93"),sQuery(id+"F2.wireOp",EDGE,"E2.sketch_text.stroke-94"),sQuery(id+"F2.wireOp",EDGE,"E2.sketch_text.stroke-95"),sQuery(id+"F2.wireOp",EDGE,"E2.sketch_text.stroke-96"),sQuery(id+"F2.wireOp",EDGE,"E2.sketch_text.stroke-97"),sQuery(id+"F2.wireOp",EDGE,"E2.sketch_text.stroke-98"),sQuery(id+"F2.wireOp",EDGE,"E2.sketch_text.stroke-99"),sQuery(id+"F2.wireOp",EDGE,"E2.sketch_text.stroke-100"),sQuery(id+"F2.wireOp",EDGE,"E2.sketch_text.stroke-101"),sQuery(id+"F2.wireOp",EDGE,"E2.sketch_text.stroke-102"),sQuery(id+"F2.wireOp",EDGE,"E2.sketch_text.stroke-103"),sQuery(id+"F2.wireOp",EDGE,"E2.sketch_text.stroke-104"),sQuery(id+"F2.wireOp",EDGE,"E2.sketch_text.stroke-105"),sQuery(id+"F2.wireOp",EDGE,"E2.sketch_text.stroke-106"),sQuery(id+"F2.wireOp",EDGE,"E2.sketch_text.stroke-107"),sQuery(id+"F2.wireOp",EDGE,"E2.sketch_text.stroke-108"),sQuery(id+"F2.wireOp",EDGE,"E2.sketch_text.stroke-109"),sQuery(id+"F2.wireOp",EDGE,"E2.sketch_text.stroke-110"),sQuery(id+"F2.wireOp",EDGE,"E2.sketch_text.stroke-111"),sQuery(id+"F2.wireOp",EDGE,"E2.sketch_text.stroke-112"),sQuery(id+"F2.wireOp",EDGE,"E2.sketch_text.stroke-113"),sQuery(id+"F2.wireOp",EDGE,"E2.sketch_text.stroke-114"),sQuery(id+"F2.wireOp",EDGE,"E2.sketch_text.stroke-115"),sQuery(id+"F2.wireOp",EDGE,"E2.sketch_text.stroke-116"),sQuery(id+"F2.wireOp",EDGE,"E2.sketch_text.stroke-117"),sQuery(id+"F2.wireOp",EDGE,"E2.sketch_text.stroke-118"),sQuery(id+"F2.wireOp",EDGE,"E2.sketch_text.stroke-119"),sQuery(id+"F2.wireOp",EDGE,"E2.sketch_text.stroke-120"),sQuery(id+"F2.wireOp",EDGE,"E2.sketch_text.stroke-121"),sQuery(id+"F2.wireOp",EDGE,"E2.sketch_text.stroke-122"),sQuery(id+"F2.wireOp",EDGE,"E2.sketch_text.stroke-123"),sQuery(id+"F2.wireOp",EDGE,"E2.sketch_text.stroke-124"),sQuery(id+"F2.wireOp",EDGE,"E2.sketch_text.stroke-125"),sQuery(id+"F2.wireOp",EDGE,"E2.sketch_text.stroke-126"),sQuery(id+"F2.wireOp",EDGE,"E2.sketch_text.stroke-127"),sQuery(id+"F2.wireOp",EDGE,"E2.sketch_text.stroke-128"),sQuery(id+"F2.wireOp",EDGE,"E2.sketch_text.stroke-129"),sQuery(id+"F2.wireOp",EDGE,"E2.sketch_text.stroke-130"),sQuery(id+"F2.wireOp",EDGE,"E2.sketch_text.stroke-131"),sQuery(id+"F2.wireOp",EDGE,"E2.sketch_text.stroke-132"),sQuery(id+"F2.wireOp",EDGE,"E2.sketch_text.stroke-133"),sQuery(id+"F2.wireOp",EDGE,"E2.sketch_text.stroke-134"),sQuery(id+"F2.wireOp",EDGE,"E2.sketch_text.stroke-135"),sQuery(id+"F2.wireOp",EDGE,"E2.sketch_text.stroke-136"),sQuery(id+"F2.wireOp",EDGE,"E2.sketch_text.stroke-137"),sQuery(id+"F2.wireOp",EDGE,"E2.sketch_text.stroke-138"),sQuery(id+"F2.wireOp",EDGE,"E2.sketch_text.stroke-139"),sQuery(id+"F2.wireOp",EDGE,"E2.sketch_text.stroke-140"),sQuery(id+"F2.wireOp",EDGE,"E2.sketch_text.stroke-141"),sQuery(id+"F2.wireOp",EDGE,"E2.sketch_text.stroke-142"),sQuery(id+"F2.wireOp",EDGE,"E2.sketch_text.stroke-143"),sQuery(id+"F2.wireOp",EDGE,"E2.sketch_text.stroke-144"),sQuery(id+"F2.wireOp",EDGE,"E2.sketch_text.stroke-145"),sQuery(id+"F2.wireOp",EDGE,"E2.sketch_text.stroke-146"),sQuery(id+"F2.wireOp",EDGE,"E2.sketch_text.stroke-147"),sQuery(id+"F2.wireOp",EDGE,"E2.sketch_text.stroke-148"),sQuery(id+"F2.wireOp",EDGE,"E2.sketch_text.stroke-149"),sQuery(id+"F2.wireOp",EDGE,"E2.sketch_text.stroke-150"),sQuery(id+"F2.wireOp",EDGE,"E2.sketch_text.stroke-151"),sQuery(id+"F2.wireOp",EDGE,"E2.sketch_text.stroke-152"),sQuery(id+"F2.wireOp",EDGE,"E2.sketch_text.stroke-153"),sQuery(id+"F2.wireOp",EDGE,"E2.sketch_text.stroke-154"),sQuery(id+"F2.wireOp",EDGE,"E2.sketch_text.stroke-155"),sQuery(id+"F2.wireOp",EDGE,"E2.sketch_text.stroke-156"),sQuery(id+"F2.wireOp",EDGE,"E2.sketch_text.stroke-157"),sQuery(id+"F2.wireOp",EDGE,"E2.sketch_text.stroke-158"),sQuery(id+"F2.wireOp",EDGE,"E2.sketch_text.stroke-159"),sQuery(id+"F2.wireOp",EDGE,"E2.sketch_text.stroke-160"),sQuery(id+"F2.wireOp",EDGE,"E2.sketch_text.stroke-161"),sQuery(id+"F2.wireOp",EDGE,"E2.sketch_text.stroke-162"),sQuery(id+"F2.wireOp",EDGE,"E2.sketch_text.stroke-163"),sQuery(id+"F2.wireOp",EDGE,"E2.sketch_text.stroke-164"),sQuery(id+"F2.wireOp",EDGE,"E2.sketch_text.stroke-165"),sQuery(id+"F2.wireOp",EDGE,"E2.sketch_text.stroke-166"),sQuery(id+"F2.wireOp",EDGE,"E2.sketch_text.stroke-167"),sQuery(id+"F2.wireOp",EDGE,"E2.sketch_text.stroke-168"),sQuery(id+"F2.wireOp",EDGE,"E2.sketch_text.stroke-169"),sQuery(id+"F2.wireOp",EDGE,"E2.sketch_text.stroke-170"),sQuery(id+"F2.wireOp",EDGE,"E2.sketch_text.stroke-171"),sQuery(id+"F2.wireOp",EDGE,"E2.sketch_text.stroke-172"),sQuery(id+"F2.wireOp",EDGE,"E2.sketch_text.stroke-173"),sQuery(id+"F3.wireOp",EDGE,"E4.sketch_text.stroke-0"),sQuery(id+"F3.wireOp",EDGE,"E4.sketch_text.stroke-1"),sQuery(id+"F3.wireOp",EDGE,"E4.sketch_text.stroke-2"),sQuery(id+"F3.wireOp",EDGE,"E4.sketch_text.stroke-3"),sQuery(id+"F3.wireOp",EDGE,"E4.sketch_text.stroke-4"),sQuery(id+"F3.wireOp",EDGE,"E4.sketch_text.stroke-5"),sQuery(id+"F3.wireOp",EDGE,"E4.sketch_text.stroke-6"),sQuery(id+"F3.wireOp",EDGE,"E4.sketch_text.stroke-7"),sQuery(id+"F3.wireOp",EDGE,"E4.sketch_text.stroke-8"),sQuery(id+"F3.wireOp",EDGE,"E4.sketch_text.stroke-9"),sQuery(id+"F3.wireOp",EDGE,"E4.sketch_text.stroke-10"),sQuery(id+"F3.wireOp",EDGE,"E4.sketch_text.stroke-11"),sQuery(id+"F3.wireOp",EDGE,"E4.sketch_text.stroke-12"),sQuery(id+"F3.wireOp",EDGE,"E4.sketch_text.stroke-13"),sQuery(id+"F3.wireOp",EDGE,"E4.sketch_text.stroke-14"),sQuery(id+"F3.wireOp",EDGE,"E4.sketch_text.stroke-15"),sQuery(id+"F3.wireOp",EDGE,"E4.sketch_text.stroke-16"),sQuery(id+"F3.wireOp",EDGE,"E4.sketch_text.stroke-17"),sQuery(id+"F3.wireOp",EDGE,"E4.sketch_text.stroke-18"),sQuery(id+"F3.wireOp",EDGE,"E4.sketch_text.stroke-19"),sQuery(id+"F3.wireOp",EDGE,"E4.sketch_text.stroke-20"),sQuery(id+"F3.wireOp",EDGE,"E4.sketch_text.stroke-21"),sQuery(id+"F3.wireOp",EDGE,"E4.sketch_text.stroke-22"),sQuery(id+"F3.wireOp",EDGE,"E4.sketch_text.stroke-23"),sQuery(id+"F3.wireOp",EDGE,"E4.sketch_text.stroke-24"),sQuery(id+"F3.wireOp",EDGE,"E4.sketch_text.stroke-25"),sQuery(id+"F3.wireOp",EDGE,"E4.sketch_text.stroke-26"),sQuery(id+"F3.wireOp",EDGE,"E4.sketch_text.stroke-27"),sQuery(id+"F3.wireOp",EDGE,"E4.sketch_text.stroke-28"),sQuery(id+"F3.wireOp",EDGE,"E4.sketch_text.stroke-29"),sQuery(id+"F3.wireOp",EDGE,"E4.sketch_text.stroke-30"),sQuery(id+"F3.wireOp",EDGE,"E4.sketch_text.stroke-31"),sQuery(id+"F3.wireOp",EDGE,"E4.sketch_text.stroke-32"),sQuery(id+"F3.wireOp",EDGE,"E4.sketch_text.stroke-33"),sQuery(id+"F3.wireOp",EDGE,"E4.sketch_text.stroke-34"),sQuery(id+"F3.wireOp",EDGE,"E4.sketch_text.stroke-35"),sQuery(id+"F3.wireOp",EDGE,"E4.sketch_text.stroke-36"),sQuery(id+"F3.wireOp",EDGE,"E4.sketch_text.stroke-37"),sQuery(id+"F3.wireOp",EDGE,"E4.sketch_text.stroke-38"),sQuery(id+"F3.wireOp",EDGE,"E4.sketch_text.stroke-39"),sQuery(id+"F3.wireOp",EDGE,"E4.sketch_text.stroke-40"),sQuery(id+"F3.wireOp",EDGE,"E4.sketch_text.stroke-41"),sQuery(id+"F3.wireOp",EDGE,"E4.sketch_text.stroke-42"),sQuery(id+"F3.wireOp",EDGE,"E4.sketch_text.stroke-43"),sQuery(id+"F3.wireOp",EDGE,"E4.sketch_text.stroke-44"),sQuery(id+"F3.wireOp",EDGE,"E4.sketch_text.stroke-45"),sQuery(id+"F3.wireOp",EDGE,"E4.sketch_text.stroke-46"),sQuery(id+"F3.wireOp",EDGE,"E4.sketch_text.stroke-47"),sQuery(id+"F3.wireOp",EDGE,"E4.sketch_text.stroke-48"),sQuery(id+"F3.wireOp",EDGE,"E4.sketch_text.stroke-49"),sQuery(id+"F3.wireOp",EDGE,"E4.sketch_text.stroke-50"),sQuery(id+"F3.wireOp",EDGE,"E4.sketch_text.stroke-51"),sQuery(id+"F3.wireOp",EDGE,"E4.sketch_text.stroke-52"),sQuery(id+"F3.wireOp",EDGE,"E4.sketch_text.stroke-53"),sQuery(id+"F3.wireOp",EDGE,"E4.sketch_text.stroke-54"),sQuery(id+"F3.wireOp",EDGE,"E4.sketch_text.stroke-55"),sQuery(id+"F3.wireOp",EDGE,"E4.sketch_text.stroke-56"),sQuery(id+"F3.wireOp",EDGE,"E4.sketch_text.stroke-57"),sQuery(id+"F3.wireOp",EDGE,"E4.sketch_text.stroke-58"),sQuery(id+"F3.wireOp",EDGE,"E4.sketch_text.stroke-59"),sQuery(id+"F3.wireOp",EDGE,"E4.sketch_text.stroke-60"),sQuery(id+"F3.wireOp",EDGE,"E4.sketch_text.stroke-61"),sQuery(id+"F3.wireOp",EDGE,"E4.sketch_text.stroke-62"),sQuery(id+"F3.wireOp",EDGE,"E4.sketch_text.stroke-71"),sQuery(id+"F3.wireOp",EDGE,"E4.sketch_text.stroke-72"),sQuery(id+"F3.wireOp",EDGE,"E4.sketch_text.stroke-73"),sQuery(id+"F3.wireOp",EDGE,"E4.sketch_text.stroke-74"),sQuery(id+"F3.wireOp",EDGE,"E4.sketch_text.stroke-75"),sQuery(id+"F3.wireOp",EDGE,"E4.sketch_text.stroke-76"),sQuery(id+"F3.wireOp",EDGE,"E4.sketch_text.stroke-77"),sQuery(id+"F3.wireOp",EDGE,"E4.sketch_text.stroke-78"),sQuery(id+"F3.wireOp",EDGE,"E4.sketch_text.stroke-79"),sQuery(id+"F3.wireOp",EDGE,"E4.sketch_text.stroke-80"),sQuery(id+"F3.wireOp",EDGE,"E4.sketch_text.stroke-81"),sQuery(id+"F3.wireOp",EDGE,"E4.sketch_text.stroke-82"),sQuery(id+"F3.wireOp",EDGE,"E4.sketch_text.stroke-83"),sQuery(id+"F3.wireOp",EDGE,"E4.sketch_text.stroke-84"),sQuery(id+"F3.wireOp",EDGE,"E4.sketch_text.stroke-85"),sQuery(id+"F3.wireOp",EDGE,"E4.sketch_text.stroke-86"),sQuery(id+"F3.wireOp",EDGE,"E4.sketch_text.stroke-87"),sQuery(id+"F3.wireOp",EDGE,"E4.sketch_text.stroke-88"),sQuery(id+"F3.wireOp",EDGE,"E4.sketch_text.stroke-89"),sQuery(id+"F3.wireOp",EDGE,"E4.sketch_text.stroke-90"),sQuery(id+"F3.wireOp",EDGE,"E4.sketch_text.stroke-91"),sQuery(id+"F3.wireOp",EDGE,"E4.sketch_text.stroke-92"),sQuery(id+"F3.wireOp",EDGE,"E4.sketch_text.stroke-93"),sQuery(id+"F3.wireOp",EDGE,"E4.sketch_text.stroke-94"),sQuery(id+"F3.wireOp",EDGE,"E4.sketch_text.stroke-95"),sQuery(id+"F3.wireOp",EDGE,"E4.sketch_text.stroke-96"),sQuery(id+"F3.wireOp",EDGE,"E4.sketch_text.stroke-97"),sQuery(id+"F3.wireOp",EDGE,"E4.sketch_text.stroke-103"),sQuery(id+"F3.wireOp",EDGE,"E4.sketch_text.stroke-104"),sQuery(id+"F3.wireOp",EDGE,"E4.sketch_text.stroke-105"),sQuery(id+"F3.wireOp",EDGE,"E4.sketch_text.stroke-106"),sQuery(id+"F3.wireOp",EDGE,"E4.sketch_text.stroke-107"),sQuery(id+"F3.wireOp",EDGE,"E4.sketch_text.stroke-108"),sQuery(id+"F3.wireOp",EDGE,"E4.sketch_text.stroke-109"),sQuery(id+"F3.wireOp",EDGE,"E4.sketch_text.stroke-110"),sQuery(id+"F3.wireOp",EDGE,"E4.sketch_text.stroke-111"),sQuery(id+"F3.wireOp",EDGE,"E4.sketch_text.stroke-112"),sQuery(id+"F3.wireOp",EDGE,"E4.sketch_text.stroke-113"),sQuery(id+"F3.wireOp",EDGE,"E4.sketch_text.stroke-114"),sQuery(id+"F3.wireOp",EDGE,"E4.sketch_text.stroke-115"),sQuery(id+"F3.wireOp",EDGE,"E4.sketch_text.stroke-116"),sQuery(id+"F3.wireOp",EDGE,"E4.sketch_text.stroke-117"),sQuery(id+"F3.wireOp",EDGE,"E4.sketch_text.stroke-118"),sQuery(id+"F3.wireOp",EDGE,"E4.sketch_text.stroke-119"),sQuery(id+"F3.wireOp",EDGE,"E4.sketch_text.stroke-120"),sQuery(id+"F3.wireOp",EDGE,"E4.sketch_text.stroke-121"),sQuery(id+"F3.wireOp",EDGE,"E4.sketch_text.stroke-122"),sQuery(id+"F3.wireOp",EDGE,"E4.sketch_text.stroke-123"),sQuery(id+"F3.wireOp",EDGE,"E4.sketch_text.stroke-124"),sQuery(id+"F3.wireOp",EDGE,"E4.sketch_text.stroke-125"),sQuery(id+"F3.wireOp",EDGE,"E4.sketch_text.stroke-126"),sQuery(id+"F3.wireOp",EDGE,"E4.sketch_text.stroke-127"),sQuery(id+"F3.wireOp",EDGE,"E4.sketch_text.stroke-128"),sQuery(id+"F3.wireOp",EDGE,"E4.sketch_text.stroke-129"),sQuery(id+"F3.wireOp",EDGE,"E4.sketch_text.stroke-130"),sQuery(id+"F3.wireOp",EDGE,"E4.sketch_text.stroke-131"),sQuery(id+"F3.wireOp",EDGE,"E4.sketch_text.stroke-132"),sQuery(id+"F3.wireOp",EDGE,"E4.sketch_text.stroke-133"),sQuery(id+"F3.wireOp",EDGE,"E4.sketch_text.stroke-134"),sQuery(id+"F3.wireOp",EDGE,"E4.sketch_text.stroke-135"),sQuery(id+"F3.wireOp",EDGE,"E4.sketch_text.stroke-136"),sQuery(id+"F3.wireOp",EDGE,"E4.sketch_text.stroke-137"),sQuery(id+"F3.wireOp",EDGE,"E4.sketch_text.stroke-138"),sQuery(id+"F3.wireOp",EDGE,"E4.sketch_text.stroke-139"),sQuery(id+"F3.wireOp",EDGE,"E4.sketch_text.stroke-140"),sQuery(id+"F3.wireOp",EDGE,"E4.sketch_text.stroke-141"),sQuery(id+"F3.wireOp",EDGE,"E4.sketch_text.stroke-142"),sQuery(id+"F3.wireOp",EDGE,"E4.sketch_text.stroke-143"),sQuery(id+"F3.wireOp",EDGE,"E4.sketch_text.stroke-144"),sQuery(id+"F3.wireOp",EDGE,"E4.sketch_text.stroke-145"),sQuery(id+"F3.wireOp",EDGE,"E4.sketch_text.stroke-146"),sQuery(id+"F3.wireOp",EDGE,"E4.sketch_text.stroke-147"),sQuery(id+"F3.wireOp",EDGE,"E4.sketch_text.stroke-148"),sQuery(id+"F3.wireOp",EDGE,"E4.sketch_text.stroke-149"),sQuery(id+"F3.wireOp",EDGE,"E4.sketch_text.stroke-150"),sQuery(id+"F3.wireOp",EDGE,"E4.sketch_text.stroke-151"),sQuery(id+"F3.wireOp",EDGE,"E4.sketch_text.stroke-152"),sQuery(id+"F3.wireOp",EDGE,"E4.sketch_text.stroke-153"),sQuery(id+"F3.wireOp",EDGE,"E4.sketch_text.stroke-159"),sQuery(id+"F3.wireOp",EDGE,"E4.sketch_text.stroke-160"),sQuery(id+"F3.wireOp",EDGE,"E4.sketch_text.stroke-161"),sQuery(id+"F3.wireOp",EDGE,"E4.sketch_text.stroke-162"),sQuery(id+"F3.wireOp",EDGE,"E4.sketch_text.stroke-163"),sQuery(id+"F3.wireOp",EDGE,"E4.sketch_text.stroke-164"),sQuery(id+"F3.wireOp",EDGE,"E4.sketch_text.stroke-165"),sQuery(id+"F3.wireOp",EDGE,"E4.sketch_text.stroke-166"),sQuery(id+"F3.wireOp",EDGE,"E4.sketch_text.stroke-167"),sQuery(id+"F3.wireOp",EDGE,"E4.sketch_text.stroke-168"),sQuery(id+"F3.wireOp",EDGE,"E4.sketch_text.stroke-169"),sQuery(id+"F3.wireOp",EDGE,"E4.sketch_text.stroke-170"),sQuery(id+"F3.wireOp",EDGE,"E4.sketch_text.stroke-171"),sQuery(id+"F3.wireOp",EDGE,"E4.sketch_text.stroke-172"),sQuery(id+"F3.wireOp",EDGE,"E4.sketch_text.stroke-173"),sQuery(id+"F3.wireOp",EDGE,"E4.sketch_text.stroke-174"),sQuery(id+"F3.wireOp",EDGE,"E4.sketch_text.stroke-175"),sQuery(id+"F3.wireOp",EDGE,"E4.sketch_text.stroke-176"),sQuery(id+"F3.wireOp",EDGE,"E4.sketch_text.stroke-177"),sQuery(id+"F3.wireOp",EDGE,"E4.sketch_text.stroke-178"),sQuery(id+"F3.wireOp",EDGE,"E4.sketch_text.stroke-179"),sQuery(id+"F3.wireOp",EDGE,"E4.sketch_text.stroke-180"),subQ2,sQuery(id+"F4.wireOp",EDGE,"E31")])],"isStart":true})]),OD(1.0)],"derivedFrom":makeQuery(id+"F1.opExtrude","CAP_EDGE",EDGE,{"disambiguationData":[OSD([subQ0])],"isStart":false})});}
            var Q25;
            {var subQ0=sQuery(id+"F0.wireOp",EDGE,"E0.top");var subQ1=sQuery(id+"F0.wireOp",EDGE,"E0.bottom");var subQ2=sQuery(id+"F4.wireOp",EDGE,"E30");Q25=makeQuery(id+"F5.boolean.opBoolean","SPLIT",EDGE,{"disambiguationData":[TD([makeQuery(id+"F1.opExtrude","CAP_FACE",FACE,{"disambiguationData":[OSD([subQ1,subQ0,sQuery(id+"F0.wireOp",EDGE,"E0.left"),sQuery(id+"F0.wireOp",EDGE,"E0.right")])],"isStart":false}),makeQuery(id+"F1.opExtrude","SWEPT_FACE",FACE,{"disambiguationData":[OSD([subQ0])]}),makeQuery(id+"F5.opExtrude","SWEPT_FACE",FACE,{"disambiguationData":[OSD([subQ2])]}),makeQuery(id+"F5.opExtrude","CAP_FACE",FACE,{"disambiguationData":[OSD([subQ1,sQuery(id+"F2.wireOp",EDGE,"E2.sketch_text.stroke-0"),sQuery(id+"F2.wireOp",EDGE,"E2.sketch_text.stroke-1"),sQuery(id+"F2.wireOp",EDGE,"E2.sketch_text.stroke-2"),sQuery(id+"F2.wireOp",EDGE,"E2.sketch_text.stroke-3"),sQuery(id+"F2.wireOp",EDGE,"E2.sketch_text.stroke-4"),sQuery(id+"F2.wireOp",EDGE,"E2.sketch_text.stroke-5"),sQuery(id+"F2.wireOp",EDGE,"E2.sketch_text.stroke-6"),sQuery(id+"F2.wireOp",EDGE,"E2.sketch_text.stroke-7"),sQuery(id+"F2.wireOp",EDGE,"E2.sketch_text.stroke-8"),sQuery(id+"F2.wireOp",EDGE,"E2.sketch_text.stroke-9"),sQuery(id+"F2.wireOp",EDGE,"E2.sketch_text.stroke-10"),sQuery(id+"F2.wireOp",EDGE,"E2.sketch_text.stroke-11"),sQuery(id+"F2.wireOp",EDGE,"E2.sketch_text.stroke-12"),sQuery(id+"F2.wireOp",EDGE,"E2.sketch_text.stroke-13"),sQuery(id+"F2.wireOp",EDGE,"E2.sketch_text.stroke-14"),sQuery(id+"F2.wireOp",EDGE,"E2.sketch_text.stroke-15"),sQuery(id+"F2.wireOp",EDGE,"E2.sketch_text.stroke-16"),sQuery(id+"F2.wireOp",EDGE,"E2.sketch_text.stroke-17"),sQuery(id+"F2.wireOp",EDGE,"E2.sketch_text.stroke-18"),sQuery(id+"F2.wireOp",EDGE,"E2.sketch_text.stroke-19"),sQuery(id+"F2.wireOp",EDGE,"E2.sketch_text.stroke-20"),sQuery(id+"F2.wireOp",EDGE,"E2.sketch_text.stroke-21"),sQuery(id+"F2.wireOp",EDGE,"E2.sketch_text.stroke-22"),sQuery(id+"F2.wireOp",EDGE,"E2.sketch_text.stroke-23"),sQuery(id+"F2.wireOp",EDGE,"E2.sketch_text.stroke-24"),sQuery(id+"F2.wireOp",EDGE,"E2.sketch_text.stroke-25"),sQuery(id+"F2.wireOp",EDGE,"E2.sketch_text.stroke-26"),sQuery(id+"F2.wireOp",EDGE,"E2.sketch_text.stroke-27"),sQuery(id+"F2.wireOp",EDGE,"E2.sketch_text.stroke-28"),sQuery(id+"F2.wireOp",EDGE,"E2.sketch_text.stroke-29"),sQuery(id+"F2.wireOp",EDGE,"E2.sketch_text.stroke-30"),sQuery(id+"F2.wireOp",EDGE,"E2.sketch_text.stroke-31"),sQuery(id+"F2.wireOp",EDGE,"E2.sketch_text.stroke-32"),sQuery(id+"F2.wireOp",EDGE,"E2.sketch_text.stroke-33"),sQuery(id+"F2.wireOp",EDGE,"E2.sketch_text.stroke-34"),sQuery(id+"F2.wireOp",EDGE,"E2.sketch_text.stroke-35"),sQuery(id+"F2.wireOp",EDGE,"E2.sketch_text.stroke-36"),sQuery(id+"F2.wireOp",EDGE,"E2.sketch_text.stroke-37"),sQuery(id+"F2.wireOp",EDGE,"E2.sketch_text.stroke-38"),sQuery(id+"F2.wireOp",EDGE,"E2.sketch_text.stroke-39"),sQuery(id+"F2.wireOp",EDGE,"E2.sketch_text.stroke-40"),sQuery(id+"F2.wireOp",EDGE,"E2.sketch_text.stroke-41"),sQuery(id+"F2.wireOp",EDGE,"E2.sketch_text.stroke-42"),sQuery(id+"F2.wireOp",EDGE,"E2.sketch_text.stroke-43"),sQuery(id+"F2.wireOp",EDGE,"E2.sketch_text.stroke-44"),sQuery(id+"F2.wireOp",EDGE,"E2.sketch_text.stroke-45"),sQuery(id+"F2.wireOp",EDGE,"E2.sketch_text.stroke-46"),sQuery(id+"F2.wireOp",EDGE,"E2.sketch_text.stroke-47"),sQuery(id+"F2.wireOp",EDGE,"E2.sketch_text.stroke-48"),sQuery(id+"F2.wireOp",EDGE,"E2.sketch_text.stroke-49"),sQuery(id+"F2.wireOp",EDGE,"E2.sketch_text.stroke-50"),sQuery(id+"F2.wireOp",EDGE,"E2.sketch_text.stroke-51"),sQuery(id+"F2.wireOp",EDGE,"E2.sketch_text.stroke-52"),sQuery(id+"F2.wireOp",EDGE,"E2.sketch_text.stroke-53"),sQuery(id+"F2.wireOp",EDGE,"E2.sketch_text.stroke-54"),sQuery(id+"F2.wireOp",EDGE,"E2.sketch_text.stroke-55"),sQuery(id+"F2.wireOp",EDGE,"E2.sketch_text.stroke-56"),sQuery(id+"F2.wireOp",EDGE,"E2.sketch_text.stroke-57"),sQuery(id+"F2.wireOp",EDGE,"E2.sketch_text.stroke-58"),sQuery(id+"F2.wireOp",EDGE,"E2.sketch_text.stroke-59"),sQuery(id+"F2.wireOp",EDGE,"E2.sketch_text.stroke-60"),sQuery(id+"F2.wireOp",EDGE,"E2.sketch_text.stroke-61"),sQuery(id+"F2.wireOp",EDGE,"E2.sketch_text.stroke-62"),sQuery(id+"F2.wireOp",EDGE,"E2.sketch_text.stroke-63"),sQuery(id+"F2.wireOp",EDGE,"E2.sketch_text.stroke-64"),sQuery(id+"F2.wireOp",EDGE,"E2.sketch_text.stroke-65"),sQuery(id+"F2.wireOp",EDGE,"E2.sketch_text.stroke-66"),sQuery(id+"F2.wireOp",EDGE,"E2.sketch_text.stroke-67"),sQuery(id+"F2.wireOp",EDGE,"E2.sketch_text.stroke-68"),sQuery(id+"F2.wireOp",EDGE,"E2.sketch_text.stroke-69"),sQuery(id+"F2.wireOp",EDGE,"E2.sketch_text.stroke-70"),sQuery(id+"F2.wireOp",EDGE,"E2.sketch_text.stroke-71"),sQuery(id+"F2.wireOp",EDGE,"E2.sketch_text.stroke-72"),sQuery(id+"F2.wireOp",EDGE,"E2.sketch_text.stroke-73"),sQuery(id+"F2.wireOp",EDGE,"E2.sketch_text.stroke-74"),sQuery(id+"F2.wireOp",EDGE,"E2.sketch_text.stroke-75"),sQuery(id+"F2.wireOp",EDGE,"E2.sketch_text.stroke-76"),sQuery(id+"F2.wireOp",EDGE,"E2.sketch_text.stroke-77"),sQuery(id+"F2.wireOp",EDGE,"E2.sketch_text.stroke-78"),sQuery(id+"F2.wireOp",EDGE,"E2.sketch_text.stroke-79"),sQuery(id+"F2.wireOp",EDGE,"E2.sketch_text.stroke-80"),sQuery(id+"F2.wireOp",EDGE,"E2.sketch_text.stroke-81"),sQuery(id+"F2.wireOp",EDGE,"E2.sketch_text.stroke-82"),sQuery(id+"F2.wireOp",EDGE,"E2.sketch_text.stroke-83"),sQuery(id+"F2.wireOp",EDGE,"E2.sketch_text.stroke-84"),sQuery(id+"F2.wireOp",EDGE,"E2.sketch_text.stroke-85"),sQuery(id+"F2.wireOp",EDGE,"E2.sketch_text.stroke-86"),sQuery(id+"F2.wireOp",EDGE,"E2.sketch_text.stroke-87"),sQuery(id+"F2.wireOp",EDGE,"E2.sketch_text.stroke-88"),sQuery(id+"F2.wireOp",EDGE,"E2.sketch_text.stroke-89"),sQuery(id+"F2.wireOp",EDGE,"E2.sketch_text.stroke-90"),sQuery(id+"F2.wireOp",EDGE,"E2.sketch_text.stroke-91"),sQuery(id+"F2.wireOp",EDGE,"E2.sketch_text.stroke-92"),sQuery(id+"F2.wireOp",EDGE,"E2.sketch_text.stroke-93"),sQuery(id+"F2.wireOp",EDGE,"E2.sketch_text.stroke-94"),sQuery(id+"F2.wireOp",EDGE,"E2.sketch_text.stroke-95"),sQuery(id+"F2.wireOp",EDGE,"E2.sketch_text.stroke-96"),sQuery(id+"F2.wireOp",EDGE,"E2.sketch_text.stroke-97"),sQuery(id+"F2.wireOp",EDGE,"E2.sketch_text.stroke-98"),sQuery(id+"F2.wireOp",EDGE,"E2.sketch_text.stroke-99"),sQuery(id+"F2.wireOp",EDGE,"E2.sketch_text.stroke-100"),sQuery(id+"F2.wireOp",EDGE,"E2.sketch_text.stroke-101"),sQuery(id+"F2.wireOp",EDGE,"E2.sketch_text.stroke-102"),sQuery(id+"F2.wireOp",EDGE,"E2.sketch_text.stroke-103"),sQuery(id+"F2.wireOp",EDGE,"E2.sketch_text.stroke-104"),sQuery(id+"F2.wireOp",EDGE,"E2.sketch_text.stroke-105"),sQuery(id+"F2.wireOp",EDGE,"E2.sketch_text.stroke-106"),sQuery(id+"F2.wireOp",EDGE,"E2.sketch_text.stroke-107"),sQuery(id+"F2.wireOp",EDGE,"E2.sketch_text.stroke-108"),sQuery(id+"F2.wireOp",EDGE,"E2.sketch_text.stroke-109"),sQuery(id+"F2.wireOp",EDGE,"E2.sketch_text.stroke-110"),sQuery(id+"F2.wireOp",EDGE,"E2.sketch_text.stroke-111"),sQuery(id+"F2.wireOp",EDGE,"E2.sketch_text.stroke-112"),sQuery(id+"F2.wireOp",EDGE,"E2.sketch_text.stroke-113"),sQuery(id+"F2.wireOp",EDGE,"E2.sketch_text.stroke-114"),sQuery(id+"F2.wireOp",EDGE,"E2.sketch_text.stroke-115"),sQuery(id+"F2.wireOp",EDGE,"E2.sketch_text.stroke-116"),sQuery(id+"F2.wireOp",EDGE,"E2.sketch_text.stroke-117"),sQuery(id+"F2.wireOp",EDGE,"E2.sketch_text.stroke-118"),sQuery(id+"F2.wireOp",EDGE,"E2.sketch_text.stroke-119"),sQuery(id+"F2.wireOp",EDGE,"E2.sketch_text.stroke-120"),sQuery(id+"F2.wireOp",EDGE,"E2.sketch_text.stroke-121"),sQuery(id+"F2.wireOp",EDGE,"E2.sketch_text.stroke-122"),sQuery(id+"F2.wireOp",EDGE,"E2.sketch_text.stroke-123"),sQuery(id+"F2.wireOp",EDGE,"E2.sketch_text.stroke-124"),sQuery(id+"F2.wireOp",EDGE,"E2.sketch_text.stroke-125"),sQuery(id+"F2.wireOp",EDGE,"E2.sketch_text.stroke-126"),sQuery(id+"F2.wireOp",EDGE,"E2.sketch_text.stroke-127"),sQuery(id+"F2.wireOp",EDGE,"E2.sketch_text.stroke-128"),sQuery(id+"F2.wireOp",EDGE,"E2.sketch_text.stroke-129"),sQuery(id+"F2.wireOp",EDGE,"E2.sketch_text.stroke-130"),sQuery(id+"F2.wireOp",EDGE,"E2.sketch_text.stroke-131"),sQuery(id+"F2.wireOp",EDGE,"E2.sketch_text.stroke-132"),sQuery(id+"F2.wireOp",EDGE,"E2.sketch_text.stroke-133"),sQuery(id+"F2.wireOp",EDGE,"E2.sketch_text.stroke-134"),sQuery(id+"F2.wireOp",EDGE,"E2.sketch_text.stroke-135"),sQuery(id+"F2.wireOp",EDGE,"E2.sketch_text.stroke-136"),sQuery(id+"F2.wireOp",EDGE,"E2.sketch_text.stroke-137"),sQuery(id+"F2.wireOp",EDGE,"E2.sketch_text.stroke-138"),sQuery(id+"F2.wireOp",EDGE,"E2.sketch_text.stroke-139"),sQuery(id+"F2.wireOp",EDGE,"E2.sketch_text.stroke-140"),sQuery(id+"F2.wireOp",EDGE,"E2.sketch_text.stroke-141"),sQuery(id+"F2.wireOp",EDGE,"E2.sketch_text.stroke-142"),sQuery(id+"F2.wireOp",EDGE,"E2.sketch_text.stroke-143"),sQuery(id+"F2.wireOp",EDGE,"E2.sketch_text.stroke-144"),sQuery(id+"F2.wireOp",EDGE,"E2.sketch_text.stroke-145"),sQuery(id+"F2.wireOp",EDGE,"E2.sketch_text.stroke-146"),sQuery(id+"F2.wireOp",EDGE,"E2.sketch_text.stroke-147"),sQuery(id+"F2.wireOp",EDGE,"E2.sketch_text.stroke-148"),sQuery(id+"F2.wireOp",EDGE,"E2.sketch_text.stroke-149"),sQuery(id+"F2.wireOp",EDGE,"E2.sketch_text.stroke-150"),sQuery(id+"F2.wireOp",EDGE,"E2.sketch_text.stroke-151"),sQuery(id+"F2.wireOp",EDGE,"E2.sketch_text.stroke-152"),sQuery(id+"F2.wireOp",EDGE,"E2.sketch_text.stroke-153"),sQuery(id+"F2.wireOp",EDGE,"E2.sketch_text.stroke-154"),sQuery(id+"F2.wireOp",EDGE,"E2.sketch_text.stroke-155"),sQuery(id+"F2.wireOp",EDGE,"E2.sketch_text.stroke-156"),sQuery(id+"F2.wireOp",EDGE,"E2.sketch_text.stroke-157"),sQuery(id+"F2.wireOp",EDGE,"E2.sketch_text.stroke-158"),sQuery(id+"F2.wireOp",EDGE,"E2.sketch_text.stroke-159"),sQuery(id+"F2.wireOp",EDGE,"E2.sketch_text.stroke-160"),sQuery(id+"F2.wireOp",EDGE,"E2.sketch_text.stroke-161"),sQuery(id+"F2.wireOp",EDGE,"E2.sketch_text.stroke-162"),sQuery(id+"F2.wireOp",EDGE,"E2.sketch_text.stroke-163"),sQuery(id+"F2.wireOp",EDGE,"E2.sketch_text.stroke-164"),sQuery(id+"F2.wireOp",EDGE,"E2.sketch_text.stroke-165"),sQuery(id+"F2.wireOp",EDGE,"E2.sketch_text.stroke-166"),sQuery(id+"F2.wireOp",EDGE,"E2.sketch_text.stroke-167"),sQuery(id+"F2.wireOp",EDGE,"E2.sketch_text.stroke-168"),sQuery(id+"F2.wireOp",EDGE,"E2.sketch_text.stroke-169"),sQuery(id+"F2.wireOp",EDGE,"E2.sketch_text.stroke-170"),sQuery(id+"F2.wireOp",EDGE,"E2.sketch_text.stroke-171"),sQuery(id+"F2.wireOp",EDGE,"E2.sketch_text.stroke-172"),sQuery(id+"F2.wireOp",EDGE,"E2.sketch_text.stroke-173"),sQuery(id+"F3.wireOp",EDGE,"E4.sketch_text.stroke-0"),sQuery(id+"F3.wireOp",EDGE,"E4.sketch_text.stroke-1"),sQuery(id+"F3.wireOp",EDGE,"E4.sketch_text.stroke-2"),sQuery(id+"F3.wireOp",EDGE,"E4.sketch_text.stroke-3"),sQuery(id+"F3.wireOp",EDGE,"E4.sketch_text.stroke-4"),sQuery(id+"F3.wireOp",EDGE,"E4.sketch_text.stroke-5"),sQuery(id+"F3.wireOp",EDGE,"E4.sketch_text.stroke-6"),sQuery(id+"F3.wireOp",EDGE,"E4.sketch_text.stroke-7"),sQuery(id+"F3.wireOp",EDGE,"E4.sketch_text.stroke-8"),sQuery(id+"F3.wireOp",EDGE,"E4.sketch_text.stroke-9"),sQuery(id+"F3.wireOp",EDGE,"E4.sketch_text.stroke-10"),sQuery(id+"F3.wireOp",EDGE,"E4.sketch_text.stroke-11"),sQuery(id+"F3.wireOp",EDGE,"E4.sketch_text.stroke-12"),sQuery(id+"F3.wireOp",EDGE,"E4.sketch_text.stroke-13"),sQuery(id+"F3.wireOp",EDGE,"E4.sketch_text.stroke-14"),sQuery(id+"F3.wireOp",EDGE,"E4.sketch_text.stroke-15"),sQuery(id+"F3.wireOp",EDGE,"E4.sketch_text.stroke-16"),sQuery(id+"F3.wireOp",EDGE,"E4.sketch_text.stroke-17"),sQuery(id+"F3.wireOp",EDGE,"E4.sketch_text.stroke-18"),sQuery(id+"F3.wireOp",EDGE,"E4.sketch_text.stroke-19"),sQuery(id+"F3.wireOp",EDGE,"E4.sketch_text.stroke-20"),sQuery(id+"F3.wireOp",EDGE,"E4.sketch_text.stroke-21"),sQuery(id+"F3.wireOp",EDGE,"E4.sketch_text.stroke-22"),sQuery(id+"F3.wireOp",EDGE,"E4.sketch_text.stroke-23"),sQuery(id+"F3.wireOp",EDGE,"E4.sketch_text.stroke-24"),sQuery(id+"F3.wireOp",EDGE,"E4.sketch_text.stroke-25"),sQuery(id+"F3.wireOp",EDGE,"E4.sketch_text.stroke-26"),sQuery(id+"F3.wireOp",EDGE,"E4.sketch_text.stroke-27"),sQuery(id+"F3.wireOp",EDGE,"E4.sketch_text.stroke-28"),sQuery(id+"F3.wireOp",EDGE,"E4.sketch_text.stroke-29"),sQuery(id+"F3.wireOp",EDGE,"E4.sketch_text.stroke-30"),sQuery(id+"F3.wireOp",EDGE,"E4.sketch_text.stroke-31"),sQuery(id+"F3.wireOp",EDGE,"E4.sketch_text.stroke-32"),sQuery(id+"F3.wireOp",EDGE,"E4.sketch_text.stroke-33"),sQuery(id+"F3.wireOp",EDGE,"E4.sketch_text.stroke-34"),sQuery(id+"F3.wireOp",EDGE,"E4.sketch_text.stroke-35"),sQuery(id+"F3.wireOp",EDGE,"E4.sketch_text.stroke-36"),sQuery(id+"F3.wireOp",EDGE,"E4.sketch_text.stroke-37"),sQuery(id+"F3.wireOp",EDGE,"E4.sketch_text.stroke-38"),sQuery(id+"F3.wireOp",EDGE,"E4.sketch_text.stroke-39"),sQuery(id+"F3.wireOp",EDGE,"E4.sketch_text.stroke-40"),sQuery(id+"F3.wireOp",EDGE,"E4.sketch_text.stroke-41"),sQuery(id+"F3.wireOp",EDGE,"E4.sketch_text.stroke-42"),sQuery(id+"F3.wireOp",EDGE,"E4.sketch_text.stroke-43"),sQuery(id+"F3.wireOp",EDGE,"E4.sketch_text.stroke-44"),sQuery(id+"F3.wireOp",EDGE,"E4.sketch_text.stroke-45"),sQuery(id+"F3.wireOp",EDGE,"E4.sketch_text.stroke-46"),sQuery(id+"F3.wireOp",EDGE,"E4.sketch_text.stroke-47"),sQuery(id+"F3.wireOp",EDGE,"E4.sketch_text.stroke-48"),sQuery(id+"F3.wireOp",EDGE,"E4.sketch_text.stroke-49"),sQuery(id+"F3.wireOp",EDGE,"E4.sketch_text.stroke-50"),sQuery(id+"F3.wireOp",EDGE,"E4.sketch_text.stroke-51"),sQuery(id+"F3.wireOp",EDGE,"E4.sketch_text.stroke-52"),sQuery(id+"F3.wireOp",EDGE,"E4.sketch_text.stroke-53"),sQuery(id+"F3.wireOp",EDGE,"E4.sketch_text.stroke-54"),sQuery(id+"F3.wireOp",EDGE,"E4.sketch_text.stroke-55"),sQuery(id+"F3.wireOp",EDGE,"E4.sketch_text.stroke-56"),sQuery(id+"F3.wireOp",EDGE,"E4.sketch_text.stroke-57"),sQuery(id+"F3.wireOp",EDGE,"E4.sketch_text.stroke-58"),sQuery(id+"F3.wireOp",EDGE,"E4.sketch_text.stroke-59"),sQuery(id+"F3.wireOp",EDGE,"E4.sketch_text.stroke-60"),sQuery(id+"F3.wireOp",EDGE,"E4.sketch_text.stroke-61"),sQuery(id+"F3.wireOp",EDGE,"E4.sketch_text.stroke-62"),sQuery(id+"F3.wireOp",EDGE,"E4.sketch_text.stroke-71"),sQuery(id+"F3.wireOp",EDGE,"E4.sketch_text.stroke-72"),sQuery(id+"F3.wireOp",EDGE,"E4.sketch_text.stroke-73"),sQuery(id+"F3.wireOp",EDGE,"E4.sketch_text.stroke-74"),sQuery(id+"F3.wireOp",EDGE,"E4.sketch_text.stroke-75"),sQuery(id+"F3.wireOp",EDGE,"E4.sketch_text.stroke-76"),sQuery(id+"F3.wireOp",EDGE,"E4.sketch_text.stroke-77"),sQuery(id+"F3.wireOp",EDGE,"E4.sketch_text.stroke-78"),sQuery(id+"F3.wireOp",EDGE,"E4.sketch_text.stroke-79"),sQuery(id+"F3.wireOp",EDGE,"E4.sketch_text.stroke-80"),sQuery(id+"F3.wireOp",EDGE,"E4.sketch_text.stroke-81"),sQuery(id+"F3.wireOp",EDGE,"E4.sketch_text.stroke-82"),sQuery(id+"F3.wireOp",EDGE,"E4.sketch_text.stroke-83"),sQuery(id+"F3.wireOp",EDGE,"E4.sketch_text.stroke-84"),sQuery(id+"F3.wireOp",EDGE,"E4.sketch_text.stroke-85"),sQuery(id+"F3.wireOp",EDGE,"E4.sketch_text.stroke-86"),sQuery(id+"F3.wireOp",EDGE,"E4.sketch_text.stroke-87"),sQuery(id+"F3.wireOp",EDGE,"E4.sketch_text.stroke-88"),sQuery(id+"F3.wireOp",EDGE,"E4.sketch_text.stroke-89"),sQuery(id+"F3.wireOp",EDGE,"E4.sketch_text.stroke-90"),sQuery(id+"F3.wireOp",EDGE,"E4.sketch_text.stroke-91"),sQuery(id+"F3.wireOp",EDGE,"E4.sketch_text.stroke-92"),sQuery(id+"F3.wireOp",EDGE,"E4.sketch_text.stroke-93"),sQuery(id+"F3.wireOp",EDGE,"E4.sketch_text.stroke-94"),sQuery(id+"F3.wireOp",EDGE,"E4.sketch_text.stroke-95"),sQuery(id+"F3.wireOp",EDGE,"E4.sketch_text.stroke-96"),sQuery(id+"F3.wireOp",EDGE,"E4.sketch_text.stroke-97"),sQuery(id+"F3.wireOp",EDGE,"E4.sketch_text.stroke-103"),sQuery(id+"F3.wireOp",EDGE,"E4.sketch_text.stroke-104"),sQuery(id+"F3.wireOp",EDGE,"E4.sketch_text.stroke-105"),sQuery(id+"F3.wireOp",EDGE,"E4.sketch_text.stroke-106"),sQuery(id+"F3.wireOp",EDGE,"E4.sketch_text.stroke-107"),sQuery(id+"F3.wireOp",EDGE,"E4.sketch_text.stroke-108"),sQuery(id+"F3.wireOp",EDGE,"E4.sketch_text.stroke-109"),sQuery(id+"F3.wireOp",EDGE,"E4.sketch_text.stroke-110"),sQuery(id+"F3.wireOp",EDGE,"E4.sketch_text.stroke-111"),sQuery(id+"F3.wireOp",EDGE,"E4.sketch_text.stroke-112"),sQuery(id+"F3.wireOp",EDGE,"E4.sketch_text.stroke-113"),sQuery(id+"F3.wireOp",EDGE,"E4.sketch_text.stroke-114"),sQuery(id+"F3.wireOp",EDGE,"E4.sketch_text.stroke-115"),sQuery(id+"F3.wireOp",EDGE,"E4.sketch_text.stroke-116"),sQuery(id+"F3.wireOp",EDGE,"E4.sketch_text.stroke-117"),sQuery(id+"F3.wireOp",EDGE,"E4.sketch_text.stroke-118"),sQuery(id+"F3.wireOp",EDGE,"E4.sketch_text.stroke-119"),sQuery(id+"F3.wireOp",EDGE,"E4.sketch_text.stroke-120"),sQuery(id+"F3.wireOp",EDGE,"E4.sketch_text.stroke-121"),sQuery(id+"F3.wireOp",EDGE,"E4.sketch_text.stroke-122"),sQuery(id+"F3.wireOp",EDGE,"E4.sketch_text.stroke-123"),sQuery(id+"F3.wireOp",EDGE,"E4.sketch_text.stroke-124"),sQuery(id+"F3.wireOp",EDGE,"E4.sketch_text.stroke-125"),sQuery(id+"F3.wireOp",EDGE,"E4.sketch_text.stroke-126"),sQuery(id+"F3.wireOp",EDGE,"E4.sketch_text.stroke-127"),sQuery(id+"F3.wireOp",EDGE,"E4.sketch_text.stroke-128"),sQuery(id+"F3.wireOp",EDGE,"E4.sketch_text.stroke-129"),sQuery(id+"F3.wireOp",EDGE,"E4.sketch_text.stroke-130"),sQuery(id+"F3.wireOp",EDGE,"E4.sketch_text.stroke-131"),sQuery(id+"F3.wireOp",EDGE,"E4.sketch_text.stroke-132"),sQuery(id+"F3.wireOp",EDGE,"E4.sketch_text.stroke-133"),sQuery(id+"F3.wireOp",EDGE,"E4.sketch_text.stroke-134"),sQuery(id+"F3.wireOp",EDGE,"E4.sketch_text.stroke-135"),sQuery(id+"F3.wireOp",EDGE,"E4.sketch_text.stroke-136"),sQuery(id+"F3.wireOp",EDGE,"E4.sketch_text.stroke-137"),sQuery(id+"F3.wireOp",EDGE,"E4.sketch_text.stroke-138"),sQuery(id+"F3.wireOp",EDGE,"E4.sketch_text.stroke-139"),sQuery(id+"F3.wireOp",EDGE,"E4.sketch_text.stroke-140"),sQuery(id+"F3.wireOp",EDGE,"E4.sketch_text.stroke-141"),sQuery(id+"F3.wireOp",EDGE,"E4.sketch_text.stroke-142"),sQuery(id+"F3.wireOp",EDGE,"E4.sketch_text.stroke-143"),sQuery(id+"F3.wireOp",EDGE,"E4.sketch_text.stroke-144"),sQuery(id+"F3.wireOp",EDGE,"E4.sketch_text.stroke-145"),sQuery(id+"F3.wireOp",EDGE,"E4.sketch_text.stroke-146"),sQuery(id+"F3.wireOp",EDGE,"E4.sketch_text.stroke-147"),sQuery(id+"F3.wireOp",EDGE,"E4.sketch_text.stroke-148"),sQuery(id+"F3.wireOp",EDGE,"E4.sketch_text.stroke-149"),sQuery(id+"F3.wireOp",EDGE,"E4.sketch_text.stroke-150"),sQuery(id+"F3.wireOp",EDGE,"E4.sketch_text.stroke-151"),sQuery(id+"F3.wireOp",EDGE,"E4.sketch_text.stroke-152"),sQuery(id+"F3.wireOp",EDGE,"E4.sketch_text.stroke-153"),sQuery(id+"F3.wireOp",EDGE,"E4.sketch_text.stroke-159"),sQuery(id+"F3.wireOp",EDGE,"E4.sketch_text.stroke-160"),sQuery(id+"F3.wireOp",EDGE,"E4.sketch_text.stroke-161"),sQuery(id+"F3.wireOp",EDGE,"E4.sketch_text.stroke-162"),sQuery(id+"F3.wireOp",EDGE,"E4.sketch_text.stroke-163"),sQuery(id+"F3.wireOp",EDGE,"E4.sketch_text.stroke-164"),sQuery(id+"F3.wireOp",EDGE,"E4.sketch_text.stroke-165"),sQuery(id+"F3.wireOp",EDGE,"E4.sketch_text.stroke-166"),sQuery(id+"F3.wireOp",EDGE,"E4.sketch_text.stroke-167"),sQuery(id+"F3.wireOp",EDGE,"E4.sketch_text.stroke-168"),sQuery(id+"F3.wireOp",EDGE,"E4.sketch_text.stroke-169"),sQuery(id+"F3.wireOp",EDGE,"E4.sketch_text.stroke-170"),sQuery(id+"F3.wireOp",EDGE,"E4.sketch_text.stroke-171"),sQuery(id+"F3.wireOp",EDGE,"E4.sketch_text.stroke-172"),sQuery(id+"F3.wireOp",EDGE,"E4.sketch_text.stroke-173"),sQuery(id+"F3.wireOp",EDGE,"E4.sketch_text.stroke-174"),sQuery(id+"F3.wireOp",EDGE,"E4.sketch_text.stroke-175"),sQuery(id+"F3.wireOp",EDGE,"E4.sketch_text.stroke-176"),sQuery(id+"F3.wireOp",EDGE,"E4.sketch_text.stroke-177"),sQuery(id+"F3.wireOp",EDGE,"E4.sketch_text.stroke-178"),sQuery(id+"F3.wireOp",EDGE,"E4.sketch_text.stroke-179"),sQuery(id+"F3.wireOp",EDGE,"E4.sketch_text.stroke-180"),subQ2,sQuery(id+"F4.wireOp",EDGE,"E31")])],"isStart":true})]),OD(0.0)],"derivedFrom":makeQuery(id+"F1.opExtrude","CAP_EDGE",EDGE,{"disambiguationData":[OSD([subQ0])],"isStart":false})});}
            var Q26;
            {var subQ0=sQuery(id+"F0.wireOp",EDGE,"E0.top");var subQ1=sQuery(id+"F0.wireOp",EDGE,"E0.bottom");var subQ2=sQuery(id+"F4.wireOp",EDGE,"E31");Q26=makeQuery(id+"F5.boolean.opBoolean","SPLIT",EDGE,{"disambiguationData":[TD([makeQuery(id+"F1.opExtrude","CAP_FACE",FACE,{"disambiguationData":[OSD([subQ1,subQ0,sQuery(id+"F0.wireOp",EDGE,"E0.left"),sQuery(id+"F0.wireOp",EDGE,"E0.right")])],"isStart":false}),makeQuery(id+"F1.opExtrude","SWEPT_FACE",FACE,{"disambiguationData":[OSD([subQ0])]}),makeQuery(id+"F5.opExtrude","CAP_FACE",FACE,{"disambiguationData":[OSD([subQ1,sQuery(id+"F2.wireOp",EDGE,"E2.sketch_text.stroke-0"),sQuery(id+"F2.wireOp",EDGE,"E2.sketch_text.stroke-1"),sQuery(id+"F2.wireOp",EDGE,"E2.sketch_text.stroke-2"),sQuery(id+"F2.wireOp",EDGE,"E2.sketch_text.stroke-3"),sQuery(id+"F2.wireOp",EDGE,"E2.sketch_text.stroke-4"),sQuery(id+"F2.wireOp",EDGE,"E2.sketch_text.stroke-5"),sQuery(id+"F2.wireOp",EDGE,"E2.sketch_text.stroke-6"),sQuery(id+"F2.wireOp",EDGE,"E2.sketch_text.stroke-7"),sQuery(id+"F2.wireOp",EDGE,"E2.sketch_text.stroke-8"),sQuery(id+"F2.wireOp",EDGE,"E2.sketch_text.stroke-9"),sQuery(id+"F2.wireOp",EDGE,"E2.sketch_text.stroke-10"),sQuery(id+"F2.wireOp",EDGE,"E2.sketch_text.stroke-11"),sQuery(id+"F2.wireOp",EDGE,"E2.sketch_text.stroke-12"),sQuery(id+"F2.wireOp",EDGE,"E2.sketch_text.stroke-13"),sQuery(id+"F2.wireOp",EDGE,"E2.sketch_text.stroke-14"),sQuery(id+"F2.wireOp",EDGE,"E2.sketch_text.stroke-15"),sQuery(id+"F2.wireOp",EDGE,"E2.sketch_text.stroke-16"),sQuery(id+"F2.wireOp",EDGE,"E2.sketch_text.stroke-17"),sQuery(id+"F2.wireOp",EDGE,"E2.sketch_text.stroke-18"),sQuery(id+"F2.wireOp",EDGE,"E2.sketch_text.stroke-19"),sQuery(id+"F2.wireOp",EDGE,"E2.sketch_text.stroke-20"),sQuery(id+"F2.wireOp",EDGE,"E2.sketch_text.stroke-21"),sQuery(id+"F2.wireOp",EDGE,"E2.sketch_text.stroke-22"),sQuery(id+"F2.wireOp",EDGE,"E2.sketch_text.stroke-23"),sQuery(id+"F2.wireOp",EDGE,"E2.sketch_text.stroke-24"),sQuery(id+"F2.wireOp",EDGE,"E2.sketch_text.stroke-25"),sQuery(id+"F2.wireOp",EDGE,"E2.sketch_text.stroke-26"),sQuery(id+"F2.wireOp",EDGE,"E2.sketch_text.stroke-27"),sQuery(id+"F2.wireOp",EDGE,"E2.sketch_text.stroke-28"),sQuery(id+"F2.wireOp",EDGE,"E2.sketch_text.stroke-29"),sQuery(id+"F2.wireOp",EDGE,"E2.sketch_text.stroke-30"),sQuery(id+"F2.wireOp",EDGE,"E2.sketch_text.stroke-31"),sQuery(id+"F2.wireOp",EDGE,"E2.sketch_text.stroke-32"),sQuery(id+"F2.wireOp",EDGE,"E2.sketch_text.stroke-33"),sQuery(id+"F2.wireOp",EDGE,"E2.sketch_text.stroke-34"),sQuery(id+"F2.wireOp",EDGE,"E2.sketch_text.stroke-35"),sQuery(id+"F2.wireOp",EDGE,"E2.sketch_text.stroke-36"),sQuery(id+"F2.wireOp",EDGE,"E2.sketch_text.stroke-37"),sQuery(id+"F2.wireOp",EDGE,"E2.sketch_text.stroke-38"),sQuery(id+"F2.wireOp",EDGE,"E2.sketch_text.stroke-39"),sQuery(id+"F2.wireOp",EDGE,"E2.sketch_text.stroke-40"),sQuery(id+"F2.wireOp",EDGE,"E2.sketch_text.stroke-41"),sQuery(id+"F2.wireOp",EDGE,"E2.sketch_text.stroke-42"),sQuery(id+"F2.wireOp",EDGE,"E2.sketch_text.stroke-43"),sQuery(id+"F2.wireOp",EDGE,"E2.sketch_text.stroke-44"),sQuery(id+"F2.wireOp",EDGE,"E2.sketch_text.stroke-45"),sQuery(id+"F2.wireOp",EDGE,"E2.sketch_text.stroke-46"),sQuery(id+"F2.wireOp",EDGE,"E2.sketch_text.stroke-47"),sQuery(id+"F2.wireOp",EDGE,"E2.sketch_text.stroke-48"),sQuery(id+"F2.wireOp",EDGE,"E2.sketch_text.stroke-49"),sQuery(id+"F2.wireOp",EDGE,"E2.sketch_text.stroke-50"),sQuery(id+"F2.wireOp",EDGE,"E2.sketch_text.stroke-51"),sQuery(id+"F2.wireOp",EDGE,"E2.sketch_text.stroke-52"),sQuery(id+"F2.wireOp",EDGE,"E2.sketch_text.stroke-53"),sQuery(id+"F2.wireOp",EDGE,"E2.sketch_text.stroke-54"),sQuery(id+"F2.wireOp",EDGE,"E2.sketch_text.stroke-55"),sQuery(id+"F2.wireOp",EDGE,"E2.sketch_text.stroke-56"),sQuery(id+"F2.wireOp",EDGE,"E2.sketch_text.stroke-57"),sQuery(id+"F2.wireOp",EDGE,"E2.sketch_text.stroke-58"),sQuery(id+"F2.wireOp",EDGE,"E2.sketch_text.stroke-59"),sQuery(id+"F2.wireOp",EDGE,"E2.sketch_text.stroke-60"),sQuery(id+"F2.wireOp",EDGE,"E2.sketch_text.stroke-61"),sQuery(id+"F2.wireOp",EDGE,"E2.sketch_text.stroke-62"),sQuery(id+"F2.wireOp",EDGE,"E2.sketch_text.stroke-63"),sQuery(id+"F2.wireOp",EDGE,"E2.sketch_text.stroke-64"),sQuery(id+"F2.wireOp",EDGE,"E2.sketch_text.stroke-65"),sQuery(id+"F2.wireOp",EDGE,"E2.sketch_text.stroke-66"),sQuery(id+"F2.wireOp",EDGE,"E2.sketch_text.stroke-67"),sQuery(id+"F2.wireOp",EDGE,"E2.sketch_text.stroke-68"),sQuery(id+"F2.wireOp",EDGE,"E2.sketch_text.stroke-69"),sQuery(id+"F2.wireOp",EDGE,"E2.sketch_text.stroke-70"),sQuery(id+"F2.wireOp",EDGE,"E2.sketch_text.stroke-71"),sQuery(id+"F2.wireOp",EDGE,"E2.sketch_text.stroke-72"),sQuery(id+"F2.wireOp",EDGE,"E2.sketch_text.stroke-73"),sQuery(id+"F2.wireOp",EDGE,"E2.sketch_text.stroke-74"),sQuery(id+"F2.wireOp",EDGE,"E2.sketch_text.stroke-75"),sQuery(id+"F2.wireOp",EDGE,"E2.sketch_text.stroke-76"),sQuery(id+"F2.wireOp",EDGE,"E2.sketch_text.stroke-77"),sQuery(id+"F2.wireOp",EDGE,"E2.sketch_text.stroke-78"),sQuery(id+"F2.wireOp",EDGE,"E2.sketch_text.stroke-79"),sQuery(id+"F2.wireOp",EDGE,"E2.sketch_text.stroke-80"),sQuery(id+"F2.wireOp",EDGE,"E2.sketch_text.stroke-81"),sQuery(id+"F2.wireOp",EDGE,"E2.sketch_text.stroke-82"),sQuery(id+"F2.wireOp",EDGE,"E2.sketch_text.stroke-83"),sQuery(id+"F2.wireOp",EDGE,"E2.sketch_text.stroke-84"),sQuery(id+"F2.wireOp",EDGE,"E2.sketch_text.stroke-85"),sQuery(id+"F2.wireOp",EDGE,"E2.sketch_text.stroke-86"),sQuery(id+"F2.wireOp",EDGE,"E2.sketch_text.stroke-87"),sQuery(id+"F2.wireOp",EDGE,"E2.sketch_text.stroke-88"),sQuery(id+"F2.wireOp",EDGE,"E2.sketch_text.stroke-89"),sQuery(id+"F2.wireOp",EDGE,"E2.sketch_text.stroke-90"),sQuery(id+"F2.wireOp",EDGE,"E2.sketch_text.stroke-91"),sQuery(id+"F2.wireOp",EDGE,"E2.sketch_text.stroke-92"),sQuery(id+"F2.wireOp",EDGE,"E2.sketch_text.stroke-93"),sQuery(id+"F2.wireOp",EDGE,"E2.sketch_text.stroke-94"),sQuery(id+"F2.wireOp",EDGE,"E2.sketch_text.stroke-95"),sQuery(id+"F2.wireOp",EDGE,"E2.sketch_text.stroke-96"),sQuery(id+"F2.wireOp",EDGE,"E2.sketch_text.stroke-97"),sQuery(id+"F2.wireOp",EDGE,"E2.sketch_text.stroke-98"),sQuery(id+"F2.wireOp",EDGE,"E2.sketch_text.stroke-99"),sQuery(id+"F2.wireOp",EDGE,"E2.sketch_text.stroke-100"),sQuery(id+"F2.wireOp",EDGE,"E2.sketch_text.stroke-101"),sQuery(id+"F2.wireOp",EDGE,"E2.sketch_text.stroke-102"),sQuery(id+"F2.wireOp",EDGE,"E2.sketch_text.stroke-103"),sQuery(id+"F2.wireOp",EDGE,"E2.sketch_text.stroke-104"),sQuery(id+"F2.wireOp",EDGE,"E2.sketch_text.stroke-105"),sQuery(id+"F2.wireOp",EDGE,"E2.sketch_text.stroke-106"),sQuery(id+"F2.wireOp",EDGE,"E2.sketch_text.stroke-107"),sQuery(id+"F2.wireOp",EDGE,"E2.sketch_text.stroke-108"),sQuery(id+"F2.wireOp",EDGE,"E2.sketch_text.stroke-109"),sQuery(id+"F2.wireOp",EDGE,"E2.sketch_text.stroke-110"),sQuery(id+"F2.wireOp",EDGE,"E2.sketch_text.stroke-111"),sQuery(id+"F2.wireOp",EDGE,"E2.sketch_text.stroke-112"),sQuery(id+"F2.wireOp",EDGE,"E2.sketch_text.stroke-113"),sQuery(id+"F2.wireOp",EDGE,"E2.sketch_text.stroke-114"),sQuery(id+"F2.wireOp",EDGE,"E2.sketch_text.stroke-115"),sQuery(id+"F2.wireOp",EDGE,"E2.sketch_text.stroke-116"),sQuery(id+"F2.wireOp",EDGE,"E2.sketch_text.stroke-117"),sQuery(id+"F2.wireOp",EDGE,"E2.sketch_text.stroke-118"),sQuery(id+"F2.wireOp",EDGE,"E2.sketch_text.stroke-119"),sQuery(id+"F2.wireOp",EDGE,"E2.sketch_text.stroke-120"),sQuery(id+"F2.wireOp",EDGE,"E2.sketch_text.stroke-121"),sQuery(id+"F2.wireOp",EDGE,"E2.sketch_text.stroke-122"),sQuery(id+"F2.wireOp",EDGE,"E2.sketch_text.stroke-123"),sQuery(id+"F2.wireOp",EDGE,"E2.sketch_text.stroke-124"),sQuery(id+"F2.wireOp",EDGE,"E2.sketch_text.stroke-125"),sQuery(id+"F2.wireOp",EDGE,"E2.sketch_text.stroke-126"),sQuery(id+"F2.wireOp",EDGE,"E2.sketch_text.stroke-127"),sQuery(id+"F2.wireOp",EDGE,"E2.sketch_text.stroke-128"),sQuery(id+"F2.wireOp",EDGE,"E2.sketch_text.stroke-129"),sQuery(id+"F2.wireOp",EDGE,"E2.sketch_text.stroke-130"),sQuery(id+"F2.wireOp",EDGE,"E2.sketch_text.stroke-131"),sQuery(id+"F2.wireOp",EDGE,"E2.sketch_text.stroke-132"),sQuery(id+"F2.wireOp",EDGE,"E2.sketch_text.stroke-133"),sQuery(id+"F2.wireOp",EDGE,"E2.sketch_text.stroke-134"),sQuery(id+"F2.wireOp",EDGE,"E2.sketch_text.stroke-135"),sQuery(id+"F2.wireOp",EDGE,"E2.sketch_text.stroke-136"),sQuery(id+"F2.wireOp",EDGE,"E2.sketch_text.stroke-137"),sQuery(id+"F2.wireOp",EDGE,"E2.sketch_text.stroke-138"),sQuery(id+"F2.wireOp",EDGE,"E2.sketch_text.stroke-139"),sQuery(id+"F2.wireOp",EDGE,"E2.sketch_text.stroke-140"),sQuery(id+"F2.wireOp",EDGE,"E2.sketch_text.stroke-141"),sQuery(id+"F2.wireOp",EDGE,"E2.sketch_text.stroke-142"),sQuery(id+"F2.wireOp",EDGE,"E2.sketch_text.stroke-143"),sQuery(id+"F2.wireOp",EDGE,"E2.sketch_text.stroke-144"),sQuery(id+"F2.wireOp",EDGE,"E2.sketch_text.stroke-145"),sQuery(id+"F2.wireOp",EDGE,"E2.sketch_text.stroke-146"),sQuery(id+"F2.wireOp",EDGE,"E2.sketch_text.stroke-147"),sQuery(id+"F2.wireOp",EDGE,"E2.sketch_text.stroke-148"),sQuery(id+"F2.wireOp",EDGE,"E2.sketch_text.stroke-149"),sQuery(id+"F2.wireOp",EDGE,"E2.sketch_text.stroke-150"),sQuery(id+"F2.wireOp",EDGE,"E2.sketch_text.stroke-151"),sQuery(id+"F2.wireOp",EDGE,"E2.sketch_text.stroke-152"),sQuery(id+"F2.wireOp",EDGE,"E2.sketch_text.stroke-153"),sQuery(id+"F2.wireOp",EDGE,"E2.sketch_text.stroke-154"),sQuery(id+"F2.wireOp",EDGE,"E2.sketch_text.stroke-155"),sQuery(id+"F2.wireOp",EDGE,"E2.sketch_text.stroke-156"),sQuery(id+"F2.wireOp",EDGE,"E2.sketch_text.stroke-157"),sQuery(id+"F2.wireOp",EDGE,"E2.sketch_text.stroke-158"),sQuery(id+"F2.wireOp",EDGE,"E2.sketch_text.stroke-159"),sQuery(id+"F2.wireOp",EDGE,"E2.sketch_text.stroke-160"),sQuery(id+"F2.wireOp",EDGE,"E2.sketch_text.stroke-161"),sQuery(id+"F2.wireOp",EDGE,"E2.sketch_text.stroke-162"),sQuery(id+"F2.wireOp",EDGE,"E2.sketch_text.stroke-163"),sQuery(id+"F2.wireOp",EDGE,"E2.sketch_text.stroke-164"),sQuery(id+"F2.wireOp",EDGE,"E2.sketch_text.stroke-165"),sQuery(id+"F2.wireOp",EDGE,"E2.sketch_text.stroke-166"),sQuery(id+"F2.wireOp",EDGE,"E2.sketch_text.stroke-167"),sQuery(id+"F2.wireOp",EDGE,"E2.sketch_text.stroke-168"),sQuery(id+"F2.wireOp",EDGE,"E2.sketch_text.stroke-169"),sQuery(id+"F2.wireOp",EDGE,"E2.sketch_text.stroke-170"),sQuery(id+"F2.wireOp",EDGE,"E2.sketch_text.stroke-171"),sQuery(id+"F2.wireOp",EDGE,"E2.sketch_text.stroke-172"),sQuery(id+"F2.wireOp",EDGE,"E2.sketch_text.stroke-173"),sQuery(id+"F3.wireOp",EDGE,"E4.sketch_text.stroke-0"),sQuery(id+"F3.wireOp",EDGE,"E4.sketch_text.stroke-1"),sQuery(id+"F3.wireOp",EDGE,"E4.sketch_text.stroke-2"),sQuery(id+"F3.wireOp",EDGE,"E4.sketch_text.stroke-3"),sQuery(id+"F3.wireOp",EDGE,"E4.sketch_text.stroke-4"),sQuery(id+"F3.wireOp",EDGE,"E4.sketch_text.stroke-5"),sQuery(id+"F3.wireOp",EDGE,"E4.sketch_text.stroke-6"),sQuery(id+"F3.wireOp",EDGE,"E4.sketch_text.stroke-7"),sQuery(id+"F3.wireOp",EDGE,"E4.sketch_text.stroke-8"),sQuery(id+"F3.wireOp",EDGE,"E4.sketch_text.stroke-9"),sQuery(id+"F3.wireOp",EDGE,"E4.sketch_text.stroke-10"),sQuery(id+"F3.wireOp",EDGE,"E4.sketch_text.stroke-11"),sQuery(id+"F3.wireOp",EDGE,"E4.sketch_text.stroke-12"),sQuery(id+"F3.wireOp",EDGE,"E4.sketch_text.stroke-13"),sQuery(id+"F3.wireOp",EDGE,"E4.sketch_text.stroke-14"),sQuery(id+"F3.wireOp",EDGE,"E4.sketch_text.stroke-15"),sQuery(id+"F3.wireOp",EDGE,"E4.sketch_text.stroke-16"),sQuery(id+"F3.wireOp",EDGE,"E4.sketch_text.stroke-17"),sQuery(id+"F3.wireOp",EDGE,"E4.sketch_text.stroke-18"),sQuery(id+"F3.wireOp",EDGE,"E4.sketch_text.stroke-19"),sQuery(id+"F3.wireOp",EDGE,"E4.sketch_text.stroke-20"),sQuery(id+"F3.wireOp",EDGE,"E4.sketch_text.stroke-21"),sQuery(id+"F3.wireOp",EDGE,"E4.sketch_text.stroke-22"),sQuery(id+"F3.wireOp",EDGE,"E4.sketch_text.stroke-23"),sQuery(id+"F3.wireOp",EDGE,"E4.sketch_text.stroke-24"),sQuery(id+"F3.wireOp",EDGE,"E4.sketch_text.stroke-25"),sQuery(id+"F3.wireOp",EDGE,"E4.sketch_text.stroke-26"),sQuery(id+"F3.wireOp",EDGE,"E4.sketch_text.stroke-27"),sQuery(id+"F3.wireOp",EDGE,"E4.sketch_text.stroke-28"),sQuery(id+"F3.wireOp",EDGE,"E4.sketch_text.stroke-29"),sQuery(id+"F3.wireOp",EDGE,"E4.sketch_text.stroke-30"),sQuery(id+"F3.wireOp",EDGE,"E4.sketch_text.stroke-31"),sQuery(id+"F3.wireOp",EDGE,"E4.sketch_text.stroke-32"),sQuery(id+"F3.wireOp",EDGE,"E4.sketch_text.stroke-33"),sQuery(id+"F3.wireOp",EDGE,"E4.sketch_text.stroke-34"),sQuery(id+"F3.wireOp",EDGE,"E4.sketch_text.stroke-35"),sQuery(id+"F3.wireOp",EDGE,"E4.sketch_text.stroke-36"),sQuery(id+"F3.wireOp",EDGE,"E4.sketch_text.stroke-37"),sQuery(id+"F3.wireOp",EDGE,"E4.sketch_text.stroke-38"),sQuery(id+"F3.wireOp",EDGE,"E4.sketch_text.stroke-39"),sQuery(id+"F3.wireOp",EDGE,"E4.sketch_text.stroke-40"),sQuery(id+"F3.wireOp",EDGE,"E4.sketch_text.stroke-41"),sQuery(id+"F3.wireOp",EDGE,"E4.sketch_text.stroke-42"),sQuery(id+"F3.wireOp",EDGE,"E4.sketch_text.stroke-43"),sQuery(id+"F3.wireOp",EDGE,"E4.sketch_text.stroke-44"),sQuery(id+"F3.wireOp",EDGE,"E4.sketch_text.stroke-45"),sQuery(id+"F3.wireOp",EDGE,"E4.sketch_text.stroke-46"),sQuery(id+"F3.wireOp",EDGE,"E4.sketch_text.stroke-47"),sQuery(id+"F3.wireOp",EDGE,"E4.sketch_text.stroke-48"),sQuery(id+"F3.wireOp",EDGE,"E4.sketch_text.stroke-49"),sQuery(id+"F3.wireOp",EDGE,"E4.sketch_text.stroke-50"),sQuery(id+"F3.wireOp",EDGE,"E4.sketch_text.stroke-51"),sQuery(id+"F3.wireOp",EDGE,"E4.sketch_text.stroke-52"),sQuery(id+"F3.wireOp",EDGE,"E4.sketch_text.stroke-53"),sQuery(id+"F3.wireOp",EDGE,"E4.sketch_text.stroke-54"),sQuery(id+"F3.wireOp",EDGE,"E4.sketch_text.stroke-55"),sQuery(id+"F3.wireOp",EDGE,"E4.sketch_text.stroke-56"),sQuery(id+"F3.wireOp",EDGE,"E4.sketch_text.stroke-57"),sQuery(id+"F3.wireOp",EDGE,"E4.sketch_text.stroke-58"),sQuery(id+"F3.wireOp",EDGE,"E4.sketch_text.stroke-59"),sQuery(id+"F3.wireOp",EDGE,"E4.sketch_text.stroke-60"),sQuery(id+"F3.wireOp",EDGE,"E4.sketch_text.stroke-61"),sQuery(id+"F3.wireOp",EDGE,"E4.sketch_text.stroke-62"),sQuery(id+"F3.wireOp",EDGE,"E4.sketch_text.stroke-71"),sQuery(id+"F3.wireOp",EDGE,"E4.sketch_text.stroke-72"),sQuery(id+"F3.wireOp",EDGE,"E4.sketch_text.stroke-73"),sQuery(id+"F3.wireOp",EDGE,"E4.sketch_text.stroke-74"),sQuery(id+"F3.wireOp",EDGE,"E4.sketch_text.stroke-75"),sQuery(id+"F3.wireOp",EDGE,"E4.sketch_text.stroke-76"),sQuery(id+"F3.wireOp",EDGE,"E4.sketch_text.stroke-77"),sQuery(id+"F3.wireOp",EDGE,"E4.sketch_text.stroke-78"),sQuery(id+"F3.wireOp",EDGE,"E4.sketch_text.stroke-79"),sQuery(id+"F3.wireOp",EDGE,"E4.sketch_text.stroke-80"),sQuery(id+"F3.wireOp",EDGE,"E4.sketch_text.stroke-81"),sQuery(id+"F3.wireOp",EDGE,"E4.sketch_text.stroke-82"),sQuery(id+"F3.wireOp",EDGE,"E4.sketch_text.stroke-83"),sQuery(id+"F3.wireOp",EDGE,"E4.sketch_text.stroke-84"),sQuery(id+"F3.wireOp",EDGE,"E4.sketch_text.stroke-85"),sQuery(id+"F3.wireOp",EDGE,"E4.sketch_text.stroke-86"),sQuery(id+"F3.wireOp",EDGE,"E4.sketch_text.stroke-87"),sQuery(id+"F3.wireOp",EDGE,"E4.sketch_text.stroke-88"),sQuery(id+"F3.wireOp",EDGE,"E4.sketch_text.stroke-89"),sQuery(id+"F3.wireOp",EDGE,"E4.sketch_text.stroke-90"),sQuery(id+"F3.wireOp",EDGE,"E4.sketch_text.stroke-91"),sQuery(id+"F3.wireOp",EDGE,"E4.sketch_text.stroke-92"),sQuery(id+"F3.wireOp",EDGE,"E4.sketch_text.stroke-93"),sQuery(id+"F3.wireOp",EDGE,"E4.sketch_text.stroke-94"),sQuery(id+"F3.wireOp",EDGE,"E4.sketch_text.stroke-95"),sQuery(id+"F3.wireOp",EDGE,"E4.sketch_text.stroke-96"),sQuery(id+"F3.wireOp",EDGE,"E4.sketch_text.stroke-97"),sQuery(id+"F3.wireOp",EDGE,"E4.sketch_text.stroke-103"),sQuery(id+"F3.wireOp",EDGE,"E4.sketch_text.stroke-104"),sQuery(id+"F3.wireOp",EDGE,"E4.sketch_text.stroke-105"),sQuery(id+"F3.wireOp",EDGE,"E4.sketch_text.stroke-106"),sQuery(id+"F3.wireOp",EDGE,"E4.sketch_text.stroke-107"),sQuery(id+"F3.wireOp",EDGE,"E4.sketch_text.stroke-108"),sQuery(id+"F3.wireOp",EDGE,"E4.sketch_text.stroke-109"),sQuery(id+"F3.wireOp",EDGE,"E4.sketch_text.stroke-110"),sQuery(id+"F3.wireOp",EDGE,"E4.sketch_text.stroke-111"),sQuery(id+"F3.wireOp",EDGE,"E4.sketch_text.stroke-112"),sQuery(id+"F3.wireOp",EDGE,"E4.sketch_text.stroke-113"),sQuery(id+"F3.wireOp",EDGE,"E4.sketch_text.stroke-114"),sQuery(id+"F3.wireOp",EDGE,"E4.sketch_text.stroke-115"),sQuery(id+"F3.wireOp",EDGE,"E4.sketch_text.stroke-116"),sQuery(id+"F3.wireOp",EDGE,"E4.sketch_text.stroke-117"),sQuery(id+"F3.wireOp",EDGE,"E4.sketch_text.stroke-118"),sQuery(id+"F3.wireOp",EDGE,"E4.sketch_text.stroke-119"),sQuery(id+"F3.wireOp",EDGE,"E4.sketch_text.stroke-120"),sQuery(id+"F3.wireOp",EDGE,"E4.sketch_text.stroke-121"),sQuery(id+"F3.wireOp",EDGE,"E4.sketch_text.stroke-122"),sQuery(id+"F3.wireOp",EDGE,"E4.sketch_text.stroke-123"),sQuery(id+"F3.wireOp",EDGE,"E4.sketch_text.stroke-124"),sQuery(id+"F3.wireOp",EDGE,"E4.sketch_text.stroke-125"),sQuery(id+"F3.wireOp",EDGE,"E4.sketch_text.stroke-126"),sQuery(id+"F3.wireOp",EDGE,"E4.sketch_text.stroke-127"),sQuery(id+"F3.wireOp",EDGE,"E4.sketch_text.stroke-128"),sQuery(id+"F3.wireOp",EDGE,"E4.sketch_text.stroke-129"),sQuery(id+"F3.wireOp",EDGE,"E4.sketch_text.stroke-130"),sQuery(id+"F3.wireOp",EDGE,"E4.sketch_text.stroke-131"),sQuery(id+"F3.wireOp",EDGE,"E4.sketch_text.stroke-132"),sQuery(id+"F3.wireOp",EDGE,"E4.sketch_text.stroke-133"),sQuery(id+"F3.wireOp",EDGE,"E4.sketch_text.stroke-134"),sQuery(id+"F3.wireOp",EDGE,"E4.sketch_text.stroke-135"),sQuery(id+"F3.wireOp",EDGE,"E4.sketch_text.stroke-136"),sQuery(id+"F3.wireOp",EDGE,"E4.sketch_text.stroke-137"),sQuery(id+"F3.wireOp",EDGE,"E4.sketch_text.stroke-138"),sQuery(id+"F3.wireOp",EDGE,"E4.sketch_text.stroke-139"),sQuery(id+"F3.wireOp",EDGE,"E4.sketch_text.stroke-140"),sQuery(id+"F3.wireOp",EDGE,"E4.sketch_text.stroke-141"),sQuery(id+"F3.wireOp",EDGE,"E4.sketch_text.stroke-142"),sQuery(id+"F3.wireOp",EDGE,"E4.sketch_text.stroke-143"),sQuery(id+"F3.wireOp",EDGE,"E4.sketch_text.stroke-144"),sQuery(id+"F3.wireOp",EDGE,"E4.sketch_text.stroke-145"),sQuery(id+"F3.wireOp",EDGE,"E4.sketch_text.stroke-146"),sQuery(id+"F3.wireOp",EDGE,"E4.sketch_text.stroke-147"),sQuery(id+"F3.wireOp",EDGE,"E4.sketch_text.stroke-148"),sQuery(id+"F3.wireOp",EDGE,"E4.sketch_text.stroke-149"),sQuery(id+"F3.wireOp",EDGE,"E4.sketch_text.stroke-150"),sQuery(id+"F3.wireOp",EDGE,"E4.sketch_text.stroke-151"),sQuery(id+"F3.wireOp",EDGE,"E4.sketch_text.stroke-152"),sQuery(id+"F3.wireOp",EDGE,"E4.sketch_text.stroke-153"),sQuery(id+"F3.wireOp",EDGE,"E4.sketch_text.stroke-159"),sQuery(id+"F3.wireOp",EDGE,"E4.sketch_text.stroke-160"),sQuery(id+"F3.wireOp",EDGE,"E4.sketch_text.stroke-161"),sQuery(id+"F3.wireOp",EDGE,"E4.sketch_text.stroke-162"),sQuery(id+"F3.wireOp",EDGE,"E4.sketch_text.stroke-163"),sQuery(id+"F3.wireOp",EDGE,"E4.sketch_text.stroke-164"),sQuery(id+"F3.wireOp",EDGE,"E4.sketch_text.stroke-165"),sQuery(id+"F3.wireOp",EDGE,"E4.sketch_text.stroke-166"),sQuery(id+"F3.wireOp",EDGE,"E4.sketch_text.stroke-167"),sQuery(id+"F3.wireOp",EDGE,"E4.sketch_text.stroke-168"),sQuery(id+"F3.wireOp",EDGE,"E4.sketch_text.stroke-169"),sQuery(id+"F3.wireOp",EDGE,"E4.sketch_text.stroke-170"),sQuery(id+"F3.wireOp",EDGE,"E4.sketch_text.stroke-171"),sQuery(id+"F3.wireOp",EDGE,"E4.sketch_text.stroke-172"),sQuery(id+"F3.wireOp",EDGE,"E4.sketch_text.stroke-173"),sQuery(id+"F3.wireOp",EDGE,"E4.sketch_text.stroke-174"),sQuery(id+"F3.wireOp",EDGE,"E4.sketch_text.stroke-175"),sQuery(id+"F3.wireOp",EDGE,"E4.sketch_text.stroke-176"),sQuery(id+"F3.wireOp",EDGE,"E4.sketch_text.stroke-177"),sQuery(id+"F3.wireOp",EDGE,"E4.sketch_text.stroke-178"),sQuery(id+"F3.wireOp",EDGE,"E4.sketch_text.stroke-179"),sQuery(id+"F3.wireOp",EDGE,"E4.sketch_text.stroke-180"),sQuery(id+"F4.wireOp",EDGE,"E30"),subQ2])],"isStart":true}),makeQuery(id+"F5.opExtrude","SWEPT_FACE",FACE,{"disambiguationData":[OSD([subQ2])]})]),OD(0.0)],"derivedFrom":makeQuery(id+"F1.opExtrude","CAP_EDGE",EDGE,{"disambiguationData":[OSD([subQ0])],"isStart":false})});}
            var Q27;
            {var subQ0=sQuery(id+"F0.wireOp",EDGE,"E0.top");var subQ1=sQuery(id+"F0.wireOp",EDGE,"E0.bottom");var subQ2=sQuery(id+"F4.wireOp",EDGE,"E31");Q27=makeQuery(id+"F5.boolean.opBoolean","SPLIT",EDGE,{"disambiguationData":[TD([makeQuery(id+"F1.opExtrude","CAP_FACE",FACE,{"disambiguationData":[OSD([subQ1,subQ0,sQuery(id+"F0.wireOp",EDGE,"E0.left"),sQuery(id+"F0.wireOp",EDGE,"E0.right")])],"isStart":false}),makeQuery(id+"F1.opExtrude","SWEPT_FACE",FACE,{"disambiguationData":[OSD([subQ0])]}),makeQuery(id+"F5.opExtrude","CAP_FACE",FACE,{"disambiguationData":[OSD([subQ1,sQuery(id+"F2.wireOp",EDGE,"E2.sketch_text.stroke-0"),sQuery(id+"F2.wireOp",EDGE,"E2.sketch_text.stroke-1"),sQuery(id+"F2.wireOp",EDGE,"E2.sketch_text.stroke-2"),sQuery(id+"F2.wireOp",EDGE,"E2.sketch_text.stroke-3"),sQuery(id+"F2.wireOp",EDGE,"E2.sketch_text.stroke-4"),sQuery(id+"F2.wireOp",EDGE,"E2.sketch_text.stroke-5"),sQuery(id+"F2.wireOp",EDGE,"E2.sketch_text.stroke-6"),sQuery(id+"F2.wireOp",EDGE,"E2.sketch_text.stroke-7"),sQuery(id+"F2.wireOp",EDGE,"E2.sketch_text.stroke-8"),sQuery(id+"F2.wireOp",EDGE,"E2.sketch_text.stroke-9"),sQuery(id+"F2.wireOp",EDGE,"E2.sketch_text.stroke-10"),sQuery(id+"F2.wireOp",EDGE,"E2.sketch_text.stroke-11"),sQuery(id+"F2.wireOp",EDGE,"E2.sketch_text.stroke-12"),sQuery(id+"F2.wireOp",EDGE,"E2.sketch_text.stroke-13"),sQuery(id+"F2.wireOp",EDGE,"E2.sketch_text.stroke-14"),sQuery(id+"F2.wireOp",EDGE,"E2.sketch_text.stroke-15"),sQuery(id+"F2.wireOp",EDGE,"E2.sketch_text.stroke-16"),sQuery(id+"F2.wireOp",EDGE,"E2.sketch_text.stroke-17"),sQuery(id+"F2.wireOp",EDGE,"E2.sketch_text.stroke-18"),sQuery(id+"F2.wireOp",EDGE,"E2.sketch_text.stroke-19"),sQuery(id+"F2.wireOp",EDGE,"E2.sketch_text.stroke-20"),sQuery(id+"F2.wireOp",EDGE,"E2.sketch_text.stroke-21"),sQuery(id+"F2.wireOp",EDGE,"E2.sketch_text.stroke-22"),sQuery(id+"F2.wireOp",EDGE,"E2.sketch_text.stroke-23"),sQuery(id+"F2.wireOp",EDGE,"E2.sketch_text.stroke-24"),sQuery(id+"F2.wireOp",EDGE,"E2.sketch_text.stroke-25"),sQuery(id+"F2.wireOp",EDGE,"E2.sketch_text.stroke-26"),sQuery(id+"F2.wireOp",EDGE,"E2.sketch_text.stroke-27"),sQuery(id+"F2.wireOp",EDGE,"E2.sketch_text.stroke-28"),sQuery(id+"F2.wireOp",EDGE,"E2.sketch_text.stroke-29"),sQuery(id+"F2.wireOp",EDGE,"E2.sketch_text.stroke-30"),sQuery(id+"F2.wireOp",EDGE,"E2.sketch_text.stroke-31"),sQuery(id+"F2.wireOp",EDGE,"E2.sketch_text.stroke-32"),sQuery(id+"F2.wireOp",EDGE,"E2.sketch_text.stroke-33"),sQuery(id+"F2.wireOp",EDGE,"E2.sketch_text.stroke-34"),sQuery(id+"F2.wireOp",EDGE,"E2.sketch_text.stroke-35"),sQuery(id+"F2.wireOp",EDGE,"E2.sketch_text.stroke-36"),sQuery(id+"F2.wireOp",EDGE,"E2.sketch_text.stroke-37"),sQuery(id+"F2.wireOp",EDGE,"E2.sketch_text.stroke-38"),sQuery(id+"F2.wireOp",EDGE,"E2.sketch_text.stroke-39"),sQuery(id+"F2.wireOp",EDGE,"E2.sketch_text.stroke-40"),sQuery(id+"F2.wireOp",EDGE,"E2.sketch_text.stroke-41"),sQuery(id+"F2.wireOp",EDGE,"E2.sketch_text.stroke-42"),sQuery(id+"F2.wireOp",EDGE,"E2.sketch_text.stroke-43"),sQuery(id+"F2.wireOp",EDGE,"E2.sketch_text.stroke-44"),sQuery(id+"F2.wireOp",EDGE,"E2.sketch_text.stroke-45"),sQuery(id+"F2.wireOp",EDGE,"E2.sketch_text.stroke-46"),sQuery(id+"F2.wireOp",EDGE,"E2.sketch_text.stroke-47"),sQuery(id+"F2.wireOp",EDGE,"E2.sketch_text.stroke-48"),sQuery(id+"F2.wireOp",EDGE,"E2.sketch_text.stroke-49"),sQuery(id+"F2.wireOp",EDGE,"E2.sketch_text.stroke-50"),sQuery(id+"F2.wireOp",EDGE,"E2.sketch_text.stroke-51"),sQuery(id+"F2.wireOp",EDGE,"E2.sketch_text.stroke-52"),sQuery(id+"F2.wireOp",EDGE,"E2.sketch_text.stroke-53"),sQuery(id+"F2.wireOp",EDGE,"E2.sketch_text.stroke-54"),sQuery(id+"F2.wireOp",EDGE,"E2.sketch_text.stroke-55"),sQuery(id+"F2.wireOp",EDGE,"E2.sketch_text.stroke-56"),sQuery(id+"F2.wireOp",EDGE,"E2.sketch_text.stroke-57"),sQuery(id+"F2.wireOp",EDGE,"E2.sketch_text.stroke-58"),sQuery(id+"F2.wireOp",EDGE,"E2.sketch_text.stroke-59"),sQuery(id+"F2.wireOp",EDGE,"E2.sketch_text.stroke-60"),sQuery(id+"F2.wireOp",EDGE,"E2.sketch_text.stroke-61"),sQuery(id+"F2.wireOp",EDGE,"E2.sketch_text.stroke-62"),sQuery(id+"F2.wireOp",EDGE,"E2.sketch_text.stroke-63"),sQuery(id+"F2.wireOp",EDGE,"E2.sketch_text.stroke-64"),sQuery(id+"F2.wireOp",EDGE,"E2.sketch_text.stroke-65"),sQuery(id+"F2.wireOp",EDGE,"E2.sketch_text.stroke-66"),sQuery(id+"F2.wireOp",EDGE,"E2.sketch_text.stroke-67"),sQuery(id+"F2.wireOp",EDGE,"E2.sketch_text.stroke-68"),sQuery(id+"F2.wireOp",EDGE,"E2.sketch_text.stroke-69"),sQuery(id+"F2.wireOp",EDGE,"E2.sketch_text.stroke-70"),sQuery(id+"F2.wireOp",EDGE,"E2.sketch_text.stroke-71"),sQuery(id+"F2.wireOp",EDGE,"E2.sketch_text.stroke-72"),sQuery(id+"F2.wireOp",EDGE,"E2.sketch_text.stroke-73"),sQuery(id+"F2.wireOp",EDGE,"E2.sketch_text.stroke-74"),sQuery(id+"F2.wireOp",EDGE,"E2.sketch_text.stroke-75"),sQuery(id+"F2.wireOp",EDGE,"E2.sketch_text.stroke-76"),sQuery(id+"F2.wireOp",EDGE,"E2.sketch_text.stroke-77"),sQuery(id+"F2.wireOp",EDGE,"E2.sketch_text.stroke-78"),sQuery(id+"F2.wireOp",EDGE,"E2.sketch_text.stroke-79"),sQuery(id+"F2.wireOp",EDGE,"E2.sketch_text.stroke-80"),sQuery(id+"F2.wireOp",EDGE,"E2.sketch_text.stroke-81"),sQuery(id+"F2.wireOp",EDGE,"E2.sketch_text.stroke-82"),sQuery(id+"F2.wireOp",EDGE,"E2.sketch_text.stroke-83"),sQuery(id+"F2.wireOp",EDGE,"E2.sketch_text.stroke-84"),sQuery(id+"F2.wireOp",EDGE,"E2.sketch_text.stroke-85"),sQuery(id+"F2.wireOp",EDGE,"E2.sketch_text.stroke-86"),sQuery(id+"F2.wireOp",EDGE,"E2.sketch_text.stroke-87"),sQuery(id+"F2.wireOp",EDGE,"E2.sketch_text.stroke-88"),sQuery(id+"F2.wireOp",EDGE,"E2.sketch_text.stroke-89"),sQuery(id+"F2.wireOp",EDGE,"E2.sketch_text.stroke-90"),sQuery(id+"F2.wireOp",EDGE,"E2.sketch_text.stroke-91"),sQuery(id+"F2.wireOp",EDGE,"E2.sketch_text.stroke-92"),sQuery(id+"F2.wireOp",EDGE,"E2.sketch_text.stroke-93"),sQuery(id+"F2.wireOp",EDGE,"E2.sketch_text.stroke-94"),sQuery(id+"F2.wireOp",EDGE,"E2.sketch_text.stroke-95"),sQuery(id+"F2.wireOp",EDGE,"E2.sketch_text.stroke-96"),sQuery(id+"F2.wireOp",EDGE,"E2.sketch_text.stroke-97"),sQuery(id+"F2.wireOp",EDGE,"E2.sketch_text.stroke-98"),sQuery(id+"F2.wireOp",EDGE,"E2.sketch_text.stroke-99"),sQuery(id+"F2.wireOp",EDGE,"E2.sketch_text.stroke-100"),sQuery(id+"F2.wireOp",EDGE,"E2.sketch_text.stroke-101"),sQuery(id+"F2.wireOp",EDGE,"E2.sketch_text.stroke-102"),sQuery(id+"F2.wireOp",EDGE,"E2.sketch_text.stroke-103"),sQuery(id+"F2.wireOp",EDGE,"E2.sketch_text.stroke-104"),sQuery(id+"F2.wireOp",EDGE,"E2.sketch_text.stroke-105"),sQuery(id+"F2.wireOp",EDGE,"E2.sketch_text.stroke-106"),sQuery(id+"F2.wireOp",EDGE,"E2.sketch_text.stroke-107"),sQuery(id+"F2.wireOp",EDGE,"E2.sketch_text.stroke-108"),sQuery(id+"F2.wireOp",EDGE,"E2.sketch_text.stroke-109"),sQuery(id+"F2.wireOp",EDGE,"E2.sketch_text.stroke-110"),sQuery(id+"F2.wireOp",EDGE,"E2.sketch_text.stroke-111"),sQuery(id+"F2.wireOp",EDGE,"E2.sketch_text.stroke-112"),sQuery(id+"F2.wireOp",EDGE,"E2.sketch_text.stroke-113"),sQuery(id+"F2.wireOp",EDGE,"E2.sketch_text.stroke-114"),sQuery(id+"F2.wireOp",EDGE,"E2.sketch_text.stroke-115"),sQuery(id+"F2.wireOp",EDGE,"E2.sketch_text.stroke-116"),sQuery(id+"F2.wireOp",EDGE,"E2.sketch_text.stroke-117"),sQuery(id+"F2.wireOp",EDGE,"E2.sketch_text.stroke-118"),sQuery(id+"F2.wireOp",EDGE,"E2.sketch_text.stroke-119"),sQuery(id+"F2.wireOp",EDGE,"E2.sketch_text.stroke-120"),sQuery(id+"F2.wireOp",EDGE,"E2.sketch_text.stroke-121"),sQuery(id+"F2.wireOp",EDGE,"E2.sketch_text.stroke-122"),sQuery(id+"F2.wireOp",EDGE,"E2.sketch_text.stroke-123"),sQuery(id+"F2.wireOp",EDGE,"E2.sketch_text.stroke-124"),sQuery(id+"F2.wireOp",EDGE,"E2.sketch_text.stroke-125"),sQuery(id+"F2.wireOp",EDGE,"E2.sketch_text.stroke-126"),sQuery(id+"F2.wireOp",EDGE,"E2.sketch_text.stroke-127"),sQuery(id+"F2.wireOp",EDGE,"E2.sketch_text.stroke-128"),sQuery(id+"F2.wireOp",EDGE,"E2.sketch_text.stroke-129"),sQuery(id+"F2.wireOp",EDGE,"E2.sketch_text.stroke-130"),sQuery(id+"F2.wireOp",EDGE,"E2.sketch_text.stroke-131"),sQuery(id+"F2.wireOp",EDGE,"E2.sketch_text.stroke-132"),sQuery(id+"F2.wireOp",EDGE,"E2.sketch_text.stroke-133"),sQuery(id+"F2.wireOp",EDGE,"E2.sketch_text.stroke-134"),sQuery(id+"F2.wireOp",EDGE,"E2.sketch_text.stroke-135"),sQuery(id+"F2.wireOp",EDGE,"E2.sketch_text.stroke-136"),sQuery(id+"F2.wireOp",EDGE,"E2.sketch_text.stroke-137"),sQuery(id+"F2.wireOp",EDGE,"E2.sketch_text.stroke-138"),sQuery(id+"F2.wireOp",EDGE,"E2.sketch_text.stroke-139"),sQuery(id+"F2.wireOp",EDGE,"E2.sketch_text.stroke-140"),sQuery(id+"F2.wireOp",EDGE,"E2.sketch_text.stroke-141"),sQuery(id+"F2.wireOp",EDGE,"E2.sketch_text.stroke-142"),sQuery(id+"F2.wireOp",EDGE,"E2.sketch_text.stroke-143"),sQuery(id+"F2.wireOp",EDGE,"E2.sketch_text.stroke-144"),sQuery(id+"F2.wireOp",EDGE,"E2.sketch_text.stroke-145"),sQuery(id+"F2.wireOp",EDGE,"E2.sketch_text.stroke-146"),sQuery(id+"F2.wireOp",EDGE,"E2.sketch_text.stroke-147"),sQuery(id+"F2.wireOp",EDGE,"E2.sketch_text.stroke-148"),sQuery(id+"F2.wireOp",EDGE,"E2.sketch_text.stroke-149"),sQuery(id+"F2.wireOp",EDGE,"E2.sketch_text.stroke-150"),sQuery(id+"F2.wireOp",EDGE,"E2.sketch_text.stroke-151"),sQuery(id+"F2.wireOp",EDGE,"E2.sketch_text.stroke-152"),sQuery(id+"F2.wireOp",EDGE,"E2.sketch_text.stroke-153"),sQuery(id+"F2.wireOp",EDGE,"E2.sketch_text.stroke-154"),sQuery(id+"F2.wireOp",EDGE,"E2.sketch_text.stroke-155"),sQuery(id+"F2.wireOp",EDGE,"E2.sketch_text.stroke-156"),sQuery(id+"F2.wireOp",EDGE,"E2.sketch_text.stroke-157"),sQuery(id+"F2.wireOp",EDGE,"E2.sketch_text.stroke-158"),sQuery(id+"F2.wireOp",EDGE,"E2.sketch_text.stroke-159"),sQuery(id+"F2.wireOp",EDGE,"E2.sketch_text.stroke-160"),sQuery(id+"F2.wireOp",EDGE,"E2.sketch_text.stroke-161"),sQuery(id+"F2.wireOp",EDGE,"E2.sketch_text.stroke-162"),sQuery(id+"F2.wireOp",EDGE,"E2.sketch_text.stroke-163"),sQuery(id+"F2.wireOp",EDGE,"E2.sketch_text.stroke-164"),sQuery(id+"F2.wireOp",EDGE,"E2.sketch_text.stroke-165"),sQuery(id+"F2.wireOp",EDGE,"E2.sketch_text.stroke-166"),sQuery(id+"F2.wireOp",EDGE,"E2.sketch_text.stroke-167"),sQuery(id+"F2.wireOp",EDGE,"E2.sketch_text.stroke-168"),sQuery(id+"F2.wireOp",EDGE,"E2.sketch_text.stroke-169"),sQuery(id+"F2.wireOp",EDGE,"E2.sketch_text.stroke-170"),sQuery(id+"F2.wireOp",EDGE,"E2.sketch_text.stroke-171"),sQuery(id+"F2.wireOp",EDGE,"E2.sketch_text.stroke-172"),sQuery(id+"F2.wireOp",EDGE,"E2.sketch_text.stroke-173"),sQuery(id+"F3.wireOp",EDGE,"E4.sketch_text.stroke-0"),sQuery(id+"F3.wireOp",EDGE,"E4.sketch_text.stroke-1"),sQuery(id+"F3.wireOp",EDGE,"E4.sketch_text.stroke-2"),sQuery(id+"F3.wireOp",EDGE,"E4.sketch_text.stroke-3"),sQuery(id+"F3.wireOp",EDGE,"E4.sketch_text.stroke-4"),sQuery(id+"F3.wireOp",EDGE,"E4.sketch_text.stroke-5"),sQuery(id+"F3.wireOp",EDGE,"E4.sketch_text.stroke-6"),sQuery(id+"F3.wireOp",EDGE,"E4.sketch_text.stroke-7"),sQuery(id+"F3.wireOp",EDGE,"E4.sketch_text.stroke-8"),sQuery(id+"F3.wireOp",EDGE,"E4.sketch_text.stroke-9"),sQuery(id+"F3.wireOp",EDGE,"E4.sketch_text.stroke-10"),sQuery(id+"F3.wireOp",EDGE,"E4.sketch_text.stroke-11"),sQuery(id+"F3.wireOp",EDGE,"E4.sketch_text.stroke-12"),sQuery(id+"F3.wireOp",EDGE,"E4.sketch_text.stroke-13"),sQuery(id+"F3.wireOp",EDGE,"E4.sketch_text.stroke-14"),sQuery(id+"F3.wireOp",EDGE,"E4.sketch_text.stroke-15"),sQuery(id+"F3.wireOp",EDGE,"E4.sketch_text.stroke-16"),sQuery(id+"F3.wireOp",EDGE,"E4.sketch_text.stroke-17"),sQuery(id+"F3.wireOp",EDGE,"E4.sketch_text.stroke-18"),sQuery(id+"F3.wireOp",EDGE,"E4.sketch_text.stroke-19"),sQuery(id+"F3.wireOp",EDGE,"E4.sketch_text.stroke-20"),sQuery(id+"F3.wireOp",EDGE,"E4.sketch_text.stroke-21"),sQuery(id+"F3.wireOp",EDGE,"E4.sketch_text.stroke-22"),sQuery(id+"F3.wireOp",EDGE,"E4.sketch_text.stroke-23"),sQuery(id+"F3.wireOp",EDGE,"E4.sketch_text.stroke-24"),sQuery(id+"F3.wireOp",EDGE,"E4.sketch_text.stroke-25"),sQuery(id+"F3.wireOp",EDGE,"E4.sketch_text.stroke-26"),sQuery(id+"F3.wireOp",EDGE,"E4.sketch_text.stroke-27"),sQuery(id+"F3.wireOp",EDGE,"E4.sketch_text.stroke-28"),sQuery(id+"F3.wireOp",EDGE,"E4.sketch_text.stroke-29"),sQuery(id+"F3.wireOp",EDGE,"E4.sketch_text.stroke-30"),sQuery(id+"F3.wireOp",EDGE,"E4.sketch_text.stroke-31"),sQuery(id+"F3.wireOp",EDGE,"E4.sketch_text.stroke-32"),sQuery(id+"F3.wireOp",EDGE,"E4.sketch_text.stroke-33"),sQuery(id+"F3.wireOp",EDGE,"E4.sketch_text.stroke-34"),sQuery(id+"F3.wireOp",EDGE,"E4.sketch_text.stroke-35"),sQuery(id+"F3.wireOp",EDGE,"E4.sketch_text.stroke-36"),sQuery(id+"F3.wireOp",EDGE,"E4.sketch_text.stroke-37"),sQuery(id+"F3.wireOp",EDGE,"E4.sketch_text.stroke-38"),sQuery(id+"F3.wireOp",EDGE,"E4.sketch_text.stroke-39"),sQuery(id+"F3.wireOp",EDGE,"E4.sketch_text.stroke-40"),sQuery(id+"F3.wireOp",EDGE,"E4.sketch_text.stroke-41"),sQuery(id+"F3.wireOp",EDGE,"E4.sketch_text.stroke-42"),sQuery(id+"F3.wireOp",EDGE,"E4.sketch_text.stroke-43"),sQuery(id+"F3.wireOp",EDGE,"E4.sketch_text.stroke-44"),sQuery(id+"F3.wireOp",EDGE,"E4.sketch_text.stroke-45"),sQuery(id+"F3.wireOp",EDGE,"E4.sketch_text.stroke-46"),sQuery(id+"F3.wireOp",EDGE,"E4.sketch_text.stroke-47"),sQuery(id+"F3.wireOp",EDGE,"E4.sketch_text.stroke-48"),sQuery(id+"F3.wireOp",EDGE,"E4.sketch_text.stroke-49"),sQuery(id+"F3.wireOp",EDGE,"E4.sketch_text.stroke-50"),sQuery(id+"F3.wireOp",EDGE,"E4.sketch_text.stroke-51"),sQuery(id+"F3.wireOp",EDGE,"E4.sketch_text.stroke-52"),sQuery(id+"F3.wireOp",EDGE,"E4.sketch_text.stroke-53"),sQuery(id+"F3.wireOp",EDGE,"E4.sketch_text.stroke-54"),sQuery(id+"F3.wireOp",EDGE,"E4.sketch_text.stroke-55"),sQuery(id+"F3.wireOp",EDGE,"E4.sketch_text.stroke-56"),sQuery(id+"F3.wireOp",EDGE,"E4.sketch_text.stroke-57"),sQuery(id+"F3.wireOp",EDGE,"E4.sketch_text.stroke-58"),sQuery(id+"F3.wireOp",EDGE,"E4.sketch_text.stroke-59"),sQuery(id+"F3.wireOp",EDGE,"E4.sketch_text.stroke-60"),sQuery(id+"F3.wireOp",EDGE,"E4.sketch_text.stroke-61"),sQuery(id+"F3.wireOp",EDGE,"E4.sketch_text.stroke-62"),sQuery(id+"F3.wireOp",EDGE,"E4.sketch_text.stroke-71"),sQuery(id+"F3.wireOp",EDGE,"E4.sketch_text.stroke-72"),sQuery(id+"F3.wireOp",EDGE,"E4.sketch_text.stroke-73"),sQuery(id+"F3.wireOp",EDGE,"E4.sketch_text.stroke-74"),sQuery(id+"F3.wireOp",EDGE,"E4.sketch_text.stroke-75"),sQuery(id+"F3.wireOp",EDGE,"E4.sketch_text.stroke-76"),sQuery(id+"F3.wireOp",EDGE,"E4.sketch_text.stroke-77"),sQuery(id+"F3.wireOp",EDGE,"E4.sketch_text.stroke-78"),sQuery(id+"F3.wireOp",EDGE,"E4.sketch_text.stroke-79"),sQuery(id+"F3.wireOp",EDGE,"E4.sketch_text.stroke-80"),sQuery(id+"F3.wireOp",EDGE,"E4.sketch_text.stroke-81"),sQuery(id+"F3.wireOp",EDGE,"E4.sketch_text.stroke-82"),sQuery(id+"F3.wireOp",EDGE,"E4.sketch_text.stroke-83"),sQuery(id+"F3.wireOp",EDGE,"E4.sketch_text.stroke-84"),sQuery(id+"F3.wireOp",EDGE,"E4.sketch_text.stroke-85"),sQuery(id+"F3.wireOp",EDGE,"E4.sketch_text.stroke-86"),sQuery(id+"F3.wireOp",EDGE,"E4.sketch_text.stroke-87"),sQuery(id+"F3.wireOp",EDGE,"E4.sketch_text.stroke-88"),sQuery(id+"F3.wireOp",EDGE,"E4.sketch_text.stroke-89"),sQuery(id+"F3.wireOp",EDGE,"E4.sketch_text.stroke-90"),sQuery(id+"F3.wireOp",EDGE,"E4.sketch_text.stroke-91"),sQuery(id+"F3.wireOp",EDGE,"E4.sketch_text.stroke-92"),sQuery(id+"F3.wireOp",EDGE,"E4.sketch_text.stroke-93"),sQuery(id+"F3.wireOp",EDGE,"E4.sketch_text.stroke-94"),sQuery(id+"F3.wireOp",EDGE,"E4.sketch_text.stroke-95"),sQuery(id+"F3.wireOp",EDGE,"E4.sketch_text.stroke-96"),sQuery(id+"F3.wireOp",EDGE,"E4.sketch_text.stroke-97"),sQuery(id+"F3.wireOp",EDGE,"E4.sketch_text.stroke-103"),sQuery(id+"F3.wireOp",EDGE,"E4.sketch_text.stroke-104"),sQuery(id+"F3.wireOp",EDGE,"E4.sketch_text.stroke-105"),sQuery(id+"F3.wireOp",EDGE,"E4.sketch_text.stroke-106"),sQuery(id+"F3.wireOp",EDGE,"E4.sketch_text.stroke-107"),sQuery(id+"F3.wireOp",EDGE,"E4.sketch_text.stroke-108"),sQuery(id+"F3.wireOp",EDGE,"E4.sketch_text.stroke-109"),sQuery(id+"F3.wireOp",EDGE,"E4.sketch_text.stroke-110"),sQuery(id+"F3.wireOp",EDGE,"E4.sketch_text.stroke-111"),sQuery(id+"F3.wireOp",EDGE,"E4.sketch_text.stroke-112"),sQuery(id+"F3.wireOp",EDGE,"E4.sketch_text.stroke-113"),sQuery(id+"F3.wireOp",EDGE,"E4.sketch_text.stroke-114"),sQuery(id+"F3.wireOp",EDGE,"E4.sketch_text.stroke-115"),sQuery(id+"F3.wireOp",EDGE,"E4.sketch_text.stroke-116"),sQuery(id+"F3.wireOp",EDGE,"E4.sketch_text.stroke-117"),sQuery(id+"F3.wireOp",EDGE,"E4.sketch_text.stroke-118"),sQuery(id+"F3.wireOp",EDGE,"E4.sketch_text.stroke-119"),sQuery(id+"F3.wireOp",EDGE,"E4.sketch_text.stroke-120"),sQuery(id+"F3.wireOp",EDGE,"E4.sketch_text.stroke-121"),sQuery(id+"F3.wireOp",EDGE,"E4.sketch_text.stroke-122"),sQuery(id+"F3.wireOp",EDGE,"E4.sketch_text.stroke-123"),sQuery(id+"F3.wireOp",EDGE,"E4.sketch_text.stroke-124"),sQuery(id+"F3.wireOp",EDGE,"E4.sketch_text.stroke-125"),sQuery(id+"F3.wireOp",EDGE,"E4.sketch_text.stroke-126"),sQuery(id+"F3.wireOp",EDGE,"E4.sketch_text.stroke-127"),sQuery(id+"F3.wireOp",EDGE,"E4.sketch_text.stroke-128"),sQuery(id+"F3.wireOp",EDGE,"E4.sketch_text.stroke-129"),sQuery(id+"F3.wireOp",EDGE,"E4.sketch_text.stroke-130"),sQuery(id+"F3.wireOp",EDGE,"E4.sketch_text.stroke-131"),sQuery(id+"F3.wireOp",EDGE,"E4.sketch_text.stroke-132"),sQuery(id+"F3.wireOp",EDGE,"E4.sketch_text.stroke-133"),sQuery(id+"F3.wireOp",EDGE,"E4.sketch_text.stroke-134"),sQuery(id+"F3.wireOp",EDGE,"E4.sketch_text.stroke-135"),sQuery(id+"F3.wireOp",EDGE,"E4.sketch_text.stroke-136"),sQuery(id+"F3.wireOp",EDGE,"E4.sketch_text.stroke-137"),sQuery(id+"F3.wireOp",EDGE,"E4.sketch_text.stroke-138"),sQuery(id+"F3.wireOp",EDGE,"E4.sketch_text.stroke-139"),sQuery(id+"F3.wireOp",EDGE,"E4.sketch_text.stroke-140"),sQuery(id+"F3.wireOp",EDGE,"E4.sketch_text.stroke-141"),sQuery(id+"F3.wireOp",EDGE,"E4.sketch_text.stroke-142"),sQuery(id+"F3.wireOp",EDGE,"E4.sketch_text.stroke-143"),sQuery(id+"F3.wireOp",EDGE,"E4.sketch_text.stroke-144"),sQuery(id+"F3.wireOp",EDGE,"E4.sketch_text.stroke-145"),sQuery(id+"F3.wireOp",EDGE,"E4.sketch_text.stroke-146"),sQuery(id+"F3.wireOp",EDGE,"E4.sketch_text.stroke-147"),sQuery(id+"F3.wireOp",EDGE,"E4.sketch_text.stroke-148"),sQuery(id+"F3.wireOp",EDGE,"E4.sketch_text.stroke-149"),sQuery(id+"F3.wireOp",EDGE,"E4.sketch_text.stroke-150"),sQuery(id+"F3.wireOp",EDGE,"E4.sketch_text.stroke-151"),sQuery(id+"F3.wireOp",EDGE,"E4.sketch_text.stroke-152"),sQuery(id+"F3.wireOp",EDGE,"E4.sketch_text.stroke-153"),sQuery(id+"F3.wireOp",EDGE,"E4.sketch_text.stroke-159"),sQuery(id+"F3.wireOp",EDGE,"E4.sketch_text.stroke-160"),sQuery(id+"F3.wireOp",EDGE,"E4.sketch_text.stroke-161"),sQuery(id+"F3.wireOp",EDGE,"E4.sketch_text.stroke-162"),sQuery(id+"F3.wireOp",EDGE,"E4.sketch_text.stroke-163"),sQuery(id+"F3.wireOp",EDGE,"E4.sketch_text.stroke-164"),sQuery(id+"F3.wireOp",EDGE,"E4.sketch_text.stroke-165"),sQuery(id+"F3.wireOp",EDGE,"E4.sketch_text.stroke-166"),sQuery(id+"F3.wireOp",EDGE,"E4.sketch_text.stroke-167"),sQuery(id+"F3.wireOp",EDGE,"E4.sketch_text.stroke-168"),sQuery(id+"F3.wireOp",EDGE,"E4.sketch_text.stroke-169"),sQuery(id+"F3.wireOp",EDGE,"E4.sketch_text.stroke-170"),sQuery(id+"F3.wireOp",EDGE,"E4.sketch_text.stroke-171"),sQuery(id+"F3.wireOp",EDGE,"E4.sketch_text.stroke-172"),sQuery(id+"F3.wireOp",EDGE,"E4.sketch_text.stroke-173"),sQuery(id+"F3.wireOp",EDGE,"E4.sketch_text.stroke-174"),sQuery(id+"F3.wireOp",EDGE,"E4.sketch_text.stroke-175"),sQuery(id+"F3.wireOp",EDGE,"E4.sketch_text.stroke-176"),sQuery(id+"F3.wireOp",EDGE,"E4.sketch_text.stroke-177"),sQuery(id+"F3.wireOp",EDGE,"E4.sketch_text.stroke-178"),sQuery(id+"F3.wireOp",EDGE,"E4.sketch_text.stroke-179"),sQuery(id+"F3.wireOp",EDGE,"E4.sketch_text.stroke-180"),sQuery(id+"F4.wireOp",EDGE,"E30"),subQ2])],"isStart":true}),makeQuery(id+"F5.opExtrude","SWEPT_FACE",FACE,{"disambiguationData":[OSD([subQ2])]})]),OD(1.0)],"derivedFrom":makeQuery(id+"F1.opExtrude","CAP_EDGE",EDGE,{"disambiguationData":[OSD([subQ0])],"isStart":false})});}
            fillet(context, id + "F6", {"entities" : qUnion([Q0, Q1, Q2, Q3, Q4, Q5, Q6, Q7, Q8, Q9, Q10, Q11, Q12, Q13, Q14, Q15, Q16, Q17, Q18, Q19, Q20, Q21, Q22, Q23, Q24, Q25, Q26, Q27]), "radius" : 5.08 * mm, "tangentPropagation" : true, "allowEdgeOverflow" : false});
        }
    });
